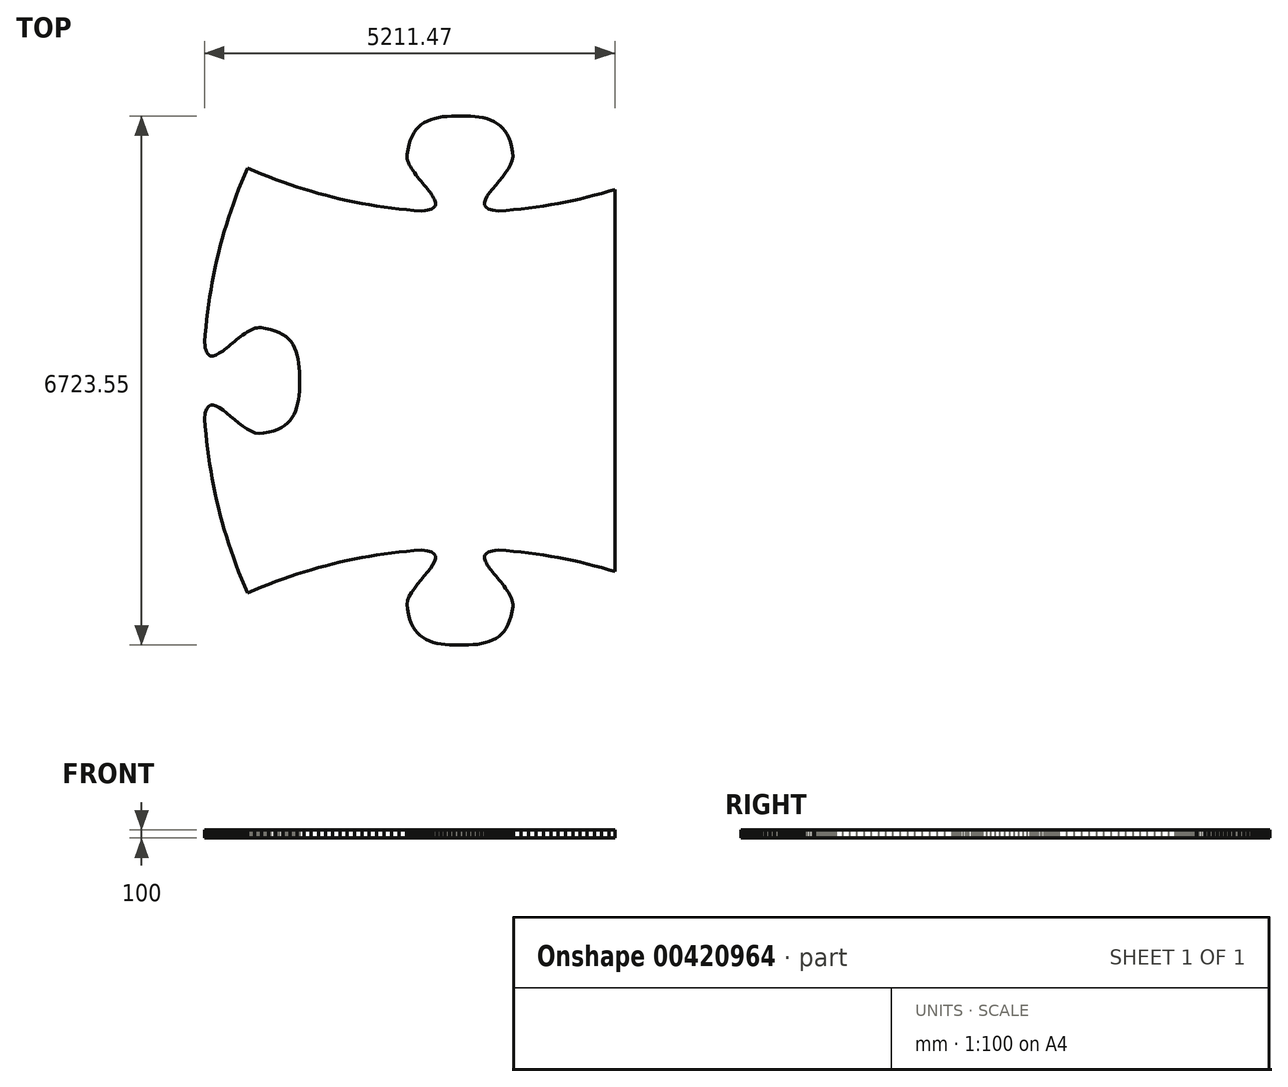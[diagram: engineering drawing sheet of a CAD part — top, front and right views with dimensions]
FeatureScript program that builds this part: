
annotation { "Feature Type Name" : "Feature", "Feature Type Description" : "" }
export const myFeature = defineFeature(function(context is Context, id is Id, definition is map)
    precondition{}
    {
        {
            var Q0;
            Q0=qCreatedBy(makeId("Top.planeOp"),FACE);
            var sketch = newSketch(context, id + "F0", { "sketchPlane" : qUnion([Q0])});
            skLineSegment(sketch, "E0", {"start": v(-1670.47, -7506.33) * mm, "end": v(-1710.93, -7498.83) * mm});
            skLineSegment(sketch, "E1", {"start": v(-1710.93, -7498.83) * mm, "end": v(-1764.8, -7491.94) * mm});
            skLineSegment(sketch, "E2", {"start": v(-1764.8, -7491.94) * mm, "end": v(-1821.32, -7487.35) * mm});
            skLineSegment(sketch, "E3", {"start": v(-1821.32, -7487.35) * mm, "end": v(-1880.41, -7484.72) * mm});
            skLineSegment(sketch, "E4", {"start": v(-1880.41, -7484.72) * mm, "end": v(-1941.99, -7483.74) * mm});
            skLineSegment(sketch, "E5", {"start": v(-1941.99, -7483.74) * mm, "end": v(-2004.44, -7484.15) * mm});
            skLineSegment(sketch, "E6", {"start": v(-2004.44, -7484.15) * mm, "end": v(-2064.53, -7486.08) * mm});
            skLineSegment(sketch, "E7", {"start": v(-2064.53, -7486.08) * mm, "end": v(-2122.08, -7489.85) * mm});
            skLineSegment(sketch, "E8", {"start": v(-2122.08, -7489.85) * mm, "end": v(-2177, -7495.78) * mm});
            skLineSegment(sketch, "E9", {"start": v(-2177, -7495.78) * mm, "end": v(-2229.24, -7504.19) * mm});
            skLineSegment(sketch, "E10", {"start": v(-2229.24, -7504.19) * mm, "end": v(-2278.7, -7515.4) * mm});
            skLineSegment(sketch, "E11", {"start": v(-2278.7, -7515.4) * mm, "end": v(-2325.3, -7529.72) * mm});
            skLineSegment(sketch, "E12", {"start": v(-2325.3, -7529.72) * mm, "end": v(-2368.99, -7547.48) * mm});
            skLineSegment(sketch, "E13", {"start": v(-2368.99, -7547.48) * mm, "end": v(-2409.66, -7568.99) * mm});
            skLineSegment(sketch, "E14", {"start": v(-2409.66, -7568.99) * mm, "end": v(-2447.25, -7594.57) * mm});
            skLineSegment(sketch, "E15", {"start": v(-2447.25, -7594.57) * mm, "end": v(-2481.68, -7624.55) * mm});
            skLineSegment(sketch, "E16", {"start": v(-2481.68, -7624.55) * mm, "end": v(-2512.86, -7659.24) * mm});
            skLineSegment(sketch, "E17", {"start": v(-2512.86, -7659.24) * mm, "end": v(-2540.73, -7698.95) * mm});
            skLineSegment(sketch, "E18", {"start": v(-2540.73, -7698.95) * mm, "end": v(-2565.2, -7744.01) * mm});
            skLineSegment(sketch, "E19", {"start": v(-2565.2, -7744.01) * mm, "end": v(-2586.21, -7794.75) * mm});
            skLineSegment(sketch, "E20", {"start": v(-2586.21, -7794.75) * mm, "end": v(-2603.67, -7851.46) * mm});
            skLineSegment(sketch, "E21", {"start": v(-2603.67, -7851.46) * mm, "end": v(-2617.5, -7914.48) * mm});
            skLineSegment(sketch, "E22", {"start": v(-2617.5, -7914.48) * mm, "end": v(-2626.4, -7974.43) * mm});
            skLineSegment(sketch, "E23", {"start": v(-2626.4, -7974.43) * mm, "end": v(-2626.92, -7998.7) * mm});
            skLineSegment(sketch, "E24", {"start": v(-2626.92, -7998.7) * mm, "end": v(-2624.12, -8023.51) * mm});
            skLineSegment(sketch, "E25", {"start": v(-2624.12, -8023.51) * mm, "end": v(-2618.27, -8048.78) * mm});
            skLineSegment(sketch, "E26", {"start": v(-2618.27, -8048.78) * mm, "end": v(-2609.65, -8074.45) * mm});
            skLineSegment(sketch, "E27", {"start": v(-2609.65, -8074.45) * mm, "end": v(-2598.53, -8100.44) * mm});
            skLineSegment(sketch, "E28", {"start": v(-2598.53, -8100.44) * mm, "end": v(-2585.17, -8126.69) * mm});
            skLineSegment(sketch, "E29", {"start": v(-2585.17, -8126.69) * mm, "end": v(-2569.85, -8153.13) * mm});
            skLineSegment(sketch, "E30", {"start": v(-2569.85, -8153.13) * mm, "end": v(-2552.84, -8179.69) * mm});
            skLineSegment(sketch, "E31", {"start": v(-2552.84, -8179.69) * mm, "end": v(-2534.4, -8206.3) * mm});
            skLineSegment(sketch, "E32", {"start": v(-2534.4, -8206.3) * mm, "end": v(-2514.82, -8232.9) * mm});
            skLineSegment(sketch, "E33", {"start": v(-2514.82, -8232.9) * mm, "end": v(-2494.35, -8259.4) * mm});
            skLineSegment(sketch, "E34", {"start": v(-2494.35, -8259.4) * mm, "end": v(-2473.27, -8285.76) * mm});
            skLineSegment(sketch, "E35", {"start": v(-2473.27, -8285.76) * mm, "end": v(-2451.84, -8311.9) * mm});
            skLineSegment(sketch, "E36", {"start": v(-2451.84, -8311.9) * mm, "end": v(-2430.34, -8337.75) * mm});
            skLineSegment(sketch, "E37", {"start": v(-2430.34, -8337.75) * mm, "end": v(-2409.04, -8363.24) * mm});
            skLineSegment(sketch, "E38", {"start": v(-2409.04, -8363.24) * mm, "end": v(-2388.21, -8388.3) * mm});
            skLineSegment(sketch, "E39", {"start": v(-2388.21, -8388.3) * mm, "end": v(-2368.12, -8412.86) * mm});
            skLineSegment(sketch, "E40", {"start": v(-2368.12, -8412.86) * mm, "end": v(-2349.03, -8436.87) * mm});
            skLineSegment(sketch, "E41", {"start": v(-2349.03, -8436.87) * mm, "end": v(-2331.22, -8460.23) * mm});
            skLineSegment(sketch, "E42", {"start": v(-2331.22, -8460.23) * mm, "end": v(-2314.96, -8482.9) * mm});
            skLineSegment(sketch, "E43", {"start": v(-2314.96, -8482.9) * mm, "end": v(-2300.52, -8504.8) * mm});
            skLineSegment(sketch, "E44", {"start": v(-2300.52, -8504.8) * mm, "end": v(-2288.17, -8525.86) * mm});
            skLineSegment(sketch, "E45", {"start": v(-2288.17, -8525.86) * mm, "end": v(-2278.17, -8546.02) * mm});
            skLineSegment(sketch, "E46", {"start": v(-2278.17, -8546.02) * mm, "end": v(-2270.8, -8565.2) * mm});
            skLineSegment(sketch, "E47", {"start": v(-2270.8, -8565.2) * mm, "end": v(-2266.34, -8583.33) * mm});
            skLineSegment(sketch, "E48", {"start": v(-2266.34, -8583.33) * mm, "end": v(-2265.04, -8600.36) * mm});
            skLineSegment(sketch, "E49", {"start": v(-2265.04, -8600.36) * mm, "end": v(-2267.18, -8616.2) * mm});
            skLineSegment(sketch, "E50", {"start": v(-2267.18, -8616.2) * mm, "end": v(-2273.03, -8630.8) * mm});
            skLineSegment(sketch, "E51", {"start": v(-2273.03, -8630.8) * mm, "end": v(-2282.86, -8644.07) * mm});
            skLineSegment(sketch, "E52", {"start": v(-2282.86, -8644.07) * mm, "end": v(-2296.94, -8655.96) * mm});
            skLineSegment(sketch, "E53", {"start": v(-2296.94, -8655.96) * mm, "end": v(-2315.54, -8666.4) * mm});
            skLineSegment(sketch, "E54", {"start": v(-2315.54, -8666.4) * mm, "end": v(-2338.93, -8675.31) * mm});
            skLineSegment(sketch, "E55", {"start": v(-2338.93, -8675.31) * mm, "end": v(-2367.38, -8682.63) * mm});
            skLineSegment(sketch, "E56", {"start": v(-2367.38, -8682.63) * mm, "end": v(-2401.15, -8688.3) * mm});
            skLineSegment(sketch, "E57", {"start": v(-2401.15, -8688.3) * mm, "end": v(-2440.53, -8692.23) * mm});
            skLineSegment(sketch, "E58", {"start": v(1692.6, -7812.46) * mm, "end": v(1735.9, -7800.77) * mm});
            skLineSegment(sketch, "E59", {"start": v(1735.9, -7800.77) * mm, "end": v(1827.3, -7777.51) * mm});
            skLineSegment(sketch, "E60", {"start": v(1827.3, -7777.51) * mm, "end": v(1919.05, -7755.6) * mm});
            skLineSegment(sketch, "E61", {"start": v(1919.05, -7755.6) * mm, "end": v(2011.14, -7735) * mm});
            skLineSegment(sketch, "E62", {"start": v(2011.14, -7735) * mm, "end": v(2103.62, -7715.73) * mm});
            skLineSegment(sketch, "E63", {"start": v(2103.62, -7715.73) * mm, "end": v(2196.5, -7697.78) * mm});
            skLineSegment(sketch, "E64", {"start": v(2196.5, -7697.78) * mm, "end": v(2289.83, -7681.14) * mm});
            skLineSegment(sketch, "E65", {"start": v(2289.83, -7681.14) * mm, "end": v(2383.6, -7665.8) * mm});
            skLineSegment(sketch, "E66", {"start": v(2383.6, -7665.8) * mm, "end": v(2477.88, -7651.75) * mm});
            skLineSegment(sketch, "E67", {"start": v(2477.88, -7651.75) * mm, "end": v(2572.66, -7639) * mm});
            skLineSegment(sketch, "E68", {"start": v(2572.66, -7639) * mm, "end": v(2667.99, -7627.53) * mm});
            skLineSegment(sketch, "E69", {"start": v(2667.99, -7627.53) * mm, "end": v(2763.88, -7617.33) * mm});
            skLineSegment(sketch, "E70", {"start": v(2763.88, -7617.33) * mm, "end": v(2860.36, -7608.4) * mm});
            skLineSegment(sketch, "E71", {"start": v(2860.36, -7608.4) * mm, "end": v(2957.46, -7600.75) * mm});
            skLineSegment(sketch, "E72", {"start": v(-1468.4, -12998.74) * mm, "end": v(-1371.3, -13006.4) * mm});
            skLineSegment(sketch, "E73", {"start": v(-1371.3, -13006.4) * mm, "end": v(-1274.82, -13015.32) * mm});
            skLineSegment(sketch, "E74", {"start": v(-1274.82, -13015.32) * mm, "end": v(-1193.26, -13024) * mm});
            skLineSegment(sketch, "E75", {"start": v(382.53, -13398.19) * mm, "end": v(386.12, -13399.5) * mm});
            skLineSegment(sketch, "E76", {"start": v(386.12, -13399.5) * mm, "end": v(475.85, -13433.68) * mm});
            skLineSegment(sketch, "E77", {"start": v(475.85, -13433.68) * mm, "end": v(565.5, -13469.25) * mm});
            skLineSegment(sketch, "E78", {"start": v(565.5, -13469.25) * mm, "end": v(655.08, -13506.22) * mm});
            skLineSegment(sketch, "E79", {"start": v(655.08, -13506.22) * mm, "end": v(744.62, -13544.6) * mm});
            skLineSegment(sketch, "E80", {"start": v(-1670.47, 3289.71) * mm, "end": v(-1710.93, 3297.22) * mm});
            skLineSegment(sketch, "E81", {"start": v(-1710.93, 3297.22) * mm, "end": v(-1764.8, 3304.1) * mm});
            skLineSegment(sketch, "E82", {"start": v(-1764.8, 3304.1) * mm, "end": v(-1821.32, 3308.7) * mm});
            skLineSegment(sketch, "E83", {"start": v(-1821.32, 3308.7) * mm, "end": v(-1880.41, 3311.32) * mm});
            skLineSegment(sketch, "E84", {"start": v(-1880.41, 3311.32) * mm, "end": v(-1941.99, 3312.3) * mm});
            skLineSegment(sketch, "E85", {"start": v(-1941.99, 3312.3) * mm, "end": v(-2004.44, 3311.9) * mm});
            skLineSegment(sketch, "E86", {"start": v(-2004.44, 3311.9) * mm, "end": v(-2064.53, 3309.97) * mm});
            skLineSegment(sketch, "E87", {"start": v(-2064.53, 3309.97) * mm, "end": v(-2122.08, 3306.2) * mm});
            skLineSegment(sketch, "E88", {"start": v(-2122.08, 3306.2) * mm, "end": v(-2177, 3300.26) * mm});
            skLineSegment(sketch, "E89", {"start": v(-2177, 3300.26) * mm, "end": v(-2229.24, 3291.85) * mm});
            skLineSegment(sketch, "E90", {"start": v(-2229.24, 3291.85) * mm, "end": v(-2278.7, 3280.64) * mm});
            skLineSegment(sketch, "E91", {"start": v(-2278.7, 3280.64) * mm, "end": v(-2325.3, 3266.32) * mm});
            skLineSegment(sketch, "E92", {"start": v(-2325.3, 3266.32) * mm, "end": v(-2368.99, 3248.56) * mm});
            skLineSegment(sketch, "E93", {"start": v(-2368.99, 3248.56) * mm, "end": v(-2409.66, 3227.05) * mm});
            skLineSegment(sketch, "E94", {"start": v(-2409.66, 3227.05) * mm, "end": v(-2447.25, 3201.46) * mm});
            skLineSegment(sketch, "E95", {"start": v(-2447.25, 3201.46) * mm, "end": v(-2481.68, 3171.48) * mm});
            skLineSegment(sketch, "E96", {"start": v(-2481.68, 3171.48) * mm, "end": v(-2512.86, 3136.79) * mm});
            skLineSegment(sketch, "E97", {"start": v(-2512.86, 3136.79) * mm, "end": v(-2540.73, 3097.07) * mm});
            skLineSegment(sketch, "E98", {"start": v(-2540.73, 3097.07) * mm, "end": v(-2565.2, 3052) * mm});
            skLineSegment(sketch, "E99", {"start": v(-2565.2, 3052) * mm, "end": v(-2586.21, 3001.26) * mm});
            skLineSegment(sketch, "E100", {"start": v(-2586.21, 3001.26) * mm, "end": v(-2603.67, 2944.54) * mm});
            skLineSegment(sketch, "E101", {"start": v(-2603.67, 2944.54) * mm, "end": v(-2617.5, 2881.5) * mm});
            skLineSegment(sketch, "E102", {"start": v(-2617.5, 2881.5) * mm, "end": v(-2626.4, 2821.55) * mm});
            skLineSegment(sketch, "E103", {"start": v(-2626.4, 2821.55) * mm, "end": v(-2626.92, 2797.29) * mm});
            skLineSegment(sketch, "E104", {"start": v(-2626.92, 2797.29) * mm, "end": v(-2624.12, 2772.5) * mm});
            skLineSegment(sketch, "E105", {"start": v(-2624.12, 2772.5) * mm, "end": v(-2618.27, 2747.24) * mm});
            skLineSegment(sketch, "E106", {"start": v(-2618.27, 2747.24) * mm, "end": v(-2609.65, 2721.58) * mm});
            skLineSegment(sketch, "E107", {"start": v(-2609.65, 2721.58) * mm, "end": v(-2598.53, 2695.6) * mm});
            skLineSegment(sketch, "E108", {"start": v(-2598.53, 2695.6) * mm, "end": v(-2585.17, 2669.36) * mm});
            skLineSegment(sketch, "E109", {"start": v(-2585.17, 2669.36) * mm, "end": v(-2569.85, 2642.93) * mm});
            skLineSegment(sketch, "E110", {"start": v(-2569.85, 2642.93) * mm, "end": v(-2552.84, 2616.37) * mm});
            skLineSegment(sketch, "E111", {"start": v(-2552.84, 2616.37) * mm, "end": v(-2534.4, 2589.76) * mm});
            skLineSegment(sketch, "E112", {"start": v(-2534.4, 2589.76) * mm, "end": v(-2514.82, 2563.17) * mm});
            skLineSegment(sketch, "E113", {"start": v(-2514.82, 2563.17) * mm, "end": v(-2494.35, 2536.66) * mm});
            skLineSegment(sketch, "E114", {"start": v(-2494.35, 2536.66) * mm, "end": v(-2473.27, 2510.3) * mm});
            skLineSegment(sketch, "E115", {"start": v(-2473.27, 2510.3) * mm, "end": v(-2451.84, 2484.16) * mm});
            skLineSegment(sketch, "E116", {"start": v(-2451.84, 2484.16) * mm, "end": v(-2430.34, 2458.31) * mm});
            skLineSegment(sketch, "E117", {"start": v(-2430.34, 2458.31) * mm, "end": v(-2409.04, 2432.82) * mm});
            skLineSegment(sketch, "E118", {"start": v(-2409.04, 2432.82) * mm, "end": v(-2388.21, 2407.76) * mm});
            skLineSegment(sketch, "E119", {"start": v(-2388.21, 2407.76) * mm, "end": v(-2368.12, 2383.19) * mm});
            skLineSegment(sketch, "E120", {"start": v(-2368.12, 2383.19) * mm, "end": v(-2349.03, 2359.18) * mm});
            skLineSegment(sketch, "E121", {"start": v(-2349.03, 2359.18) * mm, "end": v(-2331.22, 2335.8) * mm});
            skLineSegment(sketch, "E122", {"start": v(-2331.22, 2335.8) * mm, "end": v(-2314.96, 2313.14) * mm});
            skLineSegment(sketch, "E123", {"start": v(-2314.96, 2313.14) * mm, "end": v(-2300.52, 2291.23) * mm});
            skLineSegment(sketch, "E124", {"start": v(-2300.52, 2291.23) * mm, "end": v(-2288.17, 2270.17) * mm});
            skLineSegment(sketch, "E125", {"start": v(-2288.17, 2270.17) * mm, "end": v(-2278.17, 2250) * mm});
            skLineSegment(sketch, "E126", {"start": v(-2278.17, 2250) * mm, "end": v(-2270.8, 2230.82) * mm});
            skLineSegment(sketch, "E127", {"start": v(-2270.8, 2230.82) * mm, "end": v(-2266.34, 2212.68) * mm});
            skLineSegment(sketch, "E128", {"start": v(-2266.34, 2212.68) * mm, "end": v(-2265.04, 2195.65) * mm});
            skLineSegment(sketch, "E129", {"start": v(-2265.04, 2195.65) * mm, "end": v(-2267.18, 2179.8) * mm});
            skLineSegment(sketch, "E130", {"start": v(-2267.18, 2179.8) * mm, "end": v(-2273.03, 2165.2) * mm});
            skLineSegment(sketch, "E131", {"start": v(-2273.03, 2165.2) * mm, "end": v(-2282.86, 2151.92) * mm});
            skLineSegment(sketch, "E132", {"start": v(-2282.86, 2151.92) * mm, "end": v(-2296.94, 2140.03) * mm});
            skLineSegment(sketch, "E133", {"start": v(-2296.94, 2140.03) * mm, "end": v(-2315.54, 2129.59) * mm});
            skLineSegment(sketch, "E134", {"start": v(-2315.54, 2129.59) * mm, "end": v(-2338.93, 2120.67) * mm});
            skLineSegment(sketch, "E135", {"start": v(-2338.93, 2120.67) * mm, "end": v(-2367.38, 2113.35) * mm});
            skLineSegment(sketch, "E136", {"start": v(-2367.38, 2113.35) * mm, "end": v(-2401.15, 2107.68) * mm});
            skLineSegment(sketch, "E137", {"start": v(-2401.15, 2107.68) * mm, "end": v(-2440.53, 2103.75) * mm});
            skLineSegment(sketch, "E138", {"start": v(-2440.53, 2103.75) * mm, "end": v(-2537.63, 2111.41) * mm});
            skLineSegment(sketch, "E139", {"start": v(-2537.63, 2111.41) * mm, "end": v(-2634.11, 2120.34) * mm});
            skLineSegment(sketch, "E140", {"start": v(-2634.11, 2120.34) * mm, "end": v(-2730, 2130.54) * mm});
            skLineSegment(sketch, "E141", {"start": v(-2730, 2130.54) * mm, "end": v(-2825.33, 2142.02) * mm});
            skLineSegment(sketch, "E142", {"start": v(-2825.33, 2142.02) * mm, "end": v(-2920.11, 2154.78) * mm});
            skLineSegment(sketch, "E143", {"start": v(-2920.11, 2154.78) * mm, "end": v(-3014.38, 2168.83) * mm});
            skLineSegment(sketch, "E144", {"start": v(-3014.38, 2168.83) * mm, "end": v(-3108.17, 2184.18) * mm});
            skLineSegment(sketch, "E145", {"start": v(-3108.17, 2184.18) * mm, "end": v(-3201.5, 2200.83) * mm});
            skLineSegment(sketch, "E146", {"start": v(-3201.5, 2200.83) * mm, "end": v(-3294.38, 2218.79) * mm});
            skLineSegment(sketch, "E147", {"start": v(-3294.38, 2218.79) * mm, "end": v(-3386.86, 2238.06) * mm});
            skLineSegment(sketch, "E148", {"start": v(-3386.86, 2238.06) * mm, "end": v(-3478.96, 2258.66) * mm});
            skLineSegment(sketch, "E149", {"start": v(-3478.96, 2258.66) * mm, "end": v(-3570.7, 2280.59) * mm});
            skLineSegment(sketch, "E150", {"start": v(-3570.7, 2280.59) * mm, "end": v(-3662.12, 2303.85) * mm});
            skLineSegment(sketch, "E151", {"start": v(-3662.12, 2303.85) * mm, "end": v(-3753.24, 2328.45) * mm});
            skLineSegment(sketch, "E152", {"start": v(-3753.24, 2328.45) * mm, "end": v(-3844.08, 2354.4) * mm});
            skLineSegment(sketch, "E153", {"start": v(-3844.08, 2354.4) * mm, "end": v(-3934.66, 2381.7) * mm});
            skLineSegment(sketch, "E154", {"start": v(-3934.66, 2381.7) * mm, "end": v(-4025.03, 2410.37) * mm});
            skLineSegment(sketch, "E155", {"start": v(-4025.03, 2410.37) * mm, "end": v(-4115.2, 2440.4) * mm});
            skLineSegment(sketch, "E156", {"start": v(-4115.2, 2440.4) * mm, "end": v(-4205.2, 2471.8) * mm});
            skLineSegment(sketch, "E157", {"start": v(-4205.2, 2471.8) * mm, "end": v(-4295.05, 2504.58) * mm});
            skLineSegment(sketch, "E158", {"start": v(-4295.05, 2504.58) * mm, "end": v(-4384.79, 2538.75) * mm});
            skLineSegment(sketch, "E159", {"start": v(-4384.79, 2538.75) * mm, "end": v(-4474.44, 2574.3) * mm});
            skLineSegment(sketch, "E160", {"start": v(-4474.44, 2574.3) * mm, "end": v(-4564.02, 2611.26) * mm});
            skLineSegment(sketch, "E161", {"start": v(-4564.02, 2611.26) * mm, "end": v(-4653.56, 2649.62) * mm});
            skLineSegment(sketch, "E162", {"start": v(-4653.56, 2649.62) * mm, "end": v(-4691.92, 2560.08) * mm});
            skLineSegment(sketch, "E163", {"start": v(-4691.92, 2560.08) * mm, "end": v(-4728.87, 2470.5) * mm});
            skLineSegment(sketch, "E164", {"start": v(-4728.87, 2470.5) * mm, "end": v(-4764.42, 2380.86) * mm});
            skLineSegment(sketch, "E165", {"start": v(-4764.42, 2380.86) * mm, "end": v(-4798.58, 2291.13) * mm});
            skLineSegment(sketch, "E166", {"start": v(-4798.58, 2291.13) * mm, "end": v(-4831.36, 2201.28) * mm});
            skLineSegment(sketch, "E167", {"start": v(-4831.36, 2201.28) * mm, "end": v(-4862.75, 2111.29) * mm});
            skLineSegment(sketch, "E168", {"start": v(-4862.75, 2111.29) * mm, "end": v(-4892.77, 2021.13) * mm});
            skLineSegment(sketch, "E169", {"start": v(-4892.77, 2021.13) * mm, "end": v(-4921.42, 1930.77) * mm});
            skLineSegment(sketch, "E170", {"start": v(-4921.42, 1930.77) * mm, "end": v(-4948.72, 1840.19) * mm});
            skLineSegment(sketch, "E171", {"start": v(-4948.72, 1840.19) * mm, "end": v(-4974.65, 1749.36) * mm});
            skLineSegment(sketch, "E172", {"start": v(-4974.65, 1749.36) * mm, "end": v(-4999.24, 1658.25) * mm});
            skLineSegment(sketch, "E173", {"start": v(-4999.24, 1658.25) * mm, "end": v(-5022.5, 1566.84) * mm});
            skLineSegment(sketch, "E174", {"start": v(-5022.5, 1566.84) * mm, "end": v(-5044.4, 1475.1) * mm});
            skLineSegment(sketch, "E175", {"start": v(-5044.4, 1475.1) * mm, "end": v(-5065, 1383) * mm});
            skLineSegment(sketch, "E176", {"start": v(-5065, 1383) * mm, "end": v(-5084.26, 1290.53) * mm});
            skLineSegment(sketch, "E177", {"start": v(-5084.26, 1290.53) * mm, "end": v(-5102.2, 1197.64) * mm});
            skLineSegment(sketch, "E178", {"start": v(-5102.2, 1197.64) * mm, "end": v(-5118.85, 1104.31) * mm});
            skLineSegment(sketch, "E179", {"start": v(-5118.85, 1104.31) * mm, "end": v(-5134.19, 1010.53) * mm});
            skLineSegment(sketch, "E180", {"start": v(-5134.19, 1010.53) * mm, "end": v(-5148.23, 916.25) * mm});
            skLineSegment(sketch, "E181", {"start": v(-5148.23, 916.25) * mm, "end": v(-5160.98, 821.46) * mm});
            skLineSegment(sketch, "E182", {"start": v(-5160.98, 821.46) * mm, "end": v(-5172.45, 726.12) * mm});
            skLineSegment(sketch, "E183", {"start": v(-5172.45, 726.12) * mm, "end": v(-5182.65, 630.22) * mm});
            skLineSegment(sketch, "E184", {"start": v(-5182.65, 630.22) * mm, "end": v(-5191.57, 533.71) * mm});
            skLineSegment(sketch, "E185", {"start": v(-5191.57, 533.71) * mm, "end": v(-5199.24, 436.6) * mm});
            skLineSegment(sketch, "E186", {"start": v(-5199.24, 436.6) * mm, "end": v(-5189.63, 363.44) * mm});
            skLineSegment(sketch, "E187", {"start": v(-5189.63, 363.44) * mm, "end": v(-5173.39, 311.6) * mm});
            skLineSegment(sketch, "E188", {"start": v(-5173.39, 311.6) * mm, "end": v(-5151.06, 278.94) * mm});
            skLineSegment(sketch, "E189", {"start": v(-5151.06, 278.94) * mm, "end": v(-5123.18, 263.27) * mm});
            skLineSegment(sketch, "E190", {"start": v(-5123.18, 263.27) * mm, "end": v(-5090.31, 262.43) * mm});
            skLineSegment(sketch, "E191", {"start": v(-5090.31, 262.43) * mm, "end": v(-5053, 274.28) * mm});
            skLineSegment(sketch, "E192", {"start": v(-5053, 274.28) * mm, "end": v(-5011.78, 296.63) * mm});
            skLineSegment(sketch, "E193", {"start": v(-5011.78, 296.63) * mm, "end": v(-4967.22, 327.34) * mm});
            skLineSegment(sketch, "E194", {"start": v(-4967.22, 327.34) * mm, "end": v(-4919.85, 364.24) * mm});
            skLineSegment(sketch, "E195", {"start": v(-4919.85, 364.24) * mm, "end": v(-4870.22, 405.17) * mm});
            skLineSegment(sketch, "E196", {"start": v(-4870.22, 405.17) * mm, "end": v(-4818.9, 447.97) * mm});
            skLineSegment(sketch, "E197", {"start": v(-4818.9, 447.97) * mm, "end": v(-4766.4, 490.48) * mm});
            skLineSegment(sketch, "E198", {"start": v(-4766.4, 490.48) * mm, "end": v(-4713.3, 530.53) * mm});
            skLineSegment(sketch, "E199", {"start": v(-4713.3, 530.53) * mm, "end": v(-4660.13, 565.96) * mm});
            skLineSegment(sketch, "E200", {"start": v(-4660.13, 565.96) * mm, "end": v(-4607.44, 594.61) * mm});
            skLineSegment(sketch, "E201", {"start": v(-4607.44, 594.61) * mm, "end": v(-4555.79, 614.33) * mm});
            skLineSegment(sketch, "E202", {"start": v(-4555.79, 614.33) * mm, "end": v(-4505.71, 622.94) * mm});
            skLineSegment(sketch, "E203", {"start": v(-4505.71, 622.94) * mm, "end": v(-4448.53, 618) * mm});
            skLineSegment(sketch, "E204", {"start": v(-4448.53, 618) * mm, "end": v(-4382.89, 605.67) * mm});
            skLineSegment(sketch, "E205", {"start": v(-4382.89, 605.67) * mm, "end": v(-4323.68, 589.68) * mm});
            skLineSegment(sketch, "E206", {"start": v(-4323.68, 589.68) * mm, "end": v(-4270.59, 570.1) * mm});
            skLineSegment(sketch, "E207", {"start": v(-4270.59, 570.1) * mm, "end": v(-4223.29, 547.01) * mm});
            skLineSegment(sketch, "E208", {"start": v(-4223.29, 547.01) * mm, "end": v(-4181.46, 520.5) * mm});
            skLineSegment(sketch, "E209", {"start": v(-4181.46, 520.5) * mm, "end": v(-4144.8, 490.63) * mm});
            skLineSegment(sketch, "E210", {"start": v(-4144.8, 490.63) * mm, "end": v(-4112.97, 457.48) * mm});
            skLineSegment(sketch, "E211", {"start": v(-4112.97, 457.48) * mm, "end": v(-4085.67, 421.14) * mm});
            skLineSegment(sketch, "E212", {"start": v(-4085.67, 421.14) * mm, "end": v(-4062.56, 381.68) * mm});
            skLineSegment(sketch, "E213", {"start": v(-4062.56, 381.68) * mm, "end": v(-4043.34, 339.19) * mm});
            skLineSegment(sketch, "E214", {"start": v(-4043.34, 339.19) * mm, "end": v(-4027.68, 293.73) * mm});
            skLineSegment(sketch, "E215", {"start": v(-4027.68, 293.73) * mm, "end": v(-4015.26, 245.4) * mm});
            skLineSegment(sketch, "E216", {"start": v(-4015.26, 245.4) * mm, "end": v(-4005.77, 194.25) * mm});
            skLineSegment(sketch, "E217", {"start": v(-4005.77, 194.25) * mm, "end": v(-3998.89, 140.38) * mm});
            skLineSegment(sketch, "E218", {"start": v(-3998.89, 140.38) * mm, "end": v(-3994.29, 83.86) * mm});
            skLineSegment(sketch, "E219", {"start": v(-3994.29, 83.86) * mm, "end": v(-3991.66, 24.78) * mm});
            skLineSegment(sketch, "E220", {"start": v(-3991.66, 24.78) * mm, "end": v(-3990.68, -36.8) * mm});
            skLineSegment(sketch, "E221", {"start": v(-3990.68, -36.8) * mm, "end": v(-3991.09, -99.26) * mm});
            skLineSegment(sketch, "E222", {"start": v(-3991.09, -99.26) * mm, "end": v(-3993.02, -159.35) * mm});
            skLineSegment(sketch, "E223", {"start": v(-3993.02, -159.35) * mm, "end": v(-3996.8, -216.9) * mm});
            skLineSegment(sketch, "E224", {"start": v(-3996.8, -216.9) * mm, "end": v(-4002.72, -271.84) * mm});
            skLineSegment(sketch, "E225", {"start": v(-4002.72, -271.84) * mm, "end": v(-4011.13, -324.09) * mm});
            skLineSegment(sketch, "E226", {"start": v(-4011.13, -324.09) * mm, "end": v(-4022.34, -373.56) * mm});
            skLineSegment(sketch, "E227", {"start": v(-4022.34, -373.56) * mm, "end": v(-4036.66, -420.18) * mm});
            skLineSegment(sketch, "E228", {"start": v(-4036.66, -420.18) * mm, "end": v(-4054.42, -463.88) * mm});
            skLineSegment(sketch, "E229", {"start": v(-4054.42, -463.88) * mm, "end": v(-4075.94, -504.57) * mm});
            skLineSegment(sketch, "E230", {"start": v(-4075.94, -504.57) * mm, "end": v(-4101.53, -542.17) * mm});
            skLineSegment(sketch, "E231", {"start": v(-4101.53, -542.17) * mm, "end": v(-4131.5, -576.62) * mm});
            skLineSegment(sketch, "E232", {"start": v(-4131.5, -576.62) * mm, "end": v(-4166.2, -607.82) * mm});
            skLineSegment(sketch, "E233", {"start": v(-4166.2, -607.82) * mm, "end": v(-4205.92, -635.7) * mm});
            skLineSegment(sketch, "E234", {"start": v(-4205.92, -635.7) * mm, "end": v(-4250.99, -660.2) * mm});
            skLineSegment(sketch, "E235", {"start": v(-4250.99, -660.2) * mm, "end": v(-4301.73, -681.2) * mm});
            skLineSegment(sketch, "E236", {"start": v(-4301.73, -681.2) * mm, "end": v(-4358.45, -698.66) * mm});
            skLineSegment(sketch, "E237", {"start": v(-4358.45, -698.66) * mm, "end": v(-4421.48, -712.5) * mm});
            skLineSegment(sketch, "E238", {"start": v(-4421.48, -712.5) * mm, "end": v(-4481.44, -721.41) * mm});
            skLineSegment(sketch, "E239", {"start": v(-4481.44, -721.41) * mm, "end": v(-4505.71, -721.93) * mm});
            skLineSegment(sketch, "E240", {"start": v(-4505.71, -721.93) * mm, "end": v(-4530.52, -719.13) * mm});
            skLineSegment(sketch, "E241", {"start": v(-4530.52, -719.13) * mm, "end": v(-4555.79, -713.29) * mm});
            skLineSegment(sketch, "E242", {"start": v(-4555.79, -713.29) * mm, "end": v(-4581.45, -704.67) * mm});
            skLineSegment(sketch, "E243", {"start": v(-4581.45, -704.67) * mm, "end": v(-4607.44, -693.55) * mm});
            skLineSegment(sketch, "E244", {"start": v(-4607.44, -693.55) * mm, "end": v(-4633.69, -680.2) * mm});
            skLineSegment(sketch, "E245", {"start": v(-4633.69, -680.2) * mm, "end": v(-4660.13, -664.87) * mm});
            skLineSegment(sketch, "E246", {"start": v(-4660.13, -664.87) * mm, "end": v(-4686.68, -647.86) * mm});
            skLineSegment(sketch, "E247", {"start": v(-4686.68, -647.86) * mm, "end": v(-4713.3, -629.42) * mm});
            skLineSegment(sketch, "E248", {"start": v(-4713.3, -629.42) * mm, "end": v(-4739.89, -609.83) * mm});
            skLineSegment(sketch, "E249", {"start": v(-4739.89, -609.83) * mm, "end": v(-4766.4, -589.36) * mm});
            skLineSegment(sketch, "E250", {"start": v(-4766.4, -589.36) * mm, "end": v(-4792.76, -568.27) * mm});
            skLineSegment(sketch, "E251", {"start": v(-4792.76, -568.27) * mm, "end": v(-4818.9, -546.84) * mm});
            skLineSegment(sketch, "E252", {"start": v(-4818.9, -546.84) * mm, "end": v(-4844.74, -525.34) * mm});
            skLineSegment(sketch, "E253", {"start": v(-4844.74, -525.34) * mm, "end": v(-4870.22, -504.04) * mm});
            skLineSegment(sketch, "E254", {"start": v(-4870.22, -504.04) * mm, "end": v(-4895.28, -483.2) * mm});
            skLineSegment(sketch, "E255", {"start": v(-4895.28, -483.2) * mm, "end": v(-4919.85, -463.1) * mm});
            skLineSegment(sketch, "E256", {"start": v(-4919.85, -463.1) * mm, "end": v(-4943.85, -444.02) * mm});
            skLineSegment(sketch, "E257", {"start": v(-4943.85, -444.02) * mm, "end": v(-4967.22, -426.2) * mm});
            skLineSegment(sketch, "E258", {"start": v(-4967.22, -426.2) * mm, "end": v(-4989.88, -409.94) * mm});
            skLineSegment(sketch, "E259", {"start": v(-4989.88, -409.94) * mm, "end": v(-5011.78, -395.5) * mm});
            skLineSegment(sketch, "E260", {"start": v(-5011.78, -395.5) * mm, "end": v(-5032.84, -383.15) * mm});
            skLineSegment(sketch, "E261", {"start": v(-5032.84, -383.15) * mm, "end": v(-5053, -373.15) * mm});
            skLineSegment(sketch, "E262", {"start": v(-5053, -373.15) * mm, "end": v(-5072.17, -365.79) * mm});
            skLineSegment(sketch, "E263", {"start": v(-5072.17, -365.79) * mm, "end": v(-5090.31, -361.32) * mm});
            skLineSegment(sketch, "E264", {"start": v(-5090.31, -361.32) * mm, "end": v(-5107.34, -360.03) * mm});
            skLineSegment(sketch, "E265", {"start": v(-5107.34, -360.03) * mm, "end": v(-5123.18, -362.17) * mm});
            skLineSegment(sketch, "E266", {"start": v(-5123.18, -362.17) * mm, "end": v(-5137.78, -368.03) * mm});
            skLineSegment(sketch, "E267", {"start": v(-5137.78, -368.03) * mm, "end": v(-5151.06, -377.86) * mm});
            skLineSegment(sketch, "E268", {"start": v(-5151.06, -377.86) * mm, "end": v(-5162.95, -391.95) * mm});
            skLineSegment(sketch, "E269", {"start": v(-5162.95, -391.95) * mm, "end": v(-5173.39, -410.56) * mm});
            skLineSegment(sketch, "E270", {"start": v(-5173.39, -410.56) * mm, "end": v(-5182.3, -433.96) * mm});
            skLineSegment(sketch, "E271", {"start": v(-5182.3, -433.96) * mm, "end": v(-5189.63, -462.42) * mm});
            skLineSegment(sketch, "E272", {"start": v(-5189.63, -462.42) * mm, "end": v(-5195.3, -496.2) * mm});
            skLineSegment(sketch, "E273", {"start": v(-5195.3, -496.2) * mm, "end": v(-5199.24, -535.6) * mm});
            skLineSegment(sketch, "E274", {"start": v(-5199.24, -535.6) * mm, "end": v(-5191.57, -632.7) * mm});
            skLineSegment(sketch, "E275", {"start": v(-5191.57, -632.7) * mm, "end": v(-5182.65, -729.18) * mm});
            skLineSegment(sketch, "E276", {"start": v(-5182.65, -729.18) * mm, "end": v(-5172.45, -825.07) * mm});
            skLineSegment(sketch, "E277", {"start": v(-5172.45, -825.07) * mm, "end": v(-5160.98, -920.4) * mm});
            skLineSegment(sketch, "E278", {"start": v(-5160.98, -920.4) * mm, "end": v(-5148.23, -1015.17) * mm});
            skLineSegment(sketch, "E279", {"start": v(-5148.23, -1015.17) * mm, "end": v(-5134.19, -1109.44) * mm});
            skLineSegment(sketch, "E280", {"start": v(-5134.19, -1109.44) * mm, "end": v(-5118.85, -1203.22) * mm});
            skLineSegment(sketch, "E281", {"start": v(-5118.85, -1203.22) * mm, "end": v(-5102.2, -1296.54) * mm});
            skLineSegment(sketch, "E282", {"start": v(-5102.2, -1296.54) * mm, "end": v(-5084.26, -1389.42) * mm});
            skLineSegment(sketch, "E283", {"start": v(-5084.26, -1389.42) * mm, "end": v(-5065, -1481.9) * mm});
            skLineSegment(sketch, "E284", {"start": v(-5065, -1481.9) * mm, "end": v(-5044.4, -1573.98) * mm});
            skLineSegment(sketch, "E285", {"start": v(-5044.4, -1573.98) * mm, "end": v(-5022.5, -1665.72) * mm});
            skLineSegment(sketch, "E286", {"start": v(-5022.5, -1665.72) * mm, "end": v(-4999.24, -1757.12) * mm});
            skLineSegment(sketch, "E287", {"start": v(-4999.24, -1757.12) * mm, "end": v(-4974.65, -1848.23) * mm});
            skLineSegment(sketch, "E288", {"start": v(-4974.65, -1848.23) * mm, "end": v(-4948.72, -1939.05) * mm});
            skLineSegment(sketch, "E289", {"start": v(-4948.72, -1939.05) * mm, "end": v(-4921.42, -2029.63) * mm});
            skLineSegment(sketch, "E290", {"start": v(-4921.42, -2029.63) * mm, "end": v(-4892.77, -2119.98) * mm});
            skLineSegment(sketch, "E291", {"start": v(-4892.77, -2119.98) * mm, "end": v(-4862.75, -2210.13) * mm});
            skLineSegment(sketch, "E292", {"start": v(-4862.75, -2210.13) * mm, "end": v(-4831.36, -2300.11) * mm});
            skLineSegment(sketch, "E293", {"start": v(-4831.36, -2300.11) * mm, "end": v(-4798.58, -2389.95) * mm});
            skLineSegment(sketch, "E294", {"start": v(-4798.58, -2389.95) * mm, "end": v(-4764.42, -2479.67) * mm});
            skLineSegment(sketch, "E295", {"start": v(-4764.42, -2479.67) * mm, "end": v(-4728.87, -2569.3) * mm});
            skLineSegment(sketch, "E296", {"start": v(-4728.87, -2569.3) * mm, "end": v(-4691.92, -2658.85) * mm});
            skLineSegment(sketch, "E297", {"start": v(-4691.92, -2658.85) * mm, "end": v(-4653.56, -2748.37) * mm});
            skLineSegment(sketch, "E298", {"start": v(-4653.56, -2748.37) * mm, "end": v(-4564.02, -2710.02) * mm});
            skLineSegment(sketch, "E299", {"start": v(-4564.02, -2710.02) * mm, "end": v(-4474.44, -2673.07) * mm});
            skLineSegment(sketch, "E300", {"start": v(-4474.44, -2673.07) * mm, "end": v(-4384.79, -2637.52) * mm});
            skLineSegment(sketch, "E301", {"start": v(-4384.79, -2637.52) * mm, "end": v(-4295.05, -2603.37) * mm});
            skLineSegment(sketch, "E302", {"start": v(-4295.05, -2603.37) * mm, "end": v(-4205.2, -2570.6) * mm});
            skLineSegment(sketch, "E303", {"start": v(-4205.2, -2570.6) * mm, "end": v(-4115.2, -2539.2) * mm});
            skLineSegment(sketch, "E304", {"start": v(-4115.2, -2539.2) * mm, "end": v(-4025.03, -2509.19) * mm});
            skLineSegment(sketch, "E305", {"start": v(-4025.03, -2509.19) * mm, "end": v(-3934.66, -2480.54) * mm});
            skLineSegment(sketch, "E306", {"start": v(-3934.66, -2480.54) * mm, "end": v(-3844.08, -2453.24) * mm});
            skLineSegment(sketch, "E307", {"start": v(-3844.08, -2453.24) * mm, "end": v(-3753.24, -2427.3) * mm});
            skLineSegment(sketch, "E308", {"start": v(-3753.24, -2427.3) * mm, "end": v(-3662.12, -2402.72) * mm});
            skLineSegment(sketch, "E309", {"start": v(-3662.12, -2402.72) * mm, "end": v(-3570.7, -2379.47) * mm});
            skLineSegment(sketch, "E310", {"start": v(-3570.7, -2379.47) * mm, "end": v(-3478.96, -2357.55) * mm});
            skLineSegment(sketch, "E311", {"start": v(-3478.96, -2357.55) * mm, "end": v(-3386.86, -2336.97) * mm});
            skLineSegment(sketch, "E312", {"start": v(-3386.86, -2336.97) * mm, "end": v(-3294.38, -2317.7) * mm});
            skLineSegment(sketch, "E313", {"start": v(-3294.38, -2317.7) * mm, "end": v(-3201.5, -2299.75) * mm});
            skLineSegment(sketch, "E314", {"start": v(-3201.5, -2299.75) * mm, "end": v(-3108.17, -2283.11) * mm});
            skLineSegment(sketch, "E315", {"start": v(-3108.17, -2283.11) * mm, "end": v(-3014.38, -2267.78) * mm});
            skLineSegment(sketch, "E316", {"start": v(-3014.38, -2267.78) * mm, "end": v(-2920.11, -2253.74) * mm});
            skLineSegment(sketch, "E317", {"start": v(-2920.11, -2253.74) * mm, "end": v(-2825.33, -2240.99) * mm});
            skLineSegment(sketch, "E318", {"start": v(-2825.33, -2240.99) * mm, "end": v(-2730, -2229.52) * mm});
            skLineSegment(sketch, "E319", {"start": v(-2730, -2229.52) * mm, "end": v(-2634.11, -2219.33) * mm});
            skLineSegment(sketch, "E320", {"start": v(-2634.11, -2219.33) * mm, "end": v(-2537.63, -2210.41) * mm});
            skLineSegment(sketch, "E321", {"start": v(-2537.63, -2210.41) * mm, "end": v(-2440.53, -2202.76) * mm});
            skLineSegment(sketch, "E322", {"start": v(-2440.53, -2202.76) * mm, "end": v(-2367.35, -2212.35) * mm});
            skLineSegment(sketch, "E323", {"start": v(-2367.35, -2212.35) * mm, "end": v(-2315.49, -2228.59) * mm});
            skLineSegment(sketch, "E324", {"start": v(-2315.49, -2228.59) * mm, "end": v(-2282.8, -2250.92) * mm});
            skLineSegment(sketch, "E325", {"start": v(-2282.8, -2250.92) * mm, "end": v(-2267.1, -2278.79) * mm});
            skLineSegment(sketch, "E326", {"start": v(-2267.1, -2278.79) * mm, "end": v(-2266.26, -2311.65) * mm});
            skLineSegment(sketch, "E327", {"start": v(-2266.26, -2311.65) * mm, "end": v(-2278.09, -2348.97) * mm});
            skLineSegment(sketch, "E328", {"start": v(-2278.09, -2348.97) * mm, "end": v(-2300.44, -2390.18) * mm});
            skLineSegment(sketch, "E329", {"start": v(-2300.44, -2390.18) * mm, "end": v(-2331.14, -2434.75) * mm});
            skLineSegment(sketch, "E330", {"start": v(-2331.14, -2434.75) * mm, "end": v(-2368.05, -2482.12) * mm});
            skLineSegment(sketch, "E331", {"start": v(-2368.05, -2482.12) * mm, "end": v(-2408.98, -2531.75) * mm});
            skLineSegment(sketch, "E332", {"start": v(-2408.98, -2531.75) * mm, "end": v(-2451.79, -2583.09) * mm});
            skLineSegment(sketch, "E333", {"start": v(-2451.79, -2583.09) * mm, "end": v(-2494.3, -2635.58) * mm});
            skLineSegment(sketch, "E334", {"start": v(-2494.3, -2635.58) * mm, "end": v(-2534.38, -2688.69) * mm});
            skLineSegment(sketch, "E335", {"start": v(-2534.38, -2688.69) * mm, "end": v(-2569.84, -2741.86) * mm});
            skLineSegment(sketch, "E336", {"start": v(-2569.84, -2741.86) * mm, "end": v(-2598.52, -2794.55) * mm});
            skLineSegment(sketch, "E337", {"start": v(-2598.52, -2794.55) * mm, "end": v(-2618.27, -2846.2) * mm});
            skLineSegment(sketch, "E338", {"start": v(-2618.27, -2846.2) * mm, "end": v(-2626.92, -2896.28) * mm});
            skLineSegment(sketch, "E339", {"start": v(-2626.92, -2896.28) * mm, "end": v(-2621.99, -2953.46) * mm});
            skLineSegment(sketch, "E340", {"start": v(-2621.99, -2953.46) * mm, "end": v(-2609.63, -3019.1) * mm});
            skLineSegment(sketch, "E341", {"start": v(-2609.63, -3019.1) * mm, "end": v(-2593.62, -3078.3) * mm});
            skLineSegment(sketch, "E342", {"start": v(-2593.62, -3078.3) * mm, "end": v(-2574.03, -3131.38) * mm});
            skLineSegment(sketch, "E343", {"start": v(-2574.03, -3131.38) * mm, "end": v(-2550.94, -3178.67) * mm});
            skLineSegment(sketch, "E344", {"start": v(-2550.94, -3178.67) * mm, "end": v(-2524.41, -3220.49) * mm});
            skLineSegment(sketch, "E345", {"start": v(-2524.41, -3220.49) * mm, "end": v(-2494.54, -3257.15) * mm});
            skLineSegment(sketch, "E346", {"start": v(-2494.54, -3257.15) * mm, "end": v(-2461.4, -3288.97) * mm});
            skLineSegment(sketch, "E347", {"start": v(-2461.4, -3288.97) * mm, "end": v(-2425.07, -3316.27) * mm});
            skLineSegment(sketch, "E348", {"start": v(-2425.07, -3316.27) * mm, "end": v(-2385.62, -3339.37) * mm});
            skLineSegment(sketch, "E349", {"start": v(-2385.62, -3339.37) * mm, "end": v(-2343.14, -3358.6) * mm});
            skLineSegment(sketch, "E350", {"start": v(-2343.14, -3358.6) * mm, "end": v(-2297.69, -3374.25) * mm});
            skLineSegment(sketch, "E351", {"start": v(-2297.69, -3374.25) * mm, "end": v(-2249.36, -3386.67) * mm});
            skLineSegment(sketch, "E352", {"start": v(-2249.36, -3386.67) * mm, "end": v(-2198.23, -3396.16) * mm});
            skLineSegment(sketch, "E353", {"start": v(-2198.23, -3396.16) * mm, "end": v(-2144.37, -3403.04) * mm});
            skLineSegment(sketch, "E354", {"start": v(-2144.37, -3403.04) * mm, "end": v(-2087.86, -3407.64) * mm});
            skLineSegment(sketch, "E355", {"start": v(-2087.86, -3407.64) * mm, "end": v(-2028.78, -3410.27) * mm});
            skLineSegment(sketch, "E356", {"start": v(-2028.78, -3410.27) * mm, "end": v(-1967.2, -3411.25) * mm});
            skLineSegment(sketch, "E357", {"start": v(-1967.2, -3411.25) * mm, "end": v(-1904.75, -3410.84) * mm});
            skLineSegment(sketch, "E358", {"start": v(-1904.75, -3410.84) * mm, "end": v(-1844.65, -3408.9) * mm});
            skLineSegment(sketch, "E359", {"start": v(-1844.65, -3408.9) * mm, "end": v(-1787.1, -3405.14) * mm});
            skLineSegment(sketch, "E360", {"start": v(-1787.1, -3405.14) * mm, "end": v(-1732.16, -3399.2) * mm});
            skLineSegment(sketch, "E361", {"start": v(-1732.16, -3399.2) * mm, "end": v(-1679.9, -3390.8) * mm});
            skLineSegment(sketch, "E362", {"start": v(-1679.9, -3390.8) * mm, "end": v(-1670.47, -3388.66) * mm});
            skLineSegment(sketch, "E363", {"start": v(744.62, 13445.6) * mm, "end": v(655.08, 13407.24) * mm});
            skLineSegment(sketch, "E364", {"start": v(655.08, 13407.24) * mm, "end": v(565.5, 13370.29) * mm});
            skLineSegment(sketch, "E365", {"start": v(565.5, 13370.29) * mm, "end": v(549.69, 13364.01) * mm});
            skLineSegment(sketch, "E366", {"start": v(-1169.48, 12927.71) * mm, "end": v(-1178.93, 12926.57) * mm});
            skLineSegment(sketch, "E367", {"start": v(-1178.93, 12926.57) * mm, "end": v(-1274.82, 12916.36) * mm});
            skLineSegment(sketch, "E368", {"start": v(-1274.82, 12916.36) * mm, "end": v(-1371.3, 12907.41) * mm});
            skLineSegment(sketch, "E369", {"start": v(-1371.3, 12907.41) * mm, "end": v(-1468.4, 12899.73) * mm});
            skLineSegment(sketch, "E370", {"start": v(-1468.4, 12899.73) * mm, "end": v(-1541.56, 12909.36) * mm});
            skLineSegment(sketch, "E371", {"start": v(-1541.56, 12909.36) * mm, "end": v(-1593.4, 12925.63) * mm});
            skLineSegment(sketch, "E372", {"start": v(-1593.4, 12925.63) * mm, "end": v(-1626.07, 12948) * mm});
            skLineSegment(sketch, "E373", {"start": v(-1626.07, 12948) * mm, "end": v(-1641.75, 12975.89) * mm});
            skLineSegment(sketch, "E374", {"start": v(-1641.75, 12975.89) * mm, "end": v(-1642.6, 13008.77) * mm});
            skLineSegment(sketch, "E375", {"start": v(-1642.6, 13008.77) * mm, "end": v(-1630.76, 13046.1) * mm});
            skLineSegment(sketch, "E376", {"start": v(-1630.76, 13046.1) * mm, "end": v(-1608.41, 13087.33) * mm});
            skLineSegment(sketch, "E377", {"start": v(-1608.41, 13087.33) * mm, "end": v(-1577.71, 13131.91) * mm});
            skLineSegment(sketch, "E378", {"start": v(-1577.71, 13131.91) * mm, "end": v(-1540.82, 13179.29) * mm});
            skLineSegment(sketch, "E379", {"start": v(-1540.82, 13179.29) * mm, "end": v(-1499.9, 13228.92) * mm});
            skLineSegment(sketch, "E380", {"start": v(-1499.9, 13228.92) * mm, "end": v(-1457.1, 13280.26) * mm});
            skLineSegment(sketch, "E381", {"start": v(-1457.1, 13280.26) * mm, "end": v(-1414.59, 13332.75) * mm});
            skLineSegment(sketch, "E382", {"start": v(-1414.59, 13332.75) * mm, "end": v(-1374.53, 13385.86) * mm});
            skLineSegment(sketch, "E383", {"start": v(-1374.53, 13385.86) * mm, "end": v(-1339.08, 13439.03) * mm});
            skLineSegment(sketch, "E384", {"start": v(-1339.08, 13439.03) * mm, "end": v(-1310.4, 13491.71) * mm});
            skLineSegment(sketch, "E385", {"start": v(-1310.4, 13491.71) * mm, "end": v(-1290.66, 13543.37) * mm});
            skLineSegment(sketch, "E386", {"start": v(-1290.66, 13543.37) * mm, "end": v(-1282.01, 13593.44) * mm});
            skLineSegment(sketch, "E387", {"start": v(-1282.01, 13593.44) * mm, "end": v(-1286.95, 13650.63) * mm});
            skLineSegment(sketch, "E388", {"start": v(-1286.95, 13650.63) * mm, "end": v(-1299.3, 13716.27) * mm});
            skLineSegment(sketch, "E389", {"start": v(-1299.3, 13716.27) * mm, "end": v(-1315.32, 13775.47) * mm});
            skLineSegment(sketch, "E390", {"start": v(-1315.32, 13775.47) * mm, "end": v(-1334.93, 13828.55) * mm});
            skLineSegment(sketch, "E391", {"start": v(-1334.93, 13828.55) * mm, "end": v(-1358.04, 13875.84) * mm});
            skLineSegment(sketch, "E392", {"start": v(-1358.04, 13875.84) * mm, "end": v(-1384.58, 13917.65) * mm});
            skLineSegment(sketch, "E393", {"start": v(-1384.58, 13917.65) * mm, "end": v(-1414.47, 13954.3) * mm});
            skLineSegment(sketch, "E394", {"start": v(-1414.47, 13954.3) * mm, "end": v(-1447.63, 13986.1) * mm});
            skLineSegment(sketch, "E395", {"start": v(-1447.63, 13986.1) * mm, "end": v(-1483.99, 14013.4) * mm});
            skLineSegment(sketch, "E396", {"start": v(-1483.99, 14013.4) * mm, "end": v(-1523.46, 14036.49) * mm});
            skLineSegment(sketch, "E397", {"start": v(-1523.46, 14036.49) * mm, "end": v(-1565.96, 14055.7) * mm});
            skLineSegment(sketch, "E398", {"start": v(-1565.96, 14055.7) * mm, "end": v(-1611.43, 14071.34) * mm});
            skLineSegment(sketch, "E399", {"start": v(-1611.43, 14071.34) * mm, "end": v(-1659.78, 14083.74) * mm});
            skLineSegment(sketch, "E400", {"start": v(-1659.78, 14083.74) * mm, "end": v(-1710.93, 14093.22) * mm});
            skLineSegment(sketch, "E401", {"start": v(-1710.93, 14093.22) * mm, "end": v(-1764.8, 14100.1) * mm});
            skLineSegment(sketch, "E402", {"start": v(-1764.8, 14100.1) * mm, "end": v(-1821.32, 14104.68) * mm});
            skLineSegment(sketch, "E403", {"start": v(-1821.32, 14104.68) * mm, "end": v(-1880.41, 14107.3) * mm});
            skLineSegment(sketch, "E404", {"start": v(-1880.41, 14107.3) * mm, "end": v(-1941.99, 14108.28) * mm});
            skLineSegment(sketch, "E405", {"start": v(-1941.99, 14108.28) * mm, "end": v(-2004.44, 14107.87) * mm});
            skLineSegment(sketch, "E406", {"start": v(-2004.44, 14107.87) * mm, "end": v(-2064.53, 14105.95) * mm});
            skLineSegment(sketch, "E407", {"start": v(-2064.53, 14105.95) * mm, "end": v(-2122.08, 14102.19) * mm});
            skLineSegment(sketch, "E408", {"start": v(-2122.08, 14102.19) * mm, "end": v(-2177, 14096.26) * mm});
            skLineSegment(sketch, "E409", {"start": v(-2177, 14096.26) * mm, "end": v(-2229.24, 14087.87) * mm});
            skLineSegment(sketch, "E410", {"start": v(-2229.24, 14087.87) * mm, "end": v(-2278.7, 14076.67) * mm});
            skLineSegment(sketch, "E411", {"start": v(-2278.7, 14076.67) * mm, "end": v(-2325.3, 14062.36) * mm});
            skLineSegment(sketch, "E412", {"start": v(-2325.3, 14062.36) * mm, "end": v(-2368.99, 14044.62) * mm});
            skLineSegment(sketch, "E413", {"start": v(-2368.99, 14044.62) * mm, "end": v(-2409.66, 14023.12) * mm});
            skLineSegment(sketch, "E414", {"start": v(-2409.66, 14023.12) * mm, "end": v(-2447.25, 13997.55) * mm});
            skLineSegment(sketch, "E415", {"start": v(-2447.25, 13997.55) * mm, "end": v(-2481.68, 13967.59) * mm});
            skLineSegment(sketch, "E416", {"start": v(-2481.68, 13967.59) * mm, "end": v(-2512.86, 13932.91) * mm});
            skLineSegment(sketch, "E417", {"start": v(-2512.86, 13932.91) * mm, "end": v(-2540.73, 13893.2) * mm});
            skLineSegment(sketch, "E418", {"start": v(-2540.73, 13893.2) * mm, "end": v(-2565.2, 13848.15) * mm});
            skLineSegment(sketch, "E419", {"start": v(-2565.2, 13848.15) * mm, "end": v(-2586.21, 13797.42) * mm});
            skLineSegment(sketch, "E420", {"start": v(-2586.21, 13797.42) * mm, "end": v(-2603.67, 13740.7) * mm});
            skLineSegment(sketch, "E421", {"start": v(-2603.67, 13740.7) * mm, "end": v(-2617.5, 13677.68) * mm});
            skLineSegment(sketch, "E422", {"start": v(-2617.5, 13677.68) * mm, "end": v(-2626.4, 13617.72) * mm});
            skLineSegment(sketch, "E423", {"start": v(-2626.4, 13617.72) * mm, "end": v(-2626.92, 13593.44) * mm});
            skLineSegment(sketch, "E424", {"start": v(-2626.92, 13593.44) * mm, "end": v(-2624.12, 13568.64) * mm});
            skLineSegment(sketch, "E425", {"start": v(-2624.12, 13568.64) * mm, "end": v(-2618.27, 13543.37) * mm});
            skLineSegment(sketch, "E426", {"start": v(-2618.27, 13543.37) * mm, "end": v(-2609.65, 13517.7) * mm});
            skLineSegment(sketch, "E427", {"start": v(-2609.65, 13517.7) * mm, "end": v(-2598.53, 13491.71) * mm});
            skLineSegment(sketch, "E428", {"start": v(-2598.53, 13491.71) * mm, "end": v(-2585.17, 13465.47) * mm});
            skLineSegment(sketch, "E429", {"start": v(-2585.17, 13465.47) * mm, "end": v(-2569.85, 13439.03) * mm});
            skLineSegment(sketch, "E430", {"start": v(-2569.85, 13439.03) * mm, "end": v(-2552.84, 13412.47) * mm});
            skLineSegment(sketch, "E431", {"start": v(-2552.84, 13412.47) * mm, "end": v(-2534.4, 13385.86) * mm});
            skLineSegment(sketch, "E432", {"start": v(-2534.4, 13385.86) * mm, "end": v(-2514.82, 13359.26) * mm});
            skLineSegment(sketch, "E433", {"start": v(-2514.82, 13359.26) * mm, "end": v(-2494.35, 13332.75) * mm});
            skLineSegment(sketch, "E434", {"start": v(-2494.35, 13332.75) * mm, "end": v(-2473.27, 13306.4) * mm});
            skLineSegment(sketch, "E435", {"start": v(-2473.27, 13306.4) * mm, "end": v(-2451.84, 13280.26) * mm});
            skLineSegment(sketch, "E436", {"start": v(-2451.84, 13280.26) * mm, "end": v(-2430.34, 13254.4) * mm});
            skLineSegment(sketch, "E437", {"start": v(-2430.34, 13254.4) * mm, "end": v(-2409.04, 13228.92) * mm});
            skLineSegment(sketch, "E438", {"start": v(-2409.04, 13228.92) * mm, "end": v(-2388.21, 13203.86) * mm});
            skLineSegment(sketch, "E439", {"start": v(-2388.21, 13203.86) * mm, "end": v(-2368.12, 13179.29) * mm});
            skLineSegment(sketch, "E440", {"start": v(-2368.12, 13179.29) * mm, "end": v(-2349.03, 13155.28) * mm});
            skLineSegment(sketch, "E441", {"start": v(-2349.03, 13155.28) * mm, "end": v(-2331.22, 13131.91) * mm});
            skLineSegment(sketch, "E442", {"start": v(-2331.22, 13131.91) * mm, "end": v(-2314.96, 13109.24) * mm});
            skLineSegment(sketch, "E443", {"start": v(-2314.96, 13109.24) * mm, "end": v(-2300.52, 13087.33) * mm});
            skLineSegment(sketch, "E444", {"start": v(-2300.52, 13087.33) * mm, "end": v(-2288.17, 13066.27) * mm});
            skLineSegment(sketch, "E445", {"start": v(-2288.17, 13066.27) * mm, "end": v(-2278.17, 13046.1) * mm});
            skLineSegment(sketch, "E446", {"start": v(-2278.17, 13046.1) * mm, "end": v(-2270.8, 13026.92) * mm});
            skLineSegment(sketch, "E447", {"start": v(-2270.8, 13026.92) * mm, "end": v(-2266.34, 13008.77) * mm});
            skLineSegment(sketch, "E448", {"start": v(-2266.34, 13008.77) * mm, "end": v(-2265.04, 12991.74) * mm});
            skLineSegment(sketch, "E449", {"start": v(-2265.04, 12991.74) * mm, "end": v(-2267.18, 12975.89) * mm});
            skLineSegment(sketch, "E450", {"start": v(-2267.18, 12975.89) * mm, "end": v(-2273.03, 12961.28) * mm});
            skLineSegment(sketch, "E451", {"start": v(-2273.03, 12961.28) * mm, "end": v(-2282.86, 12948) * mm});
            skLineSegment(sketch, "E452", {"start": v(-2282.86, 12948) * mm, "end": v(-2296.94, 12936.09) * mm});
            skLineSegment(sketch, "E453", {"start": v(-2296.94, 12936.09) * mm, "end": v(-2315.54, 12925.63) * mm});
            skLineSegment(sketch, "E454", {"start": v(-2315.54, 12925.63) * mm, "end": v(-2338.93, 12916.7) * mm});
            skLineSegment(sketch, "E455", {"start": v(-2338.93, 12916.7) * mm, "end": v(-2367.38, 12909.36) * mm});
            skLineSegment(sketch, "E456", {"start": v(-2367.38, 12909.36) * mm, "end": v(-2401.15, 12903.68) * mm});
            skLineSegment(sketch, "E457", {"start": v(-2401.15, 12903.68) * mm, "end": v(-2440.53, 12899.73) * mm});
            skLineSegment(sketch, "E458", {"start": v(-2440.53, 12899.73) * mm, "end": v(-2537.63, 12907.41) * mm});
            skLineSegment(sketch, "E459", {"start": v(-2537.63, 12907.41) * mm, "end": v(-2634.11, 12916.36) * mm});
            skLineSegment(sketch, "E460", {"start": v(-2634.11, 12916.36) * mm, "end": v(-2730, 12926.57) * mm});
            skLineSegment(sketch, "E461", {"start": v(-2730, 12926.57) * mm, "end": v(-2825.33, 12938.06) * mm});
            skLineSegment(sketch, "E462", {"start": v(-2825.33, 12938.06) * mm, "end": v(-2920.11, 12950.83) * mm});
            skLineSegment(sketch, "E463", {"start": v(-2920.11, 12950.83) * mm, "end": v(-3014.38, 12964.89) * mm});
            skLineSegment(sketch, "E464", {"start": v(-3014.38, 12964.89) * mm, "end": v(-3108.17, 12980.24) * mm});
            skLineSegment(sketch, "E465", {"start": v(-3108.17, 12980.24) * mm, "end": v(-3201.5, 12996.9) * mm});
            skLineSegment(sketch, "E466", {"start": v(-3201.5, 12996.9) * mm, "end": v(-3294.38, 13014.85) * mm});
            skLineSegment(sketch, "E467", {"start": v(-3294.38, 13014.85) * mm, "end": v(-3386.86, 13034.12) * mm});
            skLineSegment(sketch, "E468", {"start": v(-3386.86, 13034.12) * mm, "end": v(-3478.96, 13054.72) * mm});
            skLineSegment(sketch, "E469", {"start": v(-3478.96, 13054.72) * mm, "end": v(-3570.7, 13076.64) * mm});
            skLineSegment(sketch, "E470", {"start": v(-3570.7, 13076.64) * mm, "end": v(-3662.12, 13099.9) * mm});
            skLineSegment(sketch, "E471", {"start": v(-3662.12, 13099.9) * mm, "end": v(-3753.24, 13124.49) * mm});
            skLineSegment(sketch, "E472", {"start": v(-3753.24, 13124.49) * mm, "end": v(-3844.08, 13150.43) * mm});
            skLineSegment(sketch, "E473", {"start": v(-3844.08, 13150.43) * mm, "end": v(-3934.66, 13177.73) * mm});
            skLineSegment(sketch, "E474", {"start": v(-3934.66, 13177.73) * mm, "end": v(-4025.03, 13206.38) * mm});
            skLineSegment(sketch, "E475", {"start": v(-4025.03, 13206.38) * mm, "end": v(-4115.2, 13236.4) * mm});
            skLineSegment(sketch, "E476", {"start": v(-4115.2, 13236.4) * mm, "end": v(-4205.2, 13267.8) * mm});
            skLineSegment(sketch, "E477", {"start": v(-4205.2, 13267.8) * mm, "end": v(-4295.05, 13300.57) * mm});
            skLineSegment(sketch, "E478", {"start": v(-4295.05, 13300.57) * mm, "end": v(-4384.79, 13334.73) * mm});
            skLineSegment(sketch, "E479", {"start": v(-4384.79, 13334.73) * mm, "end": v(-4474.44, 13370.29) * mm});
            skLineSegment(sketch, "E480", {"start": v(-4474.44, 13370.29) * mm, "end": v(-4564.02, 13407.24) * mm});
            skLineSegment(sketch, "E481", {"start": v(-4564.02, 13407.24) * mm, "end": v(-4653.56, 13445.6) * mm});
            skLineSegment(sketch, "E482", {"start": v(-4653.56, 13445.6) * mm, "end": v(-4691.92, 13356.06) * mm});
            skLineSegment(sketch, "E483", {"start": v(-4691.92, 13356.06) * mm, "end": v(-4728.87, 13266.48) * mm});
            skLineSegment(sketch, "E484", {"start": v(-4728.87, 13266.48) * mm, "end": v(-4764.42, 13176.84) * mm});
            skLineSegment(sketch, "E485", {"start": v(-4764.42, 13176.84) * mm, "end": v(-4798.58, 13087.1) * mm});
            skLineSegment(sketch, "E486", {"start": v(-4798.58, 13087.1) * mm, "end": v(-4831.36, 12997.26) * mm});
            skLineSegment(sketch, "E487", {"start": v(-4831.36, 12997.26) * mm, "end": v(-4862.75, 12907.27) * mm});
            skLineSegment(sketch, "E488", {"start": v(-4862.75, 12907.27) * mm, "end": v(-4892.77, 12817.1) * mm});
            skLineSegment(sketch, "E489", {"start": v(-4892.77, 12817.1) * mm, "end": v(-4921.42, 12726.75) * mm});
            skLineSegment(sketch, "E490", {"start": v(-4921.42, 12726.75) * mm, "end": v(-4948.72, 12636.18) * mm});
            skLineSegment(sketch, "E491", {"start": v(-4948.72, 12636.18) * mm, "end": v(-4974.65, 12545.35) * mm});
            skLineSegment(sketch, "E492", {"start": v(-4974.65, 12545.35) * mm, "end": v(-4999.24, 12454.25) * mm});
            skLineSegment(sketch, "E493", {"start": v(-4999.24, 12454.25) * mm, "end": v(-5022.5, 12362.84) * mm});
            skLineSegment(sketch, "E494", {"start": v(-5022.5, 12362.84) * mm, "end": v(-5044.4, 12271.1) * mm});
            skLineSegment(sketch, "E495", {"start": v(-5044.4, 12271.1) * mm, "end": v(-5065, 12179.02) * mm});
            skLineSegment(sketch, "E496", {"start": v(-5065, 12179.02) * mm, "end": v(-5084.26, 12086.55) * mm});
            skLineSegment(sketch, "E497", {"start": v(-5084.26, 12086.55) * mm, "end": v(-5102.2, 11993.67) * mm});
            skLineSegment(sketch, "E498", {"start": v(-5102.2, 11993.67) * mm, "end": v(-5118.85, 11900.36) * mm});
            skLineSegment(sketch, "E499", {"start": v(-5118.85, 11900.36) * mm, "end": v(-5134.19, 11806.59) * mm});
            skLineSegment(sketch, "E500", {"start": v(-5134.19, 11806.59) * mm, "end": v(-5148.23, 11712.32) * mm});
            skLineSegment(sketch, "E501", {"start": v(-5148.23, 11712.32) * mm, "end": v(-5160.98, 11617.55) * mm});
            skLineSegment(sketch, "E502", {"start": v(-5160.98, 11617.55) * mm, "end": v(-5172.45, 11522.23) * mm});
            skLineSegment(sketch, "E503", {"start": v(-5172.45, 11522.23) * mm, "end": v(-5182.65, 11426.34) * mm});
            skLineSegment(sketch, "E504", {"start": v(-5182.65, 11426.34) * mm, "end": v(-5191.57, 11329.86) * mm});
            skLineSegment(sketch, "E505", {"start": v(-5191.57, 11329.86) * mm, "end": v(-5199.24, 11232.76) * mm});
            skLineSegment(sketch, "E506", {"start": v(-5199.24, 11232.76) * mm, "end": v(-5189.63, 11159.58) * mm});
            skLineSegment(sketch, "E507", {"start": v(-5189.63, 11159.58) * mm, "end": v(-5173.39, 11107.72) * mm});
            skLineSegment(sketch, "E508", {"start": v(-5173.39, 11107.72) * mm, "end": v(-5151.06, 11075.03) * mm});
            skLineSegment(sketch, "E509", {"start": v(-5151.06, 11075.03) * mm, "end": v(-5123.18, 11059.34) * mm});
            skLineSegment(sketch, "E510", {"start": v(-5123.18, 11059.34) * mm, "end": v(-5090.31, 11058.48) * mm});
            skLineSegment(sketch, "E511", {"start": v(-5090.31, 11058.48) * mm, "end": v(-5053, 11070.31) * mm});
            skLineSegment(sketch, "E512", {"start": v(-5053, 11070.31) * mm, "end": v(-5011.78, 11092.66) * mm});
            skLineSegment(sketch, "E513", {"start": v(-5011.78, 11092.66) * mm, "end": v(-4967.22, 11123.36) * mm});
            skLineSegment(sketch, "E514", {"start": v(-4967.22, 11123.36) * mm, "end": v(-4919.85, 11160.25) * mm});
            skLineSegment(sketch, "E515", {"start": v(-4919.85, 11160.25) * mm, "end": v(-4870.22, 11201.18) * mm});
            skLineSegment(sketch, "E516", {"start": v(-4870.22, 11201.18) * mm, "end": v(-4818.9, 11243.98) * mm});
            skLineSegment(sketch, "E517", {"start": v(-4818.9, 11243.98) * mm, "end": v(-4766.4, 11286.48) * mm});
            skLineSegment(sketch, "E518", {"start": v(-4766.4, 11286.48) * mm, "end": v(-4713.3, 11326.53) * mm});
            skLineSegment(sketch, "E519", {"start": v(-4713.3, 11326.53) * mm, "end": v(-4660.13, 11361.97) * mm});
            skLineSegment(sketch, "E520", {"start": v(-4660.13, 11361.97) * mm, "end": v(-4607.44, 11390.63) * mm});
            skLineSegment(sketch, "E521", {"start": v(-4607.44, 11390.63) * mm, "end": v(-4555.79, 11410.35) * mm});
            skLineSegment(sketch, "E522", {"start": v(-4555.79, 11410.35) * mm, "end": v(-4505.71, 11418.98) * mm});
            skLineSegment(sketch, "E523", {"start": v(-4505.71, 11418.98) * mm, "end": v(-4448.53, 11414.03) * mm});
            skLineSegment(sketch, "E524", {"start": v(-4448.53, 11414.03) * mm, "end": v(-4382.89, 11401.7) * mm});
            skLineSegment(sketch, "E525", {"start": v(-4382.89, 11401.7) * mm, "end": v(-4323.68, 11385.7) * mm});
            skLineSegment(sketch, "E526", {"start": v(-4323.68, 11385.7) * mm, "end": v(-4270.59, 11366.11) * mm});
            skLineSegment(sketch, "E527", {"start": v(-4270.59, 11366.11) * mm, "end": v(-4223.29, 11343.02) * mm});
            skLineSegment(sketch, "E528", {"start": v(-4223.29, 11343.02) * mm, "end": v(-4181.46, 11316.5) * mm});
            skLineSegment(sketch, "E529", {"start": v(-4181.46, 11316.5) * mm, "end": v(-4144.8, 11286.62) * mm});
            skLineSegment(sketch, "E530", {"start": v(-4144.8, 11286.62) * mm, "end": v(-4112.97, 11253.47) * mm});
            skLineSegment(sketch, "E531", {"start": v(-4112.97, 11253.47) * mm, "end": v(-4085.67, 11217.13) * mm});
            skLineSegment(sketch, "E532", {"start": v(-4085.67, 11217.13) * mm, "end": v(-4062.56, 11177.67) * mm});
            skLineSegment(sketch, "E533", {"start": v(-4062.56, 11177.67) * mm, "end": v(-4043.34, 11135.17) * mm});
            skLineSegment(sketch, "E534", {"start": v(-4043.34, 11135.17) * mm, "end": v(-4027.68, 11089.71) * mm});
            skLineSegment(sketch, "E535", {"start": v(-4027.68, 11089.71) * mm, "end": v(-4015.26, 11041.37) * mm});
            skLineSegment(sketch, "E536", {"start": v(-4015.26, 11041.37) * mm, "end": v(-4005.77, 10990.23) * mm});
            skLineSegment(sketch, "E537", {"start": v(-4005.77, 10990.23) * mm, "end": v(-3998.89, 10936.36) * mm});
            skLineSegment(sketch, "E538", {"start": v(-3998.89, 10936.36) * mm, "end": v(-3994.29, 10879.84) * mm});
            skLineSegment(sketch, "E539", {"start": v(-3994.29, 10879.84) * mm, "end": v(-3991.66, 10820.76) * mm});
            skLineSegment(sketch, "E540", {"start": v(-3991.66, 10820.76) * mm, "end": v(-3990.68, 10759.18) * mm});
            skLineSegment(sketch, "E541", {"start": v(-3990.68, 10759.18) * mm, "end": v(-3991.09, 10696.72) * mm});
            skLineSegment(sketch, "E542", {"start": v(-3991.09, 10696.72) * mm, "end": v(-3993.02, 10636.63) * mm});
            skLineSegment(sketch, "E543", {"start": v(-3993.02, 10636.63) * mm, "end": v(-3996.8, 10579.08) * mm});
            skLineSegment(sketch, "E544", {"start": v(-3996.8, 10579.08) * mm, "end": v(-4002.72, 10524.14) * mm});
            skLineSegment(sketch, "E545", {"start": v(-4002.72, 10524.14) * mm, "end": v(-4011.13, 10471.9) * mm});
            skLineSegment(sketch, "E546", {"start": v(-4011.13, 10471.9) * mm, "end": v(-4022.34, 10422.42) * mm});
            skLineSegment(sketch, "E547", {"start": v(-4022.34, 10422.42) * mm, "end": v(-4036.66, 10375.8) * mm});
            skLineSegment(sketch, "E548", {"start": v(-4036.66, 10375.8) * mm, "end": v(-4054.42, 10332.1) * mm});
            skLineSegment(sketch, "E549", {"start": v(-4054.42, 10332.1) * mm, "end": v(-4075.94, 10291.41) * mm});
            skLineSegment(sketch, "E550", {"start": v(-4075.94, 10291.41) * mm, "end": v(-4101.53, 10253.8) * mm});
            skLineSegment(sketch, "E551", {"start": v(-4101.53, 10253.8) * mm, "end": v(-4131.5, 10219.36) * mm});
            skLineSegment(sketch, "E552", {"start": v(-4131.5, 10219.36) * mm, "end": v(-4166.2, 10188.16) * mm});
            skLineSegment(sketch, "E553", {"start": v(-4166.2, 10188.16) * mm, "end": v(-4205.92, 10160.28) * mm});
            skLineSegment(sketch, "E554", {"start": v(-4205.92, 10160.28) * mm, "end": v(-4250.99, 10135.79) * mm});
            skLineSegment(sketch, "E555", {"start": v(-4250.99, 10135.79) * mm, "end": v(-4301.73, 10114.77) * mm});
            skLineSegment(sketch, "E556", {"start": v(-4301.73, 10114.77) * mm, "end": v(-4358.45, 10097.31) * mm});
            skLineSegment(sketch, "E557", {"start": v(-4358.45, 10097.31) * mm, "end": v(-4421.48, 10083.49) * mm});
            skLineSegment(sketch, "E558", {"start": v(-4421.48, 10083.49) * mm, "end": v(-4481.44, 10074.56) * mm});
            skLineSegment(sketch, "E559", {"start": v(-4481.44, 10074.56) * mm, "end": v(-4505.71, 10074.05) * mm});
            skLineSegment(sketch, "E560", {"start": v(-4505.71, 10074.05) * mm, "end": v(-4530.52, 10076.86) * mm});
            skLineSegment(sketch, "E561", {"start": v(-4530.52, 10076.86) * mm, "end": v(-4555.79, 10082.7) * mm});
            skLineSegment(sketch, "E562", {"start": v(-4555.79, 10082.7) * mm, "end": v(-4581.45, 10091.33) * mm});
            skLineSegment(sketch, "E563", {"start": v(-4581.45, 10091.33) * mm, "end": v(-4607.44, 10102.46) * mm});
            skLineSegment(sketch, "E564", {"start": v(-4607.44, 10102.46) * mm, "end": v(-4633.69, 10115.82) * mm});
            skLineSegment(sketch, "E565", {"start": v(-4633.69, 10115.82) * mm, "end": v(-4660.13, 10131.14) * mm});
            skLineSegment(sketch, "E566", {"start": v(-4660.13, 10131.14) * mm, "end": v(-4686.68, 10148.16) * mm});
            skLineSegment(sketch, "E567", {"start": v(-4686.68, 10148.16) * mm, "end": v(-4713.3, 10166.6) * mm});
            skLineSegment(sketch, "E568", {"start": v(-4713.3, 10166.6) * mm, "end": v(-4739.89, 10186.2) * mm});
            skLineSegment(sketch, "E569", {"start": v(-4739.89, 10186.2) * mm, "end": v(-4766.4, 10206.67) * mm});
            skLineSegment(sketch, "E570", {"start": v(-4766.4, 10206.67) * mm, "end": v(-4792.76, 10227.76) * mm});
            skLineSegment(sketch, "E571", {"start": v(-4792.76, 10227.76) * mm, "end": v(-4818.9, 10249.2) * mm});
            skLineSegment(sketch, "E572", {"start": v(-4818.9, 10249.2) * mm, "end": v(-4844.74, 10270.7) * mm});
            skLineSegment(sketch, "E573", {"start": v(-4844.74, 10270.7) * mm, "end": v(-4870.22, 10292) * mm});
            skLineSegment(sketch, "E574", {"start": v(-4870.22, 10292) * mm, "end": v(-4895.28, 10312.85) * mm});
            skLineSegment(sketch, "E575", {"start": v(-4895.28, 10312.85) * mm, "end": v(-4919.85, 10332.95) * mm});
            skLineSegment(sketch, "E576", {"start": v(-4919.85, 10332.95) * mm, "end": v(-4943.85, 10352.05) * mm});
            skLineSegment(sketch, "E577", {"start": v(-4943.85, 10352.05) * mm, "end": v(-4967.22, 10369.86) * mm});
            skLineSegment(sketch, "E578", {"start": v(-4967.22, 10369.86) * mm, "end": v(-4989.88, 10386.13) * mm});
            skLineSegment(sketch, "E579", {"start": v(-4989.88, 10386.13) * mm, "end": v(-5011.78, 10400.58) * mm});
            skLineSegment(sketch, "E580", {"start": v(-5011.78, 10400.58) * mm, "end": v(-5032.84, 10412.94) * mm});
            skLineSegment(sketch, "E581", {"start": v(-5032.84, 10412.94) * mm, "end": v(-5053, 10422.94) * mm});
            skLineSegment(sketch, "E582", {"start": v(-5053, 10422.94) * mm, "end": v(-5072.17, 10430.31) * mm});
            skLineSegment(sketch, "E583", {"start": v(-5072.17, 10430.31) * mm, "end": v(-5090.31, 10434.79) * mm});
            skLineSegment(sketch, "E584", {"start": v(-5090.31, 10434.79) * mm, "end": v(-5107.34, 10436.1) * mm});
            skLineSegment(sketch, "E585", {"start": v(-5107.34, 10436.1) * mm, "end": v(-5123.18, 10433.96) * mm});
            skLineSegment(sketch, "E586", {"start": v(-5123.18, 10433.96) * mm, "end": v(-5137.78, 10428.11) * mm});
            skLineSegment(sketch, "E587", {"start": v(-5137.78, 10428.11) * mm, "end": v(-5151.06, 10418.29) * mm});
            skLineSegment(sketch, "E588", {"start": v(-5151.06, 10418.29) * mm, "end": v(-5162.95, 10404.21) * mm});
            skLineSegment(sketch, "E589", {"start": v(-5162.95, 10404.21) * mm, "end": v(-5173.39, 10385.62) * mm});
            skLineSegment(sketch, "E590", {"start": v(-5173.39, 10385.62) * mm, "end": v(-5182.3, 10362.23) * mm});
            skLineSegment(sketch, "E591", {"start": v(-5182.3, 10362.23) * mm, "end": v(-5189.63, 10333.79) * mm});
            skLineSegment(sketch, "E592", {"start": v(-5189.63, 10333.79) * mm, "end": v(-5195.3, 10300.01) * mm});
            skLineSegment(sketch, "E593", {"start": v(-5195.3, 10300.01) * mm, "end": v(-5199.24, 10260.64) * mm});
            skLineSegment(sketch, "E594", {"start": v(-5199.24, 10260.64) * mm, "end": v(-5191.57, 10163.51) * mm});
            skLineSegment(sketch, "E595", {"start": v(-5191.57, 10163.51) * mm, "end": v(-5182.65, 10067) * mm});
            skLineSegment(sketch, "E596", {"start": v(-5182.65, 10067) * mm, "end": v(-5172.45, 9971.1) * mm});
            skLineSegment(sketch, "E597", {"start": v(-5172.45, 9971.1) * mm, "end": v(-5160.98, 9875.76) * mm});
            skLineSegment(sketch, "E598", {"start": v(-5160.98, 9875.76) * mm, "end": v(-5148.23, 9780.96) * mm});
            skLineSegment(sketch, "E599", {"start": v(-5148.23, 9780.96) * mm, "end": v(-5134.19, 9686.68) * mm});
            skLineSegment(sketch, "E600", {"start": v(-5134.19, 9686.68) * mm, "end": v(-5118.85, 9592.88) * mm});
            skLineSegment(sketch, "E601", {"start": v(-5118.85, 9592.88) * mm, "end": v(-5102.2, 9499.55) * mm});
            skLineSegment(sketch, "E602", {"start": v(-5102.2, 9499.55) * mm, "end": v(-5084.26, 9406.65) * mm});
            skLineSegment(sketch, "E603", {"start": v(-5084.26, 9406.65) * mm, "end": v(-5065, 9314.17) * mm});
            skLineSegment(sketch, "E604", {"start": v(-5065, 9314.17) * mm, "end": v(-5044.4, 9222.06) * mm});
            skLineSegment(sketch, "E605", {"start": v(-5044.4, 9222.06) * mm, "end": v(-5022.5, 9130.32) * mm});
            skLineSegment(sketch, "E606", {"start": v(-5022.5, 9130.32) * mm, "end": v(-4999.24, 9038.9) * mm});
            skLineSegment(sketch, "E607", {"start": v(-4999.24, 9038.9) * mm, "end": v(-4974.65, 8947.79) * mm});
            skLineSegment(sketch, "E608", {"start": v(-4974.65, 8947.79) * mm, "end": v(-4948.72, 8856.96) * mm});
            skLineSegment(sketch, "E609", {"start": v(-4948.72, 8856.96) * mm, "end": v(-4921.42, 8766.37) * mm});
            skLineSegment(sketch, "E610", {"start": v(-4921.42, 8766.37) * mm, "end": v(-4892.77, 8676.02) * mm});
            skLineSegment(sketch, "E611", {"start": v(-4892.77, 8676.02) * mm, "end": v(-4862.75, 8585.86) * mm});
            skLineSegment(sketch, "E612", {"start": v(-4862.75, 8585.86) * mm, "end": v(-4831.36, 8495.87) * mm});
            skLineSegment(sketch, "E613", {"start": v(-4831.36, 8495.87) * mm, "end": v(-4798.58, 8406.03) * mm});
            skLineSegment(sketch, "E614", {"start": v(-4798.58, 8406.03) * mm, "end": v(-4764.42, 8316.31) * mm});
            skLineSegment(sketch, "E615", {"start": v(-4764.42, 8316.31) * mm, "end": v(-4728.87, 8226.69) * mm});
            skLineSegment(sketch, "E616", {"start": v(-4728.87, 8226.69) * mm, "end": v(-4691.92, 8137.13) * mm});
            skLineSegment(sketch, "E617", {"start": v(-4691.92, 8137.13) * mm, "end": v(-4653.56, 8047.6) * mm});
            skLineSegment(sketch, "E618", {"start": v(-4653.56, 8047.6) * mm, "end": v(-4564.02, 8085.97) * mm});
            skLineSegment(sketch, "E619", {"start": v(-4564.02, 8085.97) * mm, "end": v(-4474.44, 8122.92) * mm});
            skLineSegment(sketch, "E620", {"start": v(-4474.44, 8122.92) * mm, "end": v(-4384.79, 8158.47) * mm});
            skLineSegment(sketch, "E621", {"start": v(-4384.79, 8158.47) * mm, "end": v(-4295.05, 8192.64) * mm});
            skLineSegment(sketch, "E622", {"start": v(-4295.05, 8192.64) * mm, "end": v(-4205.2, 8225.4) * mm});
            skLineSegment(sketch, "E623", {"start": v(-4205.2, 8225.4) * mm, "end": v(-4115.2, 8256.8) * mm});
            skLineSegment(sketch, "E624", {"start": v(-4115.2, 8256.8) * mm, "end": v(-4025.03, 8286.82) * mm});
            skLineSegment(sketch, "E625", {"start": v(-4025.03, 8286.82) * mm, "end": v(-3934.66, 8315.48) * mm});
            skLineSegment(sketch, "E626", {"start": v(-3934.66, 8315.48) * mm, "end": v(-3844.08, 8342.77) * mm});
            skLineSegment(sketch, "E627", {"start": v(-3844.08, 8342.77) * mm, "end": v(-3753.24, 8368.71) * mm});
            skLineSegment(sketch, "E628", {"start": v(-3753.24, 8368.71) * mm, "end": v(-3662.12, 8393.3) * mm});
            skLineSegment(sketch, "E629", {"start": v(-3662.12, 8393.3) * mm, "end": v(-3570.7, 8416.56) * mm});
            skLineSegment(sketch, "E630", {"start": v(-3570.7, 8416.56) * mm, "end": v(-3478.96, 8438.48) * mm});
            skLineSegment(sketch, "E631", {"start": v(-3478.96, 8438.48) * mm, "end": v(-3386.86, 8459.07) * mm});
            skLineSegment(sketch, "E632", {"start": v(-3386.86, 8459.07) * mm, "end": v(-3294.38, 8478.34) * mm});
            skLineSegment(sketch, "E633", {"start": v(-3294.38, 8478.34) * mm, "end": v(-3201.5, 8496.3) * mm});
            skLineSegment(sketch, "E634", {"start": v(-3201.5, 8496.3) * mm, "end": v(-3108.17, 8512.94) * mm});
            skLineSegment(sketch, "E635", {"start": v(-3108.17, 8512.94) * mm, "end": v(-3014.38, 8528.3) * mm});
            skLineSegment(sketch, "E636", {"start": v(-3014.38, 8528.3) * mm, "end": v(-2920.11, 8542.34) * mm});
            skLineSegment(sketch, "E637", {"start": v(-2920.11, 8542.34) * mm, "end": v(-2825.33, 8555.1) * mm});
            skLineSegment(sketch, "E638", {"start": v(-2825.33, 8555.1) * mm, "end": v(-2730, 8566.6) * mm});
            skLineSegment(sketch, "E639", {"start": v(-2730, 8566.6) * mm, "end": v(-2634.11, 8576.8) * mm});
            skLineSegment(sketch, "E640", {"start": v(-2634.11, 8576.8) * mm, "end": v(-2537.63, 8585.74) * mm});
            skLineSegment(sketch, "E641", {"start": v(-2537.63, 8585.74) * mm, "end": v(-2440.53, 8593.41) * mm});
            skLineSegment(sketch, "E642", {"start": v(-2440.53, 8593.41) * mm, "end": v(-2367.35, 8583.79) * mm});
            skLineSegment(sketch, "E643", {"start": v(-2367.35, 8583.79) * mm, "end": v(-2315.49, 8567.53) * mm});
            skLineSegment(sketch, "E644", {"start": v(-2315.49, 8567.53) * mm, "end": v(-2282.8, 8545.18) * mm});
            skLineSegment(sketch, "E645", {"start": v(-2282.8, 8545.18) * mm, "end": v(-2267.1, 8517.29) * mm});
            skLineSegment(sketch, "E646", {"start": v(-2267.1, 8517.29) * mm, "end": v(-2266.26, 8484.4) * mm});
            skLineSegment(sketch, "E647", {"start": v(-2266.26, 8484.4) * mm, "end": v(-2278.09, 8447.08) * mm});
            skLineSegment(sketch, "E648", {"start": v(-2278.09, 8447.08) * mm, "end": v(-2300.44, 8405.86) * mm});
            skLineSegment(sketch, "E649", {"start": v(-2300.44, 8405.86) * mm, "end": v(-2331.14, 8361.29) * mm});
            skLineSegment(sketch, "E650", {"start": v(-2331.14, 8361.29) * mm, "end": v(-2368.05, 8313.91) * mm});
            skLineSegment(sketch, "E651", {"start": v(-2368.05, 8313.91) * mm, "end": v(-2408.98, 8264.28) * mm});
            skLineSegment(sketch, "E652", {"start": v(-2408.98, 8264.28) * mm, "end": v(-2451.79, 8212.95) * mm});
            skLineSegment(sketch, "E653", {"start": v(-2451.79, 8212.95) * mm, "end": v(-2494.3, 8160.45) * mm});
            skLineSegment(sketch, "E654", {"start": v(-2494.3, 8160.45) * mm, "end": v(-2534.38, 8107.35) * mm});
            skLineSegment(sketch, "E655", {"start": v(-2534.38, 8107.35) * mm, "end": v(-2569.84, 8054.18) * mm});
            skLineSegment(sketch, "E656", {"start": v(-2569.84, 8054.18) * mm, "end": v(-2598.52, 8001.5) * mm});
            skLineSegment(sketch, "E657", {"start": v(-2598.52, 8001.5) * mm, "end": v(-2618.27, 7949.84) * mm});
            skLineSegment(sketch, "E658", {"start": v(-2618.27, 7949.84) * mm, "end": v(-2626.92, 7899.76) * mm});
            skLineSegment(sketch, "E659", {"start": v(-2626.92, 7899.76) * mm, "end": v(-2621.99, 7842.58) * mm});
            skLineSegment(sketch, "E660", {"start": v(-2621.99, 7842.58) * mm, "end": v(-2609.63, 7776.94) * mm});
            skLineSegment(sketch, "E661", {"start": v(-2609.63, 7776.94) * mm, "end": v(-2593.62, 7717.73) * mm});
            skLineSegment(sketch, "E662", {"start": v(-2593.62, 7717.73) * mm, "end": v(-2574.03, 7664.63) * mm});
            skLineSegment(sketch, "E663", {"start": v(-2574.03, 7664.63) * mm, "end": v(-2550.94, 7617.34) * mm});
            skLineSegment(sketch, "E664", {"start": v(-2550.94, 7617.34) * mm, "end": v(-2524.41, 7575.51) * mm});
            skLineSegment(sketch, "E665", {"start": v(-2524.41, 7575.51) * mm, "end": v(-2494.54, 7538.85) * mm});
            skLineSegment(sketch, "E666", {"start": v(-2494.54, 7538.85) * mm, "end": v(-2461.4, 7507.02) * mm});
            skLineSegment(sketch, "E667", {"start": v(-2461.4, 7507.02) * mm, "end": v(-2425.07, 7479.72) * mm});
            skLineSegment(sketch, "E668", {"start": v(-2425.07, 7479.72) * mm, "end": v(-2385.62, 7456.61) * mm});
            skLineSegment(sketch, "E669", {"start": v(-2385.62, 7456.61) * mm, "end": v(-2343.14, 7437.39) * mm});
            skLineSegment(sketch, "E670", {"start": v(-2343.14, 7437.39) * mm, "end": v(-2297.69, 7421.73) * mm});
            skLineSegment(sketch, "E671", {"start": v(-2297.69, 7421.73) * mm, "end": v(-2249.36, 7409.31) * mm});
            skLineSegment(sketch, "E672", {"start": v(-2249.36, 7409.31) * mm, "end": v(-2198.23, 7399.82) * mm});
            skLineSegment(sketch, "E673", {"start": v(-2198.23, 7399.82) * mm, "end": v(-2144.37, 7392.94) * mm});
            skLineSegment(sketch, "E674", {"start": v(-2144.37, 7392.94) * mm, "end": v(-2087.86, 7388.34) * mm});
            skLineSegment(sketch, "E675", {"start": v(-2087.86, 7388.34) * mm, "end": v(-2028.78, 7385.71) * mm});
            skLineSegment(sketch, "E676", {"start": v(-2028.78, 7385.71) * mm, "end": v(-1967.2, 7384.73) * mm});
            skLineSegment(sketch, "E677", {"start": v(-1967.2, 7384.73) * mm, "end": v(-1904.75, 7385.14) * mm});
            skLineSegment(sketch, "E678", {"start": v(-1904.75, 7385.14) * mm, "end": v(-1844.65, 7387.07) * mm});
            skLineSegment(sketch, "E679", {"start": v(-1844.65, 7387.07) * mm, "end": v(-1787.1, 7390.84) * mm});
            skLineSegment(sketch, "E680", {"start": v(-1787.1, 7390.84) * mm, "end": v(-1732.16, 7396.77) * mm});
            skLineSegment(sketch, "E681", {"start": v(-1732.16, 7396.77) * mm, "end": v(-1679.9, 7405.18) * mm});
            skLineSegment(sketch, "E682", {"start": v(-1679.9, 7405.18) * mm, "end": v(-1670.47, 7407.32) * mm});
            skLineSegment(sketch, "E683", {"start": v(-4653.56, 8047.6) * mm, "end": v(-4743.08, 8009.25) * mm});
            skLineSegment(sketch, "E684", {"start": v(-4743.08, 8009.25) * mm, "end": v(-4832.64, 7972.3) * mm});
            skLineSegment(sketch, "E685", {"start": v(-4832.64, 7972.3) * mm, "end": v(-4922.26, 7936.74) * mm});
            skLineSegment(sketch, "E686", {"start": v(-4922.26, 7936.74) * mm, "end": v(-5011.98, 7902.58) * mm});
            skLineSegment(sketch, "E687", {"start": v(-5011.98, 7902.58) * mm, "end": v(-5101.82, 7869.8) * mm});
            skLineSegment(sketch, "E688", {"start": v(-5101.82, 7869.8) * mm, "end": v(-5191.8, 7838.41) * mm});
            skLineSegment(sketch, "E689", {"start": v(-5191.8, 7838.41) * mm, "end": v(-5281.96, 7808.4) * mm});
            skLineSegment(sketch, "E690", {"start": v(-5281.96, 7808.4) * mm, "end": v(-5372.32, 7779.74) * mm});
            skLineSegment(sketch, "E691", {"start": v(-5372.32, 7779.74) * mm, "end": v(-5462.9, 7752.44) * mm});
            skLineSegment(sketch, "E692", {"start": v(-5462.9, 7752.44) * mm, "end": v(-5553.73, 7726.5) * mm});
            skLineSegment(sketch, "E693", {"start": v(-5553.73, 7726.5) * mm, "end": v(-5644.83, 7701.9) * mm});
            skLineSegment(sketch, "E694", {"start": v(-5644.83, 7701.9) * mm, "end": v(-5736.24, 7678.65) * mm});
            skLineSegment(sketch, "E695", {"start": v(-5736.24, 7678.65) * mm, "end": v(-5827.98, 7656.73) * mm});
            skLineSegment(sketch, "E696", {"start": v(-5827.98, 7656.73) * mm, "end": v(-5920.08, 7636.14) * mm});
            skLineSegment(sketch, "E697", {"start": v(-5920.08, 7636.14) * mm, "end": v(-6012.56, 7616.86) * mm});
            skLineSegment(sketch, "E698", {"start": v(-6012.56, 7616.86) * mm, "end": v(-6105.44, 7598.9) * mm});
            skLineSegment(sketch, "E699", {"start": v(-6105.44, 7598.9) * mm, "end": v(-6198.76, 7582.25) * mm});
            skLineSegment(sketch, "E700", {"start": v(-6198.76, 7582.25) * mm, "end": v(-6292.54, 7566.9) * mm});
            skLineSegment(sketch, "E701", {"start": v(-6292.54, 7566.9) * mm, "end": v(-6386.81, 7552.84) * mm});
            skLineSegment(sketch, "E702", {"start": v(-6386.81, 7552.84) * mm, "end": v(-6481.6, 7540.07) * mm});
            skLineSegment(sketch, "E703", {"start": v(-6481.6, 7540.07) * mm, "end": v(-6576.92, 7528.58) * mm});
            skLineSegment(sketch, "E704", {"start": v(-6576.92, 7528.58) * mm, "end": v(-6672.81, 7518.37) * mm});
            skLineSegment(sketch, "E705", {"start": v(-6672.81, 7518.37) * mm, "end": v(-6769.3, 7509.42) * mm});
            skLineSegment(sketch, "E706", {"start": v(-6769.3, 7509.42) * mm, "end": v(-6866.4, 7501.74) * mm});
            skLineSegment(sketch, "E707", {"start": v(-6866.4, 7501.74) * mm, "end": v(-6939.58, 7511.35) * mm});
            skLineSegment(sketch, "E708", {"start": v(-6939.58, 7511.35) * mm, "end": v(-6991.43, 7527.6) * mm});
            skLineSegment(sketch, "E709", {"start": v(-6991.43, 7527.6) * mm, "end": v(-7024.13, 7549.93) * mm});
            skLineSegment(sketch, "E710", {"start": v(-7024.13, 7549.93) * mm, "end": v(-7039.82, 7577.82) * mm});
            skLineSegment(sketch, "E711", {"start": v(-7039.82, 7577.82) * mm, "end": v(-7040.67, 7610.7) * mm});
            skLineSegment(sketch, "E712", {"start": v(-7040.67, 7610.7) * mm, "end": v(-7028.84, 7648.03) * mm});
            skLineSegment(sketch, "E713", {"start": v(-7028.84, 7648.03) * mm, "end": v(-7006.49, 7689.26) * mm});
            skLineSegment(sketch, "E714", {"start": v(-7006.49, 7689.26) * mm, "end": v(-6975.78, 7733.84) * mm});
            skLineSegment(sketch, "E715", {"start": v(-6975.78, 7733.84) * mm, "end": v(-6938.88, 7781.23) * mm});
            skLineSegment(sketch, "E716", {"start": v(-6938.88, 7781.23) * mm, "end": v(-6897.94, 7830.87) * mm});
            skLineSegment(sketch, "E717", {"start": v(-6897.94, 7830.87) * mm, "end": v(-6855.13, 7882.22) * mm});
            skLineSegment(sketch, "E718", {"start": v(-6855.13, 7882.22) * mm, "end": v(-6812.61, 7934.72) * mm});
            skLineSegment(sketch, "E719", {"start": v(-6812.61, 7934.72) * mm, "end": v(-6772.55, 7987.84) * mm});
            skLineSegment(sketch, "E720", {"start": v(-6772.55, 7987.84) * mm, "end": v(-6737.09, 8041.02) * mm});
            skLineSegment(sketch, "E721", {"start": v(-6737.09, 8041.02) * mm, "end": v(-6708.4, 8093.71) * mm});
            skLineSegment(sketch, "E722", {"start": v(-6708.4, 8093.71) * mm, "end": v(-6688.66, 8145.37) * mm});
            skLineSegment(sketch, "E723", {"start": v(-6688.66, 8145.37) * mm, "end": v(-6680, 8195.45) * mm});
            skLineSegment(sketch, "E724", {"start": v(-6680, 8195.45) * mm, "end": v(-6684.94, 8252.64) * mm});
            skLineSegment(sketch, "E725", {"start": v(-6684.94, 8252.64) * mm, "end": v(-6697.3, 8318.28) * mm});
            skLineSegment(sketch, "E726", {"start": v(-6697.3, 8318.28) * mm, "end": v(-6713.33, 8377.48) * mm});
            skLineSegment(sketch, "E727", {"start": v(-6713.33, 8377.48) * mm, "end": v(-6732.94, 8430.56) * mm});
            skLineSegment(sketch, "E728", {"start": v(-6732.94, 8430.56) * mm, "end": v(-6756.06, 8477.85) * mm});
            skLineSegment(sketch, "E729", {"start": v(-6756.06, 8477.85) * mm, "end": v(-6782.6, 8519.66) * mm});
            skLineSegment(sketch, "E730", {"start": v(-6782.6, 8519.66) * mm, "end": v(-6812.49, 8556.3) * mm});
            skLineSegment(sketch, "E731", {"start": v(-6812.49, 8556.3) * mm, "end": v(-6845.65, 8588.12) * mm});
            skLineSegment(sketch, "E732", {"start": v(-6845.65, 8588.12) * mm, "end": v(-6882, 8615.4) * mm});
            skLineSegment(sketch, "E733", {"start": v(-6882, 8615.4) * mm, "end": v(-6921.47, 8638.5) * mm});
            skLineSegment(sketch, "E734", {"start": v(-6921.47, 8638.5) * mm, "end": v(-6963.97, 8657.7) * mm});
            skLineSegment(sketch, "E735", {"start": v(-6963.97, 8657.7) * mm, "end": v(-7009.44, 8673.35) * mm});
            skLineSegment(sketch, "E736", {"start": v(-7009.44, 8673.35) * mm, "end": v(-7057.78, 8685.75) * mm});
            skLineSegment(sketch, "E737", {"start": v(-7057.78, 8685.75) * mm, "end": v(-7108.93, 8695.23) * mm});
            skLineSegment(sketch, "E738", {"start": v(-7108.93, 8695.23) * mm, "end": v(-7162.8, 8702.1) * mm});
            skLineSegment(sketch, "E739", {"start": v(-7162.8, 8702.1) * mm, "end": v(-7219.32, 8706.7) * mm});
            skLineSegment(sketch, "E740", {"start": v(-7219.32, 8706.7) * mm, "end": v(-7278.4, 8709.32) * mm});
            skLineSegment(sketch, "E741", {"start": v(-7278.4, 8709.32) * mm, "end": v(-7339.98, 8710.3) * mm});
            skLineSegment(sketch, "E742", {"start": v(-7339.98, 8710.3) * mm, "end": v(-7402.43, 8709.89) * mm});
            skLineSegment(sketch, "E743", {"start": v(-7402.43, 8709.89) * mm, "end": v(-7462.53, 8707.96) * mm});
            skLineSegment(sketch, "E744", {"start": v(-7462.53, 8707.96) * mm, "end": v(-7520.08, 8704.2) * mm});
            skLineSegment(sketch, "E745", {"start": v(-7520.08, 8704.2) * mm, "end": v(-7575.02, 8698.28) * mm});
            skLineSegment(sketch, "E746", {"start": v(-7575.02, 8698.28) * mm, "end": v(-7627.26, 8689.88) * mm});
            skLineSegment(sketch, "E747", {"start": v(-7627.26, 8689.88) * mm, "end": v(-7676.73, 8678.68) * mm});
            skLineSegment(sketch, "E748", {"start": v(-7676.73, 8678.68) * mm, "end": v(-7723.35, 8664.37) * mm});
            skLineSegment(sketch, "E749", {"start": v(-7723.35, 8664.37) * mm, "end": v(-7767.04, 8646.63) * mm});
            skLineSegment(sketch, "E750", {"start": v(-7767.04, 8646.63) * mm, "end": v(-7807.72, 8625.13) * mm});
            skLineSegment(sketch, "E751", {"start": v(-7807.72, 8625.13) * mm, "end": v(-7845.32, 8599.56) * mm});
            skLineSegment(sketch, "E752", {"start": v(-7845.32, 8599.56) * mm, "end": v(-7879.75, 8569.6) * mm});
            skLineSegment(sketch, "E753", {"start": v(-7879.75, 8569.6) * mm, "end": v(-7910.94, 8534.92) * mm});
            skLineSegment(sketch, "E754", {"start": v(-7910.94, 8534.92) * mm, "end": v(-7938.8, 8495.21) * mm});
            skLineSegment(sketch, "E755", {"start": v(-7938.8, 8495.21) * mm, "end": v(-7963.28, 8450.16) * mm});
            skLineSegment(sketch, "E756", {"start": v(-7963.28, 8450.16) * mm, "end": v(-7984.27, 8399.43) * mm});
            skLineSegment(sketch, "E757", {"start": v(-7984.27, 8399.43) * mm, "end": v(-8001.7, 8342.71) * mm});
            skLineSegment(sketch, "E758", {"start": v(-8001.7, 8342.71) * mm, "end": v(-8015.5, 8279.69) * mm});
            skLineSegment(sketch, "E759", {"start": v(-8015.5, 8279.69) * mm, "end": v(-8024.4, 8219.73) * mm});
            skLineSegment(sketch, "E760", {"start": v(-8024.4, 8219.73) * mm, "end": v(-8024.9, 8195.45) * mm});
            skLineSegment(sketch, "E761", {"start": v(-8024.9, 8195.45) * mm, "end": v(-8022.1, 8170.65) * mm});
            skLineSegment(sketch, "E762", {"start": v(-8022.1, 8170.65) * mm, "end": v(-8016.26, 8145.37) * mm});
            skLineSegment(sketch, "E763", {"start": v(-8016.26, 8145.37) * mm, "end": v(-8007.64, 8119.7) * mm});
            skLineSegment(sketch, "E764", {"start": v(-8007.64, 8119.7) * mm, "end": v(-7996.52, 8093.71) * mm});
            skLineSegment(sketch, "E765", {"start": v(-7996.52, 8093.71) * mm, "end": v(-7983.17, 8067.46) * mm});
            skLineSegment(sketch, "E766", {"start": v(-7983.17, 8067.46) * mm, "end": v(-7967.85, 8041.02) * mm});
            skLineSegment(sketch, "E767", {"start": v(-7967.85, 8041.02) * mm, "end": v(-7950.84, 8014.46) * mm});
            skLineSegment(sketch, "E768", {"start": v(-7950.84, 8014.46) * mm, "end": v(-7932.4, 7987.84) * mm});
            skLineSegment(sketch, "E769", {"start": v(-7932.4, 7987.84) * mm, "end": v(-7912.82, 7961.24) * mm});
            skLineSegment(sketch, "E770", {"start": v(-7912.82, 7961.24) * mm, "end": v(-7892.35, 7934.72) * mm});
            skLineSegment(sketch, "E771", {"start": v(-7892.35, 7934.72) * mm, "end": v(-7871.27, 7908.36) * mm});
            skLineSegment(sketch, "E772", {"start": v(-7871.27, 7908.36) * mm, "end": v(-7849.85, 7882.22) * mm});
            skLineSegment(sketch, "E773", {"start": v(-7849.85, 7882.22) * mm, "end": v(-7828.35, 7856.36) * mm});
            skLineSegment(sketch, "E774", {"start": v(-7828.35, 7856.36) * mm, "end": v(-7807.05, 7830.87) * mm});
            skLineSegment(sketch, "E775", {"start": v(-7807.05, 7830.87) * mm, "end": v(-7786.22, 7805.8) * mm});
            skLineSegment(sketch, "E776", {"start": v(-7786.22, 7805.8) * mm, "end": v(-7766.13, 7781.23) * mm});
            skLineSegment(sketch, "E777", {"start": v(-7766.13, 7781.23) * mm, "end": v(-7747.04, 7757.22) * mm});
            skLineSegment(sketch, "E778", {"start": v(-7747.04, 7757.22) * mm, "end": v(-7729.24, 7733.84) * mm});
            skLineSegment(sketch, "E779", {"start": v(-7729.24, 7733.84) * mm, "end": v(-7712.98, 7711.17) * mm});
            skLineSegment(sketch, "E780", {"start": v(-7712.98, 7711.17) * mm, "end": v(-7698.54, 7689.26) * mm});
            skLineSegment(sketch, "E781", {"start": v(-7698.54, 7689.26) * mm, "end": v(-7686.19, 7668.2) * mm});
            skLineSegment(sketch, "E782", {"start": v(-7686.19, 7668.2) * mm, "end": v(-7676.2, 7648.03) * mm});
            skLineSegment(sketch, "E783", {"start": v(-7676.2, 7648.03) * mm, "end": v(-7668.83, 7628.84) * mm});
            skLineSegment(sketch, "E784", {"start": v(-7668.83, 7628.84) * mm, "end": v(-7664.36, 7610.7) * mm});
            skLineSegment(sketch, "E785", {"start": v(-7664.36, 7610.7) * mm, "end": v(-7663.06, 7593.67) * mm});
            skLineSegment(sketch, "E786", {"start": v(-7663.06, 7593.67) * mm, "end": v(-7665.2, 7577.82) * mm});
            skLineSegment(sketch, "E787", {"start": v(-7665.2, 7577.82) * mm, "end": v(-7671.05, 7563.22) * mm});
            skLineSegment(sketch, "E788", {"start": v(-7671.05, 7563.22) * mm, "end": v(-7680.88, 7549.93) * mm});
            skLineSegment(sketch, "E789", {"start": v(-7680.88, 7549.93) * mm, "end": v(-7694.95, 7538.04) * mm});
            skLineSegment(sketch, "E790", {"start": v(-7694.95, 7538.04) * mm, "end": v(-7713.55, 7527.6) * mm});
            skLineSegment(sketch, "E791", {"start": v(-7713.55, 7527.6) * mm, "end": v(-7736.93, 7518.67) * mm});
            skLineSegment(sketch, "E792", {"start": v(-7736.93, 7518.67) * mm, "end": v(-7765.38, 7511.35) * mm});
            skLineSegment(sketch, "E793", {"start": v(-7765.38, 7511.35) * mm, "end": v(-7799.15, 7505.68) * mm});
            skLineSegment(sketch, "E794", {"start": v(-7799.15, 7505.68) * mm, "end": v(-7838.52, 7501.74) * mm});
            skLineSegment(sketch, "E795", {"start": v(-7838.52, 7501.74) * mm, "end": v(-7935.63, 7509.42) * mm});
            skLineSegment(sketch, "E796", {"start": v(-7935.63, 7509.42) * mm, "end": v(-8032.12, 7518.37) * mm});
            skLineSegment(sketch, "E797", {"start": v(-8032.12, 7518.37) * mm, "end": v(-8128.01, 7528.58) * mm});
            skLineSegment(sketch, "E798", {"start": v(-8128.01, 7528.58) * mm, "end": v(-8223.34, 7540.07) * mm});
            skLineSegment(sketch, "E799", {"start": v(-8223.34, 7540.07) * mm, "end": v(-8318.13, 7552.84) * mm});
            skLineSegment(sketch, "E800", {"start": v(-8318.13, 7552.84) * mm, "end": v(-8412.4, 7566.9) * mm});
            skLineSegment(sketch, "E801", {"start": v(-8412.4, 7566.9) * mm, "end": v(-8506.18, 7582.25) * mm});
            skLineSegment(sketch, "E802", {"start": v(-8506.18, 7582.25) * mm, "end": v(-8599.5, 7598.9) * mm});
            skLineSegment(sketch, "E803", {"start": v(-8599.5, 7598.9) * mm, "end": v(-8692.4, 7616.86) * mm});
            skLineSegment(sketch, "E804", {"start": v(-8692.4, 7616.86) * mm, "end": v(-8784.88, 7636.14) * mm});
            skLineSegment(sketch, "E805", {"start": v(-8784.88, 7636.14) * mm, "end": v(-8876.98, 7656.73) * mm});
            skLineSegment(sketch, "E806", {"start": v(-8876.98, 7656.73) * mm, "end": v(-8968.72, 7678.65) * mm});
            skLineSegment(sketch, "E807", {"start": v(-8968.72, 7678.65) * mm, "end": v(-9060.13, 7701.9) * mm});
            skLineSegment(sketch, "E808", {"start": v(-9060.13, 7701.9) * mm, "end": v(-9151.25, 7726.5) * mm});
            skLineSegment(sketch, "E809", {"start": v(-9151.25, 7726.5) * mm, "end": v(-9242.08, 7752.44) * mm});
            skLineSegment(sketch, "E810", {"start": v(-9242.08, 7752.44) * mm, "end": v(-9332.67, 7779.74) * mm});
            skLineSegment(sketch, "E811", {"start": v(-9332.67, 7779.74) * mm, "end": v(-9423.03, 7808.4) * mm});
            skLineSegment(sketch, "E812", {"start": v(-9423.03, 7808.4) * mm, "end": v(-9513.2, 7838.41) * mm});
            skLineSegment(sketch, "E813", {"start": v(-9513.2, 7838.41) * mm, "end": v(-9603.2, 7869.8) * mm});
            skLineSegment(sketch, "E814", {"start": v(-9603.2, 7869.8) * mm, "end": v(-9693.05, 7902.58) * mm});
            skLineSegment(sketch, "E815", {"start": v(-9693.05, 7902.58) * mm, "end": v(-9782.78, 7936.74) * mm});
            skLineSegment(sketch, "E816", {"start": v(-9782.78, 7936.74) * mm, "end": v(-9872.43, 7972.3) * mm});
            skLineSegment(sketch, "E817", {"start": v(-9872.43, 7972.3) * mm, "end": v(-9962, 8009.25) * mm});
            skLineSegment(sketch, "E818", {"start": v(-9962, 8009.25) * mm, "end": v(-10051.55, 8047.6) * mm});
            skLineSegment(sketch, "E819", {"start": v(-10051.55, 2649.62) * mm, "end": v(-9962, 2687.98) * mm});
            skLineSegment(sketch, "E820", {"start": v(-9962, 2687.98) * mm, "end": v(-9872.43, 2724.93) * mm});
            skLineSegment(sketch, "E821", {"start": v(-9872.43, 2724.93) * mm, "end": v(-9782.78, 2760.49) * mm});
            skLineSegment(sketch, "E822", {"start": v(-9782.78, 2760.49) * mm, "end": v(-9693.05, 2794.65) * mm});
            skLineSegment(sketch, "E823", {"start": v(-9693.05, 2794.65) * mm, "end": v(-9603.2, 2827.42) * mm});
            skLineSegment(sketch, "E824", {"start": v(-9603.2, 2827.42) * mm, "end": v(-9513.2, 2858.81) * mm});
            skLineSegment(sketch, "E825", {"start": v(-9513.2, 2858.81) * mm, "end": v(-9423.03, 2888.83) * mm});
            skLineSegment(sketch, "E826", {"start": v(-9423.03, 2888.83) * mm, "end": v(-9332.67, 2917.48) * mm});
            skLineSegment(sketch, "E827", {"start": v(-9332.67, 2917.48) * mm, "end": v(-9242.08, 2944.77) * mm});
            skLineSegment(sketch, "E828", {"start": v(-9242.08, 2944.77) * mm, "end": v(-9151.25, 2970.71) * mm});
            skLineSegment(sketch, "E829", {"start": v(-9151.25, 2970.71) * mm, "end": v(-9060.13, 2995.3) * mm});
            skLineSegment(sketch, "E830", {"start": v(-9060.13, 2995.3) * mm, "end": v(-8968.72, 3018.55) * mm});
            skLineSegment(sketch, "E831", {"start": v(-8968.72, 3018.55) * mm, "end": v(-8876.98, 3040.46) * mm});
            skLineSegment(sketch, "E832", {"start": v(-8876.98, 3040.46) * mm, "end": v(-8784.88, 3061.04) * mm});
            skLineSegment(sketch, "E833", {"start": v(-8784.88, 3061.04) * mm, "end": v(-8692.4, 3080.3) * mm});
            skLineSegment(sketch, "E834", {"start": v(-8692.4, 3080.3) * mm, "end": v(-8599.5, 3098.25) * mm});
            skLineSegment(sketch, "E835", {"start": v(-8599.5, 3098.25) * mm, "end": v(-8506.18, 3114.89) * mm});
            skLineSegment(sketch, "E836", {"start": v(-8506.18, 3114.89) * mm, "end": v(-8412.4, 3130.22) * mm});
            skLineSegment(sketch, "E837", {"start": v(-8412.4, 3130.22) * mm, "end": v(-8318.13, 3144.26) * mm});
            skLineSegment(sketch, "E838", {"start": v(-8318.13, 3144.26) * mm, "end": v(-8223.34, 3157) * mm});
            skLineSegment(sketch, "E839", {"start": v(-8223.34, 3157) * mm, "end": v(-8128.01, 3168.47) * mm});
            skLineSegment(sketch, "E840", {"start": v(-8128.01, 3168.47) * mm, "end": v(-8032.12, 3178.66) * mm});
            skLineSegment(sketch, "E841", {"start": v(-8032.12, 3178.66) * mm, "end": v(-7935.63, 3187.58) * mm});
            skLineSegment(sketch, "E842", {"start": v(-7935.63, 3187.58) * mm, "end": v(-7838.52, 3195.23) * mm});
            skLineSegment(sketch, "E843", {"start": v(-7838.52, 3195.23) * mm, "end": v(-7765.38, 3185.64) * mm});
            skLineSegment(sketch, "E844", {"start": v(-7765.38, 3185.64) * mm, "end": v(-7713.55, 3169.4) * mm});
            skLineSegment(sketch, "E845", {"start": v(-7713.55, 3169.4) * mm, "end": v(-7680.88, 3147.08) * mm});
            skLineSegment(sketch, "E846", {"start": v(-7680.88, 3147.08) * mm, "end": v(-7665.2, 3119.21) * mm});
            skLineSegment(sketch, "E847", {"start": v(-7665.2, 3119.21) * mm, "end": v(-7664.36, 3086.35) * mm});
            skLineSegment(sketch, "E848", {"start": v(-7664.36, 3086.35) * mm, "end": v(-7676.2, 3049.04) * mm});
            skLineSegment(sketch, "E849", {"start": v(-7676.2, 3049.04) * mm, "end": v(-7698.54, 3007.83) * mm});
            skLineSegment(sketch, "E850", {"start": v(-7698.54, 3007.83) * mm, "end": v(-7729.24, 2963.27) * mm});
            skLineSegment(sketch, "E851", {"start": v(-7729.24, 2963.27) * mm, "end": v(-7766.13, 2915.9) * mm});
            skLineSegment(sketch, "E852", {"start": v(-7766.13, 2915.9) * mm, "end": v(-7807.05, 2866.28) * mm});
            skLineSegment(sketch, "E853", {"start": v(-7807.05, 2866.28) * mm, "end": v(-7849.85, 2814.95) * mm});
            skLineSegment(sketch, "E854", {"start": v(-7849.85, 2814.95) * mm, "end": v(-7892.35, 2762.46) * mm});
            skLineSegment(sketch, "E855", {"start": v(-7892.35, 2762.46) * mm, "end": v(-7932.4, 2709.35) * mm});
            skLineSegment(sketch, "E856", {"start": v(-7932.4, 2709.35) * mm, "end": v(-7967.85, 2656.19) * mm});
            skLineSegment(sketch, "E857", {"start": v(-7967.85, 2656.19) * mm, "end": v(-7996.52, 2603.5) * mm});
            skLineSegment(sketch, "E858", {"start": v(-7996.52, 2603.5) * mm, "end": v(-8016.26, 2551.85) * mm});
            skLineSegment(sketch, "E859", {"start": v(-8016.26, 2551.85) * mm, "end": v(-8024.9, 2501.78) * mm});
            skLineSegment(sketch, "E860", {"start": v(-8024.9, 2501.78) * mm, "end": v(-8019.98, 2444.59) * mm});
            skLineSegment(sketch, "E861", {"start": v(-8019.98, 2444.59) * mm, "end": v(-8007.62, 2378.95) * mm});
            skLineSegment(sketch, "E862", {"start": v(-8007.62, 2378.95) * mm, "end": v(-7991.61, 2319.74) * mm});
            skLineSegment(sketch, "E863", {"start": v(-7991.61, 2319.74) * mm, "end": v(-7972.02, 2266.65) * mm});
            skLineSegment(sketch, "E864", {"start": v(-7972.02, 2266.65) * mm, "end": v(-7948.93, 2219.35) * mm});
            skLineSegment(sketch, "E865", {"start": v(-7948.93, 2219.35) * mm, "end": v(-7922.4, 2177.53) * mm});
            skLineSegment(sketch, "E866", {"start": v(-7922.4, 2177.53) * mm, "end": v(-7892.53, 2140.86) * mm});
            skLineSegment(sketch, "E867", {"start": v(-7892.53, 2140.86) * mm, "end": v(-7859.4, 2109.03) * mm});
            skLineSegment(sketch, "E868", {"start": v(-7859.4, 2109.03) * mm, "end": v(-7823.06, 2081.73) * mm});
            skLineSegment(sketch, "E869", {"start": v(-7823.06, 2081.73) * mm, "end": v(-7783.61, 2058.62) * mm});
            skLineSegment(sketch, "E870", {"start": v(-7783.61, 2058.62) * mm, "end": v(-7741.12, 2039.4) * mm});
            skLineSegment(sketch, "E871", {"start": v(-7741.12, 2039.4) * mm, "end": v(-7695.68, 2023.74) * mm});
            skLineSegment(sketch, "E872", {"start": v(-7695.68, 2023.74) * mm, "end": v(-7647.35, 2011.32) * mm});
            skLineSegment(sketch, "E873", {"start": v(-7647.35, 2011.32) * mm, "end": v(-7596.22, 2001.83) * mm});
            skLineSegment(sketch, "E874", {"start": v(-7596.22, 2001.83) * mm, "end": v(-7542.36, 1994.95) * mm});
            skLineSegment(sketch, "E875", {"start": v(-7542.36, 1994.95) * mm, "end": v(-7485.85, 1990.35) * mm});
            skLineSegment(sketch, "E876", {"start": v(-7485.85, 1990.35) * mm, "end": v(-7426.77, 1987.72) * mm});
            skLineSegment(sketch, "E877", {"start": v(-7426.77, 1987.72) * mm, "end": v(-7365.2, 1986.74) * mm});
            skLineSegment(sketch, "E878", {"start": v(-7365.2, 1986.74) * mm, "end": v(-7302.74, 1987.15) * mm});
            skLineSegment(sketch, "E879", {"start": v(-7302.74, 1987.15) * mm, "end": v(-7242.65, 1989.08) * mm});
            skLineSegment(sketch, "E880", {"start": v(-7242.65, 1989.08) * mm, "end": v(-7185.1, 1992.85) * mm});
            skLineSegment(sketch, "E881", {"start": v(-7185.1, 1992.85) * mm, "end": v(-7130.15, 1998.78) * mm});
            skLineSegment(sketch, "E882", {"start": v(-7130.15, 1998.78) * mm, "end": v(-7077.9, 2007.2) * mm});
            skLineSegment(sketch, "E883", {"start": v(-7077.9, 2007.2) * mm, "end": v(-7028.43, 2018.4) * mm});
            skLineSegment(sketch, "E884", {"start": v(-7028.43, 2018.4) * mm, "end": v(-6981.8, 2032.73) * mm});
            skLineSegment(sketch, "E885", {"start": v(-6981.8, 2032.73) * mm, "end": v(-6938.1, 2050.49) * mm});
            skLineSegment(sketch, "E886", {"start": v(-6938.1, 2050.49) * mm, "end": v(-6897.42, 2072) * mm});
            skLineSegment(sketch, "E887", {"start": v(-6897.42, 2072) * mm, "end": v(-6859.8, 2097.59) * mm});
            skLineSegment(sketch, "E888", {"start": v(-6859.8, 2097.59) * mm, "end": v(-6825.36, 2127.57) * mm});
            skLineSegment(sketch, "E889", {"start": v(-6825.36, 2127.57) * mm, "end": v(-6794.15, 2162.26) * mm});
            skLineSegment(sketch, "E890", {"start": v(-6794.15, 2162.26) * mm, "end": v(-6766.27, 2201.98) * mm});
            skLineSegment(sketch, "E891", {"start": v(-6766.27, 2201.98) * mm, "end": v(-6741.77, 2247.05) * mm});
            skLineSegment(sketch, "E892", {"start": v(-6741.77, 2247.05) * mm, "end": v(-6720.75, 2297.79) * mm});
            skLineSegment(sketch, "E893", {"start": v(-6720.75, 2297.79) * mm, "end": v(-6703.28, 2354.5) * mm});
            skLineSegment(sketch, "E894", {"start": v(-6703.28, 2354.5) * mm, "end": v(-6689.44, 2417.54) * mm});
            skLineSegment(sketch, "E895", {"start": v(-6689.44, 2417.54) * mm, "end": v(-6680.52, 2477.5) * mm});
            skLineSegment(sketch, "E896", {"start": v(-6680.52, 2477.5) * mm, "end": v(-6680, 2501.78) * mm});
            skLineSegment(sketch, "E897", {"start": v(-6680, 2501.78) * mm, "end": v(-6682.8, 2526.58) * mm});
            skLineSegment(sketch, "E898", {"start": v(-6682.8, 2526.58) * mm, "end": v(-6688.66, 2551.85) * mm});
            skLineSegment(sketch, "E899", {"start": v(-6688.66, 2551.85) * mm, "end": v(-6697.28, 2577.51) * mm});
            skLineSegment(sketch, "E900", {"start": v(-6697.28, 2577.51) * mm, "end": v(-6708.4, 2603.5) * mm});
            skLineSegment(sketch, "E901", {"start": v(-6708.4, 2603.5) * mm, "end": v(-6721.77, 2629.75) * mm});
            skLineSegment(sketch, "E902", {"start": v(-6721.77, 2629.75) * mm, "end": v(-6737.09, 2656.19) * mm});
            skLineSegment(sketch, "E903", {"start": v(-6737.09, 2656.19) * mm, "end": v(-6754.1, 2682.74) * mm});
            skLineSegment(sketch, "E904", {"start": v(-6754.1, 2682.74) * mm, "end": v(-6772.55, 2709.35) * mm});
            skLineSegment(sketch, "E905", {"start": v(-6772.55, 2709.35) * mm, "end": v(-6792.14, 2735.95) * mm});
            skLineSegment(sketch, "E906", {"start": v(-6792.14, 2735.95) * mm, "end": v(-6812.61, 2762.46) * mm});
            skLineSegment(sketch, "E907", {"start": v(-6812.61, 2762.46) * mm, "end": v(-6833.7, 2788.81) * mm});
            skLineSegment(sketch, "E908", {"start": v(-6833.7, 2788.81) * mm, "end": v(-6855.13, 2814.95) * mm});
            skLineSegment(sketch, "E909", {"start": v(-6855.13, 2814.95) * mm, "end": v(-6876.64, 2840.8) * mm});
            skLineSegment(sketch, "E910", {"start": v(-6876.64, 2840.8) * mm, "end": v(-6897.94, 2866.28) * mm});
            skLineSegment(sketch, "E911", {"start": v(-6897.94, 2866.28) * mm, "end": v(-6918.78, 2891.34) * mm});
            skLineSegment(sketch, "E912", {"start": v(-6918.78, 2891.34) * mm, "end": v(-6938.88, 2915.9) * mm});
            skLineSegment(sketch, "E913", {"start": v(-6938.88, 2915.9) * mm, "end": v(-6957.97, 2939.9) * mm});
            skLineSegment(sketch, "E914", {"start": v(-6957.97, 2939.9) * mm, "end": v(-6975.78, 2963.27) * mm});
            skLineSegment(sketch, "E915", {"start": v(-6975.78, 2963.27) * mm, "end": v(-6992.04, 2985.93) * mm});
            skLineSegment(sketch, "E916", {"start": v(-6992.04, 2985.93) * mm, "end": v(-7006.49, 3007.83) * mm});
            skLineSegment(sketch, "E917", {"start": v(-7006.49, 3007.83) * mm, "end": v(-7018.84, 3028.89) * mm});
            skLineSegment(sketch, "E918", {"start": v(-7018.84, 3028.89) * mm, "end": v(-7028.84, 3049.04) * mm});
            skLineSegment(sketch, "E919", {"start": v(-7028.84, 3049.04) * mm, "end": v(-7036.2, 3068.21) * mm});
            skLineSegment(sketch, "E920", {"start": v(-7036.2, 3068.21) * mm, "end": v(-7040.67, 3086.35) * mm});
            skLineSegment(sketch, "E921", {"start": v(-7040.67, 3086.35) * mm, "end": v(-7041.96, 3103.37) * mm});
            skLineSegment(sketch, "E922", {"start": v(-7041.96, 3103.37) * mm, "end": v(-7039.82, 3119.21) * mm});
            skLineSegment(sketch, "E923", {"start": v(-7039.82, 3119.21) * mm, "end": v(-7033.96, 3133.8) * mm});
            skLineSegment(sketch, "E924", {"start": v(-7033.96, 3133.8) * mm, "end": v(-7024.13, 3147.08) * mm});
            skLineSegment(sketch, "E925", {"start": v(-7024.13, 3147.08) * mm, "end": v(-7010.04, 3158.97) * mm});
            skLineSegment(sketch, "E926", {"start": v(-7010.04, 3158.97) * mm, "end": v(-6991.43, 3169.4) * mm});
            skLineSegment(sketch, "E927", {"start": v(-6991.43, 3169.4) * mm, "end": v(-6968.04, 3178.32) * mm});
            skLineSegment(sketch, "E928", {"start": v(-6968.04, 3178.32) * mm, "end": v(-6939.58, 3185.64) * mm});
            skLineSegment(sketch, "E929", {"start": v(-6939.58, 3185.64) * mm, "end": v(-6905.79, 3191.3) * mm});
            skLineSegment(sketch, "E930", {"start": v(-6905.79, 3191.3) * mm, "end": v(-6866.4, 3195.23) * mm});
            skLineSegment(sketch, "E931", {"start": v(-6866.4, 3195.23) * mm, "end": v(-6769.3, 3187.58) * mm});
            skLineSegment(sketch, "E932", {"start": v(-6769.3, 3187.58) * mm, "end": v(-6672.81, 3178.66) * mm});
            skLineSegment(sketch, "E933", {"start": v(-6672.81, 3178.66) * mm, "end": v(-6576.92, 3168.47) * mm});
            skLineSegment(sketch, "E934", {"start": v(-6576.92, 3168.47) * mm, "end": v(-6481.6, 3157) * mm});
            skLineSegment(sketch, "E935", {"start": v(-6481.6, 3157) * mm, "end": v(-6386.81, 3144.26) * mm});
            skLineSegment(sketch, "E936", {"start": v(-6386.81, 3144.26) * mm, "end": v(-6292.54, 3130.22) * mm});
            skLineSegment(sketch, "E937", {"start": v(-6292.54, 3130.22) * mm, "end": v(-6198.76, 3114.89) * mm});
            skLineSegment(sketch, "E938", {"start": v(-6198.76, 3114.89) * mm, "end": v(-6105.44, 3098.25) * mm});
            skLineSegment(sketch, "E939", {"start": v(-6105.44, 3098.25) * mm, "end": v(-6012.56, 3080.3) * mm});
            skLineSegment(sketch, "E940", {"start": v(-6012.56, 3080.3) * mm, "end": v(-5920.08, 3061.04) * mm});
            skLineSegment(sketch, "E941", {"start": v(-5920.08, 3061.04) * mm, "end": v(-5827.98, 3040.46) * mm});
            skLineSegment(sketch, "E942", {"start": v(-5827.98, 3040.46) * mm, "end": v(-5736.24, 3018.55) * mm});
            skLineSegment(sketch, "E943", {"start": v(-5736.24, 3018.55) * mm, "end": v(-5644.83, 2995.3) * mm});
            skLineSegment(sketch, "E944", {"start": v(-5644.83, 2995.3) * mm, "end": v(-5553.73, 2970.71) * mm});
            skLineSegment(sketch, "E945", {"start": v(-5553.73, 2970.71) * mm, "end": v(-5462.9, 2944.77) * mm});
            skLineSegment(sketch, "E946", {"start": v(-5462.9, 2944.77) * mm, "end": v(-5372.32, 2917.48) * mm});
            skLineSegment(sketch, "E947", {"start": v(-5372.32, 2917.48) * mm, "end": v(-5281.96, 2888.83) * mm});
            skLineSegment(sketch, "E948", {"start": v(-5281.96, 2888.83) * mm, "end": v(-5191.8, 2858.81) * mm});
            skLineSegment(sketch, "E949", {"start": v(-5191.8, 2858.81) * mm, "end": v(-5101.82, 2827.42) * mm});
            skLineSegment(sketch, "E950", {"start": v(-5101.82, 2827.42) * mm, "end": v(-5011.98, 2794.65) * mm});
            skLineSegment(sketch, "E951", {"start": v(-5011.98, 2794.65) * mm, "end": v(-4922.26, 2760.49) * mm});
            skLineSegment(sketch, "E952", {"start": v(-4922.26, 2760.49) * mm, "end": v(-4832.64, 2724.93) * mm});
            skLineSegment(sketch, "E953", {"start": v(-4832.64, 2724.93) * mm, "end": v(-4743.08, 2687.98) * mm});
            skLineSegment(sketch, "E954", {"start": v(-4743.08, 2687.98) * mm, "end": v(-4653.56, 2649.62) * mm});
            skLineSegment(sketch, "E955", {"start": v(-4653.56, 2649.62) * mm, "end": v(-4615.18, 2739.14) * mm});
            skLineSegment(sketch, "E956", {"start": v(-4615.18, 2739.14) * mm, "end": v(-4578.2, 2828.7) * mm});
            skLineSegment(sketch, "E957", {"start": v(-4578.2, 2828.7) * mm, "end": v(-4542.63, 2918.32) * mm});
            skLineSegment(sketch, "E958", {"start": v(-4542.63, 2918.32) * mm, "end": v(-4508.45, 3008.04) * mm});
            skLineSegment(sketch, "E959", {"start": v(-4508.45, 3008.04) * mm, "end": v(-4475.66, 3097.88) * mm});
            skLineSegment(sketch, "E960", {"start": v(-4475.66, 3097.88) * mm, "end": v(-4444.25, 3187.86) * mm});
            skLineSegment(sketch, "E961", {"start": v(-4444.25, 3187.86) * mm, "end": v(-4414.22, 3278.01) * mm});
            skLineSegment(sketch, "E962", {"start": v(-4414.22, 3278.01) * mm, "end": v(-4385.56, 3368.36) * mm});
            skLineSegment(sketch, "E963", {"start": v(-4385.56, 3368.36) * mm, "end": v(-4358.26, 3458.94) * mm});
            skLineSegment(sketch, "E964", {"start": v(-4358.26, 3458.94) * mm, "end": v(-4332.31, 3549.77) * mm});
            skLineSegment(sketch, "E965", {"start": v(-4332.31, 3549.77) * mm, "end": v(-4307.72, 3640.87) * mm});
            skLineSegment(sketch, "E966", {"start": v(-4307.72, 3640.87) * mm, "end": v(-4284.46, 3732.28) * mm});
            skLineSegment(sketch, "E967", {"start": v(-4284.46, 3732.28) * mm, "end": v(-4262.55, 3824.02) * mm});
            skLineSegment(sketch, "E968", {"start": v(-4262.55, 3824.02) * mm, "end": v(-4241.96, 3916.11) * mm});
            skLineSegment(sketch, "E969", {"start": v(-4241.96, 3916.11) * mm, "end": v(-4222.7, 4008.59) * mm});
            skLineSegment(sketch, "E970", {"start": v(-4222.7, 4008.59) * mm, "end": v(-4204.74, 4101.47) * mm});
            skLineSegment(sketch, "E971", {"start": v(-4204.74, 4101.47) * mm, "end": v(-4188.1, 4194.8) * mm});
            skLineSegment(sketch, "E972", {"start": v(-4188.1, 4194.8) * mm, "end": v(-4172.77, 4288.58) * mm});
            skLineSegment(sketch, "E973", {"start": v(-4172.77, 4288.58) * mm, "end": v(-4158.73, 4382.85) * mm});
            skLineSegment(sketch, "E974", {"start": v(-4158.73, 4382.85) * mm, "end": v(-4145.98, 4477.64) * mm});
            skLineSegment(sketch, "E975", {"start": v(-4145.98, 4477.64) * mm, "end": v(-4134.51, 4572.96) * mm});
            skLineSegment(sketch, "E976", {"start": v(-4134.51, 4572.96) * mm, "end": v(-4124.33, 4668.86) * mm});
            skLineSegment(sketch, "E977", {"start": v(-4124.33, 4668.86) * mm, "end": v(-4115.4, 4765.35) * mm});
            skLineSegment(sketch, "E978", {"start": v(-4115.4, 4765.35) * mm, "end": v(-4107.75, 4862.45) * mm});
            skLineSegment(sketch, "E979", {"start": v(-4107.75, 4862.45) * mm, "end": v(-4117.35, 4935.63) * mm});
            skLineSegment(sketch, "E980", {"start": v(-4117.35, 4935.63) * mm, "end": v(-4133.59, 4987.48) * mm});
            skLineSegment(sketch, "E981", {"start": v(-4133.59, 4987.48) * mm, "end": v(-4155.92, 5020.17) * mm});
            skLineSegment(sketch, "E982", {"start": v(-4155.92, 5020.17) * mm, "end": v(-4183.8, 5035.85) * mm});
            skLineSegment(sketch, "E983", {"start": v(-4183.8, 5035.85) * mm, "end": v(-4216.67, 5036.7) * mm});
            skLineSegment(sketch, "E984", {"start": v(-4216.67, 5036.7) * mm, "end": v(-4254, 5024.87) * mm});
            skLineSegment(sketch, "E985", {"start": v(-4254, 5024.87) * mm, "end": v(-4295.21, 5002.52) * mm});
            skLineSegment(sketch, "E986", {"start": v(-4295.21, 5002.52) * mm, "end": v(-4339.79, 4971.82) * mm});
            skLineSegment(sketch, "E987", {"start": v(-4339.79, 4971.82) * mm, "end": v(-4387.16, 4934.92) * mm});
            skLineSegment(sketch, "E988", {"start": v(-4387.16, 4934.92) * mm, "end": v(-4436.79, 4893.98) * mm});
            skLineSegment(sketch, "E989", {"start": v(-4436.79, 4893.98) * mm, "end": v(-4488.12, 4851.18) * mm});
            skLineSegment(sketch, "E990", {"start": v(-4488.12, 4851.18) * mm, "end": v(-4540.61, 4808.66) * mm});
            skLineSegment(sketch, "E991", {"start": v(-4540.61, 4808.66) * mm, "end": v(-4593.71, 4768.6) * mm});
            skLineSegment(sketch, "E992", {"start": v(-4593.71, 4768.6) * mm, "end": v(-4646.87, 4733.14) * mm});
            skLineSegment(sketch, "E993", {"start": v(-4646.87, 4733.14) * mm, "end": v(-4699.54, 4704.46) * mm});
            skLineSegment(sketch, "E994", {"start": v(-4699.54, 4704.46) * mm, "end": v(-4751.18, 4684.72) * mm});
            skLineSegment(sketch, "E995", {"start": v(-4751.18, 4684.72) * mm, "end": v(-4801.23, 4676.06) * mm});
            skLineSegment(sketch, "E996", {"start": v(-4801.23, 4676.06) * mm, "end": v(-4858.4, 4681) * mm});
            skLineSegment(sketch, "E997", {"start": v(-4858.4, 4681) * mm, "end": v(-4924.04, 4693.35) * mm});
            skLineSegment(sketch, "E998", {"start": v(-4924.04, 4693.35) * mm, "end": v(-4983.25, 4709.37) * mm});
            skLineSegment(sketch, "E999", {"start": v(-4983.25, 4709.37) * mm, "end": v(-5036.34, 4728.97) * mm});
            skLineSegment(sketch, "E1000", {"start": v(-5036.34, 4728.97) * mm, "end": v(-5083.64, 4752.08) * mm});
            skLineSegment(sketch, "E1001", {"start": v(-5083.64, 4752.08) * mm, "end": v(-5125.46, 4778.61) * mm});
            skLineSegment(sketch, "E1002", {"start": v(-5125.46, 4778.61) * mm, "end": v(-5162.12, 4808.5) * mm});
            skLineSegment(sketch, "E1003", {"start": v(-5162.12, 4808.5) * mm, "end": v(-5193.95, 4841.66) * mm});
            skLineSegment(sketch, "E1004", {"start": v(-5193.95, 4841.66) * mm, "end": v(-5221.26, 4878) * mm});
            skLineSegment(sketch, "E1005", {"start": v(-5221.26, 4878) * mm, "end": v(-5244.36, 4917.47) * mm});
            skLineSegment(sketch, "E1006", {"start": v(-5244.36, 4917.47) * mm, "end": v(-5263.59, 4959.97) * mm});
            skLineSegment(sketch, "E1007", {"start": v(-5263.59, 4959.97) * mm, "end": v(-5279.25, 5005.43) * mm});
            skLineSegment(sketch, "E1008", {"start": v(-5279.25, 5005.43) * mm, "end": v(-5291.66, 5053.78) * mm});
            skLineSegment(sketch, "E1009", {"start": v(-5291.66, 5053.78) * mm, "end": v(-5301.15, 5104.92) * mm});
            skLineSegment(sketch, "E1010", {"start": v(-5301.15, 5104.92) * mm, "end": v(-5308.04, 5158.8) * mm});
            skLineSegment(sketch, "E1011", {"start": v(-5308.04, 5158.8) * mm, "end": v(-5312.63, 5215.31) * mm});
            skLineSegment(sketch, "E1012", {"start": v(-5312.63, 5215.31) * mm, "end": v(-5315.26, 5274.4) * mm});
            skLineSegment(sketch, "E1013", {"start": v(-5315.26, 5274.4) * mm, "end": v(-5316.24, 5335.97) * mm});
            skLineSegment(sketch, "E1014", {"start": v(-5316.24, 5335.97) * mm, "end": v(-5315.83, 5398.43) * mm});
            skLineSegment(sketch, "E1015", {"start": v(-5315.83, 5398.43) * mm, "end": v(-5313.9, 5458.52) * mm});
            skLineSegment(sketch, "E1016", {"start": v(-5313.9, 5458.52) * mm, "end": v(-5310.13, 5516.08) * mm});
            skLineSegment(sketch, "E1017", {"start": v(-5310.13, 5516.08) * mm, "end": v(-5304.2, 5571.01) * mm});
            skLineSegment(sketch, "E1018", {"start": v(-5304.2, 5571.01) * mm, "end": v(-5295.8, 5623.26) * mm});
            skLineSegment(sketch, "E1019", {"start": v(-5295.8, 5623.26) * mm, "end": v(-5284.58, 5672.73) * mm});
            skLineSegment(sketch, "E1020", {"start": v(-5284.58, 5672.73) * mm, "end": v(-5270.26, 5719.35) * mm});
            skLineSegment(sketch, "E1021", {"start": v(-5270.26, 5719.35) * mm, "end": v(-5252.5, 5763.04) * mm});
            skLineSegment(sketch, "E1022", {"start": v(-5252.5, 5763.04) * mm, "end": v(-5230.99, 5803.73) * mm});
            skLineSegment(sketch, "E1023", {"start": v(-5230.99, 5803.73) * mm, "end": v(-5205.4, 5841.33) * mm});
            skLineSegment(sketch, "E1024", {"start": v(-5205.4, 5841.33) * mm, "end": v(-5175.42, 5875.76) * mm});
            skLineSegment(sketch, "E1025", {"start": v(-5175.42, 5875.76) * mm, "end": v(-5140.73, 5906.95) * mm});
            skLineSegment(sketch, "E1026", {"start": v(-5140.73, 5906.95) * mm, "end": v(-5101, 5934.83) * mm});
            skLineSegment(sketch, "E1027", {"start": v(-5101, 5934.83) * mm, "end": v(-5055.94, 5959.3) * mm});
            skLineSegment(sketch, "E1028", {"start": v(-5055.94, 5959.3) * mm, "end": v(-5005.2, 5980.3) * mm});
            skLineSegment(sketch, "E1029", {"start": v(-5005.2, 5980.3) * mm, "end": v(-4948.48, 5997.75) * mm});
            skLineSegment(sketch, "E1030", {"start": v(-4948.48, 5997.75) * mm, "end": v(-4885.45, 6011.56) * mm});
            skLineSegment(sketch, "E1031", {"start": v(-4885.45, 6011.56) * mm, "end": v(-4825.49, 6020.46) * mm});
            skLineSegment(sketch, "E1032", {"start": v(-4825.49, 6020.46) * mm, "end": v(-4801.23, 6020.99) * mm});
            skLineSegment(sketch, "E1033", {"start": v(-4801.23, 6020.99) * mm, "end": v(-4776.44, 6018.2) * mm});
            skLineSegment(sketch, "E1034", {"start": v(-4776.44, 6018.2) * mm, "end": v(-4751.18, 6012.37) * mm});
            skLineSegment(sketch, "E1035", {"start": v(-4751.18, 6012.37) * mm, "end": v(-4725.53, 6003.76) * mm});
            skLineSegment(sketch, "E1036", {"start": v(-4725.53, 6003.76) * mm, "end": v(-4699.54, 5992.64) * mm});
            skLineSegment(sketch, "E1037", {"start": v(-4699.54, 5992.64) * mm, "end": v(-4673.3, 5979.3) * mm});
            skLineSegment(sketch, "E1038", {"start": v(-4673.3, 5979.3) * mm, "end": v(-4646.87, 5963.98) * mm});
            skLineSegment(sketch, "E1039", {"start": v(-4646.87, 5963.98) * mm, "end": v(-4620.32, 5946.97) * mm});
            skLineSegment(sketch, "E1040", {"start": v(-4620.32, 5946.97) * mm, "end": v(-4593.71, 5928.54) * mm});
            skLineSegment(sketch, "E1041", {"start": v(-4593.71, 5928.54) * mm, "end": v(-4567.12, 5908.96) * mm});
            skLineSegment(sketch, "E1042", {"start": v(-4567.12, 5908.96) * mm, "end": v(-4540.61, 5888.5) * mm});
            skLineSegment(sketch, "E1043", {"start": v(-4540.61, 5888.5) * mm, "end": v(-4514.26, 5867.41) * mm});
            skLineSegment(sketch, "E1044", {"start": v(-4514.26, 5867.41) * mm, "end": v(-4488.12, 5845.99) * mm});
            skLineSegment(sketch, "E1045", {"start": v(-4488.12, 5845.99) * mm, "end": v(-4462.28, 5824.49) * mm});
            skLineSegment(sketch, "E1046", {"start": v(-4462.28, 5824.49) * mm, "end": v(-4436.79, 5803.19) * mm});
            skLineSegment(sketch, "E1047", {"start": v(-4436.79, 5803.19) * mm, "end": v(-4411.73, 5782.36) * mm});
            skLineSegment(sketch, "E1048", {"start": v(-4411.73, 5782.36) * mm, "end": v(-4387.16, 5762.26) * mm});
            skLineSegment(sketch, "E1049", {"start": v(-4387.16, 5762.26) * mm, "end": v(-4363.16, 5743.18) * mm});
            skLineSegment(sketch, "E1050", {"start": v(-4363.16, 5743.18) * mm, "end": v(-4339.79, 5725.37) * mm});
            skLineSegment(sketch, "E1051", {"start": v(-4339.79, 5725.37) * mm, "end": v(-4317.11, 5709.1) * mm});
            skLineSegment(sketch, "E1052", {"start": v(-4317.11, 5709.1) * mm, "end": v(-4295.21, 5694.67) * mm});
            skLineSegment(sketch, "E1053", {"start": v(-4295.21, 5694.67) * mm, "end": v(-4274.15, 5682.32) * mm});
            skLineSegment(sketch, "E1054", {"start": v(-4274.15, 5682.32) * mm, "end": v(-4254, 5672.32) * mm});
            skLineSegment(sketch, "E1055", {"start": v(-4254, 5672.32) * mm, "end": v(-4234.8, 5664.96) * mm});
            skLineSegment(sketch, "E1056", {"start": v(-4234.8, 5664.96) * mm, "end": v(-4216.67, 5660.5) * mm});
            skLineSegment(sketch, "E1057", {"start": v(-4216.67, 5660.5) * mm, "end": v(-4199.64, 5659.2) * mm});
            skLineSegment(sketch, "E1058", {"start": v(-4199.64, 5659.2) * mm, "end": v(-4183.8, 5661.35) * mm});
            skLineSegment(sketch, "E1059", {"start": v(-4183.8, 5661.35) * mm, "end": v(-4169.2, 5667.2) * mm});
            skLineSegment(sketch, "E1060", {"start": v(-4169.2, 5667.2) * mm, "end": v(-4155.92, 5677.04) * mm});
            skLineSegment(sketch, "E1061", {"start": v(-4155.92, 5677.04) * mm, "end": v(-4144.03, 5691.13) * mm});
            skLineSegment(sketch, "E1062", {"start": v(-4144.03, 5691.13) * mm, "end": v(-4133.59, 5709.73) * mm});
            skLineSegment(sketch, "E1063", {"start": v(-4133.59, 5709.73) * mm, "end": v(-4124.67, 5733.13) * mm});
            skLineSegment(sketch, "E1064", {"start": v(-4124.67, 5733.13) * mm, "end": v(-4117.35, 5761.6) * mm});
            skLineSegment(sketch, "E1065", {"start": v(-4117.35, 5761.6) * mm, "end": v(-4111.69, 5795.38) * mm});
            skLineSegment(sketch, "E1066", {"start": v(-4111.69, 5795.38) * mm, "end": v(-4107.75, 5834.77) * mm});
            skLineSegment(sketch, "E1067", {"start": v(-4107.75, 5834.77) * mm, "end": v(-4115.4, 5931.87) * mm});
            skLineSegment(sketch, "E1068", {"start": v(-4115.4, 5931.87) * mm, "end": v(-4124.33, 6028.35) * mm});
            skLineSegment(sketch, "E1069", {"start": v(-4124.33, 6028.35) * mm, "end": v(-4134.51, 6124.24) * mm});
            skLineSegment(sketch, "E1070", {"start": v(-4134.51, 6124.24) * mm, "end": v(-4145.98, 6219.56) * mm});
            skLineSegment(sketch, "E1071", {"start": v(-4145.98, 6219.56) * mm, "end": v(-4158.73, 6314.33) * mm});
            skLineSegment(sketch, "E1072", {"start": v(-4158.73, 6314.33) * mm, "end": v(-4172.77, 6408.6) * mm});
            skLineSegment(sketch, "E1073", {"start": v(-4172.77, 6408.6) * mm, "end": v(-4188.1, 6502.37) * mm});
            skLineSegment(sketch, "E1074", {"start": v(-4188.1, 6502.37) * mm, "end": v(-4204.74, 6595.68) * mm});
            skLineSegment(sketch, "E1075", {"start": v(-4204.74, 6595.68) * mm, "end": v(-4222.7, 6688.56) * mm});
            skLineSegment(sketch, "E1076", {"start": v(-4222.7, 6688.56) * mm, "end": v(-4241.96, 6781.03) * mm});
            skLineSegment(sketch, "E1077", {"start": v(-4241.96, 6781.03) * mm, "end": v(-4262.55, 6873.12) * mm});
            skLineSegment(sketch, "E1078", {"start": v(-4262.55, 6873.12) * mm, "end": v(-4284.46, 6964.85) * mm});
            skLineSegment(sketch, "E1079", {"start": v(-4284.46, 6964.85) * mm, "end": v(-4307.72, 7056.26) * mm});
            skLineSegment(sketch, "E1080", {"start": v(-4307.72, 7056.26) * mm, "end": v(-4332.31, 7147.36) * mm});
            skLineSegment(sketch, "E1081", {"start": v(-4332.31, 7147.36) * mm, "end": v(-4358.26, 7238.19) * mm});
            skLineSegment(sketch, "E1082", {"start": v(-4358.26, 7238.19) * mm, "end": v(-4385.56, 7328.76) * mm});
            skLineSegment(sketch, "E1083", {"start": v(-4385.56, 7328.76) * mm, "end": v(-4414.22, 7419.12) * mm});
            skLineSegment(sketch, "E1084", {"start": v(-4414.22, 7419.12) * mm, "end": v(-4444.25, 7509.28) * mm});
            skLineSegment(sketch, "E1085", {"start": v(-4444.25, 7509.28) * mm, "end": v(-4475.66, 7599.27) * mm});
            skLineSegment(sketch, "E1086", {"start": v(-4475.66, 7599.27) * mm, "end": v(-4508.45, 7689.12) * mm});
            skLineSegment(sketch, "E1087", {"start": v(-4508.45, 7689.12) * mm, "end": v(-4542.63, 7778.85) * mm});
            skLineSegment(sketch, "E1088", {"start": v(-4542.63, 7778.85) * mm, "end": v(-4578.2, 7868.49) * mm});
            skLineSegment(sketch, "E1089", {"start": v(-4578.2, 7868.49) * mm, "end": v(-4615.18, 7958.07) * mm});
            skLineSegment(sketch, "E1090", {"start": v(-4615.18, 7958.07) * mm, "end": v(-4653.56, 8047.6) * mm});
            skLineSegment(sketch, "E1091", {"start": v(6142.61, 8047.6) * mm, "end": v(6053.07, 8009.25) * mm});
            skLineSegment(sketch, "E1092", {"start": v(6053.07, 8009.25) * mm, "end": v(5963.49, 7972.3) * mm});
            skLineSegment(sketch, "E1093", {"start": v(5963.49, 7972.3) * mm, "end": v(5873.84, 7936.74) * mm});
            skLineSegment(sketch, "E1094", {"start": v(5873.84, 7936.74) * mm, "end": v(5784.1, 7902.58) * mm});
            skLineSegment(sketch, "E1095", {"start": v(5784.1, 7902.58) * mm, "end": v(5694.25, 7869.8) * mm});
            skLineSegment(sketch, "E1096", {"start": v(5694.25, 7869.8) * mm, "end": v(5604.25, 7838.41) * mm});
            skLineSegment(sketch, "E1097", {"start": v(5604.25, 7838.41) * mm, "end": v(5514.08, 7808.4) * mm});
            skLineSegment(sketch, "E1098", {"start": v(5514.08, 7808.4) * mm, "end": v(5423.72, 7779.74) * mm});
            skLineSegment(sketch, "E1099", {"start": v(5423.72, 7779.74) * mm, "end": v(5333.13, 7752.44) * mm});
            skLineSegment(sketch, "E1100", {"start": v(5333.13, 7752.44) * mm, "end": v(5242.3, 7726.5) * mm});
            skLineSegment(sketch, "E1101", {"start": v(5242.3, 7726.5) * mm, "end": v(5151.18, 7701.9) * mm});
            skLineSegment(sketch, "E1102", {"start": v(5151.18, 7701.9) * mm, "end": v(5059.76, 7678.65) * mm});
            skLineSegment(sketch, "E1103", {"start": v(5059.76, 7678.65) * mm, "end": v(4968.02, 7656.73) * mm});
            skLineSegment(sketch, "E1104", {"start": v(4968.02, 7656.73) * mm, "end": v(4875.92, 7636.14) * mm});
            skLineSegment(sketch, "E1105", {"start": v(4875.92, 7636.14) * mm, "end": v(4783.43, 7616.86) * mm});
            skLineSegment(sketch, "E1106", {"start": v(4783.43, 7616.86) * mm, "end": v(4690.54, 7598.9) * mm});
            skLineSegment(sketch, "E1107", {"start": v(4690.54, 7598.9) * mm, "end": v(4597.22, 7582.25) * mm});
            skLineSegment(sketch, "E1108", {"start": v(4597.22, 7582.25) * mm, "end": v(4503.44, 7566.9) * mm});
            skLineSegment(sketch, "E1109", {"start": v(4503.44, 7566.9) * mm, "end": v(4409.17, 7552.84) * mm});
            skLineSegment(sketch, "E1110", {"start": v(4409.17, 7552.84) * mm, "end": v(4314.38, 7540.07) * mm});
            skLineSegment(sketch, "E1111", {"start": v(4314.38, 7540.07) * mm, "end": v(4219.06, 7528.58) * mm});
            skLineSegment(sketch, "E1112", {"start": v(4219.06, 7528.58) * mm, "end": v(4123.17, 7518.37) * mm});
            skLineSegment(sketch, "E1113", {"start": v(4123.17, 7518.37) * mm, "end": v(4026.69, 7509.42) * mm});
            skLineSegment(sketch, "E1114", {"start": v(4026.69, 7509.42) * mm, "end": v(3929.59, 7501.74) * mm});
            skLineSegment(sketch, "E1115", {"start": v(3929.59, 7501.74) * mm, "end": v(3856.43, 7511.35) * mm});
            skLineSegment(sketch, "E1116", {"start": v(3856.43, 7511.35) * mm, "end": v(3804.6, 7527.6) * mm});
            skLineSegment(sketch, "E1117", {"start": v(3804.6, 7527.6) * mm, "end": v(3771.93, 7549.93) * mm});
            skLineSegment(sketch, "E1118", {"start": v(3771.93, 7549.93) * mm, "end": v(3756.26, 7577.82) * mm});
            skLineSegment(sketch, "E1119", {"start": v(3756.26, 7577.82) * mm, "end": v(3755.43, 7610.7) * mm});
            skLineSegment(sketch, "E1120", {"start": v(3755.43, 7610.7) * mm, "end": v(3767.27, 7648.03) * mm});
            skLineSegment(sketch, "E1121", {"start": v(3767.27, 7648.03) * mm, "end": v(3789.63, 7689.26) * mm});
            skLineSegment(sketch, "E1122", {"start": v(3789.63, 7689.26) * mm, "end": v(3820.34, 7733.84) * mm});
            skLineSegment(sketch, "E1123", {"start": v(3820.34, 7733.84) * mm, "end": v(3857.24, 7781.23) * mm});
            skLineSegment(sketch, "E1124", {"start": v(3857.24, 7781.23) * mm, "end": v(3898.18, 7830.87) * mm});
            skLineSegment(sketch, "E1125", {"start": v(3898.18, 7830.87) * mm, "end": v(3940.98, 7882.22) * mm});
            skLineSegment(sketch, "E1126", {"start": v(3940.98, 7882.22) * mm, "end": v(3983.49, 7934.72) * mm});
            skLineSegment(sketch, "E1127", {"start": v(3983.49, 7934.72) * mm, "end": v(4023.54, 7987.84) * mm});
            skLineSegment(sketch, "E1128", {"start": v(4023.54, 7987.84) * mm, "end": v(4058.98, 8041.02) * mm});
            skLineSegment(sketch, "E1129", {"start": v(4058.98, 8041.02) * mm, "end": v(4087.65, 8093.71) * mm});
            skLineSegment(sketch, "E1130", {"start": v(4087.65, 8093.71) * mm, "end": v(4107.37, 8145.37) * mm});
            skLineSegment(sketch, "E1131", {"start": v(4107.37, 8145.37) * mm, "end": v(4116, 8195.45) * mm});
            skLineSegment(sketch, "E1132", {"start": v(4116, 8195.45) * mm, "end": v(4111.04, 8252.64) * mm});
            skLineSegment(sketch, "E1133", {"start": v(4111.04, 8252.64) * mm, "end": v(4098.69, 8318.28) * mm});
            skLineSegment(sketch, "E1134", {"start": v(4098.69, 8318.28) * mm, "end": v(4082.67, 8377.48) * mm});
            skLineSegment(sketch, "E1135", {"start": v(4082.67, 8377.48) * mm, "end": v(4063.07, 8430.56) * mm});
            skLineSegment(sketch, "E1136", {"start": v(4063.07, 8430.56) * mm, "end": v(4039.96, 8477.85) * mm});
            skLineSegment(sketch, "E1137", {"start": v(4039.96, 8477.85) * mm, "end": v(4013.42, 8519.66) * mm});
            skLineSegment(sketch, "E1138", {"start": v(4013.42, 8519.66) * mm, "end": v(3983.54, 8556.3) * mm});
            skLineSegment(sketch, "E1139", {"start": v(3983.54, 8556.3) * mm, "end": v(3950.38, 8588.12) * mm});
            skLineSegment(sketch, "E1140", {"start": v(3950.38, 8588.12) * mm, "end": v(3914.03, 8615.4) * mm});
            skLineSegment(sketch, "E1141", {"start": v(3914.03, 8615.4) * mm, "end": v(3874.57, 8638.5) * mm});
            skLineSegment(sketch, "E1142", {"start": v(3874.57, 8638.5) * mm, "end": v(3832.07, 8657.7) * mm});
            skLineSegment(sketch, "E1143", {"start": v(3832.07, 8657.7) * mm, "end": v(3786.6, 8673.35) * mm});
            skLineSegment(sketch, "E1144", {"start": v(3786.6, 8673.35) * mm, "end": v(3738.26, 8685.75) * mm});
            skLineSegment(sketch, "E1145", {"start": v(3738.26, 8685.75) * mm, "end": v(3687.12, 8695.23) * mm});
            skLineSegment(sketch, "E1146", {"start": v(3687.12, 8695.23) * mm, "end": v(3633.25, 8702.1) * mm});
            skLineSegment(sketch, "E1147", {"start": v(3633.25, 8702.1) * mm, "end": v(3576.73, 8706.7) * mm});
            skLineSegment(sketch, "E1148", {"start": v(3576.73, 8706.7) * mm, "end": v(3517.64, 8709.32) * mm});
            skLineSegment(sketch, "E1149", {"start": v(3517.64, 8709.32) * mm, "end": v(3456.06, 8710.3) * mm});
            skLineSegment(sketch, "E1150", {"start": v(3456.06, 8710.3) * mm, "end": v(3393.61, 8709.89) * mm});
            skLineSegment(sketch, "E1151", {"start": v(3393.61, 8709.89) * mm, "end": v(3333.52, 8707.96) * mm});
            skLineSegment(sketch, "E1152", {"start": v(3333.52, 8707.96) * mm, "end": v(3275.98, 8704.2) * mm});
            skLineSegment(sketch, "E1153", {"start": v(3275.98, 8704.2) * mm, "end": v(3221.05, 8698.28) * mm});
            skLineSegment(sketch, "E1154", {"start": v(3221.05, 8698.28) * mm, "end": v(3168.81, 8689.88) * mm});
            skLineSegment(sketch, "E1155", {"start": v(3168.81, 8689.88) * mm, "end": v(3119.35, 8678.68) * mm});
            skLineSegment(sketch, "E1156", {"start": v(3119.35, 8678.68) * mm, "end": v(3072.74, 8664.37) * mm});
            skLineSegment(sketch, "E1157", {"start": v(3072.74, 8664.37) * mm, "end": v(3029.06, 8646.63) * mm});
            skLineSegment(sketch, "E1158", {"start": v(3029.06, 8646.63) * mm, "end": v(2988.39, 8625.13) * mm});
            skLineSegment(sketch, "E1159", {"start": v(2988.39, 8625.13) * mm, "end": v(2950.8, 8599.56) * mm});
            skLineSegment(sketch, "E1160", {"start": v(2950.8, 8599.56) * mm, "end": v(2916.36, 8569.6) * mm});
            skLineSegment(sketch, "E1161", {"start": v(2916.36, 8569.6) * mm, "end": v(2885.17, 8534.92) * mm});
            skLineSegment(sketch, "E1162", {"start": v(2885.17, 8534.92) * mm, "end": v(2857.3, 8495.21) * mm});
            skLineSegment(sketch, "E1163", {"start": v(2857.3, 8495.21) * mm, "end": v(2832.81, 8450.16) * mm});
            skLineSegment(sketch, "E1164", {"start": v(2832.81, 8450.16) * mm, "end": v(2811.8, 8399.43) * mm});
            skLineSegment(sketch, "E1165", {"start": v(2811.8, 8399.43) * mm, "end": v(2794.34, 8342.71) * mm});
            skLineSegment(sketch, "E1166", {"start": v(2794.34, 8342.71) * mm, "end": v(2780.5, 8279.69) * mm});
            skLineSegment(sketch, "E1167", {"start": v(2780.5, 8279.69) * mm, "end": v(2771.58, 8219.73) * mm});
            skLineSegment(sketch, "E1168", {"start": v(2771.58, 8219.73) * mm, "end": v(2771.05, 8195.45) * mm});
            skLineSegment(sketch, "E1169", {"start": v(2771.05, 8195.45) * mm, "end": v(2773.84, 8170.65) * mm});
            skLineSegment(sketch, "E1170", {"start": v(2773.84, 8170.65) * mm, "end": v(2779.68, 8145.37) * mm});
            skLineSegment(sketch, "E1171", {"start": v(2779.68, 8145.37) * mm, "end": v(2788.3, 8119.7) * mm});
            skLineSegment(sketch, "E1172", {"start": v(2788.3, 8119.7) * mm, "end": v(2799.4, 8093.71) * mm});
            skLineSegment(sketch, "E1173", {"start": v(2799.4, 8093.71) * mm, "end": v(2812.76, 8067.46) * mm});
            skLineSegment(sketch, "E1174", {"start": v(2812.76, 8067.46) * mm, "end": v(2828.08, 8041.02) * mm});
            skLineSegment(sketch, "E1175", {"start": v(2828.08, 8041.02) * mm, "end": v(2845.1, 8014.46) * mm});
            skLineSegment(sketch, "E1176", {"start": v(2845.1, 8014.46) * mm, "end": v(2863.53, 7987.84) * mm});
            skLineSegment(sketch, "E1177", {"start": v(2863.53, 7987.84) * mm, "end": v(2883.12, 7961.24) * mm});
            skLineSegment(sketch, "E1178", {"start": v(2883.12, 7961.24) * mm, "end": v(2903.6, 7934.72) * mm});
            skLineSegment(sketch, "E1179", {"start": v(2903.6, 7934.72) * mm, "end": v(2924.68, 7908.36) * mm});
            skLineSegment(sketch, "E1180", {"start": v(2924.68, 7908.36) * mm, "end": v(2946.11, 7882.22) * mm});
            skLineSegment(sketch, "E1181", {"start": v(2946.11, 7882.22) * mm, "end": v(2967.62, 7856.36) * mm});
            skLineSegment(sketch, "E1182", {"start": v(2967.62, 7856.36) * mm, "end": v(2988.93, 7830.87) * mm});
            skLineSegment(sketch, "E1183", {"start": v(2988.93, 7830.87) * mm, "end": v(3009.77, 7805.8) * mm});
            skLineSegment(sketch, "E1184", {"start": v(3009.77, 7805.8) * mm, "end": v(3029.87, 7781.23) * mm});
            skLineSegment(sketch, "E1185", {"start": v(3029.87, 7781.23) * mm, "end": v(3048.96, 7757.22) * mm});
            skLineSegment(sketch, "E1186", {"start": v(3048.96, 7757.22) * mm, "end": v(3066.78, 7733.84) * mm});
            skLineSegment(sketch, "E1187", {"start": v(3066.78, 7733.84) * mm, "end": v(3083.05, 7711.17) * mm});
            skLineSegment(sketch, "E1188", {"start": v(3083.05, 7711.17) * mm, "end": v(3097.5, 7689.26) * mm});
            skLineSegment(sketch, "E1189", {"start": v(3097.5, 7689.26) * mm, "end": v(3109.86, 7668.2) * mm});
            skLineSegment(sketch, "E1190", {"start": v(3109.86, 7668.2) * mm, "end": v(3119.86, 7648.03) * mm});
            skLineSegment(sketch, "E1191", {"start": v(3119.86, 7648.03) * mm, "end": v(3127.23, 7628.84) * mm});
            skLineSegment(sketch, "E1192", {"start": v(3127.23, 7628.84) * mm, "end": v(3131.7, 7610.7) * mm});
            skLineSegment(sketch, "E1193", {"start": v(3131.7, 7610.7) * mm, "end": v(3133, 7593.67) * mm});
            skLineSegment(sketch, "E1194", {"start": v(3133, 7593.67) * mm, "end": v(3130.86, 7577.82) * mm});
            skLineSegment(sketch, "E1195", {"start": v(3130.86, 7577.82) * mm, "end": v(3125.01, 7563.22) * mm});
            skLineSegment(sketch, "E1196", {"start": v(3125.01, 7563.22) * mm, "end": v(3115.18, 7549.93) * mm});
            skLineSegment(sketch, "E1197", {"start": v(3115.18, 7549.93) * mm, "end": v(3101.1, 7538.04) * mm});
            skLineSegment(sketch, "E1198", {"start": v(3101.1, 7538.04) * mm, "end": v(3082.5, 7527.6) * mm});
            skLineSegment(sketch, "E1199", {"start": v(3082.5, 7527.6) * mm, "end": v(3059.1, 7518.67) * mm});
            skLineSegment(sketch, "E1200", {"start": v(3059.1, 7518.67) * mm, "end": v(3030.64, 7511.35) * mm});
            skLineSegment(sketch, "E1201", {"start": v(3030.64, 7511.35) * mm, "end": v(2996.85, 7505.68) * mm});
            skLineSegment(sketch, "E1202", {"start": v(2996.85, 7505.68) * mm, "end": v(2957.46, 7501.74) * mm});
            skLineSegment(sketch, "E1203", {"start": v(2957.46, 7501.74) * mm, "end": v(2860.36, 7509.42) * mm});
            skLineSegment(sketch, "E1204", {"start": v(2860.36, 7509.42) * mm, "end": v(2763.88, 7518.37) * mm});
            skLineSegment(sketch, "E1205", {"start": v(2763.88, 7518.37) * mm, "end": v(2667.99, 7528.58) * mm});
            skLineSegment(sketch, "E1206", {"start": v(2667.99, 7528.58) * mm, "end": v(2572.66, 7540.07) * mm});
            skLineSegment(sketch, "E1207", {"start": v(2572.66, 7540.07) * mm, "end": v(2477.88, 7552.84) * mm});
            skLineSegment(sketch, "E1208", {"start": v(2477.88, 7552.84) * mm, "end": v(2383.6, 7566.9) * mm});
            skLineSegment(sketch, "E1209", {"start": v(2383.6, 7566.9) * mm, "end": v(2289.83, 7582.25) * mm});
            skLineSegment(sketch, "E1210", {"start": v(2289.83, 7582.25) * mm, "end": v(2196.5, 7598.9) * mm});
            skLineSegment(sketch, "E1211", {"start": v(2196.5, 7598.9) * mm, "end": v(2103.62, 7616.86) * mm});
            skLineSegment(sketch, "E1212", {"start": v(2103.62, 7616.86) * mm, "end": v(2011.14, 7636.14) * mm});
            skLineSegment(sketch, "E1213", {"start": v(2011.14, 7636.14) * mm, "end": v(1919.05, 7656.73) * mm});
            skLineSegment(sketch, "E1214", {"start": v(1919.05, 7656.73) * mm, "end": v(1827.3, 7678.65) * mm});
            skLineSegment(sketch, "E1215", {"start": v(1827.3, 7678.65) * mm, "end": v(1735.9, 7701.9) * mm});
            skLineSegment(sketch, "E1216", {"start": v(1735.9, 7701.9) * mm, "end": v(1692.6, 7713.6) * mm});
            skLineSegment(sketch, "E1217", {"start": v(1692.6, 2983.61) * mm, "end": v(1735.9, 2995.3) * mm});
            skLineSegment(sketch, "E1218", {"start": v(1735.9, 2995.3) * mm, "end": v(1827.3, 3018.55) * mm});
            skLineSegment(sketch, "E1219", {"start": v(1827.3, 3018.55) * mm, "end": v(1919.05, 3040.46) * mm});
            skLineSegment(sketch, "E1220", {"start": v(1919.05, 3040.46) * mm, "end": v(2011.14, 3061.04) * mm});
            skLineSegment(sketch, "E1221", {"start": v(2011.14, 3061.04) * mm, "end": v(2103.62, 3080.3) * mm});
            skLineSegment(sketch, "E1222", {"start": v(2103.62, 3080.3) * mm, "end": v(2196.5, 3098.25) * mm});
            skLineSegment(sketch, "E1223", {"start": v(2196.5, 3098.25) * mm, "end": v(2289.83, 3114.89) * mm});
            skLineSegment(sketch, "E1224", {"start": v(2289.83, 3114.89) * mm, "end": v(2383.6, 3130.22) * mm});
            skLineSegment(sketch, "E1225", {"start": v(2383.6, 3130.22) * mm, "end": v(2477.88, 3144.26) * mm});
            skLineSegment(sketch, "E1226", {"start": v(2477.88, 3144.26) * mm, "end": v(2572.66, 3157) * mm});
            skLineSegment(sketch, "E1227", {"start": v(2572.66, 3157) * mm, "end": v(2667.99, 3168.47) * mm});
            skLineSegment(sketch, "E1228", {"start": v(2667.99, 3168.47) * mm, "end": v(2763.88, 3178.66) * mm});
            skLineSegment(sketch, "E1229", {"start": v(2763.88, 3178.66) * mm, "end": v(2860.36, 3187.58) * mm});
            skLineSegment(sketch, "E1230", {"start": v(2860.36, 3187.58) * mm, "end": v(2957.46, 3195.23) * mm});
            skLineSegment(sketch, "E1231", {"start": v(2957.46, 3195.23) * mm, "end": v(3025.39, 3186.7) * mm});
            skLineSegment(sketch, "E1232", {"start": v(3025.39, 3186.7) * mm, "end": v(3075.24, 3172.55) * mm});
            skLineSegment(sketch, "E1233", {"start": v(3075.24, 3172.55) * mm, "end": v(3108.69, 3153.2) * mm});
            skLineSegment(sketch, "E1234", {"start": v(3108.69, 3153.2) * mm, "end": v(3127.39, 3129.08) * mm});
            skLineSegment(sketch, "E1235", {"start": v(3127.39, 3129.08) * mm, "end": v(3133.01, 3100.61) * mm});
            skLineSegment(sketch, "E1236", {"start": v(3133.01, 3100.61) * mm, "end": v(3127.23, 3068.21) * mm});
            skLineSegment(sketch, "E1237", {"start": v(3127.23, 3068.21) * mm, "end": v(3111.7, 3032.3) * mm});
            skLineSegment(sketch, "E1238", {"start": v(3111.7, 3032.3) * mm, "end": v(3088.08, 2993.32) * mm});
            skLineSegment(sketch, "E1239", {"start": v(3088.08, 2993.32) * mm, "end": v(3058.05, 2951.67) * mm});
            skLineSegment(sketch, "E1240", {"start": v(3058.05, 2951.67) * mm, "end": v(3023.27, 2907.77) * mm});
            skLineSegment(sketch, "E1241", {"start": v(3023.27, 2907.77) * mm, "end": v(2985.4, 2862.06) * mm});
            skLineSegment(sketch, "E1242", {"start": v(2985.4, 2862.06) * mm, "end": v(2946.11, 2814.95) * mm});
            skLineSegment(sketch, "E1243", {"start": v(2946.11, 2814.95) * mm, "end": v(2907.07, 2766.86) * mm});
            skLineSegment(sketch, "E1244", {"start": v(2907.07, 2766.86) * mm, "end": v(2869.94, 2718.22) * mm});
            skLineSegment(sketch, "E1245", {"start": v(2869.94, 2718.22) * mm, "end": v(2836.39, 2669.45) * mm});
            skLineSegment(sketch, "E1246", {"start": v(2836.39, 2669.45) * mm, "end": v(2808.08, 2620.98) * mm});
            skLineSegment(sketch, "E1247", {"start": v(2808.08, 2620.98) * mm, "end": v(2786.67, 2573.21) * mm});
            skLineSegment(sketch, "E1248", {"start": v(2786.67, 2573.21) * mm, "end": v(2773.84, 2526.58) * mm});
            skLineSegment(sketch, "E1249", {"start": v(2773.84, 2526.58) * mm, "end": v(2771.25, 2481.5) * mm});
            skLineSegment(sketch, "E1250", {"start": v(2771.25, 2481.5) * mm, "end": v(2779.72, 2421.97) * mm});
            skLineSegment(sketch, "E1251", {"start": v(2779.72, 2421.97) * mm, "end": v(2792.03, 2363.55) * mm});
            skLineSegment(sketch, "E1252", {"start": v(2792.03, 2363.55) * mm, "end": v(2807.4, 2310.47) * mm});
            skLineSegment(sketch, "E1253", {"start": v(2807.4, 2310.47) * mm, "end": v(2825.78, 2262.49) * mm});
            skLineSegment(sketch, "E1254", {"start": v(2825.78, 2262.49) * mm, "end": v(2847.1, 2219.35) * mm});
            skLineSegment(sketch, "E1255", {"start": v(2847.1, 2219.35) * mm, "end": v(2871.28, 2180.8) * mm});
            skLineSegment(sketch, "E1256", {"start": v(2871.28, 2180.8) * mm, "end": v(2898.28, 2146.63) * mm});
            skLineSegment(sketch, "E1257", {"start": v(2898.28, 2146.63) * mm, "end": v(2928.05, 2116.55) * mm});
            skLineSegment(sketch, "E1258", {"start": v(2928.05, 2116.55) * mm, "end": v(2960.51, 2090.35) * mm});
            skLineSegment(sketch, "E1259", {"start": v(2960.51, 2090.35) * mm, "end": v(2995.61, 2067.76) * mm});
            skLineSegment(sketch, "E1260", {"start": v(2995.61, 2067.76) * mm, "end": v(3033.3, 2048.55) * mm});
            skLineSegment(sketch, "E1261", {"start": v(3033.3, 2048.55) * mm, "end": v(3073.5, 2032.46) * mm});
            skLineSegment(sketch, "E1262", {"start": v(3073.5, 2032.46) * mm, "end": v(3116.16, 2019.26) * mm});
            skLineSegment(sketch, "E1263", {"start": v(3116.16, 2019.26) * mm, "end": v(3161.22, 2008.69) * mm});
            skLineSegment(sketch, "E1264", {"start": v(3161.22, 2008.69) * mm, "end": v(3208.61, 2000.51) * mm});
            skLineSegment(sketch, "E1265", {"start": v(3208.61, 2000.51) * mm, "end": v(3258.3, 1994.48) * mm});
            skLineSegment(sketch, "E1266", {"start": v(3258.3, 1994.48) * mm, "end": v(3310.2, 1990.35) * mm});
            skLineSegment(sketch, "E1267", {"start": v(3310.2, 1990.35) * mm, "end": v(3364.26, 1987.87) * mm});
            skLineSegment(sketch, "E1268", {"start": v(3364.26, 1987.87) * mm, "end": v(3420.42, 1986.8) * mm});
            skLineSegment(sketch, "E1269", {"start": v(3420.42, 1986.8) * mm, "end": v(3477.91, 1986.92) * mm});
            skLineSegment(sketch, "E1270", {"start": v(3477.91, 1986.92) * mm, "end": v(3533.69, 1988.25) * mm});
            skLineSegment(sketch, "E1271", {"start": v(3533.69, 1988.25) * mm, "end": v(3587.34, 1991.04) * mm});
            skLineSegment(sketch, "E1272", {"start": v(3587.34, 1991.04) * mm, "end": v(3638.82, 1995.53) * mm});
            skLineSegment(sketch, "E1273", {"start": v(3638.82, 1995.53) * mm, "end": v(3688.07, 2001.97) * mm});
            skLineSegment(sketch, "E1274", {"start": v(3688.07, 2001.97) * mm, "end": v(3735.02, 2010.6) * mm});
            skLineSegment(sketch, "E1275", {"start": v(3735.02, 2010.6) * mm, "end": v(3779.62, 2021.68) * mm});
            skLineSegment(sketch, "E1276", {"start": v(3779.62, 2021.68) * mm, "end": v(3821.8, 2035.44) * mm});
            skLineSegment(sketch, "E1277", {"start": v(3821.8, 2035.44) * mm, "end": v(3861.51, 2052.13) * mm});
            skLineSegment(sketch, "E1278", {"start": v(3861.51, 2052.13) * mm, "end": v(3898.7, 2072) * mm});
            skLineSegment(sketch, "E1279", {"start": v(3898.7, 2072) * mm, "end": v(3933.27, 2095.3) * mm});
            skLineSegment(sketch, "E1280", {"start": v(3933.27, 2095.3) * mm, "end": v(3965.2, 2122.25) * mm});
            skLineSegment(sketch, "E1281", {"start": v(3965.2, 2122.25) * mm, "end": v(3994.42, 2153.13) * mm});
            skLineSegment(sketch, "E1282", {"start": v(3994.42, 2153.13) * mm, "end": v(4020.87, 2188.16) * mm});
            skLineSegment(sketch, "E1283", {"start": v(4020.87, 2188.16) * mm, "end": v(4044.48, 2227.6) * mm});
            skLineSegment(sketch, "E1284", {"start": v(4044.48, 2227.6) * mm, "end": v(4065.2, 2271.69) * mm});
            skLineSegment(sketch, "E1285", {"start": v(4065.2, 2271.69) * mm, "end": v(4082.97, 2320.68) * mm});
            skLineSegment(sketch, "E1286", {"start": v(4082.97, 2320.68) * mm, "end": v(4097.73, 2374.8) * mm});
            skLineSegment(sketch, "E1287", {"start": v(4097.73, 2374.8) * mm, "end": v(4109.42, 2434.32) * mm});
            skLineSegment(sketch, "E1288", {"start": v(4109.42, 2434.32) * mm, "end": v(4115.8, 2481.5) * mm});
            skLineSegment(sketch, "E1289", {"start": v(4115.8, 2481.5) * mm, "end": v(4115.86, 2503.82) * mm});
            skLineSegment(sketch, "E1290", {"start": v(4115.86, 2503.82) * mm, "end": v(4113.17, 2526.58) * mm});
            skLineSegment(sketch, "E1291", {"start": v(4113.17, 2526.58) * mm, "end": v(4107.92, 2549.73) * mm});
            skLineSegment(sketch, "E1292", {"start": v(4107.92, 2549.73) * mm, "end": v(4100.32, 2573.21) * mm});
            skLineSegment(sketch, "E1293", {"start": v(4100.32, 2573.21) * mm, "end": v(4090.58, 2596.98) * mm});
            skLineSegment(sketch, "E1294", {"start": v(4090.58, 2596.98) * mm, "end": v(4078.91, 2620.98) * mm});
            skLineSegment(sketch, "E1295", {"start": v(4078.91, 2620.98) * mm, "end": v(4065.51, 2645.15) * mm});
            skLineSegment(sketch, "E1296", {"start": v(4065.51, 2645.15) * mm, "end": v(4050.6, 2669.45) * mm});
            skLineSegment(sketch, "E1297", {"start": v(4050.6, 2669.45) * mm, "end": v(4034.37, 2693.83) * mm});
            skLineSegment(sketch, "E1298", {"start": v(4034.37, 2693.83) * mm, "end": v(4017.05, 2718.22) * mm});
            skLineSegment(sketch, "E1299", {"start": v(4017.05, 2718.22) * mm, "end": v(3998.83, 2742.59) * mm});
            skLineSegment(sketch, "E1300", {"start": v(3998.83, 2742.59) * mm, "end": v(3979.92, 2766.86) * mm});
            skLineSegment(sketch, "E1301", {"start": v(3979.92, 2766.86) * mm, "end": v(3960.54, 2791) * mm});
            skLineSegment(sketch, "E1302", {"start": v(3960.54, 2791) * mm, "end": v(3940.9, 2814.95) * mm});
            skLineSegment(sketch, "E1303", {"start": v(3940.9, 2814.95) * mm, "end": v(3921.18, 2838.65) * mm});
            skLineSegment(sketch, "E1304", {"start": v(3921.18, 2838.65) * mm, "end": v(3901.62, 2862.06) * mm});
            skLineSegment(sketch, "E1305", {"start": v(3901.62, 2862.06) * mm, "end": v(3882.41, 2885.12) * mm});
            skLineSegment(sketch, "E1306", {"start": v(3882.41, 2885.12) * mm, "end": v(3863.77, 2907.77) * mm});
            skLineSegment(sketch, "E1307", {"start": v(3863.77, 2907.77) * mm, "end": v(3845.9, 2929.97) * mm});
            skLineSegment(sketch, "E1308", {"start": v(3845.9, 2929.97) * mm, "end": v(3829, 2951.67) * mm});
            skLineSegment(sketch, "E1309", {"start": v(3829, 2951.67) * mm, "end": v(3813.3, 2972.8) * mm});
            skLineSegment(sketch, "E1310", {"start": v(3813.3, 2972.8) * mm, "end": v(3798.99, 2993.32) * mm});
            skLineSegment(sketch, "E1311", {"start": v(3798.99, 2993.32) * mm, "end": v(3786.28, 3013.17) * mm});
            skLineSegment(sketch, "E1312", {"start": v(3786.28, 3013.17) * mm, "end": v(3775.39, 3032.3) * mm});
            skLineSegment(sketch, "E1313", {"start": v(3775.39, 3032.3) * mm, "end": v(3766.5, 3050.67) * mm});
            skLineSegment(sketch, "E1314", {"start": v(3766.5, 3050.67) * mm, "end": v(3759.86, 3068.21) * mm});
            skLineSegment(sketch, "E1315", {"start": v(3759.86, 3068.21) * mm, "end": v(3755.65, 3084.88) * mm});
            skLineSegment(sketch, "E1316", {"start": v(3755.65, 3084.88) * mm, "end": v(3754.08, 3100.61) * mm});
            skLineSegment(sketch, "E1317", {"start": v(3754.08, 3100.61) * mm, "end": v(3755.37, 3115.37) * mm});
            skLineSegment(sketch, "E1318", {"start": v(3755.37, 3115.37) * mm, "end": v(3759.7, 3129.08) * mm});
            skLineSegment(sketch, "E1319", {"start": v(3759.7, 3129.08) * mm, "end": v(3767.32, 3141.71) * mm});
            skLineSegment(sketch, "E1320", {"start": v(3767.32, 3141.71) * mm, "end": v(3778.4, 3153.2) * mm});
            skLineSegment(sketch, "E1321", {"start": v(3778.4, 3153.2) * mm, "end": v(3793.18, 3163.5) * mm});
            skLineSegment(sketch, "E1322", {"start": v(3793.18, 3163.5) * mm, "end": v(3811.85, 3172.55) * mm});
            skLineSegment(sketch, "E1323", {"start": v(3811.85, 3172.55) * mm, "end": v(3834.61, 3180.3) * mm});
            skLineSegment(sketch, "E1324", {"start": v(3834.61, 3180.3) * mm, "end": v(3861.68, 3186.7) * mm});
            skLineSegment(sketch, "E1325", {"start": v(3861.68, 3186.7) * mm, "end": v(3893.27, 3191.7) * mm});
            skLineSegment(sketch, "E1326", {"start": v(3893.27, 3191.7) * mm, "end": v(3929.59, 3195.23) * mm});
            skLineSegment(sketch, "E1327", {"start": v(3929.59, 3195.23) * mm, "end": v(4026.69, 3187.58) * mm});
            skLineSegment(sketch, "E1328", {"start": v(4026.69, 3187.58) * mm, "end": v(4123.17, 3178.66) * mm});
            skLineSegment(sketch, "E1329", {"start": v(4123.17, 3178.66) * mm, "end": v(4219.06, 3168.47) * mm});
            skLineSegment(sketch, "E1330", {"start": v(4219.06, 3168.47) * mm, "end": v(4314.38, 3157) * mm});
            skLineSegment(sketch, "E1331", {"start": v(4314.38, 3157) * mm, "end": v(4409.17, 3144.26) * mm});
            skLineSegment(sketch, "E1332", {"start": v(4409.17, 3144.26) * mm, "end": v(4503.44, 3130.22) * mm});
            skLineSegment(sketch, "E1333", {"start": v(4503.44, 3130.22) * mm, "end": v(4597.22, 3114.89) * mm});
            skLineSegment(sketch, "E1334", {"start": v(4597.22, 3114.89) * mm, "end": v(4690.54, 3098.25) * mm});
            skLineSegment(sketch, "E1335", {"start": v(4690.54, 3098.25) * mm, "end": v(4783.43, 3080.3) * mm});
            skLineSegment(sketch, "E1336", {"start": v(4783.43, 3080.3) * mm, "end": v(4875.92, 3061.04) * mm});
            skLineSegment(sketch, "E1337", {"start": v(4875.92, 3061.04) * mm, "end": v(4968.02, 3040.46) * mm});
            skLineSegment(sketch, "E1338", {"start": v(4968.02, 3040.46) * mm, "end": v(5059.76, 3018.55) * mm});
            skLineSegment(sketch, "E1339", {"start": v(5059.76, 3018.55) * mm, "end": v(5151.18, 2995.3) * mm});
            skLineSegment(sketch, "E1340", {"start": v(5151.18, 2995.3) * mm, "end": v(5242.3, 2970.71) * mm});
            skLineSegment(sketch, "E1341", {"start": v(5242.3, 2970.71) * mm, "end": v(5333.13, 2944.77) * mm});
            skLineSegment(sketch, "E1342", {"start": v(5333.13, 2944.77) * mm, "end": v(5423.72, 2917.48) * mm});
            skLineSegment(sketch, "E1343", {"start": v(5423.72, 2917.48) * mm, "end": v(5514.08, 2888.83) * mm});
            skLineSegment(sketch, "E1344", {"start": v(5514.08, 2888.83) * mm, "end": v(5604.25, 2858.81) * mm});
            skLineSegment(sketch, "E1345", {"start": v(5604.25, 2858.81) * mm, "end": v(5694.25, 2827.42) * mm});
            skLineSegment(sketch, "E1346", {"start": v(5694.25, 2827.42) * mm, "end": v(5784.1, 2794.65) * mm});
            skLineSegment(sketch, "E1347", {"start": v(5784.1, 2794.65) * mm, "end": v(5873.84, 2760.49) * mm});
            skLineSegment(sketch, "E1348", {"start": v(5873.84, 2760.49) * mm, "end": v(5963.49, 2724.93) * mm});
            skLineSegment(sketch, "E1349", {"start": v(5963.49, 2724.93) * mm, "end": v(6053.07, 2687.98) * mm});
            skLineSegment(sketch, "E1350", {"start": v(6053.07, 2687.98) * mm, "end": v(6142.61, 2649.62) * mm});
            skLineSegment(sketch, "E1351", {"start": v(6142.61, 2649.62) * mm, "end": v(6180.97, 2739.14) * mm});
            skLineSegment(sketch, "E1352", {"start": v(6180.97, 2739.14) * mm, "end": v(6217.93, 2828.7) * mm});
            skLineSegment(sketch, "E1353", {"start": v(6217.93, 2828.7) * mm, "end": v(6253.48, 2918.32) * mm});
            skLineSegment(sketch, "E1354", {"start": v(6253.48, 2918.32) * mm, "end": v(6287.64, 3008.04) * mm});
            skLineSegment(sketch, "E1355", {"start": v(6287.64, 3008.04) * mm, "end": v(6320.41, 3097.88) * mm});
            skLineSegment(sketch, "E1356", {"start": v(6320.41, 3097.88) * mm, "end": v(6351.8, 3187.86) * mm});
            skLineSegment(sketch, "E1357", {"start": v(6351.8, 3187.86) * mm, "end": v(6381.83, 3278.01) * mm});
            skLineSegment(sketch, "E1358", {"start": v(6381.83, 3278.01) * mm, "end": v(6410.48, 3368.36) * mm});
            skLineSegment(sketch, "E1359", {"start": v(6410.48, 3368.36) * mm, "end": v(6437.77, 3458.94) * mm});
            skLineSegment(sketch, "E1360", {"start": v(6437.77, 3458.94) * mm, "end": v(6463.7, 3549.77) * mm});
            skLineSegment(sketch, "E1361", {"start": v(6463.7, 3549.77) * mm, "end": v(6488.3, 3640.87) * mm});
            skLineSegment(sketch, "E1362", {"start": v(6488.3, 3640.87) * mm, "end": v(6511.55, 3732.28) * mm});
            skLineSegment(sketch, "E1363", {"start": v(6511.55, 3732.28) * mm, "end": v(6533.46, 3824.02) * mm});
            skLineSegment(sketch, "E1364", {"start": v(6533.46, 3824.02) * mm, "end": v(6554.05, 3916.11) * mm});
            skLineSegment(sketch, "E1365", {"start": v(6554.05, 3916.11) * mm, "end": v(6573.31, 4008.59) * mm});
            skLineSegment(sketch, "E1366", {"start": v(6573.31, 4008.59) * mm, "end": v(6591.26, 4101.47) * mm});
            skLineSegment(sketch, "E1367", {"start": v(6591.26, 4101.47) * mm, "end": v(6607.9, 4194.8) * mm});
            skLineSegment(sketch, "E1368", {"start": v(6607.9, 4194.8) * mm, "end": v(6623.24, 4288.58) * mm});
            skLineSegment(sketch, "E1369", {"start": v(6623.24, 4288.58) * mm, "end": v(6637.28, 4382.85) * mm});
            skLineSegment(sketch, "E1370", {"start": v(6637.28, 4382.85) * mm, "end": v(6650.04, 4477.64) * mm});
            skLineSegment(sketch, "E1371", {"start": v(6650.04, 4477.64) * mm, "end": v(6661.5, 4572.96) * mm});
            skLineSegment(sketch, "E1372", {"start": v(6661.5, 4572.96) * mm, "end": v(6671.7, 4668.86) * mm});
            skLineSegment(sketch, "E1373", {"start": v(6671.7, 4668.86) * mm, "end": v(6680.63, 4765.35) * mm});
            skLineSegment(sketch, "E1374", {"start": v(6680.63, 4765.35) * mm, "end": v(6688.29, 4862.45) * mm});
            skLineSegment(sketch, "E1375", {"start": v(6688.29, 4862.45) * mm, "end": v(6678.68, 4935.63) * mm});
            skLineSegment(sketch, "E1376", {"start": v(6678.68, 4935.63) * mm, "end": v(6662.44, 4987.48) * mm});
            skLineSegment(sketch, "E1377", {"start": v(6662.44, 4987.48) * mm, "end": v(6640.1, 5020.17) * mm});
            skLineSegment(sketch, "E1378", {"start": v(6640.1, 5020.17) * mm, "end": v(6612.23, 5035.85) * mm});
            skLineSegment(sketch, "E1379", {"start": v(6612.23, 5035.85) * mm, "end": v(6579.37, 5036.7) * mm});
            skLineSegment(sketch, "E1380", {"start": v(6579.37, 5036.7) * mm, "end": v(6542.05, 5024.87) * mm});
            skLineSegment(sketch, "E1381", {"start": v(6542.05, 5024.87) * mm, "end": v(6500.83, 5002.52) * mm});
            skLineSegment(sketch, "E1382", {"start": v(6500.83, 5002.52) * mm, "end": v(6456.27, 4971.82) * mm});
            skLineSegment(sketch, "E1383", {"start": v(6456.27, 4971.82) * mm, "end": v(6408.9, 4934.92) * mm});
            skLineSegment(sketch, "E1384", {"start": v(6408.9, 4934.92) * mm, "end": v(6359.28, 4893.98) * mm});
            skLineSegment(sketch, "E1385", {"start": v(6359.28, 4893.98) * mm, "end": v(6307.94, 4851.18) * mm});
            skLineSegment(sketch, "E1386", {"start": v(6307.94, 4851.18) * mm, "end": v(6255.45, 4808.66) * mm});
            skLineSegment(sketch, "E1387", {"start": v(6255.45, 4808.66) * mm, "end": v(6202.35, 4768.6) * mm});
            skLineSegment(sketch, "E1388", {"start": v(6202.35, 4768.6) * mm, "end": v(6149.18, 4733.14) * mm});
            skLineSegment(sketch, "E1389", {"start": v(6149.18, 4733.14) * mm, "end": v(6096.5, 4704.46) * mm});
            skLineSegment(sketch, "E1390", {"start": v(6096.5, 4704.46) * mm, "end": v(6044.84, 4684.72) * mm});
            skLineSegment(sketch, "E1391", {"start": v(6044.84, 4684.72) * mm, "end": v(5994.77, 4676.06) * mm});
            skLineSegment(sketch, "E1392", {"start": v(5994.77, 4676.06) * mm, "end": v(5937.58, 4681) * mm});
            skLineSegment(sketch, "E1393", {"start": v(5937.58, 4681) * mm, "end": v(5871.94, 4693.35) * mm});
            skLineSegment(sketch, "E1394", {"start": v(5871.94, 4693.35) * mm, "end": v(5812.73, 4709.37) * mm});
            skLineSegment(sketch, "E1395", {"start": v(5812.73, 4709.37) * mm, "end": v(5759.64, 4728.97) * mm});
            skLineSegment(sketch, "E1396", {"start": v(5759.64, 4728.97) * mm, "end": v(5712.34, 4752.08) * mm});
            skLineSegment(sketch, "E1397", {"start": v(5712.34, 4752.08) * mm, "end": v(5670.52, 4778.61) * mm});
            skLineSegment(sketch, "E1398", {"start": v(5670.52, 4778.61) * mm, "end": v(5633.85, 4808.5) * mm});
            skLineSegment(sketch, "E1399", {"start": v(5633.85, 4808.5) * mm, "end": v(5602.03, 4841.66) * mm});
            skLineSegment(sketch, "E1400", {"start": v(5602.03, 4841.66) * mm, "end": v(5574.72, 4878) * mm});
            skLineSegment(sketch, "E1401", {"start": v(5574.72, 4878) * mm, "end": v(5551.62, 4917.47) * mm});
            skLineSegment(sketch, "E1402", {"start": v(5551.62, 4917.47) * mm, "end": v(5532.4, 4959.97) * mm});
            skLineSegment(sketch, "E1403", {"start": v(5532.4, 4959.97) * mm, "end": v(5516.73, 5005.43) * mm});
            skLineSegment(sketch, "E1404", {"start": v(5516.73, 5005.43) * mm, "end": v(5504.32, 5053.78) * mm});
            skLineSegment(sketch, "E1405", {"start": v(5504.32, 5053.78) * mm, "end": v(5494.82, 5104.92) * mm});
            skLineSegment(sketch, "E1406", {"start": v(5494.82, 5104.92) * mm, "end": v(5487.94, 5158.8) * mm});
            skLineSegment(sketch, "E1407", {"start": v(5487.94, 5158.8) * mm, "end": v(5483.34, 5215.31) * mm});
            skLineSegment(sketch, "E1408", {"start": v(5483.34, 5215.31) * mm, "end": v(5480.72, 5274.4) * mm});
            skLineSegment(sketch, "E1409", {"start": v(5480.72, 5274.4) * mm, "end": v(5479.74, 5335.97) * mm});
            skLineSegment(sketch, "E1410", {"start": v(5479.74, 5335.97) * mm, "end": v(5480.14, 5398.43) * mm});
            skLineSegment(sketch, "E1411", {"start": v(5480.14, 5398.43) * mm, "end": v(5482.07, 5458.52) * mm});
            skLineSegment(sketch, "E1412", {"start": v(5482.07, 5458.52) * mm, "end": v(5485.85, 5516.08) * mm});
            skLineSegment(sketch, "E1413", {"start": v(5485.85, 5516.08) * mm, "end": v(5491.78, 5571.01) * mm});
            skLineSegment(sketch, "E1414", {"start": v(5491.78, 5571.01) * mm, "end": v(5500.19, 5623.26) * mm});
            skLineSegment(sketch, "E1415", {"start": v(5500.19, 5623.26) * mm, "end": v(5511.4, 5672.73) * mm});
            skLineSegment(sketch, "E1416", {"start": v(5511.4, 5672.73) * mm, "end": v(5525.72, 5719.35) * mm});
            skLineSegment(sketch, "E1417", {"start": v(5525.72, 5719.35) * mm, "end": v(5543.48, 5763.04) * mm});
            skLineSegment(sketch, "E1418", {"start": v(5543.48, 5763.04) * mm, "end": v(5565, 5803.73) * mm});
            skLineSegment(sketch, "E1419", {"start": v(5565, 5803.73) * mm, "end": v(5590.58, 5841.33) * mm});
            skLineSegment(sketch, "E1420", {"start": v(5590.58, 5841.33) * mm, "end": v(5620.56, 5875.76) * mm});
            skLineSegment(sketch, "E1421", {"start": v(5620.56, 5875.76) * mm, "end": v(5655.25, 5906.95) * mm});
            skLineSegment(sketch, "E1422", {"start": v(5655.25, 5906.95) * mm, "end": v(5694.97, 5934.83) * mm});
            skLineSegment(sketch, "E1423", {"start": v(5694.97, 5934.83) * mm, "end": v(5740.04, 5959.3) * mm});
            skLineSegment(sketch, "E1424", {"start": v(5740.04, 5959.3) * mm, "end": v(5790.78, 5980.3) * mm});
            skLineSegment(sketch, "E1425", {"start": v(5790.78, 5980.3) * mm, "end": v(5847.5, 5997.75) * mm});
            skLineSegment(sketch, "E1426", {"start": v(5847.5, 5997.75) * mm, "end": v(5910.53, 6011.56) * mm});
            skLineSegment(sketch, "E1427", {"start": v(5910.53, 6011.56) * mm, "end": v(5970.5, 6020.46) * mm});
            skLineSegment(sketch, "E1428", {"start": v(5970.5, 6020.46) * mm, "end": v(5994.77, 6020.99) * mm});
            skLineSegment(sketch, "E1429", {"start": v(5994.77, 6020.99) * mm, "end": v(6019.57, 6018.2) * mm});
            skLineSegment(sketch, "E1430", {"start": v(6019.57, 6018.2) * mm, "end": v(6044.84, 6012.37) * mm});
            skLineSegment(sketch, "E1431", {"start": v(6044.84, 6012.37) * mm, "end": v(6070.5, 6003.76) * mm});
            skLineSegment(sketch, "E1432", {"start": v(6070.5, 6003.76) * mm, "end": v(6096.5, 5992.64) * mm});
            skLineSegment(sketch, "E1433", {"start": v(6096.5, 5992.64) * mm, "end": v(6122.74, 5979.3) * mm});
            skLineSegment(sketch, "E1434", {"start": v(6122.74, 5979.3) * mm, "end": v(6149.18, 5963.98) * mm});
            skLineSegment(sketch, "E1435", {"start": v(6149.18, 5963.98) * mm, "end": v(6175.74, 5946.97) * mm});
            skLineSegment(sketch, "E1436", {"start": v(6175.74, 5946.97) * mm, "end": v(6202.35, 5928.54) * mm});
            skLineSegment(sketch, "E1437", {"start": v(6202.35, 5928.54) * mm, "end": v(6228.94, 5908.96) * mm});
            skLineSegment(sketch, "E1438", {"start": v(6228.94, 5908.96) * mm, "end": v(6255.45, 5888.5) * mm});
            skLineSegment(sketch, "E1439", {"start": v(6255.45, 5888.5) * mm, "end": v(6281.8, 5867.41) * mm});
            skLineSegment(sketch, "E1440", {"start": v(6281.8, 5867.41) * mm, "end": v(6307.94, 5845.99) * mm});
            skLineSegment(sketch, "E1441", {"start": v(6307.94, 5845.99) * mm, "end": v(6333.79, 5824.49) * mm});
            skLineSegment(sketch, "E1442", {"start": v(6333.79, 5824.49) * mm, "end": v(6359.28, 5803.19) * mm});
            skLineSegment(sketch, "E1443", {"start": v(6359.28, 5803.19) * mm, "end": v(6384.34, 5782.36) * mm});
            skLineSegment(sketch, "E1444", {"start": v(6384.34, 5782.36) * mm, "end": v(6408.9, 5762.26) * mm});
            skLineSegment(sketch, "E1445", {"start": v(6408.9, 5762.26) * mm, "end": v(6432.9, 5743.18) * mm});
            skLineSegment(sketch, "E1446", {"start": v(6432.9, 5743.18) * mm, "end": v(6456.27, 5725.37) * mm});
            skLineSegment(sketch, "E1447", {"start": v(6456.27, 5725.37) * mm, "end": v(6478.94, 5709.1) * mm});
            skLineSegment(sketch, "E1448", {"start": v(6478.94, 5709.1) * mm, "end": v(6500.83, 5694.67) * mm});
            skLineSegment(sketch, "E1449", {"start": v(6500.83, 5694.67) * mm, "end": v(6521.9, 5682.32) * mm});
            skLineSegment(sketch, "E1450", {"start": v(6521.9, 5682.32) * mm, "end": v(6542.05, 5672.32) * mm});
            skLineSegment(sketch, "E1451", {"start": v(6542.05, 5672.32) * mm, "end": v(6561.23, 5664.96) * mm});
            skLineSegment(sketch, "E1452", {"start": v(6561.23, 5664.96) * mm, "end": v(6579.37, 5660.5) * mm});
            skLineSegment(sketch, "E1453", {"start": v(6579.37, 5660.5) * mm, "end": v(6596.39, 5659.2) * mm});
            skLineSegment(sketch, "E1454", {"start": v(6596.39, 5659.2) * mm, "end": v(6612.23, 5661.35) * mm});
            skLineSegment(sketch, "E1455", {"start": v(6612.23, 5661.35) * mm, "end": v(6626.83, 5667.2) * mm});
            skLineSegment(sketch, "E1456", {"start": v(6626.83, 5667.2) * mm, "end": v(6640.1, 5677.04) * mm});
            skLineSegment(sketch, "E1457", {"start": v(6640.1, 5677.04) * mm, "end": v(6652, 5691.13) * mm});
            skLineSegment(sketch, "E1458", {"start": v(6652, 5691.13) * mm, "end": v(6662.44, 5709.73) * mm});
            skLineSegment(sketch, "E1459", {"start": v(6662.44, 5709.73) * mm, "end": v(6671.36, 5733.13) * mm});
            skLineSegment(sketch, "E1460", {"start": v(6671.36, 5733.13) * mm, "end": v(6678.68, 5761.6) * mm});
            skLineSegment(sketch, "E1461", {"start": v(6678.68, 5761.6) * mm, "end": v(6684.35, 5795.38) * mm});
            skLineSegment(sketch, "E1462", {"start": v(6684.35, 5795.38) * mm, "end": v(6688.29, 5834.77) * mm});
            skLineSegment(sketch, "E1463", {"start": v(6688.29, 5834.77) * mm, "end": v(6680.63, 5931.87) * mm});
            skLineSegment(sketch, "E1464", {"start": v(6680.63, 5931.87) * mm, "end": v(6671.7, 6028.35) * mm});
            skLineSegment(sketch, "E1465", {"start": v(6671.7, 6028.35) * mm, "end": v(6661.5, 6124.24) * mm});
            skLineSegment(sketch, "E1466", {"start": v(6661.5, 6124.24) * mm, "end": v(6650.04, 6219.56) * mm});
            skLineSegment(sketch, "E1467", {"start": v(6650.04, 6219.56) * mm, "end": v(6637.28, 6314.33) * mm});
            skLineSegment(sketch, "E1468", {"start": v(6637.28, 6314.33) * mm, "end": v(6623.24, 6408.6) * mm});
            skLineSegment(sketch, "E1469", {"start": v(6623.24, 6408.6) * mm, "end": v(6607.9, 6502.37) * mm});
            skLineSegment(sketch, "E1470", {"start": v(6607.9, 6502.37) * mm, "end": v(6591.26, 6595.68) * mm});
            skLineSegment(sketch, "E1471", {"start": v(6591.26, 6595.68) * mm, "end": v(6573.31, 6688.56) * mm});
            skLineSegment(sketch, "E1472", {"start": v(6573.31, 6688.56) * mm, "end": v(6554.05, 6781.03) * mm});
            skLineSegment(sketch, "E1473", {"start": v(6554.05, 6781.03) * mm, "end": v(6533.46, 6873.12) * mm});
            skLineSegment(sketch, "E1474", {"start": v(6533.46, 6873.12) * mm, "end": v(6511.55, 6964.85) * mm});
            skLineSegment(sketch, "E1475", {"start": v(6511.55, 6964.85) * mm, "end": v(6488.3, 7056.26) * mm});
            skLineSegment(sketch, "E1476", {"start": v(6488.3, 7056.26) * mm, "end": v(6463.7, 7147.36) * mm});
            skLineSegment(sketch, "E1477", {"start": v(6463.7, 7147.36) * mm, "end": v(6437.77, 7238.19) * mm});
            skLineSegment(sketch, "E1478", {"start": v(6437.77, 7238.19) * mm, "end": v(6410.48, 7328.76) * mm});
            skLineSegment(sketch, "E1479", {"start": v(6410.48, 7328.76) * mm, "end": v(6381.83, 7419.12) * mm});
            skLineSegment(sketch, "E1480", {"start": v(6381.83, 7419.12) * mm, "end": v(6351.8, 7509.28) * mm});
            skLineSegment(sketch, "E1481", {"start": v(6351.8, 7509.28) * mm, "end": v(6320.41, 7599.27) * mm});
            skLineSegment(sketch, "E1482", {"start": v(6320.41, 7599.27) * mm, "end": v(6287.64, 7689.12) * mm});
            skLineSegment(sketch, "E1483", {"start": v(6287.64, 7689.12) * mm, "end": v(6253.48, 7778.85) * mm});
            skLineSegment(sketch, "E1484", {"start": v(6253.48, 7778.85) * mm, "end": v(6217.93, 7868.49) * mm});
            skLineSegment(sketch, "E1485", {"start": v(6217.93, 7868.49) * mm, "end": v(6180.97, 7958.07) * mm});
            skLineSegment(sketch, "E1486", {"start": v(6180.97, 7958.07) * mm, "end": v(6142.61, 8047.6) * mm});
            skLineSegment(sketch, "E1487", {"start": v(6142.61, -2748.37) * mm, "end": v(6053.07, -2786.75) * mm});
            skLineSegment(sketch, "E1488", {"start": v(6053.07, -2786.75) * mm, "end": v(5963.49, -2823.73) * mm});
            skLineSegment(sketch, "E1489", {"start": v(5963.49, -2823.73) * mm, "end": v(5873.84, -2859.3) * mm});
            skLineSegment(sketch, "E1490", {"start": v(5873.84, -2859.3) * mm, "end": v(5784.1, -2893.48) * mm});
            skLineSegment(sketch, "E1491", {"start": v(5784.1, -2893.48) * mm, "end": v(5694.25, -2926.27) * mm});
            skLineSegment(sketch, "E1492", {"start": v(5694.25, -2926.27) * mm, "end": v(5604.25, -2957.67) * mm});
            skLineSegment(sketch, "E1493", {"start": v(5604.25, -2957.67) * mm, "end": v(5514.08, -2987.7) * mm});
            skLineSegment(sketch, "E1494", {"start": v(5514.08, -2987.7) * mm, "end": v(5423.72, -3016.37) * mm});
            skLineSegment(sketch, "E1495", {"start": v(5423.72, -3016.37) * mm, "end": v(5333.13, -3043.67) * mm});
            skLineSegment(sketch, "E1496", {"start": v(5333.13, -3043.67) * mm, "end": v(5242.3, -3069.62) * mm});
            skLineSegment(sketch, "E1497", {"start": v(5242.3, -3069.62) * mm, "end": v(5151.18, -3094.22) * mm});
            skLineSegment(sketch, "E1498", {"start": v(5151.18, -3094.22) * mm, "end": v(5059.76, -3117.47) * mm});
            skLineSegment(sketch, "E1499", {"start": v(5059.76, -3117.47) * mm, "end": v(4968.02, -3139.4) * mm});
            skLineSegment(sketch, "E1500", {"start": v(4968.02, -3139.4) * mm, "end": v(4875.92, -3159.98) * mm});
            skLineSegment(sketch, "E1501", {"start": v(4875.92, -3159.98) * mm, "end": v(4783.43, -3179.25) * mm});
            skLineSegment(sketch, "E1502", {"start": v(4783.43, -3179.25) * mm, "end": v(4690.54, -3197.2) * mm});
            skLineSegment(sketch, "E1503", {"start": v(4690.54, -3197.2) * mm, "end": v(4597.22, -3213.85) * mm});
            skLineSegment(sketch, "E1504", {"start": v(4597.22, -3213.85) * mm, "end": v(4503.44, -3229.19) * mm});
            skLineSegment(sketch, "E1505", {"start": v(4503.44, -3229.19) * mm, "end": v(4409.17, -3243.23) * mm});
            skLineSegment(sketch, "E1506", {"start": v(4409.17, -3243.23) * mm, "end": v(4314.38, -3255.99) * mm});
            skLineSegment(sketch, "E1507", {"start": v(4314.38, -3255.99) * mm, "end": v(4219.06, -3267.46) * mm});
            skLineSegment(sketch, "E1508", {"start": v(4219.06, -3267.46) * mm, "end": v(4123.17, -3277.65) * mm});
            skLineSegment(sketch, "E1509", {"start": v(4123.17, -3277.65) * mm, "end": v(4026.69, -3286.58) * mm});
            skLineSegment(sketch, "E1510", {"start": v(4026.69, -3286.58) * mm, "end": v(3929.59, -3294.24) * mm});
            skLineSegment(sketch, "E1511", {"start": v(3929.59, -3294.24) * mm, "end": v(3856.43, -3284.64) * mm});
            skLineSegment(sketch, "E1512", {"start": v(3856.43, -3284.64) * mm, "end": v(3804.6, -3268.4) * mm});
            skLineSegment(sketch, "E1513", {"start": v(3804.6, -3268.4) * mm, "end": v(3771.93, -3246.07) * mm});
            skLineSegment(sketch, "E1514", {"start": v(3771.93, -3246.07) * mm, "end": v(3756.26, -3218.19) * mm});
            skLineSegment(sketch, "E1515", {"start": v(3756.26, -3218.19) * mm, "end": v(3755.43, -3185.31) * mm});
            skLineSegment(sketch, "E1516", {"start": v(3755.43, -3185.31) * mm, "end": v(3767.27, -3147.98) * mm});
            skLineSegment(sketch, "E1517", {"start": v(3767.27, -3147.98) * mm, "end": v(3789.63, -3106.76) * mm});
            skLineSegment(sketch, "E1518", {"start": v(3789.63, -3106.76) * mm, "end": v(3820.34, -3062.18) * mm});
            skLineSegment(sketch, "E1519", {"start": v(3820.34, -3062.18) * mm, "end": v(3857.24, -3014.8) * mm});
            skLineSegment(sketch, "E1520", {"start": v(3857.24, -3014.8) * mm, "end": v(3898.18, -2965.17) * mm});
            skLineSegment(sketch, "E1521", {"start": v(3898.18, -2965.17) * mm, "end": v(3940.98, -2913.83) * mm});
            skLineSegment(sketch, "E1522", {"start": v(3940.98, -2913.83) * mm, "end": v(3983.49, -2861.33) * mm});
            skLineSegment(sketch, "E1523", {"start": v(3983.49, -2861.33) * mm, "end": v(4023.54, -2808.23) * mm});
            skLineSegment(sketch, "E1524", {"start": v(4023.54, -2808.23) * mm, "end": v(4058.98, -2755.06) * mm});
            skLineSegment(sketch, "E1525", {"start": v(4058.98, -2755.06) * mm, "end": v(4087.65, -2702.39) * mm});
            skLineSegment(sketch, "E1526", {"start": v(4087.65, -2702.39) * mm, "end": v(4107.37, -2650.75) * mm});
            skLineSegment(sketch, "E1527", {"start": v(4107.37, -2650.75) * mm, "end": v(4116, -2600.7) * mm});
            skLineSegment(sketch, "E1528", {"start": v(4116, -2600.7) * mm, "end": v(4111.04, -2543.53) * mm});
            skLineSegment(sketch, "E1529", {"start": v(4111.04, -2543.53) * mm, "end": v(4098.69, -2477.9) * mm});
            skLineSegment(sketch, "E1530", {"start": v(4098.69, -2477.9) * mm, "end": v(4082.67, -2418.69) * mm});
            skLineSegment(sketch, "E1531", {"start": v(4082.67, -2418.69) * mm, "end": v(4063.07, -2365.6) * mm});
            skLineSegment(sketch, "E1532", {"start": v(4063.07, -2365.6) * mm, "end": v(4039.96, -2318.3) * mm});
            skLineSegment(sketch, "E1533", {"start": v(4039.96, -2318.3) * mm, "end": v(4013.42, -2276.48) * mm});
            skLineSegment(sketch, "E1534", {"start": v(4013.42, -2276.48) * mm, "end": v(3983.54, -2239.82) * mm});
            skLineSegment(sketch, "E1535", {"start": v(3983.54, -2239.82) * mm, "end": v(3950.38, -2208) * mm});
            skLineSegment(sketch, "E1536", {"start": v(3950.38, -2208) * mm, "end": v(3914.03, -2180.7) * mm});
            skLineSegment(sketch, "E1537", {"start": v(3914.03, -2180.7) * mm, "end": v(3874.57, -2157.6) * mm});
            skLineSegment(sketch, "E1538", {"start": v(3874.57, -2157.6) * mm, "end": v(3832.07, -2138.38) * mm});
            skLineSegment(sketch, "E1539", {"start": v(3832.07, -2138.38) * mm, "end": v(3786.6, -2122.73) * mm});
            skLineSegment(sketch, "E1540", {"start": v(3786.6, -2122.73) * mm, "end": v(3738.26, -2110.32) * mm});
            skLineSegment(sketch, "E1541", {"start": v(3738.26, -2110.32) * mm, "end": v(3687.12, -2100.83) * mm});
            skLineSegment(sketch, "E1542", {"start": v(3687.12, -2100.83) * mm, "end": v(3633.25, -2093.95) * mm});
            skLineSegment(sketch, "E1543", {"start": v(3633.25, -2093.95) * mm, "end": v(3576.73, -2089.36) * mm});
            skLineSegment(sketch, "E1544", {"start": v(3576.73, -2089.36) * mm, "end": v(3517.64, -2086.73) * mm});
            skLineSegment(sketch, "E1545", {"start": v(3517.64, -2086.73) * mm, "end": v(3456.06, -2085.75) * mm});
            skLineSegment(sketch, "E1546", {"start": v(3456.06, -2085.75) * mm, "end": v(3393.61, -2086.16) * mm});
            skLineSegment(sketch, "E1547", {"start": v(3393.61, -2086.16) * mm, "end": v(3333.52, -2088.09) * mm});
            skLineSegment(sketch, "E1548", {"start": v(3333.52, -2088.09) * mm, "end": v(3275.98, -2091.86) * mm});
            skLineSegment(sketch, "E1549", {"start": v(3275.98, -2091.86) * mm, "end": v(3221.05, -2097.78) * mm});
            skLineSegment(sketch, "E1550", {"start": v(3221.05, -2097.78) * mm, "end": v(3168.81, -2106.19) * mm});
            skLineSegment(sketch, "E1551", {"start": v(3168.81, -2106.19) * mm, "end": v(3119.35, -2117.4) * mm});
            skLineSegment(sketch, "E1552", {"start": v(3119.35, -2117.4) * mm, "end": v(3072.74, -2131.71) * mm});
            skLineSegment(sketch, "E1553", {"start": v(3072.74, -2131.71) * mm, "end": v(3029.06, -2149.47) * mm});
            skLineSegment(sketch, "E1554", {"start": v(3029.06, -2149.47) * mm, "end": v(2988.39, -2170.98) * mm});
            skLineSegment(sketch, "E1555", {"start": v(2988.39, -2170.98) * mm, "end": v(2950.8, -2196.56) * mm});
            skLineSegment(sketch, "E1556", {"start": v(2950.8, -2196.56) * mm, "end": v(2916.36, -2226.53) * mm});
            skLineSegment(sketch, "E1557", {"start": v(2916.36, -2226.53) * mm, "end": v(2885.17, -2261.22) * mm});
            skLineSegment(sketch, "E1558", {"start": v(2885.17, -2261.22) * mm, "end": v(2857.3, -2300.93) * mm});
            skLineSegment(sketch, "E1559", {"start": v(2857.3, -2300.93) * mm, "end": v(2832.81, -2346) * mm});
            skLineSegment(sketch, "E1560", {"start": v(2832.81, -2346) * mm, "end": v(2811.8, -2396.73) * mm});
            skLineSegment(sketch, "E1561", {"start": v(2811.8, -2396.73) * mm, "end": v(2794.34, -2453.46) * mm});
            skLineSegment(sketch, "E1562", {"start": v(2794.34, -2453.46) * mm, "end": v(2780.5, -2516.48) * mm});
            skLineSegment(sketch, "E1563", {"start": v(2780.5, -2516.48) * mm, "end": v(2771.58, -2576.44) * mm});
            skLineSegment(sketch, "E1564", {"start": v(2771.58, -2576.44) * mm, "end": v(2771.05, -2600.7) * mm});
            skLineSegment(sketch, "E1565", {"start": v(2771.05, -2600.7) * mm, "end": v(2773.84, -2625.5) * mm});
            skLineSegment(sketch, "E1566", {"start": v(2773.84, -2625.5) * mm, "end": v(2779.68, -2650.75) * mm});
            skLineSegment(sketch, "E1567", {"start": v(2779.68, -2650.75) * mm, "end": v(2788.3, -2676.4) * mm});
            skLineSegment(sketch, "E1568", {"start": v(2788.3, -2676.4) * mm, "end": v(2799.4, -2702.39) * mm});
            skLineSegment(sketch, "E1569", {"start": v(2799.4, -2702.39) * mm, "end": v(2812.76, -2728.63) * mm});
            skLineSegment(sketch, "E1570", {"start": v(2812.76, -2728.63) * mm, "end": v(2828.08, -2755.06) * mm});
            skLineSegment(sketch, "E1571", {"start": v(2828.08, -2755.06) * mm, "end": v(2845.1, -2781.62) * mm});
            skLineSegment(sketch, "E1572", {"start": v(2845.1, -2781.62) * mm, "end": v(2863.53, -2808.23) * mm});
            skLineSegment(sketch, "E1573", {"start": v(2863.53, -2808.23) * mm, "end": v(2883.12, -2834.82) * mm});
            skLineSegment(sketch, "E1574", {"start": v(2883.12, -2834.82) * mm, "end": v(2903.6, -2861.33) * mm});
            skLineSegment(sketch, "E1575", {"start": v(2903.6, -2861.33) * mm, "end": v(2924.68, -2887.69) * mm});
            skLineSegment(sketch, "E1576", {"start": v(2924.68, -2887.69) * mm, "end": v(2946.11, -2913.83) * mm});
            skLineSegment(sketch, "E1577", {"start": v(2946.11, -2913.83) * mm, "end": v(2967.62, -2939.67) * mm});
            skLineSegment(sketch, "E1578", {"start": v(2967.62, -2939.67) * mm, "end": v(2988.93, -2965.17) * mm});
            skLineSegment(sketch, "E1579", {"start": v(2988.93, -2965.17) * mm, "end": v(3009.77, -2990.23) * mm});
            skLineSegment(sketch, "E1580", {"start": v(3009.77, -2990.23) * mm, "end": v(3029.87, -3014.8) * mm});
            skLineSegment(sketch, "E1581", {"start": v(3029.87, -3014.8) * mm, "end": v(3048.96, -3038.8) * mm});
            skLineSegment(sketch, "E1582", {"start": v(3048.96, -3038.8) * mm, "end": v(3066.78, -3062.18) * mm});
            skLineSegment(sketch, "E1583", {"start": v(3066.78, -3062.18) * mm, "end": v(3083.05, -3084.85) * mm});
            skLineSegment(sketch, "E1584", {"start": v(3083.05, -3084.85) * mm, "end": v(3097.5, -3106.76) * mm});
            skLineSegment(sketch, "E1585", {"start": v(3097.5, -3106.76) * mm, "end": v(3109.86, -3127.82) * mm});
            skLineSegment(sketch, "E1586", {"start": v(3109.86, -3127.82) * mm, "end": v(3119.86, -3147.98) * mm});
            skLineSegment(sketch, "E1587", {"start": v(3119.86, -3147.98) * mm, "end": v(3127.23, -3167.17) * mm});
            skLineSegment(sketch, "E1588", {"start": v(3127.23, -3167.17) * mm, "end": v(3131.7, -3185.31) * mm});
            skLineSegment(sketch, "E1589", {"start": v(3131.7, -3185.31) * mm, "end": v(3133, -3202.34) * mm});
            skLineSegment(sketch, "E1590", {"start": v(3133, -3202.34) * mm, "end": v(3130.86, -3218.19) * mm});
            skLineSegment(sketch, "E1591", {"start": v(3130.86, -3218.19) * mm, "end": v(3125.01, -3232.79) * mm});
            skLineSegment(sketch, "E1592", {"start": v(3125.01, -3232.79) * mm, "end": v(3115.18, -3246.07) * mm});
            skLineSegment(sketch, "E1593", {"start": v(3115.18, -3246.07) * mm, "end": v(3101.1, -3257.96) * mm});
            skLineSegment(sketch, "E1594", {"start": v(3101.1, -3257.96) * mm, "end": v(3082.5, -3268.4) * mm});
            skLineSegment(sketch, "E1595", {"start": v(3082.5, -3268.4) * mm, "end": v(3059.1, -3277.32) * mm});
            skLineSegment(sketch, "E1596", {"start": v(3059.1, -3277.32) * mm, "end": v(3030.64, -3284.64) * mm});
            skLineSegment(sketch, "E1597", {"start": v(3030.64, -3284.64) * mm, "end": v(2996.85, -3290.3) * mm});
            skLineSegment(sketch, "E1598", {"start": v(2996.85, -3290.3) * mm, "end": v(2957.46, -3294.24) * mm});
            skLineSegment(sketch, "E1599", {"start": v(2957.46, -3294.24) * mm, "end": v(2860.36, -3286.58) * mm});
            skLineSegment(sketch, "E1600", {"start": v(2860.36, -3286.58) * mm, "end": v(2763.88, -3277.65) * mm});
            skLineSegment(sketch, "E1601", {"start": v(2763.88, -3277.65) * mm, "end": v(2667.99, -3267.46) * mm});
            skLineSegment(sketch, "E1602", {"start": v(2667.99, -3267.46) * mm, "end": v(2572.66, -3255.99) * mm});
            skLineSegment(sketch, "E1603", {"start": v(2572.66, -3255.99) * mm, "end": v(2477.88, -3243.23) * mm});
            skLineSegment(sketch, "E1604", {"start": v(2477.88, -3243.23) * mm, "end": v(2383.6, -3229.19) * mm});
            skLineSegment(sketch, "E1605", {"start": v(2383.6, -3229.19) * mm, "end": v(2289.83, -3213.85) * mm});
            skLineSegment(sketch, "E1606", {"start": v(2289.83, -3213.85) * mm, "end": v(2196.5, -3197.2) * mm});
            skLineSegment(sketch, "E1607", {"start": v(2196.5, -3197.2) * mm, "end": v(2103.62, -3179.25) * mm});
            skLineSegment(sketch, "E1608", {"start": v(2103.62, -3179.25) * mm, "end": v(2011.14, -3159.98) * mm});
            skLineSegment(sketch, "E1609", {"start": v(2011.14, -3159.98) * mm, "end": v(1919.05, -3139.4) * mm});
            skLineSegment(sketch, "E1610", {"start": v(1919.05, -3139.4) * mm, "end": v(1827.3, -3117.47) * mm});
            skLineSegment(sketch, "E1611", {"start": v(1827.3, -3117.47) * mm, "end": v(1735.9, -3094.22) * mm});
            skLineSegment(sketch, "E1612", {"start": v(1735.9, -3094.22) * mm, "end": v(1692.6, -3082.53) * mm});
            skLineSegment(sketch, "E1613", {"start": v(2957.46, -7600.75) * mm, "end": v(3025.39, -7609.28) * mm});
            skLineSegment(sketch, "E1614", {"start": v(3025.39, -7609.28) * mm, "end": v(3075.24, -7623.44) * mm});
            skLineSegment(sketch, "E1615", {"start": v(3075.24, -7623.44) * mm, "end": v(3108.69, -7642.8) * mm});
            skLineSegment(sketch, "E1616", {"start": v(3108.69, -7642.8) * mm, "end": v(3127.39, -7666.92) * mm});
            skLineSegment(sketch, "E1617", {"start": v(3127.39, -7666.92) * mm, "end": v(3133.01, -7695.4) * mm});
            skLineSegment(sketch, "E1618", {"start": v(3133.01, -7695.4) * mm, "end": v(3127.23, -7727.82) * mm});
            skLineSegment(sketch, "E1619", {"start": v(3127.23, -7727.82) * mm, "end": v(3111.7, -7763.74) * mm});
            skLineSegment(sketch, "E1620", {"start": v(3111.7, -7763.74) * mm, "end": v(3088.08, -7802.74) * mm});
            skLineSegment(sketch, "E1621", {"start": v(3088.08, -7802.74) * mm, "end": v(3058.05, -7844.41) * mm});
            skLineSegment(sketch, "E1622", {"start": v(3058.05, -7844.41) * mm, "end": v(3023.27, -7888.32) * mm});
            skLineSegment(sketch, "E1623", {"start": v(3023.27, -7888.32) * mm, "end": v(2985.4, -7934.04) * mm});
            skLineSegment(sketch, "E1624", {"start": v(2985.4, -7934.04) * mm, "end": v(2946.11, -7981.16) * mm});
            skLineSegment(sketch, "E1625", {"start": v(2946.11, -7981.16) * mm, "end": v(2907.07, -8029.25) * mm});
            skLineSegment(sketch, "E1626", {"start": v(2907.07, -8029.25) * mm, "end": v(2869.94, -8077.9) * mm});
            skLineSegment(sketch, "E1627", {"start": v(2869.94, -8077.9) * mm, "end": v(2836.39, -8126.66) * mm});
            skLineSegment(sketch, "E1628", {"start": v(2836.39, -8126.66) * mm, "end": v(2808.08, -8175.13) * mm});
            skLineSegment(sketch, "E1629", {"start": v(2808.08, -8175.13) * mm, "end": v(2786.67, -8222.88) * mm});
            skLineSegment(sketch, "E1630", {"start": v(2786.67, -8222.88) * mm, "end": v(2773.84, -8269.5) * mm});
            skLineSegment(sketch, "E1631", {"start": v(2773.84, -8269.5) * mm, "end": v(2771.25, -8314.54) * mm});
            skLineSegment(sketch, "E1632", {"start": v(2771.25, -8314.54) * mm, "end": v(2779.72, -8374.07) * mm});
            skLineSegment(sketch, "E1633", {"start": v(2779.72, -8374.07) * mm, "end": v(2792.03, -8432.49) * mm});
            skLineSegment(sketch, "E1634", {"start": v(2792.03, -8432.49) * mm, "end": v(2807.4, -8485.56) * mm});
            skLineSegment(sketch, "E1635", {"start": v(2807.4, -8485.56) * mm, "end": v(2825.78, -8533.55) * mm});
            skLineSegment(sketch, "E1636", {"start": v(2825.78, -8533.55) * mm, "end": v(2847.1, -8576.69) * mm});
            skLineSegment(sketch, "E1637", {"start": v(2847.1, -8576.69) * mm, "end": v(2871.28, -8615.22) * mm});
            skLineSegment(sketch, "E1638", {"start": v(2871.28, -8615.22) * mm, "end": v(2898.28, -8649.4) * mm});
            skLineSegment(sketch, "E1639", {"start": v(2898.28, -8649.4) * mm, "end": v(2928.05, -8679.46) * mm});
            skLineSegment(sketch, "E1640", {"start": v(2928.05, -8679.46) * mm, "end": v(2960.51, -8705.67) * mm});
            skLineSegment(sketch, "E1641", {"start": v(2960.51, -8705.67) * mm, "end": v(2995.61, -8728.25) * mm});
            skLineSegment(sketch, "E1642", {"start": v(2995.61, -8728.25) * mm, "end": v(3033.3, -8747.46) * mm});
            skLineSegment(sketch, "E1643", {"start": v(3033.3, -8747.46) * mm, "end": v(3073.5, -8763.54) * mm});
            skLineSegment(sketch, "E1644", {"start": v(3073.5, -8763.54) * mm, "end": v(3116.16, -8776.74) * mm});
            skLineSegment(sketch, "E1645", {"start": v(3116.16, -8776.74) * mm, "end": v(3161.22, -8787.3) * mm});
            skLineSegment(sketch, "E1646", {"start": v(3161.22, -8787.3) * mm, "end": v(3208.61, -8795.48) * mm});
            skLineSegment(sketch, "E1647", {"start": v(3208.61, -8795.48) * mm, "end": v(3258.3, -8801.5) * mm});
            skLineSegment(sketch, "E1648", {"start": v(3258.3, -8801.5) * mm, "end": v(3310.2, -8805.63) * mm});
            skLineSegment(sketch, "E1649", {"start": v(3310.2, -8805.63) * mm, "end": v(3364.26, -8808.1) * mm});
            skLineSegment(sketch, "E1650", {"start": v(3364.26, -8808.1) * mm, "end": v(3420.42, -8809.17) * mm});
            skLineSegment(sketch, "E1651", {"start": v(3420.42, -8809.17) * mm, "end": v(3477.91, -8809.06) * mm});
            skLineSegment(sketch, "E1652", {"start": v(3477.91, -8809.06) * mm, "end": v(3533.69, -8807.73) * mm});
            skLineSegment(sketch, "E1653", {"start": v(3533.69, -8807.73) * mm, "end": v(3587.34, -8804.95) * mm});
            skLineSegment(sketch, "E1654", {"start": v(3587.34, -8804.95) * mm, "end": v(3638.82, -8800.46) * mm});
            skLineSegment(sketch, "E1655", {"start": v(3638.82, -8800.46) * mm, "end": v(3688.07, -8794.02) * mm});
            skLineSegment(sketch, "E1656", {"start": v(3688.07, -8794.02) * mm, "end": v(3735.02, -8785.39) * mm});
            skLineSegment(sketch, "E1657", {"start": v(3735.02, -8785.39) * mm, "end": v(3779.62, -8774.32) * mm});
            skLineSegment(sketch, "E1658", {"start": v(3779.62, -8774.32) * mm, "end": v(3821.8, -8760.56) * mm});
            skLineSegment(sketch, "E1659", {"start": v(3821.8, -8760.56) * mm, "end": v(3861.51, -8743.88) * mm});
            skLineSegment(sketch, "E1660", {"start": v(3861.51, -8743.88) * mm, "end": v(3898.7, -8724.01) * mm});
            skLineSegment(sketch, "E1661", {"start": v(3898.7, -8724.01) * mm, "end": v(3933.27, -8700.72) * mm});
            skLineSegment(sketch, "E1662", {"start": v(3933.27, -8700.72) * mm, "end": v(3965.2, -8673.77) * mm});
            skLineSegment(sketch, "E1663", {"start": v(3965.2, -8673.77) * mm, "end": v(3994.42, -8642.9) * mm});
            skLineSegment(sketch, "E1664", {"start": v(3994.42, -8642.9) * mm, "end": v(4020.87, -8607.87) * mm});
            skLineSegment(sketch, "E1665", {"start": v(4020.87, -8607.87) * mm, "end": v(4044.48, -8568.43) * mm});
            skLineSegment(sketch, "E1666", {"start": v(4044.48, -8568.43) * mm, "end": v(4065.2, -8524.35) * mm});
            skLineSegment(sketch, "E1667", {"start": v(4065.2, -8524.35) * mm, "end": v(4082.97, -8475.36) * mm});
            skLineSegment(sketch, "E1668", {"start": v(4082.97, -8475.36) * mm, "end": v(4097.73, -8421.24) * mm});
            skLineSegment(sketch, "E1669", {"start": v(4097.73, -8421.24) * mm, "end": v(4109.42, -8361.72) * mm});
            skLineSegment(sketch, "E1670", {"start": v(4109.42, -8361.72) * mm, "end": v(4115.8, -8314.54) * mm});
            skLineSegment(sketch, "E1671", {"start": v(4115.8, -8314.54) * mm, "end": v(4115.86, -8292.22) * mm});
            skLineSegment(sketch, "E1672", {"start": v(4115.86, -8292.22) * mm, "end": v(4113.17, -8269.46) * mm});
            skLineSegment(sketch, "E1673", {"start": v(4113.17, -8269.46) * mm, "end": v(4107.92, -8246.31) * mm});
            skLineSegment(sketch, "E1674", {"start": v(4107.92, -8246.31) * mm, "end": v(4100.32, -8222.83) * mm});
            skLineSegment(sketch, "E1675", {"start": v(4100.32, -8222.83) * mm, "end": v(4090.58, -8199.06) * mm});
            skLineSegment(sketch, "E1676", {"start": v(4090.58, -8199.06) * mm, "end": v(4078.91, -8175.06) * mm});
            skLineSegment(sketch, "E1677", {"start": v(4078.91, -8175.06) * mm, "end": v(4065.51, -8150.88) * mm});
            skLineSegment(sketch, "E1678", {"start": v(4065.51, -8150.88) * mm, "end": v(4050.6, -8126.58) * mm});
            skLineSegment(sketch, "E1679", {"start": v(4050.6, -8126.58) * mm, "end": v(4034.37, -8102.2) * mm});
            skLineSegment(sketch, "E1680", {"start": v(4034.37, -8102.2) * mm, "end": v(4017.05, -8077.8) * mm});
            skLineSegment(sketch, "E1681", {"start": v(4017.05, -8077.8) * mm, "end": v(3998.83, -8053.44) * mm});
            skLineSegment(sketch, "E1682", {"start": v(3998.83, -8053.44) * mm, "end": v(3979.92, -8029.17) * mm});
            skLineSegment(sketch, "E1683", {"start": v(3979.92, -8029.17) * mm, "end": v(3960.54, -8005.02) * mm});
            skLineSegment(sketch, "E1684", {"start": v(3960.54, -8005.02) * mm, "end": v(3940.9, -7981.08) * mm});
            skLineSegment(sketch, "E1685", {"start": v(3940.9, -7981.08) * mm, "end": v(3921.18, -7957.37) * mm});
            skLineSegment(sketch, "E1686", {"start": v(3921.18, -7957.37) * mm, "end": v(3901.62, -7933.96) * mm});
            skLineSegment(sketch, "E1687", {"start": v(3901.62, -7933.96) * mm, "end": v(3882.41, -7910.9) * mm});
            skLineSegment(sketch, "E1688", {"start": v(3882.41, -7910.9) * mm, "end": v(3863.77, -7888.24) * mm});
            skLineSegment(sketch, "E1689", {"start": v(3863.77, -7888.24) * mm, "end": v(3845.9, -7866.04) * mm});
            skLineSegment(sketch, "E1690", {"start": v(3845.9, -7866.04) * mm, "end": v(3829, -7844.34) * mm});
            skLineSegment(sketch, "E1691", {"start": v(3829, -7844.34) * mm, "end": v(3813.3, -7823.2) * mm});
            skLineSegment(sketch, "E1692", {"start": v(3813.3, -7823.2) * mm, "end": v(3798.99, -7802.68) * mm});
            skLineSegment(sketch, "E1693", {"start": v(3798.99, -7802.68) * mm, "end": v(3786.28, -7782.83) * mm});
            skLineSegment(sketch, "E1694", {"start": v(3786.28, -7782.83) * mm, "end": v(3775.39, -7763.69) * mm});
            skLineSegment(sketch, "E1695", {"start": v(3775.39, -7763.69) * mm, "end": v(3766.5, -7745.32) * mm});
            skLineSegment(sketch, "E1696", {"start": v(3766.5, -7745.32) * mm, "end": v(3759.86, -7727.78) * mm});
            skLineSegment(sketch, "E1697", {"start": v(3759.86, -7727.78) * mm, "end": v(3755.65, -7711.11) * mm});
            skLineSegment(sketch, "E1698", {"start": v(3755.65, -7711.11) * mm, "end": v(3754.08, -7695.38) * mm});
            skLineSegment(sketch, "E1699", {"start": v(3754.08, -7695.38) * mm, "end": v(3755.37, -7680.62) * mm});
            skLineSegment(sketch, "E1700", {"start": v(3755.37, -7680.62) * mm, "end": v(3759.7, -7666.9) * mm});
            skLineSegment(sketch, "E1701", {"start": v(3759.7, -7666.9) * mm, "end": v(3767.32, -7654.27) * mm});
            skLineSegment(sketch, "E1702", {"start": v(3767.32, -7654.27) * mm, "end": v(3778.4, -7642.78) * mm});
            skLineSegment(sketch, "E1703", {"start": v(3778.4, -7642.78) * mm, "end": v(3793.18, -7632.48) * mm});
            skLineSegment(sketch, "E1704", {"start": v(3793.18, -7632.48) * mm, "end": v(3811.85, -7623.43) * mm});
            skLineSegment(sketch, "E1705", {"start": v(3811.85, -7623.43) * mm, "end": v(3834.61, -7615.68) * mm});
            skLineSegment(sketch, "E1706", {"start": v(3834.61, -7615.68) * mm, "end": v(3861.68, -7609.28) * mm});
            skLineSegment(sketch, "E1707", {"start": v(3861.68, -7609.28) * mm, "end": v(3893.27, -7604.29) * mm});
            skLineSegment(sketch, "E1708", {"start": v(3893.27, -7604.29) * mm, "end": v(3929.59, -7600.75) * mm});
            skLineSegment(sketch, "E1709", {"start": v(3929.59, -7600.75) * mm, "end": v(4026.69, -7608.4) * mm});
            skLineSegment(sketch, "E1710", {"start": v(4026.69, -7608.4) * mm, "end": v(4123.17, -7617.33) * mm});
            skLineSegment(sketch, "E1711", {"start": v(4123.17, -7617.33) * mm, "end": v(4219.06, -7627.53) * mm});
            skLineSegment(sketch, "E1712", {"start": v(4219.06, -7627.53) * mm, "end": v(4314.38, -7639) * mm});
            skLineSegment(sketch, "E1713", {"start": v(4314.38, -7639) * mm, "end": v(4409.17, -7651.75) * mm});
            skLineSegment(sketch, "E1714", {"start": v(4409.17, -7651.75) * mm, "end": v(4503.44, -7665.8) * mm});
            skLineSegment(sketch, "E1715", {"start": v(4503.44, -7665.8) * mm, "end": v(4597.22, -7681.14) * mm});
            skLineSegment(sketch, "E1716", {"start": v(4597.22, -7681.14) * mm, "end": v(4690.54, -7697.78) * mm});
            skLineSegment(sketch, "E1717", {"start": v(4690.54, -7697.78) * mm, "end": v(4783.43, -7715.73) * mm});
            skLineSegment(sketch, "E1718", {"start": v(4783.43, -7715.73) * mm, "end": v(4875.92, -7735) * mm});
            skLineSegment(sketch, "E1719", {"start": v(4875.92, -7735) * mm, "end": v(4968.02, -7755.6) * mm});
            skLineSegment(sketch, "E1720", {"start": v(4968.02, -7755.6) * mm, "end": v(5059.76, -7777.51) * mm});
            skLineSegment(sketch, "E1721", {"start": v(5059.76, -7777.51) * mm, "end": v(5151.18, -7800.77) * mm});
            skLineSegment(sketch, "E1722", {"start": v(5151.18, -7800.77) * mm, "end": v(5242.3, -7825.37) * mm});
            skLineSegment(sketch, "E1723", {"start": v(5242.3, -7825.37) * mm, "end": v(5333.13, -7851.31) * mm});
            skLineSegment(sketch, "E1724", {"start": v(5333.13, -7851.31) * mm, "end": v(5423.72, -7878.62) * mm});
            skLineSegment(sketch, "E1725", {"start": v(5423.72, -7878.62) * mm, "end": v(5514.08, -7907.28) * mm});
            skLineSegment(sketch, "E1726", {"start": v(5514.08, -7907.28) * mm, "end": v(5604.25, -7937.31) * mm});
            skLineSegment(sketch, "E1727", {"start": v(5604.25, -7937.31) * mm, "end": v(5694.25, -7968.72) * mm});
            skLineSegment(sketch, "E1728", {"start": v(5694.25, -7968.72) * mm, "end": v(5784.1, -8001.5) * mm});
            skLineSegment(sketch, "E1729", {"start": v(5784.1, -8001.5) * mm, "end": v(5873.84, -8035.69) * mm});
            skLineSegment(sketch, "E1730", {"start": v(5873.84, -8035.69) * mm, "end": v(5963.49, -8071.26) * mm});
            skLineSegment(sketch, "E1731", {"start": v(5963.49, -8071.26) * mm, "end": v(6053.07, -8108.23) * mm});
            skLineSegment(sketch, "E1732", {"start": v(6053.07, -8108.23) * mm, "end": v(6142.61, -8146.62) * mm});
            skLineSegment(sketch, "E1733", {"start": v(6142.61, -8146.62) * mm, "end": v(6180.97, -8057.07) * mm});
            skLineSegment(sketch, "E1734", {"start": v(6180.97, -8057.07) * mm, "end": v(6217.93, -7967.5) * mm});
            skLineSegment(sketch, "E1735", {"start": v(6217.93, -7967.5) * mm, "end": v(6253.48, -7877.85) * mm});
            skLineSegment(sketch, "E1736", {"start": v(6253.48, -7877.85) * mm, "end": v(6287.64, -7788.11) * mm});
            skLineSegment(sketch, "E1737", {"start": v(6287.64, -7788.11) * mm, "end": v(6320.41, -7698.26) * mm});
            skLineSegment(sketch, "E1738", {"start": v(6320.41, -7698.26) * mm, "end": v(6351.8, -7608.26) * mm});
            skLineSegment(sketch, "E1739", {"start": v(6351.8, -7608.26) * mm, "end": v(6381.83, -7518.09) * mm});
            skLineSegment(sketch, "E1740", {"start": v(6381.83, -7518.09) * mm, "end": v(6410.48, -7427.72) * mm});
            skLineSegment(sketch, "E1741", {"start": v(6410.48, -7427.72) * mm, "end": v(6437.77, -7337.13) * mm});
            skLineSegment(sketch, "E1742", {"start": v(6437.77, -7337.13) * mm, "end": v(6463.7, -7246.3) * mm});
            skLineSegment(sketch, "E1743", {"start": v(6463.7, -7246.3) * mm, "end": v(6488.3, -7155.18) * mm});
            skLineSegment(sketch, "E1744", {"start": v(6488.3, -7155.18) * mm, "end": v(6511.55, -7063.76) * mm});
            skLineSegment(sketch, "E1745", {"start": v(6511.55, -7063.76) * mm, "end": v(6533.46, -6972.02) * mm});
            skLineSegment(sketch, "E1746", {"start": v(6533.46, -6972.02) * mm, "end": v(6554.05, -6879.92) * mm});
            skLineSegment(sketch, "E1747", {"start": v(6554.05, -6879.92) * mm, "end": v(6573.31, -6787.44) * mm});
            skLineSegment(sketch, "E1748", {"start": v(6573.31, -6787.44) * mm, "end": v(6591.26, -6694.55) * mm});
            skLineSegment(sketch, "E1749", {"start": v(6591.26, -6694.55) * mm, "end": v(6607.9, -6601.22) * mm});
            skLineSegment(sketch, "E1750", {"start": v(6607.9, -6601.22) * mm, "end": v(6623.24, -6507.44) * mm});
            skLineSegment(sketch, "E1751", {"start": v(6623.24, -6507.44) * mm, "end": v(6637.28, -6413.17) * mm});
            skLineSegment(sketch, "E1752", {"start": v(6637.28, -6413.17) * mm, "end": v(6650.04, -6318.39) * mm});
            skLineSegment(sketch, "E1753", {"start": v(6650.04, -6318.39) * mm, "end": v(6661.5, -6223.06) * mm});
            skLineSegment(sketch, "E1754", {"start": v(6661.5, -6223.06) * mm, "end": v(6671.7, -6127.17) * mm});
            skLineSegment(sketch, "E1755", {"start": v(6671.7, -6127.17) * mm, "end": v(6680.63, -6030.7) * mm});
            skLineSegment(sketch, "E1756", {"start": v(6680.63, -6030.7) * mm, "end": v(6688.29, -5933.59) * mm});
            skLineSegment(sketch, "E1757", {"start": v(6688.29, -5933.59) * mm, "end": v(6678.68, -5860.4) * mm});
            skLineSegment(sketch, "E1758", {"start": v(6678.68, -5860.4) * mm, "end": v(6662.44, -5808.55) * mm});
            skLineSegment(sketch, "E1759", {"start": v(6662.44, -5808.55) * mm, "end": v(6640.1, -5775.85) * mm});
            skLineSegment(sketch, "E1760", {"start": v(6640.1, -5775.85) * mm, "end": v(6612.23, -5760.16) * mm});
            skLineSegment(sketch, "E1761", {"start": v(6612.23, -5760.16) * mm, "end": v(6579.37, -5759.31) * mm});
            skLineSegment(sketch, "E1762", {"start": v(6579.37, -5759.31) * mm, "end": v(6542.05, -5771.14) * mm});
            skLineSegment(sketch, "E1763", {"start": v(6542.05, -5771.14) * mm, "end": v(6500.83, -5793.5) * mm});
            skLineSegment(sketch, "E1764", {"start": v(6500.83, -5793.5) * mm, "end": v(6456.27, -5824.2) * mm});
            skLineSegment(sketch, "E1765", {"start": v(6456.27, -5824.2) * mm, "end": v(6408.9, -5861.1) * mm});
            skLineSegment(sketch, "E1766", {"start": v(6408.9, -5861.1) * mm, "end": v(6359.28, -5902.03) * mm});
            skLineSegment(sketch, "E1767", {"start": v(6359.28, -5902.03) * mm, "end": v(6307.94, -5944.83) * mm});
            skLineSegment(sketch, "E1768", {"start": v(6307.94, -5944.83) * mm, "end": v(6255.45, -5987.35) * mm});
            skLineSegment(sketch, "E1769", {"start": v(6255.45, -5987.35) * mm, "end": v(6202.35, -6027.41) * mm});
            skLineSegment(sketch, "E1770", {"start": v(6202.35, -6027.41) * mm, "end": v(6149.18, -6062.86) * mm});
            skLineSegment(sketch, "E1771", {"start": v(6149.18, -6062.86) * mm, "end": v(6096.5, -6091.54) * mm});
            skLineSegment(sketch, "E1772", {"start": v(6096.5, -6091.54) * mm, "end": v(6044.84, -6111.28) * mm});
            skLineSegment(sketch, "E1773", {"start": v(6044.84, -6111.28) * mm, "end": v(5994.77, -6119.92) * mm});
            skLineSegment(sketch, "E1774", {"start": v(5994.77, -6119.92) * mm, "end": v(5937.58, -6114.98) * mm});
            skLineSegment(sketch, "E1775", {"start": v(5937.58, -6114.98) * mm, "end": v(5871.94, -6102.62) * mm});
            skLineSegment(sketch, "E1776", {"start": v(5871.94, -6102.62) * mm, "end": v(5812.73, -6086.6) * mm});
            skLineSegment(sketch, "E1777", {"start": v(5812.73, -6086.6) * mm, "end": v(5759.64, -6067) * mm});
            skLineSegment(sketch, "E1778", {"start": v(5759.64, -6067) * mm, "end": v(5712.34, -6043.9) * mm});
            skLineSegment(sketch, "E1779", {"start": v(5712.34, -6043.9) * mm, "end": v(5670.52, -6017.36) * mm});
            skLineSegment(sketch, "E1780", {"start": v(5670.52, -6017.36) * mm, "end": v(5633.85, -5987.48) * mm});
            skLineSegment(sketch, "E1781", {"start": v(5633.85, -5987.48) * mm, "end": v(5602.03, -5954.32) * mm});
            skLineSegment(sketch, "E1782", {"start": v(5602.03, -5954.32) * mm, "end": v(5574.72, -5917.97) * mm});
            skLineSegment(sketch, "E1783", {"start": v(5574.72, -5917.97) * mm, "end": v(5551.62, -5878.5) * mm});
            skLineSegment(sketch, "E1784", {"start": v(5551.62, -5878.5) * mm, "end": v(5532.4, -5836) * mm});
            skLineSegment(sketch, "E1785", {"start": v(5532.4, -5836) * mm, "end": v(5516.73, -5790.54) * mm});
            skLineSegment(sketch, "E1786", {"start": v(5516.73, -5790.54) * mm, "end": v(5504.32, -5742.2) * mm});
            skLineSegment(sketch, "E1787", {"start": v(5504.32, -5742.2) * mm, "end": v(5494.82, -5691.06) * mm});
            skLineSegment(sketch, "E1788", {"start": v(5494.82, -5691.06) * mm, "end": v(5487.94, -5637.18) * mm});
            skLineSegment(sketch, "E1789", {"start": v(5487.94, -5637.18) * mm, "end": v(5483.34, -5580.67) * mm});
            skLineSegment(sketch, "E1790", {"start": v(5483.34, -5580.67) * mm, "end": v(5480.72, -5521.58) * mm});
            skLineSegment(sketch, "E1791", {"start": v(5480.72, -5521.58) * mm, "end": v(5479.74, -5460) * mm});
            skLineSegment(sketch, "E1792", {"start": v(5479.74, -5460) * mm, "end": v(5480.14, -5397.55) * mm});
            skLineSegment(sketch, "E1793", {"start": v(5480.14, -5397.55) * mm, "end": v(5482.07, -5337.46) * mm});
            skLineSegment(sketch, "E1794", {"start": v(5482.07, -5337.46) * mm, "end": v(5485.85, -5279.92) * mm});
            skLineSegment(sketch, "E1795", {"start": v(5485.85, -5279.92) * mm, "end": v(5491.78, -5224.99) * mm});
            skLineSegment(sketch, "E1796", {"start": v(5491.78, -5224.99) * mm, "end": v(5500.19, -5172.75) * mm});
            skLineSegment(sketch, "E1797", {"start": v(5500.19, -5172.75) * mm, "end": v(5511.4, -5123.3) * mm});
            skLineSegment(sketch, "E1798", {"start": v(5511.4, -5123.3) * mm, "end": v(5525.72, -5076.69) * mm});
            skLineSegment(sketch, "E1799", {"start": v(5525.72, -5076.69) * mm, "end": v(5543.48, -5033) * mm});
            skLineSegment(sketch, "E1800", {"start": v(5543.48, -5033) * mm, "end": v(5565, -4992.33) * mm});
            skLineSegment(sketch, "E1801", {"start": v(5565, -4992.33) * mm, "end": v(5590.58, -4954.74) * mm});
            skLineSegment(sketch, "E1802", {"start": v(5590.58, -4954.74) * mm, "end": v(5620.56, -4920.32) * mm});
            skLineSegment(sketch, "E1803", {"start": v(5620.56, -4920.32) * mm, "end": v(5655.25, -4889.13) * mm});
            skLineSegment(sketch, "E1804", {"start": v(5655.25, -4889.13) * mm, "end": v(5694.97, -4861.26) * mm});
            skLineSegment(sketch, "E1805", {"start": v(5694.97, -4861.26) * mm, "end": v(5740.04, -4836.78) * mm});
            skLineSegment(sketch, "E1806", {"start": v(5740.04, -4836.78) * mm, "end": v(5790.78, -4815.78) * mm});
            skLineSegment(sketch, "E1807", {"start": v(5790.78, -4815.78) * mm, "end": v(5847.5, -4798.33) * mm});
            skLineSegment(sketch, "E1808", {"start": v(5847.5, -4798.33) * mm, "end": v(5910.53, -4784.5) * mm});
            skLineSegment(sketch, "E1809", {"start": v(5910.53, -4784.5) * mm, "end": v(5970.5, -4775.58) * mm});
            skLineSegment(sketch, "E1810", {"start": v(5970.5, -4775.58) * mm, "end": v(5994.77, -4775.05) * mm});
            skLineSegment(sketch, "E1811", {"start": v(5994.77, -4775.05) * mm, "end": v(6019.57, -4777.83) * mm});
            skLineSegment(sketch, "E1812", {"start": v(6019.57, -4777.83) * mm, "end": v(6044.84, -4783.66) * mm});
            skLineSegment(sketch, "E1813", {"start": v(6044.84, -4783.66) * mm, "end": v(6070.5, -4792.27) * mm});
            skLineSegment(sketch, "E1814", {"start": v(6070.5, -4792.27) * mm, "end": v(6096.5, -4803.38) * mm});
            skLineSegment(sketch, "E1815", {"start": v(6096.5, -4803.38) * mm, "end": v(6122.74, -4816.72) * mm});
            skLineSegment(sketch, "E1816", {"start": v(6122.74, -4816.72) * mm, "end": v(6149.18, -4832.03) * mm});
            skLineSegment(sketch, "E1817", {"start": v(6149.18, -4832.03) * mm, "end": v(6175.74, -4849.04) * mm});
            skLineSegment(sketch, "E1818", {"start": v(6175.74, -4849.04) * mm, "end": v(6202.35, -4867.46) * mm});
            skLineSegment(sketch, "E1819", {"start": v(6202.35, -4867.46) * mm, "end": v(6228.94, -4887.05) * mm});
            skLineSegment(sketch, "E1820", {"start": v(6228.94, -4887.05) * mm, "end": v(6255.45, -4907.51) * mm});
            skLineSegment(sketch, "E1821", {"start": v(6255.45, -4907.51) * mm, "end": v(6281.8, -4928.6) * mm});
            skLineSegment(sketch, "E1822", {"start": v(6281.8, -4928.6) * mm, "end": v(6307.94, -4950.02) * mm});
            skLineSegment(sketch, "E1823", {"start": v(6307.94, -4950.02) * mm, "end": v(6333.79, -4971.52) * mm});
            skLineSegment(sketch, "E1824", {"start": v(6333.79, -4971.52) * mm, "end": v(6359.28, -4992.82) * mm});
            skLineSegment(sketch, "E1825", {"start": v(6359.28, -4992.82) * mm, "end": v(6384.34, -5013.65) * mm});
            skLineSegment(sketch, "E1826", {"start": v(6384.34, -5013.65) * mm, "end": v(6408.9, -5033.75) * mm});
            skLineSegment(sketch, "E1827", {"start": v(6408.9, -5033.75) * mm, "end": v(6432.9, -5052.84) * mm});
            skLineSegment(sketch, "E1828", {"start": v(6432.9, -5052.84) * mm, "end": v(6456.27, -5070.65) * mm});
            skLineSegment(sketch, "E1829", {"start": v(6456.27, -5070.65) * mm, "end": v(6478.94, -5086.91) * mm});
            skLineSegment(sketch, "E1830", {"start": v(6478.94, -5086.91) * mm, "end": v(6500.83, -5101.36) * mm});
            skLineSegment(sketch, "E1831", {"start": v(6500.83, -5101.36) * mm, "end": v(6521.9, -5113.71) * mm});
            skLineSegment(sketch, "E1832", {"start": v(6521.9, -5113.71) * mm, "end": v(6542.05, -5123.71) * mm});
            skLineSegment(sketch, "E1833", {"start": v(6542.05, -5123.71) * mm, "end": v(6561.23, -5131.08) * mm});
            skLineSegment(sketch, "E1834", {"start": v(6561.23, -5131.08) * mm, "end": v(6579.37, -5135.56) * mm});
            skLineSegment(sketch, "E1835", {"start": v(6579.37, -5135.56) * mm, "end": v(6596.39, -5136.86) * mm});
            skLineSegment(sketch, "E1836", {"start": v(6596.39, -5136.86) * mm, "end": v(6612.23, -5134.72) * mm});
            skLineSegment(sketch, "E1837", {"start": v(6612.23, -5134.72) * mm, "end": v(6626.83, -5128.88) * mm});
            skLineSegment(sketch, "E1838", {"start": v(6626.83, -5128.88) * mm, "end": v(6640.1, -5119.05) * mm});
            skLineSegment(sketch, "E1839", {"start": v(6640.1, -5119.05) * mm, "end": v(6652, -5104.98) * mm});
            skLineSegment(sketch, "E1840", {"start": v(6652, -5104.98) * mm, "end": v(6662.44, -5086.38) * mm});
            skLineSegment(sketch, "E1841", {"start": v(6662.44, -5086.38) * mm, "end": v(6671.36, -5063) * mm});
            skLineSegment(sketch, "E1842", {"start": v(6671.36, -5063) * mm, "end": v(6678.68, -5034.55) * mm});
            skLineSegment(sketch, "E1843", {"start": v(6678.68, -5034.55) * mm, "end": v(6684.35, -5000.77) * mm});
            skLineSegment(sketch, "E1844", {"start": v(6684.35, -5000.77) * mm, "end": v(6688.29, -4961.4) * mm});
            skLineSegment(sketch, "E1845", {"start": v(6688.29, -4961.4) * mm, "end": v(6680.63, -4864.3) * mm});
            skLineSegment(sketch, "E1846", {"start": v(6680.63, -4864.3) * mm, "end": v(6671.7, -4767.81) * mm});
            skLineSegment(sketch, "E1847", {"start": v(6671.7, -4767.81) * mm, "end": v(6661.5, -4671.92) * mm});
            skLineSegment(sketch, "E1848", {"start": v(6661.5, -4671.92) * mm, "end": v(6650.04, -4576.6) * mm});
            skLineSegment(sketch, "E1849", {"start": v(6650.04, -4576.6) * mm, "end": v(6637.28, -4481.82) * mm});
            skLineSegment(sketch, "E1850", {"start": v(6637.28, -4481.82) * mm, "end": v(6623.24, -4387.55) * mm});
            skLineSegment(sketch, "E1851", {"start": v(6623.24, -4387.55) * mm, "end": v(6607.9, -4293.76) * mm});
            skLineSegment(sketch, "E1852", {"start": v(6607.9, -4293.76) * mm, "end": v(6591.26, -4200.44) * mm});
            skLineSegment(sketch, "E1853", {"start": v(6591.26, -4200.44) * mm, "end": v(6573.31, -4107.55) * mm});
            skLineSegment(sketch, "E1854", {"start": v(6573.31, -4107.55) * mm, "end": v(6554.05, -4015.07) * mm});
            skLineSegment(sketch, "E1855", {"start": v(6554.05, -4015.07) * mm, "end": v(6533.46, -3922.97) * mm});
            skLineSegment(sketch, "E1856", {"start": v(6533.46, -3922.97) * mm, "end": v(6511.55, -3831.22) * mm});
            skLineSegment(sketch, "E1857", {"start": v(6511.55, -3831.22) * mm, "end": v(6488.3, -3739.8) * mm});
            skLineSegment(sketch, "E1858", {"start": v(6488.3, -3739.8) * mm, "end": v(6463.7, -3648.7) * mm});
            skLineSegment(sketch, "E1859", {"start": v(6463.7, -3648.7) * mm, "end": v(6437.77, -3557.85) * mm});
            skLineSegment(sketch, "E1860", {"start": v(6437.77, -3557.85) * mm, "end": v(6410.48, -3467.26) * mm});
            skLineSegment(sketch, "E1861", {"start": v(6410.48, -3467.26) * mm, "end": v(6381.83, -3376.9) * mm});
            skLineSegment(sketch, "E1862", {"start": v(6381.83, -3376.9) * mm, "end": v(6351.8, -3286.73) * mm});
            skLineSegment(sketch, "E1863", {"start": v(6351.8, -3286.73) * mm, "end": v(6320.41, -3196.73) * mm});
            skLineSegment(sketch, "E1864", {"start": v(6320.41, -3196.73) * mm, "end": v(6287.64, -3106.88) * mm});
            skLineSegment(sketch, "E1865", {"start": v(6287.64, -3106.88) * mm, "end": v(6253.48, -3017.14) * mm});
            skLineSegment(sketch, "E1866", {"start": v(6253.48, -3017.14) * mm, "end": v(6217.93, -2927.5) * mm});
            skLineSegment(sketch, "E1867", {"start": v(6217.93, -2927.5) * mm, "end": v(6180.97, -2837.91) * mm});
            skLineSegment(sketch, "E1868", {"start": v(6180.97, -2837.91) * mm, "end": v(6142.61, -2748.37) * mm});
            skLineSegment(sketch, "E1869", {"start": v(-4653.56, -2748.37) * mm, "end": v(-4743.08, -2786.75) * mm});
            skLineSegment(sketch, "E1870", {"start": v(-4743.08, -2786.75) * mm, "end": v(-4832.64, -2823.73) * mm});
            skLineSegment(sketch, "E1871", {"start": v(-4832.64, -2823.73) * mm, "end": v(-4922.26, -2859.3) * mm});
            skLineSegment(sketch, "E1872", {"start": v(-4922.26, -2859.3) * mm, "end": v(-5011.98, -2893.48) * mm});
            skLineSegment(sketch, "E1873", {"start": v(-5011.98, -2893.48) * mm, "end": v(-5101.82, -2926.27) * mm});
            skLineSegment(sketch, "E1874", {"start": v(-5101.82, -2926.27) * mm, "end": v(-5191.8, -2957.67) * mm});
            skLineSegment(sketch, "E1875", {"start": v(-5191.8, -2957.67) * mm, "end": v(-5281.96, -2987.7) * mm});
            skLineSegment(sketch, "E1876", {"start": v(-5281.96, -2987.7) * mm, "end": v(-5372.32, -3016.37) * mm});
            skLineSegment(sketch, "E1877", {"start": v(-5372.32, -3016.37) * mm, "end": v(-5462.9, -3043.67) * mm});
            skLineSegment(sketch, "E1878", {"start": v(-5462.9, -3043.67) * mm, "end": v(-5553.73, -3069.62) * mm});
            skLineSegment(sketch, "E1879", {"start": v(-5553.73, -3069.62) * mm, "end": v(-5644.83, -3094.22) * mm});
            skLineSegment(sketch, "E1880", {"start": v(-5644.83, -3094.22) * mm, "end": v(-5736.24, -3117.47) * mm});
            skLineSegment(sketch, "E1881", {"start": v(-5736.24, -3117.47) * mm, "end": v(-5827.98, -3139.4) * mm});
            skLineSegment(sketch, "E1882", {"start": v(-5827.98, -3139.4) * mm, "end": v(-5920.08, -3159.98) * mm});
            skLineSegment(sketch, "E1883", {"start": v(-5920.08, -3159.98) * mm, "end": v(-6012.56, -3179.25) * mm});
            skLineSegment(sketch, "E1884", {"start": v(-6012.56, -3179.25) * mm, "end": v(-6105.44, -3197.2) * mm});
            skLineSegment(sketch, "E1885", {"start": v(-6105.44, -3197.2) * mm, "end": v(-6198.76, -3213.85) * mm});
            skLineSegment(sketch, "E1886", {"start": v(-6198.76, -3213.85) * mm, "end": v(-6292.54, -3229.19) * mm});
            skLineSegment(sketch, "E1887", {"start": v(-6292.54, -3229.19) * mm, "end": v(-6386.81, -3243.23) * mm});
            skLineSegment(sketch, "E1888", {"start": v(-6386.81, -3243.23) * mm, "end": v(-6481.6, -3255.99) * mm});
            skLineSegment(sketch, "E1889", {"start": v(-6481.6, -3255.99) * mm, "end": v(-6576.92, -3267.46) * mm});
            skLineSegment(sketch, "E1890", {"start": v(-6576.92, -3267.46) * mm, "end": v(-6672.81, -3277.65) * mm});
            skLineSegment(sketch, "E1891", {"start": v(-6672.81, -3277.65) * mm, "end": v(-6769.3, -3286.58) * mm});
            skLineSegment(sketch, "E1892", {"start": v(-6769.3, -3286.58) * mm, "end": v(-6866.4, -3294.24) * mm});
            skLineSegment(sketch, "E1893", {"start": v(-6866.4, -3294.24) * mm, "end": v(-6939.58, -3284.64) * mm});
            skLineSegment(sketch, "E1894", {"start": v(-6939.58, -3284.64) * mm, "end": v(-6991.43, -3268.4) * mm});
            skLineSegment(sketch, "E1895", {"start": v(-6991.43, -3268.4) * mm, "end": v(-7024.13, -3246.07) * mm});
            skLineSegment(sketch, "E1896", {"start": v(-7024.13, -3246.07) * mm, "end": v(-7039.82, -3218.19) * mm});
            skLineSegment(sketch, "E1897", {"start": v(-7039.82, -3218.19) * mm, "end": v(-7040.67, -3185.31) * mm});
            skLineSegment(sketch, "E1898", {"start": v(-7040.67, -3185.31) * mm, "end": v(-7028.84, -3147.98) * mm});
            skLineSegment(sketch, "E1899", {"start": v(-7028.84, -3147.98) * mm, "end": v(-7006.49, -3106.76) * mm});
            skLineSegment(sketch, "E1900", {"start": v(-7006.49, -3106.76) * mm, "end": v(-6975.78, -3062.18) * mm});
            skLineSegment(sketch, "E1901", {"start": v(-6975.78, -3062.18) * mm, "end": v(-6938.88, -3014.8) * mm});
            skLineSegment(sketch, "E1902", {"start": v(-6938.88, -3014.8) * mm, "end": v(-6897.94, -2965.17) * mm});
            skLineSegment(sketch, "E1903", {"start": v(-6897.94, -2965.17) * mm, "end": v(-6855.13, -2913.83) * mm});
            skLineSegment(sketch, "E1904", {"start": v(-6855.13, -2913.83) * mm, "end": v(-6812.61, -2861.33) * mm});
            skLineSegment(sketch, "E1905", {"start": v(-6812.61, -2861.33) * mm, "end": v(-6772.55, -2808.23) * mm});
            skLineSegment(sketch, "E1906", {"start": v(-6772.55, -2808.23) * mm, "end": v(-6737.09, -2755.06) * mm});
            skLineSegment(sketch, "E1907", {"start": v(-6737.09, -2755.06) * mm, "end": v(-6708.4, -2702.39) * mm});
            skLineSegment(sketch, "E1908", {"start": v(-6708.4, -2702.39) * mm, "end": v(-6688.66, -2650.75) * mm});
            skLineSegment(sketch, "E1909", {"start": v(-6688.66, -2650.75) * mm, "end": v(-6680, -2600.7) * mm});
            skLineSegment(sketch, "E1910", {"start": v(-6680, -2600.7) * mm, "end": v(-6684.94, -2543.53) * mm});
            skLineSegment(sketch, "E1911", {"start": v(-6684.94, -2543.53) * mm, "end": v(-6697.3, -2477.9) * mm});
            skLineSegment(sketch, "E1912", {"start": v(-6697.3, -2477.9) * mm, "end": v(-6713.33, -2418.69) * mm});
            skLineSegment(sketch, "E1913", {"start": v(-6713.33, -2418.69) * mm, "end": v(-6732.94, -2365.6) * mm});
            skLineSegment(sketch, "E1914", {"start": v(-6732.94, -2365.6) * mm, "end": v(-6756.06, -2318.3) * mm});
            skLineSegment(sketch, "E1915", {"start": v(-6756.06, -2318.3) * mm, "end": v(-6782.6, -2276.48) * mm});
            skLineSegment(sketch, "E1916", {"start": v(-6782.6, -2276.48) * mm, "end": v(-6812.49, -2239.82) * mm});
            skLineSegment(sketch, "E1917", {"start": v(-6812.49, -2239.82) * mm, "end": v(-6845.65, -2208) * mm});
            skLineSegment(sketch, "E1918", {"start": v(-6845.65, -2208) * mm, "end": v(-6882, -2180.7) * mm});
            skLineSegment(sketch, "E1919", {"start": v(-6882, -2180.7) * mm, "end": v(-6921.47, -2157.6) * mm});
            skLineSegment(sketch, "E1920", {"start": v(-6921.47, -2157.6) * mm, "end": v(-6963.97, -2138.38) * mm});
            skLineSegment(sketch, "E1921", {"start": v(-6963.97, -2138.38) * mm, "end": v(-7009.44, -2122.73) * mm});
            skLineSegment(sketch, "E1922", {"start": v(-7009.44, -2122.73) * mm, "end": v(-7057.78, -2110.32) * mm});
            skLineSegment(sketch, "E1923", {"start": v(-7057.78, -2110.32) * mm, "end": v(-7108.93, -2100.83) * mm});
            skLineSegment(sketch, "E1924", {"start": v(-7108.93, -2100.83) * mm, "end": v(-7162.8, -2093.95) * mm});
            skLineSegment(sketch, "E1925", {"start": v(-7162.8, -2093.95) * mm, "end": v(-7219.32, -2089.36) * mm});
            skLineSegment(sketch, "E1926", {"start": v(-7219.32, -2089.36) * mm, "end": v(-7278.4, -2086.73) * mm});
            skLineSegment(sketch, "E1927", {"start": v(-7278.4, -2086.73) * mm, "end": v(-7339.98, -2085.75) * mm});
            skLineSegment(sketch, "E1928", {"start": v(-7339.98, -2085.75) * mm, "end": v(-7402.43, -2086.16) * mm});
            skLineSegment(sketch, "E1929", {"start": v(-7402.43, -2086.16) * mm, "end": v(-7462.53, -2088.09) * mm});
            skLineSegment(sketch, "E1930", {"start": v(-7462.53, -2088.09) * mm, "end": v(-7520.08, -2091.86) * mm});
            skLineSegment(sketch, "E1931", {"start": v(-7520.08, -2091.86) * mm, "end": v(-7575.02, -2097.78) * mm});
            skLineSegment(sketch, "E1932", {"start": v(-7575.02, -2097.78) * mm, "end": v(-7627.26, -2106.19) * mm});
            skLineSegment(sketch, "E1933", {"start": v(-7627.26, -2106.19) * mm, "end": v(-7676.73, -2117.4) * mm});
            skLineSegment(sketch, "E1934", {"start": v(-7676.73, -2117.4) * mm, "end": v(-7723.35, -2131.71) * mm});
            skLineSegment(sketch, "E1935", {"start": v(-7723.35, -2131.71) * mm, "end": v(-7767.04, -2149.47) * mm});
            skLineSegment(sketch, "E1936", {"start": v(-7767.04, -2149.47) * mm, "end": v(-7807.72, -2170.98) * mm});
            skLineSegment(sketch, "E1937", {"start": v(-7807.72, -2170.98) * mm, "end": v(-7845.32, -2196.56) * mm});
            skLineSegment(sketch, "E1938", {"start": v(-7845.32, -2196.56) * mm, "end": v(-7879.75, -2226.53) * mm});
            skLineSegment(sketch, "E1939", {"start": v(-7879.75, -2226.53) * mm, "end": v(-7910.94, -2261.22) * mm});
            skLineSegment(sketch, "E1940", {"start": v(-7910.94, -2261.22) * mm, "end": v(-7938.8, -2300.93) * mm});
            skLineSegment(sketch, "E1941", {"start": v(-7938.8, -2300.93) * mm, "end": v(-7963.28, -2346) * mm});
            skLineSegment(sketch, "E1942", {"start": v(-7963.28, -2346) * mm, "end": v(-7984.27, -2396.73) * mm});
            skLineSegment(sketch, "E1943", {"start": v(-7984.27, -2396.73) * mm, "end": v(-8001.7, -2453.46) * mm});
            skLineSegment(sketch, "E1944", {"start": v(-8001.7, -2453.46) * mm, "end": v(-8015.5, -2516.48) * mm});
            skLineSegment(sketch, "E1945", {"start": v(-8015.5, -2516.48) * mm, "end": v(-8024.4, -2576.44) * mm});
            skLineSegment(sketch, "E1946", {"start": v(-8024.4, -2576.44) * mm, "end": v(-8024.9, -2600.7) * mm});
            skLineSegment(sketch, "E1947", {"start": v(-8024.9, -2600.7) * mm, "end": v(-8022.1, -2625.5) * mm});
            skLineSegment(sketch, "E1948", {"start": v(-8022.1, -2625.5) * mm, "end": v(-8016.26, -2650.75) * mm});
            skLineSegment(sketch, "E1949", {"start": v(-8016.26, -2650.75) * mm, "end": v(-8007.64, -2676.4) * mm});
            skLineSegment(sketch, "E1950", {"start": v(-8007.64, -2676.4) * mm, "end": v(-7996.52, -2702.39) * mm});
            skLineSegment(sketch, "E1951", {"start": v(-7996.52, -2702.39) * mm, "end": v(-7983.17, -2728.63) * mm});
            skLineSegment(sketch, "E1952", {"start": v(-7983.17, -2728.63) * mm, "end": v(-7967.85, -2755.06) * mm});
            skLineSegment(sketch, "E1953", {"start": v(-7967.85, -2755.06) * mm, "end": v(-7950.84, -2781.62) * mm});
            skLineSegment(sketch, "E1954", {"start": v(-7950.84, -2781.62) * mm, "end": v(-7932.4, -2808.23) * mm});
            skLineSegment(sketch, "E1955", {"start": v(-7932.4, -2808.23) * mm, "end": v(-7912.82, -2834.82) * mm});
            skLineSegment(sketch, "E1956", {"start": v(-7912.82, -2834.82) * mm, "end": v(-7892.35, -2861.33) * mm});
            skLineSegment(sketch, "E1957", {"start": v(-7892.35, -2861.33) * mm, "end": v(-7871.27, -2887.69) * mm});
            skLineSegment(sketch, "E1958", {"start": v(-7871.27, -2887.69) * mm, "end": v(-7849.85, -2913.83) * mm});
            skLineSegment(sketch, "E1959", {"start": v(-7849.85, -2913.83) * mm, "end": v(-7828.35, -2939.67) * mm});
            skLineSegment(sketch, "E1960", {"start": v(-7828.35, -2939.67) * mm, "end": v(-7807.05, -2965.17) * mm});
            skLineSegment(sketch, "E1961", {"start": v(-7807.05, -2965.17) * mm, "end": v(-7786.22, -2990.23) * mm});
            skLineSegment(sketch, "E1962", {"start": v(-7786.22, -2990.23) * mm, "end": v(-7766.13, -3014.8) * mm});
            skLineSegment(sketch, "E1963", {"start": v(-7766.13, -3014.8) * mm, "end": v(-7747.04, -3038.8) * mm});
            skLineSegment(sketch, "E1964", {"start": v(-7747.04, -3038.8) * mm, "end": v(-7729.24, -3062.18) * mm});
            skLineSegment(sketch, "E1965", {"start": v(-7729.24, -3062.18) * mm, "end": v(-7712.98, -3084.85) * mm});
            skLineSegment(sketch, "E1966", {"start": v(-7712.98, -3084.85) * mm, "end": v(-7698.54, -3106.76) * mm});
            skLineSegment(sketch, "E1967", {"start": v(-7698.54, -3106.76) * mm, "end": v(-7686.19, -3127.82) * mm});
            skLineSegment(sketch, "E1968", {"start": v(-7686.19, -3127.82) * mm, "end": v(-7676.2, -3147.98) * mm});
            skLineSegment(sketch, "E1969", {"start": v(-7676.2, -3147.98) * mm, "end": v(-7668.83, -3167.17) * mm});
            skLineSegment(sketch, "E1970", {"start": v(-7668.83, -3167.17) * mm, "end": v(-7664.36, -3185.31) * mm});
            skLineSegment(sketch, "E1971", {"start": v(-7664.36, -3185.31) * mm, "end": v(-7663.06, -3202.34) * mm});
            skLineSegment(sketch, "E1972", {"start": v(-7663.06, -3202.34) * mm, "end": v(-7665.2, -3218.19) * mm});
            skLineSegment(sketch, "E1973", {"start": v(-7665.2, -3218.19) * mm, "end": v(-7671.05, -3232.79) * mm});
            skLineSegment(sketch, "E1974", {"start": v(-7671.05, -3232.79) * mm, "end": v(-7680.88, -3246.07) * mm});
            skLineSegment(sketch, "E1975", {"start": v(-7680.88, -3246.07) * mm, "end": v(-7694.95, -3257.96) * mm});
            skLineSegment(sketch, "E1976", {"start": v(-7694.95, -3257.96) * mm, "end": v(-7713.55, -3268.4) * mm});
            skLineSegment(sketch, "E1977", {"start": v(-7713.55, -3268.4) * mm, "end": v(-7736.93, -3277.32) * mm});
            skLineSegment(sketch, "E1978", {"start": v(-7736.93, -3277.32) * mm, "end": v(-7765.38, -3284.64) * mm});
            skLineSegment(sketch, "E1979", {"start": v(-7765.38, -3284.64) * mm, "end": v(-7799.15, -3290.3) * mm});
            skLineSegment(sketch, "E1980", {"start": v(-7799.15, -3290.3) * mm, "end": v(-7838.52, -3294.24) * mm});
            skLineSegment(sketch, "E1981", {"start": v(-7838.52, -3294.24) * mm, "end": v(-7935.63, -3286.58) * mm});
            skLineSegment(sketch, "E1982", {"start": v(-7935.63, -3286.58) * mm, "end": v(-8032.12, -3277.65) * mm});
            skLineSegment(sketch, "E1983", {"start": v(-8032.12, -3277.65) * mm, "end": v(-8128.01, -3267.46) * mm});
            skLineSegment(sketch, "E1984", {"start": v(-8128.01, -3267.46) * mm, "end": v(-8223.34, -3255.99) * mm});
            skLineSegment(sketch, "E1985", {"start": v(-8223.34, -3255.99) * mm, "end": v(-8318.13, -3243.23) * mm});
            skLineSegment(sketch, "E1986", {"start": v(-8318.13, -3243.23) * mm, "end": v(-8412.4, -3229.19) * mm});
            skLineSegment(sketch, "E1987", {"start": v(-8412.4, -3229.19) * mm, "end": v(-8506.18, -3213.85) * mm});
            skLineSegment(sketch, "E1988", {"start": v(-8506.18, -3213.85) * mm, "end": v(-8599.5, -3197.2) * mm});
            skLineSegment(sketch, "E1989", {"start": v(-8599.5, -3197.2) * mm, "end": v(-8692.4, -3179.25) * mm});
            skLineSegment(sketch, "E1990", {"start": v(-8692.4, -3179.25) * mm, "end": v(-8784.88, -3159.98) * mm});
            skLineSegment(sketch, "E1991", {"start": v(-8784.88, -3159.98) * mm, "end": v(-8876.98, -3139.4) * mm});
            skLineSegment(sketch, "E1992", {"start": v(-8876.98, -3139.4) * mm, "end": v(-8968.72, -3117.47) * mm});
            skLineSegment(sketch, "E1993", {"start": v(-8968.72, -3117.47) * mm, "end": v(-9060.13, -3094.22) * mm});
            skLineSegment(sketch, "E1994", {"start": v(-9060.13, -3094.22) * mm, "end": v(-9151.25, -3069.62) * mm});
            skLineSegment(sketch, "E1995", {"start": v(-9151.25, -3069.62) * mm, "end": v(-9242.08, -3043.67) * mm});
            skLineSegment(sketch, "E1996", {"start": v(-9242.08, -3043.67) * mm, "end": v(-9332.67, -3016.37) * mm});
            skLineSegment(sketch, "E1997", {"start": v(-9332.67, -3016.37) * mm, "end": v(-9423.03, -2987.7) * mm});
            skLineSegment(sketch, "E1998", {"start": v(-9423.03, -2987.7) * mm, "end": v(-9513.2, -2957.67) * mm});
            skLineSegment(sketch, "E1999", {"start": v(-9513.2, -2957.67) * mm, "end": v(-9603.2, -2926.27) * mm});
            skLineSegment(sketch, "E2000", {"start": v(-9603.2, -2926.27) * mm, "end": v(-9693.05, -2893.48) * mm});
            skLineSegment(sketch, "E2001", {"start": v(-9693.05, -2893.48) * mm, "end": v(-9782.78, -2859.3) * mm});
            skLineSegment(sketch, "E2002", {"start": v(-9782.78, -2859.3) * mm, "end": v(-9872.43, -2823.73) * mm});
            skLineSegment(sketch, "E2003", {"start": v(-9872.43, -2823.73) * mm, "end": v(-9962, -2786.75) * mm});
            skLineSegment(sketch, "E2004", {"start": v(-9962, -2786.75) * mm, "end": v(-10051.55, -2748.37) * mm});
            skLineSegment(sketch, "E2005", {"start": v(-10051.55, -8146.62) * mm, "end": v(-9962, -8108.23) * mm});
            skLineSegment(sketch, "E2006", {"start": v(-9962, -8108.23) * mm, "end": v(-9872.43, -8071.26) * mm});
            skLineSegment(sketch, "E2007", {"start": v(-9872.43, -8071.26) * mm, "end": v(-9782.78, -8035.69) * mm});
            skLineSegment(sketch, "E2008", {"start": v(-9782.78, -8035.69) * mm, "end": v(-9693.05, -8001.5) * mm});
            skLineSegment(sketch, "E2009", {"start": v(-9693.05, -8001.5) * mm, "end": v(-9603.2, -7968.72) * mm});
            skLineSegment(sketch, "E2010", {"start": v(-9603.2, -7968.72) * mm, "end": v(-9513.2, -7937.31) * mm});
            skLineSegment(sketch, "E2011", {"start": v(-9513.2, -7937.31) * mm, "end": v(-9423.03, -7907.28) * mm});
            skLineSegment(sketch, "E2012", {"start": v(-9423.03, -7907.28) * mm, "end": v(-9332.67, -7878.62) * mm});
            skLineSegment(sketch, "E2013", {"start": v(-9332.67, -7878.62) * mm, "end": v(-9242.08, -7851.31) * mm});
            skLineSegment(sketch, "E2014", {"start": v(-9242.08, -7851.31) * mm, "end": v(-9151.25, -7825.37) * mm});
            skLineSegment(sketch, "E2015", {"start": v(-9151.25, -7825.37) * mm, "end": v(-9060.13, -7800.77) * mm});
            skLineSegment(sketch, "E2016", {"start": v(-9060.13, -7800.77) * mm, "end": v(-8968.72, -7777.51) * mm});
            skLineSegment(sketch, "E2017", {"start": v(-8968.72, -7777.51) * mm, "end": v(-8876.98, -7755.6) * mm});
            skLineSegment(sketch, "E2018", {"start": v(-8876.98, -7755.6) * mm, "end": v(-8784.88, -7735) * mm});
            skLineSegment(sketch, "E2019", {"start": v(-8784.88, -7735) * mm, "end": v(-8692.4, -7715.73) * mm});
            skLineSegment(sketch, "E2020", {"start": v(-8692.4, -7715.73) * mm, "end": v(-8599.5, -7697.78) * mm});
            skLineSegment(sketch, "E2021", {"start": v(-8599.5, -7697.78) * mm, "end": v(-8506.18, -7681.14) * mm});
            skLineSegment(sketch, "E2022", {"start": v(-8506.18, -7681.14) * mm, "end": v(-8412.4, -7665.8) * mm});
            skLineSegment(sketch, "E2023", {"start": v(-8412.4, -7665.8) * mm, "end": v(-8318.13, -7651.75) * mm});
            skLineSegment(sketch, "E2024", {"start": v(-8318.13, -7651.75) * mm, "end": v(-8223.34, -7639) * mm});
            skLineSegment(sketch, "E2025", {"start": v(-8223.34, -7639) * mm, "end": v(-8128.01, -7627.53) * mm});
            skLineSegment(sketch, "E2026", {"start": v(-8128.01, -7627.53) * mm, "end": v(-8032.12, -7617.33) * mm});
            skLineSegment(sketch, "E2027", {"start": v(-8032.12, -7617.33) * mm, "end": v(-7935.63, -7608.4) * mm});
            skLineSegment(sketch, "E2028", {"start": v(-7935.63, -7608.4) * mm, "end": v(-7838.52, -7600.75) * mm});
            skLineSegment(sketch, "E2029", {"start": v(-7838.52, -7600.75) * mm, "end": v(-7765.38, -7610.34) * mm});
            skLineSegment(sketch, "E2030", {"start": v(-7765.38, -7610.34) * mm, "end": v(-7713.55, -7626.58) * mm});
            skLineSegment(sketch, "E2031", {"start": v(-7713.55, -7626.58) * mm, "end": v(-7680.88, -7648.92) * mm});
            skLineSegment(sketch, "E2032", {"start": v(-7680.88, -7648.92) * mm, "end": v(-7665.2, -7676.8) * mm});
            skLineSegment(sketch, "E2033", {"start": v(-7665.2, -7676.8) * mm, "end": v(-7664.36, -7709.68) * mm});
            skLineSegment(sketch, "E2034", {"start": v(-7664.36, -7709.68) * mm, "end": v(-7676.2, -7747) * mm});
            skLineSegment(sketch, "E2035", {"start": v(-7676.2, -7747) * mm, "end": v(-7698.54, -7788.23) * mm});
            skLineSegment(sketch, "E2036", {"start": v(-7698.54, -7788.23) * mm, "end": v(-7729.24, -7832.8) * mm});
            skLineSegment(sketch, "E2037", {"start": v(-7729.24, -7832.8) * mm, "end": v(-7766.13, -7880.19) * mm});
            skLineSegment(sketch, "E2038", {"start": v(-7766.13, -7880.19) * mm, "end": v(-7807.05, -7929.82) * mm});
            skLineSegment(sketch, "E2039", {"start": v(-7807.05, -7929.82) * mm, "end": v(-7849.85, -7981.16) * mm});
            skLineSegment(sketch, "E2040", {"start": v(-7849.85, -7981.16) * mm, "end": v(-7892.35, -8033.66) * mm});
            skLineSegment(sketch, "E2041", {"start": v(-7892.35, -8033.66) * mm, "end": v(-7932.4, -8086.76) * mm});
            skLineSegment(sketch, "E2042", {"start": v(-7932.4, -8086.76) * mm, "end": v(-7967.85, -8139.92) * mm});
            skLineSegment(sketch, "E2043", {"start": v(-7967.85, -8139.92) * mm, "end": v(-7996.52, -8192.6) * mm});
            skLineSegment(sketch, "E2044", {"start": v(-7996.52, -8192.6) * mm, "end": v(-8016.26, -8244.24) * mm});
            skLineSegment(sketch, "E2045", {"start": v(-8016.26, -8244.24) * mm, "end": v(-8024.9, -8294.29) * mm});
            skLineSegment(sketch, "E2046", {"start": v(-8024.9, -8294.29) * mm, "end": v(-8019.98, -8351.46) * mm});
            skLineSegment(sketch, "E2047", {"start": v(-8019.98, -8351.46) * mm, "end": v(-8007.62, -8417.1) * mm});
            skLineSegment(sketch, "E2048", {"start": v(-8007.62, -8417.1) * mm, "end": v(-7991.61, -8476.3) * mm});
            skLineSegment(sketch, "E2049", {"start": v(-7991.61, -8476.3) * mm, "end": v(-7972.02, -8529.4) * mm});
            skLineSegment(sketch, "E2050", {"start": v(-7972.02, -8529.4) * mm, "end": v(-7948.93, -8576.69) * mm});
            skLineSegment(sketch, "E2051", {"start": v(-7948.93, -8576.69) * mm, "end": v(-7922.4, -8618.5) * mm});
            skLineSegment(sketch, "E2052", {"start": v(-7922.4, -8618.5) * mm, "end": v(-7892.53, -8655.16) * mm});
            skLineSegment(sketch, "E2053", {"start": v(-7892.53, -8655.16) * mm, "end": v(-7859.4, -8686.98) * mm});
            skLineSegment(sketch, "E2054", {"start": v(-7859.4, -8686.98) * mm, "end": v(-7823.06, -8714.28) * mm});
            skLineSegment(sketch, "E2055", {"start": v(-7823.06, -8714.28) * mm, "end": v(-7783.61, -8737.38) * mm});
            skLineSegment(sketch, "E2056", {"start": v(-7783.61, -8737.38) * mm, "end": v(-7741.12, -8756.6) * mm});
            skLineSegment(sketch, "E2057", {"start": v(-7741.12, -8756.6) * mm, "end": v(-7695.68, -8772.26) * mm});
            skLineSegment(sketch, "E2058", {"start": v(-7695.68, -8772.26) * mm, "end": v(-7647.35, -8784.67) * mm});
            skLineSegment(sketch, "E2059", {"start": v(-7647.35, -8784.67) * mm, "end": v(-7596.22, -8794.16) * mm});
            skLineSegment(sketch, "E2060", {"start": v(-7596.22, -8794.16) * mm, "end": v(-7542.36, -8801.04) * mm});
            skLineSegment(sketch, "E2061", {"start": v(-7542.36, -8801.04) * mm, "end": v(-7485.85, -8805.63) * mm});
            skLineSegment(sketch, "E2062", {"start": v(-7485.85, -8805.63) * mm, "end": v(-7426.77, -8808.26) * mm});
            skLineSegment(sketch, "E2063", {"start": v(-7426.77, -8808.26) * mm, "end": v(-7365.2, -8809.24) * mm});
            skLineSegment(sketch, "E2064", {"start": v(-7365.2, -8809.24) * mm, "end": v(-7302.74, -8808.83) * mm});
            skLineSegment(sketch, "E2065", {"start": v(-7302.74, -8808.83) * mm, "end": v(-7242.65, -8806.9) * mm});
            skLineSegment(sketch, "E2066", {"start": v(-7242.65, -8806.9) * mm, "end": v(-7185.1, -8803.13) * mm});
            skLineSegment(sketch, "E2067", {"start": v(-7185.1, -8803.13) * mm, "end": v(-7130.15, -8797.2) * mm});
            skLineSegment(sketch, "E2068", {"start": v(-7130.15, -8797.2) * mm, "end": v(-7077.9, -8788.8) * mm});
            skLineSegment(sketch, "E2069", {"start": v(-7077.9, -8788.8) * mm, "end": v(-7028.43, -8777.6) * mm});
            skLineSegment(sketch, "E2070", {"start": v(-7028.43, -8777.6) * mm, "end": v(-6981.8, -8763.27) * mm});
            skLineSegment(sketch, "E2071", {"start": v(-6981.8, -8763.27) * mm, "end": v(-6938.1, -8745.52) * mm});
            skLineSegment(sketch, "E2072", {"start": v(-6938.1, -8745.52) * mm, "end": v(-6897.42, -8724.01) * mm});
            skLineSegment(sketch, "E2073", {"start": v(-6897.42, -8724.01) * mm, "end": v(-6859.8, -8698.43) * mm});
            skLineSegment(sketch, "E2074", {"start": v(-6859.8, -8698.43) * mm, "end": v(-6825.36, -8668.45) * mm});
            skLineSegment(sketch, "E2075", {"start": v(-6825.36, -8668.45) * mm, "end": v(-6794.15, -8633.77) * mm});
            skLineSegment(sketch, "E2076", {"start": v(-6794.15, -8633.77) * mm, "end": v(-6766.27, -8594.05) * mm});
            skLineSegment(sketch, "E2077", {"start": v(-6766.27, -8594.05) * mm, "end": v(-6741.77, -8548.99) * mm});
            skLineSegment(sketch, "E2078", {"start": v(-6741.77, -8548.99) * mm, "end": v(-6720.75, -8498.25) * mm});
            skLineSegment(sketch, "E2079", {"start": v(-6720.75, -8498.25) * mm, "end": v(-6703.28, -8441.53) * mm});
            skLineSegment(sketch, "E2080", {"start": v(-6703.28, -8441.53) * mm, "end": v(-6689.44, -8378.5) * mm});
            skLineSegment(sketch, "E2081", {"start": v(-6689.44, -8378.5) * mm, "end": v(-6680.52, -8318.54) * mm});
            skLineSegment(sketch, "E2082", {"start": v(-6680.52, -8318.54) * mm, "end": v(-6680, -8294.27) * mm});
            skLineSegment(sketch, "E2083", {"start": v(-6680, -8294.27) * mm, "end": v(-6682.8, -8269.46) * mm});
            skLineSegment(sketch, "E2084", {"start": v(-6682.8, -8269.46) * mm, "end": v(-6688.66, -8244.2) * mm});
            skLineSegment(sketch, "E2085", {"start": v(-6688.66, -8244.2) * mm, "end": v(-6697.28, -8218.53) * mm});
            skLineSegment(sketch, "E2086", {"start": v(-6697.28, -8218.53) * mm, "end": v(-6708.4, -8192.54) * mm});
            skLineSegment(sketch, "E2087", {"start": v(-6708.4, -8192.54) * mm, "end": v(-6721.77, -8166.29) * mm});
            skLineSegment(sketch, "E2088", {"start": v(-6721.77, -8166.29) * mm, "end": v(-6737.09, -8139.85) * mm});
            skLineSegment(sketch, "E2089", {"start": v(-6737.09, -8139.85) * mm, "end": v(-6754.1, -8113.29) * mm});
            skLineSegment(sketch, "E2090", {"start": v(-6754.1, -8113.29) * mm, "end": v(-6772.55, -8086.68) * mm});
            skLineSegment(sketch, "E2091", {"start": v(-6772.55, -8086.68) * mm, "end": v(-6792.14, -8060.08) * mm});
            skLineSegment(sketch, "E2092", {"start": v(-6792.14, -8060.08) * mm, "end": v(-6812.61, -8033.57) * mm});
            skLineSegment(sketch, "E2093", {"start": v(-6812.61, -8033.57) * mm, "end": v(-6833.7, -8007.21) * mm});
            skLineSegment(sketch, "E2094", {"start": v(-6833.7, -8007.21) * mm, "end": v(-6855.13, -7981.08) * mm});
            skLineSegment(sketch, "E2095", {"start": v(-6855.13, -7981.08) * mm, "end": v(-6876.64, -7955.23) * mm});
            skLineSegment(sketch, "E2096", {"start": v(-6876.64, -7955.23) * mm, "end": v(-6897.94, -7929.74) * mm});
            skLineSegment(sketch, "E2097", {"start": v(-6897.94, -7929.74) * mm, "end": v(-6918.78, -7904.68) * mm});
            skLineSegment(sketch, "E2098", {"start": v(-6918.78, -7904.68) * mm, "end": v(-6938.88, -7880.11) * mm});
            skLineSegment(sketch, "E2099", {"start": v(-6938.88, -7880.11) * mm, "end": v(-6957.97, -7856.11) * mm});
            skLineSegment(sketch, "E2100", {"start": v(-6957.97, -7856.11) * mm, "end": v(-6975.78, -7832.74) * mm});
            skLineSegment(sketch, "E2101", {"start": v(-6975.78, -7832.74) * mm, "end": v(-6992.04, -7810.07) * mm});
            skLineSegment(sketch, "E2102", {"start": v(-6992.04, -7810.07) * mm, "end": v(-7006.49, -7788.17) * mm});
            skLineSegment(sketch, "E2103", {"start": v(-7006.49, -7788.17) * mm, "end": v(-7018.84, -7767.11) * mm});
            skLineSegment(sketch, "E2104", {"start": v(-7018.84, -7767.11) * mm, "end": v(-7028.84, -7746.96) * mm});
            skLineSegment(sketch, "E2105", {"start": v(-7028.84, -7746.96) * mm, "end": v(-7036.2, -7727.78) * mm});
            skLineSegment(sketch, "E2106", {"start": v(-7036.2, -7727.78) * mm, "end": v(-7040.67, -7709.64) * mm});
            skLineSegment(sketch, "E2107", {"start": v(-7040.67, -7709.64) * mm, "end": v(-7041.96, -7692.62) * mm});
            skLineSegment(sketch, "E2108", {"start": v(-7041.96, -7692.62) * mm, "end": v(-7039.82, -7676.78) * mm});
            skLineSegment(sketch, "E2109", {"start": v(-7039.82, -7676.78) * mm, "end": v(-7033.96, -7662.18) * mm});
            skLineSegment(sketch, "E2110", {"start": v(-7033.96, -7662.18) * mm, "end": v(-7024.13, -7648.9) * mm});
            skLineSegment(sketch, "E2111", {"start": v(-7024.13, -7648.9) * mm, "end": v(-7010.04, -7637.01) * mm});
            skLineSegment(sketch, "E2112", {"start": v(-7010.04, -7637.01) * mm, "end": v(-6991.43, -7626.58) * mm});
            skLineSegment(sketch, "E2113", {"start": v(-6991.43, -7626.58) * mm, "end": v(-6968.04, -7617.66) * mm});
            skLineSegment(sketch, "E2114", {"start": v(-6968.04, -7617.66) * mm, "end": v(-6939.58, -7610.34) * mm});
            skLineSegment(sketch, "E2115", {"start": v(-6939.58, -7610.34) * mm, "end": v(-6905.79, -7604.68) * mm});
            skLineSegment(sketch, "E2116", {"start": v(-6905.79, -7604.68) * mm, "end": v(-6866.4, -7600.75) * mm});
            skLineSegment(sketch, "E2117", {"start": v(-6866.4, -7600.75) * mm, "end": v(-6769.3, -7608.4) * mm});
            skLineSegment(sketch, "E2118", {"start": v(-6769.3, -7608.4) * mm, "end": v(-6672.81, -7617.33) * mm});
            skLineSegment(sketch, "E2119", {"start": v(-6672.81, -7617.33) * mm, "end": v(-6576.92, -7627.53) * mm});
            skLineSegment(sketch, "E2120", {"start": v(-6576.92, -7627.53) * mm, "end": v(-6481.6, -7639) * mm});
            skLineSegment(sketch, "E2121", {"start": v(-6481.6, -7639) * mm, "end": v(-6386.81, -7651.75) * mm});
            skLineSegment(sketch, "E2122", {"start": v(-6386.81, -7651.75) * mm, "end": v(-6292.54, -7665.8) * mm});
            skLineSegment(sketch, "E2123", {"start": v(-6292.54, -7665.8) * mm, "end": v(-6198.76, -7681.14) * mm});
            skLineSegment(sketch, "E2124", {"start": v(-6198.76, -7681.14) * mm, "end": v(-6105.44, -7697.78) * mm});
            skLineSegment(sketch, "E2125", {"start": v(-6105.44, -7697.78) * mm, "end": v(-6012.56, -7715.73) * mm});
            skLineSegment(sketch, "E2126", {"start": v(-6012.56, -7715.73) * mm, "end": v(-5920.08, -7735) * mm});
            skLineSegment(sketch, "E2127", {"start": v(-5920.08, -7735) * mm, "end": v(-5827.98, -7755.6) * mm});
            skLineSegment(sketch, "E2128", {"start": v(-5827.98, -7755.6) * mm, "end": v(-5736.24, -7777.51) * mm});
            skLineSegment(sketch, "E2129", {"start": v(-5736.24, -7777.51) * mm, "end": v(-5644.83, -7800.77) * mm});
            skLineSegment(sketch, "E2130", {"start": v(-5644.83, -7800.77) * mm, "end": v(-5553.73, -7825.37) * mm});
            skLineSegment(sketch, "E2131", {"start": v(-5553.73, -7825.37) * mm, "end": v(-5462.9, -7851.31) * mm});
            skLineSegment(sketch, "E2132", {"start": v(-5462.9, -7851.31) * mm, "end": v(-5372.32, -7878.62) * mm});
            skLineSegment(sketch, "E2133", {"start": v(-5372.32, -7878.62) * mm, "end": v(-5281.96, -7907.28) * mm});
            skLineSegment(sketch, "E2134", {"start": v(-5281.96, -7907.28) * mm, "end": v(-5191.8, -7937.31) * mm});
            skLineSegment(sketch, "E2135", {"start": v(-5191.8, -7937.31) * mm, "end": v(-5101.82, -7968.72) * mm});
            skLineSegment(sketch, "E2136", {"start": v(-5101.82, -7968.72) * mm, "end": v(-5011.98, -8001.5) * mm});
            skLineSegment(sketch, "E2137", {"start": v(-5011.98, -8001.5) * mm, "end": v(-4922.26, -8035.69) * mm});
            skLineSegment(sketch, "E2138", {"start": v(-4922.26, -8035.69) * mm, "end": v(-4832.64, -8071.26) * mm});
            skLineSegment(sketch, "E2139", {"start": v(-4832.64, -8071.26) * mm, "end": v(-4743.08, -8108.23) * mm});
            skLineSegment(sketch, "E2140", {"start": v(-4743.08, -8108.23) * mm, "end": v(-4653.56, -8146.62) * mm});
            skLineSegment(sketch, "E2141", {"start": v(-4653.56, -8146.62) * mm, "end": v(-4615.18, -8057.07) * mm});
            skLineSegment(sketch, "E2142", {"start": v(-4615.18, -8057.07) * mm, "end": v(-4578.2, -7967.5) * mm});
            skLineSegment(sketch, "E2143", {"start": v(-4578.2, -7967.5) * mm, "end": v(-4542.63, -7877.85) * mm});
            skLineSegment(sketch, "E2144", {"start": v(-4542.63, -7877.85) * mm, "end": v(-4508.45, -7788.11) * mm});
            skLineSegment(sketch, "E2145", {"start": v(-4508.45, -7788.11) * mm, "end": v(-4475.66, -7698.26) * mm});
            skLineSegment(sketch, "E2146", {"start": v(-4475.66, -7698.26) * mm, "end": v(-4444.25, -7608.26) * mm});
            skLineSegment(sketch, "E2147", {"start": v(-4444.25, -7608.26) * mm, "end": v(-4414.22, -7518.09) * mm});
            skLineSegment(sketch, "E2148", {"start": v(-4414.22, -7518.09) * mm, "end": v(-4385.56, -7427.72) * mm});
            skLineSegment(sketch, "E2149", {"start": v(-4385.56, -7427.72) * mm, "end": v(-4358.26, -7337.13) * mm});
            skLineSegment(sketch, "E2150", {"start": v(-4358.26, -7337.13) * mm, "end": v(-4332.31, -7246.3) * mm});
            skLineSegment(sketch, "E2151", {"start": v(-4332.31, -7246.3) * mm, "end": v(-4307.72, -7155.18) * mm});
            skLineSegment(sketch, "E2152", {"start": v(-4307.72, -7155.18) * mm, "end": v(-4284.46, -7063.76) * mm});
            skLineSegment(sketch, "E2153", {"start": v(-4284.46, -7063.76) * mm, "end": v(-4262.55, -6972.02) * mm});
            skLineSegment(sketch, "E2154", {"start": v(-4262.55, -6972.02) * mm, "end": v(-4241.96, -6879.92) * mm});
            skLineSegment(sketch, "E2155", {"start": v(-4241.96, -6879.92) * mm, "end": v(-4222.7, -6787.44) * mm});
            skLineSegment(sketch, "E2156", {"start": v(-4222.7, -6787.44) * mm, "end": v(-4204.74, -6694.55) * mm});
            skLineSegment(sketch, "E2157", {"start": v(-4204.74, -6694.55) * mm, "end": v(-4188.1, -6601.22) * mm});
            skLineSegment(sketch, "E2158", {"start": v(-4188.1, -6601.22) * mm, "end": v(-4172.77, -6507.44) * mm});
            skLineSegment(sketch, "E2159", {"start": v(-4172.77, -6507.44) * mm, "end": v(-4158.73, -6413.17) * mm});
            skLineSegment(sketch, "E2160", {"start": v(-4158.73, -6413.17) * mm, "end": v(-4145.98, -6318.39) * mm});
            skLineSegment(sketch, "E2161", {"start": v(-4145.98, -6318.39) * mm, "end": v(-4134.51, -6223.06) * mm});
            skLineSegment(sketch, "E2162", {"start": v(-4134.51, -6223.06) * mm, "end": v(-4124.33, -6127.17) * mm});
            skLineSegment(sketch, "E2163", {"start": v(-4124.33, -6127.17) * mm, "end": v(-4115.4, -6030.7) * mm});
            skLineSegment(sketch, "E2164", {"start": v(-4115.4, -6030.7) * mm, "end": v(-4107.75, -5933.59) * mm});
            skLineSegment(sketch, "E2165", {"start": v(-4107.75, -5933.59) * mm, "end": v(-4117.35, -5860.4) * mm});
            skLineSegment(sketch, "E2166", {"start": v(-4117.35, -5860.4) * mm, "end": v(-4133.59, -5808.55) * mm});
            skLineSegment(sketch, "E2167", {"start": v(-4133.59, -5808.55) * mm, "end": v(-4155.92, -5775.85) * mm});
            skLineSegment(sketch, "E2168", {"start": v(-4155.92, -5775.85) * mm, "end": v(-4183.8, -5760.16) * mm});
            skLineSegment(sketch, "E2169", {"start": v(-4183.8, -5760.16) * mm, "end": v(-4216.67, -5759.31) * mm});
            skLineSegment(sketch, "E2170", {"start": v(-4216.67, -5759.31) * mm, "end": v(-4254, -5771.14) * mm});
            skLineSegment(sketch, "E2171", {"start": v(-4254, -5771.14) * mm, "end": v(-4295.21, -5793.5) * mm});
            skLineSegment(sketch, "E2172", {"start": v(-4295.21, -5793.5) * mm, "end": v(-4339.79, -5824.2) * mm});
            skLineSegment(sketch, "E2173", {"start": v(-4339.79, -5824.2) * mm, "end": v(-4387.16, -5861.1) * mm});
            skLineSegment(sketch, "E2174", {"start": v(-4387.16, -5861.1) * mm, "end": v(-4436.79, -5902.03) * mm});
            skLineSegment(sketch, "E2175", {"start": v(-4436.79, -5902.03) * mm, "end": v(-4488.12, -5944.83) * mm});
            skLineSegment(sketch, "E2176", {"start": v(-4488.12, -5944.83) * mm, "end": v(-4540.61, -5987.35) * mm});
            skLineSegment(sketch, "E2177", {"start": v(-4540.61, -5987.35) * mm, "end": v(-4593.71, -6027.41) * mm});
            skLineSegment(sketch, "E2178", {"start": v(-4593.71, -6027.41) * mm, "end": v(-4646.87, -6062.86) * mm});
            skLineSegment(sketch, "E2179", {"start": v(-4646.87, -6062.86) * mm, "end": v(-4699.54, -6091.54) * mm});
            skLineSegment(sketch, "E2180", {"start": v(-4699.54, -6091.54) * mm, "end": v(-4751.18, -6111.28) * mm});
            skLineSegment(sketch, "E2181", {"start": v(-4751.18, -6111.28) * mm, "end": v(-4801.23, -6119.92) * mm});
            skLineSegment(sketch, "E2182", {"start": v(-4801.23, -6119.92) * mm, "end": v(-4858.4, -6114.98) * mm});
            skLineSegment(sketch, "E2183", {"start": v(-4858.4, -6114.98) * mm, "end": v(-4924.04, -6102.62) * mm});
            skLineSegment(sketch, "E2184", {"start": v(-4924.04, -6102.62) * mm, "end": v(-4983.25, -6086.6) * mm});
            skLineSegment(sketch, "E2185", {"start": v(-4983.25, -6086.6) * mm, "end": v(-5036.34, -6067) * mm});
            skLineSegment(sketch, "E2186", {"start": v(-5036.34, -6067) * mm, "end": v(-5083.64, -6043.9) * mm});
            skLineSegment(sketch, "E2187", {"start": v(-5083.64, -6043.9) * mm, "end": v(-5125.46, -6017.36) * mm});
            skLineSegment(sketch, "E2188", {"start": v(-5125.46, -6017.36) * mm, "end": v(-5162.12, -5987.48) * mm});
            skLineSegment(sketch, "E2189", {"start": v(-5162.12, -5987.48) * mm, "end": v(-5193.95, -5954.32) * mm});
            skLineSegment(sketch, "E2190", {"start": v(-5193.95, -5954.32) * mm, "end": v(-5221.26, -5917.97) * mm});
            skLineSegment(sketch, "E2191", {"start": v(-5221.26, -5917.97) * mm, "end": v(-5244.36, -5878.5) * mm});
            skLineSegment(sketch, "E2192", {"start": v(-5244.36, -5878.5) * mm, "end": v(-5263.59, -5836) * mm});
            skLineSegment(sketch, "E2193", {"start": v(-5263.59, -5836) * mm, "end": v(-5279.25, -5790.54) * mm});
            skLineSegment(sketch, "E2194", {"start": v(-5279.25, -5790.54) * mm, "end": v(-5291.66, -5742.2) * mm});
            skLineSegment(sketch, "E2195", {"start": v(-5291.66, -5742.2) * mm, "end": v(-5301.15, -5691.06) * mm});
            skLineSegment(sketch, "E2196", {"start": v(-5301.15, -5691.06) * mm, "end": v(-5308.04, -5637.18) * mm});
            skLineSegment(sketch, "E2197", {"start": v(-5308.04, -5637.18) * mm, "end": v(-5312.63, -5580.67) * mm});
            skLineSegment(sketch, "E2198", {"start": v(-5312.63, -5580.67) * mm, "end": v(-5315.26, -5521.58) * mm});
            skLineSegment(sketch, "E2199", {"start": v(-5315.26, -5521.58) * mm, "end": v(-5316.24, -5460) * mm});
            skLineSegment(sketch, "E2200", {"start": v(-5316.24, -5460) * mm, "end": v(-5315.83, -5397.55) * mm});
            skLineSegment(sketch, "E2201", {"start": v(-5315.83, -5397.55) * mm, "end": v(-5313.9, -5337.46) * mm});
            skLineSegment(sketch, "E2202", {"start": v(-5313.9, -5337.46) * mm, "end": v(-5310.13, -5279.92) * mm});
            skLineSegment(sketch, "E2203", {"start": v(-5310.13, -5279.92) * mm, "end": v(-5304.2, -5224.99) * mm});
            skLineSegment(sketch, "E2204", {"start": v(-5304.2, -5224.99) * mm, "end": v(-5295.8, -5172.75) * mm});
            skLineSegment(sketch, "E2205", {"start": v(-5295.8, -5172.75) * mm, "end": v(-5284.58, -5123.3) * mm});
            skLineSegment(sketch, "E2206", {"start": v(-5284.58, -5123.3) * mm, "end": v(-5270.26, -5076.69) * mm});
            skLineSegment(sketch, "E2207", {"start": v(-5270.26, -5076.69) * mm, "end": v(-5252.5, -5033) * mm});
            skLineSegment(sketch, "E2208", {"start": v(-5252.5, -5033) * mm, "end": v(-5230.99, -4992.33) * mm});
            skLineSegment(sketch, "E2209", {"start": v(-5230.99, -4992.33) * mm, "end": v(-5205.4, -4954.74) * mm});
            skLineSegment(sketch, "E2210", {"start": v(-5205.4, -4954.74) * mm, "end": v(-5175.42, -4920.32) * mm});
            skLineSegment(sketch, "E2211", {"start": v(-5175.42, -4920.32) * mm, "end": v(-5140.73, -4889.13) * mm});
            skLineSegment(sketch, "E2212", {"start": v(-5140.73, -4889.13) * mm, "end": v(-5101, -4861.26) * mm});
            skLineSegment(sketch, "E2213", {"start": v(-5101, -4861.26) * mm, "end": v(-5055.94, -4836.78) * mm});
            skLineSegment(sketch, "E2214", {"start": v(-5055.94, -4836.78) * mm, "end": v(-5005.2, -4815.78) * mm});
            skLineSegment(sketch, "E2215", {"start": v(-5005.2, -4815.78) * mm, "end": v(-4948.48, -4798.33) * mm});
            skLineSegment(sketch, "E2216", {"start": v(-4948.48, -4798.33) * mm, "end": v(-4885.45, -4784.5) * mm});
            skLineSegment(sketch, "E2217", {"start": v(-4885.45, -4784.5) * mm, "end": v(-4825.49, -4775.58) * mm});
            skLineSegment(sketch, "E2218", {"start": v(-4825.49, -4775.58) * mm, "end": v(-4801.23, -4775.05) * mm});
            skLineSegment(sketch, "E2219", {"start": v(-4801.23, -4775.05) * mm, "end": v(-4776.44, -4777.83) * mm});
            skLineSegment(sketch, "E2220", {"start": v(-4776.44, -4777.83) * mm, "end": v(-4751.18, -4783.66) * mm});
            skLineSegment(sketch, "E2221", {"start": v(-4751.18, -4783.66) * mm, "end": v(-4725.53, -4792.27) * mm});
            skLineSegment(sketch, "E2222", {"start": v(-4725.53, -4792.27) * mm, "end": v(-4699.54, -4803.38) * mm});
            skLineSegment(sketch, "E2223", {"start": v(-4699.54, -4803.38) * mm, "end": v(-4673.3, -4816.72) * mm});
            skLineSegment(sketch, "E2224", {"start": v(-4673.3, -4816.72) * mm, "end": v(-4646.87, -4832.03) * mm});
            skLineSegment(sketch, "E2225", {"start": v(-4646.87, -4832.03) * mm, "end": v(-4620.32, -4849.04) * mm});
            skLineSegment(sketch, "E2226", {"start": v(-4620.32, -4849.04) * mm, "end": v(-4593.71, -4867.46) * mm});
            skLineSegment(sketch, "E2227", {"start": v(-4593.71, -4867.46) * mm, "end": v(-4567.12, -4887.05) * mm});
            skLineSegment(sketch, "E2228", {"start": v(-4567.12, -4887.05) * mm, "end": v(-4540.61, -4907.51) * mm});
            skLineSegment(sketch, "E2229", {"start": v(-4540.61, -4907.51) * mm, "end": v(-4514.26, -4928.6) * mm});
            skLineSegment(sketch, "E2230", {"start": v(-4514.26, -4928.6) * mm, "end": v(-4488.12, -4950.02) * mm});
            skLineSegment(sketch, "E2231", {"start": v(-4488.12, -4950.02) * mm, "end": v(-4462.28, -4971.52) * mm});
            skLineSegment(sketch, "E2232", {"start": v(-4462.28, -4971.52) * mm, "end": v(-4436.79, -4992.82) * mm});
            skLineSegment(sketch, "E2233", {"start": v(-4436.79, -4992.82) * mm, "end": v(-4411.73, -5013.65) * mm});
            skLineSegment(sketch, "E2234", {"start": v(-4411.73, -5013.65) * mm, "end": v(-4387.16, -5033.75) * mm});
            skLineSegment(sketch, "E2235", {"start": v(-4387.16, -5033.75) * mm, "end": v(-4363.16, -5052.84) * mm});
            skLineSegment(sketch, "E2236", {"start": v(-4363.16, -5052.84) * mm, "end": v(-4339.79, -5070.65) * mm});
            skLineSegment(sketch, "E2237", {"start": v(-4339.79, -5070.65) * mm, "end": v(-4317.11, -5086.91) * mm});
            skLineSegment(sketch, "E2238", {"start": v(-4317.11, -5086.91) * mm, "end": v(-4295.21, -5101.36) * mm});
            skLineSegment(sketch, "E2239", {"start": v(-4295.21, -5101.36) * mm, "end": v(-4274.15, -5113.71) * mm});
            skLineSegment(sketch, "E2240", {"start": v(-4274.15, -5113.71) * mm, "end": v(-4254, -5123.71) * mm});
            skLineSegment(sketch, "E2241", {"start": v(-4254, -5123.71) * mm, "end": v(-4234.8, -5131.08) * mm});
            skLineSegment(sketch, "E2242", {"start": v(-4234.8, -5131.08) * mm, "end": v(-4216.67, -5135.56) * mm});
            skLineSegment(sketch, "E2243", {"start": v(-4216.67, -5135.56) * mm, "end": v(-4199.64, -5136.86) * mm});
            skLineSegment(sketch, "E2244", {"start": v(-4199.64, -5136.86) * mm, "end": v(-4183.8, -5134.72) * mm});
            skLineSegment(sketch, "E2245", {"start": v(-4183.8, -5134.72) * mm, "end": v(-4169.2, -5128.88) * mm});
            skLineSegment(sketch, "E2246", {"start": v(-4169.2, -5128.88) * mm, "end": v(-4155.92, -5119.05) * mm});
            skLineSegment(sketch, "E2247", {"start": v(-4155.92, -5119.05) * mm, "end": v(-4144.03, -5104.98) * mm});
            skLineSegment(sketch, "E2248", {"start": v(-4144.03, -5104.98) * mm, "end": v(-4133.59, -5086.38) * mm});
            skLineSegment(sketch, "E2249", {"start": v(-4133.59, -5086.38) * mm, "end": v(-4124.67, -5063) * mm});
            skLineSegment(sketch, "E2250", {"start": v(-4124.67, -5063) * mm, "end": v(-4117.35, -5034.55) * mm});
            skLineSegment(sketch, "E2251", {"start": v(-4117.35, -5034.55) * mm, "end": v(-4111.69, -5000.77) * mm});
            skLineSegment(sketch, "E2252", {"start": v(-4111.69, -5000.77) * mm, "end": v(-4107.75, -4961.4) * mm});
            skLineSegment(sketch, "E2253", {"start": v(-4107.75, -4961.4) * mm, "end": v(-4115.4, -4864.3) * mm});
            skLineSegment(sketch, "E2254", {"start": v(-4115.4, -4864.3) * mm, "end": v(-4124.33, -4767.81) * mm});
            skLineSegment(sketch, "E2255", {"start": v(-4124.33, -4767.81) * mm, "end": v(-4134.51, -4671.92) * mm});
            skLineSegment(sketch, "E2256", {"start": v(-4134.51, -4671.92) * mm, "end": v(-4145.98, -4576.6) * mm});
            skLineSegment(sketch, "E2257", {"start": v(-4145.98, -4576.6) * mm, "end": v(-4158.73, -4481.82) * mm});
            skLineSegment(sketch, "E2258", {"start": v(-4158.73, -4481.82) * mm, "end": v(-4172.77, -4387.55) * mm});
            skLineSegment(sketch, "E2259", {"start": v(-4172.77, -4387.55) * mm, "end": v(-4188.1, -4293.76) * mm});
            skLineSegment(sketch, "E2260", {"start": v(-4188.1, -4293.76) * mm, "end": v(-4204.74, -4200.44) * mm});
            skLineSegment(sketch, "E2261", {"start": v(-4204.74, -4200.44) * mm, "end": v(-4222.7, -4107.55) * mm});
            skLineSegment(sketch, "E2262", {"start": v(-4222.7, -4107.55) * mm, "end": v(-4241.96, -4015.07) * mm});
            skLineSegment(sketch, "E2263", {"start": v(-4241.96, -4015.07) * mm, "end": v(-4262.55, -3922.97) * mm});
            skLineSegment(sketch, "E2264", {"start": v(-4262.55, -3922.97) * mm, "end": v(-4284.46, -3831.22) * mm});
            skLineSegment(sketch, "E2265", {"start": v(-4284.46, -3831.22) * mm, "end": v(-4307.72, -3739.8) * mm});
            skLineSegment(sketch, "E2266", {"start": v(-4307.72, -3739.8) * mm, "end": v(-4332.31, -3648.7) * mm});
            skLineSegment(sketch, "E2267", {"start": v(-4332.31, -3648.7) * mm, "end": v(-4358.26, -3557.85) * mm});
            skLineSegment(sketch, "E2268", {"start": v(-4358.26, -3557.85) * mm, "end": v(-4385.56, -3467.26) * mm});
            skLineSegment(sketch, "E2269", {"start": v(-4385.56, -3467.26) * mm, "end": v(-4414.22, -3376.9) * mm});
            skLineSegment(sketch, "E2270", {"start": v(-4414.22, -3376.9) * mm, "end": v(-4444.25, -3286.73) * mm});
            skLineSegment(sketch, "E2271", {"start": v(-4444.25, -3286.73) * mm, "end": v(-4475.66, -3196.73) * mm});
            skLineSegment(sketch, "E2272", {"start": v(-4475.66, -3196.73) * mm, "end": v(-4508.45, -3106.88) * mm});
            skLineSegment(sketch, "E2273", {"start": v(-4508.45, -3106.88) * mm, "end": v(-4542.63, -3017.14) * mm});
            skLineSegment(sketch, "E2274", {"start": v(-4542.63, -3017.14) * mm, "end": v(-4578.2, -2927.5) * mm});
            skLineSegment(sketch, "E2275", {"start": v(-4578.2, -2927.5) * mm, "end": v(-4615.18, -2837.91) * mm});
            skLineSegment(sketch, "E2276", {"start": v(-4615.18, -2837.91) * mm, "end": v(-4653.56, -2748.37) * mm});
            skLineSegment(sketch, "E2277", {"start": v(-2440.53, -8692.23) * mm, "end": v(-2537.63, -8684.57) * mm});
            skLineSegment(sketch, "E2278", {"start": v(-2537.63, -8684.57) * mm, "end": v(-2634.11, -8675.66) * mm});
            skLineSegment(sketch, "E2279", {"start": v(-2634.11, -8675.66) * mm, "end": v(-2730, -8665.47) * mm});
            skLineSegment(sketch, "E2280", {"start": v(-2730, -8665.47) * mm, "end": v(-2825.33, -8654) * mm});
            skLineSegment(sketch, "E2281", {"start": v(-2825.33, -8654) * mm, "end": v(-2920.11, -8641.25) * mm});
            skLineSegment(sketch, "E2282", {"start": v(-2920.11, -8641.25) * mm, "end": v(-3014.38, -8627.2) * mm});
            skLineSegment(sketch, "E2283", {"start": v(-3014.38, -8627.2) * mm, "end": v(-3108.17, -8611.87) * mm});
            skLineSegment(sketch, "E2284", {"start": v(-3108.17, -8611.87) * mm, "end": v(-3201.5, -8595.23) * mm});
            skLineSegment(sketch, "E2285", {"start": v(-3201.5, -8595.23) * mm, "end": v(-3294.38, -8577.28) * mm});
            skLineSegment(sketch, "E2286", {"start": v(-3294.38, -8577.28) * mm, "end": v(-3386.86, -8558.02) * mm});
            skLineSegment(sketch, "E2287", {"start": v(-3386.86, -8558.02) * mm, "end": v(-3478.96, -8537.43) * mm});
            skLineSegment(sketch, "E2288", {"start": v(-3478.96, -8537.43) * mm, "end": v(-3570.7, -8515.52) * mm});
            skLineSegment(sketch, "E2289", {"start": v(-3570.7, -8515.52) * mm, "end": v(-3662.12, -8492.27) * mm});
            skLineSegment(sketch, "E2290", {"start": v(-3662.12, -8492.27) * mm, "end": v(-3753.24, -8467.68) * mm});
            skLineSegment(sketch, "E2291", {"start": v(-3753.24, -8467.68) * mm, "end": v(-3844.08, -8441.74) * mm});
            skLineSegment(sketch, "E2292", {"start": v(-3844.08, -8441.74) * mm, "end": v(-3934.66, -8414.45) * mm});
            skLineSegment(sketch, "E2293", {"start": v(-3934.66, -8414.45) * mm, "end": v(-4025.03, -8385.8) * mm});
            skLineSegment(sketch, "E2294", {"start": v(-4025.03, -8385.8) * mm, "end": v(-4115.2, -8355.78) * mm});
            skLineSegment(sketch, "E2295", {"start": v(-4115.2, -8355.78) * mm, "end": v(-4205.2, -8324.4) * mm});
            skLineSegment(sketch, "E2296", {"start": v(-4205.2, -8324.4) * mm, "end": v(-4295.05, -8291.62) * mm});
            skLineSegment(sketch, "E2297", {"start": v(-4295.05, -8291.62) * mm, "end": v(-4384.79, -8257.46) * mm});
            skLineSegment(sketch, "E2298", {"start": v(-4384.79, -8257.46) * mm, "end": v(-4474.44, -8221.92) * mm});
            skLineSegment(sketch, "E2299", {"start": v(-4474.44, -8221.92) * mm, "end": v(-4564.02, -8184.97) * mm});
            skLineSegment(sketch, "E2300", {"start": v(-4564.02, -8184.97) * mm, "end": v(-4653.56, -8146.62) * mm});
            skLineSegment(sketch, "E2301", {"start": v(-4653.56, -8146.62) * mm, "end": v(-4691.92, -8236.14) * mm});
            skLineSegment(sketch, "E2302", {"start": v(-4691.92, -8236.14) * mm, "end": v(-4728.87, -8325.7) * mm});
            skLineSegment(sketch, "E2303", {"start": v(-4728.87, -8325.7) * mm, "end": v(-4764.42, -8415.32) * mm});
            skLineSegment(sketch, "E2304", {"start": v(-4764.42, -8415.32) * mm, "end": v(-4798.58, -8505.04) * mm});
            skLineSegment(sketch, "E2305", {"start": v(-4798.58, -8505.04) * mm, "end": v(-4831.36, -8594.87) * mm});
            skLineSegment(sketch, "E2306", {"start": v(-4831.36, -8594.87) * mm, "end": v(-4862.75, -8684.85) * mm});
            skLineSegment(sketch, "E2307", {"start": v(-4862.75, -8684.85) * mm, "end": v(-4892.77, -8775) * mm});
            skLineSegment(sketch, "E2308", {"start": v(-4892.77, -8775) * mm, "end": v(-4921.42, -8865.36) * mm});
            skLineSegment(sketch, "E2309", {"start": v(-4921.42, -8865.36) * mm, "end": v(-4948.72, -8955.93) * mm});
            skLineSegment(sketch, "E2310", {"start": v(-4948.72, -8955.93) * mm, "end": v(-4974.65, -9046.76) * mm});
            skLineSegment(sketch, "E2311", {"start": v(-4974.65, -9046.76) * mm, "end": v(-4999.24, -9137.86) * mm});
            skLineSegment(sketch, "E2312", {"start": v(-4999.24, -9137.86) * mm, "end": v(-5022.5, -9229.27) * mm});
            skLineSegment(sketch, "E2313", {"start": v(-5022.5, -9229.27) * mm, "end": v(-5044.4, -9321) * mm});
            skLineSegment(sketch, "E2314", {"start": v(-5044.4, -9321) * mm, "end": v(-5065, -9413.1) * mm});
            skLineSegment(sketch, "E2315", {"start": v(-5065, -9413.1) * mm, "end": v(-5084.26, -9505.57) * mm});
            skLineSegment(sketch, "E2316", {"start": v(-5084.26, -9505.57) * mm, "end": v(-5102.2, -9598.45) * mm});
            skLineSegment(sketch, "E2317", {"start": v(-5102.2, -9598.45) * mm, "end": v(-5118.85, -9691.77) * mm});
            skLineSegment(sketch, "E2318", {"start": v(-5118.85, -9691.77) * mm, "end": v(-5134.19, -9785.55) * mm});
            skLineSegment(sketch, "E2319", {"start": v(-5134.19, -9785.55) * mm, "end": v(-5148.23, -9879.81) * mm});
            skLineSegment(sketch, "E2320", {"start": v(-5148.23, -9879.81) * mm, "end": v(-5160.98, -9974.6) * mm});
            skLineSegment(sketch, "E2321", {"start": v(-5160.98, -9974.6) * mm, "end": v(-5172.45, -10069.92) * mm});
            skLineSegment(sketch, "E2322", {"start": v(-5172.45, -10069.92) * mm, "end": v(-5182.65, -10165.8) * mm});
            skLineSegment(sketch, "E2323", {"start": v(-5182.65, -10165.8) * mm, "end": v(-5191.57, -10262.29) * mm});
            skLineSegment(sketch, "E2324", {"start": v(-5191.57, -10262.29) * mm, "end": v(-5199.24, -10359.39) * mm});
            skLineSegment(sketch, "E2325", {"start": v(-5199.24, -10359.39) * mm, "end": v(-5189.63, -10432.57) * mm});
            skLineSegment(sketch, "E2326", {"start": v(-5189.63, -10432.57) * mm, "end": v(-5173.39, -10484.42) * mm});
            skLineSegment(sketch, "E2327", {"start": v(-5173.39, -10484.42) * mm, "end": v(-5151.06, -10517.1) * mm});
            skLineSegment(sketch, "E2328", {"start": v(-5151.06, -10517.1) * mm, "end": v(-5123.18, -10532.79) * mm});
            skLineSegment(sketch, "E2329", {"start": v(-5123.18, -10532.79) * mm, "end": v(-5090.31, -10533.63) * mm});
            skLineSegment(sketch, "E2330", {"start": v(-5090.31, -10533.63) * mm, "end": v(-5053, -10521.79) * mm});
            skLineSegment(sketch, "E2331", {"start": v(-5053, -10521.79) * mm, "end": v(-5011.78, -10499.43) * mm});
            skLineSegment(sketch, "E2332", {"start": v(-5011.78, -10499.43) * mm, "end": v(-4967.22, -10468.71) * mm});
            skLineSegment(sketch, "E2333", {"start": v(-4967.22, -10468.71) * mm, "end": v(-4919.85, -10431.8) * mm});
            skLineSegment(sketch, "E2334", {"start": v(-4919.85, -10431.8) * mm, "end": v(-4870.22, -10390.87) * mm});
            skLineSegment(sketch, "E2335", {"start": v(-4870.22, -10390.87) * mm, "end": v(-4818.9, -10348.06) * mm});
            skLineSegment(sketch, "E2336", {"start": v(-4818.9, -10348.06) * mm, "end": v(-4766.4, -10305.54) * mm});
            skLineSegment(sketch, "E2337", {"start": v(-4766.4, -10305.54) * mm, "end": v(-4713.3, -10265.48) * mm});
            skLineSegment(sketch, "E2338", {"start": v(-4713.3, -10265.48) * mm, "end": v(-4660.13, -10230.04) * mm});
            skLineSegment(sketch, "E2339", {"start": v(-4660.13, -10230.04) * mm, "end": v(-4607.44, -10201.38) * mm});
            skLineSegment(sketch, "E2340", {"start": v(-4607.44, -10201.38) * mm, "end": v(-4555.79, -10181.66) * mm});
            skLineSegment(sketch, "E2341", {"start": v(-4555.79, -10181.66) * mm, "end": v(-4505.71, -10173.04) * mm});
            skLineSegment(sketch, "E2342", {"start": v(-4505.71, -10173.04) * mm, "end": v(-4448.53, -10178) * mm});
            skLineSegment(sketch, "E2343", {"start": v(-4448.53, -10178) * mm, "end": v(-4382.89, -10190.35) * mm});
            skLineSegment(sketch, "E2344", {"start": v(-4382.89, -10190.35) * mm, "end": v(-4323.68, -10206.36) * mm});
            skLineSegment(sketch, "E2345", {"start": v(-4323.68, -10206.36) * mm, "end": v(-4270.59, -10225.95) * mm});
            skLineSegment(sketch, "E2346", {"start": v(-4270.59, -10225.95) * mm, "end": v(-4223.29, -10249.05) * mm});
            skLineSegment(sketch, "E2347", {"start": v(-4223.29, -10249.05) * mm, "end": v(-4181.46, -10275.57) * mm});
            skLineSegment(sketch, "E2348", {"start": v(-4181.46, -10275.57) * mm, "end": v(-4144.8, -10305.44) * mm});
            skLineSegment(sketch, "E2349", {"start": v(-4144.8, -10305.44) * mm, "end": v(-4112.97, -10338.58) * mm});
            skLineSegment(sketch, "E2350", {"start": v(-4112.97, -10338.58) * mm, "end": v(-4085.67, -10374.91) * mm});
            skLineSegment(sketch, "E2351", {"start": v(-4085.67, -10374.91) * mm, "end": v(-4062.56, -10414.36) * mm});
            skLineSegment(sketch, "E2352", {"start": v(-4062.56, -10414.36) * mm, "end": v(-4043.34, -10456.85) * mm});
            skLineSegment(sketch, "E2353", {"start": v(-4043.34, -10456.85) * mm, "end": v(-4027.68, -10502.3) * mm});
            skLineSegment(sketch, "E2354", {"start": v(-4027.68, -10502.3) * mm, "end": v(-4015.26, -10550.62) * mm});
            skLineSegment(sketch, "E2355", {"start": v(-4015.26, -10550.62) * mm, "end": v(-4005.77, -10601.75) * mm});
            skLineSegment(sketch, "E2356", {"start": v(-4005.77, -10601.75) * mm, "end": v(-3998.89, -10655.61) * mm});
            skLineSegment(sketch, "E2357", {"start": v(-3998.89, -10655.61) * mm, "end": v(-3994.29, -10712.12) * mm});
            skLineSegment(sketch, "E2358", {"start": v(-3994.29, -10712.12) * mm, "end": v(-3991.66, -10771.2) * mm});
            skLineSegment(sketch, "E2359", {"start": v(-3991.66, -10771.2) * mm, "end": v(-3990.68, -10832.78) * mm});
            skLineSegment(sketch, "E2360", {"start": v(-3990.68, -10832.78) * mm, "end": v(-3991.09, -10895.23) * mm});
            skLineSegment(sketch, "E2361", {"start": v(-3991.09, -10895.23) * mm, "end": v(-3993.02, -10955.33) * mm});
            skLineSegment(sketch, "E2362", {"start": v(-3993.02, -10955.33) * mm, "end": v(-3996.8, -11012.88) * mm});
            skLineSegment(sketch, "E2363", {"start": v(-3996.8, -11012.88) * mm, "end": v(-4002.72, -11067.82) * mm});
            skLineSegment(sketch, "E2364", {"start": v(-4002.72, -11067.82) * mm, "end": v(-4011.13, -11120.06) * mm});
            skLineSegment(sketch, "E2365", {"start": v(-4011.13, -11120.06) * mm, "end": v(-4022.34, -11169.54) * mm});
            skLineSegment(sketch, "E2366", {"start": v(-4022.34, -11169.54) * mm, "end": v(-4036.66, -11216.16) * mm});
            skLineSegment(sketch, "E2367", {"start": v(-4036.66, -11216.16) * mm, "end": v(-4054.42, -11259.86) * mm});
            skLineSegment(sketch, "E2368", {"start": v(-4054.42, -11259.86) * mm, "end": v(-4075.94, -11300.55) * mm});
            skLineSegment(sketch, "E2369", {"start": v(-4075.94, -11300.55) * mm, "end": v(-4101.53, -11338.15) * mm});
            skLineSegment(sketch, "E2370", {"start": v(-4101.53, -11338.15) * mm, "end": v(-4131.5, -11372.6) * mm});
            skLineSegment(sketch, "E2371", {"start": v(-4131.5, -11372.6) * mm, "end": v(-4166.2, -11403.8) * mm});
            skLineSegment(sketch, "E2372", {"start": v(-4166.2, -11403.8) * mm, "end": v(-4205.92, -11431.68) * mm});
            skLineSegment(sketch, "E2373", {"start": v(-4205.92, -11431.68) * mm, "end": v(-4250.99, -11456.17) * mm});
            skLineSegment(sketch, "E2374", {"start": v(-4250.99, -11456.17) * mm, "end": v(-4301.73, -11477.18) * mm});
            skLineSegment(sketch, "E2375", {"start": v(-4301.73, -11477.18) * mm, "end": v(-4358.45, -11494.64) * mm});
            skLineSegment(sketch, "E2376", {"start": v(-4358.45, -11494.64) * mm, "end": v(-4421.48, -11508.47) * mm});
            skLineSegment(sketch, "E2377", {"start": v(-4421.48, -11508.47) * mm, "end": v(-4481.44, -11517.4) * mm});
            skLineSegment(sketch, "E2378", {"start": v(-4481.44, -11517.4) * mm, "end": v(-4505.71, -11517.9) * mm});
            skLineSegment(sketch, "E2379", {"start": v(-4505.71, -11517.9) * mm, "end": v(-4530.52, -11515.11) * mm});
            skLineSegment(sketch, "E2380", {"start": v(-4530.52, -11515.11) * mm, "end": v(-4555.79, -11509.27) * mm});
            skLineSegment(sketch, "E2381", {"start": v(-4555.79, -11509.27) * mm, "end": v(-4581.45, -11500.66) * mm});
            skLineSegment(sketch, "E2382", {"start": v(-4581.45, -11500.66) * mm, "end": v(-4607.44, -11489.54) * mm});
            skLineSegment(sketch, "E2383", {"start": v(-4607.44, -11489.54) * mm, "end": v(-4633.69, -11476.18) * mm});
            skLineSegment(sketch, "E2384", {"start": v(-4633.69, -11476.18) * mm, "end": v(-4660.13, -11460.87) * mm});
            skLineSegment(sketch, "E2385", {"start": v(-4660.13, -11460.87) * mm, "end": v(-4686.68, -11443.86) * mm});
            skLineSegment(sketch, "E2386", {"start": v(-4686.68, -11443.86) * mm, "end": v(-4713.3, -11425.43) * mm});
            skLineSegment(sketch, "E2387", {"start": v(-4713.3, -11425.43) * mm, "end": v(-4739.89, -11405.84) * mm});
            skLineSegment(sketch, "E2388", {"start": v(-4739.89, -11405.84) * mm, "end": v(-4766.4, -11385.38) * mm});
            skLineSegment(sketch, "E2389", {"start": v(-4766.4, -11385.38) * mm, "end": v(-4792.76, -11364.3) * mm});
            skLineSegment(sketch, "E2390", {"start": v(-4792.76, -11364.3) * mm, "end": v(-4818.9, -11342.87) * mm});
            skLineSegment(sketch, "E2391", {"start": v(-4818.9, -11342.87) * mm, "end": v(-4844.74, -11321.38) * mm});
            skLineSegment(sketch, "E2392", {"start": v(-4844.74, -11321.38) * mm, "end": v(-4870.22, -11300.08) * mm});
            skLineSegment(sketch, "E2393", {"start": v(-4870.22, -11300.08) * mm, "end": v(-4895.28, -11279.25) * mm});
            skLineSegment(sketch, "E2394", {"start": v(-4895.28, -11279.25) * mm, "end": v(-4919.85, -11259.15) * mm});
            skLineSegment(sketch, "E2395", {"start": v(-4919.85, -11259.15) * mm, "end": v(-4943.85, -11240.07) * mm});
            skLineSegment(sketch, "E2396", {"start": v(-4943.85, -11240.07) * mm, "end": v(-4967.22, -11222.26) * mm});
            skLineSegment(sketch, "E2397", {"start": v(-4967.22, -11222.26) * mm, "end": v(-4989.88, -11206) * mm});
            skLineSegment(sketch, "E2398", {"start": v(-4989.88, -11206) * mm, "end": v(-5011.78, -11191.56) * mm});
            skLineSegment(sketch, "E2399", {"start": v(-5011.78, -11191.56) * mm, "end": v(-5032.84, -11179.21) * mm});
            skLineSegment(sketch, "E2400", {"start": v(-5032.84, -11179.21) * mm, "end": v(-5053, -11169.22) * mm});
            skLineSegment(sketch, "E2401", {"start": v(-5053, -11169.22) * mm, "end": v(-5072.17, -11161.85) * mm});
            skLineSegment(sketch, "E2402", {"start": v(-5072.17, -11161.85) * mm, "end": v(-5090.31, -11157.39) * mm});
            skLineSegment(sketch, "E2403", {"start": v(-5090.31, -11157.39) * mm, "end": v(-5107.34, -11156.09) * mm});
            skLineSegment(sketch, "E2404", {"start": v(-5107.34, -11156.09) * mm, "end": v(-5123.18, -11158.23) * mm});
            skLineSegment(sketch, "E2405", {"start": v(-5123.18, -11158.23) * mm, "end": v(-5137.78, -11164.08) * mm});
            skLineSegment(sketch, "E2406", {"start": v(-5137.78, -11164.08) * mm, "end": v(-5151.06, -11173.91) * mm});
            skLineSegment(sketch, "E2407", {"start": v(-5151.06, -11173.91) * mm, "end": v(-5162.95, -11187.99) * mm});
            skLineSegment(sketch, "E2408", {"start": v(-5162.95, -11187.99) * mm, "end": v(-5173.39, -11206.59) * mm});
            skLineSegment(sketch, "E2409", {"start": v(-5173.39, -11206.59) * mm, "end": v(-5182.3, -11229.98) * mm});
            skLineSegment(sketch, "E2410", {"start": v(-5182.3, -11229.98) * mm, "end": v(-5189.63, -11258.42) * mm});
            skLineSegment(sketch, "E2411", {"start": v(-5189.63, -11258.42) * mm, "end": v(-5195.3, -11292.2) * mm});
            skLineSegment(sketch, "E2412", {"start": v(-5195.3, -11292.2) * mm, "end": v(-5199.24, -11331.58) * mm});
            skLineSegment(sketch, "E2413", {"start": v(-5199.24, -11331.58) * mm, "end": v(-5191.57, -11428.68) * mm});
            skLineSegment(sketch, "E2414", {"start": v(-5191.57, -11428.68) * mm, "end": v(-5182.65, -11525.16) * mm});
            skLineSegment(sketch, "E2415", {"start": v(-5182.65, -11525.16) * mm, "end": v(-5172.45, -11621.05) * mm});
            skLineSegment(sketch, "E2416", {"start": v(-5172.45, -11621.05) * mm, "end": v(-5160.98, -11716.38) * mm});
            skLineSegment(sketch, "E2417", {"start": v(-5160.98, -11716.38) * mm, "end": v(-5148.23, -11811.16) * mm});
            skLineSegment(sketch, "E2418", {"start": v(-5148.23, -11811.16) * mm, "end": v(-5134.19, -11905.43) * mm});
            skLineSegment(sketch, "E2419", {"start": v(-5134.19, -11905.43) * mm, "end": v(-5118.85, -11999.21) * mm});
            skLineSegment(sketch, "E2420", {"start": v(-5118.85, -11999.21) * mm, "end": v(-5102.2, -12092.54) * mm});
            skLineSegment(sketch, "E2421", {"start": v(-5102.2, -12092.54) * mm, "end": v(-5084.26, -12185.43) * mm});
            skLineSegment(sketch, "E2422", {"start": v(-5084.26, -12185.43) * mm, "end": v(-5065, -12277.9) * mm});
            skLineSegment(sketch, "E2423", {"start": v(-5065, -12277.9) * mm, "end": v(-5044.4, -12370) * mm});
            skLineSegment(sketch, "E2424", {"start": v(-5044.4, -12370) * mm, "end": v(-5022.5, -12461.75) * mm});
            skLineSegment(sketch, "E2425", {"start": v(-5022.5, -12461.75) * mm, "end": v(-4999.24, -12553.17) * mm});
            skLineSegment(sketch, "E2426", {"start": v(-4999.24, -12553.17) * mm, "end": v(-4974.65, -12644.28) * mm});
            skLineSegment(sketch, "E2427", {"start": v(-4974.65, -12644.28) * mm, "end": v(-4948.72, -12735.12) * mm});
            skLineSegment(sketch, "E2428", {"start": v(-4948.72, -12735.12) * mm, "end": v(-4921.42, -12825.71) * mm});
            skLineSegment(sketch, "E2429", {"start": v(-4921.42, -12825.71) * mm, "end": v(-4892.77, -12916.08) * mm});
            skLineSegment(sketch, "E2430", {"start": v(-4892.77, -12916.08) * mm, "end": v(-4862.75, -13006.25) * mm});
            skLineSegment(sketch, "E2431", {"start": v(-4862.75, -13006.25) * mm, "end": v(-4831.36, -13096.25) * mm});
            skLineSegment(sketch, "E2432", {"start": v(-4831.36, -13096.25) * mm, "end": v(-4798.58, -13186.1) * mm});
            skLineSegment(sketch, "E2433", {"start": v(-4798.58, -13186.1) * mm, "end": v(-4764.42, -13275.84) * mm});
            skLineSegment(sketch, "E2434", {"start": v(-4764.42, -13275.84) * mm, "end": v(-4728.87, -13365.48) * mm});
            skLineSegment(sketch, "E2435", {"start": v(-4728.87, -13365.48) * mm, "end": v(-4691.92, -13455.06) * mm});
            skLineSegment(sketch, "E2436", {"start": v(-4691.92, -13455.06) * mm, "end": v(-4653.56, -13544.6) * mm});
            skLineSegment(sketch, "E2437", {"start": v(-4653.56, -13544.6) * mm, "end": v(-4564.02, -13506.22) * mm});
            skLineSegment(sketch, "E2438", {"start": v(-4564.02, -13506.22) * mm, "end": v(-4474.44, -13469.25) * mm});
            skLineSegment(sketch, "E2439", {"start": v(-4474.44, -13469.25) * mm, "end": v(-4384.79, -13433.68) * mm});
            skLineSegment(sketch, "E2440", {"start": v(-4384.79, -13433.68) * mm, "end": v(-4295.05, -13399.5) * mm});
            skLineSegment(sketch, "E2441", {"start": v(-4295.05, -13399.5) * mm, "end": v(-4205.2, -13366.7) * mm});
            skLineSegment(sketch, "E2442", {"start": v(-4205.2, -13366.7) * mm, "end": v(-4115.2, -13335.3) * mm});
            skLineSegment(sketch, "E2443", {"start": v(-4115.2, -13335.3) * mm, "end": v(-4025.03, -13305.27) * mm});
            skLineSegment(sketch, "E2444", {"start": v(-4025.03, -13305.27) * mm, "end": v(-3934.66, -13276.6) * mm});
            skLineSegment(sketch, "E2445", {"start": v(-3934.66, -13276.6) * mm, "end": v(-3844.08, -13249.3) * mm});
            skLineSegment(sketch, "E2446", {"start": v(-3844.08, -13249.3) * mm, "end": v(-3753.24, -13223.36) * mm});
            skLineSegment(sketch, "E2447", {"start": v(-3753.24, -13223.36) * mm, "end": v(-3662.12, -13198.76) * mm});
            skLineSegment(sketch, "E2448", {"start": v(-3662.12, -13198.76) * mm, "end": v(-3570.7, -13175.5) * mm});
            skLineSegment(sketch, "E2449", {"start": v(-3570.7, -13175.5) * mm, "end": v(-3478.96, -13153.58) * mm});
            skLineSegment(sketch, "E2450", {"start": v(-3478.96, -13153.58) * mm, "end": v(-3386.86, -13133) * mm});
            skLineSegment(sketch, "E2451", {"start": v(-3386.86, -13133) * mm, "end": v(-3294.38, -13113.72) * mm});
            skLineSegment(sketch, "E2452", {"start": v(-3294.38, -13113.72) * mm, "end": v(-3201.5, -13095.77) * mm});
            skLineSegment(sketch, "E2453", {"start": v(-3201.5, -13095.77) * mm, "end": v(-3108.17, -13079.13) * mm});
            skLineSegment(sketch, "E2454", {"start": v(-3108.17, -13079.13) * mm, "end": v(-3014.38, -13063.79) * mm});
            skLineSegment(sketch, "E2455", {"start": v(-3014.38, -13063.79) * mm, "end": v(-2920.11, -13049.74) * mm});
            skLineSegment(sketch, "E2456", {"start": v(-2920.11, -13049.74) * mm, "end": v(-2825.33, -13036.99) * mm});
            skLineSegment(sketch, "E2457", {"start": v(-2825.33, -13036.99) * mm, "end": v(-2730, -13025.52) * mm});
            skLineSegment(sketch, "E2458", {"start": v(-2730, -13025.52) * mm, "end": v(-2634.11, -13015.32) * mm});
            skLineSegment(sketch, "E2459", {"start": v(-2634.11, -13015.32) * mm, "end": v(-2537.63, -13006.4) * mm});
            skLineSegment(sketch, "E2460", {"start": v(-2537.63, -13006.4) * mm, "end": v(-2440.53, -12998.74) * mm});
            skLineSegment(sketch, "E2461", {"start": v(-2440.53, -12998.74) * mm, "end": v(-2367.35, -13008.33) * mm});
            skLineSegment(sketch, "E2462", {"start": v(-2367.35, -13008.33) * mm, "end": v(-2315.49, -13024.57) * mm});
            skLineSegment(sketch, "E2463", {"start": v(-2315.49, -13024.57) * mm, "end": v(-2282.8, -13046.9) * mm});
            skLineSegment(sketch, "E2464", {"start": v(-2282.8, -13046.9) * mm, "end": v(-2267.1, -13074.79) * mm});
            skLineSegment(sketch, "E2465", {"start": v(-2267.1, -13074.79) * mm, "end": v(-2266.26, -13107.67) * mm});
            skLineSegment(sketch, "E2466", {"start": v(-2266.26, -13107.67) * mm, "end": v(-2278.09, -13145) * mm});
            skLineSegment(sketch, "E2467", {"start": v(-2278.09, -13145) * mm, "end": v(-2300.44, -13186.22) * mm});
            skLineSegment(sketch, "E2468", {"start": v(-2300.44, -13186.22) * mm, "end": v(-2331.14, -13230.8) * mm});
            skLineSegment(sketch, "E2469", {"start": v(-2331.14, -13230.8) * mm, "end": v(-2368.05, -13278.18) * mm});
            skLineSegment(sketch, "E2470", {"start": v(-2368.05, -13278.18) * mm, "end": v(-2408.98, -13327.8) * mm});
            skLineSegment(sketch, "E2471", {"start": v(-2408.98, -13327.8) * mm, "end": v(-2451.79, -13379.15) * mm});
            skLineSegment(sketch, "E2472", {"start": v(-2451.79, -13379.15) * mm, "end": v(-2494.3, -13431.65) * mm});
            skLineSegment(sketch, "E2473", {"start": v(-2494.3, -13431.65) * mm, "end": v(-2534.38, -13484.75) * mm});
            skLineSegment(sketch, "E2474", {"start": v(-2534.38, -13484.75) * mm, "end": v(-2569.84, -13537.91) * mm});
            skLineSegment(sketch, "E2475", {"start": v(-2569.84, -13537.91) * mm, "end": v(-2598.52, -13590.59) * mm});
            skLineSegment(sketch, "E2476", {"start": v(-2598.52, -13590.59) * mm, "end": v(-2618.27, -13642.22) * mm});
            skLineSegment(sketch, "E2477", {"start": v(-2618.27, -13642.22) * mm, "end": v(-2626.92, -13692.28) * mm});
            skLineSegment(sketch, "E2478", {"start": v(-2626.92, -13692.28) * mm, "end": v(-2621.99, -13749.44) * mm});
            skLineSegment(sketch, "E2479", {"start": v(-2621.99, -13749.44) * mm, "end": v(-2609.63, -13815.09) * mm});
            skLineSegment(sketch, "E2480", {"start": v(-2609.63, -13815.09) * mm, "end": v(-2593.62, -13874.3) * mm});
            skLineSegment(sketch, "E2481", {"start": v(-2593.62, -13874.3) * mm, "end": v(-2574.03, -13927.39) * mm});
            skLineSegment(sketch, "E2482", {"start": v(-2574.03, -13927.39) * mm, "end": v(-2550.94, -13974.68) * mm});
            skLineSegment(sketch, "E2483", {"start": v(-2550.94, -13974.68) * mm, "end": v(-2524.41, -14016.5) * mm});
            skLineSegment(sketch, "E2484", {"start": v(-2524.41, -14016.5) * mm, "end": v(-2494.54, -14053.17) * mm});
            skLineSegment(sketch, "E2485", {"start": v(-2494.54, -14053.17) * mm, "end": v(-2461.4, -14085) * mm});
            skLineSegment(sketch, "E2486", {"start": v(-2461.4, -14085) * mm, "end": v(-2425.07, -14112.3) * mm});
            skLineSegment(sketch, "E2487", {"start": v(-2425.07, -14112.3) * mm, "end": v(-2385.62, -14135.4) * mm});
            skLineSegment(sketch, "E2488", {"start": v(-2385.62, -14135.4) * mm, "end": v(-2343.14, -14154.63) * mm});
            skLineSegment(sketch, "E2489", {"start": v(-2343.14, -14154.63) * mm, "end": v(-2297.69, -14170.3) * mm});
            skLineSegment(sketch, "E2490", {"start": v(-2297.69, -14170.3) * mm, "end": v(-2249.36, -14182.7) * mm});
            skLineSegment(sketch, "E2491", {"start": v(-2249.36, -14182.7) * mm, "end": v(-2198.23, -14192.2) * mm});
            skLineSegment(sketch, "E2492", {"start": v(-2198.23, -14192.2) * mm, "end": v(-2144.37, -14199.09) * mm});
            skLineSegment(sketch, "E2493", {"start": v(-2144.37, -14199.09) * mm, "end": v(-2087.86, -14203.68) * mm});
            skLineSegment(sketch, "E2494", {"start": v(-2087.86, -14203.68) * mm, "end": v(-2028.78, -14206.31) * mm});
            skLineSegment(sketch, "E2495", {"start": v(-2028.78, -14206.31) * mm, "end": v(-1967.2, -14207.29) * mm});
            skLineSegment(sketch, "E2496", {"start": v(-1967.2, -14207.29) * mm, "end": v(-1904.75, -14206.88) * mm});
            skLineSegment(sketch, "E2497", {"start": v(-1904.75, -14206.88) * mm, "end": v(-1844.65, -14204.95) * mm});
            skLineSegment(sketch, "E2498", {"start": v(-1844.65, -14204.95) * mm, "end": v(-1787.1, -14201.18) * mm});
            skLineSegment(sketch, "E2499", {"start": v(-1787.1, -14201.18) * mm, "end": v(-1732.16, -14195.25) * mm});
            skLineSegment(sketch, "E2500", {"start": v(-1732.16, -14195.25) * mm, "end": v(-1679.9, -14186.84) * mm});
            skLineSegment(sketch, "E2501", {"start": v(-1679.9, -14186.84) * mm, "end": v(-1630.43, -14175.63) * mm});
            skLineSegment(sketch, "E2502", {"start": v(-1630.43, -14175.63) * mm, "end": v(-1583.8, -14161.3) * mm});
            skLineSegment(sketch, "E2503", {"start": v(-1583.8, -14161.3) * mm, "end": v(-1540.1, -14143.55) * mm});
            skLineSegment(sketch, "E2504", {"start": v(-1540.1, -14143.55) * mm, "end": v(-1499.4, -14122.03) * mm});
            skLineSegment(sketch, "E2505", {"start": v(-1499.4, -14122.03) * mm, "end": v(-1461.8, -14096.44) * mm});
            skLineSegment(sketch, "E2506", {"start": v(-1461.8, -14096.44) * mm, "end": v(-1427.34, -14066.46) * mm});
            skLineSegment(sketch, "E2507", {"start": v(-1427.34, -14066.46) * mm, "end": v(-1396.14, -14031.77) * mm});
            skLineSegment(sketch, "E2508", {"start": v(-1396.14, -14031.77) * mm, "end": v(-1368.25, -13992.05) * mm});
            skLineSegment(sketch, "E2509", {"start": v(-1368.25, -13992.05) * mm, "end": v(-1343.76, -13946.98) * mm});
            skLineSegment(sketch, "E2510", {"start": v(-1343.76, -13946.98) * mm, "end": v(-1322.74, -13896.25) * mm});
            skLineSegment(sketch, "E2511", {"start": v(-1322.74, -13896.25) * mm, "end": v(-1305.28, -13839.52) * mm});
            skLineSegment(sketch, "E2512", {"start": v(-1305.28, -13839.52) * mm, "end": v(-1291.45, -13776.5) * mm});
            skLineSegment(sketch, "E2513", {"start": v(-1291.45, -13776.5) * mm, "end": v(-1282.53, -13716.53) * mm});
            skLineSegment(sketch, "E2514", {"start": v(-1282.53, -13716.53) * mm, "end": v(-1282.01, -13692.28) * mm});
            skLineSegment(sketch, "E2515", {"start": v(-1282.01, -13692.28) * mm, "end": v(-1284.82, -13667.48) * mm});
            skLineSegment(sketch, "E2516", {"start": v(-1284.82, -13667.48) * mm, "end": v(-1290.66, -13642.22) * mm});
            skLineSegment(sketch, "E2517", {"start": v(-1290.66, -13642.22) * mm, "end": v(-1299.28, -13616.57) * mm});
            skLineSegment(sketch, "E2518", {"start": v(-1299.28, -13616.57) * mm, "end": v(-1310.4, -13590.59) * mm});
            skLineSegment(sketch, "E2519", {"start": v(-1310.4, -13590.59) * mm, "end": v(-1323.76, -13564.35) * mm});
            skLineSegment(sketch, "E2520", {"start": v(-1323.76, -13564.35) * mm, "end": v(-1339.08, -13537.91) * mm});
            skLineSegment(sketch, "E2521", {"start": v(-1339.08, -13537.91) * mm, "end": v(-1356.1, -13511.36) * mm});
            skLineSegment(sketch, "E2522", {"start": v(-1356.1, -13511.36) * mm, "end": v(-1374.53, -13484.75) * mm});
            skLineSegment(sketch, "E2523", {"start": v(-1374.53, -13484.75) * mm, "end": v(-1394.12, -13458.16) * mm});
            skLineSegment(sketch, "E2524", {"start": v(-1394.12, -13458.16) * mm, "end": v(-1414.59, -13431.65) * mm});
            skLineSegment(sketch, "E2525", {"start": v(-1414.59, -13431.65) * mm, "end": v(-1435.67, -13405.29) * mm});
            skLineSegment(sketch, "E2526", {"start": v(-1435.67, -13405.29) * mm, "end": v(-1457.1, -13379.15) * mm});
            skLineSegment(sketch, "E2527", {"start": v(-1457.1, -13379.15) * mm, "end": v(-1478.6, -13353.3) * mm});
            skLineSegment(sketch, "E2528", {"start": v(-1478.6, -13353.3) * mm, "end": v(-1499.9, -13327.8) * mm});
            skLineSegment(sketch, "E2529", {"start": v(-1499.9, -13327.8) * mm, "end": v(-1520.72, -13302.75) * mm});
            skLineSegment(sketch, "E2530", {"start": v(-1520.72, -13302.75) * mm, "end": v(-1540.82, -13278.18) * mm});
            skLineSegment(sketch, "E2531", {"start": v(-1540.82, -13278.18) * mm, "end": v(-1559.9, -13254.17) * mm});
            skLineSegment(sketch, "E2532", {"start": v(-1559.9, -13254.17) * mm, "end": v(-1577.71, -13230.8) * mm});
            skLineSegment(sketch, "E2533", {"start": v(-1577.71, -13230.8) * mm, "end": v(-1593.97, -13208.12) * mm});
            skLineSegment(sketch, "E2534", {"start": v(-1593.97, -13208.12) * mm, "end": v(-1608.41, -13186.22) * mm});
            skLineSegment(sketch, "E2535", {"start": v(-1608.41, -13186.22) * mm, "end": v(-1620.77, -13165.15) * mm});
            skLineSegment(sketch, "E2536", {"start": v(-1620.77, -13165.15) * mm, "end": v(-1630.76, -13145) * mm});
            skLineSegment(sketch, "E2537", {"start": v(-1630.76, -13145) * mm, "end": v(-1638.13, -13125.8) * mm});
            skLineSegment(sketch, "E2538", {"start": v(-1638.13, -13125.8) * mm, "end": v(-1642.6, -13107.67) * mm});
            skLineSegment(sketch, "E2539", {"start": v(-1642.6, -13107.67) * mm, "end": v(-1643.9, -13090.64) * mm});
            skLineSegment(sketch, "E2540", {"start": v(-1643.9, -13090.64) * mm, "end": v(-1641.75, -13074.79) * mm});
            skLineSegment(sketch, "E2541", {"start": v(-1641.75, -13074.79) * mm, "end": v(-1635.9, -13060.19) * mm});
            skLineSegment(sketch, "E2542", {"start": v(-1635.9, -13060.19) * mm, "end": v(-1626.07, -13046.9) * mm});
            skLineSegment(sketch, "E2543", {"start": v(-1626.07, -13046.9) * mm, "end": v(-1612, -13035.01) * mm});
            skLineSegment(sketch, "E2544", {"start": v(-1612, -13035.01) * mm, "end": v(-1593.4, -13024.57) * mm});
            skLineSegment(sketch, "E2545", {"start": v(-1593.4, -13024.57) * mm, "end": v(-1570, -13015.66) * mm});
            skLineSegment(sketch, "E2546", {"start": v(-1570, -13015.66) * mm, "end": v(-1541.56, -13008.33) * mm});
            skLineSegment(sketch, "E2547", {"start": v(-1541.56, -13008.33) * mm, "end": v(-1507.78, -13002.67) * mm});
            skLineSegment(sketch, "E2548", {"start": v(-1507.78, -13002.67) * mm, "end": v(-1468.4, -12998.74) * mm});
            skLineSegment(sketch, "E2549", {"start": v(6142.61, -2748.37) * mm, "end": v(6104.23, -2658.85) * mm});
            skLineSegment(sketch, "E2550", {"start": v(6104.23, -2658.85) * mm, "end": v(6067.26, -2569.3) * mm});
            skLineSegment(sketch, "E2551", {"start": v(6067.26, -2569.3) * mm, "end": v(6031.68, -2479.67) * mm});
            skLineSegment(sketch, "E2552", {"start": v(6031.68, -2479.67) * mm, "end": v(5997.5, -2389.95) * mm});
            skLineSegment(sketch, "E2553", {"start": v(5997.5, -2389.95) * mm, "end": v(5964.72, -2300.11) * mm});
            skLineSegment(sketch, "E2554", {"start": v(5964.72, -2300.11) * mm, "end": v(5933.3, -2210.13) * mm});
            skLineSegment(sketch, "E2555", {"start": v(5933.3, -2210.13) * mm, "end": v(5903.28, -2119.98) * mm});
            skLineSegment(sketch, "E2556", {"start": v(5903.28, -2119.98) * mm, "end": v(5874.61, -2029.63) * mm});
            skLineSegment(sketch, "E2557", {"start": v(5874.61, -2029.63) * mm, "end": v(5847.31, -1939.05) * mm});
            skLineSegment(sketch, "E2558", {"start": v(5847.31, -1939.05) * mm, "end": v(5821.37, -1848.23) * mm});
            skLineSegment(sketch, "E2559", {"start": v(5821.37, -1848.23) * mm, "end": v(5796.77, -1757.12) * mm});
            skLineSegment(sketch, "E2560", {"start": v(5796.77, -1757.12) * mm, "end": v(5773.52, -1665.72) * mm});
            skLineSegment(sketch, "E2561", {"start": v(5773.52, -1665.72) * mm, "end": v(5751.6, -1573.98) * mm});
            skLineSegment(sketch, "E2562", {"start": v(5751.6, -1573.98) * mm, "end": v(5731.01, -1481.9) * mm});
            skLineSegment(sketch, "E2563", {"start": v(5731.01, -1481.9) * mm, "end": v(5711.75, -1389.42) * mm});
            skLineSegment(sketch, "E2564", {"start": v(5711.75, -1389.42) * mm, "end": v(5693.8, -1296.54) * mm});
            skLineSegment(sketch, "E2565", {"start": v(5693.8, -1296.54) * mm, "end": v(5677.16, -1203.22) * mm});
            skLineSegment(sketch, "E2566", {"start": v(5677.16, -1203.22) * mm, "end": v(5661.82, -1109.44) * mm});
            skLineSegment(sketch, "E2567", {"start": v(5661.82, -1109.44) * mm, "end": v(5647.78, -1015.17) * mm});
            skLineSegment(sketch, "E2568", {"start": v(5647.78, -1015.17) * mm, "end": v(5635.03, -920.4) * mm});
            skLineSegment(sketch, "E2569", {"start": v(5635.03, -920.4) * mm, "end": v(5623.57, -825.07) * mm});
            skLineSegment(sketch, "E2570", {"start": v(5623.57, -825.07) * mm, "end": v(5613.38, -729.18) * mm});
            skLineSegment(sketch, "E2571", {"start": v(5613.38, -729.18) * mm, "end": v(5604.46, -632.7) * mm});
            skLineSegment(sketch, "E2572", {"start": v(5604.46, -632.7) * mm, "end": v(5596.8, -535.6) * mm});
            skLineSegment(sketch, "E2573", {"start": v(5596.8, -535.6) * mm, "end": v(5606.4, -462.42) * mm});
            skLineSegment(sketch, "E2574", {"start": v(5606.4, -462.42) * mm, "end": v(5622.64, -410.56) * mm});
            skLineSegment(sketch, "E2575", {"start": v(5622.64, -410.56) * mm, "end": v(5644.97, -377.86) * mm});
            skLineSegment(sketch, "E2576", {"start": v(5644.97, -377.86) * mm, "end": v(5672.85, -362.17) * mm});
            skLineSegment(sketch, "E2577", {"start": v(5672.85, -362.17) * mm, "end": v(5705.73, -361.32) * mm});
            skLineSegment(sketch, "E2578", {"start": v(5705.73, -361.32) * mm, "end": v(5743.05, -373.15) * mm});
            skLineSegment(sketch, "E2579", {"start": v(5743.05, -373.15) * mm, "end": v(5784.28, -395.5) * mm});
            skLineSegment(sketch, "E2580", {"start": v(5784.28, -395.5) * mm, "end": v(5828.86, -426.2) * mm});
            skLineSegment(sketch, "E2581", {"start": v(5828.86, -426.2) * mm, "end": v(5876.24, -463.1) * mm});
            skLineSegment(sketch, "E2582", {"start": v(5876.24, -463.1) * mm, "end": v(5925.88, -504.04) * mm});
            skLineSegment(sketch, "E2583", {"start": v(5925.88, -504.04) * mm, "end": v(5977.22, -546.84) * mm});
            skLineSegment(sketch, "E2584", {"start": v(5977.22, -546.84) * mm, "end": v(6029.73, -589.36) * mm});
            skLineSegment(sketch, "E2585", {"start": v(6029.73, -589.36) * mm, "end": v(6082.85, -629.42) * mm});
            skLineSegment(sketch, "E2586", {"start": v(6082.85, -629.42) * mm, "end": v(6136.03, -664.87) * mm});
            skLineSegment(sketch, "E2587", {"start": v(6136.03, -664.87) * mm, "end": v(6188.72, -693.55) * mm});
            skLineSegment(sketch, "E2588", {"start": v(6188.72, -693.55) * mm, "end": v(6240.38, -713.29) * mm});
            skLineSegment(sketch, "E2589", {"start": v(6240.38, -713.29) * mm, "end": v(6290.46, -721.93) * mm});
            skLineSegment(sketch, "E2590", {"start": v(6290.46, -721.93) * mm, "end": v(6347.63, -717) * mm});
            skLineSegment(sketch, "E2591", {"start": v(6347.63, -717) * mm, "end": v(6413.24, -704.64) * mm});
            skLineSegment(sketch, "E2592", {"start": v(6413.24, -704.64) * mm, "end": v(6472.42, -688.62) * mm});
            skLineSegment(sketch, "E2593", {"start": v(6472.42, -688.62) * mm, "end": v(6525.5, -669.02) * mm});
            skLineSegment(sketch, "E2594", {"start": v(6525.5, -669.02) * mm, "end": v(6572.77, -645.91) * mm});
            skLineSegment(sketch, "E2595", {"start": v(6572.77, -645.91) * mm, "end": v(6614.58, -619.38) * mm});
            skLineSegment(sketch, "E2596", {"start": v(6614.58, -619.38) * mm, "end": v(6651.23, -589.5) * mm});
            skLineSegment(sketch, "E2597", {"start": v(6651.23, -589.5) * mm, "end": v(6683.04, -556.33) * mm});
            skLineSegment(sketch, "E2598", {"start": v(6683.04, -556.33) * mm, "end": v(6710.34, -519.98) * mm});
            skLineSegment(sketch, "E2599", {"start": v(6710.34, -519.98) * mm, "end": v(6733.44, -480.52) * mm});
            skLineSegment(sketch, "E2600", {"start": v(6733.44, -480.52) * mm, "end": v(6752.65, -438.02) * mm});
            skLineSegment(sketch, "E2601", {"start": v(6752.65, -438.02) * mm, "end": v(6768.3, -392.55) * mm});
            skLineSegment(sketch, "E2602", {"start": v(6768.3, -392.55) * mm, "end": v(6780.72, -344.21) * mm});
            skLineSegment(sketch, "E2603", {"start": v(6780.72, -344.21) * mm, "end": v(6790.21, -293.07) * mm});
            skLineSegment(sketch, "E2604", {"start": v(6790.21, -293.07) * mm, "end": v(6797.1, -239.2) * mm});
            skLineSegment(sketch, "E2605", {"start": v(6797.1, -239.2) * mm, "end": v(6801.69, -182.68) * mm});
            skLineSegment(sketch, "E2606", {"start": v(6801.69, -182.68) * mm, "end": v(6804.32, -123.6) * mm});
            skLineSegment(sketch, "E2607", {"start": v(6804.32, -123.6) * mm, "end": v(6805.3, -62.01) * mm});
            skLineSegment(sketch, "E2608", {"start": v(6805.3, -62.01) * mm, "end": v(6804.89, 0.44) * mm});
            skLineSegment(sketch, "E2609", {"start": v(6804.89, 0.44) * mm, "end": v(6802.96, 60.53) * mm});
            skLineSegment(sketch, "E2610", {"start": v(6802.96, 60.53) * mm, "end": v(6799.19, 118.09) * mm});
            skLineSegment(sketch, "E2611", {"start": v(6799.19, 118.09) * mm, "end": v(6793.26, 173.02) * mm});
            skLineSegment(sketch, "E2612", {"start": v(6793.26, 173.02) * mm, "end": v(6784.85, 225.27) * mm});
            skLineSegment(sketch, "E2613", {"start": v(6784.85, 225.27) * mm, "end": v(6773.64, 274.74) * mm});
            skLineSegment(sketch, "E2614", {"start": v(6773.64, 274.74) * mm, "end": v(6759.31, 321.36) * mm});
            skLineSegment(sketch, "E2615", {"start": v(6759.31, 321.36) * mm, "end": v(6741.55, 365.05) * mm});
            skLineSegment(sketch, "E2616", {"start": v(6741.55, 365.05) * mm, "end": v(6720.04, 405.73) * mm});
            skLineSegment(sketch, "E2617", {"start": v(6720.04, 405.73) * mm, "end": v(6694.45, 443.33) * mm});
            skLineSegment(sketch, "E2618", {"start": v(6694.45, 443.33) * mm, "end": v(6664.47, 477.76) * mm});
            skLineSegment(sketch, "E2619", {"start": v(6664.47, 477.76) * mm, "end": v(6629.78, 508.95) * mm});
            skLineSegment(sketch, "E2620", {"start": v(6629.78, 508.95) * mm, "end": v(6590.06, 536.81) * mm});
            skLineSegment(sketch, "E2621", {"start": v(6590.06, 536.81) * mm, "end": v(6545, 561.28) * mm});
            skLineSegment(sketch, "E2622", {"start": v(6545, 561.28) * mm, "end": v(6494.25, 582.27) * mm});
            skLineSegment(sketch, "E2623", {"start": v(6494.25, 582.27) * mm, "end": v(6437.53, 599.7) * mm});
            skLineSegment(sketch, "E2624", {"start": v(6437.53, 599.7) * mm, "end": v(6374.5, 613.51) * mm});
            skLineSegment(sketch, "E2625", {"start": v(6374.5, 613.51) * mm, "end": v(6314.54, 622.4) * mm});
            skLineSegment(sketch, "E2626", {"start": v(6314.54, 622.4) * mm, "end": v(6290.28, 622.94) * mm});
            skLineSegment(sketch, "E2627", {"start": v(6290.28, 622.94) * mm, "end": v(6265.5, 620.16) * mm});
            skLineSegment(sketch, "E2628", {"start": v(6265.5, 620.16) * mm, "end": v(6240.23, 614.33) * mm});
            skLineSegment(sketch, "E2629", {"start": v(6240.23, 614.33) * mm, "end": v(6214.58, 605.72) * mm});
            skLineSegment(sketch, "E2630", {"start": v(6214.58, 605.72) * mm, "end": v(6188.6, 594.61) * mm});
            skLineSegment(sketch, "E2631", {"start": v(6188.6, 594.61) * mm, "end": v(6162.36, 581.27) * mm});
            skLineSegment(sketch, "E2632", {"start": v(6162.36, 581.27) * mm, "end": v(6135.93, 565.96) * mm});
            skLineSegment(sketch, "E2633", {"start": v(6135.93, 565.96) * mm, "end": v(6109.37, 548.95) * mm});
            skLineSegment(sketch, "E2634", {"start": v(6109.37, 548.95) * mm, "end": v(6082.77, 530.53) * mm});
            skLineSegment(sketch, "E2635", {"start": v(6082.77, 530.53) * mm, "end": v(6056.18, 510.94) * mm});
            skLineSegment(sketch, "E2636", {"start": v(6056.18, 510.94) * mm, "end": v(6029.67, 490.48) * mm});
            skLineSegment(sketch, "E2637", {"start": v(6029.67, 490.48) * mm, "end": v(6003.31, 469.4) * mm});
            skLineSegment(sketch, "E2638", {"start": v(6003.31, 469.4) * mm, "end": v(5977.18, 447.97) * mm});
            skLineSegment(sketch, "E2639", {"start": v(5977.18, 447.97) * mm, "end": v(5951.33, 426.47) * mm});
            skLineSegment(sketch, "E2640", {"start": v(5951.33, 426.47) * mm, "end": v(5925.84, 405.17) * mm});
            skLineSegment(sketch, "E2641", {"start": v(5925.84, 405.17) * mm, "end": v(5900.78, 384.34) * mm});
            skLineSegment(sketch, "E2642", {"start": v(5900.78, 384.34) * mm, "end": v(5876.21, 364.24) * mm});
            skLineSegment(sketch, "E2643", {"start": v(5876.21, 364.24) * mm, "end": v(5852.21, 345.15) * mm});
            skLineSegment(sketch, "E2644", {"start": v(5852.21, 345.15) * mm, "end": v(5828.84, 327.34) * mm});
            skLineSegment(sketch, "E2645", {"start": v(5828.84, 327.34) * mm, "end": v(5806.17, 311.08) * mm});
            skLineSegment(sketch, "E2646", {"start": v(5806.17, 311.08) * mm, "end": v(5784.27, 296.63) * mm});
            skLineSegment(sketch, "E2647", {"start": v(5784.27, 296.63) * mm, "end": v(5763.2, 284.28) * mm});
            skLineSegment(sketch, "E2648", {"start": v(5763.2, 284.28) * mm, "end": v(5743.05, 274.28) * mm});
            skLineSegment(sketch, "E2649", {"start": v(5743.05, 274.28) * mm, "end": v(5723.86, 266.9) * mm});
            skLineSegment(sketch, "E2650", {"start": v(5723.86, 266.9) * mm, "end": v(5705.72, 262.43) * mm});
            skLineSegment(sketch, "E2651", {"start": v(5705.72, 262.43) * mm, "end": v(5688.7, 261.13) * mm});
            skLineSegment(sketch, "E2652", {"start": v(5688.7, 261.13) * mm, "end": v(5672.85, 263.27) * mm});
            skLineSegment(sketch, "E2653", {"start": v(5672.85, 263.27) * mm, "end": v(5658.25, 269.11) * mm});
            skLineSegment(sketch, "E2654", {"start": v(5658.25, 269.11) * mm, "end": v(5644.97, 278.94) * mm});
            skLineSegment(sketch, "E2655", {"start": v(5644.97, 278.94) * mm, "end": v(5633.08, 293.01) * mm});
            skLineSegment(sketch, "E2656", {"start": v(5633.08, 293.01) * mm, "end": v(5622.64, 311.6) * mm});
            skLineSegment(sketch, "E2657", {"start": v(5622.64, 311.6) * mm, "end": v(5613.73, 335) * mm});
            skLineSegment(sketch, "E2658", {"start": v(5613.73, 335) * mm, "end": v(5606.4, 363.44) * mm});
            skLineSegment(sketch, "E2659", {"start": v(5606.4, 363.44) * mm, "end": v(5600.74, 397.22) * mm});
            skLineSegment(sketch, "E2660", {"start": v(5600.74, 397.22) * mm, "end": v(5596.8, 436.6) * mm});
            skLineSegment(sketch, "E2661", {"start": v(5596.8, 436.6) * mm, "end": v(5604.46, 533.71) * mm});
            skLineSegment(sketch, "E2662", {"start": v(5604.46, 533.71) * mm, "end": v(5613.38, 630.22) * mm});
            skLineSegment(sketch, "E2663", {"start": v(5613.38, 630.22) * mm, "end": v(5623.57, 726.12) * mm});
            skLineSegment(sketch, "E2664", {"start": v(5623.57, 726.12) * mm, "end": v(5635.03, 821.46) * mm});
            skLineSegment(sketch, "E2665", {"start": v(5635.03, 821.46) * mm, "end": v(5647.78, 916.25) * mm});
            skLineSegment(sketch, "E2666", {"start": v(5647.78, 916.25) * mm, "end": v(5661.82, 1010.53) * mm});
            skLineSegment(sketch, "E2667", {"start": v(5661.82, 1010.53) * mm, "end": v(5677.16, 1104.31) * mm});
            skLineSegment(sketch, "E2668", {"start": v(5677.16, 1104.31) * mm, "end": v(5693.8, 1197.64) * mm});
            skLineSegment(sketch, "E2669", {"start": v(5693.8, 1197.64) * mm, "end": v(5711.75, 1290.53) * mm});
            skLineSegment(sketch, "E2670", {"start": v(5711.75, 1290.53) * mm, "end": v(5731.01, 1383) * mm});
            skLineSegment(sketch, "E2671", {"start": v(5731.01, 1383) * mm, "end": v(5751.6, 1475.1) * mm});
            skLineSegment(sketch, "E2672", {"start": v(5751.6, 1475.1) * mm, "end": v(5773.52, 1566.84) * mm});
            skLineSegment(sketch, "E2673", {"start": v(5773.52, 1566.84) * mm, "end": v(5796.77, 1658.25) * mm});
            skLineSegment(sketch, "E2674", {"start": v(5796.77, 1658.25) * mm, "end": v(5821.37, 1749.36) * mm});
            skLineSegment(sketch, "E2675", {"start": v(5821.37, 1749.36) * mm, "end": v(5847.31, 1840.19) * mm});
            skLineSegment(sketch, "E2676", {"start": v(5847.31, 1840.19) * mm, "end": v(5874.61, 1930.77) * mm});
            skLineSegment(sketch, "E2677", {"start": v(5874.61, 1930.77) * mm, "end": v(5903.28, 2021.13) * mm});
            skLineSegment(sketch, "E2678", {"start": v(5903.28, 2021.13) * mm, "end": v(5933.3, 2111.29) * mm});
            skLineSegment(sketch, "E2679", {"start": v(5933.3, 2111.29) * mm, "end": v(5964.72, 2201.28) * mm});
            skLineSegment(sketch, "E2680", {"start": v(5964.72, 2201.28) * mm, "end": v(5997.5, 2291.13) * mm});
            skLineSegment(sketch, "E2681", {"start": v(5997.5, 2291.13) * mm, "end": v(6031.68, 2380.86) * mm});
            skLineSegment(sketch, "E2682", {"start": v(6031.68, 2380.86) * mm, "end": v(6067.26, 2470.5) * mm});
            skLineSegment(sketch, "E2683", {"start": v(6067.26, 2470.5) * mm, "end": v(6104.23, 2560.08) * mm});
            skLineSegment(sketch, "E2684", {"start": v(6104.23, 2560.08) * mm, "end": v(6142.61, 2649.62) * mm});
            skLineSegment(sketch, "E2685", {"start": v(-4653.56, 13445.6) * mm, "end": v(-4743.08, 13483.98) * mm});
            skLineSegment(sketch, "E2686", {"start": v(-4743.08, 13483.98) * mm, "end": v(-4832.64, 13520.95) * mm});
            skLineSegment(sketch, "E2687", {"start": v(-4832.64, 13520.95) * mm, "end": v(-4922.26, 13556.52) * mm});
            skLineSegment(sketch, "E2688", {"start": v(-4922.26, 13556.52) * mm, "end": v(-5011.98, 13590.7) * mm});
            skLineSegment(sketch, "E2689", {"start": v(-5011.98, 13590.7) * mm, "end": v(-5101.82, 13623.48) * mm});
            skLineSegment(sketch, "E2690", {"start": v(-5101.82, 13623.48) * mm, "end": v(-5191.8, 13654.88) * mm});
            skLineSegment(sketch, "E2691", {"start": v(-5191.8, 13654.88) * mm, "end": v(-5281.96, 13684.9) * mm});
            skLineSegment(sketch, "E2692", {"start": v(-5281.96, 13684.9) * mm, "end": v(-5372.32, 13713.56) * mm});
            skLineSegment(sketch, "E2693", {"start": v(-5372.32, 13713.56) * mm, "end": v(-5462.9, 13740.85) * mm});
            skLineSegment(sketch, "E2694", {"start": v(-5462.9, 13740.85) * mm, "end": v(-5553.73, 13766.79) * mm});
            skLineSegment(sketch, "E2695", {"start": v(-5553.73, 13766.79) * mm, "end": v(-5644.83, 13791.38) * mm});
            skLineSegment(sketch, "E2696", {"start": v(-5644.83, 13791.38) * mm, "end": v(-5736.24, 13814.63) * mm});
            skLineSegment(sketch, "E2697", {"start": v(-5736.24, 13814.63) * mm, "end": v(-5827.98, 13836.54) * mm});
            skLineSegment(sketch, "E2698", {"start": v(-5827.98, 13836.54) * mm, "end": v(-5920.08, 13857.13) * mm});
            skLineSegment(sketch, "E2699", {"start": v(-5920.08, 13857.13) * mm, "end": v(-6012.56, 13876.4) * mm});
            skLineSegment(sketch, "E2700", {"start": v(-6012.56, 13876.4) * mm, "end": v(-6105.44, 13894.35) * mm});
            skLineSegment(sketch, "E2701", {"start": v(-6105.44, 13894.35) * mm, "end": v(-6198.76, 13911) * mm});
            skLineSegment(sketch, "E2702", {"start": v(-6198.76, 13911) * mm, "end": v(-6292.54, 13926.33) * mm});
            skLineSegment(sketch, "E2703", {"start": v(-6292.54, 13926.33) * mm, "end": v(-6386.81, 13940.38) * mm});
            skLineSegment(sketch, "E2704", {"start": v(-6386.81, 13940.38) * mm, "end": v(-6481.6, 13953.15) * mm});
            skLineSegment(sketch, "E2705", {"start": v(-6481.6, 13953.15) * mm, "end": v(-6576.92, 13964.63) * mm});
            skLineSegment(sketch, "E2706", {"start": v(-6576.92, 13964.63) * mm, "end": v(-6672.81, 13974.84) * mm});
            skLineSegment(sketch, "E2707", {"start": v(-6672.81, 13974.84) * mm, "end": v(-6769.3, 13983.78) * mm});
            skLineSegment(sketch, "E2708", {"start": v(-6769.3, 13983.78) * mm, "end": v(-6866.4, 13991.47) * mm});
            skLineSegment(sketch, "E2709", {"start": v(-6866.4, 13991.47) * mm, "end": v(-6939.58, 13981.83) * mm});
            skLineSegment(sketch, "E2710", {"start": v(-6939.58, 13981.83) * mm, "end": v(-6991.43, 13965.56) * mm});
            skLineSegment(sketch, "E2711", {"start": v(-6991.43, 13965.56) * mm, "end": v(-7024.13, 13943.2) * mm});
            skLineSegment(sketch, "E2712", {"start": v(-7024.13, 13943.2) * mm, "end": v(-7039.82, 13915.3) * mm});
            skLineSegment(sketch, "E2713", {"start": v(-7039.82, 13915.3) * mm, "end": v(-7040.67, 13882.42) * mm});
            skLineSegment(sketch, "E2714", {"start": v(-7040.67, 13882.42) * mm, "end": v(-7028.84, 13845.09) * mm});
            skLineSegment(sketch, "E2715", {"start": v(-7028.84, 13845.09) * mm, "end": v(-7006.49, 13803.86) * mm});
            skLineSegment(sketch, "E2716", {"start": v(-7006.49, 13803.86) * mm, "end": v(-6975.78, 13759.29) * mm});
            skLineSegment(sketch, "E2717", {"start": v(-6975.78, 13759.29) * mm, "end": v(-6938.88, 13711.9) * mm});
            skLineSegment(sketch, "E2718", {"start": v(-6938.88, 13711.9) * mm, "end": v(-6897.94, 13662.28) * mm});
            skLineSegment(sketch, "E2719", {"start": v(-6897.94, 13662.28) * mm, "end": v(-6855.13, 13610.94) * mm});
            skLineSegment(sketch, "E2720", {"start": v(-6855.13, 13610.94) * mm, "end": v(-6812.61, 13558.44) * mm});
            skLineSegment(sketch, "E2721", {"start": v(-6812.61, 13558.44) * mm, "end": v(-6772.55, 13505.34) * mm});
            skLineSegment(sketch, "E2722", {"start": v(-6772.55, 13505.34) * mm, "end": v(-6737.09, 13452.17) * mm});
            skLineSegment(sketch, "E2723", {"start": v(-6737.09, 13452.17) * mm, "end": v(-6708.4, 13399.48) * mm});
            skLineSegment(sketch, "E2724", {"start": v(-6708.4, 13399.48) * mm, "end": v(-6688.66, 13347.83) * mm});
            skLineSegment(sketch, "E2725", {"start": v(-6688.66, 13347.83) * mm, "end": v(-6680, 13297.75) * mm});
            skLineSegment(sketch, "E2726", {"start": v(-6680, 13297.75) * mm, "end": v(-6684.94, 13240.58) * mm});
            skLineSegment(sketch, "E2727", {"start": v(-6684.94, 13240.58) * mm, "end": v(-6697.3, 13174.97) * mm});
            skLineSegment(sketch, "E2728", {"start": v(-6697.3, 13174.97) * mm, "end": v(-6713.33, 13115.79) * mm});
            skLineSegment(sketch, "E2729", {"start": v(-6713.33, 13115.79) * mm, "end": v(-6732.94, 13062.72) * mm});
            skLineSegment(sketch, "E2730", {"start": v(-6732.94, 13062.72) * mm, "end": v(-6756.06, 13015.44) * mm});
            skLineSegment(sketch, "E2731", {"start": v(-6756.06, 13015.44) * mm, "end": v(-6782.6, 12973.63) * mm});
            skLineSegment(sketch, "E2732", {"start": v(-6782.6, 12973.63) * mm, "end": v(-6812.49, 12936.98) * mm});
            skLineSegment(sketch, "E2733", {"start": v(-6812.49, 12936.98) * mm, "end": v(-6845.65, 12905.17) * mm});
            skLineSegment(sketch, "E2734", {"start": v(-6845.65, 12905.17) * mm, "end": v(-6882, 12877.87) * mm});
            skLineSegment(sketch, "E2735", {"start": v(-6882, 12877.87) * mm, "end": v(-6921.47, 12854.78) * mm});
            skLineSegment(sketch, "E2736", {"start": v(-6921.47, 12854.78) * mm, "end": v(-6963.97, 12835.56) * mm});
            skLineSegment(sketch, "E2737", {"start": v(-6963.97, 12835.56) * mm, "end": v(-7009.44, 12819.9) * mm});
            skLineSegment(sketch, "E2738", {"start": v(-7009.44, 12819.9) * mm, "end": v(-7057.78, 12807.49) * mm});
            skLineSegment(sketch, "E2739", {"start": v(-7057.78, 12807.49) * mm, "end": v(-7108.93, 12798) * mm});
            skLineSegment(sketch, "E2740", {"start": v(-7108.93, 12798) * mm, "end": v(-7162.8, 12791.12) * mm});
            skLineSegment(sketch, "E2741", {"start": v(-7162.8, 12791.12) * mm, "end": v(-7219.32, 12786.52) * mm});
            skLineSegment(sketch, "E2742", {"start": v(-7219.32, 12786.52) * mm, "end": v(-7278.4, 12783.9) * mm});
            skLineSegment(sketch, "E2743", {"start": v(-7278.4, 12783.9) * mm, "end": v(-7339.98, 12782.92) * mm});
            skLineSegment(sketch, "E2744", {"start": v(-7339.98, 12782.92) * mm, "end": v(-7402.43, 12783.32) * mm});
            skLineSegment(sketch, "E2745", {"start": v(-7402.43, 12783.32) * mm, "end": v(-7462.53, 12785.25) * mm});
            skLineSegment(sketch, "E2746", {"start": v(-7462.53, 12785.25) * mm, "end": v(-7520.08, 12789.02) * mm});
            skLineSegment(sketch, "E2747", {"start": v(-7520.08, 12789.02) * mm, "end": v(-7575.02, 12794.95) * mm});
            skLineSegment(sketch, "E2748", {"start": v(-7575.02, 12794.95) * mm, "end": v(-7627.26, 12803.36) * mm});
            skLineSegment(sketch, "E2749", {"start": v(-7627.26, 12803.36) * mm, "end": v(-7676.73, 12814.57) * mm});
            skLineSegment(sketch, "E2750", {"start": v(-7676.73, 12814.57) * mm, "end": v(-7723.35, 12828.89) * mm});
            skLineSegment(sketch, "E2751", {"start": v(-7723.35, 12828.89) * mm, "end": v(-7767.04, 12846.64) * mm});
            skLineSegment(sketch, "E2752", {"start": v(-7767.04, 12846.64) * mm, "end": v(-7807.72, 12868.15) * mm});
            skLineSegment(sketch, "E2753", {"start": v(-7807.72, 12868.15) * mm, "end": v(-7845.32, 12893.73) * mm});
            skLineSegment(sketch, "E2754", {"start": v(-7845.32, 12893.73) * mm, "end": v(-7879.75, 12923.7) * mm});
            skLineSegment(sketch, "E2755", {"start": v(-7879.75, 12923.7) * mm, "end": v(-7910.94, 12958.37) * mm});
            skLineSegment(sketch, "E2756", {"start": v(-7910.94, 12958.37) * mm, "end": v(-7938.8, 12998.08) * mm});
            skLineSegment(sketch, "E2757", {"start": v(-7938.8, 12998.08) * mm, "end": v(-7963.28, 13043.13) * mm});
            skLineSegment(sketch, "E2758", {"start": v(-7963.28, 13043.13) * mm, "end": v(-7984.27, 13093.84) * mm});
            skLineSegment(sketch, "E2759", {"start": v(-7984.27, 13093.84) * mm, "end": v(-8001.7, 13150.54) * mm});
            skLineSegment(sketch, "E2760", {"start": v(-8001.7, 13150.54) * mm, "end": v(-8015.5, 13213.54) * mm});
            skLineSegment(sketch, "E2761", {"start": v(-8015.5, 13213.54) * mm, "end": v(-8024.4, 13273.48) * mm});
            skLineSegment(sketch, "E2762", {"start": v(-8024.4, 13273.48) * mm, "end": v(-8024.9, 13297.75) * mm});
            skLineSegment(sketch, "E2763", {"start": v(-8024.9, 13297.75) * mm, "end": v(-8022.1, 13322.56) * mm});
            skLineSegment(sketch, "E2764", {"start": v(-8022.1, 13322.56) * mm, "end": v(-8016.26, 13347.83) * mm});
            skLineSegment(sketch, "E2765", {"start": v(-8016.26, 13347.83) * mm, "end": v(-8007.64, 13373.5) * mm});
            skLineSegment(sketch, "E2766", {"start": v(-8007.64, 13373.5) * mm, "end": v(-7996.52, 13399.48) * mm});
            skLineSegment(sketch, "E2767", {"start": v(-7996.52, 13399.48) * mm, "end": v(-7983.17, 13425.73) * mm});
            skLineSegment(sketch, "E2768", {"start": v(-7983.17, 13425.73) * mm, "end": v(-7967.85, 13452.17) * mm});
            skLineSegment(sketch, "E2769", {"start": v(-7967.85, 13452.17) * mm, "end": v(-7950.84, 13478.73) * mm});
            skLineSegment(sketch, "E2770", {"start": v(-7950.84, 13478.73) * mm, "end": v(-7932.4, 13505.34) * mm});
            skLineSegment(sketch, "E2771", {"start": v(-7932.4, 13505.34) * mm, "end": v(-7912.82, 13531.93) * mm});
            skLineSegment(sketch, "E2772", {"start": v(-7912.82, 13531.93) * mm, "end": v(-7892.35, 13558.44) * mm});
            skLineSegment(sketch, "E2773", {"start": v(-7892.35, 13558.44) * mm, "end": v(-7871.27, 13584.8) * mm});
            skLineSegment(sketch, "E2774", {"start": v(-7871.27, 13584.8) * mm, "end": v(-7849.85, 13610.94) * mm});
            skLineSegment(sketch, "E2775", {"start": v(-7849.85, 13610.94) * mm, "end": v(-7828.35, 13636.79) * mm});
            skLineSegment(sketch, "E2776", {"start": v(-7828.35, 13636.79) * mm, "end": v(-7807.05, 13662.28) * mm});
            skLineSegment(sketch, "E2777", {"start": v(-7807.05, 13662.28) * mm, "end": v(-7786.22, 13687.34) * mm});
            skLineSegment(sketch, "E2778", {"start": v(-7786.22, 13687.34) * mm, "end": v(-7766.13, 13711.9) * mm});
            skLineSegment(sketch, "E2779", {"start": v(-7766.13, 13711.9) * mm, "end": v(-7747.04, 13735.91) * mm});
            skLineSegment(sketch, "E2780", {"start": v(-7747.04, 13735.91) * mm, "end": v(-7729.24, 13759.29) * mm});
            skLineSegment(sketch, "E2781", {"start": v(-7729.24, 13759.29) * mm, "end": v(-7712.98, 13781.96) * mm});
            skLineSegment(sketch, "E2782", {"start": v(-7712.98, 13781.96) * mm, "end": v(-7698.54, 13803.86) * mm});
            skLineSegment(sketch, "E2783", {"start": v(-7698.54, 13803.86) * mm, "end": v(-7686.19, 13824.93) * mm});
            skLineSegment(sketch, "E2784", {"start": v(-7686.19, 13824.93) * mm, "end": v(-7676.2, 13845.09) * mm});
            skLineSegment(sketch, "E2785", {"start": v(-7676.2, 13845.09) * mm, "end": v(-7668.83, 13864.28) * mm});
            skLineSegment(sketch, "E2786", {"start": v(-7668.83, 13864.28) * mm, "end": v(-7664.36, 13882.42) * mm});
            skLineSegment(sketch, "E2787", {"start": v(-7664.36, 13882.42) * mm, "end": v(-7663.06, 13899.45) * mm});
            skLineSegment(sketch, "E2788", {"start": v(-7663.06, 13899.45) * mm, "end": v(-7665.2, 13915.3) * mm});
            skLineSegment(sketch, "E2789", {"start": v(-7665.2, 13915.3) * mm, "end": v(-7671.05, 13929.91) * mm});
            skLineSegment(sketch, "E2790", {"start": v(-7671.05, 13929.91) * mm, "end": v(-7680.88, 13943.2) * mm});
            skLineSegment(sketch, "E2791", {"start": v(-7680.88, 13943.2) * mm, "end": v(-7694.95, 13955.1) * mm});
            skLineSegment(sketch, "E2792", {"start": v(-7694.95, 13955.1) * mm, "end": v(-7713.55, 13965.56) * mm});
            skLineSegment(sketch, "E2793", {"start": v(-7713.55, 13965.56) * mm, "end": v(-7736.93, 13974.5) * mm});
            skLineSegment(sketch, "E2794", {"start": v(-7736.93, 13974.5) * mm, "end": v(-7765.38, 13981.83) * mm});
            skLineSegment(sketch, "E2795", {"start": v(-7765.38, 13981.83) * mm, "end": v(-7799.15, 13987.51) * mm});
            skLineSegment(sketch, "E2796", {"start": v(-7799.15, 13987.51) * mm, "end": v(-7838.52, 13991.47) * mm});
            skLineSegment(sketch, "E2797", {"start": v(-7838.52, 13991.47) * mm, "end": v(-7935.63, 13983.78) * mm});
            skLineSegment(sketch, "E2798", {"start": v(-7935.63, 13983.78) * mm, "end": v(-8032.12, 13974.84) * mm});
            skLineSegment(sketch, "E2799", {"start": v(-8032.12, 13974.84) * mm, "end": v(-8128.01, 13964.63) * mm});
            skLineSegment(sketch, "E2800", {"start": v(-8128.01, 13964.63) * mm, "end": v(-8223.34, 13953.15) * mm});
            skLineSegment(sketch, "E2801", {"start": v(-8223.34, 13953.15) * mm, "end": v(-8318.13, 13940.38) * mm});
            skLineSegment(sketch, "E2802", {"start": v(-8318.13, 13940.38) * mm, "end": v(-8412.4, 13926.33) * mm});
            skLineSegment(sketch, "E2803", {"start": v(-8412.4, 13926.33) * mm, "end": v(-8506.18, 13911) * mm});
            skLineSegment(sketch, "E2804", {"start": v(-8506.18, 13911) * mm, "end": v(-8599.5, 13894.35) * mm});
            skLineSegment(sketch, "E2805", {"start": v(-8599.5, 13894.35) * mm, "end": v(-8692.4, 13876.4) * mm});
            skLineSegment(sketch, "E2806", {"start": v(-8692.4, 13876.4) * mm, "end": v(-8784.88, 13857.13) * mm});
            skLineSegment(sketch, "E2807", {"start": v(-8784.88, 13857.13) * mm, "end": v(-8876.98, 13836.54) * mm});
            skLineSegment(sketch, "E2808", {"start": v(-8876.98, 13836.54) * mm, "end": v(-8968.72, 13814.63) * mm});
            skLineSegment(sketch, "E2809", {"start": v(-8968.72, 13814.63) * mm, "end": v(-9060.13, 13791.38) * mm});
            skLineSegment(sketch, "E2810", {"start": v(-9060.13, 13791.38) * mm, "end": v(-9151.25, 13766.79) * mm});
            skLineSegment(sketch, "E2811", {"start": v(-9151.25, 13766.79) * mm, "end": v(-9242.08, 13740.85) * mm});
            skLineSegment(sketch, "E2812", {"start": v(-9242.08, 13740.85) * mm, "end": v(-9332.67, 13713.56) * mm});
            skLineSegment(sketch, "E2813", {"start": v(-9332.67, 13713.56) * mm, "end": v(-9423.03, 13684.9) * mm});
            skLineSegment(sketch, "E2814", {"start": v(-9423.03, 13684.9) * mm, "end": v(-9513.2, 13654.88) * mm});
            skLineSegment(sketch, "E2815", {"start": v(-9513.2, 13654.88) * mm, "end": v(-9603.2, 13623.48) * mm});
            skLineSegment(sketch, "E2816", {"start": v(-9603.2, 13623.48) * mm, "end": v(-9693.05, 13590.7) * mm});
            skLineSegment(sketch, "E2817", {"start": v(-9693.05, 13590.7) * mm, "end": v(-9782.78, 13556.52) * mm});
            skLineSegment(sketch, "E2818", {"start": v(-9782.78, 13556.52) * mm, "end": v(-9872.43, 13520.95) * mm});
            skLineSegment(sketch, "E2819", {"start": v(-9872.43, 13520.95) * mm, "end": v(-9921.83, 13500.56) * mm});
            skLineSegment(sketch, "E2820", {"start": v(-10051.55, 8047.6) * mm, "end": v(-10141.07, 8085.97) * mm});
            skLineSegment(sketch, "E2821", {"start": v(-10141.07, 8085.97) * mm, "end": v(-10230.63, 8122.92) * mm});
            skLineSegment(sketch, "E2822", {"start": v(-10230.63, 8122.92) * mm, "end": v(-10320.25, 8158.47) * mm});
            skLineSegment(sketch, "E2823", {"start": v(-10320.25, 8158.47) * mm, "end": v(-10409.97, 8192.64) * mm});
            skLineSegment(sketch, "E2824", {"start": v(-10409.97, 8192.64) * mm, "end": v(-10499.81, 8225.4) * mm});
            skLineSegment(sketch, "E2825", {"start": v(-10499.81, 8225.4) * mm, "end": v(-10589.8, 8256.8) * mm});
            skLineSegment(sketch, "E2826", {"start": v(-10589.8, 8256.8) * mm, "end": v(-10679.95, 8286.82) * mm});
            skLineSegment(sketch, "E2827", {"start": v(-10679.95, 8286.82) * mm, "end": v(-10753.16, 8310.04) * mm});
            skLineSegment(sketch, "E2828", {"start": v(-10808.28, 2370.26) * mm, "end": v(-10770.3, 2381.7) * mm});
            skLineSegment(sketch, "E2829", {"start": v(-10770.3, 2381.7) * mm, "end": v(-10679.95, 2410.37) * mm});
            skLineSegment(sketch, "E2830", {"start": v(-10679.95, 2410.37) * mm, "end": v(-10589.8, 2440.4) * mm});
            skLineSegment(sketch, "E2831", {"start": v(-10589.8, 2440.4) * mm, "end": v(-10499.81, 2471.8) * mm});
            skLineSegment(sketch, "E2832", {"start": v(-10499.81, 2471.8) * mm, "end": v(-10409.97, 2504.58) * mm});
            skLineSegment(sketch, "E2833", {"start": v(-10409.97, 2504.58) * mm, "end": v(-10320.25, 2538.75) * mm});
            skLineSegment(sketch, "E2834", {"start": v(-10320.25, 2538.75) * mm, "end": v(-10230.63, 2574.3) * mm});
            skLineSegment(sketch, "E2835", {"start": v(-10230.63, 2574.3) * mm, "end": v(-10141.07, 2611.26) * mm});
            skLineSegment(sketch, "E2836", {"start": v(-10141.07, 2611.26) * mm, "end": v(-10051.55, 2649.62) * mm});
            skLineSegment(sketch, "E2837", {"start": v(-10051.55, -2748.37) * mm, "end": v(-10141.07, -2710.02) * mm});
            skLineSegment(sketch, "E2838", {"start": v(-10141.07, -2710.02) * mm, "end": v(-10230.63, -2673.07) * mm});
            skLineSegment(sketch, "E2839", {"start": v(-10230.63, -2673.07) * mm, "end": v(-10320.25, -2637.52) * mm});
            skLineSegment(sketch, "E2840", {"start": v(-10320.25, -2637.52) * mm, "end": v(-10409.97, -2603.37) * mm});
            skLineSegment(sketch, "E2841", {"start": v(-10409.97, -2603.37) * mm, "end": v(-10499.81, -2570.6) * mm});
            skLineSegment(sketch, "E2842", {"start": v(-10499.81, -2570.6) * mm, "end": v(-10589.8, -2539.2) * mm});
            skLineSegment(sketch, "E2843", {"start": v(-10589.8, -2539.2) * mm, "end": v(-10679.95, -2509.19) * mm});
            skLineSegment(sketch, "E2844", {"start": v(-10679.95, -2509.19) * mm, "end": v(-10770.3, -2480.54) * mm});
            skLineSegment(sketch, "E2845", {"start": v(-10770.3, -2480.54) * mm, "end": v(-10808.28, -2469.1) * mm});
            skLineSegment(sketch, "E2846", {"start": v(-10784.52, -8418.73) * mm, "end": v(-10770.3, -8414.45) * mm});
            skLineSegment(sketch, "E2847", {"start": v(-10770.3, -8414.45) * mm, "end": v(-10679.95, -8385.8) * mm});
            skLineSegment(sketch, "E2848", {"start": v(-10679.95, -8385.8) * mm, "end": v(-10589.8, -8355.78) * mm});
            skLineSegment(sketch, "E2849", {"start": v(-10589.8, -8355.78) * mm, "end": v(-10499.81, -8324.4) * mm});
            skLineSegment(sketch, "E2850", {"start": v(-10499.81, -8324.4) * mm, "end": v(-10409.97, -8291.62) * mm});
            skLineSegment(sketch, "E2851", {"start": v(-10409.97, -8291.62) * mm, "end": v(-10320.25, -8257.46) * mm});
            skLineSegment(sketch, "E2852", {"start": v(-10320.25, -8257.46) * mm, "end": v(-10230.63, -8221.92) * mm});
            skLineSegment(sketch, "E2853", {"start": v(-10230.63, -8221.92) * mm, "end": v(-10141.07, -8184.97) * mm});
            skLineSegment(sketch, "E2854", {"start": v(-10141.07, -8184.97) * mm, "end": v(-10051.55, -8146.62) * mm});
            skLineSegment(sketch, "E2855", {"start": v(-9846.78, -13630.09) * mm, "end": v(-9782.78, -13655.47) * mm});
            skLineSegment(sketch, "E2856", {"start": v(-9782.78, -13655.47) * mm, "end": v(-9693.05, -13689.63) * mm});
            skLineSegment(sketch, "E2857", {"start": v(-9693.05, -13689.63) * mm, "end": v(-9603.2, -13722.4) * mm});
            skLineSegment(sketch, "E2858", {"start": v(-9603.2, -13722.4) * mm, "end": v(-9513.2, -13753.8) * mm});
            skLineSegment(sketch, "E2859", {"start": v(-9513.2, -13753.8) * mm, "end": v(-9423.03, -13783.82) * mm});
            skLineSegment(sketch, "E2860", {"start": v(-9423.03, -13783.82) * mm, "end": v(-9332.67, -13812.47) * mm});
            skLineSegment(sketch, "E2861", {"start": v(-9332.67, -13812.47) * mm, "end": v(-9242.08, -13839.76) * mm});
            skLineSegment(sketch, "E2862", {"start": v(-9242.08, -13839.76) * mm, "end": v(-9151.25, -13865.7) * mm});
            skLineSegment(sketch, "E2863", {"start": v(-9151.25, -13865.7) * mm, "end": v(-9060.13, -13890.29) * mm});
            skLineSegment(sketch, "E2864", {"start": v(-9060.13, -13890.29) * mm, "end": v(-8968.72, -13913.53) * mm});
            skLineSegment(sketch, "E2865", {"start": v(-8968.72, -13913.53) * mm, "end": v(-8876.98, -13935.44) * mm});
            skLineSegment(sketch, "E2866", {"start": v(-8876.98, -13935.44) * mm, "end": v(-8784.88, -13956.03) * mm});
            skLineSegment(sketch, "E2867", {"start": v(-8784.88, -13956.03) * mm, "end": v(-8692.4, -13975.3) * mm});
            skLineSegment(sketch, "E2868", {"start": v(-8692.4, -13975.3) * mm, "end": v(-8599.5, -13993.24) * mm});
            skLineSegment(sketch, "E2869", {"start": v(-8599.5, -13993.24) * mm, "end": v(-8506.18, -14009.87) * mm});
            skLineSegment(sketch, "E2870", {"start": v(-8506.18, -14009.87) * mm, "end": v(-8412.4, -14025.2) * mm});
            skLineSegment(sketch, "E2871", {"start": v(-8412.4, -14025.2) * mm, "end": v(-8318.13, -14039.24) * mm});
            skLineSegment(sketch, "E2872", {"start": v(-8318.13, -14039.24) * mm, "end": v(-8223.34, -14052) * mm});
            skLineSegment(sketch, "E2873", {"start": v(-8223.34, -14052) * mm, "end": v(-8128.01, -14063.46) * mm});
            skLineSegment(sketch, "E2874", {"start": v(-8128.01, -14063.46) * mm, "end": v(-8032.12, -14073.65) * mm});
            skLineSegment(sketch, "E2875", {"start": v(-8032.12, -14073.65) * mm, "end": v(-7935.63, -14082.56) * mm});
            skLineSegment(sketch, "E2876", {"start": v(-7935.63, -14082.56) * mm, "end": v(-7838.52, -14090.22) * mm});
            skLineSegment(sketch, "E2877", {"start": v(-7838.52, -14090.22) * mm, "end": v(-7765.38, -14080.62) * mm});
            skLineSegment(sketch, "E2878", {"start": v(-7765.38, -14080.62) * mm, "end": v(-7713.55, -14064.4) * mm});
            skLineSegment(sketch, "E2879", {"start": v(-7713.55, -14064.4) * mm, "end": v(-7680.88, -14042.07) * mm});
            skLineSegment(sketch, "E2880", {"start": v(-7680.88, -14042.07) * mm, "end": v(-7665.2, -14014.2) * mm});
            skLineSegment(sketch, "E2881", {"start": v(-7665.2, -14014.2) * mm, "end": v(-7664.36, -13981.33) * mm});
            skLineSegment(sketch, "E2882", {"start": v(-7664.36, -13981.33) * mm, "end": v(-7676.2, -13944.02) * mm});
            skLineSegment(sketch, "E2883", {"start": v(-7676.2, -13944.02) * mm, "end": v(-7698.54, -13902.81) * mm});
            skLineSegment(sketch, "E2884", {"start": v(-7698.54, -13902.81) * mm, "end": v(-7729.24, -13858.25) * mm});
            skLineSegment(sketch, "E2885", {"start": v(-7729.24, -13858.25) * mm, "end": v(-7766.13, -13810.89) * mm});
            skLineSegment(sketch, "E2886", {"start": v(-7766.13, -13810.89) * mm, "end": v(-7807.05, -13761.26) * mm});
            skLineSegment(sketch, "E2887", {"start": v(-7807.05, -13761.26) * mm, "end": v(-7849.85, -13709.93) * mm});
            skLineSegment(sketch, "E2888", {"start": v(-7849.85, -13709.93) * mm, "end": v(-7892.35, -13657.44) * mm});
            skLineSegment(sketch, "E2889", {"start": v(-7892.35, -13657.44) * mm, "end": v(-7932.4, -13604.34) * mm});
            skLineSegment(sketch, "E2890", {"start": v(-7932.4, -13604.34) * mm, "end": v(-7967.85, -13551.17) * mm});
            skLineSegment(sketch, "E2891", {"start": v(-7967.85, -13551.17) * mm, "end": v(-7996.52, -13498.49) * mm});
            skLineSegment(sketch, "E2892", {"start": v(-7996.52, -13498.49) * mm, "end": v(-8016.26, -13446.84) * mm});
            skLineSegment(sketch, "E2893", {"start": v(-8016.26, -13446.84) * mm, "end": v(-8024.9, -13396.76) * mm});
            skLineSegment(sketch, "E2894", {"start": v(-8024.9, -13396.76) * mm, "end": v(-8019.98, -13339.57) * mm});
            skLineSegment(sketch, "E2895", {"start": v(-8019.98, -13339.57) * mm, "end": v(-8007.62, -13273.93) * mm});
            skLineSegment(sketch, "E2896", {"start": v(-8007.62, -13273.93) * mm, "end": v(-7991.61, -13214.73) * mm});
            skLineSegment(sketch, "E2897", {"start": v(-7991.61, -13214.73) * mm, "end": v(-7972.02, -13161.63) * mm});
            skLineSegment(sketch, "E2898", {"start": v(-7972.02, -13161.63) * mm, "end": v(-7948.93, -13114.33) * mm});
            skLineSegment(sketch, "E2899", {"start": v(-7948.93, -13114.33) * mm, "end": v(-7922.4, -13072.51) * mm});
            skLineSegment(sketch, "E2900", {"start": v(-7922.4, -13072.51) * mm, "end": v(-7892.53, -13035.85) * mm});
            skLineSegment(sketch, "E2901", {"start": v(-7892.53, -13035.85) * mm, "end": v(-7859.4, -13004.02) * mm});
            skLineSegment(sketch, "E2902", {"start": v(-7859.4, -13004.02) * mm, "end": v(-7823.06, -12976.71) * mm});
            skLineSegment(sketch, "E2903", {"start": v(-7823.06, -12976.71) * mm, "end": v(-7783.61, -12953.6) * mm});
            skLineSegment(sketch, "E2904", {"start": v(-7783.61, -12953.6) * mm, "end": v(-7741.12, -12934.39) * mm});
            skLineSegment(sketch, "E2905", {"start": v(-7741.12, -12934.39) * mm, "end": v(-7695.68, -12918.73) * mm});
            skLineSegment(sketch, "E2906", {"start": v(-7695.68, -12918.73) * mm, "end": v(-7647.35, -12906.3) * mm});
            skLineSegment(sketch, "E2907", {"start": v(-7647.35, -12906.3) * mm, "end": v(-7596.22, -12896.82) * mm});
            skLineSegment(sketch, "E2908", {"start": v(-7596.22, -12896.82) * mm, "end": v(-7542.36, -12889.93) * mm});
            skLineSegment(sketch, "E2909", {"start": v(-7542.36, -12889.93) * mm, "end": v(-7485.85, -12885.34) * mm});
            skLineSegment(sketch, "E2910", {"start": v(-7485.85, -12885.34) * mm, "end": v(-7426.77, -12882.7) * mm});
            skLineSegment(sketch, "E2911", {"start": v(-7426.77, -12882.7) * mm, "end": v(-7365.2, -12881.73) * mm});
            skLineSegment(sketch, "E2912", {"start": v(-7365.2, -12881.73) * mm, "end": v(-7302.74, -12882.14) * mm});
            skLineSegment(sketch, "E2913", {"start": v(-7302.74, -12882.14) * mm, "end": v(-7242.65, -12884.07) * mm});
            skLineSegment(sketch, "E2914", {"start": v(-7242.65, -12884.07) * mm, "end": v(-7185.1, -12887.84) * mm});
            skLineSegment(sketch, "E2915", {"start": v(-7185.1, -12887.84) * mm, "end": v(-7130.15, -12893.77) * mm});
            skLineSegment(sketch, "E2916", {"start": v(-7130.15, -12893.77) * mm, "end": v(-7077.9, -12902.18) * mm});
            skLineSegment(sketch, "E2917", {"start": v(-7077.9, -12902.18) * mm, "end": v(-7028.43, -12913.39) * mm});
            skLineSegment(sketch, "E2918", {"start": v(-7028.43, -12913.39) * mm, "end": v(-6981.8, -12927.71) * mm});
            skLineSegment(sketch, "E2919", {"start": v(-6981.8, -12927.71) * mm, "end": v(-6938.1, -12945.47) * mm});
            skLineSegment(sketch, "E2920", {"start": v(-6938.1, -12945.47) * mm, "end": v(-6897.42, -12966.99) * mm});
            skLineSegment(sketch, "E2921", {"start": v(-6897.42, -12966.99) * mm, "end": v(-6859.8, -12992.57) * mm});
            skLineSegment(sketch, "E2922", {"start": v(-6859.8, -12992.57) * mm, "end": v(-6825.36, -13022.55) * mm});
            skLineSegment(sketch, "E2923", {"start": v(-6825.36, -13022.55) * mm, "end": v(-6794.15, -13057.24) * mm});
            skLineSegment(sketch, "E2924", {"start": v(-6794.15, -13057.24) * mm, "end": v(-6766.27, -13096.97) * mm});
            skLineSegment(sketch, "E2925", {"start": v(-6766.27, -13096.97) * mm, "end": v(-6741.77, -13142.04) * mm});
            skLineSegment(sketch, "E2926", {"start": v(-6741.77, -13142.04) * mm, "end": v(-6720.75, -13192.77) * mm});
            skLineSegment(sketch, "E2927", {"start": v(-6720.75, -13192.77) * mm, "end": v(-6703.28, -13249.5) * mm});
            skLineSegment(sketch, "E2928", {"start": v(-6703.28, -13249.5) * mm, "end": v(-6689.44, -13312.53) * mm});
            skLineSegment(sketch, "E2929", {"start": v(-6689.44, -13312.53) * mm, "end": v(-6680.52, -13372.49) * mm});
            skLineSegment(sketch, "E2930", {"start": v(-6680.52, -13372.49) * mm, "end": v(-6680, -13396.76) * mm});
            skLineSegment(sketch, "E2931", {"start": v(-6680, -13396.76) * mm, "end": v(-6682.8, -13421.57) * mm});
            skLineSegment(sketch, "E2932", {"start": v(-6682.8, -13421.57) * mm, "end": v(-6688.66, -13446.84) * mm});
            skLineSegment(sketch, "E2933", {"start": v(-6688.66, -13446.84) * mm, "end": v(-6697.28, -13472.5) * mm});
            skLineSegment(sketch, "E2934", {"start": v(-6697.28, -13472.5) * mm, "end": v(-6708.4, -13498.49) * mm});
            skLineSegment(sketch, "E2935", {"start": v(-6708.4, -13498.49) * mm, "end": v(-6721.77, -13524.74) * mm});
            skLineSegment(sketch, "E2936", {"start": v(-6721.77, -13524.74) * mm, "end": v(-6737.09, -13551.17) * mm});
            skLineSegment(sketch, "E2937", {"start": v(-6737.09, -13551.17) * mm, "end": v(-6754.1, -13577.73) * mm});
            skLineSegment(sketch, "E2938", {"start": v(-6754.1, -13577.73) * mm, "end": v(-6772.55, -13604.34) * mm});
            skLineSegment(sketch, "E2939", {"start": v(-6772.55, -13604.34) * mm, "end": v(-6792.14, -13630.93) * mm});
            skLineSegment(sketch, "E2940", {"start": v(-6792.14, -13630.93) * mm, "end": v(-6812.61, -13657.44) * mm});
            skLineSegment(sketch, "E2941", {"start": v(-6812.61, -13657.44) * mm, "end": v(-6833.7, -13683.8) * mm});
            skLineSegment(sketch, "E2942", {"start": v(-6833.7, -13683.8) * mm, "end": v(-6855.13, -13709.93) * mm});
            skLineSegment(sketch, "E2943", {"start": v(-6855.13, -13709.93) * mm, "end": v(-6876.64, -13735.78) * mm});
            skLineSegment(sketch, "E2944", {"start": v(-6876.64, -13735.78) * mm, "end": v(-6897.94, -13761.26) * mm});
            skLineSegment(sketch, "E2945", {"start": v(-6897.94, -13761.26) * mm, "end": v(-6918.78, -13786.32) * mm});
            skLineSegment(sketch, "E2946", {"start": v(-6918.78, -13786.32) * mm, "end": v(-6938.88, -13810.89) * mm});
            skLineSegment(sketch, "E2947", {"start": v(-6938.88, -13810.89) * mm, "end": v(-6957.97, -13834.89) * mm});
            skLineSegment(sketch, "E2948", {"start": v(-6957.97, -13834.89) * mm, "end": v(-6975.78, -13858.25) * mm});
            skLineSegment(sketch, "E2949", {"start": v(-6975.78, -13858.25) * mm, "end": v(-6992.04, -13880.92) * mm});
            skLineSegment(sketch, "E2950", {"start": v(-6992.04, -13880.92) * mm, "end": v(-7006.49, -13902.81) * mm});
            skLineSegment(sketch, "E2951", {"start": v(-7006.49, -13902.81) * mm, "end": v(-7018.84, -13923.87) * mm});
            skLineSegment(sketch, "E2952", {"start": v(-7018.84, -13923.87) * mm, "end": v(-7028.84, -13944.02) * mm});
            skLineSegment(sketch, "E2953", {"start": v(-7028.84, -13944.02) * mm, "end": v(-7036.2, -13963.2) * mm});
            skLineSegment(sketch, "E2954", {"start": v(-7036.2, -13963.2) * mm, "end": v(-7040.67, -13981.33) * mm});
            skLineSegment(sketch, "E2955", {"start": v(-7040.67, -13981.33) * mm, "end": v(-7041.96, -13998.36) * mm});
            skLineSegment(sketch, "E2956", {"start": v(-7041.96, -13998.36) * mm, "end": v(-7039.82, -14014.2) * mm});
            skLineSegment(sketch, "E2957", {"start": v(-7039.82, -14014.2) * mm, "end": v(-7033.96, -14028.8) * mm});
            skLineSegment(sketch, "E2958", {"start": v(-7033.96, -14028.8) * mm, "end": v(-7024.13, -14042.07) * mm});
            skLineSegment(sketch, "E2959", {"start": v(-7024.13, -14042.07) * mm, "end": v(-7010.04, -14053.95) * mm});
            skLineSegment(sketch, "E2960", {"start": v(-7010.04, -14053.95) * mm, "end": v(-6991.43, -14064.4) * mm});
            skLineSegment(sketch, "E2961", {"start": v(-6991.43, -14064.4) * mm, "end": v(-6968.04, -14073.3) * mm});
            skLineSegment(sketch, "E2962", {"start": v(-6968.04, -14073.3) * mm, "end": v(-6939.58, -14080.62) * mm});
            skLineSegment(sketch, "E2963", {"start": v(-6939.58, -14080.62) * mm, "end": v(-6905.79, -14086.28) * mm});
            skLineSegment(sketch, "E2964", {"start": v(-6905.79, -14086.28) * mm, "end": v(-6866.4, -14090.22) * mm});
            skLineSegment(sketch, "E2965", {"start": v(-6866.4, -14090.22) * mm, "end": v(-6769.3, -14082.56) * mm});
            skLineSegment(sketch, "E2966", {"start": v(-6769.3, -14082.56) * mm, "end": v(-6672.81, -14073.65) * mm});
            skLineSegment(sketch, "E2967", {"start": v(-6672.81, -14073.65) * mm, "end": v(-6576.92, -14063.46) * mm});
            skLineSegment(sketch, "E2968", {"start": v(-6576.92, -14063.46) * mm, "end": v(-6481.6, -14052) * mm});
            skLineSegment(sketch, "E2969", {"start": v(-6481.6, -14052) * mm, "end": v(-6386.81, -14039.24) * mm});
            skLineSegment(sketch, "E2970", {"start": v(-6386.81, -14039.24) * mm, "end": v(-6292.54, -14025.2) * mm});
            skLineSegment(sketch, "E2971", {"start": v(-6292.54, -14025.2) * mm, "end": v(-6198.76, -14009.87) * mm});
            skLineSegment(sketch, "E2972", {"start": v(-6198.76, -14009.87) * mm, "end": v(-6105.44, -13993.24) * mm});
            skLineSegment(sketch, "E2973", {"start": v(-6105.44, -13993.24) * mm, "end": v(-6012.56, -13975.3) * mm});
            skLineSegment(sketch, "E2974", {"start": v(-6012.56, -13975.3) * mm, "end": v(-5920.08, -13956.03) * mm});
            skLineSegment(sketch, "E2975", {"start": v(-5920.08, -13956.03) * mm, "end": v(-5827.98, -13935.44) * mm});
            skLineSegment(sketch, "E2976", {"start": v(-5827.98, -13935.44) * mm, "end": v(-5736.24, -13913.53) * mm});
            skLineSegment(sketch, "E2977", {"start": v(-5736.24, -13913.53) * mm, "end": v(-5644.83, -13890.29) * mm});
            skLineSegment(sketch, "E2978", {"start": v(-5644.83, -13890.29) * mm, "end": v(-5553.73, -13865.7) * mm});
            skLineSegment(sketch, "E2979", {"start": v(-5553.73, -13865.7) * mm, "end": v(-5462.9, -13839.76) * mm});
            skLineSegment(sketch, "E2980", {"start": v(-5462.9, -13839.76) * mm, "end": v(-5372.32, -13812.47) * mm});
            skLineSegment(sketch, "E2981", {"start": v(-5372.32, -13812.47) * mm, "end": v(-5281.96, -13783.82) * mm});
            skLineSegment(sketch, "E2982", {"start": v(-5281.96, -13783.82) * mm, "end": v(-5191.8, -13753.8) * mm});
            skLineSegment(sketch, "E2983", {"start": v(-5191.8, -13753.8) * mm, "end": v(-5101.82, -13722.4) * mm});
            skLineSegment(sketch, "E2984", {"start": v(-5101.82, -13722.4) * mm, "end": v(-5011.98, -13689.63) * mm});
            skLineSegment(sketch, "E2985", {"start": v(-5011.98, -13689.63) * mm, "end": v(-4922.26, -13655.47) * mm});
            skLineSegment(sketch, "E2986", {"start": v(-4922.26, -13655.47) * mm, "end": v(-4832.64, -13619.92) * mm});
            skLineSegment(sketch, "E2987", {"start": v(-4832.64, -13619.92) * mm, "end": v(-4743.08, -13582.97) * mm});
            skLineSegment(sketch, "E2988", {"start": v(-4743.08, -13582.97) * mm, "end": v(-4653.56, -13544.6) * mm});
            skLineSegment(sketch, "E2989", {"start": v(6142.61, 8047.6) * mm, "end": v(6104.23, 8137.13) * mm});
            skLineSegment(sketch, "E2990", {"start": v(6104.23, 8137.13) * mm, "end": v(6067.26, 8226.69) * mm});
            skLineSegment(sketch, "E2991", {"start": v(6067.26, 8226.69) * mm, "end": v(6031.68, 8316.31) * mm});
            skLineSegment(sketch, "E2992", {"start": v(6031.68, 8316.31) * mm, "end": v(5997.5, 8406.03) * mm});
            skLineSegment(sketch, "E2993", {"start": v(5997.5, 8406.03) * mm, "end": v(5964.72, 8495.87) * mm});
            skLineSegment(sketch, "E2994", {"start": v(5964.72, 8495.87) * mm, "end": v(5933.3, 8585.86) * mm});
            skLineSegment(sketch, "E2995", {"start": v(5933.3, 8585.86) * mm, "end": v(5903.28, 8676.02) * mm});
            skLineSegment(sketch, "E2996", {"start": v(5903.28, 8676.02) * mm, "end": v(5874.61, 8766.37) * mm});
            skLineSegment(sketch, "E2997", {"start": v(5874.61, 8766.37) * mm, "end": v(5847.31, 8856.96) * mm});
            skLineSegment(sketch, "E2998", {"start": v(5847.31, 8856.96) * mm, "end": v(5821.37, 8947.79) * mm});
            skLineSegment(sketch, "E2999", {"start": v(5821.37, 8947.79) * mm, "end": v(5796.77, 9038.9) * mm});
            skLineSegment(sketch, "E3000", {"start": v(5796.77, 9038.9) * mm, "end": v(5773.52, 9130.32) * mm});
            skLineSegment(sketch, "E3001", {"start": v(5773.52, 9130.32) * mm, "end": v(5751.6, 9222.06) * mm});
            skLineSegment(sketch, "E3002", {"start": v(5751.6, 9222.06) * mm, "end": v(5731.01, 9314.17) * mm});
            skLineSegment(sketch, "E3003", {"start": v(5731.01, 9314.17) * mm, "end": v(5711.75, 9406.65) * mm});
            skLineSegment(sketch, "E3004", {"start": v(5711.75, 9406.65) * mm, "end": v(5693.8, 9499.55) * mm});
            skLineSegment(sketch, "E3005", {"start": v(5693.8, 9499.55) * mm, "end": v(5677.16, 9592.88) * mm});
            skLineSegment(sketch, "E3006", {"start": v(5677.16, 9592.88) * mm, "end": v(5661.82, 9686.68) * mm});
            skLineSegment(sketch, "E3007", {"start": v(5661.82, 9686.68) * mm, "end": v(5647.78, 9780.96) * mm});
            skLineSegment(sketch, "E3008", {"start": v(5647.78, 9780.96) * mm, "end": v(5635.03, 9875.76) * mm});
            skLineSegment(sketch, "E3009", {"start": v(5635.03, 9875.76) * mm, "end": v(5623.57, 9971.1) * mm});
            skLineSegment(sketch, "E3010", {"start": v(5623.57, 9971.1) * mm, "end": v(5613.38, 10067) * mm});
            skLineSegment(sketch, "E3011", {"start": v(5613.38, 10067) * mm, "end": v(5604.46, 10163.51) * mm});
            skLineSegment(sketch, "E3012", {"start": v(5604.46, 10163.51) * mm, "end": v(5596.8, 10260.64) * mm});
            skLineSegment(sketch, "E3013", {"start": v(5596.8, 10260.64) * mm, "end": v(5606.4, 10333.79) * mm});
            skLineSegment(sketch, "E3014", {"start": v(5606.4, 10333.79) * mm, "end": v(5622.64, 10385.62) * mm});
            skLineSegment(sketch, "E3015", {"start": v(5622.64, 10385.62) * mm, "end": v(5644.97, 10418.29) * mm});
            skLineSegment(sketch, "E3016", {"start": v(5644.97, 10418.29) * mm, "end": v(5672.85, 10433.96) * mm});
            skLineSegment(sketch, "E3017", {"start": v(5672.85, 10433.96) * mm, "end": v(5705.73, 10434.8) * mm});
            skLineSegment(sketch, "E3018", {"start": v(5705.73, 10434.8) * mm, "end": v(5743.05, 10422.95) * mm});
            skLineSegment(sketch, "E3019", {"start": v(5743.05, 10422.95) * mm, "end": v(5784.28, 10400.6) * mm});
            skLineSegment(sketch, "E3020", {"start": v(5784.28, 10400.6) * mm, "end": v(5828.86, 10369.88) * mm});
            skLineSegment(sketch, "E3021", {"start": v(5828.86, 10369.88) * mm, "end": v(5876.24, 10332.98) * mm});
            skLineSegment(sketch, "E3022", {"start": v(5876.24, 10332.98) * mm, "end": v(5925.88, 10292.04) * mm});
            skLineSegment(sketch, "E3023", {"start": v(5925.88, 10292.04) * mm, "end": v(5977.22, 10249.24) * mm});
            skLineSegment(sketch, "E3024", {"start": v(5977.22, 10249.24) * mm, "end": v(6029.73, 10206.73) * mm});
            skLineSegment(sketch, "E3025", {"start": v(6029.73, 10206.73) * mm, "end": v(6082.85, 10166.68) * mm});
            skLineSegment(sketch, "E3026", {"start": v(6082.85, 10166.68) * mm, "end": v(6136.03, 10131.24) * mm});
            skLineSegment(sketch, "E3027", {"start": v(6136.03, 10131.24) * mm, "end": v(6188.72, 10102.58) * mm});
            skLineSegment(sketch, "E3028", {"start": v(6188.72, 10102.58) * mm, "end": v(6240.38, 10082.85) * mm});
            skLineSegment(sketch, "E3029", {"start": v(6240.38, 10082.85) * mm, "end": v(6290.46, 10074.23) * mm});
            skLineSegment(sketch, "E3030", {"start": v(6290.46, 10074.23) * mm, "end": v(6347.63, 10079.17) * mm});
            skLineSegment(sketch, "E3031", {"start": v(6347.63, 10079.17) * mm, "end": v(6413.24, 10091.5) * mm});
            skLineSegment(sketch, "E3032", {"start": v(6413.24, 10091.5) * mm, "end": v(6472.42, 10107.48) * mm});
            skLineSegment(sketch, "E3033", {"start": v(6472.42, 10107.48) * mm, "end": v(6525.5, 10127.06) * mm});
            skLineSegment(sketch, "E3034", {"start": v(6525.5, 10127.06) * mm, "end": v(6572.77, 10150.15) * mm});
            skLineSegment(sketch, "E3035", {"start": v(6572.77, 10150.15) * mm, "end": v(6614.58, 10176.67) * mm});
            skLineSegment(sketch, "E3036", {"start": v(6614.58, 10176.67) * mm, "end": v(6651.23, 10206.54) * mm});
            skLineSegment(sketch, "E3037", {"start": v(6651.23, 10206.54) * mm, "end": v(6683.04, 10239.68) * mm});
            skLineSegment(sketch, "E3038", {"start": v(6683.04, 10239.68) * mm, "end": v(6710.34, 10276.02) * mm});
            skLineSegment(sketch, "E3039", {"start": v(6710.34, 10276.02) * mm, "end": v(6733.44, 10315.48) * mm});
            skLineSegment(sketch, "E3040", {"start": v(6733.44, 10315.48) * mm, "end": v(6752.65, 10357.98) * mm});
            skLineSegment(sketch, "E3041", {"start": v(6752.65, 10357.98) * mm, "end": v(6768.3, 10403.43) * mm});
            skLineSegment(sketch, "E3042", {"start": v(6768.3, 10403.43) * mm, "end": v(6780.72, 10451.77) * mm});
            skLineSegment(sketch, "E3043", {"start": v(6780.72, 10451.77) * mm, "end": v(6790.21, 10502.92) * mm});
            skLineSegment(sketch, "E3044", {"start": v(6790.21, 10502.92) * mm, "end": v(6797.1, 10556.78) * mm});
            skLineSegment(sketch, "E3045", {"start": v(6797.1, 10556.78) * mm, "end": v(6801.69, 10613.3) * mm});
            skLineSegment(sketch, "E3046", {"start": v(6801.69, 10613.3) * mm, "end": v(6804.32, 10672.39) * mm});
            skLineSegment(sketch, "E3047", {"start": v(6804.32, 10672.39) * mm, "end": v(6805.3, 10733.96) * mm});
            skLineSegment(sketch, "E3048", {"start": v(6805.3, 10733.96) * mm, "end": v(6804.89, 10796.42) * mm});
            skLineSegment(sketch, "E3049", {"start": v(6804.89, 10796.42) * mm, "end": v(6802.96, 10856.51) * mm});
            skLineSegment(sketch, "E3050", {"start": v(6802.96, 10856.51) * mm, "end": v(6799.19, 10914.06) * mm});
            skLineSegment(sketch, "E3051", {"start": v(6799.19, 10914.06) * mm, "end": v(6793.26, 10969) * mm});
            skLineSegment(sketch, "E3052", {"start": v(6793.26, 10969) * mm, "end": v(6784.85, 11021.25) * mm});
            skLineSegment(sketch, "E3053", {"start": v(6784.85, 11021.25) * mm, "end": v(6773.64, 11070.72) * mm});
            skLineSegment(sketch, "E3054", {"start": v(6773.64, 11070.72) * mm, "end": v(6759.31, 11117.34) * mm});
            skLineSegment(sketch, "E3055", {"start": v(6759.31, 11117.34) * mm, "end": v(6741.55, 11161.03) * mm});
            skLineSegment(sketch, "E3056", {"start": v(6741.55, 11161.03) * mm, "end": v(6720.04, 11201.72) * mm});
            skLineSegment(sketch, "E3057", {"start": v(6720.04, 11201.72) * mm, "end": v(6694.45, 11239.31) * mm});
            skLineSegment(sketch, "E3058", {"start": v(6694.45, 11239.31) * mm, "end": v(6664.47, 11273.75) * mm});
            skLineSegment(sketch, "E3059", {"start": v(6664.47, 11273.75) * mm, "end": v(6629.78, 11304.94) * mm});
            skLineSegment(sketch, "E3060", {"start": v(6629.78, 11304.94) * mm, "end": v(6590.06, 11332.82) * mm});
            skLineSegment(sketch, "E3061", {"start": v(6590.06, 11332.82) * mm, "end": v(6545, 11357.3) * mm});
            skLineSegment(sketch, "E3062", {"start": v(6545, 11357.3) * mm, "end": v(6494.25, 11378.3) * mm});
            skLineSegment(sketch, "E3063", {"start": v(6494.25, 11378.3) * mm, "end": v(6437.53, 11395.73) * mm});
            skLineSegment(sketch, "E3064", {"start": v(6437.53, 11395.73) * mm, "end": v(6374.5, 11409.54) * mm});
            skLineSegment(sketch, "E3065", {"start": v(6374.5, 11409.54) * mm, "end": v(6314.54, 11418.45) * mm});
            skLineSegment(sketch, "E3066", {"start": v(6314.54, 11418.45) * mm, "end": v(6290.28, 11418.98) * mm});
            skLineSegment(sketch, "E3067", {"start": v(6290.28, 11418.98) * mm, "end": v(6265.5, 11416.19) * mm});
            skLineSegment(sketch, "E3068", {"start": v(6265.5, 11416.19) * mm, "end": v(6240.23, 11410.35) * mm});
            skLineSegment(sketch, "E3069", {"start": v(6240.23, 11410.35) * mm, "end": v(6214.58, 11401.75) * mm});
            skLineSegment(sketch, "E3070", {"start": v(6214.58, 11401.75) * mm, "end": v(6188.6, 11390.63) * mm});
            skLineSegment(sketch, "E3071", {"start": v(6188.6, 11390.63) * mm, "end": v(6162.36, 11377.28) * mm});
            skLineSegment(sketch, "E3072", {"start": v(6162.36, 11377.28) * mm, "end": v(6135.93, 11361.97) * mm});
            skLineSegment(sketch, "E3073", {"start": v(6135.93, 11361.97) * mm, "end": v(6109.37, 11344.96) * mm});
            skLineSegment(sketch, "E3074", {"start": v(6109.37, 11344.96) * mm, "end": v(6082.77, 11326.53) * mm});
            skLineSegment(sketch, "E3075", {"start": v(6082.77, 11326.53) * mm, "end": v(6056.18, 11306.95) * mm});
            skLineSegment(sketch, "E3076", {"start": v(6056.18, 11306.95) * mm, "end": v(6029.67, 11286.48) * mm});
            skLineSegment(sketch, "E3077", {"start": v(6029.67, 11286.48) * mm, "end": v(6003.31, 11265.4) * mm});
            skLineSegment(sketch, "E3078", {"start": v(6003.31, 11265.4) * mm, "end": v(5977.18, 11243.98) * mm});
            skLineSegment(sketch, "E3079", {"start": v(5977.18, 11243.98) * mm, "end": v(5951.33, 11222.48) * mm});
            skLineSegment(sketch, "E3080", {"start": v(5951.33, 11222.48) * mm, "end": v(5925.84, 11201.18) * mm});
            skLineSegment(sketch, "E3081", {"start": v(5925.84, 11201.18) * mm, "end": v(5900.78, 11180.35) * mm});
            skLineSegment(sketch, "E3082", {"start": v(5900.78, 11180.35) * mm, "end": v(5876.21, 11160.25) * mm});
            skLineSegment(sketch, "E3083", {"start": v(5876.21, 11160.25) * mm, "end": v(5852.21, 11141.17) * mm});
            skLineSegment(sketch, "E3084", {"start": v(5852.21, 11141.17) * mm, "end": v(5828.84, 11123.36) * mm});
            skLineSegment(sketch, "E3085", {"start": v(5828.84, 11123.36) * mm, "end": v(5806.17, 11107.1) * mm});
            skLineSegment(sketch, "E3086", {"start": v(5806.17, 11107.1) * mm, "end": v(5784.27, 11092.66) * mm});
            skLineSegment(sketch, "E3087", {"start": v(5784.27, 11092.66) * mm, "end": v(5763.2, 11080.3) * mm});
            skLineSegment(sketch, "E3088", {"start": v(5763.2, 11080.3) * mm, "end": v(5743.05, 11070.31) * mm});
            skLineSegment(sketch, "E3089", {"start": v(5743.05, 11070.31) * mm, "end": v(5723.86, 11062.95) * mm});
            skLineSegment(sketch, "E3090", {"start": v(5723.86, 11062.95) * mm, "end": v(5705.72, 11058.48) * mm});
            skLineSegment(sketch, "E3091", {"start": v(5705.72, 11058.48) * mm, "end": v(5688.7, 11057.2) * mm});
            skLineSegment(sketch, "E3092", {"start": v(5688.7, 11057.2) * mm, "end": v(5672.85, 11059.34) * mm});
            skLineSegment(sketch, "E3093", {"start": v(5672.85, 11059.34) * mm, "end": v(5658.25, 11065.2) * mm});
            skLineSegment(sketch, "E3094", {"start": v(5658.25, 11065.2) * mm, "end": v(5644.97, 11075.03) * mm});
            skLineSegment(sketch, "E3095", {"start": v(5644.97, 11075.03) * mm, "end": v(5633.08, 11089.11) * mm});
            skLineSegment(sketch, "E3096", {"start": v(5633.08, 11089.11) * mm, "end": v(5622.64, 11107.72) * mm});
            skLineSegment(sketch, "E3097", {"start": v(5622.64, 11107.72) * mm, "end": v(5613.73, 11131.12) * mm});
            skLineSegment(sketch, "E3098", {"start": v(5613.73, 11131.12) * mm, "end": v(5606.4, 11159.58) * mm});
            skLineSegment(sketch, "E3099", {"start": v(5606.4, 11159.58) * mm, "end": v(5600.74, 11193.37) * mm});
            skLineSegment(sketch, "E3100", {"start": v(5600.74, 11193.37) * mm, "end": v(5596.8, 11232.76) * mm});
            skLineSegment(sketch, "E3101", {"start": v(5596.8, 11232.76) * mm, "end": v(5604.46, 11329.86) * mm});
            skLineSegment(sketch, "E3102", {"start": v(5604.46, 11329.86) * mm, "end": v(5613.38, 11426.34) * mm});
            skLineSegment(sketch, "E3103", {"start": v(5613.38, 11426.34) * mm, "end": v(5623.57, 11522.23) * mm});
            skLineSegment(sketch, "E3104", {"start": v(5623.57, 11522.23) * mm, "end": v(5635.03, 11617.55) * mm});
            skLineSegment(sketch, "E3105", {"start": v(5635.03, 11617.55) * mm, "end": v(5647.78, 11712.32) * mm});
            skLineSegment(sketch, "E3106", {"start": v(5647.78, 11712.32) * mm, "end": v(5661.82, 11806.59) * mm});
            skLineSegment(sketch, "E3107", {"start": v(5661.82, 11806.59) * mm, "end": v(5677.16, 11900.36) * mm});
            skLineSegment(sketch, "E3108", {"start": v(5677.16, 11900.36) * mm, "end": v(5693.8, 11993.67) * mm});
            skLineSegment(sketch, "E3109", {"start": v(5693.8, 11993.67) * mm, "end": v(5711.75, 12086.55) * mm});
            skLineSegment(sketch, "E3110", {"start": v(5711.75, 12086.55) * mm, "end": v(5731.01, 12179.02) * mm});
            skLineSegment(sketch, "E3111", {"start": v(5731.01, 12179.02) * mm, "end": v(5751.6, 12271.1) * mm});
            skLineSegment(sketch, "E3112", {"start": v(5751.6, 12271.1) * mm, "end": v(5773.52, 12362.84) * mm});
            skLineSegment(sketch, "E3113", {"start": v(5773.52, 12362.84) * mm, "end": v(5796.77, 12454.25) * mm});
            skLineSegment(sketch, "E3114", {"start": v(5796.77, 12454.25) * mm, "end": v(5821.37, 12545.35) * mm});
            skLineSegment(sketch, "E3115", {"start": v(5821.37, 12545.35) * mm, "end": v(5847.31, 12636.18) * mm});
            skLineSegment(sketch, "E3116", {"start": v(5847.31, 12636.18) * mm, "end": v(5874.61, 12726.75) * mm});
            skLineSegment(sketch, "E3117", {"start": v(5874.61, 12726.75) * mm, "end": v(5903.28, 12817.1) * mm});
            skLineSegment(sketch, "E3118", {"start": v(5903.28, 12817.1) * mm, "end": v(5933.3, 12907.27) * mm});
            skLineSegment(sketch, "E3119", {"start": v(5933.3, 12907.27) * mm, "end": v(5964.72, 12997.26) * mm});
            skLineSegment(sketch, "E3120", {"start": v(5964.72, 12997.26) * mm, "end": v(5997.5, 13087.1) * mm});
            skLineSegment(sketch, "E3121", {"start": v(5997.5, 13087.1) * mm, "end": v(6031.68, 13176.84) * mm});
            skLineSegment(sketch, "E3122", {"start": v(6031.68, 13176.84) * mm, "end": v(6067.26, 13266.48) * mm});
            skLineSegment(sketch, "E3123", {"start": v(6067.26, 13266.48) * mm, "end": v(6104.23, 13356.06) * mm});
            skLineSegment(sketch, "E3124", {"start": v(6104.23, 13356.06) * mm, "end": v(6142.61, 13445.6) * mm});
            skLineSegment(sketch, "E3125", {"start": v(6142.61, 13445.6) * mm, "end": v(6053.07, 13483.98) * mm});
            skLineSegment(sketch, "E3126", {"start": v(6053.07, 13483.98) * mm, "end": v(5963.49, 13520.95) * mm});
            skLineSegment(sketch, "E3127", {"start": v(5963.49, 13520.95) * mm, "end": v(5873.84, 13556.52) * mm});
            skLineSegment(sketch, "E3128", {"start": v(5873.84, 13556.52) * mm, "end": v(5784.1, 13590.7) * mm});
            skLineSegment(sketch, "E3129", {"start": v(5784.1, 13590.7) * mm, "end": v(5694.25, 13623.48) * mm});
            skLineSegment(sketch, "E3130", {"start": v(5694.25, 13623.48) * mm, "end": v(5604.25, 13654.88) * mm});
            skLineSegment(sketch, "E3131", {"start": v(5604.25, 13654.88) * mm, "end": v(5514.08, 13684.9) * mm});
            skLineSegment(sketch, "E3132", {"start": v(5514.08, 13684.9) * mm, "end": v(5423.72, 13713.56) * mm});
            skLineSegment(sketch, "E3133", {"start": v(5423.72, 13713.56) * mm, "end": v(5333.13, 13740.85) * mm});
            skLineSegment(sketch, "E3134", {"start": v(5333.13, 13740.85) * mm, "end": v(5242.3, 13766.79) * mm});
            skLineSegment(sketch, "E3135", {"start": v(5242.3, 13766.79) * mm, "end": v(5151.18, 13791.38) * mm});
            skLineSegment(sketch, "E3136", {"start": v(5151.18, 13791.38) * mm, "end": v(5059.76, 13814.63) * mm});
            skLineSegment(sketch, "E3137", {"start": v(5059.76, 13814.63) * mm, "end": v(4968.02, 13836.54) * mm});
            skLineSegment(sketch, "E3138", {"start": v(4968.02, 13836.54) * mm, "end": v(4875.92, 13857.13) * mm});
            skLineSegment(sketch, "E3139", {"start": v(4875.92, 13857.13) * mm, "end": v(4783.43, 13876.4) * mm});
            skLineSegment(sketch, "E3140", {"start": v(4783.43, 13876.4) * mm, "end": v(4690.54, 13894.35) * mm});
            skLineSegment(sketch, "E3141", {"start": v(4690.54, 13894.35) * mm, "end": v(4597.22, 13911) * mm});
            skLineSegment(sketch, "E3142", {"start": v(4597.22, 13911) * mm, "end": v(4503.44, 13926.33) * mm});
            skLineSegment(sketch, "E3143", {"start": v(4503.44, 13926.33) * mm, "end": v(4409.17, 13940.38) * mm});
            skLineSegment(sketch, "E3144", {"start": v(4409.17, 13940.38) * mm, "end": v(4314.38, 13953.15) * mm});
            skLineSegment(sketch, "E3145", {"start": v(4314.38, 13953.15) * mm, "end": v(4219.06, 13964.63) * mm});
            skLineSegment(sketch, "E3146", {"start": v(4219.06, 13964.63) * mm, "end": v(4123.17, 13974.84) * mm});
            skLineSegment(sketch, "E3147", {"start": v(4123.17, 13974.84) * mm, "end": v(4026.69, 13983.78) * mm});
            skLineSegment(sketch, "E3148", {"start": v(4026.69, 13983.78) * mm, "end": v(3929.59, 13991.47) * mm});
            skLineSegment(sketch, "E3149", {"start": v(3929.59, 13991.47) * mm, "end": v(3856.43, 13981.83) * mm});
            skLineSegment(sketch, "E3150", {"start": v(3856.43, 13981.83) * mm, "end": v(3804.6, 13965.56) * mm});
            skLineSegment(sketch, "E3151", {"start": v(3804.6, 13965.56) * mm, "end": v(3771.93, 13943.2) * mm});
            skLineSegment(sketch, "E3152", {"start": v(3771.93, 13943.2) * mm, "end": v(3756.26, 13915.3) * mm});
            skLineSegment(sketch, "E3153", {"start": v(3756.26, 13915.3) * mm, "end": v(3755.43, 13882.42) * mm});
            skLineSegment(sketch, "E3154", {"start": v(3755.43, 13882.42) * mm, "end": v(3767.27, 13845.09) * mm});
            skLineSegment(sketch, "E3155", {"start": v(3767.27, 13845.09) * mm, "end": v(3789.63, 13803.86) * mm});
            skLineSegment(sketch, "E3156", {"start": v(3789.63, 13803.86) * mm, "end": v(3820.34, 13759.29) * mm});
            skLineSegment(sketch, "E3157", {"start": v(3820.34, 13759.29) * mm, "end": v(3857.24, 13711.9) * mm});
            skLineSegment(sketch, "E3158", {"start": v(3857.24, 13711.9) * mm, "end": v(3898.18, 13662.28) * mm});
            skLineSegment(sketch, "E3159", {"start": v(3898.18, 13662.28) * mm, "end": v(3940.98, 13610.94) * mm});
            skLineSegment(sketch, "E3160", {"start": v(3940.98, 13610.94) * mm, "end": v(3983.49, 13558.44) * mm});
            skLineSegment(sketch, "E3161", {"start": v(3983.49, 13558.44) * mm, "end": v(4023.54, 13505.34) * mm});
            skLineSegment(sketch, "E3162", {"start": v(4023.54, 13505.34) * mm, "end": v(4058.98, 13452.17) * mm});
            skLineSegment(sketch, "E3163", {"start": v(4058.98, 13452.17) * mm, "end": v(4087.65, 13399.48) * mm});
            skLineSegment(sketch, "E3164", {"start": v(4087.65, 13399.48) * mm, "end": v(4107.37, 13347.83) * mm});
            skLineSegment(sketch, "E3165", {"start": v(4107.37, 13347.83) * mm, "end": v(4116, 13297.75) * mm});
            skLineSegment(sketch, "E3166", {"start": v(4116, 13297.75) * mm, "end": v(4111.04, 13240.58) * mm});
            skLineSegment(sketch, "E3167", {"start": v(4111.04, 13240.58) * mm, "end": v(4098.69, 13174.97) * mm});
            skLineSegment(sketch, "E3168", {"start": v(4098.69, 13174.97) * mm, "end": v(4082.67, 13115.79) * mm});
            skLineSegment(sketch, "E3169", {"start": v(4082.67, 13115.79) * mm, "end": v(4063.07, 13062.72) * mm});
            skLineSegment(sketch, "E3170", {"start": v(4063.07, 13062.72) * mm, "end": v(4039.96, 13015.44) * mm});
            skLineSegment(sketch, "E3171", {"start": v(4039.96, 13015.44) * mm, "end": v(4013.42, 12973.63) * mm});
            skLineSegment(sketch, "E3172", {"start": v(4013.42, 12973.63) * mm, "end": v(3983.54, 12936.98) * mm});
            skLineSegment(sketch, "E3173", {"start": v(3983.54, 12936.98) * mm, "end": v(3950.38, 12905.17) * mm});
            skLineSegment(sketch, "E3174", {"start": v(3950.38, 12905.17) * mm, "end": v(3914.03, 12877.87) * mm});
            skLineSegment(sketch, "E3175", {"start": v(3914.03, 12877.87) * mm, "end": v(3874.57, 12854.78) * mm});
            skLineSegment(sketch, "E3176", {"start": v(3874.57, 12854.78) * mm, "end": v(3832.07, 12835.56) * mm});
            skLineSegment(sketch, "E3177", {"start": v(3832.07, 12835.56) * mm, "end": v(3786.6, 12819.9) * mm});
            skLineSegment(sketch, "E3178", {"start": v(3786.6, 12819.9) * mm, "end": v(3738.26, 12807.49) * mm});
            skLineSegment(sketch, "E3179", {"start": v(3738.26, 12807.49) * mm, "end": v(3687.12, 12798) * mm});
            skLineSegment(sketch, "E3180", {"start": v(3687.12, 12798) * mm, "end": v(3633.25, 12791.12) * mm});
            skLineSegment(sketch, "E3181", {"start": v(3633.25, 12791.12) * mm, "end": v(3576.73, 12786.52) * mm});
            skLineSegment(sketch, "E3182", {"start": v(3576.73, 12786.52) * mm, "end": v(3517.64, 12783.9) * mm});
            skLineSegment(sketch, "E3183", {"start": v(3517.64, 12783.9) * mm, "end": v(3456.06, 12782.92) * mm});
            skLineSegment(sketch, "E3184", {"start": v(3456.06, 12782.92) * mm, "end": v(3393.61, 12783.32) * mm});
            skLineSegment(sketch, "E3185", {"start": v(3393.61, 12783.32) * mm, "end": v(3333.52, 12785.25) * mm});
            skLineSegment(sketch, "E3186", {"start": v(3333.52, 12785.25) * mm, "end": v(3275.98, 12789.02) * mm});
            skLineSegment(sketch, "E3187", {"start": v(3275.98, 12789.02) * mm, "end": v(3221.05, 12794.95) * mm});
            skLineSegment(sketch, "E3188", {"start": v(3221.05, 12794.95) * mm, "end": v(3168.81, 12803.36) * mm});
            skLineSegment(sketch, "E3189", {"start": v(3168.81, 12803.36) * mm, "end": v(3119.35, 12814.57) * mm});
            skLineSegment(sketch, "E3190", {"start": v(3119.35, 12814.57) * mm, "end": v(3072.74, 12828.89) * mm});
            skLineSegment(sketch, "E3191", {"start": v(3072.74, 12828.89) * mm, "end": v(3029.06, 12846.64) * mm});
            skLineSegment(sketch, "E3192", {"start": v(3029.06, 12846.64) * mm, "end": v(2988.39, 12868.15) * mm});
            skLineSegment(sketch, "E3193", {"start": v(2988.39, 12868.15) * mm, "end": v(2950.8, 12893.73) * mm});
            skLineSegment(sketch, "E3194", {"start": v(2950.8, 12893.73) * mm, "end": v(2916.36, 12923.7) * mm});
            skLineSegment(sketch, "E3195", {"start": v(2916.36, 12923.7) * mm, "end": v(2885.17, 12958.37) * mm});
            skLineSegment(sketch, "E3196", {"start": v(2885.17, 12958.37) * mm, "end": v(2857.3, 12998.08) * mm});
            skLineSegment(sketch, "E3197", {"start": v(2857.3, 12998.08) * mm, "end": v(2832.81, 13043.13) * mm});
            skLineSegment(sketch, "E3198", {"start": v(2832.81, 13043.13) * mm, "end": v(2811.8, 13093.84) * mm});
            skLineSegment(sketch, "E3199", {"start": v(2811.8, 13093.84) * mm, "end": v(2794.34, 13150.54) * mm});
            skLineSegment(sketch, "E3200", {"start": v(2794.34, 13150.54) * mm, "end": v(2780.5, 13213.54) * mm});
            skLineSegment(sketch, "E3201", {"start": v(2780.5, 13213.54) * mm, "end": v(2771.58, 13273.48) * mm});
            skLineSegment(sketch, "E3202", {"start": v(2771.58, 13273.48) * mm, "end": v(2771.05, 13297.75) * mm});
            skLineSegment(sketch, "E3203", {"start": v(2771.05, 13297.75) * mm, "end": v(2773.84, 13322.56) * mm});
            skLineSegment(sketch, "E3204", {"start": v(2773.84, 13322.56) * mm, "end": v(2779.68, 13347.83) * mm});
            skLineSegment(sketch, "E3205", {"start": v(2779.68, 13347.83) * mm, "end": v(2788.3, 13373.5) * mm});
            skLineSegment(sketch, "E3206", {"start": v(2788.3, 13373.5) * mm, "end": v(2799.4, 13399.48) * mm});
            skLineSegment(sketch, "E3207", {"start": v(2799.4, 13399.48) * mm, "end": v(2812.76, 13425.73) * mm});
            skLineSegment(sketch, "E3208", {"start": v(2812.76, 13425.73) * mm, "end": v(2828.08, 13452.17) * mm});
            skLineSegment(sketch, "E3209", {"start": v(2828.08, 13452.17) * mm, "end": v(2845.1, 13478.73) * mm});
            skLineSegment(sketch, "E3210", {"start": v(2845.1, 13478.73) * mm, "end": v(2863.53, 13505.34) * mm});
            skLineSegment(sketch, "E3211", {"start": v(2863.53, 13505.34) * mm, "end": v(2883.12, 13531.93) * mm});
            skLineSegment(sketch, "E3212", {"start": v(2883.12, 13531.93) * mm, "end": v(2903.6, 13558.44) * mm});
            skLineSegment(sketch, "E3213", {"start": v(2903.6, 13558.44) * mm, "end": v(2924.68, 13584.8) * mm});
            skLineSegment(sketch, "E3214", {"start": v(2924.68, 13584.8) * mm, "end": v(2946.11, 13610.94) * mm});
            skLineSegment(sketch, "E3215", {"start": v(2946.11, 13610.94) * mm, "end": v(2967.62, 13636.79) * mm});
            skLineSegment(sketch, "E3216", {"start": v(2967.62, 13636.79) * mm, "end": v(2988.93, 13662.28) * mm});
            skLineSegment(sketch, "E3217", {"start": v(2988.93, 13662.28) * mm, "end": v(3009.77, 13687.34) * mm});
            skLineSegment(sketch, "E3218", {"start": v(3009.77, 13687.34) * mm, "end": v(3029.87, 13711.9) * mm});
            skLineSegment(sketch, "E3219", {"start": v(3029.87, 13711.9) * mm, "end": v(3048.96, 13735.91) * mm});
            skLineSegment(sketch, "E3220", {"start": v(3048.96, 13735.91) * mm, "end": v(3066.78, 13759.29) * mm});
            skLineSegment(sketch, "E3221", {"start": v(3066.78, 13759.29) * mm, "end": v(3083.05, 13781.96) * mm});
            skLineSegment(sketch, "E3222", {"start": v(3083.05, 13781.96) * mm, "end": v(3097.5, 13803.86) * mm});
            skLineSegment(sketch, "E3223", {"start": v(3097.5, 13803.86) * mm, "end": v(3109.86, 13824.93) * mm});
            skLineSegment(sketch, "E3224", {"start": v(3109.86, 13824.93) * mm, "end": v(3119.86, 13845.09) * mm});
            skLineSegment(sketch, "E3225", {"start": v(3119.86, 13845.09) * mm, "end": v(3127.23, 13864.28) * mm});
            skLineSegment(sketch, "E3226", {"start": v(3127.23, 13864.28) * mm, "end": v(3131.7, 13882.42) * mm});
            skLineSegment(sketch, "E3227", {"start": v(3131.7, 13882.42) * mm, "end": v(3133, 13899.45) * mm});
            skLineSegment(sketch, "E3228", {"start": v(3133, 13899.45) * mm, "end": v(3130.86, 13915.3) * mm});
            skLineSegment(sketch, "E3229", {"start": v(3130.86, 13915.3) * mm, "end": v(3125.01, 13929.91) * mm});
            skLineSegment(sketch, "E3230", {"start": v(3125.01, 13929.91) * mm, "end": v(3115.18, 13943.2) * mm});
            skLineSegment(sketch, "E3231", {"start": v(3115.18, 13943.2) * mm, "end": v(3101.1, 13955.1) * mm});
            skLineSegment(sketch, "E3232", {"start": v(3101.1, 13955.1) * mm, "end": v(3082.5, 13965.56) * mm});
            skLineSegment(sketch, "E3233", {"start": v(3082.5, 13965.56) * mm, "end": v(3059.1, 13974.5) * mm});
            skLineSegment(sketch, "E3234", {"start": v(3059.1, 13974.5) * mm, "end": v(3030.64, 13981.83) * mm});
            skLineSegment(sketch, "E3235", {"start": v(3030.64, 13981.83) * mm, "end": v(2996.85, 13987.51) * mm});
            skLineSegment(sketch, "E3236", {"start": v(2996.85, 13987.51) * mm, "end": v(2957.46, 13991.47) * mm});
            skLineSegment(sketch, "E3237", {"start": v(2957.46, 13991.47) * mm, "end": v(2860.36, 13983.78) * mm});
            skLineSegment(sketch, "E3238", {"start": v(2860.36, 13983.78) * mm, "end": v(2763.88, 13974.84) * mm});
            skLineSegment(sketch, "E3239", {"start": v(2763.88, 13974.84) * mm, "end": v(2667.99, 13964.63) * mm});
            skLineSegment(sketch, "E3240", {"start": v(2667.99, 13964.63) * mm, "end": v(2572.66, 13953.15) * mm});
            skLineSegment(sketch, "E3241", {"start": v(2572.66, 13953.15) * mm, "end": v(2477.88, 13940.38) * mm});
            skLineSegment(sketch, "E3242", {"start": v(2477.88, 13940.38) * mm, "end": v(2383.6, 13926.33) * mm});
            skLineSegment(sketch, "E3243", {"start": v(2383.6, 13926.33) * mm, "end": v(2289.83, 13911) * mm});
            skLineSegment(sketch, "E3244", {"start": v(2289.83, 13911) * mm, "end": v(2196.5, 13894.35) * mm});
            skLineSegment(sketch, "E3245", {"start": v(2196.5, 13894.35) * mm, "end": v(2103.62, 13876.4) * mm});
            skLineSegment(sketch, "E3246", {"start": v(2103.62, 13876.4) * mm, "end": v(2011.14, 13857.13) * mm});
            skLineSegment(sketch, "E3247", {"start": v(2011.14, 13857.13) * mm, "end": v(1919.05, 13836.54) * mm});
            skLineSegment(sketch, "E3248", {"start": v(1919.05, 13836.54) * mm, "end": v(1827.3, 13814.63) * mm});
            skLineSegment(sketch, "E3249", {"start": v(1827.3, 13814.63) * mm, "end": v(1735.9, 13791.38) * mm});
            skLineSegment(sketch, "E3250", {"start": v(1735.9, 13791.38) * mm, "end": v(1644.8, 13766.79) * mm});
            skLineSegment(sketch, "E3251", {"start": v(1644.8, 13766.79) * mm, "end": v(1553.96, 13740.85) * mm});
            skLineSegment(sketch, "E3252", {"start": v(1553.96, 13740.85) * mm, "end": v(1463.38, 13713.56) * mm});
            skLineSegment(sketch, "E3253", {"start": v(1463.38, 13713.56) * mm, "end": v(1373.03, 13684.9) * mm});
            skLineSegment(sketch, "E3254", {"start": v(1373.03, 13684.9) * mm, "end": v(1282.87, 13654.88) * mm});
            skLineSegment(sketch, "E3255", {"start": v(1282.87, 13654.88) * mm, "end": v(1192.89, 13623.48) * mm});
            skLineSegment(sketch, "E3256", {"start": v(1192.89, 13623.48) * mm, "end": v(1103.05, 13590.7) * mm});
            skLineSegment(sketch, "E3257", {"start": v(1103.05, 13590.7) * mm, "end": v(1013.33, 13556.52) * mm});
            skLineSegment(sketch, "E3258", {"start": v(1013.33, 13556.52) * mm, "end": v(923.7, 13520.95) * mm});
            skLineSegment(sketch, "E3259", {"start": v(923.7, 13520.95) * mm, "end": v(834.14, 13483.98) * mm});
            skLineSegment(sketch, "E3260", {"start": v(834.14, 13483.98) * mm, "end": v(744.62, 13445.6) * mm});
            skLineSegment(sketch, "E3261", {"start": v(6142.61, -13544.6) * mm, "end": v(6104.23, -13455.06) * mm});
            skLineSegment(sketch, "E3262", {"start": v(6104.23, -13455.06) * mm, "end": v(6067.26, -13365.48) * mm});
            skLineSegment(sketch, "E3263", {"start": v(6067.26, -13365.48) * mm, "end": v(6031.68, -13275.84) * mm});
            skLineSegment(sketch, "E3264", {"start": v(6031.68, -13275.84) * mm, "end": v(5997.5, -13186.1) * mm});
            skLineSegment(sketch, "E3265", {"start": v(5997.5, -13186.1) * mm, "end": v(5964.72, -13096.25) * mm});
            skLineSegment(sketch, "E3266", {"start": v(5964.72, -13096.25) * mm, "end": v(5933.3, -13006.25) * mm});
            skLineSegment(sketch, "E3267", {"start": v(5933.3, -13006.25) * mm, "end": v(5903.28, -12916.08) * mm});
            skLineSegment(sketch, "E3268", {"start": v(5903.28, -12916.08) * mm, "end": v(5874.61, -12825.71) * mm});
            skLineSegment(sketch, "E3269", {"start": v(5874.61, -12825.71) * mm, "end": v(5847.31, -12735.12) * mm});
            skLineSegment(sketch, "E3270", {"start": v(5847.31, -12735.12) * mm, "end": v(5821.37, -12644.28) * mm});
            skLineSegment(sketch, "E3271", {"start": v(5821.37, -12644.28) * mm, "end": v(5796.77, -12553.17) * mm});
            skLineSegment(sketch, "E3272", {"start": v(5796.77, -12553.17) * mm, "end": v(5773.52, -12461.75) * mm});
            skLineSegment(sketch, "E3273", {"start": v(5773.52, -12461.75) * mm, "end": v(5751.6, -12370) * mm});
            skLineSegment(sketch, "E3274", {"start": v(5751.6, -12370) * mm, "end": v(5731.01, -12277.9) * mm});
            skLineSegment(sketch, "E3275", {"start": v(5731.01, -12277.9) * mm, "end": v(5711.75, -12185.43) * mm});
            skLineSegment(sketch, "E3276", {"start": v(5711.75, -12185.43) * mm, "end": v(5693.8, -12092.54) * mm});
            skLineSegment(sketch, "E3277", {"start": v(5693.8, -12092.54) * mm, "end": v(5677.16, -11999.21) * mm});
            skLineSegment(sketch, "E3278", {"start": v(5677.16, -11999.21) * mm, "end": v(5661.82, -11905.43) * mm});
            skLineSegment(sketch, "E3279", {"start": v(5661.82, -11905.43) * mm, "end": v(5647.78, -11811.16) * mm});
            skLineSegment(sketch, "E3280", {"start": v(5647.78, -11811.16) * mm, "end": v(5635.03, -11716.38) * mm});
            skLineSegment(sketch, "E3281", {"start": v(5635.03, -11716.38) * mm, "end": v(5623.57, -11621.05) * mm});
            skLineSegment(sketch, "E3282", {"start": v(5623.57, -11621.05) * mm, "end": v(5613.38, -11525.16) * mm});
            skLineSegment(sketch, "E3283", {"start": v(5613.38, -11525.16) * mm, "end": v(5604.46, -11428.68) * mm});
            skLineSegment(sketch, "E3284", {"start": v(5604.46, -11428.68) * mm, "end": v(5596.8, -11331.58) * mm});
            skLineSegment(sketch, "E3285", {"start": v(5596.8, -11331.58) * mm, "end": v(5606.4, -11258.42) * mm});
            skLineSegment(sketch, "E3286", {"start": v(5606.4, -11258.42) * mm, "end": v(5622.64, -11206.59) * mm});
            skLineSegment(sketch, "E3287", {"start": v(5622.64, -11206.59) * mm, "end": v(5644.97, -11173.91) * mm});
            skLineSegment(sketch, "E3288", {"start": v(5644.97, -11173.91) * mm, "end": v(5672.85, -11158.23) * mm});
            skLineSegment(sketch, "E3289", {"start": v(5672.85, -11158.23) * mm, "end": v(5705.73, -11157.39) * mm});
            skLineSegment(sketch, "E3290", {"start": v(5705.73, -11157.39) * mm, "end": v(5743.05, -11169.22) * mm});
            skLineSegment(sketch, "E3291", {"start": v(5743.05, -11169.22) * mm, "end": v(5784.28, -11191.56) * mm});
            skLineSegment(sketch, "E3292", {"start": v(5784.28, -11191.56) * mm, "end": v(5828.86, -11222.26) * mm});
            skLineSegment(sketch, "E3293", {"start": v(5828.86, -11222.26) * mm, "end": v(5876.24, -11259.15) * mm});
            skLineSegment(sketch, "E3294", {"start": v(5876.24, -11259.15) * mm, "end": v(5925.88, -11300.08) * mm});
            skLineSegment(sketch, "E3295", {"start": v(5925.88, -11300.08) * mm, "end": v(5977.22, -11342.87) * mm});
            skLineSegment(sketch, "E3296", {"start": v(5977.22, -11342.87) * mm, "end": v(6029.73, -11385.38) * mm});
            skLineSegment(sketch, "E3297", {"start": v(6029.73, -11385.38) * mm, "end": v(6082.85, -11425.43) * mm});
            skLineSegment(sketch, "E3298", {"start": v(6082.85, -11425.43) * mm, "end": v(6136.03, -11460.87) * mm});
            skLineSegment(sketch, "E3299", {"start": v(6136.03, -11460.87) * mm, "end": v(6188.72, -11489.54) * mm});
            skLineSegment(sketch, "E3300", {"start": v(6188.72, -11489.54) * mm, "end": v(6240.38, -11509.27) * mm});
            skLineSegment(sketch, "E3301", {"start": v(6240.38, -11509.27) * mm, "end": v(6290.46, -11517.9) * mm});
            skLineSegment(sketch, "E3302", {"start": v(6290.46, -11517.9) * mm, "end": v(6347.63, -11512.97) * mm});
            skLineSegment(sketch, "E3303", {"start": v(6347.63, -11512.97) * mm, "end": v(6413.24, -11500.61) * mm});
            skLineSegment(sketch, "E3304", {"start": v(6413.24, -11500.61) * mm, "end": v(6472.42, -11484.6) * mm});
            skLineSegment(sketch, "E3305", {"start": v(6472.42, -11484.6) * mm, "end": v(6525.5, -11465) * mm});
            skLineSegment(sketch, "E3306", {"start": v(6525.5, -11465) * mm, "end": v(6572.77, -11441.89) * mm});
            skLineSegment(sketch, "E3307", {"start": v(6572.77, -11441.89) * mm, "end": v(6614.58, -11415.35) * mm});
            skLineSegment(sketch, "E3308", {"start": v(6614.58, -11415.35) * mm, "end": v(6651.23, -11385.47) * mm});
            skLineSegment(sketch, "E3309", {"start": v(6651.23, -11385.47) * mm, "end": v(6683.04, -11352.31) * mm});
            skLineSegment(sketch, "E3310", {"start": v(6683.04, -11352.31) * mm, "end": v(6710.34, -11315.96) * mm});
            skLineSegment(sketch, "E3311", {"start": v(6710.34, -11315.96) * mm, "end": v(6733.44, -11276.5) * mm});
            skLineSegment(sketch, "E3312", {"start": v(6733.44, -11276.5) * mm, "end": v(6752.65, -11234) * mm});
            skLineSegment(sketch, "E3313", {"start": v(6752.65, -11234) * mm, "end": v(6768.3, -11188.53) * mm});
            skLineSegment(sketch, "E3314", {"start": v(6768.3, -11188.53) * mm, "end": v(6780.72, -11140.2) * mm});
            skLineSegment(sketch, "E3315", {"start": v(6780.72, -11140.2) * mm, "end": v(6790.21, -11089.04) * mm});
            skLineSegment(sketch, "E3316", {"start": v(6790.21, -11089.04) * mm, "end": v(6797.1, -11035.17) * mm});
            skLineSegment(sketch, "E3317", {"start": v(6797.1, -11035.17) * mm, "end": v(6801.69, -10978.66) * mm});
            skLineSegment(sketch, "E3318", {"start": v(6801.69, -10978.66) * mm, "end": v(6804.32, -10919.57) * mm});
            skLineSegment(sketch, "E3319", {"start": v(6804.32, -10919.57) * mm, "end": v(6805.3, -10858) * mm});
            skLineSegment(sketch, "E3320", {"start": v(6805.3, -10858) * mm, "end": v(6804.89, -10795.54) * mm});
            skLineSegment(sketch, "E3321", {"start": v(6804.89, -10795.54) * mm, "end": v(6802.96, -10735.45) * mm});
            skLineSegment(sketch, "E3322", {"start": v(6802.96, -10735.45) * mm, "end": v(6799.19, -10677.9) * mm});
            skLineSegment(sketch, "E3323", {"start": v(6799.19, -10677.9) * mm, "end": v(6793.26, -10622.98) * mm});
            skLineSegment(sketch, "E3324", {"start": v(6793.26, -10622.98) * mm, "end": v(6784.85, -10570.74) * mm});
            skLineSegment(sketch, "E3325", {"start": v(6784.85, -10570.74) * mm, "end": v(6773.64, -10521.28) * mm});
            skLineSegment(sketch, "E3326", {"start": v(6773.64, -10521.28) * mm, "end": v(6759.31, -10474.67) * mm});
            skLineSegment(sketch, "E3327", {"start": v(6759.31, -10474.67) * mm, "end": v(6741.55, -10431) * mm});
            skLineSegment(sketch, "E3328", {"start": v(6741.55, -10431) * mm, "end": v(6720.04, -10390.32) * mm});
            skLineSegment(sketch, "E3329", {"start": v(6720.04, -10390.32) * mm, "end": v(6694.45, -10352.73) * mm});
            skLineSegment(sketch, "E3330", {"start": v(6694.45, -10352.73) * mm, "end": v(6664.47, -10318.3) * mm});
            skLineSegment(sketch, "E3331", {"start": v(6664.47, -10318.3) * mm, "end": v(6629.78, -10287.12) * mm});
            skLineSegment(sketch, "E3332", {"start": v(6629.78, -10287.12) * mm, "end": v(6590.06, -10259.25) * mm});
            skLineSegment(sketch, "E3333", {"start": v(6590.06, -10259.25) * mm, "end": v(6545, -10234.77) * mm});
            skLineSegment(sketch, "E3334", {"start": v(6545, -10234.77) * mm, "end": v(6494.25, -10213.77) * mm});
            skLineSegment(sketch, "E3335", {"start": v(6494.25, -10213.77) * mm, "end": v(6437.53, -10196.32) * mm});
            skLineSegment(sketch, "E3336", {"start": v(6437.53, -10196.32) * mm, "end": v(6374.5, -10182.5) * mm});
            skLineSegment(sketch, "E3337", {"start": v(6374.5, -10182.5) * mm, "end": v(6314.54, -10173.57) * mm});
            skLineSegment(sketch, "E3338", {"start": v(6314.54, -10173.57) * mm, "end": v(6290.28, -10173.04) * mm});
            skLineSegment(sketch, "E3339", {"start": v(6290.28, -10173.04) * mm, "end": v(6265.5, -10175.82) * mm});
            skLineSegment(sketch, "E3340", {"start": v(6265.5, -10175.82) * mm, "end": v(6240.23, -10181.66) * mm});
            skLineSegment(sketch, "E3341", {"start": v(6240.23, -10181.66) * mm, "end": v(6214.58, -10190.26) * mm});
            skLineSegment(sketch, "E3342", {"start": v(6214.58, -10190.26) * mm, "end": v(6188.6, -10201.38) * mm});
            skLineSegment(sketch, "E3343", {"start": v(6188.6, -10201.38) * mm, "end": v(6162.36, -10214.73) * mm});
            skLineSegment(sketch, "E3344", {"start": v(6162.36, -10214.73) * mm, "end": v(6135.93, -10230.04) * mm});
            skLineSegment(sketch, "E3345", {"start": v(6135.93, -10230.04) * mm, "end": v(6109.37, -10247.05) * mm});
            skLineSegment(sketch, "E3346", {"start": v(6109.37, -10247.05) * mm, "end": v(6082.77, -10265.48) * mm});
            skLineSegment(sketch, "E3347", {"start": v(6082.77, -10265.48) * mm, "end": v(6056.18, -10285.07) * mm});
            skLineSegment(sketch, "E3348", {"start": v(6056.18, -10285.07) * mm, "end": v(6029.67, -10305.54) * mm});
            skLineSegment(sketch, "E3349", {"start": v(6029.67, -10305.54) * mm, "end": v(6003.31, -10326.63) * mm});
            skLineSegment(sketch, "E3350", {"start": v(6003.31, -10326.63) * mm, "end": v(5977.18, -10348.06) * mm});
            skLineSegment(sketch, "E3351", {"start": v(5977.18, -10348.06) * mm, "end": v(5951.33, -10369.56) * mm});
            skLineSegment(sketch, "E3352", {"start": v(5951.33, -10369.56) * mm, "end": v(5925.84, -10390.87) * mm});
            skLineSegment(sketch, "E3353", {"start": v(5925.84, -10390.87) * mm, "end": v(5900.78, -10411.7) * mm});
            skLineSegment(sketch, "E3354", {"start": v(5900.78, -10411.7) * mm, "end": v(5876.21, -10431.8) * mm});
            skLineSegment(sketch, "E3355", {"start": v(5876.21, -10431.8) * mm, "end": v(5852.21, -10450.9) * mm});
            skLineSegment(sketch, "E3356", {"start": v(5852.21, -10450.9) * mm, "end": v(5828.84, -10468.71) * mm});
            skLineSegment(sketch, "E3357", {"start": v(5828.84, -10468.71) * mm, "end": v(5806.17, -10484.98) * mm});
            skLineSegment(sketch, "E3358", {"start": v(5806.17, -10484.98) * mm, "end": v(5784.27, -10499.43) * mm});
            skLineSegment(sketch, "E3359", {"start": v(5784.27, -10499.43) * mm, "end": v(5763.2, -10511.79) * mm});
            skLineSegment(sketch, "E3360", {"start": v(5763.2, -10511.79) * mm, "end": v(5743.05, -10521.79) * mm});
            skLineSegment(sketch, "E3361", {"start": v(5743.05, -10521.79) * mm, "end": v(5723.86, -10529.16) * mm});
            skLineSegment(sketch, "E3362", {"start": v(5723.86, -10529.16) * mm, "end": v(5705.72, -10533.63) * mm});
            skLineSegment(sketch, "E3363", {"start": v(5705.72, -10533.63) * mm, "end": v(5688.7, -10534.93) * mm});
            skLineSegment(sketch, "E3364", {"start": v(5688.7, -10534.93) * mm, "end": v(5672.85, -10532.79) * mm});
            skLineSegment(sketch, "E3365", {"start": v(5672.85, -10532.79) * mm, "end": v(5658.25, -10526.94) * mm});
            skLineSegment(sketch, "E3366", {"start": v(5658.25, -10526.94) * mm, "end": v(5644.97, -10517.1) * mm});
            skLineSegment(sketch, "E3367", {"start": v(5644.97, -10517.1) * mm, "end": v(5633.08, -10503.03) * mm});
            skLineSegment(sketch, "E3368", {"start": v(5633.08, -10503.03) * mm, "end": v(5622.64, -10484.42) * mm});
            skLineSegment(sketch, "E3369", {"start": v(5622.64, -10484.42) * mm, "end": v(5613.73, -10461.03) * mm});
            skLineSegment(sketch, "E3370", {"start": v(5613.73, -10461.03) * mm, "end": v(5606.4, -10432.57) * mm});
            skLineSegment(sketch, "E3371", {"start": v(5606.4, -10432.57) * mm, "end": v(5600.74, -10398.78) * mm});
            skLineSegment(sketch, "E3372", {"start": v(5600.74, -10398.78) * mm, "end": v(5596.8, -10359.39) * mm});
            skLineSegment(sketch, "E3373", {"start": v(5596.8, -10359.39) * mm, "end": v(5604.46, -10262.29) * mm});
            skLineSegment(sketch, "E3374", {"start": v(5604.46, -10262.29) * mm, "end": v(5613.38, -10165.8) * mm});
            skLineSegment(sketch, "E3375", {"start": v(5613.38, -10165.8) * mm, "end": v(5623.57, -10069.92) * mm});
            skLineSegment(sketch, "E3376", {"start": v(5623.57, -10069.92) * mm, "end": v(5635.03, -9974.6) * mm});
            skLineSegment(sketch, "E3377", {"start": v(5635.03, -9974.6) * mm, "end": v(5647.78, -9879.81) * mm});
            skLineSegment(sketch, "E3378", {"start": v(5647.78, -9879.81) * mm, "end": v(5661.82, -9785.55) * mm});
            skLineSegment(sketch, "E3379", {"start": v(5661.82, -9785.55) * mm, "end": v(5677.16, -9691.77) * mm});
            skLineSegment(sketch, "E3380", {"start": v(5677.16, -9691.77) * mm, "end": v(5693.8, -9598.45) * mm});
            skLineSegment(sketch, "E3381", {"start": v(5693.8, -9598.45) * mm, "end": v(5711.75, -9505.57) * mm});
            skLineSegment(sketch, "E3382", {"start": v(5711.75, -9505.57) * mm, "end": v(5731.01, -9413.1) * mm});
            skLineSegment(sketch, "E3383", {"start": v(5731.01, -9413.1) * mm, "end": v(5751.6, -9321) * mm});
            skLineSegment(sketch, "E3384", {"start": v(5751.6, -9321) * mm, "end": v(5773.52, -9229.27) * mm});
            skLineSegment(sketch, "E3385", {"start": v(5773.52, -9229.27) * mm, "end": v(5796.77, -9137.86) * mm});
            skLineSegment(sketch, "E3386", {"start": v(5796.77, -9137.86) * mm, "end": v(5821.37, -9046.76) * mm});
            skLineSegment(sketch, "E3387", {"start": v(5821.37, -9046.76) * mm, "end": v(5847.31, -8955.93) * mm});
            skLineSegment(sketch, "E3388", {"start": v(5847.31, -8955.93) * mm, "end": v(5874.61, -8865.36) * mm});
            skLineSegment(sketch, "E3389", {"start": v(5874.61, -8865.36) * mm, "end": v(5903.28, -8775) * mm});
            skLineSegment(sketch, "E3390", {"start": v(5903.28, -8775) * mm, "end": v(5933.3, -8684.85) * mm});
            skLineSegment(sketch, "E3391", {"start": v(5933.3, -8684.85) * mm, "end": v(5964.72, -8594.87) * mm});
            skLineSegment(sketch, "E3392", {"start": v(5964.72, -8594.87) * mm, "end": v(5997.5, -8505.04) * mm});
            skLineSegment(sketch, "E3393", {"start": v(5997.5, -8505.04) * mm, "end": v(6031.68, -8415.32) * mm});
            skLineSegment(sketch, "E3394", {"start": v(6031.68, -8415.32) * mm, "end": v(6067.26, -8325.7) * mm});
            skLineSegment(sketch, "E3395", {"start": v(6067.26, -8325.7) * mm, "end": v(6104.23, -8236.14) * mm});
            skLineSegment(sketch, "E3396", {"start": v(6104.23, -8236.14) * mm, "end": v(6142.61, -8146.62) * mm});
            skLineSegment(sketch, "E3397", {"start": v(744.62, -13544.6) * mm, "end": v(834.14, -13582.97) * mm});
            skLineSegment(sketch, "E3398", {"start": v(834.14, -13582.97) * mm, "end": v(923.7, -13619.92) * mm});
            skLineSegment(sketch, "E3399", {"start": v(923.7, -13619.92) * mm, "end": v(1013.33, -13655.47) * mm});
            skLineSegment(sketch, "E3400", {"start": v(1013.33, -13655.47) * mm, "end": v(1103.05, -13689.63) * mm});
            skLineSegment(sketch, "E3401", {"start": v(1103.05, -13689.63) * mm, "end": v(1192.89, -13722.4) * mm});
            skLineSegment(sketch, "E3402", {"start": v(1192.89, -13722.4) * mm, "end": v(1282.87, -13753.8) * mm});
            skLineSegment(sketch, "E3403", {"start": v(1282.87, -13753.8) * mm, "end": v(1373.03, -13783.82) * mm});
            skLineSegment(sketch, "E3404", {"start": v(1373.03, -13783.82) * mm, "end": v(1463.38, -13812.47) * mm});
            skLineSegment(sketch, "E3405", {"start": v(1463.38, -13812.47) * mm, "end": v(1553.96, -13839.76) * mm});
            skLineSegment(sketch, "E3406", {"start": v(1553.96, -13839.76) * mm, "end": v(1644.8, -13865.7) * mm});
            skLineSegment(sketch, "E3407", {"start": v(1644.8, -13865.7) * mm, "end": v(1735.9, -13890.29) * mm});
            skLineSegment(sketch, "E3408", {"start": v(1735.9, -13890.29) * mm, "end": v(1827.3, -13913.53) * mm});
            skLineSegment(sketch, "E3409", {"start": v(1827.3, -13913.53) * mm, "end": v(1919.05, -13935.44) * mm});
            skLineSegment(sketch, "E3410", {"start": v(1919.05, -13935.44) * mm, "end": v(2011.14, -13956.03) * mm});
            skLineSegment(sketch, "E3411", {"start": v(2011.14, -13956.03) * mm, "end": v(2103.62, -13975.3) * mm});
            skLineSegment(sketch, "E3412", {"start": v(2103.62, -13975.3) * mm, "end": v(2196.5, -13993.24) * mm});
            skLineSegment(sketch, "E3413", {"start": v(2196.5, -13993.24) * mm, "end": v(2289.83, -14009.87) * mm});
            skLineSegment(sketch, "E3414", {"start": v(2289.83, -14009.87) * mm, "end": v(2383.6, -14025.2) * mm});
            skLineSegment(sketch, "E3415", {"start": v(2383.6, -14025.2) * mm, "end": v(2477.88, -14039.24) * mm});
            skLineSegment(sketch, "E3416", {"start": v(2477.88, -14039.24) * mm, "end": v(2572.66, -14052) * mm});
            skLineSegment(sketch, "E3417", {"start": v(2572.66, -14052) * mm, "end": v(2667.99, -14063.46) * mm});
            skLineSegment(sketch, "E3418", {"start": v(2667.99, -14063.46) * mm, "end": v(2763.88, -14073.65) * mm});
            skLineSegment(sketch, "E3419", {"start": v(2763.88, -14073.65) * mm, "end": v(2860.36, -14082.56) * mm});
            skLineSegment(sketch, "E3420", {"start": v(2860.36, -14082.56) * mm, "end": v(2957.46, -14090.22) * mm});
            skLineSegment(sketch, "E3421", {"start": v(2957.46, -14090.22) * mm, "end": v(3025.39, -14081.68) * mm});
            skLineSegment(sketch, "E3422", {"start": v(3025.39, -14081.68) * mm, "end": v(3075.24, -14067.53) * mm});
            skLineSegment(sketch, "E3423", {"start": v(3075.24, -14067.53) * mm, "end": v(3108.69, -14048.19) * mm});
            skLineSegment(sketch, "E3424", {"start": v(3108.69, -14048.19) * mm, "end": v(3127.39, -14024.07) * mm});
            skLineSegment(sketch, "E3425", {"start": v(3127.39, -14024.07) * mm, "end": v(3133.01, -13995.6) * mm});
            skLineSegment(sketch, "E3426", {"start": v(3133.01, -13995.6) * mm, "end": v(3127.23, -13963.2) * mm});
            skLineSegment(sketch, "E3427", {"start": v(3127.23, -13963.2) * mm, "end": v(3111.7, -13927.3) * mm});
            skLineSegment(sketch, "E3428", {"start": v(3111.7, -13927.3) * mm, "end": v(3088.08, -13888.3) * mm});
            skLineSegment(sketch, "E3429", {"start": v(3088.08, -13888.3) * mm, "end": v(3058.05, -13846.65) * mm});
            skLineSegment(sketch, "E3430", {"start": v(3058.05, -13846.65) * mm, "end": v(3023.27, -13802.76) * mm});
            skLineSegment(sketch, "E3431", {"start": v(3023.27, -13802.76) * mm, "end": v(2985.4, -13757.04) * mm});
            skLineSegment(sketch, "E3432", {"start": v(2985.4, -13757.04) * mm, "end": v(2946.11, -13709.93) * mm});
            skLineSegment(sketch, "E3433", {"start": v(2946.11, -13709.93) * mm, "end": v(2907.07, -13661.85) * mm});
            skLineSegment(sketch, "E3434", {"start": v(2907.07, -13661.85) * mm, "end": v(2869.94, -13613.21) * mm});
            skLineSegment(sketch, "E3435", {"start": v(2869.94, -13613.21) * mm, "end": v(2836.39, -13564.44) * mm});
            skLineSegment(sketch, "E3436", {"start": v(2836.39, -13564.44) * mm, "end": v(2808.08, -13515.96) * mm});
            skLineSegment(sketch, "E3437", {"start": v(2808.08, -13515.96) * mm, "end": v(2786.67, -13468.2) * mm});
            skLineSegment(sketch, "E3438", {"start": v(2786.67, -13468.2) * mm, "end": v(2773.84, -13421.57) * mm});
            skLineSegment(sketch, "E3439", {"start": v(2773.84, -13421.57) * mm, "end": v(2771.25, -13376.5) * mm});
            skLineSegment(sketch, "E3440", {"start": v(2771.25, -13376.5) * mm, "end": v(2779.72, -13316.96) * mm});
            skLineSegment(sketch, "E3441", {"start": v(2779.72, -13316.96) * mm, "end": v(2792.03, -13258.54) * mm});
            skLineSegment(sketch, "E3442", {"start": v(2792.03, -13258.54) * mm, "end": v(2807.4, -13205.46) * mm});
            skLineSegment(sketch, "E3443", {"start": v(2807.4, -13205.46) * mm, "end": v(2825.78, -13157.47) * mm});
            skLineSegment(sketch, "E3444", {"start": v(2825.78, -13157.47) * mm, "end": v(2847.1, -13114.33) * mm});
            skLineSegment(sketch, "E3445", {"start": v(2847.1, -13114.33) * mm, "end": v(2871.28, -13075.8) * mm});
            skLineSegment(sketch, "E3446", {"start": v(2871.28, -13075.8) * mm, "end": v(2898.28, -13041.61) * mm});
            skLineSegment(sketch, "E3447", {"start": v(2898.28, -13041.61) * mm, "end": v(2928.05, -13011.54) * mm});
            skLineSegment(sketch, "E3448", {"start": v(2928.05, -13011.54) * mm, "end": v(2960.51, -12985.33) * mm});
            skLineSegment(sketch, "E3449", {"start": v(2960.51, -12985.33) * mm, "end": v(2995.61, -12962.75) * mm});
            skLineSegment(sketch, "E3450", {"start": v(2995.61, -12962.75) * mm, "end": v(3033.3, -12943.53) * mm});
            skLineSegment(sketch, "E3451", {"start": v(3033.3, -12943.53) * mm, "end": v(3073.5, -12927.45) * mm});
            skLineSegment(sketch, "E3452", {"start": v(3073.5, -12927.45) * mm, "end": v(3116.16, -12914.24) * mm});
            skLineSegment(sketch, "E3453", {"start": v(3116.16, -12914.24) * mm, "end": v(3161.22, -12903.67) * mm});
            skLineSegment(sketch, "E3454", {"start": v(3161.22, -12903.67) * mm, "end": v(3208.61, -12895.5) * mm});
            skLineSegment(sketch, "E3455", {"start": v(3208.61, -12895.5) * mm, "end": v(3258.3, -12889.47) * mm});
            skLineSegment(sketch, "E3456", {"start": v(3258.3, -12889.47) * mm, "end": v(3310.2, -12885.34) * mm});
            skLineSegment(sketch, "E3457", {"start": v(3310.2, -12885.34) * mm, "end": v(3364.26, -12882.86) * mm});
            skLineSegment(sketch, "E3458", {"start": v(3364.26, -12882.86) * mm, "end": v(3420.42, -12881.8) * mm});
            skLineSegment(sketch, "E3459", {"start": v(3420.42, -12881.8) * mm, "end": v(3477.91, -12881.9) * mm});
            skLineSegment(sketch, "E3460", {"start": v(3477.91, -12881.9) * mm, "end": v(3533.69, -12883.23) * mm});
            skLineSegment(sketch, "E3461", {"start": v(3533.69, -12883.23) * mm, "end": v(3587.34, -12886.02) * mm});
            skLineSegment(sketch, "E3462", {"start": v(3587.34, -12886.02) * mm, "end": v(3638.82, -12890.51) * mm});
            skLineSegment(sketch, "E3463", {"start": v(3638.82, -12890.51) * mm, "end": v(3688.07, -12896.95) * mm});
            skLineSegment(sketch, "E3464", {"start": v(3688.07, -12896.95) * mm, "end": v(3735.02, -12905.59) * mm});
            skLineSegment(sketch, "E3465", {"start": v(3735.02, -12905.59) * mm, "end": v(3779.62, -12916.66) * mm});
            skLineSegment(sketch, "E3466", {"start": v(3779.62, -12916.66) * mm, "end": v(3821.8, -12930.42) * mm});
            skLineSegment(sketch, "E3467", {"start": v(3821.8, -12930.42) * mm, "end": v(3861.51, -12947.12) * mm});
            skLineSegment(sketch, "E3468", {"start": v(3861.51, -12947.12) * mm, "end": v(3898.7, -12966.99) * mm});
            skLineSegment(sketch, "E3469", {"start": v(3898.7, -12966.99) * mm, "end": v(3933.27, -12990.28) * mm});
            skLineSegment(sketch, "E3470", {"start": v(3933.27, -12990.28) * mm, "end": v(3965.2, -13017.24) * mm});
            skLineSegment(sketch, "E3471", {"start": v(3965.2, -13017.24) * mm, "end": v(3994.42, -13048.11) * mm});
            skLineSegment(sketch, "E3472", {"start": v(3994.42, -13048.11) * mm, "end": v(4020.87, -13083.15) * mm});
            skLineSegment(sketch, "E3473", {"start": v(4020.87, -13083.15) * mm, "end": v(4044.48, -13122.59) * mm});
            skLineSegment(sketch, "E3474", {"start": v(4044.48, -13122.59) * mm, "end": v(4065.2, -13166.68) * mm});
            skLineSegment(sketch, "E3475", {"start": v(4065.2, -13166.68) * mm, "end": v(4082.97, -13215.66) * mm});
            skLineSegment(sketch, "E3476", {"start": v(4082.97, -13215.66) * mm, "end": v(4097.73, -13269.79) * mm});
            skLineSegment(sketch, "E3477", {"start": v(4097.73, -13269.79) * mm, "end": v(4109.42, -13329.3) * mm});
            skLineSegment(sketch, "E3478", {"start": v(4109.42, -13329.3) * mm, "end": v(4115.8, -13376.5) * mm});
            skLineSegment(sketch, "E3479", {"start": v(4115.8, -13376.5) * mm, "end": v(4115.86, -13398.8) * mm});
            skLineSegment(sketch, "E3480", {"start": v(4115.86, -13398.8) * mm, "end": v(4113.17, -13421.57) * mm});
            skLineSegment(sketch, "E3481", {"start": v(4113.17, -13421.57) * mm, "end": v(4107.92, -13444.71) * mm});
            skLineSegment(sketch, "E3482", {"start": v(4107.92, -13444.71) * mm, "end": v(4100.32, -13468.2) * mm});
            skLineSegment(sketch, "E3483", {"start": v(4100.32, -13468.2) * mm, "end": v(4090.58, -13491.96) * mm});
            skLineSegment(sketch, "E3484", {"start": v(4090.58, -13491.96) * mm, "end": v(4078.91, -13515.96) * mm});
            skLineSegment(sketch, "E3485", {"start": v(4078.91, -13515.96) * mm, "end": v(4065.51, -13540.14) * mm});
            skLineSegment(sketch, "E3486", {"start": v(4065.51, -13540.14) * mm, "end": v(4050.6, -13564.44) * mm});
            skLineSegment(sketch, "E3487", {"start": v(4050.6, -13564.44) * mm, "end": v(4034.37, -13588.82) * mm});
            skLineSegment(sketch, "E3488", {"start": v(4034.37, -13588.82) * mm, "end": v(4017.05, -13613.21) * mm});
            skLineSegment(sketch, "E3489", {"start": v(4017.05, -13613.21) * mm, "end": v(3998.83, -13637.57) * mm});
            skLineSegment(sketch, "E3490", {"start": v(3998.83, -13637.57) * mm, "end": v(3979.92, -13661.85) * mm});
            skLineSegment(sketch, "E3491", {"start": v(3979.92, -13661.85) * mm, "end": v(3960.54, -13685.99) * mm});
            skLineSegment(sketch, "E3492", {"start": v(3960.54, -13685.99) * mm, "end": v(3940.9, -13709.93) * mm});
            skLineSegment(sketch, "E3493", {"start": v(3940.9, -13709.93) * mm, "end": v(3921.18, -13733.64) * mm});
            skLineSegment(sketch, "E3494", {"start": v(3921.18, -13733.64) * mm, "end": v(3901.62, -13757.04) * mm});
            skLineSegment(sketch, "E3495", {"start": v(3901.62, -13757.04) * mm, "end": v(3882.41, -13780.1) * mm});
            skLineSegment(sketch, "E3496", {"start": v(3882.41, -13780.1) * mm, "end": v(3863.77, -13802.76) * mm});
            skLineSegment(sketch, "E3497", {"start": v(3863.77, -13802.76) * mm, "end": v(3845.9, -13824.96) * mm});
            skLineSegment(sketch, "E3498", {"start": v(3845.9, -13824.96) * mm, "end": v(3829, -13846.65) * mm});
            skLineSegment(sketch, "E3499", {"start": v(3829, -13846.65) * mm, "end": v(3813.3, -13867.79) * mm});
            skLineSegment(sketch, "E3500", {"start": v(3813.3, -13867.79) * mm, "end": v(3798.99, -13888.3) * mm});
            skLineSegment(sketch, "E3501", {"start": v(3798.99, -13888.3) * mm, "end": v(3786.28, -13908.16) * mm});
            skLineSegment(sketch, "E3502", {"start": v(3786.28, -13908.16) * mm, "end": v(3775.39, -13927.3) * mm});
            skLineSegment(sketch, "E3503", {"start": v(3775.39, -13927.3) * mm, "end": v(3766.5, -13945.66) * mm});
            skLineSegment(sketch, "E3504", {"start": v(3766.5, -13945.66) * mm, "end": v(3759.86, -13963.2) * mm});
            skLineSegment(sketch, "E3505", {"start": v(3759.86, -13963.2) * mm, "end": v(3755.65, -13979.87) * mm});
            skLineSegment(sketch, "E3506", {"start": v(3755.65, -13979.87) * mm, "end": v(3754.08, -13995.6) * mm});
            skLineSegment(sketch, "E3507", {"start": v(3754.08, -13995.6) * mm, "end": v(3755.37, -14010.35) * mm});
            skLineSegment(sketch, "E3508", {"start": v(3755.37, -14010.35) * mm, "end": v(3759.7, -14024.07) * mm});
            skLineSegment(sketch, "E3509", {"start": v(3759.7, -14024.07) * mm, "end": v(3767.32, -14036.7) * mm});
            skLineSegment(sketch, "E3510", {"start": v(3767.32, -14036.7) * mm, "end": v(3778.4, -14048.19) * mm});
            skLineSegment(sketch, "E3511", {"start": v(3778.4, -14048.19) * mm, "end": v(3793.18, -14058.48) * mm});
            skLineSegment(sketch, "E3512", {"start": v(3793.18, -14058.48) * mm, "end": v(3811.85, -14067.53) * mm});
            skLineSegment(sketch, "E3513", {"start": v(3811.85, -14067.53) * mm, "end": v(3834.61, -14075.28) * mm});
            skLineSegment(sketch, "E3514", {"start": v(3834.61, -14075.28) * mm, "end": v(3861.68, -14081.68) * mm});
            skLineSegment(sketch, "E3515", {"start": v(3861.68, -14081.68) * mm, "end": v(3893.27, -14086.68) * mm});
            skLineSegment(sketch, "E3516", {"start": v(3893.27, -14086.68) * mm, "end": v(3929.59, -14090.22) * mm});
            skLineSegment(sketch, "E3517", {"start": v(3929.59, -14090.22) * mm, "end": v(4026.69, -14082.56) * mm});
            skLineSegment(sketch, "E3518", {"start": v(4026.69, -14082.56) * mm, "end": v(4123.17, -14073.65) * mm});
            skLineSegment(sketch, "E3519", {"start": v(4123.17, -14073.65) * mm, "end": v(4219.06, -14063.46) * mm});
            skLineSegment(sketch, "E3520", {"start": v(4219.06, -14063.46) * mm, "end": v(4314.38, -14052) * mm});
            skLineSegment(sketch, "E3521", {"start": v(4314.38, -14052) * mm, "end": v(4409.17, -14039.24) * mm});
            skLineSegment(sketch, "E3522", {"start": v(4409.17, -14039.24) * mm, "end": v(4503.44, -14025.2) * mm});
            skLineSegment(sketch, "E3523", {"start": v(4503.44, -14025.2) * mm, "end": v(4597.22, -14009.87) * mm});
            skLineSegment(sketch, "E3524", {"start": v(4597.22, -14009.87) * mm, "end": v(4690.54, -13993.24) * mm});
            skLineSegment(sketch, "E3525", {"start": v(4690.54, -13993.24) * mm, "end": v(4783.43, -13975.3) * mm});
            skLineSegment(sketch, "E3526", {"start": v(4783.43, -13975.3) * mm, "end": v(4875.92, -13956.03) * mm});
            skLineSegment(sketch, "E3527", {"start": v(4875.92, -13956.03) * mm, "end": v(4968.02, -13935.44) * mm});
            skLineSegment(sketch, "E3528", {"start": v(4968.02, -13935.44) * mm, "end": v(5059.76, -13913.53) * mm});
            skLineSegment(sketch, "E3529", {"start": v(5059.76, -13913.53) * mm, "end": v(5151.18, -13890.29) * mm});
            skLineSegment(sketch, "E3530", {"start": v(5151.18, -13890.29) * mm, "end": v(5242.3, -13865.7) * mm});
            skLineSegment(sketch, "E3531", {"start": v(5242.3, -13865.7) * mm, "end": v(5333.13, -13839.76) * mm});
            skLineSegment(sketch, "E3532", {"start": v(5333.13, -13839.76) * mm, "end": v(5423.72, -13812.47) * mm});
            skLineSegment(sketch, "E3533", {"start": v(5423.72, -13812.47) * mm, "end": v(5514.08, -13783.82) * mm});
            skLineSegment(sketch, "E3534", {"start": v(5514.08, -13783.82) * mm, "end": v(5604.25, -13753.8) * mm});
            skLineSegment(sketch, "E3535", {"start": v(5604.25, -13753.8) * mm, "end": v(5694.25, -13722.4) * mm});
            skLineSegment(sketch, "E3536", {"start": v(5694.25, -13722.4) * mm, "end": v(5784.1, -13689.63) * mm});
            skLineSegment(sketch, "E3537", {"start": v(5784.1, -13689.63) * mm, "end": v(5873.84, -13655.47) * mm});
            skLineSegment(sketch, "E3538", {"start": v(5873.84, -13655.47) * mm, "end": v(5963.49, -13619.92) * mm});
            skLineSegment(sketch, "E3539", {"start": v(5963.49, -13619.92) * mm, "end": v(6053.07, -13582.97) * mm});
            skLineSegment(sketch, "E3540", {"start": v(6053.07, -13582.97) * mm, "end": v(6142.61, -13544.6) * mm});
            skLineSegment(sketch, "E3541", {"start": v(-4479.68, 18406.33) * mm, "end": v(-4475.66, 18395.32) * mm});
            skLineSegment(sketch, "E3542", {"start": v(-4475.66, 18395.32) * mm, "end": v(-4444.25, 18305.34) * mm});
            skLineSegment(sketch, "E3543", {"start": v(-4444.25, 18305.34) * mm, "end": v(-4414.22, 18215.18) * mm});
            skLineSegment(sketch, "E3544", {"start": v(-4414.22, 18215.18) * mm, "end": v(-4385.56, 18124.83) * mm});
            skLineSegment(sketch, "E3545", {"start": v(-4385.56, 18124.83) * mm, "end": v(-4358.26, 18034.25) * mm});
            skLineSegment(sketch, "E3546", {"start": v(-4358.26, 18034.25) * mm, "end": v(-4332.31, 17943.42) * mm});
            skLineSegment(sketch, "E3547", {"start": v(-4332.31, 17943.42) * mm, "end": v(-4307.72, 17852.31) * mm});
            skLineSegment(sketch, "E3548", {"start": v(-4307.72, 17852.31) * mm, "end": v(-4284.46, 17760.9) * mm});
            skLineSegment(sketch, "E3549", {"start": v(-4284.46, 17760.9) * mm, "end": v(-4262.55, 17669.16) * mm});
            skLineSegment(sketch, "E3550", {"start": v(-4262.55, 17669.16) * mm, "end": v(-4241.96, 17577.07) * mm});
            skLineSegment(sketch, "E3551", {"start": v(-4241.96, 17577.07) * mm, "end": v(-4222.7, 17484.6) * mm});
            skLineSegment(sketch, "E3552", {"start": v(-4222.7, 17484.6) * mm, "end": v(-4204.74, 17391.7) * mm});
            skLineSegment(sketch, "E3553", {"start": v(-4204.74, 17391.7) * mm, "end": v(-4188.1, 17298.38) * mm});
            skLineSegment(sketch, "E3554", {"start": v(-4188.1, 17298.38) * mm, "end": v(-4172.77, 17204.6) * mm});
            skLineSegment(sketch, "E3555", {"start": v(-4172.77, 17204.6) * mm, "end": v(-4158.73, 17110.33) * mm});
            skLineSegment(sketch, "E3556", {"start": v(-4158.73, 17110.33) * mm, "end": v(-4145.98, 17015.55) * mm});
            skLineSegment(sketch, "E3557", {"start": v(-4145.98, 17015.55) * mm, "end": v(-4134.51, 16920.23) * mm});
            skLineSegment(sketch, "E3558", {"start": v(-4134.51, 16920.23) * mm, "end": v(-4124.33, 16824.34) * mm});
            skLineSegment(sketch, "E3559", {"start": v(-4124.33, 16824.34) * mm, "end": v(-4115.4, 16727.85) * mm});
            skLineSegment(sketch, "E3560", {"start": v(-4115.4, 16727.85) * mm, "end": v(-4107.75, 16630.75) * mm});
            skLineSegment(sketch, "E3561", {"start": v(-4107.75, 16630.75) * mm, "end": v(-4117.35, 16557.57) * mm});
            skLineSegment(sketch, "E3562", {"start": v(-4117.35, 16557.57) * mm, "end": v(-4133.59, 16505.71) * mm});
            skLineSegment(sketch, "E3563", {"start": v(-4133.59, 16505.71) * mm, "end": v(-4155.92, 16473.02) * mm});
            skLineSegment(sketch, "E3564", {"start": v(-4155.92, 16473.02) * mm, "end": v(-4183.8, 16457.33) * mm});
            skLineSegment(sketch, "E3565", {"start": v(-4183.8, 16457.33) * mm, "end": v(-4216.67, 16456.47) * mm});
            skLineSegment(sketch, "E3566", {"start": v(-4216.67, 16456.47) * mm, "end": v(-4254, 16468.3) * mm});
            skLineSegment(sketch, "E3567", {"start": v(-4254, 16468.3) * mm, "end": v(-4295.21, 16490.65) * mm});
            skLineSegment(sketch, "E3568", {"start": v(-4295.21, 16490.65) * mm, "end": v(-4339.79, 16521.35) * mm});
            skLineSegment(sketch, "E3569", {"start": v(-4339.79, 16521.35) * mm, "end": v(-4387.16, 16558.24) * mm});
            skLineSegment(sketch, "E3570", {"start": v(-4387.16, 16558.24) * mm, "end": v(-4436.79, 16599.17) * mm});
            skLineSegment(sketch, "E3571", {"start": v(-4436.79, 16599.17) * mm, "end": v(-4488.12, 16641.96) * mm});
            skLineSegment(sketch, "E3572", {"start": v(-4488.12, 16641.96) * mm, "end": v(-4540.61, 16684.47) * mm});
            skLineSegment(sketch, "E3573", {"start": v(-4540.61, 16684.47) * mm, "end": v(-4593.71, 16724.52) * mm});
            skLineSegment(sketch, "E3574", {"start": v(-4593.71, 16724.52) * mm, "end": v(-4646.87, 16759.96) * mm});
            skLineSegment(sketch, "E3575", {"start": v(-4646.87, 16759.96) * mm, "end": v(-4699.54, 16788.62) * mm});
            skLineSegment(sketch, "E3576", {"start": v(-4699.54, 16788.62) * mm, "end": v(-4751.18, 16808.34) * mm});
            skLineSegment(sketch, "E3577", {"start": v(-4751.18, 16808.34) * mm, "end": v(-4801.23, 16816.97) * mm});
            skLineSegment(sketch, "E3578", {"start": v(-4801.23, 16816.97) * mm, "end": v(-4858.4, 16812.03) * mm});
            skLineSegment(sketch, "E3579", {"start": v(-4858.4, 16812.03) * mm, "end": v(-4924.04, 16799.7) * mm});
            skLineSegment(sketch, "E3580", {"start": v(-4924.04, 16799.7) * mm, "end": v(-4983.25, 16783.71) * mm});
            skLineSegment(sketch, "E3581", {"start": v(-4983.25, 16783.71) * mm, "end": v(-5036.34, 16764.13) * mm});
            skLineSegment(sketch, "E3582", {"start": v(-5036.34, 16764.13) * mm, "end": v(-5083.64, 16741.05) * mm});
            skLineSegment(sketch, "E3583", {"start": v(-5083.64, 16741.05) * mm, "end": v(-5125.46, 16714.53) * mm});
            skLineSegment(sketch, "E3584", {"start": v(-5125.46, 16714.53) * mm, "end": v(-5162.12, 16684.66) * mm});
            skLineSegment(sketch, "E3585", {"start": v(-5162.12, 16684.66) * mm, "end": v(-5193.95, 16651.51) * mm});
            skLineSegment(sketch, "E3586", {"start": v(-5193.95, 16651.51) * mm, "end": v(-5221.26, 16615.17) * mm});
            skLineSegment(sketch, "E3587", {"start": v(-5221.26, 16615.17) * mm, "end": v(-5244.36, 16575.72) * mm});
            skLineSegment(sketch, "E3588", {"start": v(-5244.36, 16575.72) * mm, "end": v(-5263.59, 16533.22) * mm});
            skLineSegment(sketch, "E3589", {"start": v(-5263.59, 16533.22) * mm, "end": v(-5279.25, 16487.76) * mm});
            skLineSegment(sketch, "E3590", {"start": v(-5279.25, 16487.76) * mm, "end": v(-5291.66, 16439.42) * mm});
            skLineSegment(sketch, "E3591", {"start": v(-5291.66, 16439.42) * mm, "end": v(-5301.15, 16388.28) * mm});
            skLineSegment(sketch, "E3592", {"start": v(-5301.15, 16388.28) * mm, "end": v(-5308.04, 16334.41) * mm});
            skLineSegment(sketch, "E3593", {"start": v(-5308.04, 16334.41) * mm, "end": v(-5312.63, 16277.9) * mm});
            skLineSegment(sketch, "E3594", {"start": v(-5312.63, 16277.9) * mm, "end": v(-5315.26, 16218.8) * mm});
            skLineSegment(sketch, "E3595", {"start": v(-5315.26, 16218.8) * mm, "end": v(-5316.24, 16157.23) * mm});
            skLineSegment(sketch, "E3596", {"start": v(-5316.24, 16157.23) * mm, "end": v(-5315.83, 16094.78) * mm});
            skLineSegment(sketch, "E3597", {"start": v(-5315.83, 16094.78) * mm, "end": v(-5313.9, 16034.69) * mm});
            skLineSegment(sketch, "E3598", {"start": v(-5313.9, 16034.69) * mm, "end": v(-5310.13, 15977.13) * mm});
            skLineSegment(sketch, "E3599", {"start": v(-5310.13, 15977.13) * mm, "end": v(-5304.2, 15922.2) * mm});
            skLineSegment(sketch, "E3600", {"start": v(-5304.2, 15922.2) * mm, "end": v(-5295.8, 15869.95) * mm});
            skLineSegment(sketch, "E3601", {"start": v(-5295.8, 15869.95) * mm, "end": v(-5284.58, 15820.48) * mm});
            skLineSegment(sketch, "E3602", {"start": v(-5284.58, 15820.48) * mm, "end": v(-5270.26, 15773.86) * mm});
            skLineSegment(sketch, "E3603", {"start": v(-5270.26, 15773.86) * mm, "end": v(-5252.5, 15730.17) * mm});
            skLineSegment(sketch, "E3604", {"start": v(-5252.5, 15730.17) * mm, "end": v(-5230.99, 15689.48) * mm});
            skLineSegment(sketch, "E3605", {"start": v(-5230.99, 15689.48) * mm, "end": v(-5205.4, 15651.88) * mm});
            skLineSegment(sketch, "E3606", {"start": v(-5205.4, 15651.88) * mm, "end": v(-5175.42, 15617.45) * mm});
            skLineSegment(sketch, "E3607", {"start": v(-5175.42, 15617.45) * mm, "end": v(-5140.73, 15586.25) * mm});
            skLineSegment(sketch, "E3608", {"start": v(-5140.73, 15586.25) * mm, "end": v(-5101, 15558.38) * mm});
            skLineSegment(sketch, "E3609", {"start": v(-5101, 15558.38) * mm, "end": v(-5055.94, 15533.9) * mm});
            skLineSegment(sketch, "E3610", {"start": v(-5055.94, 15533.9) * mm, "end": v(-5005.2, 15512.9) * mm});
            skLineSegment(sketch, "E3611", {"start": v(-5005.2, 15512.9) * mm, "end": v(-4948.48, 15495.46) * mm});
            skLineSegment(sketch, "E3612", {"start": v(-4948.48, 15495.46) * mm, "end": v(-4885.45, 15481.65) * mm});
            skLineSegment(sketch, "E3613", {"start": v(-4885.45, 15481.65) * mm, "end": v(-4825.49, 15472.74) * mm});
            skLineSegment(sketch, "E3614", {"start": v(-4825.49, 15472.74) * mm, "end": v(-4801.23, 15472.22) * mm});
            skLineSegment(sketch, "E3615", {"start": v(-4801.23, 15472.22) * mm, "end": v(-4776.44, 15475) * mm});
            skLineSegment(sketch, "E3616", {"start": v(-4776.44, 15475) * mm, "end": v(-4751.18, 15480.84) * mm});
            skLineSegment(sketch, "E3617", {"start": v(-4751.18, 15480.84) * mm, "end": v(-4725.53, 15489.45) * mm});
            skLineSegment(sketch, "E3618", {"start": v(-4725.53, 15489.45) * mm, "end": v(-4699.54, 15500.56) * mm});
            skLineSegment(sketch, "E3619", {"start": v(-4699.54, 15500.56) * mm, "end": v(-4673.3, 15513.91) * mm});
            skLineSegment(sketch, "E3620", {"start": v(-4673.3, 15513.91) * mm, "end": v(-4646.87, 15529.23) * mm});
            skLineSegment(sketch, "E3621", {"start": v(-4646.87, 15529.23) * mm, "end": v(-4620.32, 15546.23) * mm});
            skLineSegment(sketch, "E3622", {"start": v(-4620.32, 15546.23) * mm, "end": v(-4593.71, 15564.66) * mm});
            skLineSegment(sketch, "E3623", {"start": v(-4593.71, 15564.66) * mm, "end": v(-4567.12, 15584.25) * mm});
            skLineSegment(sketch, "E3624", {"start": v(-4567.12, 15584.25) * mm, "end": v(-4540.61, 15604.72) * mm});
            skLineSegment(sketch, "E3625", {"start": v(-4540.61, 15604.72) * mm, "end": v(-4514.26, 15625.8) * mm});
            skLineSegment(sketch, "E3626", {"start": v(-4514.26, 15625.8) * mm, "end": v(-4488.12, 15647.22) * mm});
            skLineSegment(sketch, "E3627", {"start": v(-4488.12, 15647.22) * mm, "end": v(-4462.28, 15668.72) * mm});
            skLineSegment(sketch, "E3628", {"start": v(-4462.28, 15668.72) * mm, "end": v(-4436.79, 15690.02) * mm});
            skLineSegment(sketch, "E3629", {"start": v(-4436.79, 15690.02) * mm, "end": v(-4411.73, 15710.85) * mm});
            skLineSegment(sketch, "E3630", {"start": v(-4411.73, 15710.85) * mm, "end": v(-4387.16, 15730.94) * mm});
            skLineSegment(sketch, "E3631", {"start": v(-4387.16, 15730.94) * mm, "end": v(-4363.16, 15750.03) * mm});
            skLineSegment(sketch, "E3632", {"start": v(-4363.16, 15750.03) * mm, "end": v(-4339.79, 15767.84) * mm});
            skLineSegment(sketch, "E3633", {"start": v(-4339.79, 15767.84) * mm, "end": v(-4317.11, 15784.1) * mm});
            skLineSegment(sketch, "E3634", {"start": v(-4317.11, 15784.1) * mm, "end": v(-4295.21, 15798.54) * mm});
            skLineSegment(sketch, "E3635", {"start": v(-4295.21, 15798.54) * mm, "end": v(-4274.15, 15810.9) * mm});
            skLineSegment(sketch, "E3636", {"start": v(-4274.15, 15810.9) * mm, "end": v(-4254, 15820.88) * mm});
            skLineSegment(sketch, "E3637", {"start": v(-4254, 15820.88) * mm, "end": v(-4234.8, 15828.25) * mm});
            skLineSegment(sketch, "E3638", {"start": v(-4234.8, 15828.25) * mm, "end": v(-4216.67, 15832.71) * mm});
            skLineSegment(sketch, "E3639", {"start": v(-4216.67, 15832.71) * mm, "end": v(-4199.64, 15834) * mm});
            skLineSegment(sketch, "E3640", {"start": v(-4199.64, 15834) * mm, "end": v(-4183.8, 15831.86) * mm});
            skLineSegment(sketch, "E3641", {"start": v(-4183.8, 15831.86) * mm, "end": v(-4169.2, 15826) * mm});
            skLineSegment(sketch, "E3642", {"start": v(-4169.2, 15826) * mm, "end": v(-4155.92, 15816.17) * mm});
            skLineSegment(sketch, "E3643", {"start": v(-4155.92, 15816.17) * mm, "end": v(-4144.03, 15802.08) * mm});
            skLineSegment(sketch, "E3644", {"start": v(-4144.03, 15802.08) * mm, "end": v(-4133.59, 15783.47) * mm});
            skLineSegment(sketch, "E3645", {"start": v(-4133.59, 15783.47) * mm, "end": v(-4124.67, 15760.08) * mm});
            skLineSegment(sketch, "E3646", {"start": v(-4124.67, 15760.08) * mm, "end": v(-4117.35, 15731.62) * mm});
            skLineSegment(sketch, "E3647", {"start": v(-4117.35, 15731.62) * mm, "end": v(-4111.69, 15697.82) * mm});
            skLineSegment(sketch, "E3648", {"start": v(-4111.69, 15697.82) * mm, "end": v(-4107.75, 15658.43) * mm});
            skLineSegment(sketch, "E3649", {"start": v(-4107.75, 15658.43) * mm, "end": v(-4115.4, 15561.35) * mm});
            skLineSegment(sketch, "E3650", {"start": v(-4115.4, 15561.35) * mm, "end": v(-4124.33, 15464.9) * mm});
            skLineSegment(sketch, "E3651", {"start": v(-4124.33, 15464.9) * mm, "end": v(-4134.51, 15369.02) * mm});
            skLineSegment(sketch, "E3652", {"start": v(-4134.51, 15369.02) * mm, "end": v(-4145.98, 15273.72) * mm});
            skLineSegment(sketch, "E3653", {"start": v(-4145.98, 15273.72) * mm, "end": v(-4158.73, 15178.95) * mm});
            skLineSegment(sketch, "E3654", {"start": v(-4158.73, 15178.95) * mm, "end": v(-4172.77, 15084.7) * mm});
            skLineSegment(sketch, "E3655", {"start": v(-4172.77, 15084.7) * mm, "end": v(-4188.1, 14990.92) * mm});
            skLineSegment(sketch, "E3656", {"start": v(-4188.1, 14990.92) * mm, "end": v(-4204.74, 14897.6) * mm});
            skLineSegment(sketch, "E3657", {"start": v(-4204.74, 14897.6) * mm, "end": v(-4222.7, 14804.73) * mm});
            skLineSegment(sketch, "E3658", {"start": v(-4222.7, 14804.73) * mm, "end": v(-4241.96, 14712.26) * mm});
            skLineSegment(sketch, "E3659", {"start": v(-4241.96, 14712.26) * mm, "end": v(-4262.55, 14620.16) * mm});
            skLineSegment(sketch, "E3660", {"start": v(-4262.55, 14620.16) * mm, "end": v(-4284.46, 14528.43) * mm});
            skLineSegment(sketch, "E3661", {"start": v(-4284.46, 14528.43) * mm, "end": v(-4307.72, 14437.02) * mm});
            skLineSegment(sketch, "E3662", {"start": v(-4307.72, 14437.02) * mm, "end": v(-4332.31, 14345.9) * mm});
            skLineSegment(sketch, "E3663", {"start": v(-4332.31, 14345.9) * mm, "end": v(-4358.26, 14255.07) * mm});
            skLineSegment(sketch, "E3664", {"start": v(-4358.26, 14255.07) * mm, "end": v(-4385.56, 14164.49) * mm});
            skLineSegment(sketch, "E3665", {"start": v(-4385.56, 14164.49) * mm, "end": v(-4414.22, 14074.12) * mm});
            skLineSegment(sketch, "E3666", {"start": v(-4414.22, 14074.12) * mm, "end": v(-4444.25, 13983.95) * mm});
            skLineSegment(sketch, "E3667", {"start": v(-4444.25, 13983.95) * mm, "end": v(-4475.66, 13893.96) * mm});
            skLineSegment(sketch, "E3668", {"start": v(-4475.66, 13893.96) * mm, "end": v(-4508.45, 13804.1) * mm});
            skLineSegment(sketch, "E3669", {"start": v(-4508.45, 13804.1) * mm, "end": v(-4542.63, 13714.37) * mm});
            skLineSegment(sketch, "E3670", {"start": v(-4542.63, 13714.37) * mm, "end": v(-4578.2, 13624.72) * mm});
            skLineSegment(sketch, "E3671", {"start": v(-4578.2, 13624.72) * mm, "end": v(-4615.18, 13535.14) * mm});
            skLineSegment(sketch, "E3672", {"start": v(-4615.18, 13535.14) * mm, "end": v(-4653.56, 13445.6) * mm});
            skLineSegment(sketch, "E3673", {"start": v(744.62, 13445.6) * mm, "end": v(706.24, 13535.14) * mm});
            skLineSegment(sketch, "E3674", {"start": v(706.24, 13535.14) * mm, "end": v(669.27, 13624.72) * mm});
            skLineSegment(sketch, "E3675", {"start": v(669.27, 13624.72) * mm, "end": v(633.7, 13714.37) * mm});
            skLineSegment(sketch, "E3676", {"start": v(633.7, 13714.37) * mm, "end": v(599.52, 13804.1) * mm});
            skLineSegment(sketch, "E3677", {"start": v(599.52, 13804.1) * mm, "end": v(566.73, 13893.96) * mm});
            skLineSegment(sketch, "E3678", {"start": v(566.73, 13893.96) * mm, "end": v(535.32, 13983.95) * mm});
            skLineSegment(sketch, "E3679", {"start": v(535.32, 13983.95) * mm, "end": v(505.29, 14074.12) * mm});
            skLineSegment(sketch, "E3680", {"start": v(505.29, 14074.12) * mm, "end": v(476.62, 14164.49) * mm});
            skLineSegment(sketch, "E3681", {"start": v(476.62, 14164.49) * mm, "end": v(449.32, 14255.07) * mm});
            skLineSegment(sketch, "E3682", {"start": v(449.32, 14255.07) * mm, "end": v(423.37, 14345.9) * mm});
            skLineSegment(sketch, "E3683", {"start": v(423.37, 14345.9) * mm, "end": v(398.78, 14437.02) * mm});
            skLineSegment(sketch, "E3684", {"start": v(398.78, 14437.02) * mm, "end": v(375.52, 14528.43) * mm});
            skLineSegment(sketch, "E3685", {"start": v(375.52, 14528.43) * mm, "end": v(353.6, 14620.16) * mm});
            skLineSegment(sketch, "E3686", {"start": v(353.6, 14620.16) * mm, "end": v(333, 14712.26) * mm});
            skLineSegment(sketch, "E3687", {"start": v(333, 14712.26) * mm, "end": v(313.74, 14804.73) * mm});
            skLineSegment(sketch, "E3688", {"start": v(313.74, 14804.73) * mm, "end": v(295.79, 14897.6) * mm});
            skLineSegment(sketch, "E3689", {"start": v(295.79, 14897.6) * mm, "end": v(279.15, 14990.92) * mm});
            skLineSegment(sketch, "E3690", {"start": v(279.15, 14990.92) * mm, "end": v(263.8, 15084.7) * mm});
            skLineSegment(sketch, "E3691", {"start": v(263.8, 15084.7) * mm, "end": v(249.76, 15178.95) * mm});
            skLineSegment(sketch, "E3692", {"start": v(249.76, 15178.95) * mm, "end": v(237, 15273.72) * mm});
            skLineSegment(sketch, "E3693", {"start": v(237, 15273.72) * mm, "end": v(225.54, 15369.02) * mm});
            skLineSegment(sketch, "E3694", {"start": v(225.54, 15369.02) * mm, "end": v(215.34, 15464.9) * mm});
            skLineSegment(sketch, "E3695", {"start": v(215.34, 15464.9) * mm, "end": v(206.42, 15561.35) * mm});
            skLineSegment(sketch, "E3696", {"start": v(206.42, 15561.35) * mm, "end": v(198.75, 15658.43) * mm});
            skLineSegment(sketch, "E3697", {"start": v(198.75, 15658.43) * mm, "end": v(208.36, 15731.62) * mm});
            skLineSegment(sketch, "E3698", {"start": v(208.36, 15731.62) * mm, "end": v(224.6, 15783.47) * mm});
            skLineSegment(sketch, "E3699", {"start": v(224.6, 15783.47) * mm, "end": v(246.95, 15816.17) * mm});
            skLineSegment(sketch, "E3700", {"start": v(246.95, 15816.17) * mm, "end": v(274.83, 15831.86) * mm});
            skLineSegment(sketch, "E3701", {"start": v(274.83, 15831.86) * mm, "end": v(307.71, 15832.71) * mm});
            skLineSegment(sketch, "E3702", {"start": v(307.71, 15832.71) * mm, "end": v(345.04, 15820.88) * mm});
            skLineSegment(sketch, "E3703", {"start": v(345.04, 15820.88) * mm, "end": v(386.26, 15798.54) * mm});
            skLineSegment(sketch, "E3704", {"start": v(386.26, 15798.54) * mm, "end": v(430.84, 15767.84) * mm});
            skLineSegment(sketch, "E3705", {"start": v(430.84, 15767.84) * mm, "end": v(478.22, 15730.94) * mm});
            skLineSegment(sketch, "E3706", {"start": v(478.22, 15730.94) * mm, "end": v(527.85, 15690.02) * mm});
            skLineSegment(sketch, "E3707", {"start": v(527.85, 15690.02) * mm, "end": v(579.18, 15647.22) * mm});
            skLineSegment(sketch, "E3708", {"start": v(579.18, 15647.22) * mm, "end": v(631.68, 15604.72) * mm});
            skLineSegment(sketch, "E3709", {"start": v(631.68, 15604.72) * mm, "end": v(684.78, 15564.66) * mm});
            skLineSegment(sketch, "E3710", {"start": v(684.78, 15564.66) * mm, "end": v(737.94, 15529.23) * mm});
            skLineSegment(sketch, "E3711", {"start": v(737.94, 15529.23) * mm, "end": v(790.6, 15500.56) * mm});
            skLineSegment(sketch, "E3712", {"start": v(790.6, 15500.56) * mm, "end": v(842.24, 15480.84) * mm});
            skLineSegment(sketch, "E3713", {"start": v(842.24, 15480.84) * mm, "end": v(892.3, 15472.22) * mm});
            skLineSegment(sketch, "E3714", {"start": v(892.3, 15472.22) * mm, "end": v(949.46, 15477.17) * mm});
            skLineSegment(sketch, "E3715", {"start": v(949.46, 15477.17) * mm, "end": v(1015.1, 15489.52) * mm});
            skLineSegment(sketch, "E3716", {"start": v(1015.1, 15489.52) * mm, "end": v(1074.31, 15505.54) * mm});
            skLineSegment(sketch, "E3717", {"start": v(1074.31, 15505.54) * mm, "end": v(1127.4, 15525.13) * mm});
            skLineSegment(sketch, "E3718", {"start": v(1127.4, 15525.13) * mm, "end": v(1174.7, 15548.23) * mm});
            skLineSegment(sketch, "E3719", {"start": v(1174.7, 15548.23) * mm, "end": v(1216.52, 15574.76) * mm});
            skLineSegment(sketch, "E3720", {"start": v(1216.52, 15574.76) * mm, "end": v(1253.19, 15604.63) * mm});
            skLineSegment(sketch, "E3721", {"start": v(1253.19, 15604.63) * mm, "end": v(1285.02, 15637.78) * mm});
            skLineSegment(sketch, "E3722", {"start": v(1285.02, 15637.78) * mm, "end": v(1312.32, 15674.12) * mm});
            skLineSegment(sketch, "E3723", {"start": v(1312.32, 15674.12) * mm, "end": v(1335.43, 15713.57) * mm});
            skLineSegment(sketch, "E3724", {"start": v(1335.43, 15713.57) * mm, "end": v(1354.65, 15756.06) * mm});
            skLineSegment(sketch, "E3725", {"start": v(1354.65, 15756.06) * mm, "end": v(1370.31, 15801.51) * mm});
            skLineSegment(sketch, "E3726", {"start": v(1370.31, 15801.51) * mm, "end": v(1382.73, 15849.85) * mm});
            skLineSegment(sketch, "E3727", {"start": v(1382.73, 15849.85) * mm, "end": v(1392.22, 15900.98) * mm});
            skLineSegment(sketch, "E3728", {"start": v(1392.22, 15900.98) * mm, "end": v(1399.1, 15954.85) * mm});
            skLineSegment(sketch, "E3729", {"start": v(1399.1, 15954.85) * mm, "end": v(1403.7, 16011.36) * mm});
            skLineSegment(sketch, "E3730", {"start": v(1403.7, 16011.36) * mm, "end": v(1406.33, 16070.44) * mm});
            skLineSegment(sketch, "E3731", {"start": v(1406.33, 16070.44) * mm, "end": v(1407.3, 16132.02) * mm});
            skLineSegment(sketch, "E3732", {"start": v(1407.3, 16132.02) * mm, "end": v(1406.9, 16194.47) * mm});
            skLineSegment(sketch, "E3733", {"start": v(1406.9, 16194.47) * mm, "end": v(1404.97, 16254.56) * mm});
            skLineSegment(sketch, "E3734", {"start": v(1404.97, 16254.56) * mm, "end": v(1401.2, 16312.12) * mm});
            skLineSegment(sketch, "E3735", {"start": v(1401.2, 16312.12) * mm, "end": v(1395.27, 16367.06) * mm});
            skLineSegment(sketch, "E3736", {"start": v(1395.27, 16367.06) * mm, "end": v(1386.86, 16419.3) * mm});
            skLineSegment(sketch, "E3737", {"start": v(1386.86, 16419.3) * mm, "end": v(1375.65, 16468.77) * mm});
            skLineSegment(sketch, "E3738", {"start": v(1375.65, 16468.77) * mm, "end": v(1361.32, 16515.39) * mm});
            skLineSegment(sketch, "E3739", {"start": v(1361.32, 16515.39) * mm, "end": v(1343.56, 16559.08) * mm});
            skLineSegment(sketch, "E3740", {"start": v(1343.56, 16559.08) * mm, "end": v(1322.05, 16599.76) * mm});
            skLineSegment(sketch, "E3741", {"start": v(1322.05, 16599.76) * mm, "end": v(1296.46, 16637.36) * mm});
            skLineSegment(sketch, "E3742", {"start": v(1296.46, 16637.36) * mm, "end": v(1266.48, 16671.79) * mm});
            skLineSegment(sketch, "E3743", {"start": v(1266.48, 16671.79) * mm, "end": v(1231.8, 16702.98) * mm});
            skLineSegment(sketch, "E3744", {"start": v(1231.8, 16702.98) * mm, "end": v(1192.07, 16730.85) * mm});
            skLineSegment(sketch, "E3745", {"start": v(1192.07, 16730.85) * mm, "end": v(1147, 16755.31) * mm});
            skLineSegment(sketch, "E3746", {"start": v(1147, 16755.31) * mm, "end": v(1096.26, 16776.3) * mm});
            skLineSegment(sketch, "E3747", {"start": v(1096.26, 16776.3) * mm, "end": v(1039.54, 16793.74) * mm});
            skLineSegment(sketch, "E3748", {"start": v(1039.54, 16793.74) * mm, "end": v(976.51, 16807.54) * mm});
            skLineSegment(sketch, "E3749", {"start": v(976.51, 16807.54) * mm, "end": v(916.55, 16816.44) * mm});
            skLineSegment(sketch, "E3750", {"start": v(916.55, 16816.44) * mm, "end": v(892.3, 16816.97) * mm});
            skLineSegment(sketch, "E3751", {"start": v(892.3, 16816.97) * mm, "end": v(867.5, 16814.18) * mm});
            skLineSegment(sketch, "E3752", {"start": v(867.5, 16814.18) * mm, "end": v(842.24, 16808.34) * mm});
            skLineSegment(sketch, "E3753", {"start": v(842.24, 16808.34) * mm, "end": v(816.6, 16799.73) * mm});
            skLineSegment(sketch, "E3754", {"start": v(816.6, 16799.73) * mm, "end": v(790.6, 16788.62) * mm});
            skLineSegment(sketch, "E3755", {"start": v(790.6, 16788.62) * mm, "end": v(764.37, 16775.27) * mm});
            skLineSegment(sketch, "E3756", {"start": v(764.37, 16775.27) * mm, "end": v(737.94, 16759.96) * mm});
            skLineSegment(sketch, "E3757", {"start": v(737.94, 16759.96) * mm, "end": v(711.38, 16742.95) * mm});
            skLineSegment(sketch, "E3758", {"start": v(711.38, 16742.95) * mm, "end": v(684.78, 16724.52) * mm});
            skLineSegment(sketch, "E3759", {"start": v(684.78, 16724.52) * mm, "end": v(658.19, 16704.94) * mm});
            skLineSegment(sketch, "E3760", {"start": v(658.19, 16704.94) * mm, "end": v(631.68, 16684.47) * mm});
            skLineSegment(sketch, "E3761", {"start": v(631.68, 16684.47) * mm, "end": v(605.32, 16663.39) * mm});
            skLineSegment(sketch, "E3762", {"start": v(605.32, 16663.39) * mm, "end": v(579.18, 16641.96) * mm});
            skLineSegment(sketch, "E3763", {"start": v(579.18, 16641.96) * mm, "end": v(553.34, 16620.47) * mm});
            skLineSegment(sketch, "E3764", {"start": v(553.34, 16620.47) * mm, "end": v(527.85, 16599.17) * mm});
            skLineSegment(sketch, "E3765", {"start": v(527.85, 16599.17) * mm, "end": v(502.79, 16578.34) * mm});
            skLineSegment(sketch, "E3766", {"start": v(502.79, 16578.34) * mm, "end": v(478.22, 16558.24) * mm});
            skLineSegment(sketch, "E3767", {"start": v(478.22, 16558.24) * mm, "end": v(454.21, 16539.16) * mm});
            skLineSegment(sketch, "E3768", {"start": v(454.21, 16539.16) * mm, "end": v(430.84, 16521.35) * mm});
            skLineSegment(sketch, "E3769", {"start": v(430.84, 16521.35) * mm, "end": v(408.17, 16505.09) * mm});
            skLineSegment(sketch, "E3770", {"start": v(408.17, 16505.09) * mm, "end": v(386.26, 16490.65) * mm});
            skLineSegment(sketch, "E3771", {"start": v(386.26, 16490.65) * mm, "end": v(365.2, 16478.3) * mm});
            skLineSegment(sketch, "E3772", {"start": v(365.2, 16478.3) * mm, "end": v(345.04, 16468.3) * mm});
            skLineSegment(sketch, "E3773", {"start": v(345.04, 16468.3) * mm, "end": v(325.85, 16460.94) * mm});
            skLineSegment(sketch, "E3774", {"start": v(325.85, 16460.94) * mm, "end": v(307.71, 16456.47) * mm});
            skLineSegment(sketch, "E3775", {"start": v(307.71, 16456.47) * mm, "end": v(290.68, 16455.18) * mm});
            skLineSegment(sketch, "E3776", {"start": v(290.68, 16455.18) * mm, "end": v(274.83, 16457.33) * mm});
            skLineSegment(sketch, "E3777", {"start": v(274.83, 16457.33) * mm, "end": v(260.23, 16463.18) * mm});
            skLineSegment(sketch, "E3778", {"start": v(260.23, 16463.18) * mm, "end": v(246.95, 16473.02) * mm});
            skLineSegment(sketch, "E3779", {"start": v(246.95, 16473.02) * mm, "end": v(235.05, 16487.1) * mm});
            skLineSegment(sketch, "E3780", {"start": v(235.05, 16487.1) * mm, "end": v(224.6, 16505.71) * mm});
            skLineSegment(sketch, "E3781", {"start": v(224.6, 16505.71) * mm, "end": v(215.69, 16529.1) * mm});
            skLineSegment(sketch, "E3782", {"start": v(215.69, 16529.1) * mm, "end": v(208.36, 16557.57) * mm});
            skLineSegment(sketch, "E3783", {"start": v(208.36, 16557.57) * mm, "end": v(202.7, 16591.36) * mm});
            skLineSegment(sketch, "E3784", {"start": v(202.7, 16591.36) * mm, "end": v(198.75, 16630.75) * mm});
            skLineSegment(sketch, "E3785", {"start": v(198.75, 16630.75) * mm, "end": v(206.42, 16727.85) * mm});
            skLineSegment(sketch, "E3786", {"start": v(206.42, 16727.85) * mm, "end": v(215.34, 16824.34) * mm});
            skLineSegment(sketch, "E3787", {"start": v(215.34, 16824.34) * mm, "end": v(225.54, 16920.23) * mm});
            skLineSegment(sketch, "E3788", {"start": v(225.54, 16920.23) * mm, "end": v(237, 17015.55) * mm});
            skLineSegment(sketch, "E3789", {"start": v(237, 17015.55) * mm, "end": v(249.76, 17110.33) * mm});
            skLineSegment(sketch, "E3790", {"start": v(249.76, 17110.33) * mm, "end": v(263.8, 17204.6) * mm});
            skLineSegment(sketch, "E3791", {"start": v(263.8, 17204.6) * mm, "end": v(279.15, 17298.38) * mm});
            skLineSegment(sketch, "E3792", {"start": v(279.15, 17298.38) * mm, "end": v(295.79, 17391.7) * mm});
            skLineSegment(sketch, "E3793", {"start": v(295.79, 17391.7) * mm, "end": v(313.74, 17484.6) * mm});
            skLineSegment(sketch, "E3794", {"start": v(313.74, 17484.6) * mm, "end": v(333, 17577.07) * mm});
            skLineSegment(sketch, "E3795", {"start": v(333, 17577.07) * mm, "end": v(353.6, 17669.16) * mm});
            skLineSegment(sketch, "E3796", {"start": v(353.6, 17669.16) * mm, "end": v(375.52, 17760.9) * mm});
            skLineSegment(sketch, "E3797", {"start": v(375.52, 17760.9) * mm, "end": v(398.78, 17852.31) * mm});
            skLineSegment(sketch, "E3798", {"start": v(398.78, 17852.31) * mm, "end": v(423.37, 17943.42) * mm});
            skLineSegment(sketch, "E3799", {"start": v(423.37, 17943.42) * mm, "end": v(449.32, 18034.25) * mm});
            skLineSegment(sketch, "E3800", {"start": v(449.32, 18034.25) * mm, "end": v(476.62, 18124.83) * mm});
            skLineSegment(sketch, "E3801", {"start": v(476.62, 18124.83) * mm, "end": v(505.29, 18215.18) * mm});
            skLineSegment(sketch, "E3802", {"start": v(505.29, 18215.18) * mm, "end": v(535.32, 18305.34) * mm});
            skLineSegment(sketch, "E3803", {"start": v(535.32, 18305.34) * mm, "end": v(566.73, 18395.32) * mm});
            skLineSegment(sketch, "E3804", {"start": v(566.73, 18395.32) * mm, "end": v(599.52, 18485.16) * mm});
            skLineSegment(sketch, "E3805", {"start": v(599.52, 18485.16) * mm, "end": v(633.7, 18574.88) * mm});
            skLineSegment(sketch, "E3806", {"start": v(633.7, 18574.88) * mm, "end": v(669.27, 18664.5) * mm});
            skLineSegment(sketch, "E3807", {"start": v(669.27, 18664.5) * mm, "end": v(706.24, 18754.07) * mm});
            skLineSegment(sketch, "E3808", {"start": v(706.24, 18754.07) * mm, "end": v(817.24, 19012.95) * mm});
            skLineSegment(sketch, "E3809", {"start": v(-4459.85, -18448.93) * mm, "end": v(-4444.25, -18404.24) * mm});
            skLineSegment(sketch, "E3810", {"start": v(-4444.25, -18404.24) * mm, "end": v(-4414.22, -18314.07) * mm});
            skLineSegment(sketch, "E3811", {"start": v(-4414.22, -18314.07) * mm, "end": v(-4385.56, -18223.7) * mm});
            skLineSegment(sketch, "E3812", {"start": v(-4385.56, -18223.7) * mm, "end": v(-4358.26, -18133.11) * mm});
            skLineSegment(sketch, "E3813", {"start": v(-4358.26, -18133.11) * mm, "end": v(-4332.31, -18042.27) * mm});
            skLineSegment(sketch, "E3814", {"start": v(-4332.31, -18042.27) * mm, "end": v(-4307.72, -17951.16) * mm});
            skLineSegment(sketch, "E3815", {"start": v(-4307.72, -17951.16) * mm, "end": v(-4284.46, -17859.74) * mm});
            skLineSegment(sketch, "E3816", {"start": v(-4284.46, -17859.74) * mm, "end": v(-4262.55, -17768) * mm});
            skLineSegment(sketch, "E3817", {"start": v(-4262.55, -17768) * mm, "end": v(-4241.96, -17675.9) * mm});
            skLineSegment(sketch, "E3818", {"start": v(-4241.96, -17675.9) * mm, "end": v(-4222.7, -17583.42) * mm});
            skLineSegment(sketch, "E3819", {"start": v(-4222.7, -17583.42) * mm, "end": v(-4204.74, -17490.53) * mm});
            skLineSegment(sketch, "E3820", {"start": v(-4204.74, -17490.53) * mm, "end": v(-4188.1, -17397.2) * mm});
            skLineSegment(sketch, "E3821", {"start": v(-4188.1, -17397.2) * mm, "end": v(-4172.77, -17303.42) * mm});
            skLineSegment(sketch, "E3822", {"start": v(-4172.77, -17303.42) * mm, "end": v(-4158.73, -17209.15) * mm});
            skLineSegment(sketch, "E3823", {"start": v(-4158.73, -17209.15) * mm, "end": v(-4145.98, -17114.36) * mm});
            skLineSegment(sketch, "E3824", {"start": v(-4145.98, -17114.36) * mm, "end": v(-4134.51, -17019.04) * mm});
            skLineSegment(sketch, "E3825", {"start": v(-4134.51, -17019.04) * mm, "end": v(-4124.33, -16923.15) * mm});
            skLineSegment(sketch, "E3826", {"start": v(-4124.33, -16923.15) * mm, "end": v(-4115.4, -16826.67) * mm});
            skLineSegment(sketch, "E3827", {"start": v(-4115.4, -16826.67) * mm, "end": v(-4107.75, -16729.57) * mm});
            skLineSegment(sketch, "E3828", {"start": v(-4107.75, -16729.57) * mm, "end": v(-4116.29, -16661.67) * mm});
            skLineSegment(sketch, "E3829", {"start": v(-4116.29, -16661.67) * mm, "end": v(-4130.44, -16611.83) * mm});
            skLineSegment(sketch, "E3830", {"start": v(-4130.44, -16611.83) * mm, "end": v(-4149.8, -16578.4) * mm});
            skLineSegment(sketch, "E3831", {"start": v(-4149.8, -16578.4) * mm, "end": v(-4173.92, -16559.71) * mm});
            skLineSegment(sketch, "E3832", {"start": v(-4173.92, -16559.71) * mm, "end": v(-4202.4, -16554.1) * mm});
            skLineSegment(sketch, "E3833", {"start": v(-4202.4, -16554.1) * mm, "end": v(-4234.8, -16559.88) * mm});
            skLineSegment(sketch, "E3834", {"start": v(-4234.8, -16559.88) * mm, "end": v(-4270.72, -16575.42) * mm});
            skLineSegment(sketch, "E3835", {"start": v(-4270.72, -16575.42) * mm, "end": v(-4309.73, -16599.03) * mm});
            skLineSegment(sketch, "E3836", {"start": v(-4309.73, -16599.03) * mm, "end": v(-4351.39, -16629.05) * mm});
            skLineSegment(sketch, "E3837", {"start": v(-4351.39, -16629.05) * mm, "end": v(-4395.29, -16663.83) * mm});
            skLineSegment(sketch, "E3838", {"start": v(-4395.29, -16663.83) * mm, "end": v(-4441, -16701.69) * mm});
            skLineSegment(sketch, "E3839", {"start": v(-4441, -16701.69) * mm, "end": v(-4488.12, -16740.96) * mm});
            skLineSegment(sketch, "E3840", {"start": v(-4488.12, -16740.96) * mm, "end": v(-4536.2, -16780) * mm});
            skLineSegment(sketch, "E3841", {"start": v(-4536.2, -16780) * mm, "end": v(-4584.84, -16817.11) * mm});
            skLineSegment(sketch, "E3842", {"start": v(-4584.84, -16817.11) * mm, "end": v(-4633.6, -16850.66) * mm});
            skLineSegment(sketch, "E3843", {"start": v(-4633.6, -16850.66) * mm, "end": v(-4682.08, -16878.96) * mm});
            skLineSegment(sketch, "E3844", {"start": v(-4682.08, -16878.96) * mm, "end": v(-4729.83, -16900.36) * mm});
            skLineSegment(sketch, "E3845", {"start": v(-4729.83, -16900.36) * mm, "end": v(-4776.44, -16913.19) * mm});
            skLineSegment(sketch, "E3846", {"start": v(-4776.44, -16913.19) * mm, "end": v(-4821.48, -16915.78) * mm});
            skLineSegment(sketch, "E3847", {"start": v(-4821.48, -16915.78) * mm, "end": v(-4881.01, -16907.3) * mm});
            skLineSegment(sketch, "E3848", {"start": v(-4881.01, -16907.3) * mm, "end": v(-4939.43, -16895) * mm});
            skLineSegment(sketch, "E3849", {"start": v(-4939.43, -16895) * mm, "end": v(-4992.51, -16879.62) * mm});
            skLineSegment(sketch, "E3850", {"start": v(-4992.51, -16879.62) * mm, "end": v(-5040.5, -16861.25) * mm});
            skLineSegment(sketch, "E3851", {"start": v(-5040.5, -16861.25) * mm, "end": v(-5083.64, -16839.94) * mm});
            skLineSegment(sketch, "E3852", {"start": v(-5083.64, -16839.94) * mm, "end": v(-5122.18, -16815.75) * mm});
            skLineSegment(sketch, "E3853", {"start": v(-5122.18, -16815.75) * mm, "end": v(-5156.36, -16788.74) * mm});
            skLineSegment(sketch, "E3854", {"start": v(-5156.36, -16788.74) * mm, "end": v(-5186.43, -16758.98) * mm});
            skLineSegment(sketch, "E3855", {"start": v(-5186.43, -16758.98) * mm, "end": v(-5212.64, -16726.51) * mm});
            skLineSegment(sketch, "E3856", {"start": v(-5212.64, -16726.51) * mm, "end": v(-5235.23, -16691.41) * mm});
            skLineSegment(sketch, "E3857", {"start": v(-5235.23, -16691.41) * mm, "end": v(-5254.44, -16653.73) * mm});
            skLineSegment(sketch, "E3858", {"start": v(-5254.44, -16653.73) * mm, "end": v(-5270.53, -16613.53) * mm});
            skLineSegment(sketch, "E3859", {"start": v(-5270.53, -16613.53) * mm, "end": v(-5283.73, -16570.87) * mm});
            skLineSegment(sketch, "E3860", {"start": v(-5283.73, -16570.87) * mm, "end": v(-5294.3, -16525.81) * mm});
            skLineSegment(sketch, "E3861", {"start": v(-5294.3, -16525.81) * mm, "end": v(-5302.47, -16478.41) * mm});
            skLineSegment(sketch, "E3862", {"start": v(-5302.47, -16478.41) * mm, "end": v(-5308.5, -16428.73) * mm});
            skLineSegment(sketch, "E3863", {"start": v(-5308.5, -16428.73) * mm, "end": v(-5312.63, -16376.83) * mm});
            skLineSegment(sketch, "E3864", {"start": v(-5312.63, -16376.83) * mm, "end": v(-5315.11, -16322.77) * mm});
            skLineSegment(sketch, "E3865", {"start": v(-5315.11, -16322.77) * mm, "end": v(-5316.18, -16266.6) * mm});
            skLineSegment(sketch, "E3866", {"start": v(-5316.18, -16266.6) * mm, "end": v(-5316.07, -16209.11) * mm});
            skLineSegment(sketch, "E3867", {"start": v(-5316.07, -16209.11) * mm, "end": v(-5314.74, -16153.34) * mm});
            skLineSegment(sketch, "E3868", {"start": v(-5314.74, -16153.34) * mm, "end": v(-5311.95, -16099.68) * mm});
            skLineSegment(sketch, "E3869", {"start": v(-5311.95, -16099.68) * mm, "end": v(-5307.46, -16048.2) * mm});
            skLineSegment(sketch, "E3870", {"start": v(-5307.46, -16048.2) * mm, "end": v(-5301.02, -15998.95) * mm});
            skLineSegment(sketch, "E3871", {"start": v(-5301.02, -15998.95) * mm, "end": v(-5292.38, -15952) * mm});
            skLineSegment(sketch, "E3872", {"start": v(-5292.38, -15952) * mm, "end": v(-5281.3, -15907.4) * mm});
            skLineSegment(sketch, "E3873", {"start": v(-5281.3, -15907.4) * mm, "end": v(-5267.55, -15865.22) * mm});
            skLineSegment(sketch, "E3874", {"start": v(-5267.55, -15865.22) * mm, "end": v(-5250.85, -15825.51) * mm});
            skLineSegment(sketch, "E3875", {"start": v(-5250.85, -15825.51) * mm, "end": v(-5230.99, -15788.34) * mm});
            skLineSegment(sketch, "E3876", {"start": v(-5230.99, -15788.34) * mm, "end": v(-5207.7, -15753.75) * mm});
            skLineSegment(sketch, "E3877", {"start": v(-5207.7, -15753.75) * mm, "end": v(-5180.73, -15721.82) * mm});
            skLineSegment(sketch, "E3878", {"start": v(-5180.73, -15721.82) * mm, "end": v(-5149.86, -15692.6) * mm});
            skLineSegment(sketch, "E3879", {"start": v(-5149.86, -15692.6) * mm, "end": v(-5114.82, -15666.16) * mm});
            skLineSegment(sketch, "E3880", {"start": v(-5114.82, -15666.16) * mm, "end": v(-5075.39, -15642.55) * mm});
            skLineSegment(sketch, "E3881", {"start": v(-5075.39, -15642.55) * mm, "end": v(-5031.3, -15621.82) * mm});
            skLineSegment(sketch, "E3882", {"start": v(-5031.3, -15621.82) * mm, "end": v(-4982.3, -15604.05) * mm});
            skLineSegment(sketch, "E3883", {"start": v(-4982.3, -15604.05) * mm, "end": v(-4928.18, -15589.3) * mm});
            skLineSegment(sketch, "E3884", {"start": v(-4928.18, -15589.3) * mm, "end": v(-4868.67, -15577.6) * mm});
            skLineSegment(sketch, "E3885", {"start": v(-4868.67, -15577.6) * mm, "end": v(-4821.48, -15571.24) * mm});
            skLineSegment(sketch, "E3886", {"start": v(-4821.48, -15571.24) * mm, "end": v(-4799.18, -15571.16) * mm});
            skLineSegment(sketch, "E3887", {"start": v(-4799.18, -15571.16) * mm, "end": v(-4776.44, -15573.85) * mm});
            skLineSegment(sketch, "E3888", {"start": v(-4776.44, -15573.85) * mm, "end": v(-4753.3, -15579.1) * mm});
            skLineSegment(sketch, "E3889", {"start": v(-4753.3, -15579.1) * mm, "end": v(-4729.83, -15586.7) * mm});
            skLineSegment(sketch, "E3890", {"start": v(-4729.83, -15586.7) * mm, "end": v(-4706.07, -15596.45) * mm});
            skLineSegment(sketch, "E3891", {"start": v(-4706.07, -15596.45) * mm, "end": v(-4682.08, -15608.12) * mm});
            skLineSegment(sketch, "E3892", {"start": v(-4682.08, -15608.12) * mm, "end": v(-4657.9, -15621.52) * mm});
            skLineSegment(sketch, "E3893", {"start": v(-4657.9, -15621.52) * mm, "end": v(-4633.6, -15636.44) * mm});
            skLineSegment(sketch, "E3894", {"start": v(-4633.6, -15636.44) * mm, "end": v(-4609.24, -15652.67) * mm});
            skLineSegment(sketch, "E3895", {"start": v(-4609.24, -15652.67) * mm, "end": v(-4584.84, -15670) * mm});
            skLineSegment(sketch, "E3896", {"start": v(-4584.84, -15670) * mm, "end": v(-4560.48, -15688.22) * mm});
            skLineSegment(sketch, "E3897", {"start": v(-4560.48, -15688.22) * mm, "end": v(-4536.2, -15707.13) * mm});
            skLineSegment(sketch, "E3898", {"start": v(-4536.2, -15707.13) * mm, "end": v(-4512.07, -15726.51) * mm});
            skLineSegment(sketch, "E3899", {"start": v(-4512.07, -15726.51) * mm, "end": v(-4488.12, -15746.16) * mm});
            skLineSegment(sketch, "E3900", {"start": v(-4488.12, -15746.16) * mm, "end": v(-4464.42, -15765.88) * mm});
            skLineSegment(sketch, "E3901", {"start": v(-4464.42, -15765.88) * mm, "end": v(-4441, -15785.44) * mm});
            skLineSegment(sketch, "E3902", {"start": v(-4441, -15785.44) * mm, "end": v(-4417.95, -15804.65) * mm});
            skLineSegment(sketch, "E3903", {"start": v(-4417.95, -15804.65) * mm, "end": v(-4395.29, -15823.3) * mm});
            skLineSegment(sketch, "E3904", {"start": v(-4395.29, -15823.3) * mm, "end": v(-4373.08, -15841.18) * mm});
            skLineSegment(sketch, "E3905", {"start": v(-4373.08, -15841.18) * mm, "end": v(-4351.39, -15858.07) * mm});
            skLineSegment(sketch, "E3906", {"start": v(-4351.39, -15858.07) * mm, "end": v(-4330.25, -15873.78) * mm});
            skLineSegment(sketch, "E3907", {"start": v(-4330.25, -15873.78) * mm, "end": v(-4309.73, -15888.1) * mm});
            skLineSegment(sketch, "E3908", {"start": v(-4309.73, -15888.1) * mm, "end": v(-4289.87, -15900.8) * mm});
            skLineSegment(sketch, "E3909", {"start": v(-4289.87, -15900.8) * mm, "end": v(-4270.72, -15911.7) * mm});
            skLineSegment(sketch, "E3910", {"start": v(-4270.72, -15911.7) * mm, "end": v(-4252.36, -15920.57) * mm});
            skLineSegment(sketch, "E3911", {"start": v(-4252.36, -15920.57) * mm, "end": v(-4234.8, -15927.22) * mm});
            skLineSegment(sketch, "E3912", {"start": v(-4234.8, -15927.22) * mm, "end": v(-4218.14, -15931.43) * mm});
            skLineSegment(sketch, "E3913", {"start": v(-4218.14, -15931.43) * mm, "end": v(-4202.4, -15933) * mm});
            skLineSegment(sketch, "E3914", {"start": v(-4202.4, -15933) * mm, "end": v(-4187.64, -15931.71) * mm});
            skLineSegment(sketch, "E3915", {"start": v(-4187.64, -15931.71) * mm, "end": v(-4173.92, -15927.37) * mm});
            skLineSegment(sketch, "E3916", {"start": v(-4173.92, -15927.37) * mm, "end": v(-4161.29, -15919.75) * mm});
            skLineSegment(sketch, "E3917", {"start": v(-4161.29, -15919.75) * mm, "end": v(-4149.8, -15908.66) * mm});
            skLineSegment(sketch, "E3918", {"start": v(-4149.8, -15908.66) * mm, "end": v(-4139.5, -15893.88) * mm});
            skLineSegment(sketch, "E3919", {"start": v(-4139.5, -15893.88) * mm, "end": v(-4130.44, -15875.21) * mm});
            skLineSegment(sketch, "E3920", {"start": v(-4130.44, -15875.21) * mm, "end": v(-4122.7, -15852.44) * mm});
            skLineSegment(sketch, "E3921", {"start": v(-4122.7, -15852.44) * mm, "end": v(-4116.29, -15825.36) * mm});
            skLineSegment(sketch, "E3922", {"start": v(-4116.29, -15825.36) * mm, "end": v(-4111.3, -15793.76) * mm});
            skLineSegment(sketch, "E3923", {"start": v(-4111.3, -15793.76) * mm, "end": v(-4107.75, -15757.44) * mm});
            skLineSegment(sketch, "E3924", {"start": v(-4107.75, -15757.44) * mm, "end": v(-4115.4, -15660.33) * mm});
            skLineSegment(sketch, "E3925", {"start": v(-4115.4, -15660.33) * mm, "end": v(-4124.33, -15563.84) * mm});
            skLineSegment(sketch, "E3926", {"start": v(-4124.33, -15563.84) * mm, "end": v(-4134.51, -15467.95) * mm});
            skLineSegment(sketch, "E3927", {"start": v(-4134.51, -15467.95) * mm, "end": v(-4145.98, -15372.62) * mm});
            skLineSegment(sketch, "E3928", {"start": v(-4145.98, -15372.62) * mm, "end": v(-4158.73, -15277.84) * mm});
            skLineSegment(sketch, "E3929", {"start": v(-4158.73, -15277.84) * mm, "end": v(-4172.77, -15183.56) * mm});
            skLineSegment(sketch, "E3930", {"start": v(-4172.77, -15183.56) * mm, "end": v(-4188.1, -15089.78) * mm});
            skLineSegment(sketch, "E3931", {"start": v(-4188.1, -15089.78) * mm, "end": v(-4204.74, -14996.46) * mm});
            skLineSegment(sketch, "E3932", {"start": v(-4204.74, -14996.46) * mm, "end": v(-4222.7, -14903.57) * mm});
            skLineSegment(sketch, "E3933", {"start": v(-4222.7, -14903.57) * mm, "end": v(-4241.96, -14811.1) * mm});
            skLineSegment(sketch, "E3934", {"start": v(-4241.96, -14811.1) * mm, "end": v(-4262.55, -14719) * mm});
            skLineSegment(sketch, "E3935", {"start": v(-4262.55, -14719) * mm, "end": v(-4284.46, -14627.27) * mm});
            skLineSegment(sketch, "E3936", {"start": v(-4284.46, -14627.27) * mm, "end": v(-4307.72, -14535.86) * mm});
            skLineSegment(sketch, "E3937", {"start": v(-4307.72, -14535.86) * mm, "end": v(-4332.31, -14444.75) * mm});
            skLineSegment(sketch, "E3938", {"start": v(-4332.31, -14444.75) * mm, "end": v(-4358.26, -14353.93) * mm});
            skLineSegment(sketch, "E3939", {"start": v(-4358.26, -14353.93) * mm, "end": v(-4385.56, -14263.35) * mm});
            skLineSegment(sketch, "E3940", {"start": v(-4385.56, -14263.35) * mm, "end": v(-4414.22, -14173) * mm});
            skLineSegment(sketch, "E3941", {"start": v(-4414.22, -14173) * mm, "end": v(-4444.25, -14082.84) * mm});
            skLineSegment(sketch, "E3942", {"start": v(-4444.25, -14082.84) * mm, "end": v(-4475.66, -13992.86) * mm});
            skLineSegment(sketch, "E3943", {"start": v(-4475.66, -13992.86) * mm, "end": v(-4508.45, -13903.03) * mm});
            skLineSegment(sketch, "E3944", {"start": v(-4508.45, -13903.03) * mm, "end": v(-4542.63, -13813.3) * mm});
            skLineSegment(sketch, "E3945", {"start": v(-4542.63, -13813.3) * mm, "end": v(-4578.2, -13723.68) * mm});
            skLineSegment(sketch, "E3946", {"start": v(-4578.2, -13723.68) * mm, "end": v(-4615.18, -13634.13) * mm});
            skLineSegment(sketch, "E3947", {"start": v(-4615.18, -13634.13) * mm, "end": v(-4653.56, -13544.6) * mm});
            skLineSegment(sketch, "E3948", {"start": v(744.62, -13544.6) * mm, "end": v(706.24, -13634.13) * mm});
            skLineSegment(sketch, "E3949", {"start": v(706.24, -13634.13) * mm, "end": v(669.27, -13723.68) * mm});
            skLineSegment(sketch, "E3950", {"start": v(669.27, -13723.68) * mm, "end": v(633.7, -13813.3) * mm});
            skLineSegment(sketch, "E3951", {"start": v(633.7, -13813.3) * mm, "end": v(599.52, -13903.03) * mm});
            skLineSegment(sketch, "E3952", {"start": v(599.52, -13903.03) * mm, "end": v(566.73, -13992.86) * mm});
            skLineSegment(sketch, "E3953", {"start": v(566.73, -13992.86) * mm, "end": v(535.32, -14082.84) * mm});
            skLineSegment(sketch, "E3954", {"start": v(535.32, -14082.84) * mm, "end": v(505.29, -14173) * mm});
            skLineSegment(sketch, "E3955", {"start": v(505.29, -14173) * mm, "end": v(476.62, -14263.35) * mm});
            skLineSegment(sketch, "E3956", {"start": v(476.62, -14263.35) * mm, "end": v(449.32, -14353.93) * mm});
            skLineSegment(sketch, "E3957", {"start": v(449.32, -14353.93) * mm, "end": v(423.37, -14444.75) * mm});
            skLineSegment(sketch, "E3958", {"start": v(423.37, -14444.75) * mm, "end": v(398.78, -14535.86) * mm});
            skLineSegment(sketch, "E3959", {"start": v(398.78, -14535.86) * mm, "end": v(375.52, -14627.27) * mm});
            skLineSegment(sketch, "E3960", {"start": v(375.52, -14627.27) * mm, "end": v(353.6, -14719) * mm});
            skLineSegment(sketch, "E3961", {"start": v(353.6, -14719) * mm, "end": v(333, -14811.1) * mm});
            skLineSegment(sketch, "E3962", {"start": v(333, -14811.1) * mm, "end": v(313.74, -14903.57) * mm});
            skLineSegment(sketch, "E3963", {"start": v(313.74, -14903.57) * mm, "end": v(295.79, -14996.46) * mm});
            skLineSegment(sketch, "E3964", {"start": v(295.79, -14996.46) * mm, "end": v(279.15, -15089.78) * mm});
            skLineSegment(sketch, "E3965", {"start": v(279.15, -15089.78) * mm, "end": v(263.8, -15183.56) * mm});
            skLineSegment(sketch, "E3966", {"start": v(263.8, -15183.56) * mm, "end": v(249.76, -15277.84) * mm});
            skLineSegment(sketch, "E3967", {"start": v(249.76, -15277.84) * mm, "end": v(237, -15372.62) * mm});
            skLineSegment(sketch, "E3968", {"start": v(237, -15372.62) * mm, "end": v(225.54, -15467.95) * mm});
            skLineSegment(sketch, "E3969", {"start": v(225.54, -15467.95) * mm, "end": v(215.34, -15563.84) * mm});
            skLineSegment(sketch, "E3970", {"start": v(215.34, -15563.84) * mm, "end": v(206.42, -15660.33) * mm});
            skLineSegment(sketch, "E3971", {"start": v(206.42, -15660.33) * mm, "end": v(198.75, -15757.44) * mm});
            skLineSegment(sketch, "E3972", {"start": v(198.75, -15757.44) * mm, "end": v(208.36, -15830.61) * mm});
            skLineSegment(sketch, "E3973", {"start": v(208.36, -15830.61) * mm, "end": v(224.6, -15882.46) * mm});
            skLineSegment(sketch, "E3974", {"start": v(224.6, -15882.46) * mm, "end": v(246.95, -15915.14) * mm});
            skLineSegment(sketch, "E3975", {"start": v(246.95, -15915.14) * mm, "end": v(274.83, -15930.82) * mm});
            skLineSegment(sketch, "E3976", {"start": v(274.83, -15930.82) * mm, "end": v(307.71, -15931.65) * mm});
            skLineSegment(sketch, "E3977", {"start": v(307.71, -15931.65) * mm, "end": v(345.04, -15919.81) * mm});
            skLineSegment(sketch, "E3978", {"start": v(345.04, -15919.81) * mm, "end": v(386.26, -15897.45) * mm});
            skLineSegment(sketch, "E3979", {"start": v(386.26, -15897.45) * mm, "end": v(430.84, -15866.74) * mm});
            skLineSegment(sketch, "E3980", {"start": v(430.84, -15866.74) * mm, "end": v(478.22, -15829.83) * mm});
            skLineSegment(sketch, "E3981", {"start": v(478.22, -15829.83) * mm, "end": v(527.85, -15788.89) * mm});
            skLineSegment(sketch, "E3982", {"start": v(527.85, -15788.89) * mm, "end": v(579.18, -15746.08) * mm});
            skLineSegment(sketch, "E3983", {"start": v(579.18, -15746.08) * mm, "end": v(631.68, -15703.56) * mm});
            skLineSegment(sketch, "E3984", {"start": v(631.68, -15703.56) * mm, "end": v(684.78, -15663.5) * mm});
            skLineSegment(sketch, "E3985", {"start": v(684.78, -15663.5) * mm, "end": v(737.94, -15628.05) * mm});
            skLineSegment(sketch, "E3986", {"start": v(737.94, -15628.05) * mm, "end": v(790.6, -15599.39) * mm});
            skLineSegment(sketch, "E3987", {"start": v(790.6, -15599.39) * mm, "end": v(842.24, -15579.66) * mm});
            skLineSegment(sketch, "E3988", {"start": v(842.24, -15579.66) * mm, "end": v(892.3, -15571.03) * mm});
            skLineSegment(sketch, "E3989", {"start": v(892.3, -15571.03) * mm, "end": v(949.46, -15575.99) * mm});
            skLineSegment(sketch, "E3990", {"start": v(949.46, -15575.99) * mm, "end": v(1015.1, -15588.34) * mm});
            skLineSegment(sketch, "E3991", {"start": v(1015.1, -15588.34) * mm, "end": v(1074.31, -15604.36) * mm});
            skLineSegment(sketch, "E3992", {"start": v(1074.31, -15604.36) * mm, "end": v(1127.4, -15623.96) * mm});
            skLineSegment(sketch, "E3993", {"start": v(1127.4, -15623.96) * mm, "end": v(1174.7, -15647.07) * mm});
            skLineSegment(sketch, "E3994", {"start": v(1174.7, -15647.07) * mm, "end": v(1216.52, -15673.6) * mm});
            skLineSegment(sketch, "E3995", {"start": v(1216.52, -15673.6) * mm, "end": v(1253.19, -15703.49) * mm});
            skLineSegment(sketch, "E3996", {"start": v(1253.19, -15703.49) * mm, "end": v(1285.02, -15736.64) * mm});
            skLineSegment(sketch, "E3997", {"start": v(1285.02, -15736.64) * mm, "end": v(1312.32, -15773) * mm});
            skLineSegment(sketch, "E3998", {"start": v(1312.32, -15773) * mm, "end": v(1335.43, -15812.46) * mm});
            skLineSegment(sketch, "E3999", {"start": v(1335.43, -15812.46) * mm, "end": v(1354.65, -15854.96) * mm});
            skLineSegment(sketch, "E4000", {"start": v(1354.65, -15854.96) * mm, "end": v(1370.31, -15900.42) * mm});
            skLineSegment(sketch, "E4001", {"start": v(1370.31, -15900.42) * mm, "end": v(1382.73, -15948.76) * mm});
            skLineSegment(sketch, "E4002", {"start": v(1382.73, -15948.76) * mm, "end": v(1392.22, -15999.9) * mm});
            skLineSegment(sketch, "E4003", {"start": v(1392.22, -15999.9) * mm, "end": v(1399.1, -16053.78) * mm});
            skLineSegment(sketch, "E4004", {"start": v(1399.1, -16053.78) * mm, "end": v(1403.7, -16110.3) * mm});
            skLineSegment(sketch, "E4005", {"start": v(1403.7, -16110.3) * mm, "end": v(1406.33, -16169.38) * mm});
            skLineSegment(sketch, "E4006", {"start": v(1406.33, -16169.38) * mm, "end": v(1407.3, -16230.96) * mm});
            skLineSegment(sketch, "E4007", {"start": v(1407.3, -16230.96) * mm, "end": v(1406.9, -16293.42) * mm});
            skLineSegment(sketch, "E4008", {"start": v(1406.9, -16293.42) * mm, "end": v(1404.97, -16353.5) * mm});
            skLineSegment(sketch, "E4009", {"start": v(1404.97, -16353.5) * mm, "end": v(1401.2, -16411.05) * mm});
            skLineSegment(sketch, "E4010", {"start": v(1401.2, -16411.05) * mm, "end": v(1395.27, -16465.98) * mm});
            skLineSegment(sketch, "E4011", {"start": v(1395.27, -16465.98) * mm, "end": v(1386.86, -16518.21) * mm});
            skLineSegment(sketch, "E4012", {"start": v(1386.86, -16518.21) * mm, "end": v(1375.65, -16567.67) * mm});
            skLineSegment(sketch, "E4013", {"start": v(1375.65, -16567.67) * mm, "end": v(1361.32, -16614.28) * mm});
            skLineSegment(sketch, "E4014", {"start": v(1361.32, -16614.28) * mm, "end": v(1343.56, -16657.96) * mm});
            skLineSegment(sketch, "E4015", {"start": v(1343.56, -16657.96) * mm, "end": v(1322.05, -16698.64) * mm});
            skLineSegment(sketch, "E4016", {"start": v(1322.05, -16698.64) * mm, "end": v(1296.46, -16736.23) * mm});
            skLineSegment(sketch, "E4017", {"start": v(1296.46, -16736.23) * mm, "end": v(1266.48, -16770.66) * mm});
            skLineSegment(sketch, "E4018", {"start": v(1266.48, -16770.66) * mm, "end": v(1231.8, -16801.86) * mm});
            skLineSegment(sketch, "E4019", {"start": v(1231.8, -16801.86) * mm, "end": v(1192.07, -16829.73) * mm});
            skLineSegment(sketch, "E4020", {"start": v(1192.07, -16829.73) * mm, "end": v(1147, -16854.21) * mm});
            skLineSegment(sketch, "E4021", {"start": v(1147, -16854.21) * mm, "end": v(1096.26, -16875.22) * mm});
            skLineSegment(sketch, "E4022", {"start": v(1096.26, -16875.22) * mm, "end": v(1039.54, -16892.68) * mm});
            skLineSegment(sketch, "E4023", {"start": v(1039.54, -16892.68) * mm, "end": v(976.51, -16906.52) * mm});
            skLineSegment(sketch, "E4024", {"start": v(976.51, -16906.52) * mm, "end": v(916.55, -16915.45) * mm});
            skLineSegment(sketch, "E4025", {"start": v(916.55, -16915.45) * mm, "end": v(892.3, -16915.98) * mm});
            skLineSegment(sketch, "E4026", {"start": v(892.3, -16915.98) * mm, "end": v(867.5, -16913.19) * mm});
            skLineSegment(sketch, "E4027", {"start": v(867.5, -16913.19) * mm, "end": v(842.24, -16907.35) * mm});
            skLineSegment(sketch, "E4028", {"start": v(842.24, -16907.35) * mm, "end": v(816.6, -16898.74) * mm});
            skLineSegment(sketch, "E4029", {"start": v(816.6, -16898.74) * mm, "end": v(790.6, -16887.63) * mm});
            skLineSegment(sketch, "E4030", {"start": v(790.6, -16887.63) * mm, "end": v(764.37, -16874.28) * mm});
            skLineSegment(sketch, "E4031", {"start": v(764.37, -16874.28) * mm, "end": v(737.94, -16858.97) * mm});
            skLineSegment(sketch, "E4032", {"start": v(737.94, -16858.97) * mm, "end": v(711.38, -16841.96) * mm});
            skLineSegment(sketch, "E4033", {"start": v(711.38, -16841.96) * mm, "end": v(684.78, -16823.53) * mm});
            skLineSegment(sketch, "E4034", {"start": v(684.78, -16823.53) * mm, "end": v(658.19, -16803.94) * mm});
            skLineSegment(sketch, "E4035", {"start": v(658.19, -16803.94) * mm, "end": v(631.68, -16783.47) * mm});
            skLineSegment(sketch, "E4036", {"start": v(631.68, -16783.47) * mm, "end": v(605.32, -16762.39) * mm});
            skLineSegment(sketch, "E4037", {"start": v(605.32, -16762.39) * mm, "end": v(579.18, -16740.96) * mm});
            skLineSegment(sketch, "E4038", {"start": v(579.18, -16740.96) * mm, "end": v(553.34, -16719.46) * mm});
            skLineSegment(sketch, "E4039", {"start": v(553.34, -16719.46) * mm, "end": v(527.85, -16698.16) * mm});
            skLineSegment(sketch, "E4040", {"start": v(527.85, -16698.16) * mm, "end": v(502.79, -16677.32) * mm});
            skLineSegment(sketch, "E4041", {"start": v(502.79, -16677.32) * mm, "end": v(478.22, -16657.23) * mm});
            skLineSegment(sketch, "E4042", {"start": v(478.22, -16657.23) * mm, "end": v(454.21, -16638.14) * mm});
            skLineSegment(sketch, "E4043", {"start": v(454.21, -16638.14) * mm, "end": v(430.84, -16620.32) * mm});
            skLineSegment(sketch, "E4044", {"start": v(430.84, -16620.32) * mm, "end": v(408.17, -16604.06) * mm});
            skLineSegment(sketch, "E4045", {"start": v(408.17, -16604.06) * mm, "end": v(386.26, -16589.61) * mm});
            skLineSegment(sketch, "E4046", {"start": v(386.26, -16589.61) * mm, "end": v(365.2, -16577.25) * mm});
            skLineSegment(sketch, "E4047", {"start": v(365.2, -16577.25) * mm, "end": v(345.04, -16567.25) * mm});
            skLineSegment(sketch, "E4048", {"start": v(345.04, -16567.25) * mm, "end": v(325.85, -16559.88) * mm});
            skLineSegment(sketch, "E4049", {"start": v(325.85, -16559.88) * mm, "end": v(307.71, -16555.41) * mm});
            skLineSegment(sketch, "E4050", {"start": v(307.71, -16555.41) * mm, "end": v(290.68, -16554.1) * mm});
            skLineSegment(sketch, "E4051", {"start": v(290.68, -16554.1) * mm, "end": v(274.83, -16556.24) * mm});
            skLineSegment(sketch, "E4052", {"start": v(274.83, -16556.24) * mm, "end": v(260.23, -16562.09) * mm});
            skLineSegment(sketch, "E4053", {"start": v(260.23, -16562.09) * mm, "end": v(246.95, -16571.91) * mm});
            skLineSegment(sketch, "E4054", {"start": v(246.95, -16571.91) * mm, "end": v(235.05, -16585.99) * mm});
            skLineSegment(sketch, "E4055", {"start": v(235.05, -16585.99) * mm, "end": v(224.6, -16604.58) * mm});
            skLineSegment(sketch, "E4056", {"start": v(224.6, -16604.58) * mm, "end": v(215.69, -16627.97) * mm});
            skLineSegment(sketch, "E4057", {"start": v(215.69, -16627.97) * mm, "end": v(208.36, -16656.41) * mm});
            skLineSegment(sketch, "E4058", {"start": v(208.36, -16656.41) * mm, "end": v(202.7, -16690.2) * mm});
            skLineSegment(sketch, "E4059", {"start": v(202.7, -16690.2) * mm, "end": v(198.75, -16729.57) * mm});
            skLineSegment(sketch, "E4060", {"start": v(198.75, -16729.57) * mm, "end": v(206.42, -16826.67) * mm});
            skLineSegment(sketch, "E4061", {"start": v(206.42, -16826.67) * mm, "end": v(215.34, -16923.15) * mm});
            skLineSegment(sketch, "E4062", {"start": v(215.34, -16923.15) * mm, "end": v(225.54, -17019.04) * mm});
            skLineSegment(sketch, "E4063", {"start": v(225.54, -17019.04) * mm, "end": v(237, -17114.36) * mm});
            skLineSegment(sketch, "E4064", {"start": v(237, -17114.36) * mm, "end": v(249.76, -17209.15) * mm});
            skLineSegment(sketch, "E4065", {"start": v(249.76, -17209.15) * mm, "end": v(263.8, -17303.42) * mm});
            skLineSegment(sketch, "E4066", {"start": v(263.8, -17303.42) * mm, "end": v(279.15, -17397.2) * mm});
            skLineSegment(sketch, "E4067", {"start": v(279.15, -17397.2) * mm, "end": v(295.79, -17490.53) * mm});
            skLineSegment(sketch, "E4068", {"start": v(295.79, -17490.53) * mm, "end": v(313.74, -17583.42) * mm});
            skLineSegment(sketch, "E4069", {"start": v(313.74, -17583.42) * mm, "end": v(333, -17675.9) * mm});
            skLineSegment(sketch, "E4070", {"start": v(333, -17675.9) * mm, "end": v(353.6, -17768) * mm});
            skLineSegment(sketch, "E4071", {"start": v(353.6, -17768) * mm, "end": v(375.52, -17859.74) * mm});
            skLineSegment(sketch, "E4072", {"start": v(375.52, -17859.74) * mm, "end": v(398.78, -17951.16) * mm});
            skLineSegment(sketch, "E4073", {"start": v(398.78, -17951.16) * mm, "end": v(423.37, -18042.27) * mm});
            skLineSegment(sketch, "E4074", {"start": v(423.37, -18042.27) * mm, "end": v(449.32, -18133.11) * mm});
            skLineSegment(sketch, "E4075", {"start": v(449.32, -18133.11) * mm, "end": v(476.62, -18223.7) * mm});
            skLineSegment(sketch, "E4076", {"start": v(476.62, -18223.7) * mm, "end": v(505.29, -18314.07) * mm});
            skLineSegment(sketch, "E4077", {"start": v(505.29, -18314.07) * mm, "end": v(535.32, -18404.24) * mm});
            skLineSegment(sketch, "E4078", {"start": v(535.32, -18404.24) * mm, "end": v(566.73, -18494.23) * mm});
            skLineSegment(sketch, "E4079", {"start": v(566.73, -18494.23) * mm, "end": v(599.52, -18584.09) * mm});
            skLineSegment(sketch, "E4080", {"start": v(599.52, -18584.09) * mm, "end": v(633.7, -18673.83) * mm});
            skLineSegment(sketch, "E4081", {"start": v(633.7, -18673.83) * mm, "end": v(669.27, -18763.47) * mm});
            skLineSegment(sketch, "E4082", {"start": v(669.27, -18763.47) * mm, "end": v(706.24, -18853.05) * mm});
            skLineSegment(sketch, "E4083", {"start": v(706.24, -18853.05) * mm, "end": v(789.68, -19047.7) * mm});
            skLineSegment(sketch, "E4084", {"start": v(6142.61, -13544.6) * mm, "end": v(6180.97, -13634.13) * mm});
            skLineSegment(sketch, "E4085", {"start": v(6180.97, -13634.13) * mm, "end": v(6217.93, -13723.68) * mm});
            skLineSegment(sketch, "E4086", {"start": v(6217.93, -13723.68) * mm, "end": v(6253.48, -13813.3) * mm});
            skLineSegment(sketch, "E4087", {"start": v(6253.48, -13813.3) * mm, "end": v(6287.64, -13903.03) * mm});
            skLineSegment(sketch, "E4088", {"start": v(6287.64, -13903.03) * mm, "end": v(6320.41, -13992.86) * mm});
            skLineSegment(sketch, "E4089", {"start": v(6320.41, -13992.86) * mm, "end": v(6351.8, -14082.84) * mm});
            skLineSegment(sketch, "E4090", {"start": v(6351.8, -14082.84) * mm, "end": v(6381.83, -14173) * mm});
            skLineSegment(sketch, "E4091", {"start": v(6381.83, -14173) * mm, "end": v(6410.48, -14263.35) * mm});
            skLineSegment(sketch, "E4092", {"start": v(6410.48, -14263.35) * mm, "end": v(6437.77, -14353.93) * mm});
            skLineSegment(sketch, "E4093", {"start": v(6437.77, -14353.93) * mm, "end": v(6463.7, -14444.75) * mm});
            skLineSegment(sketch, "E4094", {"start": v(6463.7, -14444.75) * mm, "end": v(6488.3, -14535.86) * mm});
            skLineSegment(sketch, "E4095", {"start": v(6488.3, -14535.86) * mm, "end": v(6511.55, -14627.27) * mm});
            skLineSegment(sketch, "E4096", {"start": v(6511.55, -14627.27) * mm, "end": v(6533.46, -14719) * mm});
            skLineSegment(sketch, "E4097", {"start": v(6533.46, -14719) * mm, "end": v(6554.05, -14811.1) * mm});
            skLineSegment(sketch, "E4098", {"start": v(6554.05, -14811.1) * mm, "end": v(6573.31, -14903.57) * mm});
            skLineSegment(sketch, "E4099", {"start": v(6573.31, -14903.57) * mm, "end": v(6591.26, -14996.46) * mm});
            skLineSegment(sketch, "E4100", {"start": v(6591.26, -14996.46) * mm, "end": v(6607.9, -15089.78) * mm});
            skLineSegment(sketch, "E4101", {"start": v(6607.9, -15089.78) * mm, "end": v(6623.24, -15183.56) * mm});
            skLineSegment(sketch, "E4102", {"start": v(6623.24, -15183.56) * mm, "end": v(6637.28, -15277.84) * mm});
            skLineSegment(sketch, "E4103", {"start": v(6637.28, -15277.84) * mm, "end": v(6650.04, -15372.62) * mm});
            skLineSegment(sketch, "E4104", {"start": v(6650.04, -15372.62) * mm, "end": v(6661.5, -15467.95) * mm});
            skLineSegment(sketch, "E4105", {"start": v(6661.5, -15467.95) * mm, "end": v(6671.7, -15563.84) * mm});
            skLineSegment(sketch, "E4106", {"start": v(6671.7, -15563.84) * mm, "end": v(6680.63, -15660.33) * mm});
            skLineSegment(sketch, "E4107", {"start": v(6680.63, -15660.33) * mm, "end": v(6688.29, -15757.44) * mm});
            skLineSegment(sketch, "E4108", {"start": v(6688.29, -15757.44) * mm, "end": v(6678.68, -15830.61) * mm});
            skLineSegment(sketch, "E4109", {"start": v(6678.68, -15830.61) * mm, "end": v(6662.44, -15882.46) * mm});
            skLineSegment(sketch, "E4110", {"start": v(6662.44, -15882.46) * mm, "end": v(6640.1, -15915.14) * mm});
            skLineSegment(sketch, "E4111", {"start": v(6640.1, -15915.14) * mm, "end": v(6612.23, -15930.82) * mm});
            skLineSegment(sketch, "E4112", {"start": v(6612.23, -15930.82) * mm, "end": v(6579.37, -15931.65) * mm});
            skLineSegment(sketch, "E4113", {"start": v(6579.37, -15931.65) * mm, "end": v(6542.05, -15919.81) * mm});
            skLineSegment(sketch, "E4114", {"start": v(6542.05, -15919.81) * mm, "end": v(6500.83, -15897.45) * mm});
            skLineSegment(sketch, "E4115", {"start": v(6500.83, -15897.45) * mm, "end": v(6456.27, -15866.74) * mm});
            skLineSegment(sketch, "E4116", {"start": v(6456.27, -15866.74) * mm, "end": v(6408.9, -15829.83) * mm});
            skLineSegment(sketch, "E4117", {"start": v(6408.9, -15829.83) * mm, "end": v(6359.28, -15788.89) * mm});
            skLineSegment(sketch, "E4118", {"start": v(6359.28, -15788.89) * mm, "end": v(6307.94, -15746.08) * mm});
            skLineSegment(sketch, "E4119", {"start": v(6307.94, -15746.08) * mm, "end": v(6255.45, -15703.56) * mm});
            skLineSegment(sketch, "E4120", {"start": v(6255.45, -15703.56) * mm, "end": v(6202.35, -15663.5) * mm});
            skLineSegment(sketch, "E4121", {"start": v(6202.35, -15663.5) * mm, "end": v(6149.18, -15628.05) * mm});
            skLineSegment(sketch, "E4122", {"start": v(6149.18, -15628.05) * mm, "end": v(6096.5, -15599.39) * mm});
            skLineSegment(sketch, "E4123", {"start": v(6096.5, -15599.39) * mm, "end": v(6044.84, -15579.66) * mm});
            skLineSegment(sketch, "E4124", {"start": v(6044.84, -15579.66) * mm, "end": v(5994.77, -15571.03) * mm});
            skLineSegment(sketch, "E4125", {"start": v(5994.77, -15571.03) * mm, "end": v(5937.58, -15575.99) * mm});
            skLineSegment(sketch, "E4126", {"start": v(5937.58, -15575.99) * mm, "end": v(5871.94, -15588.34) * mm});
            skLineSegment(sketch, "E4127", {"start": v(5871.94, -15588.34) * mm, "end": v(5812.73, -15604.36) * mm});
            skLineSegment(sketch, "E4128", {"start": v(5812.73, -15604.36) * mm, "end": v(5759.64, -15623.96) * mm});
            skLineSegment(sketch, "E4129", {"start": v(5759.64, -15623.96) * mm, "end": v(5712.34, -15647.07) * mm});
            skLineSegment(sketch, "E4130", {"start": v(5712.34, -15647.07) * mm, "end": v(5670.52, -15673.6) * mm});
            skLineSegment(sketch, "E4131", {"start": v(5670.52, -15673.6) * mm, "end": v(5633.85, -15703.49) * mm});
            skLineSegment(sketch, "E4132", {"start": v(5633.85, -15703.49) * mm, "end": v(5602.03, -15736.64) * mm});
            skLineSegment(sketch, "E4133", {"start": v(5602.03, -15736.64) * mm, "end": v(5574.72, -15773) * mm});
            skLineSegment(sketch, "E4134", {"start": v(5574.72, -15773) * mm, "end": v(5551.62, -15812.46) * mm});
            skLineSegment(sketch, "E4135", {"start": v(5551.62, -15812.46) * mm, "end": v(5532.4, -15854.96) * mm});
            skLineSegment(sketch, "E4136", {"start": v(5532.4, -15854.96) * mm, "end": v(5516.73, -15900.42) * mm});
            skLineSegment(sketch, "E4137", {"start": v(5516.73, -15900.42) * mm, "end": v(5504.32, -15948.76) * mm});
            skLineSegment(sketch, "E4138", {"start": v(5504.32, -15948.76) * mm, "end": v(5494.82, -15999.9) * mm});
            skLineSegment(sketch, "E4139", {"start": v(5494.82, -15999.9) * mm, "end": v(5487.94, -16053.78) * mm});
            skLineSegment(sketch, "E4140", {"start": v(5487.94, -16053.78) * mm, "end": v(5483.34, -16110.3) * mm});
            skLineSegment(sketch, "E4141", {"start": v(5483.34, -16110.3) * mm, "end": v(5480.72, -16169.38) * mm});
            skLineSegment(sketch, "E4142", {"start": v(5480.72, -16169.38) * mm, "end": v(5479.74, -16230.96) * mm});
            skLineSegment(sketch, "E4143", {"start": v(5479.74, -16230.96) * mm, "end": v(5480.14, -16293.42) * mm});
            skLineSegment(sketch, "E4144", {"start": v(5480.14, -16293.42) * mm, "end": v(5482.07, -16353.5) * mm});
            skLineSegment(sketch, "E4145", {"start": v(5482.07, -16353.5) * mm, "end": v(5485.85, -16411.05) * mm});
            skLineSegment(sketch, "E4146", {"start": v(5485.85, -16411.05) * mm, "end": v(5491.78, -16465.98) * mm});
            skLineSegment(sketch, "E4147", {"start": v(5491.78, -16465.98) * mm, "end": v(5500.19, -16518.21) * mm});
            skLineSegment(sketch, "E4148", {"start": v(5500.19, -16518.21) * mm, "end": v(5511.4, -16567.67) * mm});
            skLineSegment(sketch, "E4149", {"start": v(5511.4, -16567.67) * mm, "end": v(5525.72, -16614.28) * mm});
            skLineSegment(sketch, "E4150", {"start": v(5525.72, -16614.28) * mm, "end": v(5543.48, -16657.96) * mm});
            skLineSegment(sketch, "E4151", {"start": v(5543.48, -16657.96) * mm, "end": v(5565, -16698.64) * mm});
            skLineSegment(sketch, "E4152", {"start": v(5565, -16698.64) * mm, "end": v(5590.58, -16736.23) * mm});
            skLineSegment(sketch, "E4153", {"start": v(5590.58, -16736.23) * mm, "end": v(5620.56, -16770.66) * mm});
            skLineSegment(sketch, "E4154", {"start": v(5620.56, -16770.66) * mm, "end": v(5655.25, -16801.86) * mm});
            skLineSegment(sketch, "E4155", {"start": v(5655.25, -16801.86) * mm, "end": v(5694.97, -16829.73) * mm});
            skLineSegment(sketch, "E4156", {"start": v(5694.97, -16829.73) * mm, "end": v(5740.04, -16854.21) * mm});
            skLineSegment(sketch, "E4157", {"start": v(5740.04, -16854.21) * mm, "end": v(5790.78, -16875.22) * mm});
            skLineSegment(sketch, "E4158", {"start": v(5790.78, -16875.22) * mm, "end": v(5847.5, -16892.68) * mm});
            skLineSegment(sketch, "E4159", {"start": v(5847.5, -16892.68) * mm, "end": v(5910.53, -16906.52) * mm});
            skLineSegment(sketch, "E4160", {"start": v(5910.53, -16906.52) * mm, "end": v(5970.5, -16915.45) * mm});
            skLineSegment(sketch, "E4161", {"start": v(5970.5, -16915.45) * mm, "end": v(5994.77, -16915.98) * mm});
            skLineSegment(sketch, "E4162", {"start": v(5994.77, -16915.98) * mm, "end": v(6019.57, -16913.19) * mm});
            skLineSegment(sketch, "E4163", {"start": v(6019.57, -16913.19) * mm, "end": v(6044.84, -16907.35) * mm});
            skLineSegment(sketch, "E4164", {"start": v(6044.84, -16907.35) * mm, "end": v(6070.5, -16898.74) * mm});
            skLineSegment(sketch, "E4165", {"start": v(6070.5, -16898.74) * mm, "end": v(6096.5, -16887.63) * mm});
            skLineSegment(sketch, "E4166", {"start": v(6096.5, -16887.63) * mm, "end": v(6122.74, -16874.28) * mm});
            skLineSegment(sketch, "E4167", {"start": v(6122.74, -16874.28) * mm, "end": v(6149.18, -16858.97) * mm});
            skLineSegment(sketch, "E4168", {"start": v(6149.18, -16858.97) * mm, "end": v(6175.74, -16841.96) * mm});
            skLineSegment(sketch, "E4169", {"start": v(6175.74, -16841.96) * mm, "end": v(6202.35, -16823.53) * mm});
            skLineSegment(sketch, "E4170", {"start": v(6202.35, -16823.53) * mm, "end": v(6228.94, -16803.94) * mm});
            skLineSegment(sketch, "E4171", {"start": v(6228.94, -16803.94) * mm, "end": v(6255.45, -16783.47) * mm});
            skLineSegment(sketch, "E4172", {"start": v(6255.45, -16783.47) * mm, "end": v(6281.8, -16762.39) * mm});
            skLineSegment(sketch, "E4173", {"start": v(6281.8, -16762.39) * mm, "end": v(6307.94, -16740.96) * mm});
            skLineSegment(sketch, "E4174", {"start": v(6307.94, -16740.96) * mm, "end": v(6333.79, -16719.46) * mm});
            skLineSegment(sketch, "E4175", {"start": v(6333.79, -16719.46) * mm, "end": v(6359.28, -16698.16) * mm});
            skLineSegment(sketch, "E4176", {"start": v(6359.28, -16698.16) * mm, "end": v(6384.34, -16677.32) * mm});
            skLineSegment(sketch, "E4177", {"start": v(6384.34, -16677.32) * mm, "end": v(6408.9, -16657.23) * mm});
            skLineSegment(sketch, "E4178", {"start": v(6408.9, -16657.23) * mm, "end": v(6432.9, -16638.14) * mm});
            skLineSegment(sketch, "E4179", {"start": v(6432.9, -16638.14) * mm, "end": v(6456.27, -16620.32) * mm});
            skLineSegment(sketch, "E4180", {"start": v(6456.27, -16620.32) * mm, "end": v(6478.94, -16604.06) * mm});
            skLineSegment(sketch, "E4181", {"start": v(6478.94, -16604.06) * mm, "end": v(6500.83, -16589.61) * mm});
            skLineSegment(sketch, "E4182", {"start": v(6500.83, -16589.61) * mm, "end": v(6521.9, -16577.25) * mm});
            skLineSegment(sketch, "E4183", {"start": v(6521.9, -16577.25) * mm, "end": v(6542.05, -16567.25) * mm});
            skLineSegment(sketch, "E4184", {"start": v(6542.05, -16567.25) * mm, "end": v(6561.23, -16559.88) * mm});
            skLineSegment(sketch, "E4185", {"start": v(6561.23, -16559.88) * mm, "end": v(6579.37, -16555.41) * mm});
            skLineSegment(sketch, "E4186", {"start": v(6579.37, -16555.41) * mm, "end": v(6596.39, -16554.1) * mm});
            skLineSegment(sketch, "E4187", {"start": v(6596.39, -16554.1) * mm, "end": v(6612.23, -16556.24) * mm});
            skLineSegment(sketch, "E4188", {"start": v(6612.23, -16556.24) * mm, "end": v(6626.83, -16562.09) * mm});
            skLineSegment(sketch, "E4189", {"start": v(6626.83, -16562.09) * mm, "end": v(6640.1, -16571.91) * mm});
            skLineSegment(sketch, "E4190", {"start": v(6640.1, -16571.91) * mm, "end": v(6652, -16585.99) * mm});
            skLineSegment(sketch, "E4191", {"start": v(6652, -16585.99) * mm, "end": v(6662.44, -16604.58) * mm});
            skLineSegment(sketch, "E4192", {"start": v(6662.44, -16604.58) * mm, "end": v(6671.36, -16627.97) * mm});
            skLineSegment(sketch, "E4193", {"start": v(6671.36, -16627.97) * mm, "end": v(6678.68, -16656.41) * mm});
            skLineSegment(sketch, "E4194", {"start": v(6678.68, -16656.41) * mm, "end": v(6684.35, -16690.2) * mm});
            skLineSegment(sketch, "E4195", {"start": v(6684.35, -16690.2) * mm, "end": v(6688.29, -16729.57) * mm});
            skLineSegment(sketch, "E4196", {"start": v(6688.29, -16729.57) * mm, "end": v(6680.63, -16826.67) * mm});
            skLineSegment(sketch, "E4197", {"start": v(6680.63, -16826.67) * mm, "end": v(6671.7, -16923.15) * mm});
            skLineSegment(sketch, "E4198", {"start": v(6671.7, -16923.15) * mm, "end": v(6661.5, -17019.04) * mm});
            skLineSegment(sketch, "E4199", {"start": v(6661.5, -17019.04) * mm, "end": v(6650.04, -17114.36) * mm});
            skLineSegment(sketch, "E4200", {"start": v(6650.04, -17114.36) * mm, "end": v(6637.28, -17209.15) * mm});
            skLineSegment(sketch, "E4201", {"start": v(6637.28, -17209.15) * mm, "end": v(6623.24, -17303.42) * mm});
            skLineSegment(sketch, "E4202", {"start": v(6623.24, -17303.42) * mm, "end": v(6607.9, -17397.2) * mm});
            skLineSegment(sketch, "E4203", {"start": v(6607.9, -17397.2) * mm, "end": v(6591.26, -17490.53) * mm});
            skLineSegment(sketch, "E4204", {"start": v(6591.26, -17490.53) * mm, "end": v(6573.31, -17583.42) * mm});
            skLineSegment(sketch, "E4205", {"start": v(6573.31, -17583.42) * mm, "end": v(6572.89, -17585.46) * mm});
            skLineSegment(sketch, "E4206", {"start": v(10777.37, -8427.8) * mm, "end": v(10731.1, -8441.74) * mm});
            skLineSegment(sketch, "E4207", {"start": v(10731.1, -8441.74) * mm, "end": v(10640.28, -8467.68) * mm});
            skLineSegment(sketch, "E4208", {"start": v(10640.28, -8467.68) * mm, "end": v(10549.18, -8492.27) * mm});
            skLineSegment(sketch, "E4209", {"start": v(10549.18, -8492.27) * mm, "end": v(10457.77, -8515.52) * mm});
            skLineSegment(sketch, "E4210", {"start": v(10457.77, -8515.52) * mm, "end": v(10366.04, -8537.43) * mm});
            skLineSegment(sketch, "E4211", {"start": v(10366.04, -8537.43) * mm, "end": v(10273.96, -8558.02) * mm});
            skLineSegment(sketch, "E4212", {"start": v(10273.96, -8558.02) * mm, "end": v(10181.49, -8577.28) * mm});
            skLineSegment(sketch, "E4213", {"start": v(10181.49, -8577.28) * mm, "end": v(10088.61, -8595.23) * mm});
            skLineSegment(sketch, "E4214", {"start": v(10088.61, -8595.23) * mm, "end": v(9995.3, -8611.87) * mm});
            skLineSegment(sketch, "E4215", {"start": v(9995.3, -8611.87) * mm, "end": v(9901.53, -8627.2) * mm});
            skLineSegment(sketch, "E4216", {"start": v(9901.53, -8627.2) * mm, "end": v(9807.27, -8641.25) * mm});
            skLineSegment(sketch, "E4217", {"start": v(9807.27, -8641.25) * mm, "end": v(9712.5, -8654) * mm});
            skLineSegment(sketch, "E4218", {"start": v(9712.5, -8654) * mm, "end": v(9617.2, -8665.47) * mm});
            skLineSegment(sketch, "E4219", {"start": v(9617.2, -8665.47) * mm, "end": v(9521.32, -8675.66) * mm});
            skLineSegment(sketch, "E4220", {"start": v(9521.32, -8675.66) * mm, "end": v(9424.85, -8684.57) * mm});
            skLineSegment(sketch, "E4221", {"start": v(9424.85, -8684.57) * mm, "end": v(9327.77, -8692.23) * mm});
            skLineSegment(sketch, "E4222", {"start": v(9327.77, -8692.23) * mm, "end": v(9254.6, -8682.63) * mm});
            skLineSegment(sketch, "E4223", {"start": v(9254.6, -8682.63) * mm, "end": v(9202.74, -8666.4) * mm});
            skLineSegment(sketch, "E4224", {"start": v(9202.74, -8666.4) * mm, "end": v(9170.05, -8644.07) * mm});
            skLineSegment(sketch, "E4225", {"start": v(9170.05, -8644.07) * mm, "end": v(9154.37, -8616.2) * mm});
            skLineSegment(sketch, "E4226", {"start": v(9154.37, -8616.2) * mm, "end": v(9153.52, -8583.33) * mm});
            skLineSegment(sketch, "E4227", {"start": v(9153.52, -8583.33) * mm, "end": v(9165.35, -8546.02) * mm});
            skLineSegment(sketch, "E4228", {"start": v(9165.35, -8546.02) * mm, "end": v(9187.69, -8504.8) * mm});
            skLineSegment(sketch, "E4229", {"start": v(9187.69, -8504.8) * mm, "end": v(9218.39, -8460.23) * mm});
            skLineSegment(sketch, "E4230", {"start": v(9218.39, -8460.23) * mm, "end": v(9255.28, -8412.86) * mm});
            skLineSegment(sketch, "E4231", {"start": v(9255.28, -8412.86) * mm, "end": v(9296.2, -8363.24) * mm});
            skLineSegment(sketch, "E4232", {"start": v(9296.2, -8363.24) * mm, "end": v(9339, -8311.9) * mm});
            skLineSegment(sketch, "E4233", {"start": v(9339, -8311.9) * mm, "end": v(9381.5, -8259.4) * mm});
            skLineSegment(sketch, "E4234", {"start": v(9381.5, -8259.4) * mm, "end": v(9421.55, -8206.3) * mm});
            skLineSegment(sketch, "E4235", {"start": v(9421.55, -8206.3) * mm, "end": v(9456.98, -8153.13) * mm});
            skLineSegment(sketch, "E4236", {"start": v(9456.98, -8153.13) * mm, "end": v(9485.64, -8100.44) * mm});
            skLineSegment(sketch, "E4237", {"start": v(9485.64, -8100.44) * mm, "end": v(9505.36, -8048.78) * mm});
            skLineSegment(sketch, "E4238", {"start": v(9505.36, -8048.78) * mm, "end": v(9513.98, -7998.7) * mm});
            skLineSegment(sketch, "E4239", {"start": v(9513.98, -7998.7) * mm, "end": v(9509.03, -7941.52) * mm});
            skLineSegment(sketch, "E4240", {"start": v(9509.03, -7941.52) * mm, "end": v(9496.68, -7875.9) * mm});
            skLineSegment(sketch, "E4241", {"start": v(9496.68, -7875.9) * mm, "end": v(9480.67, -7816.7) * mm});
            skLineSegment(sketch, "E4242", {"start": v(9480.67, -7816.7) * mm, "end": v(9461.08, -7763.6) * mm});
            skLineSegment(sketch, "E4243", {"start": v(9461.08, -7763.6) * mm, "end": v(9437.98, -7716.32) * mm});
            skLineSegment(sketch, "E4244", {"start": v(9437.98, -7716.32) * mm, "end": v(9411.46, -7674.5) * mm});
            skLineSegment(sketch, "E4245", {"start": v(9411.46, -7674.5) * mm, "end": v(9381.59, -7637.84) * mm});
            skLineSegment(sketch, "E4246", {"start": v(9381.59, -7637.84) * mm, "end": v(9348.45, -7606.02) * mm});
            skLineSegment(sketch, "E4247", {"start": v(9348.45, -7606.02) * mm, "end": v(9312.11, -7578.72) * mm});
            skLineSegment(sketch, "E4248", {"start": v(9312.11, -7578.72) * mm, "end": v(9272.66, -7555.61) * mm});
            skLineSegment(sketch, "E4249", {"start": v(9272.66, -7555.61) * mm, "end": v(9230.18, -7536.4) * mm});
            skLineSegment(sketch, "E4250", {"start": v(9230.18, -7536.4) * mm, "end": v(9184.73, -7520.73) * mm});
            skLineSegment(sketch, "E4251", {"start": v(9184.73, -7520.73) * mm, "end": v(9136.4, -7508.32) * mm});
            skLineSegment(sketch, "E4252", {"start": v(9136.4, -7508.32) * mm, "end": v(9085.27, -7498.83) * mm});
            skLineSegment(sketch, "E4253", {"start": v(9085.27, -7498.83) * mm, "end": v(9031.41, -7491.94) * mm});
            skLineSegment(sketch, "E4254", {"start": v(9031.41, -7491.94) * mm, "end": v(8974.9, -7487.35) * mm});
            skLineSegment(sketch, "E4255", {"start": v(8974.9, -7487.35) * mm, "end": v(8915.82, -7484.72) * mm});
            skLineSegment(sketch, "E4256", {"start": v(8915.82, -7484.72) * mm, "end": v(8854.25, -7483.74) * mm});
            skLineSegment(sketch, "E4257", {"start": v(8854.25, -7483.74) * mm, "end": v(8791.8, -7484.15) * mm});
            skLineSegment(sketch, "E4258", {"start": v(8791.8, -7484.15) * mm, "end": v(8731.7, -7486.08) * mm});
            skLineSegment(sketch, "E4259", {"start": v(8731.7, -7486.08) * mm, "end": v(8674.15, -7489.85) * mm});
            skLineSegment(sketch, "E4260", {"start": v(8674.15, -7489.85) * mm, "end": v(8619.2, -7495.78) * mm});
            skLineSegment(sketch, "E4261", {"start": v(8619.2, -7495.78) * mm, "end": v(8566.96, -7504.19) * mm});
            skLineSegment(sketch, "E4262", {"start": v(8566.96, -7504.19) * mm, "end": v(8517.49, -7515.4) * mm});
            skLineSegment(sketch, "E4263", {"start": v(8517.49, -7515.4) * mm, "end": v(8470.86, -7529.72) * mm});
            skLineSegment(sketch, "E4264", {"start": v(8470.86, -7529.72) * mm, "end": v(8427.16, -7547.48) * mm});
            skLineSegment(sketch, "E4265", {"start": v(8427.16, -7547.48) * mm, "end": v(8386.47, -7568.99) * mm});
            skLineSegment(sketch, "E4266", {"start": v(8386.47, -7568.99) * mm, "end": v(8348.86, -7594.57) * mm});
            skLineSegment(sketch, "E4267", {"start": v(8348.86, -7594.57) * mm, "end": v(8314.42, -7624.55) * mm});
            skLineSegment(sketch, "E4268", {"start": v(8314.42, -7624.55) * mm, "end": v(8283.2, -7659.24) * mm});
            skLineSegment(sketch, "E4269", {"start": v(8283.2, -7659.24) * mm, "end": v(8255.32, -7698.95) * mm});
            skLineSegment(sketch, "E4270", {"start": v(8255.32, -7698.95) * mm, "end": v(8230.83, -7744.01) * mm});
            skLineSegment(sketch, "E4271", {"start": v(8230.83, -7744.01) * mm, "end": v(8209.8, -7794.75) * mm});
            skLineSegment(sketch, "E4272", {"start": v(8209.8, -7794.75) * mm, "end": v(8192.34, -7851.46) * mm});
            skLineSegment(sketch, "E4273", {"start": v(8192.34, -7851.46) * mm, "end": v(8178.5, -7914.48) * mm});
            skLineSegment(sketch, "E4274", {"start": v(8178.5, -7914.48) * mm, "end": v(8169.57, -7974.43) * mm});
            skLineSegment(sketch, "E4275", {"start": v(8169.57, -7974.43) * mm, "end": v(8169.06, -7998.7) * mm});
            skLineSegment(sketch, "E4276", {"start": v(8169.06, -7998.7) * mm, "end": v(8171.86, -8023.51) * mm});
            skLineSegment(sketch, "E4277", {"start": v(8171.86, -8023.51) * mm, "end": v(8177.71, -8048.78) * mm});
            skLineSegment(sketch, "E4278", {"start": v(8177.71, -8048.78) * mm, "end": v(8186.33, -8074.45) * mm});
            skLineSegment(sketch, "E4279", {"start": v(8186.33, -8074.45) * mm, "end": v(8197.46, -8100.44) * mm});
            skLineSegment(sketch, "E4280", {"start": v(8197.46, -8100.44) * mm, "end": v(8210.82, -8126.69) * mm});
            skLineSegment(sketch, "E4281", {"start": v(8210.82, -8126.69) * mm, "end": v(8226.14, -8153.13) * mm});
            skLineSegment(sketch, "E4282", {"start": v(8226.14, -8153.13) * mm, "end": v(8243.16, -8179.69) * mm});
            skLineSegment(sketch, "E4283", {"start": v(8243.16, -8179.69) * mm, "end": v(8261.6, -8206.3) * mm});
            skLineSegment(sketch, "E4284", {"start": v(8261.6, -8206.3) * mm, "end": v(8281.2, -8232.9) * mm});
            skLineSegment(sketch, "E4285", {"start": v(8281.2, -8232.9) * mm, "end": v(8301.67, -8259.4) * mm});
            skLineSegment(sketch, "E4286", {"start": v(8301.67, -8259.4) * mm, "end": v(8322.76, -8285.76) * mm});
            skLineSegment(sketch, "E4287", {"start": v(8322.76, -8285.76) * mm, "end": v(8344.19, -8311.9) * mm});
            skLineSegment(sketch, "E4288", {"start": v(8344.19, -8311.9) * mm, "end": v(8365.7, -8337.75) * mm});
            skLineSegment(sketch, "E4289", {"start": v(8365.7, -8337.75) * mm, "end": v(8387, -8363.24) * mm});
            skLineSegment(sketch, "E4290", {"start": v(8387, -8363.24) * mm, "end": v(8407.83, -8388.3) * mm});
            skLineSegment(sketch, "E4291", {"start": v(8407.83, -8388.3) * mm, "end": v(8427.93, -8412.86) * mm});
            skLineSegment(sketch, "E4292", {"start": v(8427.93, -8412.86) * mm, "end": v(8447.02, -8436.87) * mm});
            skLineSegment(sketch, "E4293", {"start": v(8447.02, -8436.87) * mm, "end": v(8464.83, -8460.23) * mm});
            skLineSegment(sketch, "E4294", {"start": v(8464.83, -8460.23) * mm, "end": v(8481.1, -8482.9) * mm});
            skLineSegment(sketch, "E4295", {"start": v(8481.1, -8482.9) * mm, "end": v(8495.54, -8504.8) * mm});
            skLineSegment(sketch, "E4296", {"start": v(8495.54, -8504.8) * mm, "end": v(8507.9, -8525.86) * mm});
            skLineSegment(sketch, "E4297", {"start": v(8507.9, -8525.86) * mm, "end": v(8517.9, -8546.02) * mm});
            skLineSegment(sketch, "E4298", {"start": v(8517.9, -8546.02) * mm, "end": v(8525.26, -8565.2) * mm});
            skLineSegment(sketch, "E4299", {"start": v(8525.26, -8565.2) * mm, "end": v(8529.72, -8583.33) * mm});
            skLineSegment(sketch, "E4300", {"start": v(8529.72, -8583.33) * mm, "end": v(8531.02, -8600.36) * mm});
            skLineSegment(sketch, "E4301", {"start": v(8531.02, -8600.36) * mm, "end": v(8528.87, -8616.2) * mm});
            skLineSegment(sketch, "E4302", {"start": v(8528.87, -8616.2) * mm, "end": v(8523.02, -8630.8) * mm});
            skLineSegment(sketch, "E4303", {"start": v(8523.02, -8630.8) * mm, "end": v(8513.18, -8644.07) * mm});
            skLineSegment(sketch, "E4304", {"start": v(8513.18, -8644.07) * mm, "end": v(8499.1, -8655.96) * mm});
            skLineSegment(sketch, "E4305", {"start": v(8499.1, -8655.96) * mm, "end": v(8480.49, -8666.4) * mm});
            skLineSegment(sketch, "E4306", {"start": v(8480.49, -8666.4) * mm, "end": v(8457.1, -8675.31) * mm});
            skLineSegment(sketch, "E4307", {"start": v(8457.1, -8675.31) * mm, "end": v(8428.63, -8682.63) * mm});
            skLineSegment(sketch, "E4308", {"start": v(8428.63, -8682.63) * mm, "end": v(8394.84, -8688.3) * mm});
            skLineSegment(sketch, "E4309", {"start": v(8394.84, -8688.3) * mm, "end": v(8355.45, -8692.23) * mm});
            skLineSegment(sketch, "E4310", {"start": v(8355.45, -8692.23) * mm, "end": v(8258.35, -8684.57) * mm});
            skLineSegment(sketch, "E4311", {"start": v(8258.35, -8684.57) * mm, "end": v(8161.86, -8675.66) * mm});
            skLineSegment(sketch, "E4312", {"start": v(8161.86, -8675.66) * mm, "end": v(8065.97, -8665.47) * mm});
            skLineSegment(sketch, "E4313", {"start": v(8065.97, -8665.47) * mm, "end": v(7970.65, -8654) * mm});
            skLineSegment(sketch, "E4314", {"start": v(7970.65, -8654) * mm, "end": v(7875.87, -8641.25) * mm});
            skLineSegment(sketch, "E4315", {"start": v(7875.87, -8641.25) * mm, "end": v(7781.6, -8627.2) * mm});
            skLineSegment(sketch, "E4316", {"start": v(7781.6, -8627.2) * mm, "end": v(7687.82, -8611.87) * mm});
            skLineSegment(sketch, "E4317", {"start": v(7687.82, -8611.87) * mm, "end": v(7594.5, -8595.23) * mm});
            skLineSegment(sketch, "E4318", {"start": v(7594.5, -8595.23) * mm, "end": v(7501.6, -8577.28) * mm});
            skLineSegment(sketch, "E4319", {"start": v(7501.6, -8577.28) * mm, "end": v(7409.13, -8558.02) * mm});
            skLineSegment(sketch, "E4320", {"start": v(7409.13, -8558.02) * mm, "end": v(7317.04, -8537.43) * mm});
            skLineSegment(sketch, "E4321", {"start": v(7317.04, -8537.43) * mm, "end": v(7225.3, -8515.52) * mm});
            skLineSegment(sketch, "E4322", {"start": v(7225.3, -8515.52) * mm, "end": v(7133.89, -8492.27) * mm});
            skLineSegment(sketch, "E4323", {"start": v(7133.89, -8492.27) * mm, "end": v(7042.78, -8467.68) * mm});
            skLineSegment(sketch, "E4324", {"start": v(7042.78, -8467.68) * mm, "end": v(6951.95, -8441.74) * mm});
            skLineSegment(sketch, "E4325", {"start": v(6951.95, -8441.74) * mm, "end": v(6861.37, -8414.45) * mm});
            skLineSegment(sketch, "E4326", {"start": v(6861.37, -8414.45) * mm, "end": v(6771.02, -8385.8) * mm});
            skLineSegment(sketch, "E4327", {"start": v(6771.02, -8385.8) * mm, "end": v(6680.86, -8355.78) * mm});
            skLineSegment(sketch, "E4328", {"start": v(6680.86, -8355.78) * mm, "end": v(6590.88, -8324.4) * mm});
            skLineSegment(sketch, "E4329", {"start": v(6590.88, -8324.4) * mm, "end": v(6501.04, -8291.62) * mm});
            skLineSegment(sketch, "E4330", {"start": v(6501.04, -8291.62) * mm, "end": v(6411.32, -8257.46) * mm});
            skLineSegment(sketch, "E4331", {"start": v(6411.32, -8257.46) * mm, "end": v(6321.7, -8221.92) * mm});
            skLineSegment(sketch, "E4332", {"start": v(6321.7, -8221.92) * mm, "end": v(6232.13, -8184.97) * mm});
            skLineSegment(sketch, "E4333", {"start": v(6232.13, -8184.97) * mm, "end": v(6142.61, -8146.62) * mm});
            skLineSegment(sketch, "E4334", {"start": v(10808.28, 2377.67) * mm, "end": v(10731.1, 2354.4) * mm});
            skLineSegment(sketch, "E4335", {"start": v(10731.1, 2354.4) * mm, "end": v(10640.28, 2328.45) * mm});
            skLineSegment(sketch, "E4336", {"start": v(10640.28, 2328.45) * mm, "end": v(10549.18, 2303.85) * mm});
            skLineSegment(sketch, "E4337", {"start": v(10549.18, 2303.85) * mm, "end": v(10457.77, 2280.59) * mm});
            skLineSegment(sketch, "E4338", {"start": v(10457.77, 2280.59) * mm, "end": v(10366.04, 2258.66) * mm});
            skLineSegment(sketch, "E4339", {"start": v(10366.04, 2258.66) * mm, "end": v(10273.96, 2238.06) * mm});
            skLineSegment(sketch, "E4340", {"start": v(10273.96, 2238.06) * mm, "end": v(10181.49, 2218.79) * mm});
            skLineSegment(sketch, "E4341", {"start": v(10181.49, 2218.79) * mm, "end": v(10088.61, 2200.83) * mm});
            skLineSegment(sketch, "E4342", {"start": v(10088.61, 2200.83) * mm, "end": v(9995.3, 2184.18) * mm});
            skLineSegment(sketch, "E4343", {"start": v(9995.3, 2184.18) * mm, "end": v(9901.53, 2168.83) * mm});
            skLineSegment(sketch, "E4344", {"start": v(9901.53, 2168.83) * mm, "end": v(9807.27, 2154.78) * mm});
            skLineSegment(sketch, "E4345", {"start": v(9807.27, 2154.78) * mm, "end": v(9712.5, 2142.02) * mm});
            skLineSegment(sketch, "E4346", {"start": v(9712.5, 2142.02) * mm, "end": v(9617.2, 2130.54) * mm});
            skLineSegment(sketch, "E4347", {"start": v(9617.2, 2130.54) * mm, "end": v(9521.32, 2120.34) * mm});
            skLineSegment(sketch, "E4348", {"start": v(9521.32, 2120.34) * mm, "end": v(9424.85, 2111.41) * mm});
            skLineSegment(sketch, "E4349", {"start": v(9424.85, 2111.41) * mm, "end": v(9327.77, 2103.75) * mm});
            skLineSegment(sketch, "E4350", {"start": v(9327.77, 2103.75) * mm, "end": v(9254.6, 2113.35) * mm});
            skLineSegment(sketch, "E4351", {"start": v(9254.6, 2113.35) * mm, "end": v(9202.74, 2129.59) * mm});
            skLineSegment(sketch, "E4352", {"start": v(9202.74, 2129.59) * mm, "end": v(9170.05, 2151.92) * mm});
            skLineSegment(sketch, "E4353", {"start": v(9170.05, 2151.92) * mm, "end": v(9154.37, 2179.8) * mm});
            skLineSegment(sketch, "E4354", {"start": v(9154.37, 2179.8) * mm, "end": v(9153.52, 2212.68) * mm});
            skLineSegment(sketch, "E4355", {"start": v(9153.52, 2212.68) * mm, "end": v(9165.35, 2250.01) * mm});
            skLineSegment(sketch, "E4356", {"start": v(9165.35, 2250.01) * mm, "end": v(9187.69, 2291.24) * mm});
            skLineSegment(sketch, "E4357", {"start": v(9187.69, 2291.24) * mm, "end": v(9218.39, 2335.83) * mm});
            skLineSegment(sketch, "E4358", {"start": v(9218.39, 2335.83) * mm, "end": v(9255.28, 2383.22) * mm});
            skLineSegment(sketch, "E4359", {"start": v(9255.28, 2383.22) * mm, "end": v(9296.2, 2432.86) * mm});
            skLineSegment(sketch, "E4360", {"start": v(9296.2, 2432.86) * mm, "end": v(9339, 2484.21) * mm});
            skLineSegment(sketch, "E4361", {"start": v(9339, 2484.21) * mm, "end": v(9381.5, 2536.72) * mm});
            skLineSegment(sketch, "E4362", {"start": v(9381.5, 2536.72) * mm, "end": v(9421.55, 2589.84) * mm});
            skLineSegment(sketch, "E4363", {"start": v(9421.55, 2589.84) * mm, "end": v(9456.98, 2643.02) * mm});
            skLineSegment(sketch, "E4364", {"start": v(9456.98, 2643.02) * mm, "end": v(9485.64, 2695.72) * mm});
            skLineSegment(sketch, "E4365", {"start": v(9485.64, 2695.72) * mm, "end": v(9505.36, 2747.38) * mm});
            skLineSegment(sketch, "E4366", {"start": v(9505.36, 2747.38) * mm, "end": v(9513.98, 2797.46) * mm});
            skLineSegment(sketch, "E4367", {"start": v(9513.98, 2797.46) * mm, "end": v(9509.03, 2854.64) * mm});
            skLineSegment(sketch, "E4368", {"start": v(9509.03, 2854.64) * mm, "end": v(9496.68, 2920.25) * mm});
            skLineSegment(sketch, "E4369", {"start": v(9496.68, 2920.25) * mm, "end": v(9480.67, 2979.43) * mm});
            skLineSegment(sketch, "E4370", {"start": v(9480.67, 2979.43) * mm, "end": v(9461.08, 3032.5) * mm});
            skLineSegment(sketch, "E4371", {"start": v(9461.08, 3032.5) * mm, "end": v(9437.98, 3079.78) * mm});
            skLineSegment(sketch, "E4372", {"start": v(9437.98, 3079.78) * mm, "end": v(9411.46, 3121.58) * mm});
            skLineSegment(sketch, "E4373", {"start": v(9411.46, 3121.58) * mm, "end": v(9381.59, 3158.23) * mm});
            skLineSegment(sketch, "E4374", {"start": v(9381.59, 3158.23) * mm, "end": v(9348.45, 3190.05) * mm});
            skLineSegment(sketch, "E4375", {"start": v(9348.45, 3190.05) * mm, "end": v(9312.11, 3217.35) * mm});
            skLineSegment(sketch, "E4376", {"start": v(9312.11, 3217.35) * mm, "end": v(9272.66, 3240.44) * mm});
            skLineSegment(sketch, "E4377", {"start": v(9272.66, 3240.44) * mm, "end": v(9230.18, 3259.66) * mm});
            skLineSegment(sketch, "E4378", {"start": v(9230.18, 3259.66) * mm, "end": v(9184.73, 3275.32) * mm});
            skLineSegment(sketch, "E4379", {"start": v(9184.73, 3275.32) * mm, "end": v(9136.4, 3287.73) * mm});
            skLineSegment(sketch, "E4380", {"start": v(9136.4, 3287.73) * mm, "end": v(9085.27, 3297.22) * mm});
            skLineSegment(sketch, "E4381", {"start": v(9085.27, 3297.22) * mm, "end": v(9031.41, 3304.1) * mm});
            skLineSegment(sketch, "E4382", {"start": v(9031.41, 3304.1) * mm, "end": v(8974.9, 3308.7) * mm});
            skLineSegment(sketch, "E4383", {"start": v(8974.9, 3308.7) * mm, "end": v(8915.82, 3311.32) * mm});
            skLineSegment(sketch, "E4384", {"start": v(8915.82, 3311.32) * mm, "end": v(8854.25, 3312.3) * mm});
            skLineSegment(sketch, "E4385", {"start": v(8854.25, 3312.3) * mm, "end": v(8791.8, 3311.9) * mm});
            skLineSegment(sketch, "E4386", {"start": v(8791.8, 3311.9) * mm, "end": v(8731.7, 3309.97) * mm});
            skLineSegment(sketch, "E4387", {"start": v(8731.7, 3309.97) * mm, "end": v(8674.15, 3306.2) * mm});
            skLineSegment(sketch, "E4388", {"start": v(8674.15, 3306.2) * mm, "end": v(8619.2, 3300.26) * mm});
            skLineSegment(sketch, "E4389", {"start": v(8619.2, 3300.26) * mm, "end": v(8566.96, 3291.85) * mm});
            skLineSegment(sketch, "E4390", {"start": v(8566.96, 3291.85) * mm, "end": v(8517.49, 3280.64) * mm});
            skLineSegment(sketch, "E4391", {"start": v(8517.49, 3280.64) * mm, "end": v(8470.86, 3266.32) * mm});
            skLineSegment(sketch, "E4392", {"start": v(8470.86, 3266.32) * mm, "end": v(8427.16, 3248.56) * mm});
            skLineSegment(sketch, "E4393", {"start": v(8427.16, 3248.56) * mm, "end": v(8386.47, 3227.05) * mm});
            skLineSegment(sketch, "E4394", {"start": v(8386.47, 3227.05) * mm, "end": v(8348.86, 3201.46) * mm});
            skLineSegment(sketch, "E4395", {"start": v(8348.86, 3201.46) * mm, "end": v(8314.42, 3171.48) * mm});
            skLineSegment(sketch, "E4396", {"start": v(8314.42, 3171.48) * mm, "end": v(8283.2, 3136.79) * mm});
            skLineSegment(sketch, "E4397", {"start": v(8283.2, 3136.79) * mm, "end": v(8255.32, 3097.07) * mm});
            skLineSegment(sketch, "E4398", {"start": v(8255.32, 3097.07) * mm, "end": v(8230.83, 3052) * mm});
            skLineSegment(sketch, "E4399", {"start": v(8230.83, 3052) * mm, "end": v(8209.8, 3001.26) * mm});
            skLineSegment(sketch, "E4400", {"start": v(8209.8, 3001.26) * mm, "end": v(8192.34, 2944.54) * mm});
            skLineSegment(sketch, "E4401", {"start": v(8192.34, 2944.54) * mm, "end": v(8178.5, 2881.5) * mm});
            skLineSegment(sketch, "E4402", {"start": v(8178.5, 2881.5) * mm, "end": v(8169.57, 2821.55) * mm});
            skLineSegment(sketch, "E4403", {"start": v(8169.57, 2821.55) * mm, "end": v(8169.06, 2797.29) * mm});
            skLineSegment(sketch, "E4404", {"start": v(8169.06, 2797.29) * mm, "end": v(8171.86, 2772.5) * mm});
            skLineSegment(sketch, "E4405", {"start": v(8171.86, 2772.5) * mm, "end": v(8177.71, 2747.24) * mm});
            skLineSegment(sketch, "E4406", {"start": v(8177.71, 2747.24) * mm, "end": v(8186.33, 2721.58) * mm});
            skLineSegment(sketch, "E4407", {"start": v(8186.33, 2721.58) * mm, "end": v(8197.46, 2695.6) * mm});
            skLineSegment(sketch, "E4408", {"start": v(8197.46, 2695.6) * mm, "end": v(8210.82, 2669.36) * mm});
            skLineSegment(sketch, "E4409", {"start": v(8210.82, 2669.36) * mm, "end": v(8226.14, 2642.93) * mm});
            skLineSegment(sketch, "E4410", {"start": v(8226.14, 2642.93) * mm, "end": v(8243.16, 2616.37) * mm});
            skLineSegment(sketch, "E4411", {"start": v(8243.16, 2616.37) * mm, "end": v(8261.6, 2589.76) * mm});
            skLineSegment(sketch, "E4412", {"start": v(8261.6, 2589.76) * mm, "end": v(8281.2, 2563.17) * mm});
            skLineSegment(sketch, "E4413", {"start": v(8281.2, 2563.17) * mm, "end": v(8301.67, 2536.66) * mm});
            skLineSegment(sketch, "E4414", {"start": v(8301.67, 2536.66) * mm, "end": v(8322.76, 2510.3) * mm});
            skLineSegment(sketch, "E4415", {"start": v(8322.76, 2510.3) * mm, "end": v(8344.19, 2484.16) * mm});
            skLineSegment(sketch, "E4416", {"start": v(8344.19, 2484.16) * mm, "end": v(8365.7, 2458.31) * mm});
            skLineSegment(sketch, "E4417", {"start": v(8365.7, 2458.31) * mm, "end": v(8387, 2432.82) * mm});
            skLineSegment(sketch, "E4418", {"start": v(8387, 2432.82) * mm, "end": v(8407.83, 2407.76) * mm});
            skLineSegment(sketch, "E4419", {"start": v(8407.83, 2407.76) * mm, "end": v(8427.93, 2383.19) * mm});
            skLineSegment(sketch, "E4420", {"start": v(8427.93, 2383.19) * mm, "end": v(8447.02, 2359.18) * mm});
            skLineSegment(sketch, "E4421", {"start": v(8447.02, 2359.18) * mm, "end": v(8464.83, 2335.8) * mm});
            skLineSegment(sketch, "E4422", {"start": v(8464.83, 2335.8) * mm, "end": v(8481.1, 2313.14) * mm});
            skLineSegment(sketch, "E4423", {"start": v(8481.1, 2313.14) * mm, "end": v(8495.54, 2291.23) * mm});
            skLineSegment(sketch, "E4424", {"start": v(8495.54, 2291.23) * mm, "end": v(8507.9, 2270.17) * mm});
            skLineSegment(sketch, "E4425", {"start": v(8507.9, 2270.17) * mm, "end": v(8517.9, 2250) * mm});
            skLineSegment(sketch, "E4426", {"start": v(8517.9, 2250) * mm, "end": v(8525.26, 2230.82) * mm});
            skLineSegment(sketch, "E4427", {"start": v(8525.26, 2230.82) * mm, "end": v(8529.72, 2212.68) * mm});
            skLineSegment(sketch, "E4428", {"start": v(8529.72, 2212.68) * mm, "end": v(8531.02, 2195.65) * mm});
            skLineSegment(sketch, "E4429", {"start": v(8531.02, 2195.65) * mm, "end": v(8528.87, 2179.8) * mm});
            skLineSegment(sketch, "E4430", {"start": v(8528.87, 2179.8) * mm, "end": v(8523.02, 2165.2) * mm});
            skLineSegment(sketch, "E4431", {"start": v(8523.02, 2165.2) * mm, "end": v(8513.18, 2151.92) * mm});
            skLineSegment(sketch, "E4432", {"start": v(8513.18, 2151.92) * mm, "end": v(8499.1, 2140.03) * mm});
            skLineSegment(sketch, "E4433", {"start": v(8499.1, 2140.03) * mm, "end": v(8480.49, 2129.59) * mm});
            skLineSegment(sketch, "E4434", {"start": v(8480.49, 2129.59) * mm, "end": v(8457.1, 2120.67) * mm});
            skLineSegment(sketch, "E4435", {"start": v(8457.1, 2120.67) * mm, "end": v(8428.63, 2113.35) * mm});
            skLineSegment(sketch, "E4436", {"start": v(8428.63, 2113.35) * mm, "end": v(8394.84, 2107.68) * mm});
            skLineSegment(sketch, "E4437", {"start": v(8394.84, 2107.68) * mm, "end": v(8355.45, 2103.75) * mm});
            skLineSegment(sketch, "E4438", {"start": v(8355.45, 2103.75) * mm, "end": v(8258.35, 2111.41) * mm});
            skLineSegment(sketch, "E4439", {"start": v(8258.35, 2111.41) * mm, "end": v(8161.86, 2120.34) * mm});
            skLineSegment(sketch, "E4440", {"start": v(8161.86, 2120.34) * mm, "end": v(8065.97, 2130.54) * mm});
            skLineSegment(sketch, "E4441", {"start": v(8065.97, 2130.54) * mm, "end": v(7970.65, 2142.02) * mm});
            skLineSegment(sketch, "E4442", {"start": v(7970.65, 2142.02) * mm, "end": v(7875.87, 2154.78) * mm});
            skLineSegment(sketch, "E4443", {"start": v(7875.87, 2154.78) * mm, "end": v(7781.6, 2168.83) * mm});
            skLineSegment(sketch, "E4444", {"start": v(7781.6, 2168.83) * mm, "end": v(7687.82, 2184.18) * mm});
            skLineSegment(sketch, "E4445", {"start": v(7687.82, 2184.18) * mm, "end": v(7594.5, 2200.83) * mm});
            skLineSegment(sketch, "E4446", {"start": v(7594.5, 2200.83) * mm, "end": v(7501.6, 2218.79) * mm});
            skLineSegment(sketch, "E4447", {"start": v(7501.6, 2218.79) * mm, "end": v(7409.13, 2238.06) * mm});
            skLineSegment(sketch, "E4448", {"start": v(7409.13, 2238.06) * mm, "end": v(7317.04, 2258.66) * mm});
            skLineSegment(sketch, "E4449", {"start": v(7317.04, 2258.66) * mm, "end": v(7225.3, 2280.59) * mm});
            skLineSegment(sketch, "E4450", {"start": v(7225.3, 2280.59) * mm, "end": v(7133.89, 2303.85) * mm});
            skLineSegment(sketch, "E4451", {"start": v(7133.89, 2303.85) * mm, "end": v(7042.78, 2328.45) * mm});
            skLineSegment(sketch, "E4452", {"start": v(7042.78, 2328.45) * mm, "end": v(6951.95, 2354.4) * mm});
            skLineSegment(sketch, "E4453", {"start": v(6951.95, 2354.4) * mm, "end": v(6861.37, 2381.7) * mm});
            skLineSegment(sketch, "E4454", {"start": v(6861.37, 2381.7) * mm, "end": v(6771.02, 2410.37) * mm});
            skLineSegment(sketch, "E4455", {"start": v(6771.02, 2410.37) * mm, "end": v(6680.86, 2440.4) * mm});
            skLineSegment(sketch, "E4456", {"start": v(6680.86, 2440.4) * mm, "end": v(6590.88, 2471.8) * mm});
            skLineSegment(sketch, "E4457", {"start": v(6590.88, 2471.8) * mm, "end": v(6501.04, 2504.58) * mm});
            skLineSegment(sketch, "E4458", {"start": v(6501.04, 2504.58) * mm, "end": v(6411.32, 2538.75) * mm});
            skLineSegment(sketch, "E4459", {"start": v(6411.32, 2538.75) * mm, "end": v(6321.7, 2574.3) * mm});
            skLineSegment(sketch, "E4460", {"start": v(6321.7, 2574.3) * mm, "end": v(6232.13, 2611.26) * mm});
            skLineSegment(sketch, "E4461", {"start": v(6232.13, 2611.26) * mm, "end": v(6142.61, 2649.62) * mm});
            skLineSegment(sketch, "E4462", {"start": v(6142.61, -2748.37) * mm, "end": v(6232.13, -2710.02) * mm});
            skLineSegment(sketch, "E4463", {"start": v(6232.13, -2710.02) * mm, "end": v(6321.7, -2673.07) * mm});
            skLineSegment(sketch, "E4464", {"start": v(6321.7, -2673.07) * mm, "end": v(6411.32, -2637.52) * mm});
            skLineSegment(sketch, "E4465", {"start": v(6411.32, -2637.52) * mm, "end": v(6501.04, -2603.37) * mm});
            skLineSegment(sketch, "E4466", {"start": v(6501.04, -2603.37) * mm, "end": v(6590.88, -2570.6) * mm});
            skLineSegment(sketch, "E4467", {"start": v(6590.88, -2570.6) * mm, "end": v(6680.86, -2539.2) * mm});
            skLineSegment(sketch, "E4468", {"start": v(6680.86, -2539.2) * mm, "end": v(6771.02, -2509.19) * mm});
            skLineSegment(sketch, "E4469", {"start": v(6771.02, -2509.19) * mm, "end": v(6861.37, -2480.54) * mm});
            skLineSegment(sketch, "E4470", {"start": v(6861.37, -2480.54) * mm, "end": v(6951.95, -2453.24) * mm});
            skLineSegment(sketch, "E4471", {"start": v(6951.95, -2453.24) * mm, "end": v(7042.78, -2427.3) * mm});
            skLineSegment(sketch, "E4472", {"start": v(7042.78, -2427.3) * mm, "end": v(7133.89, -2402.72) * mm});
            skLineSegment(sketch, "E4473", {"start": v(7133.89, -2402.72) * mm, "end": v(7225.3, -2379.47) * mm});
            skLineSegment(sketch, "E4474", {"start": v(7225.3, -2379.47) * mm, "end": v(7317.04, -2357.55) * mm});
            skLineSegment(sketch, "E4475", {"start": v(7317.04, -2357.55) * mm, "end": v(7409.13, -2336.97) * mm});
            skLineSegment(sketch, "E4476", {"start": v(7409.13, -2336.97) * mm, "end": v(7501.6, -2317.7) * mm});
            skLineSegment(sketch, "E4477", {"start": v(7501.6, -2317.7) * mm, "end": v(7594.5, -2299.75) * mm});
            skLineSegment(sketch, "E4478", {"start": v(7594.5, -2299.75) * mm, "end": v(7687.82, -2283.11) * mm});
            skLineSegment(sketch, "E4479", {"start": v(7687.82, -2283.11) * mm, "end": v(7781.6, -2267.78) * mm});
            skLineSegment(sketch, "E4480", {"start": v(7781.6, -2267.78) * mm, "end": v(7875.87, -2253.74) * mm});
            skLineSegment(sketch, "E4481", {"start": v(7875.87, -2253.74) * mm, "end": v(7970.65, -2240.99) * mm});
            skLineSegment(sketch, "E4482", {"start": v(7970.65, -2240.99) * mm, "end": v(8065.97, -2229.52) * mm});
            skLineSegment(sketch, "E4483", {"start": v(8065.97, -2229.52) * mm, "end": v(8161.86, -2219.33) * mm});
            skLineSegment(sketch, "E4484", {"start": v(8161.86, -2219.33) * mm, "end": v(8258.35, -2210.41) * mm});
            skLineSegment(sketch, "E4485", {"start": v(8258.35, -2210.41) * mm, "end": v(8355.45, -2202.76) * mm});
            skLineSegment(sketch, "E4486", {"start": v(8355.45, -2202.76) * mm, "end": v(8428.63, -2212.35) * mm});
            skLineSegment(sketch, "E4487", {"start": v(8428.63, -2212.35) * mm, "end": v(8480.49, -2228.59) * mm});
            skLineSegment(sketch, "E4488", {"start": v(8480.49, -2228.59) * mm, "end": v(8513.18, -2250.92) * mm});
            skLineSegment(sketch, "E4489", {"start": v(8513.18, -2250.92) * mm, "end": v(8528.87, -2278.79) * mm});
            skLineSegment(sketch, "E4490", {"start": v(8528.87, -2278.79) * mm, "end": v(8529.72, -2311.65) * mm});
            skLineSegment(sketch, "E4491", {"start": v(8529.72, -2311.65) * mm, "end": v(8517.9, -2348.97) * mm});
            skLineSegment(sketch, "E4492", {"start": v(8517.9, -2348.97) * mm, "end": v(8495.54, -2390.18) * mm});
            skLineSegment(sketch, "E4493", {"start": v(8495.54, -2390.18) * mm, "end": v(8464.83, -2434.75) * mm});
            skLineSegment(sketch, "E4494", {"start": v(8464.83, -2434.75) * mm, "end": v(8427.93, -2482.12) * mm});
            skLineSegment(sketch, "E4495", {"start": v(8427.93, -2482.12) * mm, "end": v(8387, -2531.75) * mm});
            skLineSegment(sketch, "E4496", {"start": v(8387, -2531.75) * mm, "end": v(8344.19, -2583.09) * mm});
            skLineSegment(sketch, "E4497", {"start": v(8344.19, -2583.09) * mm, "end": v(8301.67, -2635.58) * mm});
            skLineSegment(sketch, "E4498", {"start": v(8301.67, -2635.58) * mm, "end": v(8261.6, -2688.69) * mm});
            skLineSegment(sketch, "E4499", {"start": v(8261.6, -2688.69) * mm, "end": v(8226.14, -2741.86) * mm});
            skLineSegment(sketch, "E4500", {"start": v(8226.14, -2741.86) * mm, "end": v(8197.46, -2794.55) * mm});
            skLineSegment(sketch, "E4501", {"start": v(8197.46, -2794.55) * mm, "end": v(8177.71, -2846.2) * mm});
            skLineSegment(sketch, "E4502", {"start": v(8177.71, -2846.2) * mm, "end": v(8169.06, -2896.28) * mm});
            skLineSegment(sketch, "E4503", {"start": v(8169.06, -2896.28) * mm, "end": v(8174, -2953.46) * mm});
            skLineSegment(sketch, "E4504", {"start": v(8174, -2953.46) * mm, "end": v(8186.36, -3019.1) * mm});
            skLineSegment(sketch, "E4505", {"start": v(8186.36, -3019.1) * mm, "end": v(8202.39, -3078.3) * mm});
            skLineSegment(sketch, "E4506", {"start": v(8202.39, -3078.3) * mm, "end": v(8222, -3131.38) * mm});
            skLineSegment(sketch, "E4507", {"start": v(8222, -3131.38) * mm, "end": v(8245.1, -3178.67) * mm});
            skLineSegment(sketch, "E4508", {"start": v(8245.1, -3178.67) * mm, "end": v(8271.65, -3220.49) * mm});
            skLineSegment(sketch, "E4509", {"start": v(8271.65, -3220.49) * mm, "end": v(8301.54, -3257.15) * mm});
            skLineSegment(sketch, "E4510", {"start": v(8301.54, -3257.15) * mm, "end": v(8334.7, -3288.97) * mm});
            skLineSegment(sketch, "E4511", {"start": v(8334.7, -3288.97) * mm, "end": v(8371.05, -3316.27) * mm});
            skLineSegment(sketch, "E4512", {"start": v(8371.05, -3316.27) * mm, "end": v(8410.52, -3339.37) * mm});
            skLineSegment(sketch, "E4513", {"start": v(8410.52, -3339.37) * mm, "end": v(8453.03, -3358.6) * mm});
            skLineSegment(sketch, "E4514", {"start": v(8453.03, -3358.6) * mm, "end": v(8498.49, -3374.25) * mm});
            skLineSegment(sketch, "E4515", {"start": v(8498.49, -3374.25) * mm, "end": v(8546.83, -3386.67) * mm});
            skLineSegment(sketch, "E4516", {"start": v(8546.83, -3386.67) * mm, "end": v(8597.98, -3396.16) * mm});
            skLineSegment(sketch, "E4517", {"start": v(8597.98, -3396.16) * mm, "end": v(8651.85, -3403.04) * mm});
            skLineSegment(sketch, "E4518", {"start": v(8651.85, -3403.04) * mm, "end": v(8708.37, -3407.64) * mm});
            skLineSegment(sketch, "E4519", {"start": v(8708.37, -3407.64) * mm, "end": v(8767.46, -3410.27) * mm});
            skLineSegment(sketch, "E4520", {"start": v(8767.46, -3410.27) * mm, "end": v(8829.03, -3411.25) * mm});
            skLineSegment(sketch, "E4521", {"start": v(8829.03, -3411.25) * mm, "end": v(8891.49, -3410.84) * mm});
            skLineSegment(sketch, "E4522", {"start": v(8891.49, -3410.84) * mm, "end": v(8951.57, -3408.9) * mm});
            skLineSegment(sketch, "E4523", {"start": v(8951.57, -3408.9) * mm, "end": v(9009.12, -3405.14) * mm});
            skLineSegment(sketch, "E4524", {"start": v(9009.12, -3405.14) * mm, "end": v(9064.05, -3399.2) * mm});
            skLineSegment(sketch, "E4525", {"start": v(9064.05, -3399.2) * mm, "end": v(9116.28, -3390.8) * mm});
            skLineSegment(sketch, "E4526", {"start": v(9116.28, -3390.8) * mm, "end": v(9165.74, -3379.6) * mm});
            skLineSegment(sketch, "E4527", {"start": v(9165.74, -3379.6) * mm, "end": v(9212.35, -3365.27) * mm});
            skLineSegment(sketch, "E4528", {"start": v(9212.35, -3365.27) * mm, "end": v(9256.03, -3347.5) * mm});
            skLineSegment(sketch, "E4529", {"start": v(9256.03, -3347.5) * mm, "end": v(9296.7, -3326) * mm});
            skLineSegment(sketch, "E4530", {"start": v(9296.7, -3326) * mm, "end": v(9334.3, -3300.41) * mm});
            skLineSegment(sketch, "E4531", {"start": v(9334.3, -3300.41) * mm, "end": v(9368.72, -3270.44) * mm});
            skLineSegment(sketch, "E4532", {"start": v(9368.72, -3270.44) * mm, "end": v(9399.9, -3235.75) * mm});
            skLineSegment(sketch, "E4533", {"start": v(9399.9, -3235.75) * mm, "end": v(9427.78, -3196.03) * mm});
            skLineSegment(sketch, "E4534", {"start": v(9427.78, -3196.03) * mm, "end": v(9452.25, -3150.97) * mm});
            skLineSegment(sketch, "E4535", {"start": v(9452.25, -3150.97) * mm, "end": v(9473.26, -3100.24) * mm});
            skLineSegment(sketch, "E4536", {"start": v(9473.26, -3100.24) * mm, "end": v(9490.7, -3043.53) * mm});
            skLineSegment(sketch, "E4537", {"start": v(9490.7, -3043.53) * mm, "end": v(9504.53, -2980.5) * mm});
            skLineSegment(sketch, "E4538", {"start": v(9504.53, -2980.5) * mm, "end": v(9513.46, -2920.55) * mm});
            skLineSegment(sketch, "E4539", {"start": v(9513.46, -2920.55) * mm, "end": v(9513.98, -2896.28) * mm});
            skLineSegment(sketch, "E4540", {"start": v(9513.98, -2896.28) * mm, "end": v(9511.2, -2871.47) * mm});
            skLineSegment(sketch, "E4541", {"start": v(9511.2, -2871.47) * mm, "end": v(9505.36, -2846.2) * mm});
            skLineSegment(sketch, "E4542", {"start": v(9505.36, -2846.2) * mm, "end": v(9496.75, -2820.54) * mm});
            skLineSegment(sketch, "E4543", {"start": v(9496.75, -2820.54) * mm, "end": v(9485.64, -2794.55) * mm});
            skLineSegment(sketch, "E4544", {"start": v(9485.64, -2794.55) * mm, "end": v(9472.3, -2768.3) * mm});
            skLineSegment(sketch, "E4545", {"start": v(9472.3, -2768.3) * mm, "end": v(9456.98, -2741.86) * mm});
            skLineSegment(sketch, "E4546", {"start": v(9456.98, -2741.86) * mm, "end": v(9439.98, -2715.3) * mm});
            skLineSegment(sketch, "E4547", {"start": v(9439.98, -2715.3) * mm, "end": v(9421.55, -2688.69) * mm});
            skLineSegment(sketch, "E4548", {"start": v(9421.55, -2688.69) * mm, "end": v(9401.96, -2662.1) * mm});
            skLineSegment(sketch, "E4549", {"start": v(9401.96, -2662.1) * mm, "end": v(9381.5, -2635.58) * mm});
            skLineSegment(sketch, "E4550", {"start": v(9381.5, -2635.58) * mm, "end": v(9360.42, -2609.22) * mm});
            skLineSegment(sketch, "E4551", {"start": v(9360.42, -2609.22) * mm, "end": v(9339, -2583.09) * mm});
            skLineSegment(sketch, "E4552", {"start": v(9339, -2583.09) * mm, "end": v(9317.5, -2557.24) * mm});
            skLineSegment(sketch, "E4553", {"start": v(9317.5, -2557.24) * mm, "end": v(9296.2, -2531.75) * mm});
            skLineSegment(sketch, "E4554", {"start": v(9296.2, -2531.75) * mm, "end": v(9275.37, -2506.69) * mm});
            skLineSegment(sketch, "E4555", {"start": v(9275.37, -2506.69) * mm, "end": v(9255.28, -2482.12) * mm});
            skLineSegment(sketch, "E4556", {"start": v(9255.28, -2482.12) * mm, "end": v(9236.2, -2458.12) * mm});
            skLineSegment(sketch, "E4557", {"start": v(9236.2, -2458.12) * mm, "end": v(9218.39, -2434.75) * mm});
            skLineSegment(sketch, "E4558", {"start": v(9218.39, -2434.75) * mm, "end": v(9202.13, -2412.08) * mm});
            skLineSegment(sketch, "E4559", {"start": v(9202.13, -2412.08) * mm, "end": v(9187.69, -2390.18) * mm});
            skLineSegment(sketch, "E4560", {"start": v(9187.69, -2390.18) * mm, "end": v(9175.34, -2369.12) * mm});
            skLineSegment(sketch, "E4561", {"start": v(9175.34, -2369.12) * mm, "end": v(9165.35, -2348.97) * mm});
            skLineSegment(sketch, "E4562", {"start": v(9165.35, -2348.97) * mm, "end": v(9157.98, -2329.79) * mm});
            skLineSegment(sketch, "E4563", {"start": v(9157.98, -2329.79) * mm, "end": v(9153.52, -2311.65) * mm});
            skLineSegment(sketch, "E4564", {"start": v(9153.52, -2311.65) * mm, "end": v(9152.22, -2294.63) * mm});
            skLineSegment(sketch, "E4565", {"start": v(9152.22, -2294.63) * mm, "end": v(9154.37, -2278.79) * mm});
            skLineSegment(sketch, "E4566", {"start": v(9154.37, -2278.79) * mm, "end": v(9160.22, -2264.2) * mm});
            skLineSegment(sketch, "E4567", {"start": v(9160.22, -2264.2) * mm, "end": v(9170.05, -2250.92) * mm});
            skLineSegment(sketch, "E4568", {"start": v(9170.05, -2250.92) * mm, "end": v(9184.14, -2239.02) * mm});
            skLineSegment(sketch, "E4569", {"start": v(9184.14, -2239.02) * mm, "end": v(9202.74, -2228.59) * mm});
            skLineSegment(sketch, "E4570", {"start": v(9202.74, -2228.59) * mm, "end": v(9226.14, -2219.67) * mm});
            skLineSegment(sketch, "E4571", {"start": v(9226.14, -2219.67) * mm, "end": v(9254.6, -2212.35) * mm});
            skLineSegment(sketch, "E4572", {"start": v(9254.6, -2212.35) * mm, "end": v(9288.38, -2206.7) * mm});
            skLineSegment(sketch, "E4573", {"start": v(9288.38, -2206.7) * mm, "end": v(9327.77, -2202.76) * mm});
            skLineSegment(sketch, "E4574", {"start": v(9327.77, -2202.76) * mm, "end": v(9424.85, -2210.41) * mm});
            skLineSegment(sketch, "E4575", {"start": v(9424.85, -2210.41) * mm, "end": v(9521.32, -2219.33) * mm});
            skLineSegment(sketch, "E4576", {"start": v(9521.32, -2219.33) * mm, "end": v(9617.2, -2229.52) * mm});
            skLineSegment(sketch, "E4577", {"start": v(9617.2, -2229.52) * mm, "end": v(9712.5, -2240.99) * mm});
            skLineSegment(sketch, "E4578", {"start": v(9712.5, -2240.99) * mm, "end": v(9807.27, -2253.74) * mm});
            skLineSegment(sketch, "E4579", {"start": v(9807.27, -2253.74) * mm, "end": v(9901.53, -2267.78) * mm});
            skLineSegment(sketch, "E4580", {"start": v(9901.53, -2267.78) * mm, "end": v(9995.3, -2283.11) * mm});
            skLineSegment(sketch, "E4581", {"start": v(9995.3, -2283.11) * mm, "end": v(10088.61, -2299.75) * mm});
            skLineSegment(sketch, "E4582", {"start": v(10088.61, -2299.75) * mm, "end": v(10181.49, -2317.7) * mm});
            skLineSegment(sketch, "E4583", {"start": v(10181.49, -2317.7) * mm, "end": v(10273.96, -2336.97) * mm});
            skLineSegment(sketch, "E4584", {"start": v(10273.96, -2336.97) * mm, "end": v(10366.04, -2357.55) * mm});
            skLineSegment(sketch, "E4585", {"start": v(10366.04, -2357.55) * mm, "end": v(10457.77, -2379.47) * mm});
            skLineSegment(sketch, "E4586", {"start": v(10457.77, -2379.47) * mm, "end": v(10549.18, -2402.72) * mm});
            skLineSegment(sketch, "E4587", {"start": v(10549.18, -2402.72) * mm, "end": v(10640.28, -2427.3) * mm});
            skLineSegment(sketch, "E4588", {"start": v(10640.28, -2427.3) * mm, "end": v(10731.1, -2453.24) * mm});
            skLineSegment(sketch, "E4589", {"start": v(10731.1, -2453.24) * mm, "end": v(10808.28, -2476.5) * mm});
            skLineSegment(sketch, "E4590", {"start": v(10110.42, 13001.1) * mm, "end": v(10088.61, 12996.9) * mm});
            skLineSegment(sketch, "E4591", {"start": v(10088.61, 12996.9) * mm, "end": v(9995.3, 12980.24) * mm});
            skLineSegment(sketch, "E4592", {"start": v(9995.3, 12980.24) * mm, "end": v(9901.53, 12964.89) * mm});
            skLineSegment(sketch, "E4593", {"start": v(9901.53, 12964.89) * mm, "end": v(9807.27, 12950.83) * mm});
            skLineSegment(sketch, "E4594", {"start": v(9807.27, 12950.83) * mm, "end": v(9712.5, 12938.06) * mm});
            skLineSegment(sketch, "E4595", {"start": v(9712.5, 12938.06) * mm, "end": v(9617.2, 12926.57) * mm});
            skLineSegment(sketch, "E4596", {"start": v(9617.2, 12926.57) * mm, "end": v(9521.32, 12916.36) * mm});
            skLineSegment(sketch, "E4597", {"start": v(9521.32, 12916.36) * mm, "end": v(9424.85, 12907.41) * mm});
            skLineSegment(sketch, "E4598", {"start": v(9424.85, 12907.41) * mm, "end": v(9327.77, 12899.73) * mm});
            skLineSegment(sketch, "E4599", {"start": v(9327.77, 12899.73) * mm, "end": v(9254.6, 12909.36) * mm});
            skLineSegment(sketch, "E4600", {"start": v(9254.6, 12909.36) * mm, "end": v(9202.74, 12925.63) * mm});
            skLineSegment(sketch, "E4601", {"start": v(9202.74, 12925.63) * mm, "end": v(9170.05, 12948) * mm});
            skLineSegment(sketch, "E4602", {"start": v(9170.05, 12948) * mm, "end": v(9154.37, 12975.89) * mm});
            skLineSegment(sketch, "E4603", {"start": v(9154.37, 12975.89) * mm, "end": v(9153.52, 13008.77) * mm});
            skLineSegment(sketch, "E4604", {"start": v(9153.52, 13008.77) * mm, "end": v(9165.35, 13046.1) * mm});
            skLineSegment(sketch, "E4605", {"start": v(9165.35, 13046.1) * mm, "end": v(9187.69, 13087.33) * mm});
            skLineSegment(sketch, "E4606", {"start": v(9187.69, 13087.33) * mm, "end": v(9218.39, 13131.91) * mm});
            skLineSegment(sketch, "E4607", {"start": v(9218.39, 13131.91) * mm, "end": v(9255.28, 13179.29) * mm});
            skLineSegment(sketch, "E4608", {"start": v(9255.28, 13179.29) * mm, "end": v(9296.2, 13228.92) * mm});
            skLineSegment(sketch, "E4609", {"start": v(9296.2, 13228.92) * mm, "end": v(9339, 13280.26) * mm});
            skLineSegment(sketch, "E4610", {"start": v(9339, 13280.26) * mm, "end": v(9381.5, 13332.75) * mm});
            skLineSegment(sketch, "E4611", {"start": v(9381.5, 13332.75) * mm, "end": v(9421.55, 13385.86) * mm});
            skLineSegment(sketch, "E4612", {"start": v(9421.55, 13385.86) * mm, "end": v(9456.98, 13439.03) * mm});
            skLineSegment(sketch, "E4613", {"start": v(9456.98, 13439.03) * mm, "end": v(9485.64, 13491.71) * mm});
            skLineSegment(sketch, "E4614", {"start": v(9485.64, 13491.71) * mm, "end": v(9505.36, 13543.37) * mm});
            skLineSegment(sketch, "E4615", {"start": v(9505.36, 13543.37) * mm, "end": v(9513.98, 13593.44) * mm});
            skLineSegment(sketch, "E4616", {"start": v(9513.98, 13593.44) * mm, "end": v(9509.03, 13650.63) * mm});
            skLineSegment(sketch, "E4617", {"start": v(9509.03, 13650.63) * mm, "end": v(9496.68, 13716.27) * mm});
            skLineSegment(sketch, "E4618", {"start": v(9496.68, 13716.27) * mm, "end": v(9480.67, 13775.47) * mm});
            skLineSegment(sketch, "E4619", {"start": v(9480.67, 13775.47) * mm, "end": v(9461.08, 13828.55) * mm});
            skLineSegment(sketch, "E4620", {"start": v(9461.08, 13828.55) * mm, "end": v(9437.98, 13875.84) * mm});
            skLineSegment(sketch, "E4621", {"start": v(9437.98, 13875.84) * mm, "end": v(9411.46, 13917.65) * mm});
            skLineSegment(sketch, "E4622", {"start": v(9411.46, 13917.65) * mm, "end": v(9381.59, 13954.3) * mm});
            skLineSegment(sketch, "E4623", {"start": v(9381.59, 13954.3) * mm, "end": v(9348.45, 13986.1) * mm});
            skLineSegment(sketch, "E4624", {"start": v(9348.45, 13986.1) * mm, "end": v(9312.11, 14013.4) * mm});
            skLineSegment(sketch, "E4625", {"start": v(9312.11, 14013.4) * mm, "end": v(9272.66, 14036.49) * mm});
            skLineSegment(sketch, "E4626", {"start": v(9272.66, 14036.49) * mm, "end": v(9230.18, 14055.7) * mm});
            skLineSegment(sketch, "E4627", {"start": v(9230.18, 14055.7) * mm, "end": v(9184.73, 14071.34) * mm});
            skLineSegment(sketch, "E4628", {"start": v(9184.73, 14071.34) * mm, "end": v(9136.4, 14083.74) * mm});
            skLineSegment(sketch, "E4629", {"start": v(9136.4, 14083.74) * mm, "end": v(9085.27, 14093.22) * mm});
            skLineSegment(sketch, "E4630", {"start": v(9085.27, 14093.22) * mm, "end": v(9031.41, 14100.1) * mm});
            skLineSegment(sketch, "E4631", {"start": v(9031.41, 14100.1) * mm, "end": v(8974.9, 14104.68) * mm});
            skLineSegment(sketch, "E4632", {"start": v(8974.9, 14104.68) * mm, "end": v(8915.82, 14107.3) * mm});
            skLineSegment(sketch, "E4633", {"start": v(8915.82, 14107.3) * mm, "end": v(8854.25, 14108.28) * mm});
            skLineSegment(sketch, "E4634", {"start": v(8854.25, 14108.28) * mm, "end": v(8791.8, 14107.87) * mm});
            skLineSegment(sketch, "E4635", {"start": v(8791.8, 14107.87) * mm, "end": v(8731.7, 14105.95) * mm});
            skLineSegment(sketch, "E4636", {"start": v(8731.7, 14105.95) * mm, "end": v(8674.15, 14102.19) * mm});
            skLineSegment(sketch, "E4637", {"start": v(8674.15, 14102.19) * mm, "end": v(8619.2, 14096.26) * mm});
            skLineSegment(sketch, "E4638", {"start": v(8619.2, 14096.26) * mm, "end": v(8566.96, 14087.87) * mm});
            skLineSegment(sketch, "E4639", {"start": v(8566.96, 14087.87) * mm, "end": v(8517.49, 14076.67) * mm});
            skLineSegment(sketch, "E4640", {"start": v(8517.49, 14076.67) * mm, "end": v(8470.86, 14062.36) * mm});
            skLineSegment(sketch, "E4641", {"start": v(8470.86, 14062.36) * mm, "end": v(8427.16, 14044.62) * mm});
            skLineSegment(sketch, "E4642", {"start": v(8427.16, 14044.62) * mm, "end": v(8386.47, 14023.12) * mm});
            skLineSegment(sketch, "E4643", {"start": v(8386.47, 14023.12) * mm, "end": v(8348.86, 13997.55) * mm});
            skLineSegment(sketch, "E4644", {"start": v(8348.86, 13997.55) * mm, "end": v(8314.42, 13967.59) * mm});
            skLineSegment(sketch, "E4645", {"start": v(8314.42, 13967.59) * mm, "end": v(8283.2, 13932.91) * mm});
            skLineSegment(sketch, "E4646", {"start": v(8283.2, 13932.91) * mm, "end": v(8255.32, 13893.2) * mm});
            skLineSegment(sketch, "E4647", {"start": v(8255.32, 13893.2) * mm, "end": v(8230.83, 13848.15) * mm});
            skLineSegment(sketch, "E4648", {"start": v(8230.83, 13848.15) * mm, "end": v(8209.8, 13797.42) * mm});
            skLineSegment(sketch, "E4649", {"start": v(8209.8, 13797.42) * mm, "end": v(8192.34, 13740.7) * mm});
            skLineSegment(sketch, "E4650", {"start": v(8192.34, 13740.7) * mm, "end": v(8178.5, 13677.68) * mm});
            skLineSegment(sketch, "E4651", {"start": v(8178.5, 13677.68) * mm, "end": v(8169.57, 13617.72) * mm});
            skLineSegment(sketch, "E4652", {"start": v(8169.57, 13617.72) * mm, "end": v(8169.06, 13593.44) * mm});
            skLineSegment(sketch, "E4653", {"start": v(8169.06, 13593.44) * mm, "end": v(8171.86, 13568.64) * mm});
            skLineSegment(sketch, "E4654", {"start": v(8171.86, 13568.64) * mm, "end": v(8177.71, 13543.37) * mm});
            skLineSegment(sketch, "E4655", {"start": v(8177.71, 13543.37) * mm, "end": v(8186.33, 13517.7) * mm});
            skLineSegment(sketch, "E4656", {"start": v(8186.33, 13517.7) * mm, "end": v(8197.46, 13491.71) * mm});
            skLineSegment(sketch, "E4657", {"start": v(8197.46, 13491.71) * mm, "end": v(8210.82, 13465.47) * mm});
            skLineSegment(sketch, "E4658", {"start": v(8210.82, 13465.47) * mm, "end": v(8226.14, 13439.03) * mm});
            skLineSegment(sketch, "E4659", {"start": v(8226.14, 13439.03) * mm, "end": v(8243.16, 13412.47) * mm});
            skLineSegment(sketch, "E4660", {"start": v(8243.16, 13412.47) * mm, "end": v(8261.6, 13385.86) * mm});
            skLineSegment(sketch, "E4661", {"start": v(8261.6, 13385.86) * mm, "end": v(8281.2, 13359.26) * mm});
            skLineSegment(sketch, "E4662", {"start": v(8281.2, 13359.26) * mm, "end": v(8301.67, 13332.75) * mm});
            skLineSegment(sketch, "E4663", {"start": v(8301.67, 13332.75) * mm, "end": v(8322.76, 13306.4) * mm});
            skLineSegment(sketch, "E4664", {"start": v(8322.76, 13306.4) * mm, "end": v(8344.19, 13280.26) * mm});
            skLineSegment(sketch, "E4665", {"start": v(8344.19, 13280.26) * mm, "end": v(8365.7, 13254.4) * mm});
            skLineSegment(sketch, "E4666", {"start": v(8365.7, 13254.4) * mm, "end": v(8387, 13228.92) * mm});
            skLineSegment(sketch, "E4667", {"start": v(8387, 13228.92) * mm, "end": v(8407.83, 13203.86) * mm});
            skLineSegment(sketch, "E4668", {"start": v(8407.83, 13203.86) * mm, "end": v(8427.93, 13179.29) * mm});
            skLineSegment(sketch, "E4669", {"start": v(8427.93, 13179.29) * mm, "end": v(8447.02, 13155.28) * mm});
            skLineSegment(sketch, "E4670", {"start": v(8447.02, 13155.28) * mm, "end": v(8464.83, 13131.91) * mm});
            skLineSegment(sketch, "E4671", {"start": v(8464.83, 13131.91) * mm, "end": v(8481.1, 13109.24) * mm});
            skLineSegment(sketch, "E4672", {"start": v(8481.1, 13109.24) * mm, "end": v(8495.54, 13087.33) * mm});
            skLineSegment(sketch, "E4673", {"start": v(8495.54, 13087.33) * mm, "end": v(8507.9, 13066.27) * mm});
            skLineSegment(sketch, "E4674", {"start": v(8507.9, 13066.27) * mm, "end": v(8517.9, 13046.1) * mm});
            skLineSegment(sketch, "E4675", {"start": v(8517.9, 13046.1) * mm, "end": v(8525.26, 13026.92) * mm});
            skLineSegment(sketch, "E4676", {"start": v(8525.26, 13026.92) * mm, "end": v(8529.72, 13008.77) * mm});
            skLineSegment(sketch, "E4677", {"start": v(8529.72, 13008.77) * mm, "end": v(8531.02, 12991.74) * mm});
            skLineSegment(sketch, "E4678", {"start": v(8531.02, 12991.74) * mm, "end": v(8528.87, 12975.89) * mm});
            skLineSegment(sketch, "E4679", {"start": v(8528.87, 12975.89) * mm, "end": v(8523.02, 12961.28) * mm});
            skLineSegment(sketch, "E4680", {"start": v(8523.02, 12961.28) * mm, "end": v(8513.18, 12948) * mm});
            skLineSegment(sketch, "E4681", {"start": v(8513.18, 12948) * mm, "end": v(8499.1, 12936.09) * mm});
            skLineSegment(sketch, "E4682", {"start": v(8499.1, 12936.09) * mm, "end": v(8480.49, 12925.63) * mm});
            skLineSegment(sketch, "E4683", {"start": v(8480.49, 12925.63) * mm, "end": v(8457.1, 12916.7) * mm});
            skLineSegment(sketch, "E4684", {"start": v(8457.1, 12916.7) * mm, "end": v(8428.63, 12909.36) * mm});
            skLineSegment(sketch, "E4685", {"start": v(8428.63, 12909.36) * mm, "end": v(8394.84, 12903.68) * mm});
            skLineSegment(sketch, "E4686", {"start": v(8394.84, 12903.68) * mm, "end": v(8355.45, 12899.73) * mm});
            skLineSegment(sketch, "E4687", {"start": v(8355.45, 12899.73) * mm, "end": v(8258.35, 12907.41) * mm});
            skLineSegment(sketch, "E4688", {"start": v(8258.35, 12907.41) * mm, "end": v(8161.86, 12916.36) * mm});
            skLineSegment(sketch, "E4689", {"start": v(8161.86, 12916.36) * mm, "end": v(8065.97, 12926.57) * mm});
            skLineSegment(sketch, "E4690", {"start": v(8065.97, 12926.57) * mm, "end": v(7970.65, 12938.06) * mm});
            skLineSegment(sketch, "E4691", {"start": v(7970.65, 12938.06) * mm, "end": v(7875.87, 12950.83) * mm});
            skLineSegment(sketch, "E4692", {"start": v(7875.87, 12950.83) * mm, "end": v(7781.6, 12964.89) * mm});
            skLineSegment(sketch, "E4693", {"start": v(7781.6, 12964.89) * mm, "end": v(7687.82, 12980.24) * mm});
            skLineSegment(sketch, "E4694", {"start": v(7687.82, 12980.24) * mm, "end": v(7594.5, 12996.9) * mm});
            skLineSegment(sketch, "E4695", {"start": v(7594.5, 12996.9) * mm, "end": v(7501.6, 13014.85) * mm});
            skLineSegment(sketch, "E4696", {"start": v(7501.6, 13014.85) * mm, "end": v(7409.13, 13034.12) * mm});
            skLineSegment(sketch, "E4697", {"start": v(7409.13, 13034.12) * mm, "end": v(7317.04, 13054.72) * mm});
            skLineSegment(sketch, "E4698", {"start": v(7317.04, 13054.72) * mm, "end": v(7225.3, 13076.64) * mm});
            skLineSegment(sketch, "E4699", {"start": v(7225.3, 13076.64) * mm, "end": v(7133.89, 13099.9) * mm});
            skLineSegment(sketch, "E4700", {"start": v(7133.89, 13099.9) * mm, "end": v(7042.78, 13124.49) * mm});
            skLineSegment(sketch, "E4701", {"start": v(7042.78, 13124.49) * mm, "end": v(6951.95, 13150.43) * mm});
            skLineSegment(sketch, "E4702", {"start": v(6951.95, 13150.43) * mm, "end": v(6861.37, 13177.73) * mm});
            skLineSegment(sketch, "E4703", {"start": v(6861.37, 13177.73) * mm, "end": v(6771.02, 13206.38) * mm});
            skLineSegment(sketch, "E4704", {"start": v(6771.02, 13206.38) * mm, "end": v(6680.86, 13236.4) * mm});
            skLineSegment(sketch, "E4705", {"start": v(6680.86, 13236.4) * mm, "end": v(6590.88, 13267.8) * mm});
            skLineSegment(sketch, "E4706", {"start": v(6590.88, 13267.8) * mm, "end": v(6501.04, 13300.57) * mm});
            skLineSegment(sketch, "E4707", {"start": v(6501.04, 13300.57) * mm, "end": v(6411.32, 13334.73) * mm});
            skLineSegment(sketch, "E4708", {"start": v(6411.32, 13334.73) * mm, "end": v(6321.7, 13370.29) * mm});
            skLineSegment(sketch, "E4709", {"start": v(6321.7, 13370.29) * mm, "end": v(6232.13, 13407.24) * mm});
            skLineSegment(sketch, "E4710", {"start": v(6232.13, 13407.24) * mm, "end": v(6142.61, 13445.6) * mm});
            skLineSegment(sketch, "E4711", {"start": v(6142.61, 8047.6) * mm, "end": v(6232.13, 8085.97) * mm});
            skLineSegment(sketch, "E4712", {"start": v(6232.13, 8085.97) * mm, "end": v(6321.7, 8122.92) * mm});
            skLineSegment(sketch, "E4713", {"start": v(6321.7, 8122.92) * mm, "end": v(6411.32, 8158.47) * mm});
            skLineSegment(sketch, "E4714", {"start": v(6411.32, 8158.47) * mm, "end": v(6501.04, 8192.64) * mm});
            skLineSegment(sketch, "E4715", {"start": v(6501.04, 8192.64) * mm, "end": v(6590.88, 8225.4) * mm});
            skLineSegment(sketch, "E4716", {"start": v(6590.88, 8225.4) * mm, "end": v(6680.86, 8256.8) * mm});
            skLineSegment(sketch, "E4717", {"start": v(6680.86, 8256.8) * mm, "end": v(6771.02, 8286.82) * mm});
            skLineSegment(sketch, "E4718", {"start": v(6771.02, 8286.82) * mm, "end": v(6861.37, 8315.48) * mm});
            skLineSegment(sketch, "E4719", {"start": v(6861.37, 8315.48) * mm, "end": v(6951.95, 8342.77) * mm});
            skLineSegment(sketch, "E4720", {"start": v(6951.95, 8342.77) * mm, "end": v(7042.78, 8368.71) * mm});
            skLineSegment(sketch, "E4721", {"start": v(7042.78, 8368.71) * mm, "end": v(7133.89, 8393.3) * mm});
            skLineSegment(sketch, "E4722", {"start": v(7133.89, 8393.3) * mm, "end": v(7225.3, 8416.56) * mm});
            skLineSegment(sketch, "E4723", {"start": v(7225.3, 8416.56) * mm, "end": v(7317.04, 8438.48) * mm});
            skLineSegment(sketch, "E4724", {"start": v(7317.04, 8438.48) * mm, "end": v(7409.13, 8459.07) * mm});
            skLineSegment(sketch, "E4725", {"start": v(7409.13, 8459.07) * mm, "end": v(7501.6, 8478.34) * mm});
            skLineSegment(sketch, "E4726", {"start": v(7501.6, 8478.34) * mm, "end": v(7594.5, 8496.3) * mm});
            skLineSegment(sketch, "E4727", {"start": v(7594.5, 8496.3) * mm, "end": v(7687.82, 8512.94) * mm});
            skLineSegment(sketch, "E4728", {"start": v(7687.82, 8512.94) * mm, "end": v(7781.6, 8528.3) * mm});
            skLineSegment(sketch, "E4729", {"start": v(7781.6, 8528.3) * mm, "end": v(7875.87, 8542.34) * mm});
            skLineSegment(sketch, "E4730", {"start": v(7875.87, 8542.34) * mm, "end": v(7970.65, 8555.1) * mm});
            skLineSegment(sketch, "E4731", {"start": v(7970.65, 8555.1) * mm, "end": v(8065.97, 8566.6) * mm});
            skLineSegment(sketch, "E4732", {"start": v(8065.97, 8566.6) * mm, "end": v(8161.86, 8576.8) * mm});
            skLineSegment(sketch, "E4733", {"start": v(8161.86, 8576.8) * mm, "end": v(8258.35, 8585.74) * mm});
            skLineSegment(sketch, "E4734", {"start": v(8258.35, 8585.74) * mm, "end": v(8355.45, 8593.41) * mm});
            skLineSegment(sketch, "E4735", {"start": v(8355.45, 8593.41) * mm, "end": v(8428.63, 8583.79) * mm});
            skLineSegment(sketch, "E4736", {"start": v(8428.63, 8583.79) * mm, "end": v(8480.49, 8567.53) * mm});
            skLineSegment(sketch, "E4737", {"start": v(8480.49, 8567.53) * mm, "end": v(8513.18, 8545.18) * mm});
            skLineSegment(sketch, "E4738", {"start": v(8513.18, 8545.18) * mm, "end": v(8528.87, 8517.29) * mm});
            skLineSegment(sketch, "E4739", {"start": v(8528.87, 8517.29) * mm, "end": v(8529.72, 8484.4) * mm});
            skLineSegment(sketch, "E4740", {"start": v(8529.72, 8484.4) * mm, "end": v(8517.9, 8447.08) * mm});
            skLineSegment(sketch, "E4741", {"start": v(8517.9, 8447.08) * mm, "end": v(8495.54, 8405.86) * mm});
            skLineSegment(sketch, "E4742", {"start": v(8495.54, 8405.86) * mm, "end": v(8464.83, 8361.29) * mm});
            skLineSegment(sketch, "E4743", {"start": v(8464.83, 8361.29) * mm, "end": v(8427.93, 8313.91) * mm});
            skLineSegment(sketch, "E4744", {"start": v(8427.93, 8313.91) * mm, "end": v(8387, 8264.28) * mm});
            skLineSegment(sketch, "E4745", {"start": v(8387, 8264.28) * mm, "end": v(8344.19, 8212.95) * mm});
            skLineSegment(sketch, "E4746", {"start": v(8344.19, 8212.95) * mm, "end": v(8301.67, 8160.45) * mm});
            skLineSegment(sketch, "E4747", {"start": v(8301.67, 8160.45) * mm, "end": v(8261.6, 8107.35) * mm});
            skLineSegment(sketch, "E4748", {"start": v(8261.6, 8107.35) * mm, "end": v(8226.14, 8054.18) * mm});
            skLineSegment(sketch, "E4749", {"start": v(8226.14, 8054.18) * mm, "end": v(8197.46, 8001.5) * mm});
            skLineSegment(sketch, "E4750", {"start": v(8197.46, 8001.5) * mm, "end": v(8177.71, 7949.84) * mm});
            skLineSegment(sketch, "E4751", {"start": v(8177.71, 7949.84) * mm, "end": v(8169.06, 7899.76) * mm});
            skLineSegment(sketch, "E4752", {"start": v(8169.06, 7899.76) * mm, "end": v(8174, 7842.58) * mm});
            skLineSegment(sketch, "E4753", {"start": v(8174, 7842.58) * mm, "end": v(8186.36, 7776.94) * mm});
            skLineSegment(sketch, "E4754", {"start": v(8186.36, 7776.94) * mm, "end": v(8202.39, 7717.73) * mm});
            skLineSegment(sketch, "E4755", {"start": v(8202.39, 7717.73) * mm, "end": v(8222, 7664.63) * mm});
            skLineSegment(sketch, "E4756", {"start": v(8222, 7664.63) * mm, "end": v(8245.1, 7617.34) * mm});
            skLineSegment(sketch, "E4757", {"start": v(8245.1, 7617.34) * mm, "end": v(8271.65, 7575.51) * mm});
            skLineSegment(sketch, "E4758", {"start": v(8271.65, 7575.51) * mm, "end": v(8301.54, 7538.85) * mm});
            skLineSegment(sketch, "E4759", {"start": v(8301.54, 7538.85) * mm, "end": v(8334.7, 7507.02) * mm});
            skLineSegment(sketch, "E4760", {"start": v(8334.7, 7507.02) * mm, "end": v(8371.05, 7479.72) * mm});
            skLineSegment(sketch, "E4761", {"start": v(8371.05, 7479.72) * mm, "end": v(8410.52, 7456.61) * mm});
            skLineSegment(sketch, "E4762", {"start": v(8410.52, 7456.61) * mm, "end": v(8453.03, 7437.39) * mm});
            skLineSegment(sketch, "E4763", {"start": v(8453.03, 7437.39) * mm, "end": v(8498.49, 7421.73) * mm});
            skLineSegment(sketch, "E4764", {"start": v(8498.49, 7421.73) * mm, "end": v(8546.83, 7409.31) * mm});
            skLineSegment(sketch, "E4765", {"start": v(8546.83, 7409.31) * mm, "end": v(8597.98, 7399.82) * mm});
            skLineSegment(sketch, "E4766", {"start": v(8597.98, 7399.82) * mm, "end": v(8651.85, 7392.94) * mm});
            skLineSegment(sketch, "E4767", {"start": v(8651.85, 7392.94) * mm, "end": v(8708.37, 7388.34) * mm});
            skLineSegment(sketch, "E4768", {"start": v(8708.37, 7388.34) * mm, "end": v(8767.46, 7385.71) * mm});
            skLineSegment(sketch, "E4769", {"start": v(8767.46, 7385.71) * mm, "end": v(8829.03, 7384.73) * mm});
            skLineSegment(sketch, "E4770", {"start": v(8829.03, 7384.73) * mm, "end": v(8891.49, 7385.14) * mm});
            skLineSegment(sketch, "E4771", {"start": v(8891.49, 7385.14) * mm, "end": v(8951.57, 7387.07) * mm});
            skLineSegment(sketch, "E4772", {"start": v(8951.57, 7387.07) * mm, "end": v(9009.12, 7390.84) * mm});
            skLineSegment(sketch, "E4773", {"start": v(9009.12, 7390.84) * mm, "end": v(9064.05, 7396.77) * mm});
            skLineSegment(sketch, "E4774", {"start": v(9064.05, 7396.77) * mm, "end": v(9116.28, 7405.18) * mm});
            skLineSegment(sketch, "E4775", {"start": v(9116.28, 7405.18) * mm, "end": v(9165.74, 7416.39) * mm});
            skLineSegment(sketch, "E4776", {"start": v(9165.74, 7416.39) * mm, "end": v(9212.35, 7430.71) * mm});
            skLineSegment(sketch, "E4777", {"start": v(9212.35, 7430.71) * mm, "end": v(9256.03, 7448.47) * mm});
            skLineSegment(sketch, "E4778", {"start": v(9256.03, 7448.47) * mm, "end": v(9296.7, 7469.99) * mm});
            skLineSegment(sketch, "E4779", {"start": v(9296.7, 7469.99) * mm, "end": v(9334.3, 7495.58) * mm});
            skLineSegment(sketch, "E4780", {"start": v(9334.3, 7495.58) * mm, "end": v(9368.72, 7525.56) * mm});
            skLineSegment(sketch, "E4781", {"start": v(9368.72, 7525.56) * mm, "end": v(9399.9, 7560.25) * mm});
            skLineSegment(sketch, "E4782", {"start": v(9399.9, 7560.25) * mm, "end": v(9427.78, 7599.97) * mm});
            skLineSegment(sketch, "E4783", {"start": v(9427.78, 7599.97) * mm, "end": v(9452.25, 7645.04) * mm});
            skLineSegment(sketch, "E4784", {"start": v(9452.25, 7645.04) * mm, "end": v(9473.26, 7695.78) * mm});
            skLineSegment(sketch, "E4785", {"start": v(9473.26, 7695.78) * mm, "end": v(9490.7, 7752.5) * mm});
            skLineSegment(sketch, "E4786", {"start": v(9490.7, 7752.5) * mm, "end": v(9504.53, 7815.53) * mm});
            skLineSegment(sketch, "E4787", {"start": v(9504.53, 7815.53) * mm, "end": v(9513.46, 7875.5) * mm});
            skLineSegment(sketch, "E4788", {"start": v(9513.46, 7875.5) * mm, "end": v(9513.98, 7899.76) * mm});
            skLineSegment(sketch, "E4789", {"start": v(9513.98, 7899.76) * mm, "end": v(9511.2, 7924.57) * mm});
            skLineSegment(sketch, "E4790", {"start": v(9511.2, 7924.57) * mm, "end": v(9505.36, 7949.84) * mm});
            skLineSegment(sketch, "E4791", {"start": v(9505.36, 7949.84) * mm, "end": v(9496.75, 7975.5) * mm});
            skLineSegment(sketch, "E4792", {"start": v(9496.75, 7975.5) * mm, "end": v(9485.64, 8001.5) * mm});
            skLineSegment(sketch, "E4793", {"start": v(9485.64, 8001.5) * mm, "end": v(9472.3, 8027.74) * mm});
            skLineSegment(sketch, "E4794", {"start": v(9472.3, 8027.74) * mm, "end": v(9456.98, 8054.18) * mm});
            skLineSegment(sketch, "E4795", {"start": v(9456.98, 8054.18) * mm, "end": v(9439.98, 8080.74) * mm});
            skLineSegment(sketch, "E4796", {"start": v(9439.98, 8080.74) * mm, "end": v(9421.55, 8107.35) * mm});
            skLineSegment(sketch, "E4797", {"start": v(9421.55, 8107.35) * mm, "end": v(9401.96, 8133.94) * mm});
            skLineSegment(sketch, "E4798", {"start": v(9401.96, 8133.94) * mm, "end": v(9381.5, 8160.45) * mm});
            skLineSegment(sketch, "E4799", {"start": v(9381.5, 8160.45) * mm, "end": v(9360.42, 8186.81) * mm});
            skLineSegment(sketch, "E4800", {"start": v(9360.42, 8186.81) * mm, "end": v(9339, 8212.95) * mm});
            skLineSegment(sketch, "E4801", {"start": v(9339, 8212.95) * mm, "end": v(9317.5, 8238.8) * mm});
            skLineSegment(sketch, "E4802", {"start": v(9317.5, 8238.8) * mm, "end": v(9296.2, 8264.28) * mm});
            skLineSegment(sketch, "E4803", {"start": v(9296.2, 8264.28) * mm, "end": v(9275.37, 8289.34) * mm});
            skLineSegment(sketch, "E4804", {"start": v(9275.37, 8289.34) * mm, "end": v(9255.28, 8313.91) * mm});
            skLineSegment(sketch, "E4805", {"start": v(9255.28, 8313.91) * mm, "end": v(9236.2, 8337.91) * mm});
            skLineSegment(sketch, "E4806", {"start": v(9236.2, 8337.91) * mm, "end": v(9218.39, 8361.29) * mm});
            skLineSegment(sketch, "E4807", {"start": v(9218.39, 8361.29) * mm, "end": v(9202.13, 8383.96) * mm});
            skLineSegment(sketch, "E4808", {"start": v(9202.13, 8383.96) * mm, "end": v(9187.69, 8405.86) * mm});
            skLineSegment(sketch, "E4809", {"start": v(9187.69, 8405.86) * mm, "end": v(9175.34, 8426.92) * mm});
            skLineSegment(sketch, "E4810", {"start": v(9175.34, 8426.92) * mm, "end": v(9165.35, 8447.08) * mm});
            skLineSegment(sketch, "E4811", {"start": v(9165.35, 8447.08) * mm, "end": v(9157.98, 8466.27) * mm});
            skLineSegment(sketch, "E4812", {"start": v(9157.98, 8466.27) * mm, "end": v(9153.52, 8484.4) * mm});
            skLineSegment(sketch, "E4813", {"start": v(9153.52, 8484.4) * mm, "end": v(9152.22, 8501.44) * mm});
            skLineSegment(sketch, "E4814", {"start": v(9152.22, 8501.44) * mm, "end": v(9154.37, 8517.29) * mm});
            skLineSegment(sketch, "E4815", {"start": v(9154.37, 8517.29) * mm, "end": v(9160.22, 8531.9) * mm});
            skLineSegment(sketch, "E4816", {"start": v(9160.22, 8531.9) * mm, "end": v(9170.05, 8545.18) * mm});
            skLineSegment(sketch, "E4817", {"start": v(9170.05, 8545.18) * mm, "end": v(9184.14, 8557.08) * mm});
            skLineSegment(sketch, "E4818", {"start": v(9184.14, 8557.08) * mm, "end": v(9202.74, 8567.53) * mm});
            skLineSegment(sketch, "E4819", {"start": v(9202.74, 8567.53) * mm, "end": v(9226.14, 8576.45) * mm});
            skLineSegment(sketch, "E4820", {"start": v(9226.14, 8576.45) * mm, "end": v(9254.6, 8583.79) * mm});
            skLineSegment(sketch, "E4821", {"start": v(9254.6, 8583.79) * mm, "end": v(9288.38, 8589.46) * mm});
            skLineSegment(sketch, "E4822", {"start": v(9288.38, 8589.46) * mm, "end": v(9327.77, 8593.41) * mm});
            skLineSegment(sketch, "E4823", {"start": v(9327.77, 8593.41) * mm, "end": v(9424.85, 8585.74) * mm});
            skLineSegment(sketch, "E4824", {"start": v(9424.85, 8585.74) * mm, "end": v(9521.32, 8576.8) * mm});
            skLineSegment(sketch, "E4825", {"start": v(9521.32, 8576.8) * mm, "end": v(9617.2, 8566.6) * mm});
            skLineSegment(sketch, "E4826", {"start": v(9617.2, 8566.6) * mm, "end": v(9712.5, 8555.1) * mm});
            skLineSegment(sketch, "E4827", {"start": v(9712.5, 8555.1) * mm, "end": v(9807.27, 8542.34) * mm});
            skLineSegment(sketch, "E4828", {"start": v(9807.27, 8542.34) * mm, "end": v(9901.53, 8528.3) * mm});
            skLineSegment(sketch, "E4829", {"start": v(9901.53, 8528.3) * mm, "end": v(9995.3, 8512.94) * mm});
            skLineSegment(sketch, "E4830", {"start": v(9995.3, 8512.94) * mm, "end": v(10088.61, 8496.3) * mm});
            skLineSegment(sketch, "E4831", {"start": v(10088.61, 8496.3) * mm, "end": v(10181.49, 8478.34) * mm});
            skLineSegment(sketch, "E4832", {"start": v(10181.49, 8478.34) * mm, "end": v(10273.96, 8459.07) * mm});
            skLineSegment(sketch, "E4833", {"start": v(10273.96, 8459.07) * mm, "end": v(10366.04, 8438.48) * mm});
            skLineSegment(sketch, "E4834", {"start": v(10366.04, 8438.48) * mm, "end": v(10457.77, 8416.56) * mm});
            skLineSegment(sketch, "E4835", {"start": v(10457.77, 8416.56) * mm, "end": v(10549.18, 8393.3) * mm});
            skLineSegment(sketch, "E4836", {"start": v(10549.18, 8393.3) * mm, "end": v(10640.28, 8368.71) * mm});
            skLineSegment(sketch, "E4837", {"start": v(10640.28, 8368.71) * mm, "end": v(10731.1, 8342.77) * mm});
            skLineSegment(sketch, "E4838", {"start": v(10731.1, 8342.77) * mm, "end": v(10767.74, 8331.73) * mm});
            skLineSegment(sketch, "E4839", {"start": v(10808.28, 5929.62) * mm, "end": v(10808.28, -188.07) * mm});
            skLineSegment(sketch, "E4840", {"start": v(10808.28, -188.07) * mm, "end": v(10808.28, -6305.75) * mm});
            skLineSegment(sketch, "E4841", {"start": v(10808.28, -6305.75) * mm, "end": v(10807.88, -6564.9) * mm});
            skLineSegment(sketch, "E4842", {"start": v(10807.88, -6564.9) * mm, "end": v(10806.7, -6819.64) * mm});
            skLineSegment(sketch, "E4843", {"start": v(10806.7, -6819.64) * mm, "end": v(10804.74, -7069.97) * mm});
            skLineSegment(sketch, "E4844", {"start": v(10804.74, -7069.97) * mm, "end": v(10801.97, -7315.87) * mm});
            skLineSegment(sketch, "E4845", {"start": v(10801.97, -7315.87) * mm, "end": v(10798.38, -7557.35) * mm});
            skLineSegment(sketch, "E4846", {"start": v(10798.38, -7557.35) * mm, "end": v(10793.98, -7794.4) * mm});
            skLineSegment(sketch, "E4847", {"start": v(10793.98, -7794.4) * mm, "end": v(10788.75, -8027.02) * mm});
            skLineSegment(sketch, "E4848", {"start": v(10788.75, -8027.02) * mm, "end": v(10782.7, -8255.2) * mm});
            skLineSegment(sketch, "E4849", {"start": v(10782.7, -8255.2) * mm, "end": v(10775.79, -8478.95) * mm});
            skLineSegment(sketch, "E4850", {"start": v(10775.79, -8478.95) * mm, "end": v(10768.03, -8698.25) * mm});
            skLineSegment(sketch, "E4851", {"start": v(10768.03, -8698.25) * mm, "end": v(10759.42, -8913.1) * mm});
            skLineSegment(sketch, "E4852", {"start": v(10759.42, -8913.1) * mm, "end": v(10749.94, -9123.5) * mm});
            skLineSegment(sketch, "E4853", {"start": v(10749.94, -9123.5) * mm, "end": v(10739.58, -9329.44) * mm});
            skLineSegment(sketch, "E4854", {"start": v(10739.58, -9329.44) * mm, "end": v(10728.34, -9530.93) * mm});
            skLineSegment(sketch, "E4855", {"start": v(10728.34, -9530.93) * mm, "end": v(10716.2, -9727.94) * mm});
            skLineSegment(sketch, "E4856", {"start": v(10716.2, -9727.94) * mm, "end": v(10703.18, -9920.5) * mm});
            skLineSegment(sketch, "E4857", {"start": v(10703.18, -9920.5) * mm, "end": v(10689.24, -10108.57) * mm});
            skLineSegment(sketch, "E4858", {"start": v(10689.24, -10108.57) * mm, "end": v(10674.39, -10292.17) * mm});
            skLineSegment(sketch, "E4859", {"start": v(10674.39, -10292.17) * mm, "end": v(10658.61, -10471.29) * mm});
            skLineSegment(sketch, "E4860", {"start": v(10658.61, -10471.29) * mm, "end": v(10641.9, -10645.92) * mm});
            skLineSegment(sketch, "E4861", {"start": v(10641.9, -10645.92) * mm, "end": v(10624.25, -10816.07) * mm});
            skLineSegment(sketch, "E4862", {"start": v(10624.25, -10816.07) * mm, "end": v(10605.66, -10981.72) * mm});
            skLineSegment(sketch, "E4863", {"start": v(10605.66, -10981.72) * mm, "end": v(10586.1, -11142.87) * mm});
            skLineSegment(sketch, "E4864", {"start": v(10586.1, -11142.87) * mm, "end": v(10565.59, -11299.53) * mm});
            skLineSegment(sketch, "E4865", {"start": v(10565.59, -11299.53) * mm, "end": v(10544.1, -11451.68) * mm});
            skLineSegment(sketch, "E4866", {"start": v(10544.1, -11451.68) * mm, "end": v(10521.63, -11599.32) * mm});
            skLineSegment(sketch, "E4867", {"start": v(10521.63, -11599.32) * mm, "end": v(10498.17, -11742.45) * mm});
            skLineSegment(sketch, "E4868", {"start": v(10498.17, -11742.45) * mm, "end": v(10473.71, -11881.06) * mm});
            skLineSegment(sketch, "E4869", {"start": v(10473.71, -11881.06) * mm, "end": v(10448.25, -12015.15) * mm});
            skLineSegment(sketch, "E4870", {"start": v(10448.25, -12015.15) * mm, "end": v(10421.78, -12144.7) * mm});
            skLineSegment(sketch, "E4871", {"start": v(10421.78, -12144.7) * mm, "end": v(10394.29, -12269.74) * mm});
            skLineSegment(sketch, "E4872", {"start": v(10394.29, -12269.74) * mm, "end": v(10380.16, -12330.56) * mm});
            skLineSegment(sketch, "E4873", {"start": v(10380.16, -12330.56) * mm, "end": v(10365.77, -12390.24) * mm});
            skLineSegment(sketch, "E4874", {"start": v(10365.77, -12390.24) * mm, "end": v(10335.82, -12508.28) * mm});
            skLineSegment(sketch, "E4875", {"start": v(10335.82, -12508.28) * mm, "end": v(10304.05, -12625.93) * mm});
            skLineSegment(sketch, "E4876", {"start": v(10304.05, -12625.93) * mm, "end": v(10270.46, -12743.17) * mm});
            skLineSegment(sketch, "E4877", {"start": v(10270.46, -12743.17) * mm, "end": v(10235.04, -12860.02) * mm});
            skLineSegment(sketch, "E4878", {"start": v(10235.04, -12860.02) * mm, "end": v(10197.8, -12976.46) * mm});
            skLineSegment(sketch, "E4879", {"start": v(10197.8, -12976.46) * mm, "end": v(10158.71, -13092.5) * mm});
            skLineSegment(sketch, "E4880", {"start": v(10158.71, -13092.5) * mm, "end": v(10117.8, -13208.11) * mm});
            skLineSegment(sketch, "E4881", {"start": v(10117.8, -13208.11) * mm, "end": v(10075.02, -13323.32) * mm});
            skLineSegment(sketch, "E4882", {"start": v(10075.02, -13323.32) * mm, "end": v(10030.41, -13438.1) * mm});
            skLineSegment(sketch, "E4883", {"start": v(10030.41, -13438.1) * mm, "end": v(9983.95, -13552.45) * mm});
            skLineSegment(sketch, "E4884", {"start": v(9983.95, -13552.45) * mm, "end": v(9935.63, -13666.38) * mm});
            skLineSegment(sketch, "E4885", {"start": v(9935.63, -13666.38) * mm, "end": v(9885.45, -13779.87) * mm});
            skLineSegment(sketch, "E4886", {"start": v(9885.45, -13779.87) * mm, "end": v(9833.4, -13892.92) * mm});
            skLineSegment(sketch, "E4887", {"start": v(9833.4, -13892.92) * mm, "end": v(9779.5, -14005.54) * mm});
            skLineSegment(sketch, "E4888", {"start": v(9779.5, -14005.54) * mm, "end": v(9723.7, -14117.7) * mm});
            skLineSegment(sketch, "E4889", {"start": v(9723.7, -14117.7) * mm, "end": v(9666.05, -14229.42) * mm});
            skLineSegment(sketch, "E4890", {"start": v(9666.05, -14229.42) * mm, "end": v(9606.51, -14340.68) * mm});
            skLineSegment(sketch, "E4891", {"start": v(9606.51, -14340.68) * mm, "end": v(9545.09, -14451.5) * mm});
            skLineSegment(sketch, "E4892", {"start": v(9545.09, -14451.5) * mm, "end": v(9481.78, -14561.84) * mm});
            skLineSegment(sketch, "E4893", {"start": v(9481.78, -14561.84) * mm, "end": v(9416.58, -14671.71) * mm});
            skLineSegment(sketch, "E4894", {"start": v(9416.58, -14671.71) * mm, "end": v(9349.48, -14781.12) * mm});
            skLineSegment(sketch, "E4895", {"start": v(9349.48, -14781.12) * mm, "end": v(9280.48, -14890.06) * mm});
            skLineSegment(sketch, "E4896", {"start": v(9280.48, -14890.06) * mm, "end": v(9209.58, -14998.51) * mm});
            skLineSegment(sketch, "E4897", {"start": v(9209.58, -14998.51) * mm, "end": v(9136.77, -15106.49) * mm});
            skLineSegment(sketch, "E4898", {"start": v(9136.77, -15106.49) * mm, "end": v(9062.05, -15213.97) * mm});
            skLineSegment(sketch, "E4899", {"start": v(9062.05, -15213.97) * mm, "end": v(8985.4, -15320.97) * mm});
            skLineSegment(sketch, "E4900", {"start": v(8985.4, -15320.97) * mm, "end": v(8906.85, -15427.48) * mm});
            skLineSegment(sketch, "E4901", {"start": v(8906.85, -15427.48) * mm, "end": v(8826.36, -15533.48) * mm});
            skLineSegment(sketch, "E4902", {"start": v(8826.36, -15533.48) * mm, "end": v(8743.95, -15638.98) * mm});
            skLineSegment(sketch, "E4903", {"start": v(8743.95, -15638.98) * mm, "end": v(8659.6, -15743.98) * mm});
            skLineSegment(sketch, "E4904", {"start": v(8659.6, -15743.98) * mm, "end": v(8573.33, -15848.47) * mm});
            skLineSegment(sketch, "E4905", {"start": v(8573.33, -15848.47) * mm, "end": v(8485.1, -15952.44) * mm});
            skLineSegment(sketch, "E4906", {"start": v(8485.1, -15952.44) * mm, "end": v(8440.36, -16004.05) * mm});
            skLineSegment(sketch, "E4907", {"start": v(8440.36, -16004.05) * mm, "end": v(8395.33, -16055.18) * mm});
            skLineSegment(sketch, "E4908", {"start": v(8395.33, -16055.18) * mm, "end": v(8350, -16105.83) * mm});
            skLineSegment(sketch, "E4909", {"start": v(8350, -16105.83) * mm, "end": v(8304.38, -16155.99) * mm});
            skLineSegment(sketch, "E4910", {"start": v(8304.38, -16155.99) * mm, "end": v(8258.48, -16205.67) * mm});
            skLineSegment(sketch, "E4911", {"start": v(8258.48, -16205.67) * mm, "end": v(8212.27, -16254.86) * mm});
            skLineSegment(sketch, "E4912", {"start": v(8212.27, -16254.86) * mm, "end": v(8165.78, -16303.58) * mm});
            skLineSegment(sketch, "E4913", {"start": v(8165.78, -16303.58) * mm, "end": v(8119, -16351.82) * mm});
            skLineSegment(sketch, "E4914", {"start": v(8119, -16351.82) * mm, "end": v(8071.92, -16399.58) * mm});
            skLineSegment(sketch, "E4915", {"start": v(8071.92, -16399.58) * mm, "end": v(8024.55, -16446.86) * mm});
            skLineSegment(sketch, "E4916", {"start": v(8024.55, -16446.86) * mm, "end": v(7976.9, -16493.67) * mm});
            skLineSegment(sketch, "E4917", {"start": v(7976.9, -16493.67) * mm, "end": v(7928.94, -16540) * mm});
            skLineSegment(sketch, "E4918", {"start": v(7928.94, -16540) * mm, "end": v(7880.7, -16585.86) * mm});
            skLineSegment(sketch, "E4919", {"start": v(7880.7, -16585.86) * mm, "end": v(7832.17, -16631.25) * mm});
            skLineSegment(sketch, "E4920", {"start": v(7832.17, -16631.25) * mm, "end": v(7783.34, -16676.16) * mm});
            skLineSegment(sketch, "E4921", {"start": v(7783.34, -16676.16) * mm, "end": v(7734.22, -16720.6) * mm});
            skLineSegment(sketch, "E4922", {"start": v(7734.22, -16720.6) * mm, "end": v(7684.81, -16764.58) * mm});
            skLineSegment(sketch, "E4923", {"start": v(7684.81, -16764.58) * mm, "end": v(7635.11, -16808.08) * mm});
            skLineSegment(sketch, "E4924", {"start": v(7635.11, -16808.08) * mm, "end": v(7585.12, -16851.12) * mm});
            skLineSegment(sketch, "E4925", {"start": v(7585.12, -16851.12) * mm, "end": v(7534.83, -16893.69) * mm});
            skLineSegment(sketch, "E4926", {"start": v(7534.83, -16893.69) * mm, "end": v(7484.26, -16935.8) * mm});
            skLineSegment(sketch, "E4927", {"start": v(7484.26, -16935.8) * mm, "end": v(7433.4, -16977.43) * mm});
            skLineSegment(sketch, "E4928", {"start": v(7433.4, -16977.43) * mm, "end": v(7382.23, -17018.6) * mm});
            skLineSegment(sketch, "E4929", {"start": v(7382.23, -17018.6) * mm, "end": v(7330.78, -17059.32) * mm});
            skLineSegment(sketch, "E4930", {"start": v(7330.78, -17059.32) * mm, "end": v(7279.04, -17099.57) * mm});
            skLineSegment(sketch, "E4931", {"start": v(7279.04, -17099.57) * mm, "end": v(7227, -17139.35) * mm});
            skLineSegment(sketch, "E4932", {"start": v(7227, -17139.35) * mm, "end": v(7174.67, -17178.68) * mm});
            skLineSegment(sketch, "E4933", {"start": v(7174.67, -17178.68) * mm, "end": v(7122.06, -17217.55) * mm});
            skLineSegment(sketch, "E4934", {"start": v(7122.06, -17217.55) * mm, "end": v(7069.15, -17255.97) * mm});
            skLineSegment(sketch, "E4935", {"start": v(7069.15, -17255.97) * mm, "end": v(7015.95, -17293.92) * mm});
            skLineSegment(sketch, "E4936", {"start": v(7015.95, -17293.92) * mm, "end": v(6962.45, -17331.42) * mm});
            skLineSegment(sketch, "E4937", {"start": v(6962.45, -17331.42) * mm, "end": v(6908.67, -17368.47) * mm});
            skLineSegment(sketch, "E4938", {"start": v(6908.67, -17368.47) * mm, "end": v(6854.6, -17405.06) * mm});
            skLineSegment(sketch, "E4939", {"start": v(6854.6, -17405.06) * mm, "end": v(6800.22, -17441.2) * mm});
            skLineSegment(sketch, "E4940", {"start": v(6800.22, -17441.2) * mm, "end": v(6745.56, -17476.88) * mm});
            skLineSegment(sketch, "E4941", {"start": v(6745.56, -17476.88) * mm, "end": v(6690.61, -17512.12) * mm});
            skLineSegment(sketch, "E4942", {"start": v(6690.61, -17512.12) * mm, "end": v(6635.37, -17546.9) * mm});
            skLineSegment(sketch, "E4943", {"start": v(6635.37, -17546.9) * mm, "end": v(6579.83, -17581.24) * mm});
            skLineSegment(sketch, "E4944", {"start": v(6579.83, -17581.24) * mm, "end": v(6524, -17615.13) * mm});
            skLineSegment(sketch, "E4945", {"start": v(6524, -17615.13) * mm, "end": v(6467.89, -17648.58) * mm});
            skLineSegment(sketch, "E4946", {"start": v(6467.89, -17648.58) * mm, "end": v(6411.48, -17681.58) * mm});
            skLineSegment(sketch, "E4947", {"start": v(6411.48, -17681.58) * mm, "end": v(6354.78, -17714.13) * mm});
            skLineSegment(sketch, "E4948", {"start": v(6354.78, -17714.13) * mm, "end": v(6297.78, -17746.24) * mm});
            skLineSegment(sketch, "E4949", {"start": v(6297.78, -17746.24) * mm, "end": v(6240.5, -17777.9) * mm});
            skLineSegment(sketch, "E4950", {"start": v(6240.5, -17777.9) * mm, "end": v(6182.92, -17809.13) * mm});
            skLineSegment(sketch, "E4951", {"start": v(6182.92, -17809.13) * mm, "end": v(6125.05, -17839.92) * mm});
            skLineSegment(sketch, "E4952", {"start": v(6125.05, -17839.92) * mm, "end": v(6066.9, -17870.26) * mm});
            skLineSegment(sketch, "E4953", {"start": v(6066.9, -17870.26) * mm, "end": v(6008.44, -17900.17) * mm});
            skLineSegment(sketch, "E4954", {"start": v(6008.44, -17900.17) * mm, "end": v(5949.7, -17929.64) * mm});
            skLineSegment(sketch, "E4955", {"start": v(5949.7, -17929.64) * mm, "end": v(5890.66, -17958.67) * mm});
            skLineSegment(sketch, "E4956", {"start": v(5890.66, -17958.67) * mm, "end": v(5831.33, -17987.27) * mm});
            skLineSegment(sketch, "E4957", {"start": v(5831.33, -17987.27) * mm, "end": v(5771.71, -18015.43) * mm});
            skLineSegment(sketch, "E4958", {"start": v(5771.71, -18015.43) * mm, "end": v(5711.8, -18043.16) * mm});
            skLineSegment(sketch, "E4959", {"start": v(5711.8, -18043.16) * mm, "end": v(5651.6, -18070.46) * mm});
            skLineSegment(sketch, "E4960", {"start": v(5651.6, -18070.46) * mm, "end": v(5591.1, -18097.32) * mm});
            skLineSegment(sketch, "E4961", {"start": v(5591.1, -18097.32) * mm, "end": v(5530.32, -18123.76) * mm});
            skLineSegment(sketch, "E4962", {"start": v(5530.32, -18123.76) * mm, "end": v(5407.88, -18175.34) * mm});
            skLineSegment(sketch, "E4963", {"start": v(5407.88, -18175.34) * mm, "end": v(5284.26, -18225.21) * mm});
            skLineSegment(sketch, "E4964", {"start": v(5284.26, -18225.21) * mm, "end": v(5159.48, -18273.38) * mm});
            skLineSegment(sketch, "E4965", {"start": v(5159.48, -18273.38) * mm, "end": v(5033.54, -18319.86) * mm});
            skLineSegment(sketch, "E4966", {"start": v(5033.54, -18319.86) * mm, "end": v(4906.55, -18364.78) * mm});
            skLineSegment(sketch, "E4967", {"start": v(4906.55, -18364.78) * mm, "end": v(4778.66, -18408.28) * mm});
            skLineSegment(sketch, "E4968", {"start": v(4778.66, -18408.28) * mm, "end": v(4649.86, -18450.34) * mm});
            skLineSegment(sketch, "E4969", {"start": v(4649.86, -18450.34) * mm, "end": v(4520.16, -18490.99) * mm});
            skLineSegment(sketch, "E4970", {"start": v(4520.16, -18490.99) * mm, "end": v(4389.54, -18530.2) * mm});
            skLineSegment(sketch, "E4971", {"start": v(4389.54, -18530.2) * mm, "end": v(4258.02, -18568) * mm});
            skLineSegment(sketch, "E4972", {"start": v(4258.02, -18568) * mm, "end": v(4125.6, -18604.36) * mm});
            skLineSegment(sketch, "E4973", {"start": v(4125.6, -18604.36) * mm, "end": v(3992.26, -18639.3) * mm});
            skLineSegment(sketch, "E4974", {"start": v(3992.26, -18639.3) * mm, "end": v(3858.01, -18672.8) * mm});
            skLineSegment(sketch, "E4975", {"start": v(3858.01, -18672.8) * mm, "end": v(3722.86, -18704.9) * mm});
            skLineSegment(sketch, "E4976", {"start": v(3722.86, -18704.9) * mm, "end": v(3586.8, -18735.56) * mm});
            skLineSegment(sketch, "E4977", {"start": v(3586.8, -18735.56) * mm, "end": v(3449.84, -18764.79) * mm});
            skLineSegment(sketch, "E4978", {"start": v(3449.84, -18764.79) * mm, "end": v(3311.97, -18792.6) * mm});
            skLineSegment(sketch, "E4979", {"start": v(3311.97, -18792.6) * mm, "end": v(3173.19, -18818.98) * mm});
            skLineSegment(sketch, "E4980", {"start": v(3173.19, -18818.98) * mm, "end": v(3033.5, -18843.94) * mm});
            skLineSegment(sketch, "E4981", {"start": v(3033.5, -18843.94) * mm, "end": v(2892.9, -18867.47) * mm});
            skLineSegment(sketch, "E4982", {"start": v(2892.9, -18867.47) * mm, "end": v(2751.4, -18889.57) * mm});
            skLineSegment(sketch, "E4983", {"start": v(2751.4, -18889.57) * mm, "end": v(2608.99, -18910.25) * mm});
            skLineSegment(sketch, "E4984", {"start": v(2608.99, -18910.25) * mm, "end": v(2465.67, -18929.5) * mm});
            skLineSegment(sketch, "E4985", {"start": v(2465.67, -18929.5) * mm, "end": v(2321.44, -18947.32) * mm});
            skLineSegment(sketch, "E4986", {"start": v(2321.44, -18947.32) * mm, "end": v(2176.3, -18963.72) * mm});
            skLineSegment(sketch, "E4987", {"start": v(2176.3, -18963.72) * mm, "end": v(2030.27, -18978.7) * mm});
            skLineSegment(sketch, "E4988", {"start": v(2030.27, -18978.7) * mm, "end": v(1883.32, -18992.24) * mm});
            skLineSegment(sketch, "E4989", {"start": v(1883.32, -18992.24) * mm, "end": v(1735.46, -19004.37) * mm});
            skLineSegment(sketch, "E4990", {"start": v(1735.46, -19004.37) * mm, "end": v(1586.7, -19015.06) * mm});
            skLineSegment(sketch, "E4991", {"start": v(1586.7, -19015.06) * mm, "end": v(1437.03, -19024.33) * mm});
            skLineSegment(sketch, "E4992", {"start": v(1437.03, -19024.33) * mm, "end": v(1286.45, -19032.17) * mm});
            skLineSegment(sketch, "E4993", {"start": v(1286.45, -19032.17) * mm, "end": v(1134.97, -19038.6) * mm});
            skLineSegment(sketch, "E4994", {"start": v(1134.97, -19038.6) * mm, "end": v(982.57, -19043.58) * mm});
            skLineSegment(sketch, "E4995", {"start": v(982.57, -19043.58) * mm, "end": v(829.27, -19047.15) * mm});
            skLineSegment(sketch, "E4996", {"start": v(829.27, -19047.15) * mm, "end": v(675.06, -19049.29) * mm});
            skLineSegment(sketch, "E4997", {"start": v(675.06, -19049.29) * mm, "end": v(519.95, -19050) * mm});
            skLineSegment(sketch, "E4998", {"start": v(519.95, -19050) * mm, "end": v(315.63, -19049.22) * mm});
            skLineSegment(sketch, "E4999", {"start": v(315.63, -19049.22) * mm, "end": v(113.4, -19046.9) * mm});
            skLineSegment(sketch, "E5000", {"start": v(113.4, -19046.9) * mm, "end": v(-86.74, -19043.04) * mm});
            skLineSegment(sketch, "E5001", {"start": v(-86.74, -19043.04) * mm, "end": v(-284.78, -19037.64) * mm});
            skLineSegment(sketch, "E5002", {"start": v(-284.78, -19037.64) * mm, "end": v(-480.71, -19030.72) * mm});
            skLineSegment(sketch, "E5003", {"start": v(-480.71, -19030.72) * mm, "end": v(-674.53, -19022.29) * mm});
            skLineSegment(sketch, "E5004", {"start": v(-674.53, -19022.29) * mm, "end": v(-866.23, -19012.35) * mm});
            skLineSegment(sketch, "E5005", {"start": v(-866.23, -19012.35) * mm, "end": v(-1055.8, -19000.9) * mm});
            skLineSegment(sketch, "E5006", {"start": v(-1055.8, -19000.9) * mm, "end": v(-1243.23, -18987.98) * mm});
            skLineSegment(sketch, "E5007", {"start": v(-1243.23, -18987.98) * mm, "end": v(-1428.5, -18973.57) * mm});
            skLineSegment(sketch, "E5008", {"start": v(-1428.5, -18973.57) * mm, "end": v(-1611.63, -18957.68) * mm});
            skLineSegment(sketch, "E5009", {"start": v(-1611.63, -18957.68) * mm, "end": v(-1792.6, -18940.32) * mm});
            skLineSegment(sketch, "E5010", {"start": v(-1792.6, -18940.32) * mm, "end": v(-1971.38, -18921.51) * mm});
            skLineSegment(sketch, "E5011", {"start": v(-1971.38, -18921.51) * mm, "end": v(-2148, -18901.25) * mm});
            skLineSegment(sketch, "E5012", {"start": v(-2148, -18901.25) * mm, "end": v(-2322.42, -18879.54) * mm});
            skLineSegment(sketch, "E5013", {"start": v(-2322.42, -18879.54) * mm, "end": v(-2494.64, -18856.4) * mm});
            skLineSegment(sketch, "E5014", {"start": v(-2494.64, -18856.4) * mm, "end": v(-2664.67, -18831.84) * mm});
            skLineSegment(sketch, "E5015", {"start": v(-2664.67, -18831.84) * mm, "end": v(-2832.48, -18805.85) * mm});
            skLineSegment(sketch, "E5016", {"start": v(-2832.48, -18805.85) * mm, "end": v(-2998.07, -18778.46) * mm});
            skLineSegment(sketch, "E5017", {"start": v(-2998.07, -18778.46) * mm, "end": v(-3161.43, -18749.66) * mm});
            skLineSegment(sketch, "E5018", {"start": v(-3161.43, -18749.66) * mm, "end": v(-3322.56, -18719.48) * mm});
            skLineSegment(sketch, "E5019", {"start": v(-3322.56, -18719.48) * mm, "end": v(-3481.44, -18687.9) * mm});
            skLineSegment(sketch, "E5020", {"start": v(-3481.44, -18687.9) * mm, "end": v(-3638.07, -18654.95) * mm});
            skLineSegment(sketch, "E5021", {"start": v(-3638.07, -18654.95) * mm, "end": v(-3792.44, -18620.63) * mm});
            skLineSegment(sketch, "E5022", {"start": v(-3792.44, -18620.63) * mm, "end": v(-3944.54, -18584.95) * mm});
            skLineSegment(sketch, "E5023", {"start": v(-3944.54, -18584.95) * mm, "end": v(-4094.36, -18547.91) * mm});
            skLineSegment(sketch, "E5024", {"start": v(-4094.36, -18547.91) * mm, "end": v(-4241.9, -18509.53) * mm});
            skLineSegment(sketch, "E5025", {"start": v(-4241.9, -18509.53) * mm, "end": v(-4387.15, -18469.81) * mm});
            skLineSegment(sketch, "E5026", {"start": v(-4387.15, -18469.81) * mm, "end": v(-4530.09, -18428.77) * mm});
            skLineSegment(sketch, "E5027", {"start": v(-4530.09, -18428.77) * mm, "end": v(-4670.72, -18386.4) * mm});
            skLineSegment(sketch, "E5028", {"start": v(-4670.72, -18386.4) * mm, "end": v(-4809.04, -18342.72) * mm});
            skLineSegment(sketch, "E5029", {"start": v(-4809.04, -18342.72) * mm, "end": v(-4945.03, -18297.74) * mm});
            skLineSegment(sketch, "E5030", {"start": v(-4945.03, -18297.74) * mm, "end": v(-5013.26, -18273.67) * mm});
            skLineSegment(sketch, "E5031", {"start": v(-5013.26, -18273.67) * mm, "end": v(-5081.03, -18249.19) * mm});
            skLineSegment(sketch, "E5032", {"start": v(-5081.03, -18249.19) * mm, "end": v(-5148.35, -18224.28) * mm});
            skLineSegment(sketch, "E5033", {"start": v(-5148.35, -18224.28) * mm, "end": v(-5215.21, -18198.95) * mm});
            skLineSegment(sketch, "E5034", {"start": v(-5215.21, -18198.95) * mm, "end": v(-5281.63, -18173.2) * mm});
            skLineSegment(sketch, "E5035", {"start": v(-5281.63, -18173.2) * mm, "end": v(-5347.59, -18147.05) * mm});
            skLineSegment(sketch, "E5036", {"start": v(-5347.59, -18147.05) * mm, "end": v(-5413.1, -18120.46) * mm});
            skLineSegment(sketch, "E5037", {"start": v(-5413.1, -18120.46) * mm, "end": v(-5478.16, -18093.46) * mm});
            skLineSegment(sketch, "E5038", {"start": v(-5478.16, -18093.46) * mm, "end": v(-5542.77, -18066.05) * mm});
            skLineSegment(sketch, "E5039", {"start": v(-5542.77, -18066.05) * mm, "end": v(-5606.94, -18038.21) * mm});
            skLineSegment(sketch, "E5040", {"start": v(-5606.94, -18038.21) * mm, "end": v(-5670.65, -18009.96) * mm});
            skLineSegment(sketch, "E5041", {"start": v(-5670.65, -18009.96) * mm, "end": v(-5733.92, -17981.3) * mm});
            skLineSegment(sketch, "E5042", {"start": v(-5733.92, -17981.3) * mm, "end": v(-5796.74, -17952.22) * mm});
            skLineSegment(sketch, "E5043", {"start": v(-5796.74, -17952.22) * mm, "end": v(-5859.1, -17922.72) * mm});
            skLineSegment(sketch, "E5044", {"start": v(-5859.1, -17922.72) * mm, "end": v(-5921.03, -17892.81) * mm});
            skLineSegment(sketch, "E5045", {"start": v(-5921.03, -17892.81) * mm, "end": v(-5982.51, -17862.49) * mm});
            skLineSegment(sketch, "E5046", {"start": v(-5982.51, -17862.49) * mm, "end": v(-6043.54, -17831.75) * mm});
            skLineSegment(sketch, "E5047", {"start": v(-6043.54, -17831.75) * mm, "end": v(-6104.13, -17800.6) * mm});
            skLineSegment(sketch, "E5048", {"start": v(-6104.13, -17800.6) * mm, "end": v(-6164.27, -17769.04) * mm});
            skLineSegment(sketch, "E5049", {"start": v(-6164.27, -17769.04) * mm, "end": v(-6223.97, -17737.06) * mm});
            skLineSegment(sketch, "E5050", {"start": v(-6223.97, -17737.06) * mm, "end": v(-6283.23, -17704.68) * mm});
            skLineSegment(sketch, "E5051", {"start": v(-6283.23, -17704.68) * mm, "end": v(-6342.04, -17671.88) * mm});
            skLineSegment(sketch, "E5052", {"start": v(-6342.04, -17671.88) * mm, "end": v(-6400.4, -17638.68) * mm});
            skLineSegment(sketch, "E5053", {"start": v(-6400.4, -17638.68) * mm, "end": v(-6458.34, -17605.06) * mm});
            skLineSegment(sketch, "E5054", {"start": v(-6458.34, -17605.06) * mm, "end": v(-6515.82, -17571.04) * mm});
            skLineSegment(sketch, "E5055", {"start": v(-6515.82, -17571.04) * mm, "end": v(-6572.87, -17536.6) * mm});
            skLineSegment(sketch, "E5056", {"start": v(-6572.87, -17536.6) * mm, "end": v(-6629.47, -17501.76) * mm});
            skLineSegment(sketch, "E5057", {"start": v(-6629.47, -17501.76) * mm, "end": v(-6685.64, -17466.51) * mm});
            skLineSegment(sketch, "E5058", {"start": v(-6685.64, -17466.51) * mm, "end": v(-6741.36, -17430.86) * mm});
            skLineSegment(sketch, "E5059", {"start": v(-6741.36, -17430.86) * mm, "end": v(-6796.65, -17394.8) * mm});
            skLineSegment(sketch, "E5060", {"start": v(-6796.65, -17394.8) * mm, "end": v(-6851.5, -17358.33) * mm});
            skLineSegment(sketch, "E5061", {"start": v(-6851.5, -17358.33) * mm, "end": v(-6905.9, -17321.45) * mm});
            skLineSegment(sketch, "E5062", {"start": v(-6905.9, -17321.45) * mm, "end": v(-6959.87, -17284.17) * mm});
            skLineSegment(sketch, "E5063", {"start": v(-6959.87, -17284.17) * mm, "end": v(-7013.4, -17246.49) * mm});
            skLineSegment(sketch, "E5064", {"start": v(-7013.4, -17246.49) * mm, "end": v(-7066.5, -17208.4) * mm});
            skLineSegment(sketch, "E5065", {"start": v(-7066.5, -17208.4) * mm, "end": v(-7119.17, -17169.9) * mm});
            skLineSegment(sketch, "E5066", {"start": v(-7119.17, -17169.9) * mm, "end": v(-7171.4, -17131) * mm});
            skLineSegment(sketch, "E5067", {"start": v(-7171.4, -17131) * mm, "end": v(-7223.18, -17091.71) * mm});
            skLineSegment(sketch, "E5068", {"start": v(-7223.18, -17091.71) * mm, "end": v(-7274.54, -17052.01) * mm});
            skLineSegment(sketch, "E5069", {"start": v(-7274.54, -17052.01) * mm, "end": v(-7325.46, -17011.91) * mm});
            skLineSegment(sketch, "E5070", {"start": v(-7325.46, -17011.91) * mm, "end": v(-7375.95, -16971.4) * mm});
            skLineSegment(sketch, "E5071", {"start": v(-7375.95, -16971.4) * mm, "end": v(-7426, -16930.5) * mm});
            skLineSegment(sketch, "E5072", {"start": v(-7426, -16930.5) * mm, "end": v(-7475.63, -16889.2) * mm});
            skLineSegment(sketch, "E5073", {"start": v(-7475.63, -16889.2) * mm, "end": v(-7524.82, -16847.5) * mm});
            skLineSegment(sketch, "E5074", {"start": v(-7524.82, -16847.5) * mm, "end": v(-7573.59, -16805.4) * mm});
            skLineSegment(sketch, "E5075", {"start": v(-7573.59, -16805.4) * mm, "end": v(-7621.91, -16762.9) * mm});
            skLineSegment(sketch, "E5076", {"start": v(-7621.91, -16762.9) * mm, "end": v(-7669.81, -16720) * mm});
            skLineSegment(sketch, "E5077", {"start": v(-7669.81, -16720) * mm, "end": v(-7717.28, -16676.7) * mm});
            skLineSegment(sketch, "E5078", {"start": v(-7717.28, -16676.7) * mm, "end": v(-7764.32, -16633) * mm});
            skLineSegment(sketch, "E5079", {"start": v(-7764.32, -16633) * mm, "end": v(-7810.93, -16588.92) * mm});
            skLineSegment(sketch, "E5080", {"start": v(-7810.93, -16588.92) * mm, "end": v(-7857.12, -16544.43) * mm});
            skLineSegment(sketch, "E5081", {"start": v(-7857.12, -16544.43) * mm, "end": v(-7902.87, -16499.55) * mm});
            skLineSegment(sketch, "E5082", {"start": v(-7902.87, -16499.55) * mm, "end": v(-7948.2, -16454.28) * mm});
            skLineSegment(sketch, "E5083", {"start": v(-7948.2, -16454.28) * mm, "end": v(-7993.1, -16408.6) * mm});
            skLineSegment(sketch, "E5084", {"start": v(-7993.1, -16408.6) * mm, "end": v(-8037.57, -16362.54) * mm});
            skLineSegment(sketch, "E5085", {"start": v(-8037.57, -16362.54) * mm, "end": v(-8081.62, -16316.08) * mm});
            skLineSegment(sketch, "E5086", {"start": v(-8081.62, -16316.08) * mm, "end": v(-8125.24, -16269.23) * mm});
            skLineSegment(sketch, "E5087", {"start": v(-8125.24, -16269.23) * mm, "end": v(-8168.44, -16221.99) * mm});
            skLineSegment(sketch, "E5088", {"start": v(-8168.44, -16221.99) * mm, "end": v(-8211.21, -16174.35) * mm});
            skLineSegment(sketch, "E5089", {"start": v(-8211.21, -16174.35) * mm, "end": v(-8253.56, -16126.33) * mm});
            skLineSegment(sketch, "E5090", {"start": v(-8253.56, -16126.33) * mm, "end": v(-8295.49, -16077.9) * mm});
            skLineSegment(sketch, "E5091", {"start": v(-8295.49, -16077.9) * mm, "end": v(-8336.99, -16029.1) * mm});
            skLineSegment(sketch, "E5092", {"start": v(-8336.99, -16029.1) * mm, "end": v(-8378.07, -15979.9) * mm});
            skLineSegment(sketch, "E5093", {"start": v(-8378.07, -15979.9) * mm, "end": v(-8418.73, -15930.31) * mm});
            skLineSegment(sketch, "E5094", {"start": v(-8418.73, -15930.31) * mm, "end": v(-8498.91, -15828.55) * mm});
            skLineSegment(sketch, "E5095", {"start": v(-8498.91, -15828.55) * mm, "end": v(-8577.66, -15726.52) * mm});
            skLineSegment(sketch, "E5096", {"start": v(-8577.66, -15726.52) * mm, "end": v(-8654.98, -15624.23) * mm});
            skLineSegment(sketch, "E5097", {"start": v(-8654.98, -15624.23) * mm, "end": v(-8730.86, -15521.68) * mm});
            skLineSegment(sketch, "E5098", {"start": v(-8730.86, -15521.68) * mm, "end": v(-8805.3, -15418.88) * mm});
            skLineSegment(sketch, "E5099", {"start": v(-8805.3, -15418.88) * mm, "end": v(-8878.3, -15315.81) * mm});
            skLineSegment(sketch, "E5100", {"start": v(-8878.3, -15315.81) * mm, "end": v(-8949.83, -15212.5) * mm});
            skLineSegment(sketch, "E5101", {"start": v(-8949.83, -15212.5) * mm, "end": v(-9019.92, -15108.9) * mm});
            skLineSegment(sketch, "E5102", {"start": v(-9019.92, -15108.9) * mm, "end": v(-9088.55, -15005.06) * mm});
            skLineSegment(sketch, "E5103", {"start": v(-9088.55, -15005.06) * mm, "end": v(-9155.71, -14900.96) * mm});
            skLineSegment(sketch, "E5104", {"start": v(-9155.71, -14900.96) * mm, "end": v(-9221.41, -14796.6) * mm});
            skLineSegment(sketch, "E5105", {"start": v(-9221.41, -14796.6) * mm, "end": v(-9285.64, -14691.98) * mm});
            skLineSegment(sketch, "E5106", {"start": v(-9285.64, -14691.98) * mm, "end": v(-9348.4, -14587.1) * mm});
            skLineSegment(sketch, "E5107", {"start": v(-9348.4, -14587.1) * mm, "end": v(-9409.67, -14481.96) * mm});
            skLineSegment(sketch, "E5108", {"start": v(-9409.67, -14481.96) * mm, "end": v(-9469.46, -14376.56) * mm});
            skLineSegment(sketch, "E5109", {"start": v(-9469.46, -14376.56) * mm, "end": v(-9527.77, -14270.9) * mm});
            skLineSegment(sketch, "E5110", {"start": v(-9527.77, -14270.9) * mm, "end": v(-9584.58, -14164.99) * mm});
            skLineSegment(sketch, "E5111", {"start": v(-9584.58, -14164.99) * mm, "end": v(-9639.9, -14058.81) * mm});
            skLineSegment(sketch, "E5112", {"start": v(-9639.9, -14058.81) * mm, "end": v(-9693.72, -13952.38) * mm});
            skLineSegment(sketch, "E5113", {"start": v(-9693.72, -13952.38) * mm, "end": v(-9746.04, -13845.68) * mm});
            skLineSegment(sketch, "E5114", {"start": v(-9746.04, -13845.68) * mm, "end": v(-9796.85, -13738.73) * mm});
            skLineSegment(sketch, "E5115", {"start": v(-9796.85, -13738.73) * mm, "end": v(-9846.15, -13631.52) * mm});
            skLineSegment(sketch, "E5116", {"start": v(-9846.15, -13631.52) * mm, "end": v(-9893.93, -13524.04) * mm});
            skLineSegment(sketch, "E5117", {"start": v(-9893.93, -13524.04) * mm, "end": v(-9940.2, -13416.31) * mm});
            skLineSegment(sketch, "E5118", {"start": v(-9940.2, -13416.31) * mm, "end": v(-9984.94, -13308.32) * mm});
            skLineSegment(sketch, "E5119", {"start": v(-9984.94, -13308.32) * mm, "end": v(-10028.15, -13200.07) * mm});
            skLineSegment(sketch, "E5120", {"start": v(-10028.15, -13200.07) * mm, "end": v(-10069.84, -13091.56) * mm});
            skLineSegment(sketch, "E5121", {"start": v(-10069.84, -13091.56) * mm, "end": v(-10109.98, -12982.8) * mm});
            skLineSegment(sketch, "E5122", {"start": v(-10109.98, -12982.8) * mm, "end": v(-10148.6, -12873.76) * mm});
            skLineSegment(sketch, "E5123", {"start": v(-10148.6, -12873.76) * mm, "end": v(-10185.66, -12764.47) * mm});
            skLineSegment(sketch, "E5124", {"start": v(-10185.66, -12764.47) * mm, "end": v(-10221.17, -12654.93) * mm});
            skLineSegment(sketch, "E5125", {"start": v(-10221.17, -12654.93) * mm, "end": v(-10255.14, -12545.12) * mm});
            skLineSegment(sketch, "E5126", {"start": v(-10255.14, -12545.12) * mm, "end": v(-10272.62, -12488.61) * mm});
            skLineSegment(sketch, "E5127", {"start": v(-10272.62, -12488.61) * mm, "end": v(-10289.82, -12431.1) * mm});
            skLineSegment(sketch, "E5128", {"start": v(-10289.82, -12431.1) * mm, "end": v(-10306.72, -12372.58) * mm});
            skLineSegment(sketch, "E5129", {"start": v(-10306.72, -12372.58) * mm, "end": v(-10323.34, -12313.06) * mm});
            skLineSegment(sketch, "E5130", {"start": v(-10323.34, -12313.06) * mm, "end": v(-10339.66, -12252.53) * mm});
            skLineSegment(sketch, "E5131", {"start": v(-10339.66, -12252.53) * mm, "end": v(-10355.7, -12190.99) * mm});
            skLineSegment(sketch, "E5132", {"start": v(-10355.7, -12190.99) * mm, "end": v(-10371.44, -12128.44) * mm});
            skLineSegment(sketch, "E5133", {"start": v(-10371.44, -12128.44) * mm, "end": v(-10386.9, -12064.89) * mm});
            skLineSegment(sketch, "E5134", {"start": v(-10386.9, -12064.89) * mm, "end": v(-10416.95, -11934.75) * mm});
            skLineSegment(sketch, "E5135", {"start": v(-10416.95, -11934.75) * mm, "end": v(-10445.86, -11800.58) * mm});
            skLineSegment(sketch, "E5136", {"start": v(-10445.86, -11800.58) * mm, "end": v(-10473.62, -11662.36) * mm});
            skLineSegment(sketch, "E5137", {"start": v(-10473.62, -11662.36) * mm, "end": v(-10500.25, -11520.1) * mm});
            skLineSegment(sketch, "E5138", {"start": v(-10500.25, -11520.1) * mm, "end": v(-10525.74, -11373.78) * mm});
            skLineSegment(sketch, "E5139", {"start": v(-10525.74, -11373.78) * mm, "end": v(-10550.1, -11223.4) * mm});
            skLineSegment(sketch, "E5140", {"start": v(-10550.1, -11223.4) * mm, "end": v(-10573.33, -11068.97) * mm});
            skLineSegment(sketch, "E5141", {"start": v(-10573.33, -11068.97) * mm, "end": v(-10595.45, -10910.48) * mm});
            skLineSegment(sketch, "E5142", {"start": v(-10595.45, -10910.48) * mm, "end": v(-10616.44, -10747.91) * mm});
            skLineSegment(sketch, "E5143", {"start": v(-10616.44, -10747.91) * mm, "end": v(-10636.32, -10581.28) * mm});
            skLineSegment(sketch, "E5144", {"start": v(-10636.32, -10581.28) * mm, "end": v(-10655.1, -10410.57) * mm});
            skLineSegment(sketch, "E5145", {"start": v(-10655.1, -10410.57) * mm, "end": v(-10672.76, -10235.78) * mm});
            skLineSegment(sketch, "E5146", {"start": v(-10672.76, -10235.78) * mm, "end": v(-10689.32, -10056.9) * mm});
            skLineSegment(sketch, "E5147", {"start": v(-10689.32, -10056.9) * mm, "end": v(-10704.78, -9873.95) * mm});
            skLineSegment(sketch, "E5148", {"start": v(-10704.78, -9873.95) * mm, "end": v(-10719.15, -9686.9) * mm});
            skLineSegment(sketch, "E5149", {"start": v(-10719.15, -9686.9) * mm, "end": v(-10732.44, -9495.74) * mm});
            skLineSegment(sketch, "E5150", {"start": v(-10732.44, -9495.74) * mm, "end": v(-10744.63, -9300.5) * mm});
            skLineSegment(sketch, "E5151", {"start": v(-10744.63, -9300.5) * mm, "end": v(-10755.74, -9101.14) * mm});
            skLineSegment(sketch, "E5152", {"start": v(-10755.74, -9101.14) * mm, "end": v(-10765.78, -8897.68) * mm});
            skLineSegment(sketch, "E5153", {"start": v(-10765.78, -8897.68) * mm, "end": v(-10774.74, -8690.11) * mm});
            skLineSegment(sketch, "E5154", {"start": v(-10774.74, -8690.11) * mm, "end": v(-10782.63, -8478.42) * mm});
            skLineSegment(sketch, "E5155", {"start": v(-10782.63, -8478.42) * mm, "end": v(-10789.46, -8262.61) * mm});
            skLineSegment(sketch, "E5156", {"start": v(-10789.46, -8262.61) * mm, "end": v(-10795.23, -8042.68) * mm});
            skLineSegment(sketch, "E5157", {"start": v(-10795.23, -8042.68) * mm, "end": v(-10799.93, -7818.62) * mm});
            skLineSegment(sketch, "E5158", {"start": v(-10799.93, -7818.62) * mm, "end": v(-10803.59, -7590.43) * mm});
            skLineSegment(sketch, "E5159", {"start": v(-10803.59, -7590.43) * mm, "end": v(-10806.2, -7358.1) * mm});
            skLineSegment(sketch, "E5160", {"start": v(-10806.2, -7358.1) * mm, "end": v(-10807.76, -7121.63) * mm});
            skLineSegment(sketch, "E5161", {"start": v(-10807.76, -7121.63) * mm, "end": v(-10808.28, -6881.01) * mm});
            skLineSegment(sketch, "E5162", {"start": v(-10808.28, -6881.01) * mm, "end": v(-10808.28, -475.7) * mm});
            skLineSegment(sketch, "E5163", {"start": v(-10808.28, -475.7) * mm, "end": v(-10808.28, 5929.62) * mm});
            skLineSegment(sketch, "E5164", {"start": v(-10808.28, 5929.62) * mm, "end": v(-10807.43, 6242.44) * mm});
            skLineSegment(sketch, "E5165", {"start": v(-10807.43, 6242.44) * mm, "end": v(-10804.9, 6550.34) * mm});
            skLineSegment(sketch, "E5166", {"start": v(-10804.9, 6550.34) * mm, "end": v(-10800.67, 6853.31) * mm});
            skLineSegment(sketch, "E5167", {"start": v(-10800.67, 6853.31) * mm, "end": v(-10794.75, 7151.36) * mm});
            skLineSegment(sketch, "E5168", {"start": v(-10794.75, 7151.36) * mm, "end": v(-10787.12, 7444.47) * mm});
            skLineSegment(sketch, "E5169", {"start": v(-10787.12, 7444.47) * mm, "end": v(-10777.8, 7732.67) * mm});
            skLineSegment(sketch, "E5170", {"start": v(-10777.8, 7732.67) * mm, "end": v(-10766.75, 8015.93) * mm});
            skLineSegment(sketch, "E5171", {"start": v(-10766.75, 8015.93) * mm, "end": v(-10754, 8294.27) * mm});
            skLineSegment(sketch, "E5172", {"start": v(-10754, 8294.27) * mm, "end": v(-10739.53, 8567.69) * mm});
            skLineSegment(sketch, "E5173", {"start": v(-10739.53, 8567.69) * mm, "end": v(-10723.33, 8836.17) * mm});
            skLineSegment(sketch, "E5174", {"start": v(-10723.33, 8836.17) * mm, "end": v(-10714.59, 8968.57) * mm});
            skLineSegment(sketch, "E5175", {"start": v(-10714.59, 8968.57) * mm, "end": v(-10705.41, 9099.73) * mm});
            skLineSegment(sketch, "E5176", {"start": v(-10705.41, 9099.73) * mm, "end": v(-10695.8, 9229.67) * mm});
            skLineSegment(sketch, "E5177", {"start": v(-10695.8, 9229.67) * mm, "end": v(-10685.76, 9358.37) * mm});
            skLineSegment(sketch, "E5178", {"start": v(-10685.76, 9358.37) * mm, "end": v(-10675.29, 9485.84) * mm});
            skLineSegment(sketch, "E5179", {"start": v(-10675.29, 9485.84) * mm, "end": v(-10664.38, 9612.08) * mm});
            skLineSegment(sketch, "E5180", {"start": v(-10664.38, 9612.08) * mm, "end": v(-10653.04, 9737.08) * mm});
            skLineSegment(sketch, "E5181", {"start": v(-10653.04, 9737.08) * mm, "end": v(-10641.26, 9860.86) * mm});
            skLineSegment(sketch, "E5182", {"start": v(-10641.26, 9860.86) * mm, "end": v(-10629.05, 9983.4) * mm});
            skLineSegment(sketch, "E5183", {"start": v(-10629.05, 9983.4) * mm, "end": v(-10616.4, 10104.71) * mm});
            skLineSegment(sketch, "E5184", {"start": v(-10616.4, 10104.71) * mm, "end": v(-10603.3, 10224.8) * mm});
            skLineSegment(sketch, "E5185", {"start": v(-10603.3, 10224.8) * mm, "end": v(-10589.79, 10343.64) * mm});
            skLineSegment(sketch, "E5186", {"start": v(-10589.79, 10343.64) * mm, "end": v(-10575.83, 10461.26) * mm});
            skLineSegment(sketch, "E5187", {"start": v(-10575.83, 10461.26) * mm, "end": v(-10561.43, 10577.64) * mm});
            skLineSegment(sketch, "E5188", {"start": v(-10561.43, 10577.64) * mm, "end": v(-10546.59, 10692.8) * mm});
            skLineSegment(sketch, "E5189", {"start": v(-10546.59, 10692.8) * mm, "end": v(-10531.31, 10806.72) * mm});
            skLineSegment(sketch, "E5190", {"start": v(-10531.31, 10806.72) * mm, "end": v(-10515.6, 10919.41) * mm});
            skLineSegment(sketch, "E5191", {"start": v(-10515.6, 10919.41) * mm, "end": v(-10499.44, 11030.87) * mm});
            skLineSegment(sketch, "E5192", {"start": v(-10499.44, 11030.87) * mm, "end": v(-10482.84, 11141.1) * mm});
            skLineSegment(sketch, "E5193", {"start": v(-10482.84, 11141.1) * mm, "end": v(-10465.8, 11250.1) * mm});
            skLineSegment(sketch, "E5194", {"start": v(-10465.8, 11250.1) * mm, "end": v(-10448.33, 11357.86) * mm});
            skLineSegment(sketch, "E5195", {"start": v(-10448.33, 11357.86) * mm, "end": v(-10430.4, 11464.39) * mm});
            skLineSegment(sketch, "E5196", {"start": v(-10430.4, 11464.39) * mm, "end": v(-10412.04, 11569.7) * mm});
            skLineSegment(sketch, "E5197", {"start": v(-10412.04, 11569.7) * mm, "end": v(-10393.23, 11673.76) * mm});
            skLineSegment(sketch, "E5198", {"start": v(-10393.23, 11673.76) * mm, "end": v(-10373.98, 11776.6) * mm});
            skLineSegment(sketch, "E5199", {"start": v(-10373.98, 11776.6) * mm, "end": v(-10354.29, 11878.2) * mm});
            skLineSegment(sketch, "E5200", {"start": v(-10354.29, 11878.2) * mm, "end": v(-10334.15, 11978.58) * mm});
            skLineSegment(sketch, "E5201", {"start": v(-10334.15, 11978.58) * mm, "end": v(-10313.56, 12077.72) * mm});
            skLineSegment(sketch, "E5202", {"start": v(-10313.56, 12077.72) * mm, "end": v(-10292.53, 12175.63) * mm});
            skLineSegment(sketch, "E5203", {"start": v(-10292.53, 12175.63) * mm, "end": v(-10271.06, 12272.31) * mm});
            skLineSegment(sketch, "E5204", {"start": v(-10271.06, 12272.31) * mm, "end": v(-10249.13, 12367.76) * mm});
            skLineSegment(sketch, "E5205", {"start": v(-10249.13, 12367.76) * mm, "end": v(-10226.76, 12461.98) * mm});
            skLineSegment(sketch, "E5206", {"start": v(-10226.76, 12461.98) * mm, "end": v(-10203.95, 12554.96) * mm});
            skLineSegment(sketch, "E5207", {"start": v(-10203.95, 12554.96) * mm, "end": v(-10180.68, 12646.72) * mm});
            skLineSegment(sketch, "E5208", {"start": v(-10180.68, 12646.72) * mm, "end": v(-10156.97, 12737.24) * mm});
            skLineSegment(sketch, "E5209", {"start": v(-10156.97, 12737.24) * mm, "end": v(-10132.8, 12826.53) * mm});
            skLineSegment(sketch, "E5210", {"start": v(-10132.8, 12826.53) * mm, "end": v(-10108.19, 12914.59) * mm});
            skLineSegment(sketch, "E5211", {"start": v(-10108.19, 12914.59) * mm, "end": v(-10083.12, 13001.42) * mm});
            skLineSegment(sketch, "E5212", {"start": v(-10083.12, 13001.42) * mm, "end": v(-10057.6, 13087.01) * mm});
            skLineSegment(sketch, "E5213", {"start": v(-10057.6, 13087.01) * mm, "end": v(-10031.64, 13171.38) * mm});
            skLineSegment(sketch, "E5214", {"start": v(-10031.64, 13171.38) * mm, "end": v(-10005.23, 13254.5) * mm});
            skLineSegment(sketch, "E5215", {"start": v(-10005.23, 13254.5) * mm, "end": v(-9978.36, 13336.4) * mm});
            skLineSegment(sketch, "E5216", {"start": v(-9978.36, 13336.4) * mm, "end": v(-9951.03, 13417.08) * mm});
            skLineSegment(sketch, "E5217", {"start": v(-9951.03, 13417.08) * mm, "end": v(-9923.26, 13496.52) * mm});
            skLineSegment(sketch, "E5218", {"start": v(-9923.26, 13496.52) * mm, "end": v(-9895.87, 13574.07) * mm});
            skLineSegment(sketch, "E5219", {"start": v(-9895.87, 13574.07) * mm, "end": v(-9867.64, 13651.18) * mm});
            skLineSegment(sketch, "E5220", {"start": v(-9867.64, 13651.18) * mm, "end": v(-9838.57, 13727.83) * mm});
            skLineSegment(sketch, "E5221", {"start": v(-9838.57, 13727.83) * mm, "end": v(-9808.65, 13804.02) * mm});
            skLineSegment(sketch, "E5222", {"start": v(-9808.65, 13804.02) * mm, "end": v(-9777.89, 13879.76) * mm});
            skLineSegment(sketch, "E5223", {"start": v(-9777.89, 13879.76) * mm, "end": v(-9746.28, 13955.04) * mm});
            skLineSegment(sketch, "E5224", {"start": v(-9746.28, 13955.04) * mm, "end": v(-9713.83, 14029.86) * mm});
            skLineSegment(sketch, "E5225", {"start": v(-9713.83, 14029.86) * mm, "end": v(-9680.53, 14104.23) * mm});
            skLineSegment(sketch, "E5226", {"start": v(-9680.53, 14104.23) * mm, "end": v(-9646.38, 14178.14) * mm});
            skLineSegment(sketch, "E5227", {"start": v(-9646.38, 14178.14) * mm, "end": v(-9611.39, 14251.6) * mm});
            skLineSegment(sketch, "E5228", {"start": v(-9611.39, 14251.6) * mm, "end": v(-9575.54, 14324.58) * mm});
            skLineSegment(sketch, "E5229", {"start": v(-9575.54, 14324.58) * mm, "end": v(-9538.86, 14397.12) * mm});
            skLineSegment(sketch, "E5230", {"start": v(-9538.86, 14397.12) * mm, "end": v(-9501.32, 14469.2) * mm});
            skLineSegment(sketch, "E5231", {"start": v(-9501.32, 14469.2) * mm, "end": v(-9462.93, 14540.8) * mm});
            skLineSegment(sketch, "E5232", {"start": v(-9462.93, 14540.8) * mm, "end": v(-9423.7, 14611.96) * mm});
            skLineSegment(sketch, "E5233", {"start": v(-9423.7, 14611.96) * mm, "end": v(-9383.6, 14682.65) * mm});
            skLineSegment(sketch, "E5234", {"start": v(-9383.6, 14682.65) * mm, "end": v(-9342.67, 14752.88) * mm});
            skLineSegment(sketch, "E5235", {"start": v(-9342.67, 14752.88) * mm, "end": v(-9300.88, 14822.64) * mm});
            skLineSegment(sketch, "E5236", {"start": v(-9300.88, 14822.64) * mm, "end": v(-9258.24, 14891.95) * mm});
            skLineSegment(sketch, "E5237", {"start": v(-9258.24, 14891.95) * mm, "end": v(-9214.74, 14960.79) * mm});
            skLineSegment(sketch, "E5238", {"start": v(-9214.74, 14960.79) * mm, "end": v(-9170.4, 15029.16) * mm});
            skLineSegment(sketch, "E5239", {"start": v(-9170.4, 15029.16) * mm, "end": v(-9125.2, 15097.08) * mm});
            skLineSegment(sketch, "E5240", {"start": v(-9125.2, 15097.08) * mm, "end": v(-9079.14, 15164.52) * mm});
            skLineSegment(sketch, "E5241", {"start": v(-9079.14, 15164.52) * mm, "end": v(-9032.23, 15231.5) * mm});
            skLineSegment(sketch, "E5242", {"start": v(-9032.23, 15231.5) * mm, "end": v(-8984.47, 15298.02) * mm});
            skLineSegment(sketch, "E5243", {"start": v(-8984.47, 15298.02) * mm, "end": v(-8935.85, 15364.07) * mm});
            skLineSegment(sketch, "E5244", {"start": v(-8935.85, 15364.07) * mm, "end": v(-8886.38, 15429.65) * mm});
            skLineSegment(sketch, "E5245", {"start": v(-8886.38, 15429.65) * mm, "end": v(-8836.05, 15494.77) * mm});
            skLineSegment(sketch, "E5246", {"start": v(-8836.05, 15494.77) * mm, "end": v(-8784.86, 15559.42) * mm});
            skLineSegment(sketch, "E5247", {"start": v(-8784.86, 15559.42) * mm, "end": v(-8732.82, 15623.6) * mm});
            skLineSegment(sketch, "E5248", {"start": v(-8732.82, 15623.6) * mm, "end": v(-8679.91, 15687.3) * mm});
            skLineSegment(sketch, "E5249", {"start": v(-8679.91, 15687.3) * mm, "end": v(-8626.15, 15750.54) * mm});
            skLineSegment(sketch, "E5250", {"start": v(-8626.15, 15750.54) * mm, "end": v(-8571.53, 15813.32) * mm});
            skLineSegment(sketch, "E5251", {"start": v(-8571.53, 15813.32) * mm, "end": v(-8516.06, 15875.62) * mm});
            skLineSegment(sketch, "E5252", {"start": v(-8516.06, 15875.62) * mm, "end": v(-8459.72, 15937.44) * mm});
            skLineSegment(sketch, "E5253", {"start": v(-8459.72, 15937.44) * mm, "end": v(-8402.52, 15998.8) * mm});
            skLineSegment(sketch, "E5254", {"start": v(-8402.52, 15998.8) * mm, "end": v(-8344.46, 16059.69) * mm});
            skLineSegment(sketch, "E5255", {"start": v(-8344.46, 16059.69) * mm, "end": v(-8285.54, 16120.1) * mm});
            skLineSegment(sketch, "E5256", {"start": v(-8285.54, 16120.1) * mm, "end": v(-8225.75, 16180.04) * mm});
            skLineSegment(sketch, "E5257", {"start": v(-8225.75, 16180.04) * mm, "end": v(-8165.1, 16239.5) * mm});
            skLineSegment(sketch, "E5258", {"start": v(-8165.1, 16239.5) * mm, "end": v(-8103.6, 16298.5) * mm});
            skLineSegment(sketch, "E5259", {"start": v(-8103.6, 16298.5) * mm, "end": v(-8041.23, 16357.02) * mm});
            skLineSegment(sketch, "E5260", {"start": v(-8041.23, 16357.02) * mm, "end": v(-7977.99, 16415.06) * mm});
            skLineSegment(sketch, "E5261", {"start": v(-7977.99, 16415.06) * mm, "end": v(-7913.89, 16472.63) * mm});
            skLineSegment(sketch, "E5262", {"start": v(-7913.89, 16472.63) * mm, "end": v(-7848.92, 16529.72) * mm});
            skLineSegment(sketch, "E5263", {"start": v(-7848.92, 16529.72) * mm, "end": v(-7783.1, 16586.34) * mm});
            skLineSegment(sketch, "E5264", {"start": v(-7783.1, 16586.34) * mm, "end": v(-7716.4, 16642.47) * mm});
            skLineSegment(sketch, "E5265", {"start": v(-7716.4, 16642.47) * mm, "end": v(-7648.83, 16698.14) * mm});
            skLineSegment(sketch, "E5266", {"start": v(-7648.83, 16698.14) * mm, "end": v(-7580.4, 16753.32) * mm});
            skLineSegment(sketch, "E5267", {"start": v(-7580.4, 16753.32) * mm, "end": v(-7511.1, 16808.02) * mm});
            skLineSegment(sketch, "E5268", {"start": v(-7511.1, 16808.02) * mm, "end": v(-7440.94, 16862.25) * mm});
            skLineSegment(sketch, "E5269", {"start": v(-7440.94, 16862.25) * mm, "end": v(-7369.9, 16916) * mm});
            skLineSegment(sketch, "E5270", {"start": v(-7369.9, 16916) * mm, "end": v(-7298, 16969.26) * mm});
            skLineSegment(sketch, "E5271", {"start": v(-7298, 16969.26) * mm, "end": v(-7225.23, 17022.04) * mm});
            skLineSegment(sketch, "E5272", {"start": v(-7225.23, 17022.04) * mm, "end": v(-7151.58, 17074.35) * mm});
            skLineSegment(sketch, "E5273", {"start": v(-7151.58, 17074.35) * mm, "end": v(-7077.07, 17126.17) * mm});
            skLineSegment(sketch, "E5274", {"start": v(-7077.07, 17126.17) * mm, "end": v(-7001.69, 17177.5) * mm});
            skLineSegment(sketch, "E5275", {"start": v(-7001.69, 17177.5) * mm, "end": v(-6925.43, 17228.36) * mm});
            skLineSegment(sketch, "E5276", {"start": v(-6925.43, 17228.36) * mm, "end": v(-6848.3, 17278.74) * mm});
            skLineSegment(sketch, "E5277", {"start": v(-6848.3, 17278.74) * mm, "end": v(-6770.3, 17328.63) * mm});
            skLineSegment(sketch, "E5278", {"start": v(-6770.3, 17328.63) * mm, "end": v(-6691.43, 17378.04) * mm});
            skLineSegment(sketch, "E5279", {"start": v(-6691.43, 17378.04) * mm, "end": v(-6611.68, 17426.96) * mm});
            skLineSegment(sketch, "E5280", {"start": v(-6611.68, 17426.96) * mm, "end": v(-6531.06, 17475.4) * mm});
            skLineSegment(sketch, "E5281", {"start": v(-6531.06, 17475.4) * mm, "end": v(-6449.56, 17523.34) * mm});
            skLineSegment(sketch, "E5282", {"start": v(-6449.56, 17523.34) * mm, "end": v(-6368.4, 17570.66) * mm});
            skLineSegment(sketch, "E5283", {"start": v(-6368.4, 17570.66) * mm, "end": v(-6286.67, 17617.2) * mm});
            skLineSegment(sketch, "E5284", {"start": v(-6286.67, 17617.2) * mm, "end": v(-6204.4, 17662.98) * mm});
            skLineSegment(sketch, "E5285", {"start": v(-6204.4, 17662.98) * mm, "end": v(-6121.58, 17707.97) * mm});
            skLineSegment(sketch, "E5286", {"start": v(-6121.58, 17707.97) * mm, "end": v(-6038.2, 17752.2) * mm});
            skLineSegment(sketch, "E5287", {"start": v(-6038.2, 17752.2) * mm, "end": v(-5954.29, 17795.65) * mm});
            skLineSegment(sketch, "E5288", {"start": v(-5954.29, 17795.65) * mm, "end": v(-5869.82, 17838.33) * mm});
            skLineSegment(sketch, "E5289", {"start": v(-5869.82, 17838.33) * mm, "end": v(-5784.8, 17880.25) * mm});
            skLineSegment(sketch, "E5290", {"start": v(-5784.8, 17880.25) * mm, "end": v(-5699.25, 17921.4) * mm});
            skLineSegment(sketch, "E5291", {"start": v(-5699.25, 17921.4) * mm, "end": v(-5613.14, 17961.79) * mm});
            skLineSegment(sketch, "E5292", {"start": v(-5613.14, 17961.79) * mm, "end": v(-5526.49, 18001.4) * mm});
            skLineSegment(sketch, "E5293", {"start": v(-5526.49, 18001.4) * mm, "end": v(-5439.29, 18040.27) * mm});
            skLineSegment(sketch, "E5294", {"start": v(-5439.29, 18040.27) * mm, "end": v(-5351.54, 18078.38) * mm});
            skLineSegment(sketch, "E5295", {"start": v(-5351.54, 18078.38) * mm, "end": v(-5263.25, 18115.72) * mm});
            skLineSegment(sketch, "E5296", {"start": v(-5263.25, 18115.72) * mm, "end": v(-5174.42, 18152.31) * mm});
            skLineSegment(sketch, "E5297", {"start": v(-5174.42, 18152.31) * mm, "end": v(-5085.05, 18188.15) * mm});
            skLineSegment(sketch, "E5298", {"start": v(-5085.05, 18188.15) * mm, "end": v(-4995.13, 18223.23) * mm});
            skLineSegment(sketch, "E5299", {"start": v(-4995.13, 18223.23) * mm, "end": v(-4904.67, 18257.55) * mm});
            skLineSegment(sketch, "E5300", {"start": v(-4904.67, 18257.55) * mm, "end": v(-4813.67, 18291.13) * mm});
            skLineSegment(sketch, "E5301", {"start": v(-4813.67, 18291.13) * mm, "end": v(-4722.12, 18323.96) * mm});
            skLineSegment(sketch, "E5302", {"start": v(-4722.12, 18323.96) * mm, "end": v(-4630.04, 18356.04) * mm});
            skLineSegment(sketch, "E5303", {"start": v(-4630.04, 18356.04) * mm, "end": v(-4537.41, 18387.38) * mm});
            skLineSegment(sketch, "E5304", {"start": v(-4537.41, 18387.38) * mm, "end": v(-4444.25, 18417.97) * mm});
            skLineSegment(sketch, "E5305", {"start": v(-4444.25, 18417.97) * mm, "end": v(-4350.54, 18447.82) * mm});
            skLineSegment(sketch, "E5306", {"start": v(-4350.54, 18447.82) * mm, "end": v(-4256.3, 18476.92) * mm});
            skLineSegment(sketch, "E5307", {"start": v(-4256.3, 18476.92) * mm, "end": v(-4161.52, 18505.3) * mm});
            skLineSegment(sketch, "E5308", {"start": v(-4161.52, 18505.3) * mm, "end": v(-4066.2, 18532.92) * mm});
            skLineSegment(sketch, "E5309", {"start": v(-4066.2, 18532.92) * mm, "end": v(-3970.34, 18559.81) * mm});
            skLineSegment(sketch, "E5310", {"start": v(-3970.34, 18559.81) * mm, "end": v(-3873.95, 18585.97) * mm});
            skLineSegment(sketch, "E5311", {"start": v(-3873.95, 18585.97) * mm, "end": v(-3777.02, 18611.39) * mm});
            skLineSegment(sketch, "E5312", {"start": v(-3777.02, 18611.39) * mm, "end": v(-3679.56, 18636.08) * mm});
            skLineSegment(sketch, "E5313", {"start": v(-3679.56, 18636.08) * mm, "end": v(-3581.55, 18660.04) * mm});
            skLineSegment(sketch, "E5314", {"start": v(-3581.55, 18660.04) * mm, "end": v(-3483.02, 18683.27) * mm});
            skLineSegment(sketch, "E5315", {"start": v(-3483.02, 18683.27) * mm, "end": v(-3383.95, 18705.77) * mm});
            skLineSegment(sketch, "E5316", {"start": v(-3383.95, 18705.77) * mm, "end": v(-3284.35, 18727.55) * mm});
            skLineSegment(sketch, "E5317", {"start": v(-3284.35, 18727.55) * mm, "end": v(-3184.2, 18748.6) * mm});
            skLineSegment(sketch, "E5318", {"start": v(-3184.2, 18748.6) * mm, "end": v(-3083.54, 18768.93) * mm});
            skLineSegment(sketch, "E5319", {"start": v(-3083.54, 18768.93) * mm, "end": v(-2982.34, 18788.54) * mm});
            skLineSegment(sketch, "E5320", {"start": v(-2982.34, 18788.54) * mm, "end": v(-2880.6, 18807.42) * mm});
            skLineSegment(sketch, "E5321", {"start": v(-2880.6, 18807.42) * mm, "end": v(-2778.34, 18825.6) * mm});
            skLineSegment(sketch, "E5322", {"start": v(-2778.34, 18825.6) * mm, "end": v(-2675.55, 18843.04) * mm});
            skLineSegment(sketch, "E5323", {"start": v(-2675.55, 18843.04) * mm, "end": v(-2572.22, 18859.78) * mm});
            skLineSegment(sketch, "E5324", {"start": v(-2572.22, 18859.78) * mm, "end": v(-2468.37, 18875.8) * mm});
            skLineSegment(sketch, "E5325", {"start": v(-2468.37, 18875.8) * mm, "end": v(-2363.98, 18891.1) * mm});
            skLineSegment(sketch, "E5326", {"start": v(-2363.98, 18891.1) * mm, "end": v(-2259.07, 18905.7) * mm});
            skLineSegment(sketch, "E5327", {"start": v(-2259.07, 18905.7) * mm, "end": v(-2153.63, 18919.6) * mm});
            skLineSegment(sketch, "E5328", {"start": v(-2153.63, 18919.6) * mm, "end": v(-2047.66, 18932.78) * mm});
            skLineSegment(sketch, "E5329", {"start": v(-2047.66, 18932.78) * mm, "end": v(-1941.16, 18945.25) * mm});
            skLineSegment(sketch, "E5330", {"start": v(-1941.16, 18945.25) * mm, "end": v(-1834.14, 18957.02) * mm});
            skLineSegment(sketch, "E5331", {"start": v(-1834.14, 18957.02) * mm, "end": v(-1726.59, 18968.08) * mm});
            skLineSegment(sketch, "E5332", {"start": v(-1726.59, 18968.08) * mm, "end": v(-1618.51, 18978.45) * mm});
            skLineSegment(sketch, "E5333", {"start": v(-1618.51, 18978.45) * mm, "end": v(-1509.92, 18988.11) * mm});
            skLineSegment(sketch, "E5334", {"start": v(-1509.92, 18988.11) * mm, "end": v(-1400.8, 18997.08) * mm});
            skLineSegment(sketch, "E5335", {"start": v(-1400.8, 18997.08) * mm, "end": v(-1291.14, 19005.34) * mm});
            skLineSegment(sketch, "E5336", {"start": v(-1291.14, 19005.34) * mm, "end": v(-1180.97, 19012.92) * mm});
            skLineSegment(sketch, "E5337", {"start": v(-1180.97, 19012.92) * mm, "end": v(-1070.27, 19019.8) * mm});
            skLineSegment(sketch, "E5338", {"start": v(-1070.27, 19019.8) * mm, "end": v(-959.06, 19025.98) * mm});
            skLineSegment(sketch, "E5339", {"start": v(-959.06, 19025.98) * mm, "end": v(-847.32, 19031.47) * mm});
            skLineSegment(sketch, "E5340", {"start": v(-847.32, 19031.47) * mm, "end": v(-735.06, 19036.27) * mm});
            skLineSegment(sketch, "E5341", {"start": v(-735.06, 19036.27) * mm, "end": v(-622.27, 19040.4) * mm});
            skLineSegment(sketch, "E5342", {"start": v(-622.27, 19040.4) * mm, "end": v(-508.97, 19043.82) * mm});
            skLineSegment(sketch, "E5343", {"start": v(-508.97, 19043.82) * mm, "end": v(-395.15, 19046.56) * mm});
            skLineSegment(sketch, "E5344", {"start": v(-395.15, 19046.56) * mm, "end": v(-280.8, 19048.62) * mm});
            skLineSegment(sketch, "E5345", {"start": v(-280.8, 19048.62) * mm, "end": v(-165.94, 19050) * mm});
            skLineSegment(sketch, "E5346", {"start": v(-165.94, 19050) * mm, "end": v(22.17, 19047.02) * mm});
            skLineSegment(sketch, "E5347", {"start": v(22.17, 19047.02) * mm, "end": v(208.99, 19042.2) * mm});
            skLineSegment(sketch, "E5348", {"start": v(208.99, 19042.2) * mm, "end": v(394.52, 19035.56) * mm});
            skLineSegment(sketch, "E5349", {"start": v(394.52, 19035.56) * mm, "end": v(578.76, 19027.05) * mm});
            skLineSegment(sketch, "E5350", {"start": v(578.76, 19027.05) * mm, "end": v(761.73, 19016.69) * mm});
            skLineSegment(sketch, "E5351", {"start": v(761.73, 19016.69) * mm, "end": v(943.42, 19004.45) * mm});
            skLineSegment(sketch, "E5352", {"start": v(943.42, 19004.45) * mm, "end": v(1123.83, 18990.32) * mm});
            skLineSegment(sketch, "E5353", {"start": v(1123.83, 18990.32) * mm, "end": v(1302.98, 18974.29) * mm});
            skLineSegment(sketch, "E5354", {"start": v(1302.98, 18974.29) * mm, "end": v(1480.87, 18956.35) * mm});
            skLineSegment(sketch, "E5355", {"start": v(1480.87, 18956.35) * mm, "end": v(1569.33, 18946.66) * mm});
            skLineSegment(sketch, "E5356", {"start": v(1569.33, 18946.66) * mm, "end": v(1657.5, 18936.48) * mm});
            skLineSegment(sketch, "E5357", {"start": v(1657.5, 18936.48) * mm, "end": v(1745.33, 18925.82) * mm});
            skLineSegment(sketch, "E5358", {"start": v(1745.33, 18925.82) * mm, "end": v(1832.86, 18914.68) * mm});
            skLineSegment(sketch, "E5359", {"start": v(1832.86, 18914.68) * mm, "end": v(1920.07, 18903.05) * mm});
            skLineSegment(sketch, "E5360", {"start": v(1920.07, 18903.05) * mm, "end": v(2006.98, 18890.93) * mm});
            skLineSegment(sketch, "E5361", {"start": v(2006.98, 18890.93) * mm, "end": v(2093.57, 18878.32) * mm});
            skLineSegment(sketch, "E5362", {"start": v(2093.57, 18878.32) * mm, "end": v(2179.84, 18865.22) * mm});
            skLineSegment(sketch, "E5363", {"start": v(2179.84, 18865.22) * mm, "end": v(2265.81, 18851.62) * mm});
            skLineSegment(sketch, "E5364", {"start": v(2265.81, 18851.62) * mm, "end": v(2351.47, 18837.53) * mm});
            skLineSegment(sketch, "E5365", {"start": v(2351.47, 18837.53) * mm, "end": v(2436.82, 18822.95) * mm});
            skLineSegment(sketch, "E5366", {"start": v(2436.82, 18822.95) * mm, "end": v(2521.86, 18807.86) * mm});
            skLineSegment(sketch, "E5367", {"start": v(2521.86, 18807.86) * mm, "end": v(2606.59, 18792.28) * mm});
            skLineSegment(sketch, "E5368", {"start": v(2606.59, 18792.28) * mm, "end": v(2691, 18776.2) * mm});
            skLineSegment(sketch, "E5369", {"start": v(2691, 18776.2) * mm, "end": v(2775.12, 18759.61) * mm});
            skLineSegment(sketch, "E5370", {"start": v(2775.12, 18759.61) * mm, "end": v(2858.92, 18742.52) * mm});
            skLineSegment(sketch, "E5371", {"start": v(2858.92, 18742.52) * mm, "end": v(2942.42, 18724.93) * mm});
            skLineSegment(sketch, "E5372", {"start": v(2942.42, 18724.93) * mm, "end": v(3025.62, 18706.82) * mm});
            skLineSegment(sketch, "E5373", {"start": v(3025.62, 18706.82) * mm, "end": v(3108.5, 18688.21) * mm});
            skLineSegment(sketch, "E5374", {"start": v(3108.5, 18688.21) * mm, "end": v(3191.08, 18669.1) * mm});
            skLineSegment(sketch, "E5375", {"start": v(3191.08, 18669.1) * mm, "end": v(3273.36, 18649.46) * mm});
            skLineSegment(sketch, "E5376", {"start": v(3273.36, 18649.46) * mm, "end": v(3355.33, 18629.31) * mm});
            skLineSegment(sketch, "E5377", {"start": v(3355.33, 18629.31) * mm, "end": v(3437, 18608.65) * mm});
            skLineSegment(sketch, "E5378", {"start": v(3437, 18608.65) * mm, "end": v(3518.36, 18587.48) * mm});
            skLineSegment(sketch, "E5379", {"start": v(3518.36, 18587.48) * mm, "end": v(3599.43, 18565.79) * mm});
            skLineSegment(sketch, "E5380", {"start": v(3599.43, 18565.79) * mm, "end": v(3680.18, 18543.57) * mm});
            skLineSegment(sketch, "E5381", {"start": v(3680.18, 18543.57) * mm, "end": v(3760.64, 18520.84) * mm});
            skLineSegment(sketch, "E5382", {"start": v(3760.64, 18520.84) * mm, "end": v(3840.8, 18497.58) * mm});
            skLineSegment(sketch, "E5383", {"start": v(3840.8, 18497.58) * mm, "end": v(3920.65, 18473.8) * mm});
            skLineSegment(sketch, "E5384", {"start": v(3920.65, 18473.8) * mm, "end": v(4000.2, 18449.5) * mm});
            skLineSegment(sketch, "E5385", {"start": v(4000.2, 18449.5) * mm, "end": v(4079.47, 18424.67) * mm});
            skLineSegment(sketch, "E5386", {"start": v(4079.47, 18424.67) * mm, "end": v(4158.42, 18399.31) * mm});
            skLineSegment(sketch, "E5387", {"start": v(4158.42, 18399.31) * mm, "end": v(4237.08, 18373.42) * mm});
            skLineSegment(sketch, "E5388", {"start": v(4237.08, 18373.42) * mm, "end": v(4315.44, 18347) * mm});
            skLineSegment(sketch, "E5389", {"start": v(4315.44, 18347) * mm, "end": v(4393.5, 18320.05) * mm});
            skLineSegment(sketch, "E5390", {"start": v(4393.5, 18320.05) * mm, "end": v(4471.26, 18292.57) * mm});
            skLineSegment(sketch, "E5391", {"start": v(4471.26, 18292.57) * mm, "end": v(4548.73, 18264.54) * mm});
            skLineSegment(sketch, "E5392", {"start": v(4548.73, 18264.54) * mm, "end": v(4625.9, 18235.98) * mm});
            skLineSegment(sketch, "E5393", {"start": v(4625.9, 18235.98) * mm, "end": v(4702.78, 18206.88) * mm});
            skLineSegment(sketch, "E5394", {"start": v(4702.78, 18206.88) * mm, "end": v(4779.36, 18177.25) * mm});
            skLineSegment(sketch, "E5395", {"start": v(4779.36, 18177.25) * mm, "end": v(4855.64, 18147.06) * mm});
            skLineSegment(sketch, "E5396", {"start": v(4855.64, 18147.06) * mm, "end": v(4931.63, 18116.34) * mm});
            skLineSegment(sketch, "E5397", {"start": v(4931.63, 18116.34) * mm, "end": v(5007.33, 18085.07) * mm});
            skLineSegment(sketch, "E5398", {"start": v(5007.33, 18085.07) * mm, "end": v(5082.73, 18053.26) * mm});
            skLineSegment(sketch, "E5399", {"start": v(5082.73, 18053.26) * mm, "end": v(5157.85, 18020.9) * mm});
            skLineSegment(sketch, "E5400", {"start": v(5157.85, 18020.9) * mm, "end": v(5232.67, 17987.98) * mm});
            skLineSegment(sketch, "E5401", {"start": v(5232.67, 17987.98) * mm, "end": v(5380.84, 17921.15) * mm});
            skLineSegment(sketch, "E5402", {"start": v(5380.84, 17921.15) * mm, "end": v(5526.69, 17853.42) * mm});
            skLineSegment(sketch, "E5403", {"start": v(5526.69, 17853.42) * mm, "end": v(5670.19, 17784.78) * mm});
            skLineSegment(sketch, "E5404", {"start": v(5670.19, 17784.78) * mm, "end": v(5811.34, 17715.26) * mm});
            skLineSegment(sketch, "E5405", {"start": v(5811.34, 17715.26) * mm, "end": v(5950.15, 17644.84) * mm});
            skLineSegment(sketch, "E5406", {"start": v(5950.15, 17644.84) * mm, "end": v(6086.6, 17573.53) * mm});
            skLineSegment(sketch, "E5407", {"start": v(6086.6, 17573.53) * mm, "end": v(6220.69, 17501.34) * mm});
            skLineSegment(sketch, "E5408", {"start": v(6220.69, 17501.34) * mm, "end": v(6352.42, 17428.27) * mm});
            skLineSegment(sketch, "E5409", {"start": v(6352.42, 17428.27) * mm, "end": v(6481.79, 17354.33) * mm});
            skLineSegment(sketch, "E5410", {"start": v(6481.79, 17354.33) * mm, "end": v(6608.78, 17279.52) * mm});
            skLineSegment(sketch, "E5411", {"start": v(6608.78, 17279.52) * mm, "end": v(6733.4, 17203.84) * mm});
            skLineSegment(sketch, "E5412", {"start": v(6733.4, 17203.84) * mm, "end": v(6855.64, 17127.3) * mm});
            skLineSegment(sketch, "E5413", {"start": v(6855.64, 17127.3) * mm, "end": v(6975.5, 17049.89) * mm});
            skLineSegment(sketch, "E5414", {"start": v(6975.5, 17049.89) * mm, "end": v(7092.98, 16971.63) * mm});
            skLineSegment(sketch, "E5415", {"start": v(7092.98, 16971.63) * mm, "end": v(7150.82, 16932.18) * mm});
            skLineSegment(sketch, "E5416", {"start": v(7150.82, 16932.18) * mm, "end": v(7208.06, 16892.52) * mm});
            skLineSegment(sketch, "E5417", {"start": v(7208.06, 16892.52) * mm, "end": v(7264.7, 16852.65) * mm});
            skLineSegment(sketch, "E5418", {"start": v(7264.7, 16852.65) * mm, "end": v(7320.75, 16812.57) * mm});
            skLineSegment(sketch, "E5419", {"start": v(7320.75, 16812.57) * mm, "end": v(7376.2, 16772.27) * mm});
            skLineSegment(sketch, "E5420", {"start": v(7376.2, 16772.27) * mm, "end": v(7431.05, 16731.77) * mm});
            skLineSegment(sketch, "E5421", {"start": v(7431.05, 16731.77) * mm, "end": v(7485.3, 16691.05) * mm});
            skLineSegment(sketch, "E5422", {"start": v(7485.3, 16691.05) * mm, "end": v(7538.93, 16650.13) * mm});
            skLineSegment(sketch, "E5423", {"start": v(7538.93, 16650.13) * mm, "end": v(7591.98, 16609) * mm});
            skLineSegment(sketch, "E5424", {"start": v(7591.98, 16609) * mm, "end": v(7644.42, 16567.66) * mm});
            skLineSegment(sketch, "E5425", {"start": v(7644.42, 16567.66) * mm, "end": v(7696.25, 16526.11) * mm});
            skLineSegment(sketch, "E5426", {"start": v(7696.25, 16526.11) * mm, "end": v(7747.49, 16484.36) * mm});
            skLineSegment(sketch, "E5427", {"start": v(7747.49, 16484.36) * mm, "end": v(7798.12, 16442.4) * mm});
            skLineSegment(sketch, "E5428", {"start": v(7798.12, 16442.4) * mm, "end": v(7848.15, 16400.23) * mm});
            skLineSegment(sketch, "E5429", {"start": v(7848.15, 16400.23) * mm, "end": v(7897.57, 16357.86) * mm});
            skLineSegment(sketch, "E5430", {"start": v(7897.57, 16357.86) * mm, "end": v(7946.39, 16315.28) * mm});
            skLineSegment(sketch, "E5431", {"start": v(7946.39, 16315.28) * mm, "end": v(7994.6, 16272.5) * mm});
            skLineSegment(sketch, "E5432", {"start": v(7994.6, 16272.5) * mm, "end": v(8042.2, 16229.5) * mm});
            skLineSegment(sketch, "E5433", {"start": v(8042.2, 16229.5) * mm, "end": v(8089.2, 16186.32) * mm});
            skLineSegment(sketch, "E5434", {"start": v(8089.2, 16186.32) * mm, "end": v(8135.6, 16142.93) * mm});
            skLineSegment(sketch, "E5435", {"start": v(8135.6, 16142.93) * mm, "end": v(8181.38, 16099.33) * mm});
            skLineSegment(sketch, "E5436", {"start": v(8181.38, 16099.33) * mm, "end": v(8226.55, 16055.53) * mm});
            skLineSegment(sketch, "E5437", {"start": v(8226.55, 16055.53) * mm, "end": v(8271.12, 16011.53) * mm});
            skLineSegment(sketch, "E5438", {"start": v(8271.12, 16011.53) * mm, "end": v(8315.07, 15967.33) * mm});
            skLineSegment(sketch, "E5439", {"start": v(8315.07, 15967.33) * mm, "end": v(8358.42, 15922.93) * mm});
            skLineSegment(sketch, "E5440", {"start": v(8358.42, 15922.93) * mm, "end": v(8401.16, 15878.33) * mm});
            skLineSegment(sketch, "E5441", {"start": v(8401.16, 15878.33) * mm, "end": v(8443.29, 15833.53) * mm});
            skLineSegment(sketch, "E5442", {"start": v(8443.29, 15833.53) * mm, "end": v(8484.8, 15788.53) * mm});
            skLineSegment(sketch, "E5443", {"start": v(8484.8, 15788.53) * mm, "end": v(8525.7, 15743.33) * mm});
            skLineSegment(sketch, "E5444", {"start": v(8525.7, 15743.33) * mm, "end": v(8566, 15697.94) * mm});
            skLineSegment(sketch, "E5445", {"start": v(8566, 15697.94) * mm, "end": v(8605.68, 15652.34) * mm});
            skLineSegment(sketch, "E5446", {"start": v(8605.68, 15652.34) * mm, "end": v(8644.74, 15606.55) * mm});
            skLineSegment(sketch, "E5447", {"start": v(8644.74, 15606.55) * mm, "end": v(8683.2, 15560.56) * mm});
            skLineSegment(sketch, "E5448", {"start": v(8683.2, 15560.56) * mm, "end": v(8721.03, 15514.38) * mm});
            skLineSegment(sketch, "E5449", {"start": v(8721.03, 15514.38) * mm, "end": v(8758.25, 15468) * mm});
            skLineSegment(sketch, "E5450", {"start": v(8758.25, 15468) * mm, "end": v(8794.86, 15421.43) * mm});
            skLineSegment(sketch, "E5451", {"start": v(8794.86, 15421.43) * mm, "end": v(8868.76, 15325.62) * mm});
            skLineSegment(sketch, "E5452", {"start": v(8868.76, 15325.62) * mm, "end": v(8941.1, 15229.05) * mm});
            skLineSegment(sketch, "E5453", {"start": v(8941.1, 15229.05) * mm, "end": v(9011.88, 15131.7) * mm});
            skLineSegment(sketch, "E5454", {"start": v(9011.88, 15131.7) * mm, "end": v(9081.1, 15033.59) * mm});
            skLineSegment(sketch, "E5455", {"start": v(9081.1, 15033.59) * mm, "end": v(9148.78, 14934.71) * mm});
            skLineSegment(sketch, "E5456", {"start": v(9148.78, 14934.71) * mm, "end": v(9214.9, 14835.08) * mm});
            skLineSegment(sketch, "E5457", {"start": v(9214.9, 14835.08) * mm, "end": v(9279.46, 14734.7) * mm});
            skLineSegment(sketch, "E5458", {"start": v(9279.46, 14734.7) * mm, "end": v(9342.47, 14633.56) * mm});
            skLineSegment(sketch, "E5459", {"start": v(9342.47, 14633.56) * mm, "end": v(9403.92, 14531.67) * mm});
            skLineSegment(sketch, "E5460", {"start": v(9403.92, 14531.67) * mm, "end": v(9463.8, 14429.05) * mm});
            skLineSegment(sketch, "E5461", {"start": v(9463.8, 14429.05) * mm, "end": v(9522.15, 14325.7) * mm});
            skLineSegment(sketch, "E5462", {"start": v(9522.15, 14325.7) * mm, "end": v(9578.93, 14221.6) * mm});
            skLineSegment(sketch, "E5463", {"start": v(9578.93, 14221.6) * mm, "end": v(9634.16, 14116.78) * mm});
            skLineSegment(sketch, "E5464", {"start": v(9634.16, 14116.78) * mm, "end": v(9687.83, 14011.23) * mm});
            skLineSegment(sketch, "E5465", {"start": v(9687.83, 14011.23) * mm, "end": v(9739.95, 13904.96) * mm});
            skLineSegment(sketch, "E5466", {"start": v(9739.95, 13904.96) * mm, "end": v(9790.5, 13797.97) * mm});
            skLineSegment(sketch, "E5467", {"start": v(9790.5, 13797.97) * mm, "end": v(9839.5, 13690.28) * mm});
            skLineSegment(sketch, "E5468", {"start": v(9839.5, 13690.28) * mm, "end": v(9886.96, 13581.87) * mm});
            skLineSegment(sketch, "E5469", {"start": v(9886.96, 13581.87) * mm, "end": v(9932.85, 13472.76) * mm});
            skLineSegment(sketch, "E5470", {"start": v(9932.85, 13472.76) * mm, "end": v(9977.19, 13362.94) * mm});
            skLineSegment(sketch, "E5471", {"start": v(9977.19, 13362.94) * mm, "end": v(10019.97, 13252.43) * mm});
            skLineSegment(sketch, "E5472", {"start": v(10019.97, 13252.43) * mm, "end": v(10061.2, 13141.23) * mm});
            skLineSegment(sketch, "E5473", {"start": v(10061.2, 13141.23) * mm, "end": v(10100.87, 13029.34) * mm});
            skLineSegment(sketch, "E5474", {"start": v(10100.87, 13029.34) * mm, "end": v(10138.98, 12916.76) * mm});
            skLineSegment(sketch, "E5475", {"start": v(10138.98, 12916.76) * mm, "end": v(10175.54, 12803.5) * mm});
            skLineSegment(sketch, "E5476", {"start": v(10175.54, 12803.5) * mm, "end": v(10210.54, 12689.57) * mm});
            skLineSegment(sketch, "E5477", {"start": v(10210.54, 12689.57) * mm, "end": v(10244, 12574.96) * mm});
            skLineSegment(sketch, "E5478", {"start": v(10244, 12574.96) * mm, "end": v(10275.88, 12459.69) * mm});
            skLineSegment(sketch, "E5479", {"start": v(10275.88, 12459.69) * mm, "end": v(10306.22, 12343.75) * mm});
            skLineSegment(sketch, "E5480", {"start": v(10306.22, 12343.75) * mm, "end": v(10335, 12227.15) * mm});
            skLineSegment(sketch, "E5481", {"start": v(10335, 12227.15) * mm, "end": v(10362.22, 12109.9) * mm});
            skLineSegment(sketch, "E5482", {"start": v(10362.22, 12109.9) * mm, "end": v(10387.9, 11991.99) * mm});
            skLineSegment(sketch, "E5483", {"start": v(10387.9, 11991.99) * mm, "end": v(10414.4, 11871.49) * mm});
            skLineSegment(sketch, "E5484", {"start": v(10414.4, 11871.49) * mm, "end": v(10440.01, 11746.46) * mm});
            skLineSegment(sketch, "E5485", {"start": v(10440.01, 11746.46) * mm, "end": v(10464.72, 11616.9) * mm});
            skLineSegment(sketch, "E5486", {"start": v(10464.72, 11616.9) * mm, "end": v(10488.54, 11482.84) * mm});
            skLineSegment(sketch, "E5487", {"start": v(10488.54, 11482.84) * mm, "end": v(10511.46, 11344.27) * mm});
            skLineSegment(sketch, "E5488", {"start": v(10511.46, 11344.27) * mm, "end": v(10533.5, 11201.2) * mm});
            skLineSegment(sketch, "E5489", {"start": v(10533.5, 11201.2) * mm, "end": v(10554.65, 11053.65) * mm});
            skLineSegment(sketch, "E5490", {"start": v(10554.65, 11053.65) * mm, "end": v(10574.92, 10901.62) * mm});
            skLineSegment(sketch, "E5491", {"start": v(10574.92, 10901.62) * mm, "end": v(10594.32, 10745.1) * mm});
            skLineSegment(sketch, "E5492", {"start": v(10594.32, 10745.1) * mm, "end": v(10612.85, 10584.14) * mm});
            skLineSegment(sketch, "E5493", {"start": v(10612.85, 10584.14) * mm, "end": v(10630.5, 10418.7) * mm});
            skLineSegment(sketch, "E5494", {"start": v(10630.5, 10418.7) * mm, "end": v(10647.3, 10248.83) * mm});
            skLineSegment(sketch, "E5495", {"start": v(10647.3, 10248.83) * mm, "end": v(10663.24, 10074.51) * mm});
            skLineSegment(sketch, "E5496", {"start": v(10663.24, 10074.51) * mm, "end": v(10678.33, 9895.76) * mm});
            skLineSegment(sketch, "E5497", {"start": v(10678.33, 9895.76) * mm, "end": v(10692.56, 9712.59) * mm});
            skLineSegment(sketch, "E5498", {"start": v(10692.56, 9712.59) * mm, "end": v(10705.95, 9525) * mm});
            skLineSegment(sketch, "E5499", {"start": v(10705.95, 9525) * mm, "end": v(10718.49, 9333) * mm});
            skLineSegment(sketch, "E5500", {"start": v(10718.49, 9333) * mm, "end": v(10730.2, 9136.6) * mm});
            skLineSegment(sketch, "E5501", {"start": v(10730.2, 9136.6) * mm, "end": v(10741.06, 8935.82) * mm});
            skLineSegment(sketch, "E5502", {"start": v(10741.06, 8935.82) * mm, "end": v(10751.1, 8730.64) * mm});
            skLineSegment(sketch, "E5503", {"start": v(10751.1, 8730.64) * mm, "end": v(10760.32, 8521.1) * mm});
            skLineSegment(sketch, "E5504", {"start": v(10760.32, 8521.1) * mm, "end": v(10768.7, 8307.18) * mm});
            skLineSegment(sketch, "E5505", {"start": v(10768.7, 8307.18) * mm, "end": v(10776.28, 8088.9) * mm});
            skLineSegment(sketch, "E5506", {"start": v(10776.28, 8088.9) * mm, "end": v(10783.04, 7866.28) * mm});
            skLineSegment(sketch, "E5507", {"start": v(10783.04, 7866.28) * mm, "end": v(10788.99, 7639.32) * mm});
            skLineSegment(sketch, "E5508", {"start": v(10788.99, 7639.32) * mm, "end": v(10794.13, 7408.01) * mm});
            skLineSegment(sketch, "E5509", {"start": v(10794.13, 7408.01) * mm, "end": v(10798.47, 7172.38) * mm});
            skLineSegment(sketch, "E5510", {"start": v(10798.47, 7172.38) * mm, "end": v(10802, 6932.43) * mm});
            skLineSegment(sketch, "E5511", {"start": v(10802, 6932.43) * mm, "end": v(10804.76, 6688.18) * mm});
            skLineSegment(sketch, "E5512", {"start": v(10804.76, 6688.18) * mm, "end": v(10806.71, 6439.61) * mm});
            skLineSegment(sketch, "E5513", {"start": v(10806.71, 6439.61) * mm, "end": v(10807.89, 6186.76) * mm});
            skLineSegment(sketch, "E5514", {"start": v(10807.89, 6186.76) * mm, "end": v(10808.28, 5929.62) * mm});
            skLineSegment(sketch, "E5515", {"start": v(1692.6, 9027.18) * mm, "end": v(1692.27, 9207.57) * mm});
            skLineSegment(sketch, "E5516", {"start": v(1692.27, 9207.57) * mm, "end": v(1691.31, 9383.7) * mm});
            skLineSegment(sketch, "E5517", {"start": v(1691.31, 9383.7) * mm, "end": v(1689.72, 9555.53) * mm});
            skLineSegment(sketch, "E5518", {"start": v(1689.72, 9555.53) * mm, "end": v(1687.5, 9723.1) * mm});
            skLineSegment(sketch, "E5519", {"start": v(1687.5, 9723.1) * mm, "end": v(1684.66, 9886.37) * mm});
            skLineSegment(sketch, "E5520", {"start": v(1684.66, 9886.37) * mm, "end": v(1681.22, 10045.38) * mm});
            skLineSegment(sketch, "E5521", {"start": v(1681.22, 10045.38) * mm, "end": v(1677.18, 10200.1) * mm});
            skLineSegment(sketch, "E5522", {"start": v(1677.18, 10200.1) * mm, "end": v(1672.54, 10350.56) * mm});
            skLineSegment(sketch, "E5523", {"start": v(1672.54, 10350.56) * mm, "end": v(1667.33, 10496.73) * mm});
            skLineSegment(sketch, "E5524", {"start": v(1667.33, 10496.73) * mm, "end": v(1661.54, 10638.62) * mm});
            skLineSegment(sketch, "E5525", {"start": v(1661.54, 10638.62) * mm, "end": v(1655.18, 10776.23) * mm});
            skLineSegment(sketch, "E5526", {"start": v(1655.18, 10776.23) * mm, "end": v(1648.26, 10909.57) * mm});
            skLineSegment(sketch, "E5527", {"start": v(1648.26, 10909.57) * mm, "end": v(1640.79, 11038.63) * mm});
            skLineSegment(sketch, "E5528", {"start": v(1640.79, 11038.63) * mm, "end": v(1632.78, 11163.4) * mm});
            skLineSegment(sketch, "E5529", {"start": v(1632.78, 11163.4) * mm, "end": v(1624.23, 11283.9) * mm});
            skLineSegment(sketch, "E5530", {"start": v(1624.23, 11283.9) * mm, "end": v(1615.16, 11400.13) * mm});
            skLineSegment(sketch, "E5531", {"start": v(1615.16, 11400.13) * mm, "end": v(1605.56, 11512.08) * mm});
            skLineSegment(sketch, "E5532", {"start": v(1605.56, 11512.08) * mm, "end": v(1595.46, 11619.74) * mm});
            skLineSegment(sketch, "E5533", {"start": v(1595.46, 11619.74) * mm, "end": v(1584.86, 11723.13) * mm});
            skLineSegment(sketch, "E5534", {"start": v(1584.86, 11723.13) * mm, "end": v(1573.76, 11822.24) * mm});
            skLineSegment(sketch, "E5535", {"start": v(1573.76, 11822.24) * mm, "end": v(1562.17, 11917.08) * mm});
            skLineSegment(sketch, "E5536", {"start": v(1562.17, 11917.08) * mm, "end": v(1550.1, 12007.63) * mm});
            skLineSegment(sketch, "E5537", {"start": v(1550.1, 12007.63) * mm, "end": v(1537.58, 12093.9) * mm});
            skLineSegment(sketch, "E5538", {"start": v(1537.58, 12093.9) * mm, "end": v(1524.58, 12175.9) * mm});
            skLineSegment(sketch, "E5539", {"start": v(1524.58, 12175.9) * mm, "end": v(1511.13, 12253.62) * mm});
            skLineSegment(sketch, "E5540", {"start": v(1511.13, 12253.62) * mm, "end": v(1497.24, 12327.07) * mm});
            skLineSegment(sketch, "E5541", {"start": v(1497.24, 12327.07) * mm, "end": v(1482.9, 12396.23) * mm});
            skLineSegment(sketch, "E5542", {"start": v(1482.9, 12396.23) * mm, "end": v(1468.14, 12461.11) * mm});
            skLineSegment(sketch, "E5543", {"start": v(1468.14, 12461.11) * mm, "end": v(1452.96, 12521.72) * mm});
            skLineSegment(sketch, "E5544", {"start": v(1452.96, 12521.72) * mm, "end": v(1437.36, 12578.05) * mm});
            skLineSegment(sketch, "E5545", {"start": v(1437.36, 12578.05) * mm, "end": v(1421.36, 12630.1) * mm});
            skLineSegment(sketch, "E5546", {"start": v(1421.36, 12630.1) * mm, "end": v(1404.97, 12677.87) * mm});
            skLineSegment(sketch, "E5547", {"start": v(1404.97, 12677.87) * mm, "end": v(1385.52, 12722.8) * mm});
            skLineSegment(sketch, "E5548", {"start": v(1385.52, 12722.8) * mm, "end": v(1364.52, 12766.3) * mm});
            skLineSegment(sketch, "E5549", {"start": v(1364.52, 12766.3) * mm, "end": v(1341.98, 12808.38) * mm});
            skLineSegment(sketch, "E5550", {"start": v(1341.98, 12808.38) * mm, "end": v(1330.13, 12828.89) * mm});
            skLineSegment(sketch, "E5551", {"start": v(1330.13, 12828.89) * mm, "end": v(1317.89, 12849.04) * mm});
            skLineSegment(sketch, "E5552", {"start": v(1317.89, 12849.04) * mm, "end": v(1305.27, 12868.85) * mm});
            skLineSegment(sketch, "E5553", {"start": v(1305.27, 12868.85) * mm, "end": v(1292.26, 12888.3) * mm});
            skLineSegment(sketch, "E5554", {"start": v(1292.26, 12888.3) * mm, "end": v(1278.87, 12907.4) * mm});
            skLineSegment(sketch, "E5555", {"start": v(1278.87, 12907.4) * mm, "end": v(1265.1, 12926.15) * mm});
            skLineSegment(sketch, "E5556", {"start": v(1265.1, 12926.15) * mm, "end": v(1250.94, 12944.55) * mm});
            skLineSegment(sketch, "E5557", {"start": v(1250.94, 12944.55) * mm, "end": v(1236.4, 12962.6) * mm});
            skLineSegment(sketch, "E5558", {"start": v(1236.4, 12962.6) * mm, "end": v(1221.48, 12980.3) * mm});
            skLineSegment(sketch, "E5559", {"start": v(1221.48, 12980.3) * mm, "end": v(1206.18, 12997.66) * mm});
            skLineSegment(sketch, "E5560", {"start": v(1206.18, 12997.66) * mm, "end": v(1190.5, 13014.66) * mm});
            skLineSegment(sketch, "E5561", {"start": v(1190.5, 13014.66) * mm, "end": v(1174.44, 13031.32) * mm});
            skLineSegment(sketch, "E5562", {"start": v(1174.44, 13031.32) * mm, "end": v(1158, 13047.62) * mm});
            skLineSegment(sketch, "E5563", {"start": v(1158, 13047.62) * mm, "end": v(1141.17, 13063.58) * mm});
            skLineSegment(sketch, "E5564", {"start": v(1141.17, 13063.58) * mm, "end": v(1106.4, 13094.47) * mm});
            skLineSegment(sketch, "E5565", {"start": v(1106.4, 13094.47) * mm, "end": v(1070.1, 13123.97) * mm});
            skLineSegment(sketch, "E5566", {"start": v(1070.1, 13123.97) * mm, "end": v(1032.3, 13152.1) * mm});
            skLineSegment(sketch, "E5567", {"start": v(1032.3, 13152.1) * mm, "end": v(993, 13178.85) * mm});
            skLineSegment(sketch, "E5568", {"start": v(993, 13178.85) * mm, "end": v(952.2, 13204.23) * mm});
            skLineSegment(sketch, "E5569", {"start": v(952.2, 13204.23) * mm, "end": v(909.9, 13228.24) * mm});
            skLineSegment(sketch, "E5570", {"start": v(909.9, 13228.24) * mm, "end": v(866.12, 13250.9) * mm});
            skLineSegment(sketch, "E5571", {"start": v(866.12, 13250.9) * mm, "end": v(820.85, 13272.2) * mm});
            skLineSegment(sketch, "E5572", {"start": v(820.85, 13272.2) * mm, "end": v(774.1, 13292.14) * mm});
            skLineSegment(sketch, "E5573", {"start": v(774.1, 13292.14) * mm, "end": v(725.86, 13310.74) * mm});
            skLineSegment(sketch, "E5574", {"start": v(725.86, 13310.74) * mm, "end": v(676.15, 13328) * mm});
            skLineSegment(sketch, "E5575", {"start": v(676.15, 13328) * mm, "end": v(624.97, 13343.9) * mm});
            skLineSegment(sketch, "E5576", {"start": v(624.97, 13343.9) * mm, "end": v(572.33, 13358.47) * mm});
            skLineSegment(sketch, "E5577", {"start": v(572.33, 13358.47) * mm, "end": v(518.22, 13371.71) * mm});
            skLineSegment(sketch, "E5578", {"start": v(518.22, 13371.71) * mm, "end": v(462.65, 13383.63) * mm});
            skLineSegment(sketch, "E5579", {"start": v(462.65, 13383.63) * mm, "end": v(405.63, 13394.21) * mm});
            skLineSegment(sketch, "E5580", {"start": v(405.63, 13394.21) * mm, "end": v(347.16, 13403.48) * mm});
            skLineSegment(sketch, "E5581", {"start": v(347.16, 13403.48) * mm, "end": v(287.24, 13411.43) * mm});
            skLineSegment(sketch, "E5582", {"start": v(287.24, 13411.43) * mm, "end": v(225.88, 13418.06) * mm});
            skLineSegment(sketch, "E5583", {"start": v(225.88, 13418.06) * mm, "end": v(163.08, 13423.4) * mm});
            skLineSegment(sketch, "E5584", {"start": v(163.08, 13423.4) * mm, "end": v(98.85, 13427.42) * mm});
            skLineSegment(sketch, "E5585", {"start": v(98.85, 13427.42) * mm, "end": v(33.19, 13430.14) * mm});
            skLineSegment(sketch, "E5586", {"start": v(33.19, 13430.14) * mm, "end": v(-30.47, 13427.41) * mm});
            skLineSegment(sketch, "E5587", {"start": v(-30.47, 13427.41) * mm, "end": v(-92.82, 13423.38) * mm});
            skLineSegment(sketch, "E5588", {"start": v(-92.82, 13423.38) * mm, "end": v(-153.87, 13418.03) * mm});
            skLineSegment(sketch, "E5589", {"start": v(-153.87, 13418.03) * mm, "end": v(-213.6, 13411.34) * mm});
            skLineSegment(sketch, "E5590", {"start": v(-213.6, 13411.34) * mm, "end": v(-272.03, 13403.3) * mm});
            skLineSegment(sketch, "E5591", {"start": v(-272.03, 13403.3) * mm, "end": v(-329.14, 13393.92) * mm});
            skLineSegment(sketch, "E5592", {"start": v(-329.14, 13393.92) * mm, "end": v(-384.93, 13383.16) * mm});
            skLineSegment(sketch, "E5593", {"start": v(-384.93, 13383.16) * mm, "end": v(-439.4, 13371.02) * mm});
            skLineSegment(sketch, "E5594", {"start": v(-439.4, 13371.02) * mm, "end": v(-492.53, 13357.49) * mm});
            skLineSegment(sketch, "E5595", {"start": v(-492.53, 13357.49) * mm, "end": v(-544.34, 13342.55) * mm});
            skLineSegment(sketch, "E5596", {"start": v(-544.34, 13342.55) * mm, "end": v(-594.8, 13326.2) * mm});
            skLineSegment(sketch, "E5597", {"start": v(-594.8, 13326.2) * mm, "end": v(-643.93, 13308.4) * mm});
            skLineSegment(sketch, "E5598", {"start": v(-643.93, 13308.4) * mm, "end": v(-691.7, 13289.18) * mm});
            skLineSegment(sketch, "E5599", {"start": v(-691.7, 13289.18) * mm, "end": v(-738.14, 13268.5) * mm});
            skLineSegment(sketch, "E5600", {"start": v(-738.14, 13268.5) * mm, "end": v(-783.22, 13246.34) * mm});
            skLineSegment(sketch, "E5601", {"start": v(-783.22, 13246.34) * mm, "end": v(-826.94, 13222.71) * mm});
            skLineSegment(sketch, "E5602", {"start": v(-826.94, 13222.71) * mm, "end": v(-869.3, 13197.6) * mm});
            skLineSegment(sketch, "E5603", {"start": v(-869.3, 13197.6) * mm, "end": v(-910.3, 13170.97) * mm});
            skLineSegment(sketch, "E5604", {"start": v(-910.3, 13170.97) * mm, "end": v(-949.92, 13142.83) * mm});
            skLineSegment(sketch, "E5605", {"start": v(-949.92, 13142.83) * mm, "end": v(-969.21, 13128.2) * mm});
            skLineSegment(sketch, "E5606", {"start": v(-969.21, 13128.2) * mm, "end": v(-988.17, 13113.17) * mm});
            skLineSegment(sketch, "E5607", {"start": v(-988.17, 13113.17) * mm, "end": v(-1006.78, 13097.76) * mm});
            skLineSegment(sketch, "E5608", {"start": v(-1006.78, 13097.76) * mm, "end": v(-1025.04, 13081.96) * mm});
            skLineSegment(sketch, "E5609", {"start": v(-1025.04, 13081.96) * mm, "end": v(-1042.96, 13065.78) * mm});
            skLineSegment(sketch, "E5610", {"start": v(-1042.96, 13065.78) * mm, "end": v(-1060.54, 13049.2) * mm});
            skLineSegment(sketch, "E5611", {"start": v(-1060.54, 13049.2) * mm, "end": v(-1077.76, 13032.24) * mm});
            skLineSegment(sketch, "E5612", {"start": v(-1077.76, 13032.24) * mm, "end": v(-1094.64, 13014.88) * mm});
            skLineSegment(sketch, "E5613", {"start": v(-1094.64, 13014.88) * mm, "end": v(-1111.18, 12997.13) * mm});
            skLineSegment(sketch, "E5614", {"start": v(-1111.18, 12997.13) * mm, "end": v(-1127.36, 12978.99) * mm});
            skLineSegment(sketch, "E5615", {"start": v(-1127.36, 12978.99) * mm, "end": v(-1143.2, 12960.44) * mm});
            skLineSegment(sketch, "E5616", {"start": v(-1143.2, 12960.44) * mm, "end": v(-1158.68, 12941.5) * mm});
            skLineSegment(sketch, "E5617", {"start": v(-1158.68, 12941.5) * mm, "end": v(-1173.82, 12922.16) * mm});
            skLineSegment(sketch, "E5618", {"start": v(-1173.82, 12922.16) * mm, "end": v(-1188.61, 12902.42) * mm});
            skLineSegment(sketch, "E5619", {"start": v(-1188.61, 12902.42) * mm, "end": v(-1203.05, 12882.27) * mm});
            skLineSegment(sketch, "E5620", {"start": v(-1203.05, 12882.27) * mm, "end": v(-1217.13, 12861.72) * mm});
            skLineSegment(sketch, "E5621", {"start": v(-1217.13, 12861.72) * mm, "end": v(-1230.87, 12840.76) * mm});
            skLineSegment(sketch, "E5622", {"start": v(-1230.87, 12840.76) * mm, "end": v(-1244.25, 12819.4) * mm});
            skLineSegment(sketch, "E5623", {"start": v(-1244.25, 12819.4) * mm, "end": v(-1257.28, 12797.63) * mm});
            skLineSegment(sketch, "E5624", {"start": v(-1257.28, 12797.63) * mm, "end": v(-1269.96, 12775.44) * mm});
            skLineSegment(sketch, "E5625", {"start": v(-1269.96, 12775.44) * mm, "end": v(-1282.29, 12752.84) * mm});
            skLineSegment(sketch, "E5626", {"start": v(-1282.29, 12752.84) * mm, "end": v(-1294.26, 12729.83) * mm});
            skLineSegment(sketch, "E5627", {"start": v(-1294.26, 12729.83) * mm, "end": v(-1317.13, 12682.57) * mm});
            skLineSegment(sketch, "E5628", {"start": v(-1317.13, 12682.57) * mm, "end": v(-1338.59, 12633.62) * mm});
            skLineSegment(sketch, "E5629", {"start": v(-1338.59, 12633.62) * mm, "end": v(-1359, 12581.9) * mm});
            skLineSegment(sketch, "E5630", {"start": v(-1359, 12581.9) * mm, "end": v(-1378.78, 12526.28) * mm});
            skLineSegment(sketch, "E5631", {"start": v(-1378.78, 12526.28) * mm, "end": v(-1397.9, 12466.76) * mm});
            skLineSegment(sketch, "E5632", {"start": v(-1397.9, 12466.76) * mm, "end": v(-1416.37, 12403.34) * mm});
            skLineSegment(sketch, "E5633", {"start": v(-1416.37, 12403.34) * mm, "end": v(-1434.2, 12336.01) * mm});
            skLineSegment(sketch, "E5634", {"start": v(-1434.2, 12336.01) * mm, "end": v(-1451.38, 12264.78) * mm});
            skLineSegment(sketch, "E5635", {"start": v(-1451.38, 12264.78) * mm, "end": v(-1467.9, 12189.63) * mm});
            skLineSegment(sketch, "E5636", {"start": v(-1467.9, 12189.63) * mm, "end": v(-1483.79, 12110.56) * mm});
            skLineSegment(sketch, "E5637", {"start": v(-1483.79, 12110.56) * mm, "end": v(-1499.02, 12027.58) * mm});
            skLineSegment(sketch, "E5638", {"start": v(-1499.02, 12027.58) * mm, "end": v(-1513.6, 11940.66) * mm});
            skLineSegment(sketch, "E5639", {"start": v(-1513.6, 11940.66) * mm, "end": v(-1527.54, 11849.82) * mm});
            skLineSegment(sketch, "E5640", {"start": v(-1527.54, 11849.82) * mm, "end": v(-1540.83, 11755.05) * mm});
            skLineSegment(sketch, "E5641", {"start": v(-1540.83, 11755.05) * mm, "end": v(-1553.47, 11656.33) * mm});
            skLineSegment(sketch, "E5642", {"start": v(-1553.47, 11656.33) * mm, "end": v(-1565.46, 11553.67) * mm});
            skLineSegment(sketch, "E5643", {"start": v(-1565.46, 11553.67) * mm, "end": v(-1576.8, 11447.07) * mm});
            skLineSegment(sketch, "E5644", {"start": v(-1576.8, 11447.07) * mm, "end": v(-1587.5, 11336.52) * mm});
            skLineSegment(sketch, "E5645", {"start": v(-1587.5, 11336.52) * mm, "end": v(-1597.55, 11222.01) * mm});
            skLineSegment(sketch, "E5646", {"start": v(-1597.55, 11222.01) * mm, "end": v(-1606.95, 11103.55) * mm});
            skLineSegment(sketch, "E5647", {"start": v(-1606.95, 11103.55) * mm, "end": v(-1615.7, 10981.12) * mm});
            skLineSegment(sketch, "E5648", {"start": v(-1615.7, 10981.12) * mm, "end": v(-1623.8, 10854.73) * mm});
            skLineSegment(sketch, "E5649", {"start": v(-1623.8, 10854.73) * mm, "end": v(-1631.25, 10724.37) * mm});
            skLineSegment(sketch, "E5650", {"start": v(-1631.25, 10724.37) * mm, "end": v(-1638.06, 10590.03) * mm});
            skLineSegment(sketch, "E5651", {"start": v(-1638.06, 10590.03) * mm, "end": v(-1644.22, 10451.71) * mm});
            skLineSegment(sketch, "E5652", {"start": v(-1644.22, 10451.71) * mm, "end": v(-1649.73, 10309.42) * mm});
            skLineSegment(sketch, "E5653", {"start": v(-1649.73, 10309.42) * mm, "end": v(-1654.59, 10163.13) * mm});
            skLineSegment(sketch, "E5654", {"start": v(-1654.59, 10163.13) * mm, "end": v(-1658.8, 10012.86) * mm});
            skLineSegment(sketch, "E5655", {"start": v(-1658.8, 10012.86) * mm, "end": v(-1662.37, 9858.59) * mm});
            skLineSegment(sketch, "E5656", {"start": v(-1662.37, 9858.59) * mm, "end": v(-1665.28, 9700.32) * mm});
            skLineSegment(sketch, "E5657", {"start": v(-1665.28, 9700.32) * mm, "end": v(-1667.55, 9538.05) * mm});
            skLineSegment(sketch, "E5658", {"start": v(-1667.55, 9538.05) * mm, "end": v(-1669.17, 9371.77) * mm});
            skLineSegment(sketch, "E5659", {"start": v(-1669.17, 9371.77) * mm, "end": v(-1670.15, 9201.48) * mm});
            skLineSegment(sketch, "E5660", {"start": v(-1670.15, 9201.48) * mm, "end": v(-1670.47, 9027.18) * mm});
            skLineSegment(sketch, "E5661", {"start": v(-1670.47, 9027.18) * mm, "end": v(-1670.47, 55.31) * mm});
            skLineSegment(sketch, "E5662", {"start": v(-1670.47, 55.31) * mm, "end": v(-1670.47, -8916.55) * mm});
            skLineSegment(sketch, "E5663", {"start": v(-1670.47, -8916.55) * mm, "end": v(-1670.15, -9113.28) * mm});
            skLineSegment(sketch, "E5664", {"start": v(-1670.15, -9113.28) * mm, "end": v(-1669.18, -9305.2) * mm});
            skLineSegment(sketch, "E5665", {"start": v(-1669.18, -9305.2) * mm, "end": v(-1667.57, -9492.3) * mm});
            skLineSegment(sketch, "E5666", {"start": v(-1667.57, -9492.3) * mm, "end": v(-1665.33, -9674.56) * mm});
            skLineSegment(sketch, "E5667", {"start": v(-1665.33, -9674.56) * mm, "end": v(-1662.45, -9851.98) * mm});
            skLineSegment(sketch, "E5668", {"start": v(-1662.45, -9851.98) * mm, "end": v(-1658.95, -10024.55) * mm});
            skLineSegment(sketch, "E5669", {"start": v(-1658.95, -10024.55) * mm, "end": v(-1654.82, -10192.24) * mm});
            skLineSegment(sketch, "E5670", {"start": v(-1654.82, -10192.24) * mm, "end": v(-1650.07, -10355.05) * mm});
            skLineSegment(sketch, "E5671", {"start": v(-1650.07, -10355.05) * mm, "end": v(-1644.71, -10512.97) * mm});
            skLineSegment(sketch, "E5672", {"start": v(-1644.71, -10512.97) * mm, "end": v(-1638.74, -10665.98) * mm});
            skLineSegment(sketch, "E5673", {"start": v(-1638.74, -10665.98) * mm, "end": v(-1632.15, -10814.07) * mm});
            skLineSegment(sketch, "E5674", {"start": v(-1632.15, -10814.07) * mm, "end": v(-1624.97, -10957.23) * mm});
            skLineSegment(sketch, "E5675", {"start": v(-1624.97, -10957.23) * mm, "end": v(-1617.18, -11095.45) * mm});
            skLineSegment(sketch, "E5676", {"start": v(-1617.18, -11095.45) * mm, "end": v(-1608.8, -11228.72) * mm});
            skLineSegment(sketch, "E5677", {"start": v(-1608.8, -11228.72) * mm, "end": v(-1599.83, -11357.02) * mm});
            skLineSegment(sketch, "E5678", {"start": v(-1599.83, -11357.02) * mm, "end": v(-1590.27, -11480.34) * mm});
            skLineSegment(sketch, "E5679", {"start": v(-1590.27, -11480.34) * mm, "end": v(-1580.12, -11598.66) * mm});
            skLineSegment(sketch, "E5680", {"start": v(-1580.12, -11598.66) * mm, "end": v(-1569.4, -11711.99) * mm});
            skLineSegment(sketch, "E5681", {"start": v(-1569.4, -11711.99) * mm, "end": v(-1558.1, -11820.3) * mm});
            skLineSegment(sketch, "E5682", {"start": v(-1558.1, -11820.3) * mm, "end": v(-1546.23, -11923.58) * mm});
            skLineSegment(sketch, "E5683", {"start": v(-1546.23, -11923.58) * mm, "end": v(-1533.8, -12021.82) * mm});
            skLineSegment(sketch, "E5684", {"start": v(-1533.8, -12021.82) * mm, "end": v(-1520.8, -12115.01) * mm});
            skLineSegment(sketch, "E5685", {"start": v(-1520.8, -12115.01) * mm, "end": v(-1507.24, -12203.14) * mm});
            skLineSegment(sketch, "E5686", {"start": v(-1507.24, -12203.14) * mm, "end": v(-1493.12, -12286.19) * mm});
            skLineSegment(sketch, "E5687", {"start": v(-1493.12, -12286.19) * mm, "end": v(-1478.46, -12364.15) * mm});
            skLineSegment(sketch, "E5688", {"start": v(-1478.46, -12364.15) * mm, "end": v(-1463.24, -12437) * mm});
            skLineSegment(sketch, "E5689", {"start": v(-1463.24, -12437) * mm, "end": v(-1447.49, -12504.75) * mm});
            skLineSegment(sketch, "E5690", {"start": v(-1447.49, -12504.75) * mm, "end": v(-1431.2, -12567.38) * mm});
            skLineSegment(sketch, "E5691", {"start": v(-1431.2, -12567.38) * mm, "end": v(-1414.37, -12624.86) * mm});
            skLineSegment(sketch, "E5692", {"start": v(-1414.37, -12624.86) * mm, "end": v(-1405.75, -12651.68) * mm});
            skLineSegment(sketch, "E5693", {"start": v(-1405.75, -12651.68) * mm, "end": v(-1397, -12677.2) * mm});
            skLineSegment(sketch, "E5694", {"start": v(-1397, -12677.2) * mm, "end": v(-1388.13, -12701.43) * mm});
            skLineSegment(sketch, "E5695", {"start": v(-1388.13, -12701.43) * mm, "end": v(-1379.12, -12724.37) * mm});
            skLineSegment(sketch, "E5696", {"start": v(-1379.12, -12724.37) * mm, "end": v(-1369.98, -12746.02) * mm});
            skLineSegment(sketch, "E5697", {"start": v(-1369.98, -12746.02) * mm, "end": v(-1360.71, -12766.38) * mm});
            skLineSegment(sketch, "E5698", {"start": v(-1360.71, -12766.38) * mm, "end": v(-1341.27, -12807.21) * mm});
            skLineSegment(sketch, "E5699", {"start": v(-1341.27, -12807.21) * mm, "end": v(-1320.28, -12846.75) * mm});
            skLineSegment(sketch, "E5700", {"start": v(-1320.28, -12846.75) * mm, "end": v(-1297.75, -12885) * mm});
            skLineSegment(sketch, "E5701", {"start": v(-1297.75, -12885) * mm, "end": v(-1273.68, -12921.95) * mm});
            skLineSegment(sketch, "E5702", {"start": v(-1273.68, -12921.95) * mm, "end": v(-1248.1, -12957.6) * mm});
            skLineSegment(sketch, "E5703", {"start": v(-1248.1, -12957.6) * mm, "end": v(-1221, -12991.95) * mm});
            skLineSegment(sketch, "E5704", {"start": v(-1221, -12991.95) * mm, "end": v(-1192.38, -13025.01) * mm});
            skLineSegment(sketch, "E5705", {"start": v(-1192.38, -13025.01) * mm, "end": v(-1162.28, -13056.77) * mm});
            skLineSegment(sketch, "E5706", {"start": v(-1162.28, -13056.77) * mm, "end": v(-1130.68, -13087.24) * mm});
            skLineSegment(sketch, "E5707", {"start": v(-1130.68, -13087.24) * mm, "end": v(-1097.6, -13116.4) * mm});
            skLineSegment(sketch, "E5708", {"start": v(-1097.6, -13116.4) * mm, "end": v(-1063.04, -13144.28) * mm});
            skLineSegment(sketch, "E5709", {"start": v(-1063.04, -13144.28) * mm, "end": v(-1027.02, -13170.86) * mm});
            skLineSegment(sketch, "E5710", {"start": v(-1027.02, -13170.86) * mm, "end": v(-989.54, -13196.14) * mm});
            skLineSegment(sketch, "E5711", {"start": v(-989.54, -13196.14) * mm, "end": v(-950.6, -13220.12) * mm});
            skLineSegment(sketch, "E5712", {"start": v(-950.6, -13220.12) * mm, "end": v(-910.23, -13242.8) * mm});
            skLineSegment(sketch, "E5713", {"start": v(-910.23, -13242.8) * mm, "end": v(-868.42, -13264.2) * mm});
            skLineSegment(sketch, "E5714", {"start": v(-868.42, -13264.2) * mm, "end": v(-825.19, -13284.3) * mm});
            skLineSegment(sketch, "E5715", {"start": v(-825.19, -13284.3) * mm, "end": v(-780.54, -13303.1) * mm});
            skLineSegment(sketch, "E5716", {"start": v(-780.54, -13303.1) * mm, "end": v(-734.48, -13320.6) * mm});
            skLineSegment(sketch, "E5717", {"start": v(-734.48, -13320.6) * mm, "end": v(-687.01, -13336.8) * mm});
            skLineSegment(sketch, "E5718", {"start": v(-687.01, -13336.8) * mm, "end": v(-638.15, -13351.7) * mm});
            skLineSegment(sketch, "E5719", {"start": v(-638.15, -13351.7) * mm, "end": v(-587.91, -13365.32) * mm});
            skLineSegment(sketch, "E5720", {"start": v(-587.91, -13365.32) * mm, "end": v(-536.3, -13377.63) * mm});
            skLineSegment(sketch, "E5721", {"start": v(-536.3, -13377.63) * mm, "end": v(-483.3, -13388.65) * mm});
            skLineSegment(sketch, "E5722", {"start": v(-483.3, -13388.65) * mm, "end": v(-428.95, -13398.38) * mm});
            skLineSegment(sketch, "E5723", {"start": v(-428.95, -13398.38) * mm, "end": v(-373.25, -13406.8) * mm});
            skLineSegment(sketch, "E5724", {"start": v(-373.25, -13406.8) * mm, "end": v(-316.2, -13413.93) * mm});
            skLineSegment(sketch, "E5725", {"start": v(-316.2, -13413.93) * mm, "end": v(-257.81, -13419.77) * mm});
            skLineSegment(sketch, "E5726", {"start": v(-257.81, -13419.77) * mm, "end": v(-198.1, -13424.3) * mm});
            skLineSegment(sketch, "E5727", {"start": v(-198.1, -13424.3) * mm, "end": v(-137.06, -13427.55) * mm});
            skLineSegment(sketch, "E5728", {"start": v(-137.06, -13427.55) * mm, "end": v(-74.72, -13429.5) * mm});
            skLineSegment(sketch, "E5729", {"start": v(-74.72, -13429.5) * mm, "end": v(-11.06, -13430.14) * mm});
            skLineSegment(sketch, "E5730", {"start": v(-11.06, -13430.14) * mm, "end": v(54.54, -13429.36) * mm});
            skLineSegment(sketch, "E5731", {"start": v(54.54, -13429.36) * mm, "end": v(118.59, -13427.03) * mm});
            skLineSegment(sketch, "E5732", {"start": v(118.59, -13427.03) * mm, "end": v(181.1, -13423.16) * mm});
            skLineSegment(sketch, "E5733", {"start": v(181.1, -13423.16) * mm, "end": v(242.08, -13417.74) * mm});
            skLineSegment(sketch, "E5734", {"start": v(242.08, -13417.74) * mm, "end": v(301.54, -13410.78) * mm});
            skLineSegment(sketch, "E5735", {"start": v(301.54, -13410.78) * mm, "end": v(359.48, -13402.28) * mm});
            skLineSegment(sketch, "E5736", {"start": v(359.48, -13402.28) * mm, "end": v(415.92, -13392.26) * mm});
            skLineSegment(sketch, "E5737", {"start": v(415.92, -13392.26) * mm, "end": v(470.86, -13380.7) * mm});
            skLineSegment(sketch, "E5738", {"start": v(470.86, -13380.7) * mm, "end": v(524.3, -13367.63) * mm});
            skLineSegment(sketch, "E5739", {"start": v(524.3, -13367.63) * mm, "end": v(576.27, -13353.03) * mm});
            skLineSegment(sketch, "E5740", {"start": v(576.27, -13353.03) * mm, "end": v(626.75, -13336.92) * mm});
            skLineSegment(sketch, "E5741", {"start": v(626.75, -13336.92) * mm, "end": v(675.78, -13319.3) * mm});
            skLineSegment(sketch, "E5742", {"start": v(675.78, -13319.3) * mm, "end": v(723.34, -13300.17) * mm});
            skLineSegment(sketch, "E5743", {"start": v(723.34, -13300.17) * mm, "end": v(769.45, -13279.53) * mm});
            skLineSegment(sketch, "E5744", {"start": v(769.45, -13279.53) * mm, "end": v(814.12, -13257.4) * mm});
            skLineSegment(sketch, "E5745", {"start": v(814.12, -13257.4) * mm, "end": v(857.36, -13233.78) * mm});
            skLineSegment(sketch, "E5746", {"start": v(857.36, -13233.78) * mm, "end": v(899.17, -13208.66) * mm});
            skLineSegment(sketch, "E5747", {"start": v(899.17, -13208.66) * mm, "end": v(939.56, -13182.05) * mm});
            skLineSegment(sketch, "E5748", {"start": v(939.56, -13182.05) * mm, "end": v(978.55, -13153.97) * mm});
            skLineSegment(sketch, "E5749", {"start": v(978.55, -13153.97) * mm, "end": v(1016.13, -13124.4) * mm});
            skLineSegment(sketch, "E5750", {"start": v(1016.13, -13124.4) * mm, "end": v(1052.32, -13093.36) * mm});
            skLineSegment(sketch, "E5751", {"start": v(1052.32, -13093.36) * mm, "end": v(1087.12, -13060.85) * mm});
            skLineSegment(sketch, "E5752", {"start": v(1087.12, -13060.85) * mm, "end": v(1120.54, -13026.87) * mm});
            skLineSegment(sketch, "E5753", {"start": v(1120.54, -13026.87) * mm, "end": v(1152.6, -12991.43) * mm});
            skLineSegment(sketch, "E5754", {"start": v(1152.6, -12991.43) * mm, "end": v(1183.3, -12954.54) * mm});
            skLineSegment(sketch, "E5755", {"start": v(1183.3, -12954.54) * mm, "end": v(1212.63, -12916.18) * mm});
            skLineSegment(sketch, "E5756", {"start": v(1212.63, -12916.18) * mm, "end": v(1240.63, -12876.38) * mm});
            skLineSegment(sketch, "E5757", {"start": v(1240.63, -12876.38) * mm, "end": v(1267.29, -12835.13) * mm});
            skLineSegment(sketch, "E5758", {"start": v(1267.29, -12835.13) * mm, "end": v(1292.62, -12792.44) * mm});
            skLineSegment(sketch, "E5759", {"start": v(1292.62, -12792.44) * mm, "end": v(1316.63, -12748.3) * mm});
            skLineSegment(sketch, "E5760", {"start": v(1316.63, -12748.3) * mm, "end": v(1339.32, -12702.74) * mm});
            skLineSegment(sketch, "E5761", {"start": v(1339.32, -12702.74) * mm, "end": v(1360.71, -12655.75) * mm});
            skLineSegment(sketch, "E5762", {"start": v(1360.71, -12655.75) * mm, "end": v(1371, -12631.4) * mm});
            skLineSegment(sketch, "E5763", {"start": v(1371, -12631.4) * mm, "end": v(1381.13, -12606.1) * mm});
            skLineSegment(sketch, "E5764", {"start": v(1381.13, -12606.1) * mm, "end": v(1391.1, -12579.82) * mm});
            skLineSegment(sketch, "E5765", {"start": v(1391.1, -12579.82) * mm, "end": v(1400.9, -12552.57) * mm});
            skLineSegment(sketch, "E5766", {"start": v(1400.9, -12552.57) * mm, "end": v(1420.03, -12495.16) * mm});
            skLineSegment(sketch, "E5767", {"start": v(1420.03, -12495.16) * mm, "end": v(1438.5, -12433.89) * mm});
            skLineSegment(sketch, "E5768", {"start": v(1438.5, -12433.89) * mm, "end": v(1456.32, -12368.76) * mm});
            skLineSegment(sketch, "E5769", {"start": v(1456.32, -12368.76) * mm, "end": v(1473.5, -12299.79) * mm});
            skLineSegment(sketch, "E5770", {"start": v(1473.5, -12299.79) * mm, "end": v(1490.03, -12226.97) * mm});
            skLineSegment(sketch, "E5771", {"start": v(1490.03, -12226.97) * mm, "end": v(1505.91, -12150.32) * mm});
            skLineSegment(sketch, "E5772", {"start": v(1505.91, -12150.32) * mm, "end": v(1521.15, -12069.85) * mm});
            skLineSegment(sketch, "E5773", {"start": v(1521.15, -12069.85) * mm, "end": v(1535.73, -11985.56) * mm});
            skLineSegment(sketch, "E5774", {"start": v(1535.73, -11985.56) * mm, "end": v(1549.67, -11897.46) * mm});
            skLineSegment(sketch, "E5775", {"start": v(1549.67, -11897.46) * mm, "end": v(1562.95, -11805.56) * mm});
            skLineSegment(sketch, "E5776", {"start": v(1562.95, -11805.56) * mm, "end": v(1575.6, -11709.87) * mm});
            skLineSegment(sketch, "E5777", {"start": v(1575.6, -11709.87) * mm, "end": v(1587.59, -11610.4) * mm});
            skLineSegment(sketch, "E5778", {"start": v(1587.59, -11610.4) * mm, "end": v(1598.93, -11507.15) * mm});
            skLineSegment(sketch, "E5779", {"start": v(1598.93, -11507.15) * mm, "end": v(1609.63, -11400.13) * mm});
            skLineSegment(sketch, "E5780", {"start": v(1609.63, -11400.13) * mm, "end": v(1619.67, -11289.35) * mm});
            skLineSegment(sketch, "E5781", {"start": v(1619.67, -11289.35) * mm, "end": v(1629.07, -11174.83) * mm});
            skLineSegment(sketch, "E5782", {"start": v(1629.07, -11174.83) * mm, "end": v(1637.82, -11056.55) * mm});
            skLineSegment(sketch, "E5783", {"start": v(1637.82, -11056.55) * mm, "end": v(1645.92, -10934.55) * mm});
            skLineSegment(sketch, "E5784", {"start": v(1645.92, -10934.55) * mm, "end": v(1653.38, -10808.81) * mm});
            skLineSegment(sketch, "E5785", {"start": v(1653.38, -10808.81) * mm, "end": v(1660.19, -10679.36) * mm});
            skLineSegment(sketch, "E5786", {"start": v(1660.19, -10679.36) * mm, "end": v(1666.34, -10546.2) * mm});
            skLineSegment(sketch, "E5787", {"start": v(1666.34, -10546.2) * mm, "end": v(1671.85, -10409.33) * mm});
            skLineSegment(sketch, "E5788", {"start": v(1671.85, -10409.33) * mm, "end": v(1676.71, -10268.76) * mm});
            skLineSegment(sketch, "E5789", {"start": v(1676.71, -10268.76) * mm, "end": v(1680.93, -10124.52) * mm});
            skLineSegment(sketch, "E5790", {"start": v(1680.93, -10124.52) * mm, "end": v(1684.5, -9976.59) * mm});
            skLineSegment(sketch, "E5791", {"start": v(1684.5, -9976.59) * mm, "end": v(1687.41, -9824.99) * mm});
            skLineSegment(sketch, "E5792", {"start": v(1687.41, -9824.99) * mm, "end": v(1689.68, -9669.73) * mm});
            skLineSegment(sketch, "E5793", {"start": v(1689.68, -9669.73) * mm, "end": v(1691.3, -9510.82) * mm});
            skLineSegment(sketch, "E5794", {"start": v(1691.3, -9510.82) * mm, "end": v(1692.27, -9348.25) * mm});
            skLineSegment(sketch, "E5795", {"start": v(1692.27, -9348.25) * mm, "end": v(1692.6, -9182.06) * mm});
            skLineSegment(sketch, "E5796", {"start": v(1692.6, -9182.06) * mm, "end": v(1692.6, -77.44) * mm});
            skLineSegment(sketch, "E5797", {"start": v(1692.6, -77.44) * mm, "end": v(1692.6, 9027.18) * mm});
            skSolve(sketch);
        }
        {
            var Q0;
            Q0=makeQuery(id+"F0.imprint","IMPRINT",FACE,{"disambiguationData":[TD([[makeQuery(id+"F0.imprint","IMPRINT",EDGE,{"derivedFrom":sQuery(id+"F0.wireOp",EDGE,"E2549")}),-1.0]])]});
            extrude(context, id + "F1", {"entities" : qUnion([Q0]), "depth" : 100 * mm});
        }
    });
